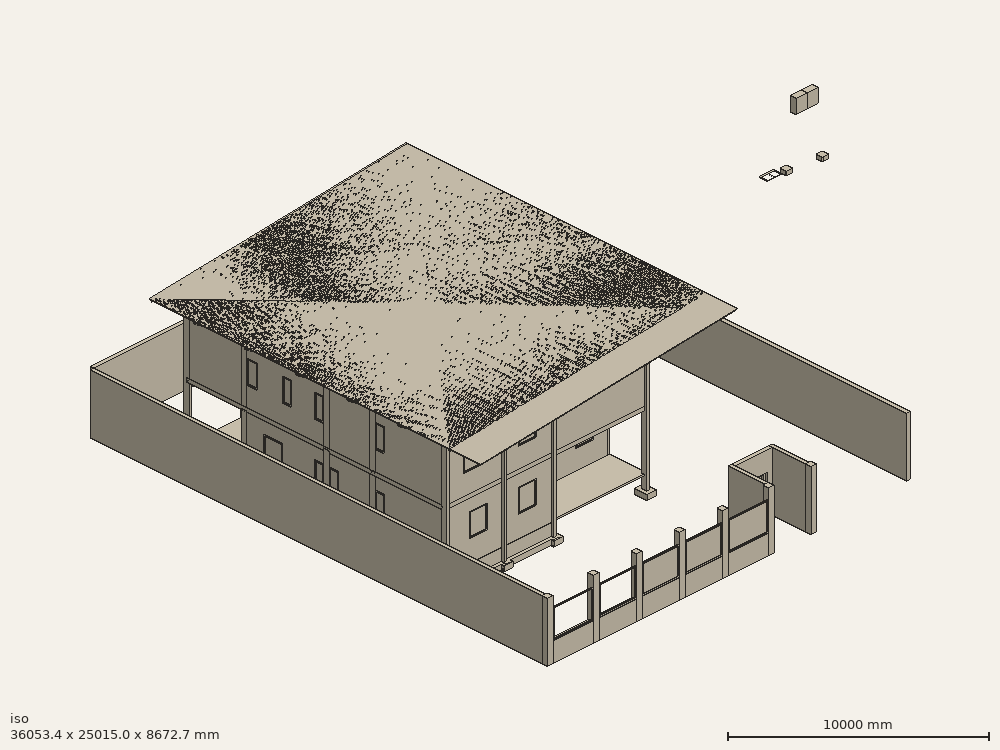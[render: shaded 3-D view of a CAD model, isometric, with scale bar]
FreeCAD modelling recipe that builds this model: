
FCSTD DOCUMENT  (FreeCAD 0.16R5937 (Git))
Label: Dyimba Construction Document test
License: All rights reserved
LicenseURL: http://en.wikipedia.org/wiki/All_rights_reserved
objects: Part::Part2DObjectPython×1218, App::FeaturePython×485, Part::FeaturePython×369, Part::Feature×198, App::DocumentObjectGroup×80, Part::Extrusion×48, Sketcher::SketchObject×44, Drawing::FeatureViewPython×33, App::Annotation×30, Part::Cut×9, Part::MultiFuse×5, Image::ImagePlane×1, App::DocumentObjectGroupPython×1, Drawing::FeaturePage×1
note: 1904 computed .brp shape members not serialized (recipe doc carries the construction recipe); baked Part::Feature solids carry a one-line shape summary decoded from their .brp

FEATURE [App::FeaturePython] Axes  # WARN: FeaturePython — macro-defined, semantics opaque (R4)
  Angles = [0,0,0,0,0]
  Distances = [70,3100,1350,1350,5050]
  Length = 17000
FEATURE [App::FeaturePython] Axes001  # WARN: FeaturePython — macro-defined, semantics opaque (R4)
  Angles = [0,0,0,0,0]
  Distances = [0,3130,4470,2500,3900]
  Length = 15000
  Placement = pos=(-2000,16000,0) rot=(0,0,-1;1.5708rad)
FEATURE [Part::FeaturePython] Structure  # WARN: FeaturePython — macro-defined, semantics opaque (R4)
  Height = 6700
  Length = 150
  MoveWithHost = false
  Nodes = (2) [(0,0,0),(0,0,6700)]
  Normal = (0,0,0)
  Placement = pos=(70,16000,-700) rot=(0,0,1;0rad)
  Role = 1
  Width = 300
FEATURE [Part::FeaturePython] Structure001  # WARN: FeaturePython — macro-defined, semantics opaque (R4)
  Height = 6700
  Length = 150
  MoveWithHost = false
  Nodes = (2) [(0,0,0),(0,0,6700)]
  Normal = (0,0,0)
  Placement = pos=(3170,16000,-700) rot=(0,0,1;0rad)
  Role = 1
  Width = 300
FEATURE [Part::FeaturePython] Structure002  # WARN: FeaturePython — macro-defined, semantics opaque (R4)
  Height = 6700
  Length = 150
  MoveWithHost = false
  Nodes = (2) [(0,0,0),(0,0,6700)]
  Normal = (0,0,0)
  Placement = pos=(5870,16000,-700) rot=(0,0,1;0rad)
  Role = 1
  Width = 300
FEATURE [Part::FeaturePython] Structure003  # WARN: FeaturePython — macro-defined, semantics opaque (R4)
  Height = 6700
  Length = 150
  MoveWithHost = false
  Nodes = (2) [(0,0,0),(0,0,6700)]
  Normal = (0,0,0)
  Placement = pos=(10920,16000,-700) rot=(0,0,1;0rad)
  Role = 1
  Width = 300
FEATURE [Part::FeaturePython] Structure016  # WARN: FeaturePython — macro-defined, semantics opaque (R4)
  Height = 6700
  Length = 150
  MoveWithHost = false
  Nodes = (2) [(0,0,0),(0,0,6700)]
  Normal = (0,0,0)
  Placement = pos=(70,5900,-700) rot=(0,0,1;0rad)
  Role = 1
  Width = 300
FEATURE [Part::FeaturePython] Structure019  # WARN: FeaturePython — macro-defined, semantics opaque (R4)
  Height = 6700
  Length = 150
  MoveWithHost = false
  Nodes = (2) [(0,0,0),(0,0,6700)]
  Normal = (0,0,0)
  Placement = pos=(10920,5900,-700) rot=(0,0,1;0rad)
  Role = 1
  Width = 300
FEATURE [Part::FeaturePython] Structure018  # WARN: FeaturePython — macro-defined, semantics opaque (R4)
  Height = 6700
  Length = 150
  MoveWithHost = false
  Nodes = (2) [(0,0,0),(0,0,6700)]
  Normal = (0,0,0)
  Placement = pos=(5870,5900,-700) rot=(0,0,1;0rad)
  Role = 1
  Width = 300
FEATURE [Part::FeaturePython] Structure020  # WARN: FeaturePython — macro-defined, semantics opaque (R4)
  Height = 6700
  Length = 150
  MoveWithHost = false
  Nodes = (2) [(0,0,0),(0,0,6700)]
  Normal = (0,0,0)
  Placement = pos=(70,2000,-700) rot=(0,0,1;0rad)
  Role = 1
  Width = 300
FEATURE [Part::FeaturePython] Structure021  # WARN: FeaturePython — macro-defined, semantics opaque (R4)
  Height = 6700
  Length = 150
  MoveWithHost = false
  Nodes = (2) [(0,0,0),(0,0,6700)]
  Normal = (0,0,0)
  Placement = pos=(10920,2000,-700) rot=(0,0,1;0rad)
  Role = 1
  Width = 300
FEATURE [Part::FeaturePython] Structure022  # WARN: FeaturePython — macro-defined, semantics opaque (R4)
  Height = 6700
  Length = 150
  MoveWithHost = false
  Nodes = (2) [(0,0,0),(0,0,6700)]
  Normal = (0,0,0)
  Placement = pos=(5870,2000,-700) rot=(0,0,1;0rad)
  Role = 1
  Width = 300
FEATURE [Part::FeaturePython] Structure023  # WARN: FeaturePython — macro-defined, semantics opaque (R4)
  Height = 6700
  Length = 150
  MoveWithHost = false
  Nodes = (2) [(0,0,0),(0,0,6700)]
  Normal = (0,0,0)
  Placement = pos=(3170,2000,-700) rot=(0,0,1;0rad)
  Role = 1
  Width = 300
FEATURE [Part::FeaturePython] Structure024  # WARN: FeaturePython — macro-defined, semantics opaque (R4)
  Height = 6700
  Length = 150
  MoveWithHost = false
  Nodes = (2) [(0,0,0),(0,0,6700)]
  Normal = (0,0,0)
  Placement = pos=(70,8400,-700) rot=(0,0,1;0rad)
  Role = 1
  Width = 300
FEATURE [Part::FeaturePython] Structure025  # WARN: FeaturePython — macro-defined, semantics opaque (R4)
  Height = 6700
  Length = 150
  MoveWithHost = false
  Nodes = (2) [(0,0,0),(0,0,6700)]
  Normal = (0,0,0)
  Placement = pos=(10920,8400,-700) rot=(0,0,1;0rad)
  Role = 1
  Width = 300
FEATURE [Part::FeaturePython] Structure026  # WARN: FeaturePython — macro-defined, semantics opaque (R4)
  Height = 6700
  Length = 150
  MoveWithHost = false
  Nodes = (2) [(0,0,0),(0,0,6700)]
  Normal = (0,0,0)
  Placement = pos=(5870,8400,-700) rot=(0,0,1;0rad)
  Role = 1
  Width = 300
FEATURE [Part::FeaturePython] Structure027  # WARN: FeaturePython — macro-defined, semantics opaque (R4)
  Height = 6700
  Length = 150
  MoveWithHost = false
  Nodes = (2) [(0,0,0),(0,0,6700)]
  Normal = (0,0,0)
  Placement = pos=(4520,8400,-700) rot=(0,0,1;0rad)
  Role = 1
  Width = 300
FEATURE [Part::FeaturePython] Structure028  # WARN: FeaturePython — macro-defined, semantics opaque (R4)
  Height = 6700
  Length = 150
  MoveWithHost = false
  Nodes = (2) [(0,0,0),(0,0,6700)]
  Normal = (0,0,0)
  Placement = pos=(70,12870,-700) rot=(0,0,1;0rad)
  Role = 1
  Width = 300
FEATURE [Part::FeaturePython] Structure029  # WARN: FeaturePython — macro-defined, semantics opaque (R4)
  Height = 6700
  Length = 150
  MoveWithHost = false
  Nodes = (2) [(0,0,0),(0,0,6700)]
  Normal = (0,0,0)
  Placement = pos=(10920,12870,-700) rot=(0,0,1;0rad)
  Role = 1
  Width = 300
FEATURE [Part::FeaturePython] Structure030  # WARN: FeaturePython — macro-defined, semantics opaque (R4)
  Height = 6700
  Length = 150
  MoveWithHost = false
  Nodes = (2) [(0,0,0),(0,0,6700)]
  Normal = (0,0,0)
  Placement = pos=(5870,12870,-700) rot=(0,0,1;0rad)
  Role = 1
  Width = 300
FEATURE [Part::FeaturePython] Structure031  # WARN: FeaturePython — macro-defined, semantics opaque (R4)
  Height = 6700
  Length = 150
  MoveWithHost = false
  Nodes = (2) [(0,0,0),(0,0,6700)]
  Normal = (0,0,0)
  Placement = pos=(4520,12870,-700) rot=(0,0,1;0rad)
  Role = 1
  Width = 300
FEATURE [App::DocumentObjectGroup] Group  label="A-Columns"
  Group = -> [Structure,Structure001,Structure002,Structure003,Structure016,Structure018,Structure019,Structure020,Structure021,Structure022,Structure023,Structure024,Structure025,Structure026,Structure027,Structure028,Structure029,Structure030,Structure031]
FEATURE [Part::Part2DObjectPython] Line  # Draft 2D object (typed FeaturePython)
  ChamferSize = 0
  Closed = false
  End = (10845,16000,0)
  FilletRadius = 0
  Length = 4900
  MakeFace = true
  Points = (2) [(5945,16000,0),(10845,16000,0)]
  Start = (5945,16000,0)
FEATURE [Part::Part2DObjectPython] Line001  # Draft 2D object (typed FeaturePython)
  ChamferSize = 0
  Closed = false
  End = (5795,16000,-100)
  FilletRadius = 0
  Length = 2550
  MakeFace = true
  Placement = pos=(0,0,-100) rot=(0,0,1;0rad)
  Points = (2) [(3245,16000,0),(5795,16000,0)]
  Start = (3245,16000,-100)
FEATURE [Part::Part2DObjectPython] Line002  # Draft 2D object (typed FeaturePython)
  ChamferSize = 0
  Closed = false
  End = (10920,15850,0)
  FilletRadius = 0
  Length = 2830
  MakeFace = true
  Points = (2) [(10920,13020,0),(10920,15850,0)]
  Start = (10920,13020,0)
FEATURE [Part::Part2DObjectPython] Line003  # Draft 2D object (typed FeaturePython)
  ChamferSize = 0
  Closed = false
  End = (10920,12720,0)
  FilletRadius = 0
  Length = 4170
  MakeFace = true
  Points = (2) [(10920,8550,0),(10920,12720,0)]
  Start = (10920,8550,0)
FEATURE [Part::Part2DObjectPython] Line005  # Draft 2D object (typed FeaturePython)
  ChamferSize = 0
  Closed = false
  End = (10920,5750,-100)
  FilletRadius = 0
  Length = 1750.39
  MakeFace = true
  Placement = pos=(0,0,-100) rot=(0,0,1;0rad)
  Points = (2) [(10920,3999.61,0),(10920,5750,0)]
  Start = (10920,3999.61,-100)
FEATURE [Part::Part2DObjectPython] Line007  # Draft 2D object (typed FeaturePython)
  ChamferSize = 0
  Closed = false
  End = (3095,2000,0)
  FilletRadius = 0
  Length = 2950
  MakeFace = true
  Points = (2) [(145,2000,0),(3095,2000,0)]
  Start = (145,2000,0)
FEATURE [Part::Part2DObjectPython] Line008  # Draft 2D object (typed FeaturePython)
  ChamferSize = 0
  Closed = false
  End = (3170,2150,-100)
  FilletRadius = 0
  Length = 3600
  MakeFace = true
  Placement = pos=(0,0,-100) rot=(0,0,1;0rad)
  Points = (2) [(3170,5750,0),(3170,2150,0)]
  Start = (3170,5750,-100)
FEATURE [Part::Part2DObjectPython] Line009  # Draft 2D object (typed FeaturePython)
  ChamferSize = 0
  Closed = false
  End = (5870,2150,3000)
  FilletRadius = 0
  Length = 3600
  MakeFace = true
  Points = (2) [(5870,5750,3000),(5870,2150,3000)]
  Start = (5870,5750,3000)
FEATURE [Part::Part2DObjectPython] Line010  # Draft 2D object (typed FeaturePython)
  ChamferSize = 0
  Closed = false
  End = (3245,2000,3000)
  FilletRadius = 0
  Length = 2550
  MakeFace = true
  Placement = pos=(0,-1000,0) rot=(0,0,1;0rad)
  Points = (2) [(5795,3000,3000),(3245,3000,3000)]
  Start = (5795,2000,3000)
FEATURE [Part::Part2DObjectPython] Line011  # Draft 2D object (typed FeaturePython)
  ChamferSize = 0
  Closed = false
  End = (10845,2000,-100)
  FilletRadius = 0
  Length = 4900
  MakeFace = true
  Placement = pos=(0,0,-100) rot=(0,0,1;0rad)
  Points = (2) [(5945,2000,0),(10845,2000,0)]
  Start = (5945,2000,-100)
FEATURE [Part::Part2DObjectPython] Line013  # Draft 2D object (typed FeaturePython)
  ChamferSize = 0
  Closed = false
  End = (70,5750,0)
  FilletRadius = 0
  Length = 3600
  MakeFace = true
  Placement = pos=(-10850,0,-3172.19) rot=(0,0,1;0rad)
  Points = (2) [(10920,2150,3172.19),(10920,5750,3172.19)]
  Start = (70,2150,0)
FEATURE [Part::Part2DObjectPython] Line014  # Draft 2D object (typed FeaturePython)
  ChamferSize = 0
  Closed = false
  End = (70,6050,0)
  FilletRadius = 0
  Length = 2200
  MakeFace = true
  Placement = pos=(-10850,0,-3172.19) rot=(0,0,1;0rad)
  Points = (2) [(10920,8250,3172.19),(10920,6050,3172.19)]
  Start = (70,8250,0)
FEATURE [Part::Part2DObjectPython] Line015  # Draft 2D object (typed FeaturePython)
  ChamferSize = 0
  Closed = false
  End = (70,12720,0)
  FilletRadius = 0
  Length = 4170
  MakeFace = true
  Placement = pos=(-10850,0,-3172.19) rot=(0,0,1;0rad)
  Points = (2) [(10920,8550,3172.19),(10920,12720,3172.19)]
  Start = (70,8550,0)
FEATURE [Part::Part2DObjectPython] Line016  # Draft 2D object (typed FeaturePython)
  ChamferSize = 0
  Closed = false
  End = (10845,11850,3000)
  FilletRadius = 0
  Length = 3550
  MakeFace = true
  Placement = pos=(0,-1020,3000) rot=(0,0,1;0rad)
  Points = (2) [(7295,12870,0),(10845,12870,0)]
  Start = (7295,11850,3000)
FEATURE [Part::Part2DObjectPython] Line017  # Draft 2D object (typed FeaturePython)
  ChamferSize = 0
  Closed = false
  End = (4595,12870,-100)
  FilletRadius = 0
  Length = 1200
  MakeFace = true
  Placement = pos=(0,0,-100) rot=(0,0,1;0rad)
  Points = (2) [(5795,12870,0),(4595,12870,0)]
  Start = (5795,12870,-100)
FEATURE [Part::Part2DObjectPython] Line018  # Draft 2D object (typed FeaturePython)
  ChamferSize = 0
  Closed = false
  End = (4520,15350,3000)
  FilletRadius = 0
  Length = 500
  MakeFace = true
  Points = (2) [(4520,15850,3000),(4520,15350,3000)]
  Start = (4520,15850,3000)
FEATURE [Part::Part2DObjectPython] Line019  # Draft 2D object (typed FeaturePython)
  ChamferSize = 0
  Closed = false
  End = (145,12000,3000)
  FilletRadius = 0
  Length = 4300
  MakeFace = true
  Placement = pos=(0,-870,3000) rot=(0,0,1;0rad)
  Points = (2) [(4445,12870,0),(145,12870,0)]
  Start = (4445,12000,3000)
FEATURE [Part::Part2DObjectPython] Line022  # Draft 2D object (typed FeaturePython)
  ChamferSize = 0
  Closed = false
  End = (145,9600,0)
  FilletRadius = 0
  Length = 4300
  MakeFace = true
  Placement = pos=(0,50,0) rot=(0,0,1;0rad)
  Points = (2) [(4445,9550,0),(145,9550,0)]
  Start = (4445,9600,0)
FEATURE [Part::FeaturePython] Wall004  # WARN: FeaturePython — macro-defined, semantics opaque (R4)
  Align = 2
  Base = -> Line005
  Face = 0
  Height = 2900
  Length = 0
  MoveWithHost = false
  Normal = (0,0,0)
  Role = 0
  Width = 150
FEATURE [Part::FeaturePython] Wall013  # WARN: FeaturePython — macro-defined, semantics opaque (R4)
  Align = 0
  Base = -> Line017
  Face = 0
  Height = 2800
  Length = 0
  MoveWithHost = false
  Normal = (0,0,0)
  Role = 0
  Width = 150
FEATURE [Part::FeaturePython] Wall015  # WARN: FeaturePython — macro-defined, semantics opaque (R4)
  Align = 0
  Base = -> Line001
  Face = 0
  Height = 2900
  Length = 0
  MoveWithHost = false
  Normal = (0,0,0)
  Role = 0
  Width = 150
FEATURE [Part::Part2DObjectPython] Line025  # Draft 2D object (typed FeaturePython)
  ChamferSize = 0
  Closed = false
  End = (8945,13020,-100)
  FilletRadius = 0
  Length = 2830
  MakeFace = true
  Placement = pos=(0,0,2900) rot=(0,0,1;0rad)
  Points = (2) [(8945,15850,-3000),(8945,13020,-3000)]
  Start = (8945,15850,-100)
FEATURE [Part::FeaturePython] Wall027  # WARN: FeaturePython — macro-defined, semantics opaque (R4)
  Align = 2
  Base = -> Line014
  Face = 0
  Height = 2800
  Length = 0
  MoveWithHost = false
  Normal = (0,0,0)
  Placement = pos=(0,0,3000) rot=(0,0,1;0rad)
  Role = 0
  Width = 150
FEATURE [Part::FeaturePython] Wall028  # WARN: FeaturePython — macro-defined, semantics opaque (R4)
  Align = 2
  Base = -> Line009
  Face = 0
  Height = 2800
  Length = 0
  MoveWithHost = false
  Normal = (0,0,0)
  Role = 0
  Width = 150
FEATURE [Part::FeaturePython] Wall033  # WARN: FeaturePython — macro-defined, semantics opaque (R4)
  Align = 2
  Base = -> Line018
  Face = 0
  Height = 2800
  Length = 0
  MoveWithHost = false
  Normal = (0,0,0)
  Role = 0
  Width = 150
FEATURE [Part::FeaturePython] Wall034  # WARN: FeaturePython — macro-defined, semantics opaque (R4)
  Align = 0
  Base = -> Line022
  Face = 0
  Height = 2800
  Length = 0
  MoveWithHost = false
  Normal = (0,0,0)
  Placement = pos=(0,0,3000) rot=(0,0,1;0rad)
  Role = 0
  Width = 150
FEATURE [Part::FeaturePython] Wall035  # WARN: FeaturePython — macro-defined, semantics opaque (R4)
  Align = 0
  Base = -> Line016
  Face = 0
  Height = 2800
  Length = 0
  MoveWithHost = false
  Normal = (0,0,0)
  Role = 0
  Width = 150
FEATURE [Part::Part2DObjectPython] Line027  # Draft 2D object (typed FeaturePython)
  ChamferSize = 0
  Closed = false
  End = (5795,5900,3000)
  FilletRadius = 0
  Length = 1200
  MakeFace = true
  Points = (2) [(4595,5900,3000),(5795,5900,3000)]
  Start = (4595,5900,3000)
FEATURE [Part::FeaturePython] Wall045  # WARN: FeaturePython — macro-defined, semantics opaque (R4)
  Align = 1
  Base = -> Line027
  Face = 0
  Height = 2800
  Length = 0
  MoveWithHost = false
  Normal = (0,0,0)
  Role = 0
  Width = 150
FEATURE [Part::Part2DObjectPython] Line028  # Draft 2D object (typed FeaturePython)
  ChamferSize = 0
  Closed = false
  End = (10845,5900,3000)
  FilletRadius = 0
  Length = 4900
  MakeFace = true
  Points = (2) [(5945,5900,3000),(10845,5900,3000)]
  Start = (5945,5900,3000)
FEATURE [Part::Part2DObjectPython] Line029  # Draft 2D object (typed FeaturePython)
  ChamferSize = 0
  Closed = false
  End = (70,13020,3000)
  FilletRadius = 0
  Length = 2830
  MakeFace = true
  Points = (2) [(70,15850,3000),(70,13020,3000)]
  Start = (70,15850,3000)
FEATURE [Part::Part2DObjectPython] Line030  # Draft 2D object (typed FeaturePython)
  ChamferSize = 0
  Closed = false
  End = (145,16000,3000)
  FilletRadius = 0
  Length = 2950
  MakeFace = true
  Points = (2) [(3095,16000,3000),(145,16000,3000)]
  Start = (3095,16000,3000)
FEATURE [Part::FeaturePython] Wall048  # WARN: FeaturePython — macro-defined, semantics opaque (R4)
  Align = 2
  Base = -> Line029
  Face = 0
  Height = 2800
  Length = 0
  MoveWithHost = false
  Normal = (0,0,0)
  Role = 0
  Width = 150
FEATURE [Part::Part2DObjectPython] Line031  # Draft 2D object (typed FeaturePython)
  ChamferSize = 0
  Closed = false
  End = (3245,16000,3000)
  FilletRadius = 0
  Length = 2550
  MakeFace = true
  Points = (2) [(5795,16000,3000),(3245,16000,3000)]
  Start = (5795,16000,3000)
FEATURE [Part::Part2DObjectPython] Line039  # Draft 2D object (typed FeaturePython)
  ChamferSize = 0
  Closed = false
  End = (10845,10200,3000)
  FilletRadius = 0
  Length = 3550
  MakeFace = true
  Points = (2) [(7295,10200,3000),(10845,10200,3000)]
  Start = (7295,10200,3000)
FEATURE [Part::FeaturePython] Wall051  # WARN: FeaturePython — macro-defined, semantics opaque (R4)
  Align = 0
  Base = -> Line039
  Face = 0
  Height = 2800
  Length = 0
  MoveWithHost = false
  Normal = (0,0,0)
  Role = 0
  Width = 150
FEATURE [Part::Part2DObjectPython] Line040  # Draft 2D object (typed FeaturePython)
  ChamferSize = 0
  Closed = false
  End = (7145,6050,3000)
  FilletRadius = 0
  Length = 9800
  MakeFace = true
  Points = (2) [(7145,15850,3000),(7145,6050,3000)]
  Start = (7145,15850,3000)
FEATURE [Part::Part2DObjectPython] Line041  # Draft 2D object (typed FeaturePython)
  ChamferSize = 0
  Closed = false
  End = (4593.51,8250,3000)
  FilletRadius = 0
  Length = 1201.49
  MakeFace = true
  Points = (2) [(5795,8250,3000),(4593.51,8250,3000)]
  Start = (5795,8250,3000)
FEATURE [Part::Part2DObjectPython] Line042  # Draft 2D object (typed FeaturePython)
  ChamferSize = 0
  Closed = false
  End = (5945,12720,3000)
  FilletRadius = 0
  Length = 4170
  MakeFace = true
  Points = (2) [(5945,8550,3000),(5945,12720,3000)]
  Start = (5945,8550,3000)
FEATURE [Part::FeaturePython] Wall053  # WARN: FeaturePython — macro-defined, semantics opaque (R4)
  Align = 1
  Base = -> Line042
  Face = 0
  Height = 1000
  Length = 0
  MoveWithHost = false
  Normal = (0,0,0)
  Role = 0
  Width = 150
FEATURE [Part::FeaturePython] Wall054  # WARN: FeaturePython — macro-defined, semantics opaque (R4)
  Align = 0
  Base = -> Line041
  Face = 0
  Height = 1000
  Length = 0
  MoveWithHost = false
  Normal = (0,0,0)
  Role = 0
  Width = 150
FEATURE [Part::Part2DObjectPython] Line043  # Draft 2D object (typed FeaturePython)
  ChamferSize = 0
  Closed = false
  End = (2380,4069.81,3000)
  FilletRadius = 0
  Length = 4506.35
  MakeFace = true
  Placement = pos=(-4915,0.305262,0.0001461) rot=(0,0,1;0rad)
  Points = (2) [(7295,8575.86,3000),(7295,4069.51,3000)]
  Start = (2380,8576.17,3000)
FEATURE [Part::Part2DObjectPython] Line047  # Draft 2D object (typed FeaturePython)
  ChamferSize = 0
  Closed = false
  End = (7295,8250,3000)
  FilletRadius = 0
  Length = 600
  MakeFace = true
  Points = (2) [(7895,8250,3000),(7295,8250,3000)]
  Start = (7895,8250,3000)
FEATURE [Part::FeaturePython] Wall055  # WARN: FeaturePython — macro-defined, semantics opaque (R4)
  Align = 0
  Base = -> Line047
  Face = 0
  Height = 2800
  Length = 0
  MoveWithHost = false
  Normal = (0,0,0)
  Role = 0
  Width = 150
FEATURE [Part::Part2DObjectPython] Line048  # Draft 2D object (typed FeaturePython)
  ChamferSize = 0
  Closed = false
  End = (7447.32,11850.3,3000)
  FilletRadius = 0
  Length = 3155.03
  MakeFace = true
  Placement = pos=(-4915,0.305262,0.0001461) rot=(0,0,1;0rad)
  Points = (2) [(9207.29,11850,3000),(12362.3,11850,3000)]
  Start = (4292.29,11850.3,3000)
FEATURE [Part::Part2DObjectPython] Line049  # Draft 2D object (typed FeaturePython)
  ChamferSize = 0
  Closed = false
  End = (8569.45,15850.3,3000)
  FilletRadius = 0
  Length = 4404.97
  MakeFace = true
  Placement = pos=(-4915,0.305262,0.0001461) rot=(0,0,1;0rad)
  Points = (2) [(9079.47,15850,3000),(13484.4,15850,3000)]
  Start = (4164.47,15850.3,3000)
FEATURE [Part::Part2DObjectPython] Line050  # Draft 2D object (typed FeaturePython)
  ChamferSize = 0
  Closed = false
  End = (8569.45,13650.3,3000)
  FilletRadius = 0
  Length = 4404.97
  MakeFace = true
  Placement = pos=(-4915,0.305262,0.0001461) rot=(0,0,1;0rad)
  Points = (2) [(9079.47,13650,3000),(13484.4,13650,3000)]
  Start = (4164.47,13650.3,3000)
FEATURE [Part::Part2DObjectPython] Line023  # Draft 2D object (typed FeaturePython)
  ChamferSize = 0
  Closed = false
  End = (4520,12720,3000)
  FilletRadius = 0
  Length = 4170
  MakeFace = true
  Points = (2) [(4520,8550,3000),(4520,12720,3000)]
  Start = (4520,8550,3000)
FEATURE [Part::FeaturePython] Wall029  # WARN: FeaturePython — macro-defined, semantics opaque (R4)
  Align = 2
  Base = -> Line023
  Face = 0
  Height = 2800
  Length = 0
  MoveWithHost = false
  Normal = (0,0,0)
  Role = 0
  Width = 150
FEATURE [Part::Part2DObjectPython] Line052  # Draft 2D object (typed FeaturePython)
  ChamferSize = 0
  Closed = false
  End = (4595,8250,3000)
  FilletRadius = 0
  Length = 2350
  MakeFace = true
  Points = (2) [(4595,5900,3000),(4595,8250,3000)]
  Start = (4595,5900,3000)
FEATURE [Part::Part2DObjectPython] Line057  # Draft 2D object (typed FeaturePython)
  ChamferSize = 0
  Closed = false
  End = (-6976.01,12000.3,3000)
  FilletRadius = 0
  Length = 3334.15
  MakeFace = true
  Placement = pos=(-4915,0.305262,0.0001461) rot=(0,0,1;0rad)
  Points = (2) [(1273.13,12000,3000),(-2061.02,12000,3000)]
  Start = (-3641.87,12000.3,3000)
FEATURE [Part::Part2DObjectPython] Line058  # Draft 2D object (typed FeaturePython)
  ChamferSize = 0
  Closed = false
  End = (-6976.01,11400.3,3000)
  FilletRadius = 0
  Length = 7145.96
  MakeFace = true
  Placement = pos=(-4915,0.305262,0.0001461) rot=(0,0,1;0rad)
  Points = (2) [(5084.95,11400,3000),(-2061.02,11400,3000)]
  Start = (169.949,11400.3,3000)
FEATURE [Part::Part2DObjectPython] Line059  # Draft 2D object (typed FeaturePython)
  ChamferSize = 0
  Closed = false
  End = (3170,12000,3000)
  FilletRadius = 0
  Length = 600
  MakeFace = true
  Points = (2) [(3170,11400,3000),(3170,12000,3000)]
  Start = (3170,11400,3000)
FEATURE [Part::FeaturePython] Wall058  # WARN: FeaturePython — macro-defined, semantics opaque (R4)
  Align = 1
  Base = -> Line059
  Face = 0
  Height = 2800
  Length = 0
  MoveWithHost = false
  Normal = (0,0,0)
  Role = 0
  Width = 150
FEATURE [Part::Part2DObjectPython] Line060  # Draft 2D object (typed FeaturePython)
  ChamferSize = 0
  Closed = false
  End = (10845,12870,-100)
  FilletRadius = 0
  Length = 4900
  MakeFace = true
  Placement = pos=(0,0,-100) rot=(0,0,1;0rad)
  Points = (2) [(5945,12870,0),(10845,12870,0)]
  Start = (5945,12870,-100)
FEATURE [Part::Part2DObjectPython] Line061  # Draft 2D object (typed FeaturePython)
  ChamferSize = 0
  Closed = false
  End = (5930,16814.6,0.0001461)
  FilletRadius = 0
  Length = 2358.9
  MakeFace = true
  Placement = pos=(-4915,0.305262,0.0001461) rot=(0,0,1;0rad)
  Points = (2) [(10845,14455.4,0),(10845,16814.3,0)]
  Start = (5930,14455.7,0.0001461)
FEATURE [Part::Part2DObjectPython] Line062  # Draft 2D object (typed FeaturePython)
  ChamferSize = 0
  Closed = false
  End = (4520,15850,-100)
  FilletRadius = 0
  Length = 2830
  MakeFace = true
  Placement = pos=(0,0,-100) rot=(0,0,1;0rad)
  Points = (2) [(4520,13020,0),(4520,15850,0)]
  Start = (4520,13020,-100)
FEATURE [Part::Part2DObjectPython] Line063  # Draft 2D object (typed FeaturePython)
  ChamferSize = 0
  Closed = false
  End = (4520,12720,-100)
  FilletRadius = 0
  Length = 4170
  MakeFace = true
  Placement = pos=(0,0,-100) rot=(0,0,1;0rad)
  Points = (2) [(4520,8550,0),(4520,12720,0)]
  Start = (4520,8550,-100)
FEATURE [Part::FeaturePython] Wall062  # WARN: FeaturePython — macro-defined, semantics opaque (R4)
  Align = 2
  Base = -> Line063
  Face = 0
  Height = 2900
  Length = 0
  MoveWithHost = false
  Normal = (0,0,0)
  Role = 0
  Width = 150
FEATURE [Part::Part2DObjectPython] Line064  # Draft 2D object (typed FeaturePython)
  ChamferSize = 0
  Closed = false
  End = (3170,9600,-100)
  FilletRadius = 0
  Length = 4850
  MakeFace = true
  Placement = pos=(0,0,-100) rot=(0,0,1;0rad)
  Points = (2) [(3170,4750,0),(3170,9600,0)]
  Start = (3170,4750,-100)
FEATURE [Part::Part2DObjectPython] Line065  # Draft 2D object (typed FeaturePython)
  ChamferSize = 0
  Closed = false
  End = (-6252.85,2150.31,0.0001461)
  FilletRadius = 0
  Length = 2264.08
  MakeFace = true
  Placement = pos=(-4915,0.305262,0.0001461) rot=(0,0,1;0rad)
  Points = (2) [(926.23,2150,0),(-1337.85,2150,0)]
  Start = (-3988.77,2150.31,0.0001461)
FEATURE [Part::Part2DObjectPython] Line066  # Draft 2D object (typed FeaturePython)
  ChamferSize = 0
  Closed = false
  End = (-6252.85,6500.31,0.0001461)
  FilletRadius = 0
  Length = 2264.08
  MakeFace = true
  Placement = pos=(-4915,0.305262,0.0001461) rot=(0,0,1;0rad)
  Points = (2) [(926.23,6500,0),(-1337.85,6500,0)]
  Start = (-3988.77,6500.31,0.0001461)
FEATURE [Part::Part2DObjectPython] Line067  # Draft 2D object (typed FeaturePython)
  ChamferSize = 0
  Closed = false
  End = (3095,6500,-100)
  FilletRadius = 0
  Length = 2950
  MakeFace = true
  Placement = pos=(0,0,-100) rot=(0,0,1;0rad)
  Points = (2) [(145,6500,0),(3095,6500,0)]
  Start = (145,6500,-100)
FEATURE [Part::Part2DObjectPython] Line068  # Draft 2D object (typed FeaturePython)
  ChamferSize = 0
  Closed = false
  End = (3095,8250,-100)
  FilletRadius = 0
  Length = 2950
  MakeFace = true
  Placement = pos=(0,0,-100) rot=(0,0,1;0rad)
  Points = (2) [(145,8250,0),(3095,8250,0)]
  Start = (145,8250,-100)
FEATURE [Part::FeaturePython] Wall065  # WARN: FeaturePython — macro-defined, semantics opaque (R4)
  Align = 1
  Base = -> Line068
  Face = 0
  Height = 2900
  Length = 0
  MoveWithHost = false
  Normal = (0,0,0)
  Role = 0
  Width = 150
FEATURE [Part::Part2DObjectPython] Line069  # Draft 2D object (typed FeaturePython)
  ChamferSize = 0
  Closed = false
  End = (-6633.63,8400.31,0.0001461)
  FilletRadius = 0
  Length = 3259.04
  MakeFace = true
  Placement = pos=(-4915,0.305262,0.0001461) rot=(0,0,1;0rad)
  Points = (2) [(1540.41,8400,0),(-1718.63,8400,0)]
  Start = (-3374.59,8400.31,0.0001461)
FEATURE [Part::Part2DObjectPython] Line070  # Draft 2D object (typed FeaturePython)
  ChamferSize = 0
  Closed = false
  End = (-6633.63,9600.31,0.0001461)
  FilletRadius = 0
  Length = 1863.63
  MakeFace = true
  Placement = pos=(-4915,0.305262,0.0001461) rot=(0,0,1;0rad)
  Points = (2) [(145,9600,0),(-1718.63,9600,0)]
  Start = (-4770,9600.31,0.0001461)
FEATURE [Part::Part2DObjectPython] Line071  # Draft 2D object (typed FeaturePython)
  ChamferSize = 0
  Closed = false
  End = (4445,9600,-100)
  FilletRadius = 0
  Length = 4300
  MakeFace = true
  Placement = pos=(0,0,-100) rot=(0,0,1;0rad)
  Points = (2) [(145,9600,0),(4445,9600,0)]
  Start = (145,9600,-100)
FEATURE [Part::Part2DObjectPython] Line072  # Draft 2D object (typed FeaturePython)
  ChamferSize = 0
  Closed = false
  End = (145,13020,-100)
  FilletRadius = 0
  Length = 4300
  MakeFace = true
  Placement = pos=(0,0,-100) rot=(0,0,1;0rad)
  Points = (2) [(4445,13020,0),(145,13020,0)]
  Start = (4445,13020,-100)
FEATURE [Part::Part2DObjectPython] Line073  # Draft 2D object (typed FeaturePython)
  ChamferSize = 0
  Closed = false
  End = (5795,3000,-100)
  FilletRadius = 0
  Length = 2550
  MakeFace = true
  Placement = pos=(0,0,-100) rot=(0,0,1;0rad)
  Points = (2) [(3245,3000,0),(5795,3000,0)]
  Start = (3245,3000,-100)
FEATURE [Part::Feature] Mesh
  Placement = pos=(5488.78,8171.39,0) rot=(0,0,1;0rad)
  shape: bbox 1200 x 4502 x 3000 mm, 40 faces (baked)
FEATURE [Part::Part2DObjectPython] Line074  # Draft 2D object (typed FeaturePython)
  ChamferSize = 0
  Closed = false
  End = (145,2000,-100)
  FilletRadius = 0
  Length = 2950
  MakeFace = true
  Placement = pos=(0,0,-100) rot=(0,0,1;0rad)
  Points = (2) [(3095,2000,0),(145,2000,0)]
  Start = (3095,2000,-100)
FEATURE [Part::FeaturePython] Stairs  # WARN: FeaturePython — macro-defined, semantics opaque (R4)
  Align = 0
  Base = -> Mesh
  BlondelRatio = 0
  Height = 3000
  Landings = 0
  Length = 4500
  MoveWithHost = false
  Nosing = 0
  NumberOfSteps = 0
  Placement = pos=(5488.78,8171.39,0) rot=(0,0,1;0rad)
  RiserHeight = 0
  Role = 0
  StringerWidth = 0
  Structure = 0
  StructureOffset = 0
  StructureThickness = 0
  TreadDepth = 0
  TreadThickness = 0
  Width = 1000
  Winders = 0
FEATURE [Part::Part2DObjectPython] Line076  # Draft 2D object (typed FeaturePython)
  ChamferSize = 0
  Closed = false
  End = (70,12720,-100)
  FilletRadius = 0
  Length = 4170
  MakeFace = true
  Placement = pos=(0,0,-100) rot=(0,0,1;0rad)
  Points = (2) [(70,8550,0.180568),(70,12720,0)]
  Start = (70,8550,-99.8194)
FEATURE [Part::Part2DObjectPython] Line077  # Draft 2D object (typed FeaturePython)
  ChamferSize = 0
  Closed = false
  End = (10920,15850,-100)
  FilletRadius = 0
  Length = 2830
  MakeFace = true
  Placement = pos=(0,0,-100) rot=(0,0,1;0rad)
  Points = (2) [(10920,13020,0),(10920,15850,0)]
  Start = (10920,13020,-100)
FEATURE [Part::Part2DObjectPython] Line078  # Draft 2D object (typed FeaturePython)
  ChamferSize = 0
  Closed = false
  End = (5870,5750,-100)
  FilletRadius = 0
  Length = 3600
  MakeFace = true
  Placement = pos=(0,0,-100) rot=(0,0,1;0rad)
  Points = (2) [(5870,2150,0),(5870,5750,0)]
  Start = (5870,2150,-100)
FEATURE [Part::Part2DObjectPython] Line079  # Draft 2D object (typed FeaturePython)
  ChamferSize = 0
  Closed = false
  End = (5945,16000,-100)
  FilletRadius = 0
  Length = 4900
  MakeFace = true
  Placement = pos=(0,0,-100) rot=(0,0,1;0rad)
  Points = (2) [(10845,16000,0),(5945,16000,0)]
  Start = (10845,16000,-100)
FEATURE [Part::Part2DObjectPython] Line080  # Draft 2D object (typed FeaturePython)
  ChamferSize = 0
  Closed = false
  End = (70,5750,-100)
  FilletRadius = 0
  Length = 3600
  MakeFace = true
  Placement = pos=(0,0,-100) rot=(0,0,1;0rad)
  Points = (2) [(70,2150,0),(70,5750,0)]
  Start = (70,2150,-100)
FEATURE [Part::Part2DObjectPython] Line081  # Draft 2D object (typed FeaturePython)
  ChamferSize = 0
  Closed = false
  End = (10920,12720,-100)
  FilletRadius = 0
  Length = 4170
  MakeFace = true
  Placement = pos=(0,0,-100) rot=(0,0,1;0rad)
  Points = (2) [(10920,8550,0),(10920,12720,0)]
  Start = (10920,8550,-100)
FEATURE [Part::Part2DObjectPython] Line082  # Draft 2D object (typed FeaturePython)
  ChamferSize = 0
  Closed = false
  End = (70,8250,-100)
  FilletRadius = 0
  Length = 2200
  MakeFace = true
  Placement = pos=(0,0,-100) rot=(0,0,1;0rad)
  Points = (2) [(70,6050,0),(70,8250,0)]
  Start = (70,6050,-100)
FEATURE [Part::Part2DObjectPython] Line083  # Draft 2D object (typed FeaturePython)
  ChamferSize = 0
  Closed = false
  End = (10845,11850,3000)
  FilletRadius = 0
  Length = 3550
  MakeFace = true
  Points = (2) [(7295,11850,3000),(10845,11850,3000)]
  Start = (7295,11850,3000)
FEATURE [Part::FeaturePython] Wall078  # WARN: FeaturePython — macro-defined, semantics opaque (R4)
  Align = 0
  Base = -> Line083
  Face = 0
  Height = 2800
  Length = 0
  MoveWithHost = false
  Normal = (0,0,0)
  Role = 0
  Width = 150
FEATURE [Part::Part2DObjectPython] Line084  # Draft 2D object (typed FeaturePython)
  ChamferSize = 0
  Closed = false
  End = (6080,-2593.43,0.0001461)
  FilletRadius = 0
  Length = 21220.1
  MakeFace = true
  Placement = pos=(-4915,0.305262,0.0001461) rot=(0,0,1;0rad)
  Points = (2) [(10995,18626.4,0),(10995,-2593.73,0)]
  Start = (6080,18626.7,0.0001461)
FEATURE [Part::Part2DObjectPython] Line085  # Draft 2D object (typed FeaturePython)
  ChamferSize = 0
  Closed = false
  End = (-4920,499.046,0.0001461)
  FilletRadius = 0
  Length = 18816.3
  MakeFace = true
  Placement = pos=(-4915,0.305262,0.0001461) rot=(0,0,1;0rad)
  Points = (2) [(-5,19315,0),(-5,498.741,0)]
  Start = (-4920,19315.3,0.0001461)
FEATURE [Part::Part2DObjectPython] Line086  # Draft 2D object (typed FeaturePython)
  ChamferSize = 0
  Closed = false
  End = (-5909.06,2000.31,0.0001461)
  FilletRadius = 0
  Length = 13580.1
  MakeFace = true
  Placement = pos=(-4915,0.305262,0.0001461) rot=(0,0,1;0rad)
  Points = (2) [(12586,2000,0),(-994.058,2000,0)]
  Start = (7671.03,2000.31,0.0001461)
FEATURE [Part::Part2DObjectPython] Line087  # Draft 2D object (typed FeaturePython)
  ChamferSize = 0
  Closed = false
  End = (8231.98,16000.3,0.0001461)
  FilletRadius = 0
  Length = 16540.6
  MakeFace = true
  Placement = pos=(-4915,0.305262,0.0001461) rot=(0,0,1;0rad)
  Points = (2) [(-3393.63,16000,0),(13147,16000,0)]
  Start = (-8308.63,16000.3,0.0001461)
FEATURE [Part::Part2DObjectPython] Rectangle  # Draft 2D object (typed FeaturePython)
  ChamferSize = 0
  FilletRadius = 0
  Height = -14000
  Length = -11000
  MakeFace = true
  Placement = pos=(10995,16000,3000) rot=(0,0,1;0rad)
FEATURE [Part::Extrusion] Extrusion001  label="level 2 slab"
  Base = -> Rectangle
  Dir = (0,0,-200)
  Solid = true
FEATURE [Part::Part2DObjectPython] Line088  # Draft 2D object (typed FeaturePython)
  ChamferSize = 0
  Closed = false
  End = (-4920,14435.3,0.0001461)
  FilletRadius = 0
  Length = 1565
  MakeFace = true
  Placement = pos=(-4915,0.305262,0.0001461) rot=(0,0,1;0rad)
  Points = (2) [(-5,16000,0),(-5,14435,0)]
  Start = (-4920,16000.3,0.0001461)
FEATURE [Part::Part2DObjectPython] Line089  # Draft 2D object (typed FeaturePython)
  ChamferSize = 0
  Closed = false
  End = (-6915,16000.3,0.0001461)
  FilletRadius = 0
  Length = 3620
  MakeFace = true
  Placement = pos=(-4915,0.305262,0.0001461) rot=(0,0,1;0rad)
  Points = (2) [(1620,16000,0),(-2000,16000,0)]
  Start = (-3295,16000.3,0.0001461)
FEATURE [Part::Part2DObjectPython] Line090  # Draft 2D object (typed FeaturePython)
  ChamferSize = 0
  Closed = false
  End = (880.002,20292.4,3000)
  FilletRadius = 0
  Length = 21199.3
  MakeFace = true
  Placement = pos=(-4915,0.305262,0.0001461) rot=(0,0,1;0rad)
  Points = (2) [(5795,-907.189,3000),(5795,20292.1,3000)]
  Start = (880.002,-906.884,3000)
FEATURE [Part::Part2DObjectPython] Line091  # Draft 2D object (typed FeaturePython)
  ChamferSize = 0
  Closed = false
  End = (-319.998,19324.2,3000)
  FilletRadius = 0
  Length = 18775.6
  MakeFace = true
  Placement = pos=(-4915,0.305262,0.0001461) rot=(0,0,1;0rad)
  Points = (2) [(4595,548.288,3000),(4595,19323.9,3000)]
  Start = (-319.998,548.593,3000)
FEATURE [Part::Part2DObjectPython] Line092  # Draft 2D object (typed FeaturePython)
  ChamferSize = 0
  Closed = false
  End = (-6405.68,13020.3,3000)
  FilletRadius = 0
  Length = 13409.8
  MakeFace = true
  Placement = pos=(-4915,0.305262,0.0001461) rot=(0,0,1;0rad)
  Points = (2) [(11919.1,13020,3000),(-1490.68,13020,3000)]
  Start = (7004.15,13020.3,3000)
FEATURE [Part::Part2DObjectPython] Line093  # Draft 2D object (typed FeaturePython)
  ChamferSize = 0
  Closed = false
  End = (7233.23,8400.31,3000)
  FilletRadius = 0
  Length = 15139.7
  MakeFace = true
  Placement = pos=(-4915,0.305262,0.0001461) rot=(0,0,1;0rad)
  Points = (2) [(-2991.47,8400,3000),(12148.2,8400,3000)]
  Start = (-7906.46,8400.31,3000)
FEATURE [Part::Part2DObjectPython] Rectangle002  # Draft 2D object (typed FeaturePython)
  ChamferSize = 0
  FilletRadius = 0
  Height = -4620
  Length = 1200
  MakeFace = true
  Placement = pos=(4595,13020,3000) rot=(0,0,1;0rad)
FEATURE [Part::Extrusion] Extrusion003
  Base = -> Rectangle002
  Dir = (0,0,-200)
  Solid = true
FEATURE [Part::Cut] Cut  label="Floor Slab level 2"
  Base = -> Extrusion001
  Tool = -> Extrusion003
FEATURE [Part::Part2DObjectPython] Line094  # Draft 2D object (typed FeaturePython)
  ChamferSize = 0
  Closed = false
  End = (10344.7,16000.3,6000)
  FilletRadius = 0
  Length = 18706.8
  MakeFace = true
  Placement = pos=(-4915,0.305262,0.0001461) rot=(0,0,1;0rad)
  Points = (2) [(-3447.1,16000,6000),(15259.7,16000,6000)]
  Start = (-8362.1,16000.3,6000)
FEATURE [Part::Part2DObjectPython] Line095  # Draft 2D object (typed FeaturePython)
  ChamferSize = 0
  Closed = false
  End = (10085,2000.31,6000)
  FilletRadius = 0
  Length = 18000
  MakeFace = true
  Placement = pos=(-4915,0.305262,0.0001461) rot=(0,0,1;0rad)
  Points = (2) [(-3000,2000,6000),(15000,2000,6000)]
  Start = (-7915,2000.31,6000)
FEATURE [Part::Part2DObjectPython] Line097  # Draft 2D object (typed FeaturePython)
  ChamferSize = 0
  Closed = false
  End = (6080,-1999.69,6000)
  FilletRadius = 0
  Length = 20565.3
  MakeFace = true
  Placement = pos=(-4915,0.305262,0.0001461) rot=(0,0,1;0rad)
  Points = (2) [(10995,18565.3,6000),(10995,-2000,6000)]
  Start = (6080,18565.6,6000)
FEATURE [Part::Part2DObjectPython] Line098  # Draft 2D object (typed FeaturePython)
  ChamferSize = 0
  Closed = false
  End = (11657.2,5900.31,6000)
  FilletRadius = 0
  Length = 17589.6
  MakeFace = true
  Placement = pos=(-4915,0.305262,0.0001461) rot=(0,0,1;0rad)
  Points = (2) [(-1017.37,5900,6000),(16572.2,5900,6000)]
  Start = (-5932.37,5900.31,6000)
FEATURE [Part::Part2DObjectPython] Line099  # Draft 2D object (typed FeaturePython)
  ChamferSize = 0
  Closed = false
  End = (1030,-647.56,6000)
  FilletRadius = 0
  Length = 7788.14
  MakeFace = true
  Placement = pos=(-4915,0.305262,0.0001461) rot=(0,0,1;0rad)
  Points = (2) [(5945,7140.27,6000),(5945,-647.865,6000)]
  Start = (1030,7140.58,6000)
FEATURE [Part::Part2DObjectPython] Line100  # Draft 2D object (typed FeaturePython)
  ChamferSize = 0
  Closed = false
  End = (11192.5,2150.31,6000)
  FilletRadius = 0
  Length = 14487.5
  MakeFace = true
  Placement = pos=(-4915,0.305262,0.0001461) rot=(0,0,1;0rad)
  Points = (2) [(1620,2150,6000),(16107.5,2150,6000)]
  Start = (-3295,2150.31,6000)
FEATURE [Part::Part2DObjectPython] Line101  # Draft 2D object (typed FeaturePython)
  ChamferSize = 0
  Closed = false
  End = (5930,-331.374,6000)
  FilletRadius = 0
  Length = 7481.68
  MakeFace = true
  Placement = pos=(-4915,0.305262,0.0001461) rot=(0,0,1;0rad)
  Points = (2) [(10845,7150,6000),(10845,-331.68,6000)]
  Start = (5930,7150.31,6000)
FEATURE [Part::Part2DObjectPython] Rectangle004  # Draft 2D object (typed FeaturePython)
  ChamferSize = 0
  FilletRadius = 0
  Height = -3750
  Length = 4900
  MakeFace = true
  Placement = pos=(5945,5900,6000) rot=(0,0,1;0rad)
FEATURE [Part::Extrusion] Extrusion005
  Base = -> Rectangle004
  Dir = (0,0,-200)
  Solid = true
FEATURE [Part::Part2DObjectPython] Line102  # Draft 2D object (typed FeaturePython)
  ChamferSize = 0
  Closed = false
  End = (-4920,18537.5,6000)
  FilletRadius = 0
  Length = 19254.8
  MakeFace = true
  Placement = pos=(-4915,0.305262,0.0001461) rot=(0,0,1;0rad)
  Points = (2) [(-5,-717.619,6000),(-5,18537.2,6000)]
  Start = (-4920,-717.314,6000)
FEATURE [Part::Part2DObjectPython] Rectangle005  # Draft 2D object (typed FeaturePython)
  ChamferSize = 0
  FilletRadius = 0
  Height = 14000
  Length = 11000
  MakeFace = true
  Placement = pos=(-5,2000,6000) rot=(0,0,1;0rad)
FEATURE [Part::Extrusion] Extrusion006
  Base = -> Rectangle005
  Dir = (0,0,-200)
  Solid = true
FEATURE [Part::Cut] Cut001  label="Roof Slab level 3"
  Base = -> Extrusion006
  Placement = pos=(0.0019531,0.000212966,-3.634e-05) rot=(0,0,1;0rad)
  Tool = -> Extrusion005
FEATURE [Part::Part2DObjectPython] Line105  # Draft 2D object (typed FeaturePython)
  ChamferSize = 0
  Closed = false
  End = (1030,2000.31,3000)
  FilletRadius = 0
  Length = 6000
  MakeFace = true
  Placement = pos=(-4915,0.305262,0.0001461) rot=(0,0,1;0rad)
  Points = (2) [(5945,2000,9000),(5945,2000,3000)]
  Start = (1030,2000.31,9000)
FEATURE [Part::Part2DObjectPython] Line106  # Draft 2D object (typed FeaturePython)
  ChamferSize = 0
  Closed = false
  End = (1030,2150.31,3000)
  FilletRadius = 0
  Length = 6000
  MakeFace = true
  Placement = pos=(-4915,0.305262,0.0001461) rot=(0,0,1;0rad)
  Points = (2) [(5945,2150,9000),(5945,2150,3000)]
  Start = (1030,2150.31,9000)
FEATURE [Part::Part2DObjectPython] Line107  # Draft 2D object (typed FeaturePython)
  ChamferSize = 0
  Closed = false
  End = (1030,1518.67,3000)
  FilletRadius = 0
  Length = 631.638
  MakeFace = true
  Placement = pos=(-4915,0.305262,0.0001461) rot=(0,0,1;0rad)
  Points = (2) [(5945,2150,3000),(5945,1518.36,3000)]
  Start = (1030,2150.31,3000)
FEATURE [Part::Part2DObjectPython] Line108  # Draft 2D object (typed FeaturePython)
  ChamferSize = 0
  Closed = false
  End = (1030,3000.31,4000)
  FilletRadius = 0
  Length = 1000
  MakeFace = true
  Placement = pos=(-4915,0.305262,0.0001461) rot=(0,0,1;0rad)
  Points = (2) [(5945,2000,4000),(5945,3000,4000)]
  Start = (1030,2000.31,4000)
FEATURE [Part::Part2DObjectPython] Line109  # Draft 2D object (typed FeaturePython)
  ChamferSize = 0
  Closed = false
  End = (1030,2150.31,3632.83)
  FilletRadius = 0
  Length = 150
  MakeFace = true
  Placement = pos=(-4915,0.305262,0.0001461) rot=(0,0,1;0rad)
  Points = (2) [(5945,2000,3632.83),(5945,2150,3632.83)]
  Start = (1030,2000.31,3632.83)
FEATURE [Part::Part2DObjectPython] Line110  # Draft 2D object (typed FeaturePython)
  ChamferSize = 0
  Closed = false
  End = (1030,2075.31,4000)
  FilletRadius = 0
  Length = 900
  MakeFace = true
  Placement = pos=(-4915,0.305262,0.0001461) rot=(0,0,1;0rad)
  Points = (2) [(5945,2075,3100),(5945,2075,4000)]
  Start = (1030,2075.31,3100)
FEATURE [Part::Part2DObjectPython] Line111  # Draft 2D object (typed FeaturePython)
  ChamferSize = 0
  Closed = false
  End = (1030,3000.31,3960)
  FilletRadius = 0
  Length = 1000
  MakeFace = true
  Placement = pos=(-4915,0.305262,0.0001461) rot=(0,0,1;0rad)
  Points = (2) [(5945,2000,3960),(5945,3000,3960)]
  Start = (1030,2000.31,3960)
FEATURE [Part::Part2DObjectPython] Line112  # Draft 2D object (typed FeaturePython)
  ChamferSize = 0
  Closed = false
  End = (1030,2075.33,4000)
  FilletRadius = 0
  Length = 367.171
  MakeFace = true
  Placement = pos=(-4915,0.305262,0.0001461) rot=(0,0,1;0rad)
  Points = (2) [(5945,2075.02,3632.83),(5945,2075.02,4000)]
  Start = (1030,2075.33,3632.83)
FEATURE [Part::Part2DObjectPython] Line113  # Draft 2D object (typed FeaturePython)
  ChamferSize = 0
  Closed = false
  End = (1030,2095.31,4000)
  FilletRadius = 0
  Length = 367.171
  MakeFace = true
  Placement = pos=(-4915,0.305262,0.0001461) rot=(0,0,1;0rad)
  Points = (2) [(5945,2095,3632.83),(5945,2095,4000)]
  Start = (1030,2095.31,3632.83)
FEATURE [Part::Part2DObjectPython] Line114  # Draft 2D object (typed FeaturePython)
  ChamferSize = 0
  Closed = false
  End = (1030,2055.31,4000)
  FilletRadius = 0
  Length = 367.171
  MakeFace = true
  Placement = pos=(-4915,0.305262,0.0001461) rot=(0,0,1;0rad)
  Points = (2) [(5945,2055,3632.83),(5945,2055,4000)]
  Start = (1030,2055.31,3632.83)
FEATURE [Part::Part2DObjectPython] Line115  # Draft 2D object (typed FeaturePython)
  ChamferSize = 0
  Closed = false
  End = (1030,1518.67,3100)
  FilletRadius = 0
  Length = 631.638
  MakeFace = true
  Placement = pos=(-4915,0.305262,0.0001461) rot=(0,0,1;0rad)
  Points = (2) [(5945,2150,3100),(5945,1518.36,3100)]
  Start = (1030,2150.31,3100)
FEATURE [Part::Part2DObjectPython] Line116  # Draft 2D object (typed FeaturePython)
  ChamferSize = 0
  Closed = false
  End = (1030,1518.67,3140)
  FilletRadius = 0
  Length = 631.638
  MakeFace = true
  Placement = pos=(-4915,0.305262,0.0001461) rot=(0,0,1;0rad)
  Points = (2) [(5945,2150,3140),(5945,1518.36,3140)]
  Start = (1030,2150.31,3140)
FEATURE [Part::Part2DObjectPython] Rectangle006  # Draft 2D object (typed FeaturePython)
  ChamferSize = 0
  FilletRadius = 0
  Height = -40
  Length = 40
  MakeFace = true
  Placement = pos=(5945,2055,4000) rot=(0.57735,0.57735,0.57735;2.0944rad)
FEATURE [Part::Part2DObjectPython] Rectangle007  # Draft 2D object (typed FeaturePython)
  ChamferSize = 0
  FilletRadius = 0
  Height = -40
  Length = 40
  MakeFace = true
  Placement = pos=(5945,2055,3140) rot=(0.57735,0.57735,0.57735;2.0944rad)
FEATURE [Part::Extrusion] Extrusion007
  Base = -> Rectangle006
  Dir = (4900,0,0)
  Solid = true
FEATURE [Part::Extrusion] Extrusion008
  Base = -> Rectangle007
  Dir = (4900,0,0)
  Solid = true
FEATURE [Part::Part2DObjectPython] Line117  # Draft 2D object (typed FeaturePython)
  ChamferSize = 0
  Closed = false
  End = (5005,2150.31,3000)
  FilletRadius = 0
  Length = 2000
  MakeFace = true
  Placement = pos=(-4915,0.305262,0.0001461) rot=(0,0,1;0rad)
  Points = (2) [(11920,2150,3000),(9920,2150,3000)]
  Start = (7005,2150.31,3000)
FEATURE [Part::Part2DObjectPython] Line118  # Draft 2D object (typed FeaturePython)
  ChamferSize = 0
  Closed = false
  End = (6393.3,2150.31,3100)
  FilletRadius = 0
  Length = 463.293
  MakeFace = true
  Placement = pos=(-4915,0.305262,0.0001461) rot=(0,0,1;0rad)
  Points = (2) [(10845,2150,3100),(11308.3,2150,3100)]
  Start = (5930,2150.31,3100)
FEATURE [Part::Part2DObjectPython] Line119  # Draft 2D object (typed FeaturePython)
  ChamferSize = 0
  Closed = false
  End = (6393.3,2150.31,3140)
  FilletRadius = 0
  Length = 463.293
  MakeFace = true
  Placement = pos=(-4915,0.305262,0.0001461) rot=(0,0,1;0rad)
  Points = (2) [(10845,2150,3140),(11308.3,2150,3140)]
  Start = (5930,2150.31,3140)
FEATURE [Part::Part2DObjectPython] Line120  # Draft 2D object (typed FeaturePython)
  ChamferSize = 0
  Closed = false
  End = (6393.3,2150.31,3960)
  FilletRadius = 0
  Length = 463.293
  MakeFace = true
  Placement = pos=(-4915,0.305262,0.0001461) rot=(0,0,1;0rad)
  Points = (2) [(10845,2150,3960),(11308.3,2150,3960)]
  Start = (5930,2150.31,3960)
FEATURE [Part::Part2DObjectPython] Line121  # Draft 2D object (typed FeaturePython)
  ChamferSize = 0
  Closed = false
  End = (6393.3,2150.31,4000)
  FilletRadius = 0
  Length = 463.293
  MakeFace = true
  Placement = pos=(-4915,0.305262,0.0001461) rot=(0,0,1;0rad)
  Points = (2) [(10845,2150,4000),(11308.3,2150,4000)]
  Start = (5930,2150.31,4000)
FEATURE [Part::Part2DObjectPython] Line122  # Draft 2D object (typed FeaturePython)
  ChamferSize = 0
  Closed = false
  End = (6080,2150.31,4000)
  FilletRadius = 0
  Length = 900
  MakeFace = true
  Placement = pos=(-4915,0.305262,0.0001461) rot=(0,0,1;0rad)
  Points = (2) [(10995,2150,3100),(10995,2150,4000)]
  Start = (6080,2150.31,3100)
FEATURE [Part::Part2DObjectPython] Line123  # Draft 2D object (typed FeaturePython)
  ChamferSize = 0
  Closed = false
  End = (5930,2150.31,4000)
  FilletRadius = 0
  Length = 900
  MakeFace = true
  Placement = pos=(-4915,0.305262,0.0001461) rot=(0,0,1;0rad)
  Points = (2) [(10845,2150,3100),(10845,2150,4000)]
  Start = (5930,2150.31,3100)
FEATURE [Part::Part2DObjectPython] Line124  # Draft 2D object (typed FeaturePython)
  ChamferSize = 0
  Closed = false
  End = (5930,2150.31,3774.18)
  FilletRadius = 0
  Length = 150
  MakeFace = true
  Placement = pos=(-4915,0.305262,0.0001461) rot=(0,0,1;0rad)
  Points = (2) [(10995,2150,3774.18),(10845,2150,3774.18)]
  Start = (6080,2150.31,3774.18)
FEATURE [Part::Part2DObjectPython] Line125  # Draft 2D object (typed FeaturePython)
  ChamferSize = 0
  Closed = false
  End = (6005,2150.31,4000)
  FilletRadius = 0
  Length = 900
  MakeFace = true
  Placement = pos=(-4915,0.305262,0.0001461) rot=(0,0,1;0rad)
  Points = (2) [(10920,2150,3100),(10920,2150,4000)]
  Start = (6005,2150.31,3100)
FEATURE [Part::Part2DObjectPython] Line126  # Draft 2D object (typed FeaturePython)
  ChamferSize = 0
  Closed = false
  End = (6025,2150.31,4000)
  FilletRadius = 0
  Length = 900
  MakeFace = true
  Placement = pos=(-4915,0.305262,0.0001461) rot=(0,0,1;0rad)
  Points = (2) [(10940,2150,3100),(10940,2150,4000)]
  Start = (6025,2150.31,3100)
FEATURE [Part::Part2DObjectPython] Line127  # Draft 2D object (typed FeaturePython)
  ChamferSize = 0
  Closed = false
  End = (5985,2150.31,4000)
  FilletRadius = 0
  Length = 900
  MakeFace = true
  Placement = pos=(-4915,0.305262,0.0001461) rot=(0,0,1;0rad)
  Points = (2) [(10900,2150,3100),(10900,2150,4000)]
  Start = (5985,2150.31,3100)
FEATURE [Part::Part2DObjectPython] Rectangle008  # Draft 2D object (typed FeaturePython)
  ChamferSize = 0
  FilletRadius = 0
  Height = 40
  Length = -40
  MakeFace = true
  Placement = pos=(10900,2150,3960) rot=(0,0.707107,0.707107;3.14159rad)
FEATURE [Part::Part2DObjectPython] Rectangle009  # Draft 2D object (typed FeaturePython)
  ChamferSize = 0
  FilletRadius = 0
  Height = -40
  Length = -40
  MakeFace = true
  Placement = pos=(10900,2150,3140) rot=(0,0.707107,0.707107;3.14159rad)
FEATURE [Part::Extrusion] Extrusion009
  Base = -> Rectangle009
  Dir = (0,3600,-1e-12)
  Solid = true
FEATURE [Part::Extrusion] Extrusion010
  Base = -> Rectangle008
  Dir = (0,3600,-1e-12)
  Solid = true
FEATURE [Part::Part2DObjectPython] Line129  # Draft 2D object (typed FeaturePython)
  ChamferSize = 0
  Closed = false
  End = (7785.1,2150.31,6000)
  FilletRadius = 0
  Length = 13165
  MakeFace = true
  Placement = pos=(-4915,0.305262,0.0001461) rot=(0,0,1;0rad)
  Points = (2) [(-464.903,2150,6000),(12700.1,2150,6000)]
  Start = (-5379.9,2150.31,6000)
  Support = -> Cut001
FEATURE [Part::Part2DObjectPython] Line130  # Draft 2D object (typed FeaturePython)
  ChamferSize = 0
  Closed = false
  End = (-5379.9,2000.31,6000)
  FilletRadius = 0
  Length = 13165
  MakeFace = true
  Placement = pos=(-4915,0.305262,0.0001461) rot=(0,0,1;0rad)
  Points = (2) [(12700.1,2000,6000),(-464.903,2000,6000)]
  Start = (7785.1,2000.31,6000)
FEATURE [Part::Part2DObjectPython] Line131  # Draft 2D object (typed FeaturePython)
  ChamferSize = 0
  Closed = false
  End = (7785.1,16000.3,6000)
  FilletRadius = 0
  Length = 14700.1
  MakeFace = true
  Placement = pos=(-4915,0.305262,0.0001461) rot=(0,0,1;0rad)
  Points = (2) [(-2000,16000,6000),(12700.1,16000,6000)]
  Start = (-6915,16000.3,6000)
FEATURE [Part::Part2DObjectPython] Line133  # Draft 2D object (typed FeaturePython)
  ChamferSize = 0
  Closed = false
  End = (7785.1,15850.3,6000)
  FilletRadius = 0
  Length = 14700.1
  MakeFace = true
  Placement = pos=(-4915,0.305262,0.0001461) rot=(0,0,1;0rad)
  Points = (2) [(-2000,15850,6000),(12700.1,15850,6000)]
  Start = (-6915,15850.3,6000)
FEATURE [Part::Part2DObjectPython] Line134  # Draft 2D object (typed FeaturePython)
  ChamferSize = 0
  Closed = false
  End = (7785.1,2000.31,6000)
  FilletRadius = 0
  Length = 150
  MakeFace = true
  Placement = pos=(-4915,0.305262,0.0001461) rot=(0,0,1;0rad)
  Points = (2) [(12700.1,2150,6000),(12700.1,2000,6000)]
  Start = (7785.1,2150.31,6000)
  Support = -> Cut001
FEATURE [Part::Part2DObjectPython] Line135  # Draft 2D object (typed FeaturePython)
  ChamferSize = 0
  Closed = false
  End = (-6051.9,2075.31,6000)
  FilletRadius = 0
  Length = 13837
  MakeFace = true
  Placement = pos=(-4915,0.305262,0.0001461) rot=(0,0,1;0rad)
  Points = (2) [(12700.1,2075,6000),(-1136.9,2075,6000)]
  Start = (7785.1,2075.31,6000)
FEATURE [Part::Part2DObjectPython] Line136  # Draft 2D object (typed FeaturePython)
  ChamferSize = 0
  Closed = false
  End = (7785.1,15850.3,6000)
  FilletRadius = 0
  Length = 150
  MakeFace = true
  Placement = pos=(-4915,0.305262,0.0001461) rot=(0,0,1;0rad)
  Points = (2) [(12700.1,16000,6000),(12700.1,15850,6000)]
  Start = (7785.1,16000.3,6000)
FEATURE [Part::Part2DObjectPython] Line137  # Draft 2D object (typed FeaturePython)
  ChamferSize = 0
  Closed = false
  End = (-6911.9,15925.3,6000)
  FilletRadius = 0
  Length = 14697
  MakeFace = true
  Placement = pos=(-4915,0.305262,0.0001461) rot=(0,0,1;0rad)
  Points = (2) [(12700.1,15925,6000),(-1996.9,15925,6000)]
  Start = (7785.1,15925.3,6000)
FEATURE [Part::Part2DObjectPython] Line141  # Draft 2D object (typed FeaturePython)
  ChamferSize = 0
  Closed = true
  End = (6080,2090.31,6000)
  FilletRadius = 0
  Length = 0
  MakeFace = true
  Placement = pos=(-4915,0.305262,0.0001461) rot=(0,0,1;0rad)
  Points = (2) [(10995,2090,6000),(10995,2090,6000)]
  Start = (6080,2090.31,6000)
FEATURE [Part::Part2DObjectPython] Line144  # Draft 2D object (typed FeaturePython)
  ChamferSize = 0
  Closed = false
  End = (6080,2075.31,6000)
  FilletRadius = 0
  Length = 2461
  MakeFace = true
  Placement = pos=(-4915,0.305262,0.0001461) rot=(0,0,1;0rad)
  Points = (2) [(10995,2075,8461),(10995,2075,6000)]
  Start = (6080,2075.31,8461)
FEATURE [Part::Part2DObjectPython] Line148  # Draft 2D object (typed FeaturePython)
  ChamferSize = 0
  Closed = false
  End = (6080,15925.3,6000)
  FilletRadius = 0
  Length = 2461
  MakeFace = true
  Placement = pos=(-4915,10387.8,0.0001461) rot=(0,0,1;0rad)
  Points = (2) [(10995,5537.5,8461),(10995,5537.5,6000)]
  Start = (6080,15925.3,8461)
FEATURE [Part::Part2DObjectPython] Line147  # Draft 2D object (typed FeaturePython)
  ChamferSize = 0
  Closed = false
  End = (6080,12462.8,6000)
  FilletRadius = 0
  Length = 2461
  MakeFace = true
  Placement = pos=(-4915,6925.31,0.0001461) rot=(0,0,1;0rad)
  Points = (2) [(10995,5537.5,8461),(10995,5537.5,6000)]
  Start = (6080,12462.8,8461)
FEATURE [Part::Part2DObjectPython] Line149  # Draft 2D object (typed FeaturePython)
  ChamferSize = 0
  Closed = false
  End = (6080,4845.31,6000)
  FilletRadius = 0
  Length = 2461
  MakeFace = true
  Placement = pos=(-4915,0.305262,0.0001461) rot=(0,0,1;0rad)
  Points = (2) [(10995,4845,8461),(10995,4845,6000)]
  Start = (6080,4845.31,8461)
FEATURE [Part::Part2DObjectPython] Line150  # Draft 2D object (typed FeaturePython)
  ChamferSize = 0
  Closed = false
  End = (6080,7615.31,6000)
  FilletRadius = 0
  Length = 2461
  MakeFace = true
  Placement = pos=(-4915,2770.31,0.0001461) rot=(0,0,1;0rad)
  Points = (2) [(10995,4845,8461),(10995,4845,6000)]
  Start = (6080,7615.31,8461)
FEATURE [Part::Part2DObjectPython] Line151  # Draft 2D object (typed FeaturePython)
  ChamferSize = 0
  Closed = false
  End = (6080,10385.3,6000)
  FilletRadius = 0
  Length = 2461
  MakeFace = true
  Placement = pos=(-4915,5540.31,0.0001461) rot=(0,0,1;0rad)
  Points = (2) [(10995,4845,8461),(10995,4845,6000)]
  Start = (6080,10385.3,8461)
FEATURE [Part::Part2DObjectPython] Line152  # Draft 2D object (typed FeaturePython)
  ChamferSize = 0
  Closed = false
  End = (6080,13155.3,6000)
  FilletRadius = 0
  Length = 2461
  MakeFace = true
  Placement = pos=(-4915,8310.31,0.0001461) rot=(0,0,1;0rad)
  Points = (2) [(10995,4845,8461),(10995,4845,6000)]
  Start = (6080,13155.3,8461)
FEATURE [Part::Part2DObjectPython] Line153  # Draft 2D object (typed FeaturePython)
  ChamferSize = 0
  Closed = false
  End = (6080,15925.3,6000)
  FilletRadius = 0
  Length = 2461
  MakeFace = true
  Placement = pos=(-4915,11080.3,0.0001461) rot=(0,0,1;0rad)
  Points = (2) [(10995,4845,8461),(10995,4845,6000)]
  Start = (6080,15925.3,8461)
FEATURE [Part::Feature] Clone  label="Clone of Extrusion018"
  Placement = pos=(0,2770,0) rot=(0,0,1;0rad)
  shape: bbox 11000 x 40 x 40 mm, 6 faces (baked)
FEATURE [Part::Feature] Clone004  label="Clone of Extrusion019"
  Placement = pos=(0,5540,0) rot=(0,0,1;0rad)
  shape: bbox 11000 x 40 x 40 mm, 6 faces (baked)
FEATURE [Part::Feature] Clone005  label="Clone of Extrusion020"
  Placement = pos=(0,8310,0) rot=(0,0,1;0rad)
  shape: bbox 11000 x 40 x 40 mm, 6 faces (baked)
FEATURE [Part::Feature] Clone006  label="Clone of Extrusion021"
  Placement = pos=(0,11080,0) rot=(0,0,1;0rad)
  shape: bbox 11000 x 40 x 40 mm, 6 faces (baked)
FEATURE [Part::Feature] Clone007  label="Clone of Extrusion022"
  Placement = pos=(0,13850,0) rot=(0,0,1;0rad)
  shape: bbox 11000 x 40 x 40 mm, 6 faces (baked)
FEATURE [Part::Feature] Clone008  label="Clone of Extrusion023"
  shape: bbox 11000 x 40 x 40 mm, 6 faces (baked)
FEATURE [Part::Part2DObjectPython] Rectangle012  # Draft 2D object (typed FeaturePython)
  ChamferSize = 0
  FilletRadius = 0
  Height = -14000
  Length = 18000
  MakeFace = true
  Placement = pos=(12945.5,17000,7633.02) rot=(0.043578,-0.043578,-0.998099;1.5727rad)
FEATURE [Part::Feature] Face009
  Placement = pos=(12949,2055,7593.18) rot=(0,1,0;1.48353rad)
  shape: bbox 3.488 x 40 x 39.85 mm, 1 faces, 0 solids (baked)
FEATURE [Part::Part2DObjectPython] Line155  # Draft 2D object (typed FeaturePython)
  ChamferSize = 0
  Closed = false
  End = (-4920,13155.3,6040)
  FilletRadius = 0
  Length = 1385
  MakeFace = true
  Placement = pos=(-4915,0.305262,0.0001461) rot=(0,0,1;0rad)
  Points = (2) [(-5,14540,6040),(-5,13155,6040)]
  Start = (-4920,14540.3,6040)
FEATURE [Part::Part2DObjectPython] Line156  # Draft 2D object (typed FeaturePython)
  ChamferSize = 0
  Closed = false
  End = (-4920,14540.3,7197)
  FilletRadius = 0
  Length = 1157
  MakeFace = true
  Placement = pos=(-4915,0.305262,0.0001461) rot=(0,0,1;0rad)
  Points = (2) [(-5,14540,6040),(-5,14540,7197)]
  Start = (-4920,14540.3,6040)
FEATURE [Part::Part2DObjectPython] Line157  # Draft 2D object (typed FeaturePython)
  ChamferSize = 0
  Closed = false
  End = (-4920,13155.3,7197)
  FilletRadius = 0
  Length = 1157
  MakeFace = true
  Placement = pos=(-4915,-1384.69,0.0001461) rot=(0,0,1;0rad)
  Points = (2) [(-5,14540,6040),(-5,14540,7197)]
  Start = (-4920,13155.3,6040)
FEATURE [Part::Part2DObjectPython] Line158  # Draft 2D object (typed FeaturePython)
  ChamferSize = 0
  Closed = false
  End = (-4920,11770.3,6040)
  FilletRadius = 0
  Length = 1385
  MakeFace = true
  Placement = pos=(-4915,-1384.69,0.0001461) rot=(0,0,1;0rad)
  Points = (2) [(-5,14540,6040),(-5,13155,6040)]
  Start = (-4920,13155.3,6040)
FEATURE [Part::Part2DObjectPython] Line159  # Draft 2D object (typed FeaturePython)
  ChamferSize = 0
  Closed = false
  End = (-4920,11770.3,7197)
  FilletRadius = 0
  Length = 1157
  MakeFace = true
  Placement = pos=(-4915,-2769.69,0.0001461) rot=(0,0,1;0rad)
  Points = (2) [(-5,14540,6040),(-5,14540,7197)]
  Start = (-4920,11770.3,6040)
FEATURE [Part::Part2DObjectPython] Line160  # Draft 2D object (typed FeaturePython)
  ChamferSize = 0
  Closed = false
  End = (-4920,10385.3,6040)
  FilletRadius = 0
  Length = 1385
  MakeFace = true
  Placement = pos=(-4915,-2769.69,0.0001461) rot=(0,0,1;0rad)
  Points = (2) [(-5,14540,6040),(-5,13155,6040)]
  Start = (-4920,11770.3,6040)
FEATURE [Part::Part2DObjectPython] Line161  # Draft 2D object (typed FeaturePython)
  ChamferSize = 0
  Closed = false
  End = (-4920,9000.31,7197)
  FilletRadius = 0
  Length = 1157
  MakeFace = true
  Placement = pos=(-4915,-5539.69,0.0001461) rot=(0,0,1;0rad)
  Points = (2) [(-5,14540,6040),(-5,14540,7197)]
  Start = (-4920,9000.31,6040)
FEATURE [Part::Part2DObjectPython] Line162  # Draft 2D object (typed FeaturePython)
  ChamferSize = 0
  Closed = false
  End = (-4920,7615.31,6040)
  FilletRadius = 0
  Length = 1385
  MakeFace = true
  Placement = pos=(-4915,-5539.69,0.0001461) rot=(0,0,1;0rad)
  Points = (2) [(-5,14540,6040),(-5,13155,6040)]
  Start = (-4920,9000.31,6040)
FEATURE [Part::Part2DObjectPython] Line163  # Draft 2D object (typed FeaturePython)
  ChamferSize = 0
  Closed = false
  End = (-4920,7615.31,7197)
  FilletRadius = 0
  Length = 1157
  MakeFace = true
  Placement = pos=(-4915,-6924.69,0.0001461) rot=(0,0,1;0rad)
  Points = (2) [(-5,14540,6040),(-5,14540,7197)]
  Start = (-4920,7615.31,6040)
FEATURE [Part::Part2DObjectPython] Line164  # Draft 2D object (typed FeaturePython)
  ChamferSize = 0
  Closed = false
  End = (-4920,6230.31,6040)
  FilletRadius = 0
  Length = 1385
  MakeFace = true
  Placement = pos=(-4915,-6924.69,0.0001461) rot=(0,0,1;0rad)
  Points = (2) [(-5,14540,6040),(-5,13155,6040)]
  Start = (-4920,7615.31,6040)
FEATURE [Part::Part2DObjectPython] Line165  # Draft 2D object (typed FeaturePython)
  ChamferSize = 0
  Closed = false
  End = (-4920,4845.31,6040)
  FilletRadius = 0
  Length = 1385
  MakeFace = true
  Placement = pos=(-4915,-8309.69,0.0001461) rot=(0,0,1;0rad)
  Points = (2) [(-5,14540,6040),(-5,13155,6040)]
  Start = (-4920,6230.31,6040)
FEATURE [Part::Part2DObjectPython] Line166  # Draft 2D object (typed FeaturePython)
  ChamferSize = 0
  Closed = false
  End = (-4920,6230.31,7197)
  FilletRadius = 0
  Length = 1157
  MakeFace = true
  Placement = pos=(-4915,-8309.69,0.0001461) rot=(0,0,1;0rad)
  Points = (2) [(-5,14540,6040),(-5,14540,7197)]
  Start = (-4920,6230.31,6040)
FEATURE [Part::Part2DObjectPython] Line167  # Draft 2D object (typed FeaturePython)
  ChamferSize = 0
  Closed = false
  End = (-4920,4845.31,7197)
  FilletRadius = 0
  Length = 1157
  MakeFace = true
  Placement = pos=(-4915,-9694.69,0.0001461) rot=(0,0,1;0rad)
  Points = (2) [(-5,14540,6040),(-5,14540,7197)]
  Start = (-4920,4845.31,6040)
FEATURE [Part::Part2DObjectPython] Line168  # Draft 2D object (typed FeaturePython)
  ChamferSize = 0
  Closed = false
  End = (-4920,3460.31,6040)
  FilletRadius = 0
  Length = 1385
  MakeFace = true
  Placement = pos=(-4915,-9694.69,0.0001461) rot=(0,0,1;0rad)
  Points = (2) [(-5,14540,6040),(-5,13155,6040)]
  Start = (-4920,4845.31,6040)
FEATURE [Part::Part2DObjectPython] Line169  # Draft 2D object (typed FeaturePython)
  ChamferSize = 0
  Closed = false
  End = (-4920,2075.31,6040)
  FilletRadius = 0
  Length = 1385
  MakeFace = true
  Placement = pos=(-4915,-11079.7,0.0001461) rot=(0,0,1;0rad)
  Points = (2) [(-5,14540,6040),(-5,13155,6040)]
  Start = (-4920,3460.31,6040)
FEATURE [Part::Part2DObjectPython] Line170  # Draft 2D object (typed FeaturePython)
  ChamferSize = 0
  Closed = false
  End = (-4920,3460.31,7197)
  FilletRadius = 0
  Length = 1157
  MakeFace = true
  Placement = pos=(-4915,-11079.7,0.0001461) rot=(0,0,1;0rad)
  Points = (2) [(-5,14540,6040),(-5,14540,7197)]
  Start = (-4920,3460.31,6040)
FEATURE [Part::Part2DObjectPython] Line171  # Draft 2D object (typed FeaturePython)
  ChamferSize = 0
  Closed = false
  End = (-4920,2075.31,7197)
  FilletRadius = 0
  Length = 1157
  MakeFace = true
  Placement = pos=(-4915,-12464.7,0.0001461) rot=(0,0,1;0rad)
  Points = (2) [(-5,14540,6040),(-5,14540,7197)]
  Start = (-4920,2075.31,6040)
FEATURE [Part::Part2DObjectPython] Line172  # Draft 2D object (typed FeaturePython)
  ChamferSize = 0
  Closed = false
  End = (-4920,690.305,6040)
  FilletRadius = 0
  Length = 1385
  MakeFace = true
  Placement = pos=(-4915,-12464.7,0.0001461) rot=(0,0,1;0rad)
  Points = (2) [(-5,14540,6040),(-5,13155,6040)]
  Start = (-4920,2075.31,6040)
FEATURE [Part::Part2DObjectPython] Line173  # Draft 2D object (typed FeaturePython)
  ChamferSize = 0
  Closed = false
  End = (-4920,15925.3,7197)
  FilletRadius = 0
  Length = 1157
  MakeFace = true
  Placement = pos=(-4915,1385.31,0.0001461) rot=(0,0,1;0rad)
  Points = (2) [(-5,14540,6040),(-5,14540,7197)]
  Start = (-4920,15925.3,6040)
FEATURE [Part::Part2DObjectPython] Line174  # Draft 2D object (typed FeaturePython)
  ChamferSize = 0
  Closed = false
  End = (-4920,14540.3,6040)
  FilletRadius = 0
  Length = 1385
  MakeFace = true
  Placement = pos=(-4915,1385.31,0.0001461) rot=(0,0,1;0rad)
  Points = (2) [(-5,14540,6040),(-5,13155,6040)]
  Start = (-4920,15925.3,6040)
FEATURE [Part::Part2DObjectPython] Line175  # Draft 2D object (typed FeaturePython)
  ChamferSize = 0
  Closed = false
  End = (-4920,15925.3,6040)
  FilletRadius = 0
  Length = 1385
  MakeFace = true
  Placement = pos=(-4915,2770.31,0.0001461) rot=(0,0,1;0rad)
  Points = (2) [(-5,14540,6040),(-5,13155,6040)]
  Start = (-4920,17310.3,6040)
FEATURE [Part::Part2DObjectPython] Line176  # Draft 2D object (typed FeaturePython)
  ChamferSize = 0
  Closed = false
  End = (-4920,17310.3,7197)
  FilletRadius = 0
  Length = 1157
  MakeFace = true
  Placement = pos=(-4915,2770.31,0.0001461) rot=(0,0,1;0rad)
  Points = (2) [(-5,14540,6040),(-5,14540,7197)]
  Start = (-4920,17310.3,6040)
FEATURE [Part::Feature] Extrusion016
  Placement = pos=(0,1385,0) rot=(0,0,1;0rad)
  shape: bbox 13950 x 40 x 1260 mm, 6 faces (baked)
FEATURE [Part::Feature] Extrusion017
  Placement = pos=(0,4155,0) rot=(0,0,1;0rad)
  shape: bbox 13950 x 40 x 1260 mm, 6 faces (baked)
FEATURE [Part::Feature] Extrusion018
  Placement = pos=(0,6925,0) rot=(0,0,1;0rad)
  shape: bbox 13950 x 40 x 1260 mm, 6 faces (baked)
FEATURE [Part::Feature] Extrusion019
  Placement = pos=(0,9695,0) rot=(0,0,1;0rad)
  shape: bbox 13950 x 40 x 1260 mm, 6 faces (baked)
FEATURE [Part::Feature] Extrusion020
  Placement = pos=(0,12465,0) rot=(0,0,1;0rad)
  shape: bbox 13950 x 40 x 1260 mm, 6 faces (baked)
FEATURE [Part::Feature] Extrusion021
  Placement = pos=(0,14825,1e-12) rot=(0,0,1;0rad)
  shape: bbox 13950 x 40 x 1260 mm, 6 faces (baked)
FEATURE [Sketcher::SketchObject] Sketch002
  Placement = pos=(10995,10357,3902.22) rot=(0.57735,0.57735,0.57735;2.0944rad)
  sketch-geometry (8):
    g0: LineSegment StartX=0 StartY=0 StartZ=0 EndX=500 EndY=0 EndZ=0
    g1: LineSegment StartX=500 StartY=0 StartZ=0 EndX=500 EndY=1200 EndZ=0
    g2: LineSegment StartX=500 StartY=1200 StartZ=0 EndX=0 EndY=1200 EndZ=0
    g3: LineSegment StartX=0 StartY=1200 StartZ=0 EndX=0 EndY=0 EndZ=0
    g4: LineSegment StartX=50 StartY=50 StartZ=0 EndX=450 EndY=50 EndZ=0
    g5: LineSegment StartX=450 StartY=50 StartZ=0 EndX=450 EndY=1150 EndZ=0
    g6: LineSegment StartX=450 StartY=1150 StartZ=0 EndX=50 EndY=1150 EndZ=0
    g7: LineSegment StartX=50 StartY=1150 StartZ=0 EndX=50 EndY=50 EndZ=0
  constraints (23):
    c: Coincident(g0,g1)
    c: Coincident(g1,g2)
    c: Coincident(g2,g3)
    c: Coincident(g3,g0)
    c: Horizontal(g0)
    c: Horizontal(g2)
    c: Vertical(g1)
    c: Vertical(g3)
    c: Coincident(g4,g5)
    c: Coincident(g5,g6)
    c: Coincident(g6,g7)
    c: Coincident(g7,g4)
    c: Horizontal(g4)
    c: Horizontal(g6)
    c: Vertical(g5)
    c: Vertical(g7)
    c: DistanceY(g1) = 1200
    c: DistanceX(g0) = 500
    c: DistanceY(g6,g2) = 50
    c: DistanceX(g2,g6) = 50
    c: DistanceX(g4,g0) = 50
    c: DistanceY(g0,g4) = 50
    c: Coincident(g0,g-1)
FEATURE [Part::FeaturePython] Window001  # WARN: FeaturePython — macro-defined, semantics opaque (R4)
  Base = -> Sketch002
  Height = 1200
  HoleDepth = 0
  MoveWithHost = true
  Normal = (-1,0,0)
  Placement = pos=(0,843.034,97.7756) rot=(0,0,1;0rad)
  Preset = 1
  Role = 0
  Width = 500
  WindowParts = OuterFrame | Frame | Wire0,Wire1 | 100.0 | 0.0 | Glass | Glass panel | Wire1 | 10.0 | 50.0
FEATURE [Part::FeaturePython] Wall026  # WARN: FeaturePython — macro-defined, semantics opaque (R4)
  Align = 2
  Base = -> Line003
  Face = 0
  Height = 2800
  Length = 0
  MoveWithHost = false
  Normal = (0,0,0)
  Placement = pos=(0,0,3000) rot=(0,0,1;0rad)
  Role = 0
  Subtractions = -> [Window001]
  Width = 150
FEATURE [Sketcher::SketchObject] Sketch005
  Placement = pos=(10995,7773.34,3915.03) rot=(0.707107,0,0.707107;3.14159rad)
  sketch-geometry (8):
    g0: LineSegment StartX=0 StartY=0 StartZ=0 EndX=1200 EndY=0 EndZ=0
    g1: LineSegment StartX=1200 StartY=0 StartZ=0 EndX=1200 EndY=1000 EndZ=0
    g2: LineSegment StartX=1200 StartY=1000 StartZ=0 EndX=0 EndY=1000 EndZ=0
    g3: LineSegment StartX=0 StartY=1000 StartZ=0 EndX=0 EndY=0 EndZ=0
    g4: LineSegment StartX=50 StartY=50 StartZ=0 EndX=1150 EndY=50 EndZ=0
    g5: LineSegment StartX=1150 StartY=50 StartZ=0 EndX=1150 EndY=950 EndZ=0
    g6: LineSegment StartX=1150 StartY=950 StartZ=0 EndX=50 EndY=950 EndZ=0
    g7: LineSegment StartX=50 StartY=950 StartZ=0 EndX=50 EndY=50 EndZ=0
  constraints (23):
    c: Coincident(g0,g1)
    c: Coincident(g1,g2)
    c: Coincident(g2,g3)
    c: Coincident(g3,g0)
    c: Horizontal(g0)
    c: Horizontal(g2)
    c: Vertical(g1)
    c: Vertical(g3)
    c: Coincident(g4,g5)
    c: Coincident(g5,g6)
    c: Coincident(g6,g7)
    c: Coincident(g7,g4)
    c: Horizontal(g4)
    c: Horizontal(g6)
    c: Vertical(g5)
    c: Vertical(g7)
    c: DistanceY(g1) = 1000
    c: DistanceX(g0) = 1200
    c: DistanceY(g6,g2) = 50
    c: DistanceX(g2,g6) = 50
    c: DistanceX(g4,g0) = 50
    c: DistanceY(g0,g4) = 50
    c: Coincident(g0,g-1)
FEATURE [Part::FeaturePython] Window003  # WARN: FeaturePython — macro-defined, semantics opaque (R4)
  Base = -> Sketch005
  Height = 1000
  HoleDepth = 0
  MoveWithHost = true
  Normal = (-1,0,0)
  Placement = pos=(-3.8e-08,476.658,84.9653) rot=(0,0,1;0rad)
  Preset = 1
  Role = 0
  Width = 1200
  WindowParts = OuterFrame | Frame | Wire0,Wire1 | 100.0 | 0.0 | Glass | Glass panel | Wire1 | 10.0 | 50.0
FEATURE [Sketcher::SketchObject] Sketch007
  Placement = pos=(10995,13727.4,3866.65) rot=(0.57735,0.57735,0.57735;2.0944rad)
  sketch-geometry (8):
    g0: LineSegment StartX=0 StartY=0 StartZ=0 EndX=1000 EndY=0 EndZ=0
    g1: LineSegment StartX=1000 StartY=0 StartZ=0 EndX=1000 EndY=1200 EndZ=0
    g2: LineSegment StartX=1000 StartY=1200 StartZ=0 EndX=0 EndY=1200 EndZ=0
    g3: LineSegment StartX=0 StartY=1200 StartZ=0 EndX=0 EndY=0 EndZ=0
    g4: LineSegment StartX=50 StartY=50 StartZ=0 EndX=950 EndY=50 EndZ=0
    g5: LineSegment StartX=950 StartY=50 StartZ=0 EndX=950 EndY=1150 EndZ=0
    g6: LineSegment StartX=950 StartY=1150 StartZ=0 EndX=50 EndY=1150 EndZ=0
    g7: LineSegment StartX=50 StartY=1150 StartZ=0 EndX=50 EndY=50 EndZ=0
  constraints (23):
    c: Coincident(g0,g1)
    c: Coincident(g1,g2)
    c: Coincident(g2,g3)
    c: Coincident(g3,g0)
    c: Horizontal(g0)
    c: Horizontal(g2)
    c: Vertical(g1)
    c: Vertical(g3)
    c: Coincident(g4,g5)
    c: Coincident(g5,g6)
    c: Coincident(g6,g7)
    c: Coincident(g7,g4)
    c: Horizontal(g4)
    c: Horizontal(g6)
    c: Vertical(g5)
    c: Vertical(g7)
    c: DistanceY(g1) = 1200
    c: DistanceX(g0) = 1000
    c: DistanceY(g6,g2) = 50
    c: DistanceX(g2,g6) = 50
    c: DistanceX(g4,g0) = 50
    c: DistanceY(g0,g4) = 50
    c: Coincident(g0,g-1)
FEATURE [Part::FeaturePython] Window  # WARN: FeaturePython — macro-defined, semantics opaque (R4)
  Base = -> Sketch007
  Height = 1200
  HoleDepth = 0
  MoveWithHost = true
  Normal = (-1,0,0)
  Placement = pos=(0,-348.61,133.351) rot=(0,0,1;0rad)
  Preset = 1
  Role = 0
  Width = 1000
  WindowParts = OuterFrame | Frame | Wire0,Wire1 | 100.0 | 0.0 | Glass | Glass panel | Wire1 | 10.0 | 50.0
FEATURE [Part::FeaturePython] Wall038  # WARN: FeaturePython — macro-defined, semantics opaque (R4)
  Align = 2
  Base = -> Line002
  Face = 0
  Height = 2800
  Length = 0
  MoveWithHost = false
  Normal = (0,0,0)
  Placement = pos=(0,0,3000) rot=(0,0,1;0rad)
  Role = 0
  Subtractions = -> [Window]
  Width = 150
FEATURE [Part::Part2DObjectPython] Line179  # Draft 2D object (typed FeaturePython)
  ChamferSize = 0
  Closed = false
  End = (6080,13376.2,-595.874)
  FilletRadius = 0
  Length = 4498.1
  MakeFace = true
  Placement = pos=(-4915,2672.22,0.0001461) rot=(0,0,1;0rad)
  Points = (2) [(10995,10704,3902.22),(10995,10704,-595.874)]
  Start = (6080,13376.2,3902.22)
FEATURE [Sketcher::SketchObject] Sketch009
  Placement = pos=(10995,13569,1202.02) rot=(0.57735,0.57735,0.57735;2.0944rad)
  sketch-geometry (8):
    g0: LineSegment StartX=0 StartY=0 StartZ=0 EndX=500 EndY=0 EndZ=0
    g1: LineSegment StartX=500 StartY=0 StartZ=0 EndX=500 EndY=1200 EndZ=0
    g2: LineSegment StartX=500 StartY=1200 StartZ=0 EndX=0 EndY=1200 EndZ=0
    g3: LineSegment StartX=0 StartY=1200 StartZ=0 EndX=0 EndY=0 EndZ=0
    g4: LineSegment StartX=50 StartY=50 StartZ=0 EndX=450 EndY=50 EndZ=0
    g5: LineSegment StartX=450 StartY=50 StartZ=0 EndX=450 EndY=1150 EndZ=0
    g6: LineSegment StartX=450 StartY=1150 StartZ=0 EndX=50 EndY=1150 EndZ=0
    g7: LineSegment StartX=50 StartY=1150 StartZ=0 EndX=50 EndY=50 EndZ=0
  constraints (23):
    c: Coincident(g0,g1)
    c: Coincident(g1,g2)
    c: Coincident(g2,g3)
    c: Coincident(g3,g0)
    c: Horizontal(g0)
    c: Horizontal(g2)
    c: Vertical(g1)
    c: Vertical(g3)
    c: Coincident(g4,g5)
    c: Coincident(g5,g6)
    c: Coincident(g6,g7)
    c: Coincident(g7,g4)
    c: Horizontal(g4)
    c: Horizontal(g6)
    c: Vertical(g5)
    c: Vertical(g7)
    c: DistanceY(g1) = 1200
    c: DistanceX(g0) = 500
    c: DistanceY(g6,g2) = 50
    c: DistanceX(g2,g6) = 50
    c: DistanceX(g4,g0) = 50
    c: DistanceY(g0,g4) = 50
    c: Coincident(g0,g-1)
FEATURE [Part::FeaturePython] Window005  # WARN: FeaturePython — macro-defined, semantics opaque (R4)
  Base = -> Sketch009
  Height = 1200
  HoleDepth = 0
  MoveWithHost = true
  Normal = (-1,0,0)
  Placement = pos=(0,-190.232,-202.202) rot=(0,0,1;0rad)
  Preset = 1
  Role = 0
  Width = 500
  WindowParts = OuterFrame | Frame | Wire0,Wire1 | 100.0 | 0.0 | Glass | Glass panel | Wire1 | 10.0 | 50.0
FEATURE [Part::FeaturePython] Wall073  # WARN: FeaturePython — macro-defined, semantics opaque (R4)
  Align = 2
  Base = -> Line077
  Face = 0
  Height = 2900
  Length = 0
  MoveWithHost = false
  Normal = (0,0,0)
  Role = 0
  Subtractions = -> [Window005]
  Width = 150
FEATURE [Part::Part2DObjectPython] Line181  # Draft 2D object (typed FeaturePython)
  ChamferSize = 0
  Closed = false
  End = (9168,2000.31,1000)
  FilletRadius = 0
  Length = 8138
  MakeFace = true
  Placement = pos=(-4915,0.305262,0.0001461) rot=(0,0,1;0rad)
  Points = (2) [(5945,2000,1000),(14083,2000,1000)]
  Start = (1030,2000.31,1000)
FEATURE [Part::FeaturePython] Window007  # WARN: FeaturePython — macro-defined, semantics opaque (R4)
  Height = 0
  HoleDepth = 0
  MoveWithHost = true
  Normal = (0,1,0)
  Placement = pos=(0,-850,0) rot=(0,0,1;0rad)
  Preset = 0
  Role = 0
  Width = 0
FEATURE [Sketcher::SketchObject] Sketch
  Placement = pos=(4554,2850,-2) rot=(1,0,0;1.5708rad)
  sketch-geometry (8):
    g0: LineSegment StartX=0 StartY=0 StartZ=0 EndX=900 EndY=0 EndZ=0
    g1: LineSegment StartX=900 StartY=0 StartZ=0 EndX=900 EndY=2000 EndZ=0
    g2: LineSegment StartX=900 StartY=2000 StartZ=0 EndX=0 EndY=2000 EndZ=0
    g3: LineSegment StartX=0 StartY=2000 StartZ=0 EndX=0 EndY=0 EndZ=0
    g4: LineSegment StartX=50 StartY=0 StartZ=0 EndX=850 EndY=0 EndZ=0
    g5: LineSegment StartX=850 StartY=0 StartZ=0 EndX=850 EndY=1950 EndZ=0
    g6: LineSegment StartX=850 StartY=1950 StartZ=0 EndX=50 EndY=1950 EndZ=0
    g7: LineSegment StartX=50 StartY=1950 StartZ=0 EndX=50 EndY=0 EndZ=0
  constraints (23):
    c: Coincident(g0,g1)
    c: Coincident(g1,g2)
    c: Coincident(g2,g3)
    c: Coincident(g3,g0)
    c: Horizontal(g0)
    c: Horizontal(g2)
    c: Vertical(g1)
    c: Vertical(g3)
    c: Coincident(g4,g5)
    c: Coincident(g5,g6)
    c: Coincident(g6,g7)
    c: Coincident(g7,g4)
    c: Horizontal(g4)
    c: Horizontal(g6)
    c: Vertical(g5)
    c: Vertical(g7)
    c: DistanceY(g1) = 2000
    c: DistanceX(g0) = 900
    c: DistanceY(g6,g2) = 50
    c: DistanceX(g2,g6) = 50
    c: DistanceX(g4,g0) = 50
    c: DistanceY(g0,g4) = 0
    c: Coincident(g0,g-1)
FEATURE [Part::Part2DObjectPython] Line182  # Draft 2D object (typed FeaturePython)
  ChamferSize = 0
  Closed = false
  End = (-1670,2150.31,0.0001461)
  FilletRadius = 0
  Length = 2550
  MakeFace = true
  Placement = pos=(-4915,0.305262,0.0001461) rot=(0,0,1;0rad)
  Points = (2) [(5795,2150,0),(3245,2150,0)]
  Start = (880.002,2150.31,0.0001461)
FEATURE [Sketcher::SketchObject] Sketch016
  Placement = pos=(3245,3000,0) rot=(1,0,0;1.5708rad)
  sketch-geometry (8):
    g0: LineSegment StartX=0 StartY=0 StartZ=0 EndX=900 EndY=0 EndZ=0
    g1: LineSegment StartX=900 StartY=0 StartZ=0 EndX=900 EndY=2000 EndZ=0
    g2: LineSegment StartX=900 StartY=2000 StartZ=0 EndX=0 EndY=2000 EndZ=0
    g3: LineSegment StartX=0 StartY=2000 StartZ=0 EndX=0 EndY=0 EndZ=0
    g4: LineSegment StartX=50 StartY=0 StartZ=0 EndX=850 EndY=0 EndZ=0
    g5: LineSegment StartX=850 StartY=0 StartZ=0 EndX=850 EndY=1950 EndZ=0
    g6: LineSegment StartX=850 StartY=1950 StartZ=0 EndX=50 EndY=1950 EndZ=0
    g7: LineSegment StartX=50 StartY=1950 StartZ=0 EndX=50 EndY=0 EndZ=0
  constraints (23):
    c: Coincident(g0,g1)
    c: Coincident(g1,g2)
    c: Coincident(g2,g3)
    c: Coincident(g3,g0)
    c: Horizontal(g0)
    c: Horizontal(g2)
    c: Vertical(g1)
    c: Vertical(g3)
    c: Coincident(g4,g5)
    c: Coincident(g5,g6)
    c: Coincident(g6,g7)
    c: Coincident(g7,g4)
    c: Horizontal(g4)
    c: Horizontal(g6)
    c: Vertical(g5)
    c: Vertical(g7)
    c: DistanceY(g1) = 2000
    c: DistanceX(g0) = 900
    c: DistanceY(g6,g2) = 50
    c: DistanceX(g2,g6) = 50
    c: DistanceX(g4,g0) = 50
    c: DistanceY(g0,g4) = 0
    c: Coincident(g0,g-1)
FEATURE [Sketcher::SketchObject] Sketch017
  Placement = pos=(8925.65,2000,1184.37) rot=(1,0,0;1.5708rad)
  sketch-geometry (8):
    g0: LineSegment StartX=0 StartY=0 StartZ=0 EndX=1000 EndY=0 EndZ=0
    g1: LineSegment StartX=1000 StartY=0 StartZ=0 EndX=1000 EndY=1200 EndZ=0
    g2: LineSegment StartX=1000 StartY=1200 StartZ=0 EndX=0 EndY=1200 EndZ=0
    g3: LineSegment StartX=0 StartY=1200 StartZ=0 EndX=0 EndY=0 EndZ=0
    g4: LineSegment StartX=50 StartY=50 StartZ=0 EndX=950 EndY=50 EndZ=0
    g5: LineSegment StartX=950 StartY=50 StartZ=0 EndX=950 EndY=1150 EndZ=0
    g6: LineSegment StartX=950 StartY=1150 StartZ=0 EndX=50 EndY=1150 EndZ=0
    g7: LineSegment StartX=50 StartY=1150 StartZ=0 EndX=50 EndY=50 EndZ=0
  constraints (23):
    c: Coincident(g0,g1)
    c: Coincident(g1,g2)
    c: Coincident(g2,g3)
    c: Coincident(g3,g0)
    c: Horizontal(g0)
    c: Horizontal(g2)
    c: Vertical(g1)
    c: Vertical(g3)
    c: Coincident(g4,g5)
    c: Coincident(g5,g6)
    c: Coincident(g6,g7)
    c: Coincident(g7,g4)
    c: Horizontal(g4)
    c: Horizontal(g6)
    c: Vertical(g5)
    c: Vertical(g7)
    c: DistanceY(g1) = 1200
    c: DistanceX(g0) = 1000
    c: DistanceY(g6,g2) = 50
    c: DistanceX(g2,g6) = 50
    c: DistanceX(g4,g0) = 50
    c: DistanceY(g0,g4) = 50
    c: Coincident(g0,g-1)
FEATURE [Part::FeaturePython] Window010  label="Window008"  # WARN: FeaturePython — macro-defined, semantics opaque (R4)
  Base = -> Sketch017
  Height = 1200
  HoleDepth = 0
  MoveWithHost = true
  Normal = (0,1,0)
  Placement = pos=(194.348,1999.61,-184.366) rot=(0,0,1;0rad)
  Preset = 1
  Role = 0
  Width = 1000
  WindowParts = OuterFrame | Frame | Wire0,Wire1 | 100.0 | 0.0 | Glass | Glass panel | Wire1 | 10.0 | 50.0
FEATURE [Sketcher::SketchObject] Sketch018
  Placement = pos=(6850.59,2000,1115.38) rot=(1,0,0;1.5708rad)
  sketch-geometry (8):
    g0: LineSegment StartX=0 StartY=0 StartZ=0 EndX=1000 EndY=0 EndZ=0
    g1: LineSegment StartX=1000 StartY=0 StartZ=0 EndX=1000 EndY=1200 EndZ=0
    g2: LineSegment StartX=1000 StartY=1200 StartZ=0 EndX=0 EndY=1200 EndZ=0
    g3: LineSegment StartX=0 StartY=1200 StartZ=0 EndX=0 EndY=0 EndZ=0
    g4: LineSegment StartX=50 StartY=50 StartZ=0 EndX=950 EndY=50 EndZ=0
    g5: LineSegment StartX=950 StartY=50 StartZ=0 EndX=950 EndY=1150 EndZ=0
    g6: LineSegment StartX=950 StartY=1150 StartZ=0 EndX=50 EndY=1150 EndZ=0
    g7: LineSegment StartX=50 StartY=1150 StartZ=0 EndX=50 EndY=50 EndZ=0
  constraints (23):
    c: Coincident(g0,g1)
    c: Coincident(g1,g2)
    c: Coincident(g2,g3)
    c: Coincident(g3,g0)
    c: Horizontal(g0)
    c: Horizontal(g2)
    c: Vertical(g1)
    c: Vertical(g3)
    c: Coincident(g4,g5)
    c: Coincident(g5,g6)
    c: Coincident(g6,g7)
    c: Coincident(g7,g4)
    c: Horizontal(g4)
    c: Horizontal(g6)
    c: Vertical(g5)
    c: Vertical(g7)
    c: DistanceY(g1) = 1200
    c: DistanceX(g0) = 1000
    c: DistanceY(g6,g2) = 50
    c: DistanceX(g2,g6) = 50
    c: DistanceX(g4,g0) = 50
    c: DistanceY(g0,g4) = 50
    c: Coincident(g0,g-1)
FEATURE [Part::FeaturePython] Window011  label="Window009"  # WARN: FeaturePython — macro-defined, semantics opaque (R4)
  Base = -> Sketch018
  Height = 1200
  HoleDepth = 0
  MoveWithHost = true
  Normal = (0,1,0)
  Placement = pos=(-180.587,1999.61,-115.38) rot=(0,0,1;0rad)
  Preset = 1
  Role = 0
  Width = 1000
  WindowParts = OuterFrame | Frame | Wire0,Wire1 | 100.0 | 0.0 | Glass | Glass panel | Wire1 | 10.0 | 50.0
FEATURE [Part::FeaturePython] Wall011  # WARN: FeaturePython — macro-defined, semantics opaque (R4)
  Align = 1
  Base = -> Line011
  Face = 0
  Height = 2900
  Length = 0
  MoveWithHost = false
  Normal = (0,0,0)
  Placement = pos=(0,1999.61,0) rot=(0,0,1;0rad)
  Role = 0
  Subtractions = -> [Window010,Window011]
  Width = 150
FEATURE [Part::Part2DObjectPython] Line180  # Draft 2D object (typed FeaturePython)
  ChamferSize = 0
  Closed = false
  End = (9168,2000.31,0.0001461)
  FilletRadius = 0
  Length = 5688
  MakeFace = true
  Placement = pos=(-4915,0.305262,0.0001461) rot=(0,0,1;0rad)
  Points = (2) [(8395,2000,0),(14083,2000,0)]
  Start = (3480,2000.31,0.0001461)
  Support = -> Wall011
FEATURE [Part::Part2DObjectPython] Line184  # Draft 2D object (typed FeaturePython)
  ChamferSize = 0
  Closed = false
  End = (4205,2000.31,0.0001461)
  FilletRadius = 0
  Length = 1000
  MakeFace = true
  Placement = pos=(-4915,0.305262,0.0001461) rot=(0,0,1;0rad)
  Points = (2) [(9120,2000,1000),(9120,2000,0)]
  Start = (4205,2000.31,1000)
FEATURE [Part::Part2DObjectPython] Line185  # Draft 2D object (typed FeaturePython)
  ChamferSize = 0
  Closed = false
  End = (2755,2000.31,0.0001461)
  FilletRadius = 0
  Length = 1000
  MakeFace = true
  Placement = pos=(-6365,0.305262,0.0001461) rot=(0,0,1;0rad)
  Points = (2) [(9120,2000,1000),(9120,2000,0)]
  Start = (2755,2000.31,1000)
FEATURE [Part::Part2DObjectPython] Line186  # Draft 2D object (typed FeaturePython)
  ChamferSize = 0
  Closed = false
  End = (2030,2000.31,0.0001461)
  FilletRadius = 0
  Length = 1000
  MakeFace = true
  Placement = pos=(-4190,0.305262,0.0001461) rot=(0,0,1;0rad)
  Points = (2) [(6220,2000,1000),(6220,2000,-2.27374e-13)]
  Start = (2030,2000.31,1000)
FEATURE [Part::Part2DObjectPython] Line187  # Draft 2D object (typed FeaturePython)
  ChamferSize = 0
  Closed = false
  End = (-6672,2000.31,0.0001461)
  FilletRadius = 0
  Length = 3377
  MakeFace = true
  Placement = pos=(-4915,0.305262,0.0001461) rot=(0,0,1;0rad)
  Points = (2) [(1620,2000,0),(-1757,2000,0)]
  Start = (-3295,2000.31,0.0001461)
FEATURE [Part::Part2DObjectPython] Line188  # Draft 2D object (typed FeaturePython)
  ChamferSize = 0
  Closed = false
  End = (-6672,2000.31,1000)
  FilletRadius = 0
  Length = 4852
  MakeFace = true
  Placement = pos=(-4915,0.305262,0.0001461) rot=(0,0,1;0rad)
  Points = (2) [(3095,2000,1000),(-1757,2000,1000)]
  Start = (-1820,2000.31,1000)
FEATURE [Sketcher::SketchObject] Sketch019
  Placement = pos=(1545.66,2000,1022.9) rot=(0.57735,-0.57735,0.57735;2.0944rad)
  sketch-geometry (8):
    g0: LineSegment StartX=0 StartY=0 StartZ=0 EndX=1200 EndY=0 EndZ=0
    g1: LineSegment StartX=1200 StartY=0 StartZ=0 EndX=1200 EndY=1000 EndZ=0
    g2: LineSegment StartX=1200 StartY=1000 StartZ=0 EndX=0 EndY=1000 EndZ=0
    g3: LineSegment StartX=0 StartY=1000 StartZ=0 EndX=0 EndY=0 EndZ=0
    g4: LineSegment StartX=50 StartY=50 StartZ=0 EndX=1150 EndY=50 EndZ=0
    g5: LineSegment StartX=1150 StartY=50 StartZ=0 EndX=1150 EndY=950 EndZ=0
    g6: LineSegment StartX=1150 StartY=950 StartZ=0 EndX=50 EndY=950 EndZ=0
    g7: LineSegment StartX=50 StartY=950 StartZ=0 EndX=50 EndY=50 EndZ=0
  constraints (23):
    c: Coincident(g0,g1)
    c: Coincident(g1,g2)
    c: Coincident(g2,g3)
    c: Coincident(g3,g0)
    c: Horizontal(g0)
    c: Horizontal(g2)
    c: Vertical(g1)
    c: Vertical(g3)
    c: Coincident(g4,g5)
    c: Coincident(g5,g6)
    c: Coincident(g6,g7)
    c: Coincident(g7,g4)
    c: Horizontal(g4)
    c: Horizontal(g6)
    c: Vertical(g5)
    c: Vertical(g7)
    c: DistanceY(g1) = 1000
    c: DistanceX(g0) = 1200
    c: DistanceY(g6,g2) = 50
    c: DistanceX(g2,g6) = 50
    c: DistanceX(g4,g0) = 50
    c: DistanceY(g0,g4) = 50
    c: Coincident(g0,g-1)
FEATURE [Part::FeaturePython] Window012  label="Window010"  # WARN: FeaturePython — macro-defined, semantics opaque (R4)
  Base = -> Sketch019
  Height = 1000
  HoleDepth = 0
  MoveWithHost = true
  Normal = (0,1,0)
  Placement = pos=(811.598,0,-22.8969) rot=(0,0,1;0rad)
  Preset = 1
  Role = 0
  Width = 1200
  WindowParts = OuterFrame | Frame | Wire0,Wire1 | 100.0 | 0.0 | Glass | Glass panel | Wire1 | 10.0 | 50.0
FEATURE [Part::FeaturePython] Wall069  # WARN: FeaturePython — macro-defined, semantics opaque (R4)
  Align = 0
  Base = -> Line074
  Face = 0
  Height = 2900
  Length = 0
  MoveWithHost = false
  Normal = (0,0,0)
  Role = 0
  Subtractions = -> [Window012]
  Width = 150
FEATURE [Part::Part2DObjectPython] Line189  # Draft 2D object (typed FeaturePython)
  ChamferSize = 0
  Closed = false
  End = (-3773.13,2000.31,-286)
  FilletRadius = 0
  Length = 1308.9
  MakeFace = true
  Placement = pos=(-4915,0.305262,0.0001461) rot=(0,0,1;0rad)
  Points = (2) [(1141.86,2000,1022.9),(1141.86,2000,-286)]
  Start = (-3773.13,2000.31,1022.9)
  Support = -> Window012
FEATURE [Part::Part2DObjectPython] Line190  # Draft 2D object (typed FeaturePython)
  ChamferSize = 0
  Closed = false
  End = (-2873.13,2000.31,-286)
  FilletRadius = 0
  Length = 1308.9
  MakeFace = true
  Placement = pos=(-4915,0.305262,0.0001461) rot=(0,0,1;0rad)
  Points = (2) [(2041.86,2000,1022.9),(2041.86,2000,-286)]
  Start = (-2873.13,2000.31,1022.9)
FEATURE [Sketcher::SketchObject] Sketch020
  Placement = pos=(983.279,2000,3851.04) rot=(1,0,0;1.5708rad)
  sketch-geometry (8):
    g0: LineSegment StartX=0 StartY=0 StartZ=0 EndX=1000 EndY=0 EndZ=0
    g1: LineSegment StartX=1000 StartY=0 StartZ=0 EndX=1000 EndY=1200 EndZ=0
    g2: LineSegment StartX=1000 StartY=1200 StartZ=0 EndX=0 EndY=1200 EndZ=0
    g3: LineSegment StartX=0 StartY=1200 StartZ=0 EndX=0 EndY=0 EndZ=0
    g4: LineSegment StartX=50 StartY=50 StartZ=0 EndX=950 EndY=50 EndZ=0
    g5: LineSegment StartX=950 StartY=50 StartZ=0 EndX=950 EndY=1150 EndZ=0
    g6: LineSegment StartX=950 StartY=1150 StartZ=0 EndX=50 EndY=1150 EndZ=0
    g7: LineSegment StartX=50 StartY=1150 StartZ=0 EndX=50 EndY=50 EndZ=0
  constraints (23):
    c: Coincident(g0,g1)
    c: Coincident(g1,g2)
    c: Coincident(g2,g3)
    c: Coincident(g3,g0)
    c: Horizontal(g0)
    c: Horizontal(g2)
    c: Vertical(g1)
    c: Vertical(g3)
    c: Coincident(g4,g5)
    c: Coincident(g5,g6)
    c: Coincident(g6,g7)
    c: Coincident(g7,g4)
    c: Horizontal(g4)
    c: Horizontal(g6)
    c: Vertical(g5)
    c: Vertical(g7)
    c: DistanceY(g1) = 1200
    c: DistanceX(g0) = 1000
    c: DistanceY(g6,g2) = 50
    c: DistanceX(g2,g6) = 50
    c: DistanceX(g4,g0) = 50
    c: DistanceY(g0,g4) = 50
    c: Coincident(g0,g-1)
FEATURE [Part::FeaturePython] Window013  label="Window011"  # WARN: FeaturePython — macro-defined, semantics opaque (R4)
  Base = -> Sketch020
  Height = 1200
  HoleDepth = 0
  MoveWithHost = true
  Normal = (0,1,0)
  Placement = pos=(58.7006,0,148.958) rot=(0,0,1;0rad)
  Preset = 1
  Role = 0
  Width = 1000
  WindowParts = OuterFrame | Frame | Wire0,Wire1 | 100.0 | 0.0 | Glass | Glass panel | Wire1 | 10.0 | 50.0
FEATURE [Part::FeaturePython] Wall042  # WARN: FeaturePython — macro-defined, semantics opaque (R4)
  Align = 1
  Base = -> Line007
  Face = 0
  Height = 2800
  Length = 0
  MoveWithHost = false
  Normal = (0,0,0)
  Placement = pos=(0,0,3000) rot=(0,0,1;0rad)
  Role = 0
  Subtractions = -> [Window013]
  Width = 150
FEATURE [Part::Part2DObjectPython] Line191  # Draft 2D object (typed FeaturePython)
  ChamferSize = 0
  Closed = false
  End = (-8347,2000.31,4000)
  FilletRadius = 0
  Length = 7110.34
  MakeFace = true
  Placement = pos=(-4915,0.305262,0.0001461) rot=(0,0,1;0rad)
  Points = (2) [(3678.34,2000,4000),(-3432,2000,4000)]
  Start = (-1236.66,2000.31,4000)
FEATURE [Part::Part2DObjectPython] Line192  # Draft 2D object (typed FeaturePython)
  ChamferSize = 0
  Closed = false
  End = (-3873,2000.31,6263)
  FilletRadius = 0
  Length = 4085.59
  MakeFace = true
  Placement = pos=(-4915,0.305262,0.0001461) rot=(0,0,1;0rad)
  Points = (2) [(1041.86,2000,2177.41),(1042,2000,6263)]
  Start = (-3873.13,2000.31,2177.41)
FEATURE [Sketcher::SketchObject] Sketch023
  Placement = pos=(4360.23,2000,4106.42) rot=(0.57735,-0.57735,0.57735;2.0944rad)
  sketch-geometry (8):
    g0: LineSegment StartX=0 StartY=0 StartZ=0 EndX=1200 EndY=0 EndZ=0
    g1: LineSegment StartX=1200 StartY=0 StartZ=0 EndX=1200 EndY=1000 EndZ=0
    g2: LineSegment StartX=1200 StartY=1000 StartZ=0 EndX=0 EndY=1000 EndZ=0
    g3: LineSegment StartX=0 StartY=1000 StartZ=0 EndX=0 EndY=0 EndZ=0
    g4: LineSegment StartX=50 StartY=50 StartZ=0 EndX=1150 EndY=50 EndZ=0
    g5: LineSegment StartX=1150 StartY=50 StartZ=0 EndX=1150 EndY=950 EndZ=0
    g6: LineSegment StartX=1150 StartY=950 StartZ=0 EndX=50 EndY=950 EndZ=0
    g7: LineSegment StartX=50 StartY=950 StartZ=0 EndX=50 EndY=50 EndZ=0
  constraints (23):
    c: Coincident(g0,g1)
    c: Coincident(g1,g2)
    c: Coincident(g2,g3)
    c: Coincident(g3,g0)
    c: Horizontal(g0)
    c: Horizontal(g2)
    c: Vertical(g1)
    c: Vertical(g3)
    c: Coincident(g4,g5)
    c: Coincident(g5,g6)
    c: Coincident(g6,g7)
    c: Coincident(g7,g4)
    c: Horizontal(g4)
    c: Horizontal(g6)
    c: Vertical(g5)
    c: Vertical(g7)
    c: DistanceY(g1) = 1000
    c: DistanceX(g0) = 1200
    c: DistanceY(g6,g2) = 50
    c: DistanceX(g2,g6) = 50
    c: DistanceX(g4,g0) = 50
    c: DistanceY(g0,g4) = 50
    c: Coincident(g0,g-1)
FEATURE [Part::FeaturePython] Window015  label="Window013"  # WARN: FeaturePython — macro-defined, semantics opaque (R4)
  Base = -> Sketch023
  Height = 1000
  HoleDepth = 0
  MoveWithHost = true
  Normal = (0,1,0)
  Placement = pos=(659.766,0,-107.052) rot=(0,0,1;0rad)
  Preset = 1
  Role = 0
  Width = 1200
  WindowParts = OuterFrame | Frame | Wire0,Wire1 | 100.0 | 0.0 | Glass | Glass panel | Wire1 | 10.0 | 50.0
FEATURE [Part::FeaturePython] Wall023  # WARN: FeaturePython — macro-defined, semantics opaque (R4)
  Align = 0
  Base = -> Line010
  Face = 0
  Height = 2800
  Length = 0
  MoveWithHost = false
  Normal = (0,0,0)
  Role = 0
  Subtractions = -> [Window015]
  Width = 150
FEATURE [Part::Part2DObjectPython] Line193  # Draft 2D object (typed FeaturePython)
  ChamferSize = 0
  Closed = false
  End = (-894.998,2000.31,2270)
  FilletRadius = 0
  Length = 1729.37
  MakeFace = true
  Placement = pos=(-4915,0.305262,0.0001461) rot=(0,0,1;0rad)
  Points = (2) [(4020,2000,3999.37),(4020,2000,2270)]
  Start = (-894.998,2000.31,3999.37)
FEATURE [Sketcher::SketchObject] Sketch024
  Placement = pos=(6684.54,16000,3695.65) rot=(0.57735,0.57735,0.57735;4.18879rad)
  sketch-geometry (8):
    g0: LineSegment StartX=0 StartY=0 StartZ=0 EndX=1200 EndY=0 EndZ=0
    g1: LineSegment StartX=1200 StartY=0 StartZ=0 EndX=1200 EndY=1200 EndZ=0
    g2: LineSegment StartX=1200 StartY=1200 StartZ=0 EndX=0 EndY=1200 EndZ=0
    g3: LineSegment StartX=0 StartY=1200 StartZ=0 EndX=0 EndY=0 EndZ=0
    g4: LineSegment StartX=50 StartY=50 StartZ=0 EndX=1150 EndY=50 EndZ=0
    g5: LineSegment StartX=1150 StartY=50 StartZ=0 EndX=1150 EndY=1150 EndZ=0
    g6: LineSegment StartX=1150 StartY=1150 StartZ=0 EndX=50 EndY=1150 EndZ=0
    g7: LineSegment StartX=50 StartY=1150 StartZ=0 EndX=50 EndY=50 EndZ=0
  constraints (23):
    c: Coincident(g0,g1)
    c: Coincident(g1,g2)
    c: Coincident(g2,g3)
    c: Coincident(g3,g0)
    c: Horizontal(g0)
    c: Horizontal(g2)
    c: Vertical(g1)
    c: Vertical(g3)
    c: Coincident(g4,g5)
    c: Coincident(g5,g6)
    c: Coincident(g6,g7)
    c: Coincident(g7,g4)
    c: Horizontal(g4)
    c: Horizontal(g6)
    c: Vertical(g5)
    c: Vertical(g7)
    c: DistanceY(g1) = 1200
    c: DistanceX(g0) = 1200
    c: DistanceY(g6,g2) = 50
    c: DistanceX(g2,g6) = 50
    c: DistanceX(g4,g0) = 50
    c: DistanceY(g0,g4) = 50
    c: Coincident(g0,g-1)
FEATURE [Part::FeaturePython] Window016  label="Window014"  # WARN: FeaturePython — macro-defined, semantics opaque (R4)
  Base = -> Sketch024
  Height = 1200
  HoleDepth = 0
  MoveWithHost = true
  Normal = (0,-1,0)
  Placement = pos=(-739.539,0,304.351) rot=(0,0,1;0rad)
  Preset = 1
  Role = 0
  Width = 1200
  WindowParts = OuterFrame | Frame | Wire0,Wire1 | 100.0 | 0.0 | Glass | Glass panel | Wire1 | 10.0 | 50.0
FEATURE [Part::FeaturePython] Wall024  # WARN: FeaturePython — macro-defined, semantics opaque (R4)
  Align = 0
  Base = -> Line
  Face = 0
  Height = 2800
  Length = 0
  MoveWithHost = false
  Normal = (0,0,0)
  Placement = pos=(0,0,3000) rot=(0,0,1;0rad)
  Role = 0
  Subtractions = -> [Window016]
  Width = 150
FEATURE [Sketcher::SketchObject] Sketch025
  Placement = pos=(5176.32,16000,3501.5) rot=(0,0.707107,0.707107;3.14159rad)
  sketch-geometry (8):
    g0: LineSegment StartX=0 StartY=0 StartZ=0 EndX=1200 EndY=0 EndZ=0
    g1: LineSegment StartX=1200 StartY=0 StartZ=0 EndX=1200 EndY=1200 EndZ=0
    g2: LineSegment StartX=1200 StartY=1200 StartZ=0 EndX=0 EndY=1200 EndZ=0
    g3: LineSegment StartX=0 StartY=1200 StartZ=0 EndX=0 EndY=0 EndZ=0
    g4: LineSegment StartX=50 StartY=50 StartZ=0 EndX=1150 EndY=50 EndZ=0
    g5: LineSegment StartX=1150 StartY=50 StartZ=0 EndX=1150 EndY=1150 EndZ=0
    g6: LineSegment StartX=1150 StartY=1150 StartZ=0 EndX=50 EndY=1150 EndZ=0
    g7: LineSegment StartX=50 StartY=1150 StartZ=0 EndX=50 EndY=50 EndZ=0
  constraints (23):
    c: Coincident(g0,g1)
    c: Coincident(g1,g2)
    c: Coincident(g2,g3)
    c: Coincident(g3,g0)
    c: Horizontal(g0)
    c: Horizontal(g2)
    c: Vertical(g1)
    c: Vertical(g3)
    c: Coincident(g4,g5)
    c: Coincident(g5,g6)
    c: Coincident(g6,g7)
    c: Coincident(g7,g4)
    c: Horizontal(g4)
    c: Horizontal(g6)
    c: Vertical(g5)
    c: Vertical(g7)
    c: DistanceY(g1) = 1200
    c: DistanceX(g0) = 1200
    c: DistanceY(g6,g2) = 50
    c: DistanceX(g2,g6) = 50
    c: DistanceX(g4,g0) = 50
    c: DistanceY(g0,g4) = 50
    c: Coincident(g0,g-1)
FEATURE [Part::FeaturePython] Window017  label="Window015"  # WARN: FeaturePython — macro-defined, semantics opaque (R4)
  Base = -> Sketch025
  Height = 1200
  HoleDepth = 0
  MoveWithHost = true
  Normal = (0,-1,0)
  Placement = pos=(618.677,0,498.5) rot=(0,0,1;0rad)
  Preset = 1
  Role = 0
  Width = 1200
  WindowParts = OuterFrame | Frame | Wire0,Wire1 | 100.0 | 0.0 | Glass | Glass panel | Wire1 | 10.0 | 50.0
FEATURE [Part::FeaturePython] Wall050  # WARN: FeaturePython — macro-defined, semantics opaque (R4)
  Align = 1
  Base = -> Line031
  Face = 0
  Height = 2800
  Length = 0
  MoveWithHost = false
  Normal = (0,0,0)
  Role = 0
  Subtractions = -> [Window017]
  Width = 150
FEATURE [Sketcher::SketchObject] Sketch026
  Placement = pos=(2156.94,16000,4060.29) rot=(0,0.707107,0.707107;3.14159rad)
  sketch-geometry (8):
    g0: LineSegment StartX=0 StartY=0 StartZ=0 EndX=2950 EndY=0 EndZ=0
    g1: LineSegment StartX=2950 StartY=0 StartZ=0 EndX=2950 EndY=1200 EndZ=0
    g2: LineSegment StartX=2950 StartY=1200 StartZ=0 EndX=0 EndY=1200 EndZ=0
    g3: LineSegment StartX=0 StartY=1200 StartZ=0 EndX=0 EndY=0 EndZ=0
    g4: LineSegment StartX=50 StartY=50 StartZ=0 EndX=2900 EndY=50 EndZ=0
    g5: LineSegment StartX=2900 StartY=50 StartZ=0 EndX=2900 EndY=1150 EndZ=0
    g6: LineSegment StartX=2900 StartY=1150 StartZ=0 EndX=50 EndY=1150 EndZ=0
    g7: LineSegment StartX=50 StartY=1150 StartZ=0 EndX=50 EndY=50 EndZ=0
  constraints (23):
    c: Coincident(g0,g1)
    c: Coincident(g1,g2)
    c: Coincident(g2,g3)
    c: Coincident(g3,g0)
    c: Horizontal(g0)
    c: Horizontal(g2)
    c: Vertical(g1)
    c: Vertical(g3)
    c: Coincident(g4,g5)
    c: Coincident(g5,g6)
    c: Coincident(g6,g7)
    c: Coincident(g7,g4)
    c: Horizontal(g4)
    c: Horizontal(g6)
    c: Vertical(g5)
    c: Vertical(g7)
    c: DistanceY(g1) = 1200
    c: DistanceX(g0) = 2950
    c: DistanceY(g6,g2) = 50
    c: DistanceX(g2,g6) = 50
    c: DistanceX(g4,g0) = 50
    c: DistanceY(g0,g4) = 50
    c: Coincident(g0,g-1)
FEATURE [Part::FeaturePython] Window018  label="Window016"  # WARN: FeaturePython — macro-defined, semantics opaque (R4)
  Base = -> Sketch026
  Height = 1200
  HoleDepth = 0
  MoveWithHost = true
  Normal = (0,-1,0)
  Placement = pos=(938.057,0,-60.292) rot=(0,0,1;0rad)
  Preset = 1
  Role = 0
  Width = 2950
  WindowParts = OuterFrame | Frame | Wire0,Wire1 | 100.0 | 0.0 | Glass | Glass panel | Wire1 | 10.0 | 50.0
FEATURE [Part::FeaturePython] Wall049  # WARN: FeaturePython — macro-defined, semantics opaque (R4)
  Align = 1
  Base = -> Line030
  Face = 0
  Height = 2800
  Length = 0
  MoveWithHost = false
  Normal = (0,0,0)
  Role = 0
  Subtractions = -> [Window018]
  Width = 150
FEATURE [Part::Part2DObjectPython] Line194  # Draft 2D object (typed FeaturePython)
  ChamferSize = 0
  Closed = false
  End = (1030,17748.3,5800)
  FilletRadius = 0
  Length = 1898
  MakeFace = true
  Placement = pos=(-4915,0.305262,0.0001461) rot=(0,0,1;0rad)
  Points = (2) [(5945,15850,5800),(5945,17748,5800)]
  Start = (1030,15850.3,5800)
  Support = -> Wall024
FEATURE [Part::Part2DObjectPython] Line195  # Draft 2D object (typed FeaturePython)
  ChamferSize = 0
  Closed = false
  End = (2230,17748.3,5800)
  FilletRadius = 0
  Length = 1898
  MakeFace = true
  Placement = pos=(-4915,0.305262,0.0001461) rot=(0,0,1;0rad)
  Points = (2) [(7145,15850,5800),(7145,17748,5800)]
  Start = (2230,15850.3,5800)
FEATURE [App::FeaturePython] Dimension005  # Draft dimension (typed FeaturePython)
  Dimline = (1874,17060.3,5800)
  Direction = (0,0,0)
  Distance = 1200
  End = (2230,16799.3,5800)
  Normal = (0,0,1)
  Start = (1030,16799.3,5800)
FEATURE [Part::Part2DObjectPython] Line196  # Draft 2D object (typed FeaturePython)
  ChamferSize = 0
  Closed = false
  End = (-4770,17753.3,5800)
  FilletRadius = 0
  Length = 1753
  MakeFace = true
  Placement = pos=(-4915,0.305262,0.0001461) rot=(0,0,1;0rad)
  Points = (2) [(145,16000,5800),(145,17753,5800)]
  Start = (-4770,16000.3,5800)
  Support = -> Wall049
FEATURE [Part::Part2DObjectPython] Line197  # Draft 2D object (typed FeaturePython)
  ChamferSize = 0
  Closed = false
  End = (-1820,17753.3,5800)
  FilletRadius = 0
  Length = 1753
  MakeFace = true
  Placement = pos=(-4915,0.305262,0.0001461) rot=(0,0,1;0rad)
  Points = (2) [(3095,16000,5800),(3095,17753,5800)]
  Start = (-1820,16000.3,5800)
FEATURE [App::FeaturePython] Dimension006  # Draft dimension (typed FeaturePython)
  Dimline = (-4366,17280.3,5800)
  Direction = (0,0,0)
  Distance = 2950
  End = (-4770,16876.8,5800)
  Normal = (0,0,1)
  Start = (-1820,16876.8,5800)
FEATURE [Part::Part2DObjectPython] Line198  # Draft 2D object (typed FeaturePython)
  ChamferSize = 0
  Closed = false
  End = (-7627.21,16000.3,5045.65)
  FilletRadius = 0
  Length = 8657.21
  MakeFace = true
  Placement = pos=(-4915,0.305262,0.0001461) rot=(0,0,1;0rad)
  Points = (2) [(5945,16000,5045.65),(-2712.21,16000,5045.65)]
  Start = (1030,16000.3,5045.65)
  Support = -> Structure002
FEATURE [Sketcher::SketchObject] Sketch027
  Placement = pos=(7204.4,16000,892.333) rot=(0,0.707107,0.707107;3.14159rad)
  sketch-geometry (8):
    g0: LineSegment StartX=0 StartY=0 StartZ=0 EndX=1200 EndY=0 EndZ=0
    g1: LineSegment StartX=1200 StartY=0 StartZ=0 EndX=1200 EndY=1200 EndZ=0
    g2: LineSegment StartX=1200 StartY=1200 StartZ=0 EndX=0 EndY=1200 EndZ=0
    g3: LineSegment StartX=0 StartY=1200 StartZ=0 EndX=0 EndY=0 EndZ=0
    g4: LineSegment StartX=50 StartY=50 StartZ=0 EndX=1150 EndY=50 EndZ=0
    g5: LineSegment StartX=1150 StartY=50 StartZ=0 EndX=1150 EndY=1150 EndZ=0
    g6: LineSegment StartX=1150 StartY=1150 StartZ=0 EndX=50 EndY=1150 EndZ=0
    g7: LineSegment StartX=50 StartY=1150 StartZ=0 EndX=50 EndY=50 EndZ=0
  constraints (23):
    c: Coincident(g0,g1)
    c: Coincident(g1,g2)
    c: Coincident(g2,g3)
    c: Coincident(g3,g0)
    c: Horizontal(g0)
    c: Horizontal(g2)
    c: Vertical(g1)
    c: Vertical(g3)
    c: Coincident(g4,g5)
    c: Coincident(g5,g6)
    c: Coincident(g6,g7)
    c: Coincident(g7,g4)
    c: Horizontal(g4)
    c: Horizontal(g6)
    c: Vertical(g5)
    c: Vertical(g7)
    c: DistanceY(g1) = 1200
    c: DistanceX(g0) = 1200
    c: DistanceY(g6,g2) = 50
    c: DistanceX(g2,g6) = 50
    c: DistanceX(g4,g0) = 50
    c: DistanceY(g0,g4) = 50
    c: Coincident(g0,g-1)
FEATURE [Part::FeaturePython] Window019  label="Window017"  # WARN: FeaturePython — macro-defined, semantics opaque (R4)
  Base = -> Sketch027
  Height = 1200
  HoleDepth = 0
  MoveWithHost = true
  Normal = (0,-1,0)
  Placement = pos=(-59.4014,0,107.264) rot=(0,0,1;0rad)
  Preset = 1
  Role = 0
  Width = 1200
  WindowParts = OuterFrame | Frame | Wire0,Wire1 | 100.0 | 0.0 | Glass | Glass panel | Wire1 | 10.0 | 50.0
FEATURE [Part::FeaturePython] Wall  # WARN: FeaturePython — macro-defined, semantics opaque (R4)
  Align = 1
  Base = -> Line079
  Face = 0
  Height = 2900
  Length = 0
  MoveWithHost = false
  Normal = (0,0,0)
  Role = 0
  Subtractions = -> [Window019]
  Width = 150
FEATURE [Part::Part2DObjectPython] Line200  # Draft 2D object (typed FeaturePython)
  ChamferSize = 0
  Closed = false
  End = (-4920,-620.272,4000)
  FilletRadius = 0
  Length = 6370.58
  MakeFace = true
  Placement = pos=(-4915,0.305262,0.0001461) rot=(0,0,1;0rad)
  Points = (2) [(-5,5750,4000),(-5,-620.577,4000)]
  Start = (-4920,5750.31,4000)
FEATURE [Part::Part2DObjectPython] Line201  # Draft 2D object (typed FeaturePython)
  ChamferSize = 0
  Closed = false
  End = (-4920,-1734.02,0.0666884)
  FilletRadius = 0
  Length = 7484.33
  MakeFace = true
  Placement = pos=(-4915,0.305262,0.0001461) rot=(0,0,1;0rad)
  Points = (2) [(-5,5750,0),(-5,-1734.33,0.0665423)]
  Start = (-4920,5750.31,0.0001461)
FEATURE [Part::Part2DObjectPython] Line202  # Draft 2D object (typed FeaturePython)
  ChamferSize = 0
  Closed = false
  End = (-4920,-1734.02,1000.07)
  FilletRadius = 0
  Length = 7484.33
  MakeFace = true
  Placement = pos=(-4915,0.305262,0.0001461) rot=(0,0,1;0rad)
  Points = (2) [(-5,5750.01,1000),(-5,-1734.32,1000.07)]
  Start = (-4920,5750.31,1000)
FEATURE [Sketcher::SketchObject] Sketch031
  Placement = pos=(-5,3708.81,1040.01) rot=(0.57735,-0.57735,-0.57735;2.0944rad)
  sketch-geometry (8):
    g0: LineSegment StartX=0 StartY=0 StartZ=0 EndX=500 EndY=0 EndZ=0
    g1: LineSegment StartX=500 StartY=0 StartZ=0 EndX=500 EndY=1200 EndZ=0
    g2: LineSegment StartX=500 StartY=1200 StartZ=0 EndX=0 EndY=1200 EndZ=0
    g3: LineSegment StartX=0 StartY=1200 StartZ=0 EndX=0 EndY=0 EndZ=0
    g4: LineSegment StartX=50 StartY=50 StartZ=0 EndX=450 EndY=50 EndZ=0
    g5: LineSegment StartX=450 StartY=50 StartZ=0 EndX=450 EndY=1150 EndZ=0
    g6: LineSegment StartX=450 StartY=1150 StartZ=0 EndX=50 EndY=1150 EndZ=0
    g7: LineSegment StartX=50 StartY=1150 StartZ=0 EndX=50 EndY=50 EndZ=0
  constraints (23):
    c: Coincident(g0,g1)
    c: Coincident(g1,g2)
    c: Coincident(g2,g3)
    c: Coincident(g3,g0)
    c: Horizontal(g0)
    c: Horizontal(g2)
    c: Vertical(g1)
    c: Vertical(g3)
    c: Coincident(g4,g5)
    c: Coincident(g5,g6)
    c: Coincident(g6,g7)
    c: Coincident(g7,g4)
    c: Horizontal(g4)
    c: Horizontal(g6)
    c: Vertical(g5)
    c: Vertical(g7)
    c: DistanceY(g1) = 1200
    c: DistanceX(g0) = 500
    c: DistanceY(g6,g2) = 50
    c: DistanceX(g2,g6) = 50
    c: DistanceX(g4,g0) = 50
    c: DistanceY(g0,g4) = 50
    c: Coincident(g0,g-1)
FEATURE [Part::FeaturePython] Window024  label="Window022"  # WARN: FeaturePython — macro-defined, semantics opaque (R4)
  Base = -> Sketch031
  Height = 1200
  HoleDepth = 0
  MoveWithHost = true
  Normal = (1,0,0)
  Placement = pos=(0,2041.19,-39.9771) rot=(0,0,1;0rad)
  Preset = 1
  Role = 0
  Width = 500
  WindowParts = OuterFrame | Frame | Wire0,Wire1 | 100.0 | 0.0 | Glass | Glass panel | Wire1 | 10.0 | 50.0
FEATURE [Part::FeaturePython] Wall075  # WARN: FeaturePython — macro-defined, semantics opaque (R4)
  Align = 2
  Base = -> Line080
  Face = 0
  Height = 2900
  Length = 0
  MoveWithHost = false
  Normal = (0,0,0)
  Role = 0
  Subtractions = -> [Window024]
  Width = 150
FEATURE [Sketcher::SketchObject] Sketch032
  Placement = pos=(-5,3336.55,4144.34) rot=(0.57735,-0.57735,-0.57735;2.0944rad)
  sketch-geometry (8):
    g0: LineSegment StartX=0 StartY=0 StartZ=0 EndX=500 EndY=0 EndZ=0
    g1: LineSegment StartX=500 StartY=0 StartZ=0 EndX=500 EndY=1200 EndZ=0
    g2: LineSegment StartX=500 StartY=1200 StartZ=0 EndX=0 EndY=1200 EndZ=0
    g3: LineSegment StartX=0 StartY=1200 StartZ=0 EndX=0 EndY=0 EndZ=0
    g4: LineSegment StartX=50 StartY=50 StartZ=0 EndX=450 EndY=50 EndZ=0
    g5: LineSegment StartX=450 StartY=50 StartZ=0 EndX=450 EndY=1150 EndZ=0
    g6: LineSegment StartX=450 StartY=1150 StartZ=0 EndX=50 EndY=1150 EndZ=0
    g7: LineSegment StartX=50 StartY=1150 StartZ=0 EndX=50 EndY=50 EndZ=0
  constraints (23):
    c: Coincident(g0,g1)
    c: Coincident(g1,g2)
    c: Coincident(g2,g3)
    c: Coincident(g3,g0)
    c: Horizontal(g0)
    c: Horizontal(g2)
    c: Vertical(g1)
    c: Vertical(g3)
    c: Coincident(g4,g5)
    c: Coincident(g5,g6)
    c: Coincident(g6,g7)
    c: Coincident(g7,g4)
    c: Horizontal(g4)
    c: Horizontal(g6)
    c: Vertical(g5)
    c: Vertical(g7)
    c: DistanceY(g1) = 1200
    c: DistanceX(g0) = 500
    c: DistanceY(g6,g2) = 50
    c: DistanceX(g2,g6) = 50
    c: DistanceX(g4,g0) = 50
    c: DistanceY(g0,g4) = 50
    c: Coincident(g0,g-1)
FEATURE [Part::FeaturePython] Window026  label="Window024"  # WARN: FeaturePython — macro-defined, semantics opaque (R4)
  Base = -> Sketch032
  Height = 1200
  HoleDepth = 0
  MoveWithHost = true
  Normal = (1,0,0)
  Placement = pos=(0,2413.45,-144.716) rot=(0,0,1;0rad)
  Preset = 1
  Role = 0
  Width = 500
  WindowParts = OuterFrame | Frame | Wire0,Wire1 | 100.0 | 0.0 | Glass | Glass panel | Wire1 | 10.0 | 50.0
FEATURE [Part::FeaturePython] Wall025  # WARN: FeaturePython — macro-defined, semantics opaque (R4)
  Align = 2
  Base = -> Line013
  Face = 0
  Height = 2800
  Length = 0
  MoveWithHost = false
  Normal = (0,0,0)
  Placement = pos=(0,0,3000) rot=(0,0,1;0rad)
  Role = 0
  Subtractions = -> [Window026]
  Width = 150
FEATURE [Part::Part2DObjectPython] Line199  # Draft 2D object (typed FeaturePython)
  ChamferSize = 0
  Closed = false
  End = (-4920,-620.272,3000)
  FilletRadius = 0
  Length = 6370.58
  MakeFace = true
  Placement = pos=(-4915,0.305262,0.0001461) rot=(0,0,1;0rad)
  Points = (2) [(-5,5750,3000),(-5,-620.577,3000)]
  Start = (-4920,5750.31,3000)
  Support = -> Wall025
FEATURE [Sketcher::SketchObject] Sketch035
  Placement = pos=(-5,8905.43,3845.39) rot=(0,-1,0;1.5708rad)
  sketch-geometry (8):
    g0: LineSegment StartX=0 StartY=0 StartZ=0 EndX=1200 EndY=0 EndZ=0
    g1: LineSegment StartX=1200 StartY=0 StartZ=0 EndX=1200 EndY=500 EndZ=0
    g2: LineSegment StartX=1200 StartY=500 StartZ=0 EndX=0 EndY=500 EndZ=0
    g3: LineSegment StartX=0 StartY=500 StartZ=0 EndX=0 EndY=0 EndZ=0
    g4: LineSegment StartX=50 StartY=50 StartZ=0 EndX=1150 EndY=50 EndZ=0
    g5: LineSegment StartX=1150 StartY=50 StartZ=0 EndX=1150 EndY=450 EndZ=0
    g6: LineSegment StartX=1150 StartY=450 StartZ=0 EndX=50 EndY=450 EndZ=0
    g7: LineSegment StartX=50 StartY=450 StartZ=0 EndX=50 EndY=50 EndZ=0
  constraints (23):
    c: Coincident(g0,g1)
    c: Coincident(g1,g2)
    c: Coincident(g2,g3)
    c: Coincident(g3,g0)
    c: Horizontal(g0)
    c: Horizontal(g2)
    c: Vertical(g1)
    c: Vertical(g3)
    c: Coincident(g4,g5)
    c: Coincident(g5,g6)
    c: Coincident(g6,g7)
    c: Coincident(g7,g4)
    c: Horizontal(g4)
    c: Horizontal(g6)
    c: Vertical(g5)
    c: Vertical(g7)
    c: DistanceY(g1) = 500
    c: DistanceX(g0) = 1200
    c: DistanceY(g6,g2) = 50
    c: DistanceX(g2,g6) = 50
    c: DistanceX(g4,g0) = 50
    c: DistanceY(g0,g4) = 50
    c: Coincident(g0,g-1)
FEATURE [Part::FeaturePython] Window029  label="Window027"  # WARN: FeaturePython — macro-defined, semantics opaque (R4)
  Base = -> Sketch035
  Height = 1000
  HoleDepth = 0
  MoveWithHost = true
  Normal = (1,0,0)
  Placement = pos=(0,-355.431,154.61) rot=(0,0,1;0rad)
  Preset = 1
  Role = 0
  Width = 1000
  WindowParts = OuterFrame | Frame | Wire0,Wire1 | 100.0 | 0.0 | Glass | Glass panel | Wire1 | 10.0 | 50.0
FEATURE [Sketcher::SketchObject] Sketch036
  Placement = pos=(-5,9726.63,950.647) rot=(0.57735,-0.57735,-0.57735;2.0944rad)
  sketch-geometry (8):
    g0: LineSegment StartX=0 StartY=0 StartZ=0 EndX=500 EndY=0 EndZ=0
    g1: LineSegment StartX=500 StartY=0 StartZ=0 EndX=500 EndY=1200 EndZ=0
    g2: LineSegment StartX=500 StartY=1200 StartZ=0 EndX=0 EndY=1200 EndZ=0
    g3: LineSegment StartX=0 StartY=1200 StartZ=0 EndX=0 EndY=0 EndZ=0
    g4: LineSegment StartX=50 StartY=50 StartZ=0 EndX=450 EndY=50 EndZ=0
    g5: LineSegment StartX=450 StartY=50 StartZ=0 EndX=450 EndY=1150 EndZ=0
    g6: LineSegment StartX=450 StartY=1150 StartZ=0 EndX=50 EndY=1150 EndZ=0
    g7: LineSegment StartX=50 StartY=1150 StartZ=0 EndX=50 EndY=50 EndZ=0
  constraints (23):
    c: Coincident(g0,g1)
    c: Coincident(g1,g2)
    c: Coincident(g2,g3)
    c: Coincident(g3,g0)
    c: Horizontal(g0)
    c: Horizontal(g2)
    c: Vertical(g1)
    c: Vertical(g3)
    c: Coincident(g4,g5)
    c: Coincident(g5,g6)
    c: Coincident(g6,g7)
    c: Coincident(g7,g4)
    c: Horizontal(g4)
    c: Horizontal(g6)
    c: Vertical(g5)
    c: Vertical(g7)
    c: DistanceY(g1) = 1200
    c: DistanceX(g0) = 500
    c: DistanceY(g6,g2) = 50
    c: DistanceX(g2,g6) = 50
    c: DistanceX(g4,g0) = 50
    c: DistanceY(g0,g4) = 50
    c: Coincident(g0,g-1)
FEATURE [Part::FeaturePython] Window030  label="Window028"  # WARN: FeaturePython — macro-defined, semantics opaque (R4)
  Base = -> Sketch036
  Height = 1000
  HoleDepth = 0
  MoveWithHost = true
  Normal = (1,0,0)
  Placement = pos=(0,-676.63,49.3897) rot=(0,0,1;0rad)
  Preset = 1
  Role = 0
  Width = 1000
  WindowParts = OuterFrame | Frame | Wire0,Wire1 | 100.0 | 0.0 | Glass | Glass panel | Wire1 | 10.0 | 50.0
FEATURE [Sketcher::SketchObject] Sketch037
  Placement = pos=(-5,11427.7,3858.09) rot=(0.57735,-0.57735,-0.57735;2.0944rad)
  sketch-geometry (8):
    g0: LineSegment StartX=0 StartY=0 StartZ=0 EndX=500 EndY=0 EndZ=0
    g1: LineSegment StartX=500 StartY=0 StartZ=0 EndX=500 EndY=1200 EndZ=0
    g2: LineSegment StartX=500 StartY=1200 StartZ=0 EndX=0 EndY=1200 EndZ=0
    g3: LineSegment StartX=0 StartY=1200 StartZ=0 EndX=0 EndY=0 EndZ=0
    g4: LineSegment StartX=50 StartY=50 StartZ=0 EndX=450 EndY=50 EndZ=0
    g5: LineSegment StartX=450 StartY=50 StartZ=0 EndX=450 EndY=1150 EndZ=0
    g6: LineSegment StartX=450 StartY=1150 StartZ=0 EndX=50 EndY=1150 EndZ=0
    g7: LineSegment StartX=50 StartY=1150 StartZ=0 EndX=50 EndY=50 EndZ=0
  constraints (23):
    c: Coincident(g0,g1)
    c: Coincident(g1,g2)
    c: Coincident(g2,g3)
    c: Coincident(g3,g0)
    c: Horizontal(g0)
    c: Horizontal(g2)
    c: Vertical(g1)
    c: Vertical(g3)
    c: Coincident(g4,g5)
    c: Coincident(g5,g6)
    c: Coincident(g6,g7)
    c: Coincident(g7,g4)
    c: Horizontal(g4)
    c: Horizontal(g6)
    c: Vertical(g5)
    c: Vertical(g7)
    c: DistanceY(g1) = 1200
    c: DistanceX(g0) = 500
    c: DistanceY(g6,g2) = 50
    c: DistanceX(g2,g6) = 50
    c: DistanceX(g4,g0) = 50
    c: DistanceY(g0,g4) = 50
    c: Coincident(g0,g-1)
FEATURE [Part::FeaturePython] Window031  label="Window029"  # WARN: FeaturePython — macro-defined, semantics opaque (R4)
  Base = -> Sketch037
  Height = 1000
  HoleDepth = 0
  MoveWithHost = true
  Normal = (1,0,0)
  Placement = pos=(0,-636.294,141.535) rot=(0,0,1;0rad)
  Preset = 1
  Role = 0
  Width = 1000
  WindowParts = OuterFrame | Frame | Wire0,Wire1 | 100.0 | 0.0 | Glass | Glass panel | Wire1 | 10.0 | 50.0
FEATURE [Sketcher::SketchObject] Sketch038
  Placement = pos=(-5,11630.4,963.774) rot=(0.57735,-0.57735,-0.57735;2.0944rad)
  sketch-geometry (8):
    g0: LineSegment StartX=0 StartY=0 StartZ=0 EndX=1000 EndY=0 EndZ=0
    g1: LineSegment StartX=1000 StartY=0 StartZ=0 EndX=1000 EndY=1200 EndZ=0
    g2: LineSegment StartX=1000 StartY=1200 StartZ=0 EndX=0 EndY=1200 EndZ=0
    g3: LineSegment StartX=0 StartY=1200 StartZ=0 EndX=0 EndY=0 EndZ=0
    g4: LineSegment StartX=50 StartY=50 StartZ=0 EndX=950 EndY=50 EndZ=0
    g5: LineSegment StartX=950 StartY=50 StartZ=0 EndX=950 EndY=1150 EndZ=0
    g6: LineSegment StartX=950 StartY=1150 StartZ=0 EndX=50 EndY=1150 EndZ=0
    g7: LineSegment StartX=50 StartY=1150 StartZ=0 EndX=50 EndY=50 EndZ=0
  constraints (23):
    c: Coincident(g0,g1)
    c: Coincident(g1,g2)
    c: Coincident(g2,g3)
    c: Coincident(g3,g0)
    c: Horizontal(g0)
    c: Horizontal(g2)
    c: Vertical(g1)
    c: Vertical(g3)
    c: Coincident(g4,g5)
    c: Coincident(g5,g6)
    c: Coincident(g6,g7)
    c: Coincident(g7,g4)
    c: Horizontal(g4)
    c: Horizontal(g6)
    c: Vertical(g5)
    c: Vertical(g7)
    c: DistanceY(g1) = 1200
    c: DistanceX(g0) = 1000
    c: DistanceY(g6,g2) = 50
    c: DistanceX(g2,g6) = 50
    c: DistanceX(g4,g0) = 50
    c: DistanceY(g0,g4) = 50
    c: Coincident(g0,g-1)
FEATURE [Part::FeaturePython] Window032  label="Window030"  # WARN: FeaturePython — macro-defined, semantics opaque (R4)
  Base = -> Sketch038
  Height = 1200
  HoleDepth = 0
  MoveWithHost = true
  Normal = (1,0,0)
  Placement = pos=(0,161.051,36.2626) rot=(0,0,1;0rad)
  Preset = 1
  Role = 0
  Width = 1000
  WindowParts = OuterFrame | Frame | Wire0,Wire1 | 100.0 | 0.0 | Glass | Glass panel | Wire1 | 10.0 | 50.0
FEATURE [Part::FeaturePython] Wall072  # WARN: FeaturePython — macro-defined, semantics opaque (R4)
  Align = 2
  Base = -> Line076
  Face = 0
  Height = 2900
  Length = 0
  MoveWithHost = false
  Normal = (0,0,0)
  Role = 0
  Subtractions = -> [Window030,Window032]
  Width = 150
FEATURE [Sketcher::SketchObject] Sketch039
  Placement = pos=(-5,12440.3,3880.54) rot=(0.57735,-0.57735,-0.57735;2.0944rad)
  sketch-geometry (8):
    g0: LineSegment StartX=0 StartY=0 StartZ=0 EndX=570 EndY=0 EndZ=0
    g1: LineSegment StartX=570 StartY=0 StartZ=0 EndX=570 EndY=1200 EndZ=0
    g2: LineSegment StartX=570 StartY=1200 StartZ=0 EndX=0 EndY=1200 EndZ=0
    g3: LineSegment StartX=0 StartY=1200 StartZ=0 EndX=0 EndY=0 EndZ=0
    g4: LineSegment StartX=50 StartY=50 StartZ=0 EndX=520 EndY=50 EndZ=0
    g5: LineSegment StartX=520 StartY=50 StartZ=0 EndX=520 EndY=1150 EndZ=0
    g6: LineSegment StartX=520 StartY=1150 StartZ=0 EndX=50 EndY=1150 EndZ=0
    g7: LineSegment StartX=50 StartY=1150 StartZ=0 EndX=50 EndY=50 EndZ=0
  constraints (23):
    c: Coincident(g0,g1)
    c: Coincident(g1,g2)
    c: Coincident(g2,g3)
    c: Coincident(g3,g0)
    c: Horizontal(g0)
    c: Horizontal(g2)
    c: Vertical(g1)
    c: Vertical(g3)
    c: Coincident(g4,g5)
    c: Coincident(g5,g6)
    c: Coincident(g6,g7)
    c: Coincident(g7,g4)
    c: Horizontal(g4)
    c: Horizontal(g6)
    c: Vertical(g5)
    c: Vertical(g7)
    c: DistanceY(g1) = 1200
    c: DistanceX(g0) = 570
    c: DistanceY(g6,g2) = 50
    c: DistanceX(g2,g6) = 50
    c: DistanceX(g4,g0) = 50
    c: DistanceY(g0,g4) = 50
    c: Coincident(g0,g-1)
FEATURE [Part::FeaturePython] Window033  label="Window031"  # WARN: FeaturePython — macro-defined, semantics opaque (R4)
  Base = -> Sketch039
  Height = 1200
  HoleDepth = 0
  MoveWithHost = true
  Normal = (1,0,0)
  Placement = pos=(0,279.658,119.464) rot=(0,0,1;0rad)
  Preset = 1
  Role = 0
  Width = 570
  WindowParts = OuterFrame | Frame | Wire0,Wire1 | 100.0 | 0.0 | Glass | Glass panel | Wire1 | 10.0 | 50.0
FEATURE [Part::FeaturePython] Wall041  # WARN: FeaturePython — macro-defined, semantics opaque (R4)
  Align = 2
  Base = -> Line015
  Face = 0
  Height = 2800
  Length = 0
  MoveWithHost = false
  Normal = (0,0,0)
  Placement = pos=(0,0,3000) rot=(0,0,1;0rad)
  Role = 0
  Subtractions = -> [Window029,Window031,Window033]
  Width = 150
FEATURE [Sketcher::SketchObject] Sketch041
  Placement = pos=(-5,6454.91,995.958) rot=(0,-1,0;1.5708rad)
  sketch-geometry (8):
    g0: LineSegment StartX=0 StartY=0 StartZ=0 EndX=1200 EndY=0 EndZ=0
    g1: LineSegment StartX=1200 StartY=0 StartZ=0 EndX=1200 EndY=500 EndZ=0
    g2: LineSegment StartX=1200 StartY=500 StartZ=0 EndX=0 EndY=500 EndZ=0
    g3: LineSegment StartX=0 StartY=500 StartZ=0 EndX=0 EndY=0 EndZ=0
    g4: LineSegment StartX=50 StartY=50 StartZ=0 EndX=1150 EndY=50 EndZ=0
    g5: LineSegment StartX=1150 StartY=50 StartZ=0 EndX=1150 EndY=450 EndZ=0
    g6: LineSegment StartX=1150 StartY=450 StartZ=0 EndX=50 EndY=450 EndZ=0
    g7: LineSegment StartX=50 StartY=450 StartZ=0 EndX=50 EndY=50 EndZ=0
  constraints (23):
    c: Coincident(g0,g1)
    c: Coincident(g1,g2)
    c: Coincident(g2,g3)
    c: Coincident(g3,g0)
    c: Horizontal(g0)
    c: Horizontal(g2)
    c: Vertical(g1)
    c: Vertical(g3)
    c: Coincident(g4,g5)
    c: Coincident(g5,g6)
    c: Coincident(g6,g7)
    c: Coincident(g7,g4)
    c: Horizontal(g4)
    c: Horizontal(g6)
    c: Vertical(g5)
    c: Vertical(g7)
    c: DistanceY(g1) = 500
    c: DistanceX(g0) = 1200
    c: DistanceY(g6,g2) = 50
    c: DistanceX(g2,g6) = 50
    c: DistanceX(g4,g0) = 50
    c: DistanceY(g0,g4) = 50
    c: Coincident(g0,g-1)
FEATURE [Part::FeaturePython] Window034  label="Window032"  # WARN: FeaturePython — macro-defined, semantics opaque (R4)
  Base = -> Sketch041
  Height = 500
  HoleDepth = 0
  MoveWithHost = true
  Normal = (1,0,0)
  Placement = pos=(0,1295.09,4.07861) rot=(0,0,1;0rad)
  Preset = 1
  Role = 0
  Width = 1200
  WindowParts = OuterFrame | Frame | Wire0,Wire1 | 100.0 | 0.0 | Glass | Glass panel | Wire1 | 10.0 | 50.0
FEATURE [Part::FeaturePython] Wall077  # WARN: FeaturePython — macro-defined, semantics opaque (R4)
  Align = 2
  Base = -> Line082
  Face = 0
  Height = 2900
  Length = 0
  MoveWithHost = false
  Normal = (0,0,0)
  Role = 0
  Subtractions = -> [Window034]
  Width = 150
FEATURE [Part::Part2DObjectPython] Line203  # Draft 2D object (typed FeaturePython)
  ChamferSize = 0
  Closed = false
  End = (-4920,8250.31,286.666)
  FilletRadius = 0
  Length = 2200
  MakeFace = true
  Placement = pos=(-4915,0.305262,0.0001461) rot=(0,0,1;0rad)
  Points = (2) [(-5,6050,286.666),(-5,8250,286.666)]
  Start = (-4920,6050.31,286.666)
FEATURE [Part::Part2DObjectPython] Line204  # Draft 2D object (typed FeaturePython)
  ChamferSize = 0
  Closed = false
  End = (-4920,8250.73,-967.374)
  FilletRadius = 0
  Length = 1254.04
  MakeFace = true
  Placement = pos=(-4915,0.305262,0.0001461) rot=(0,0,1;0rad)
  Points = (2) [(-5,8250,286.666),(-5,8250.42,-967.374)]
  Start = (-4920,8250.31,286.666)
FEATURE [Part::Part2DObjectPython] Line205  # Draft 2D object (typed FeaturePython)
  ChamferSize = 0
  Closed = false
  End = (-4920,7050.31,-695.847)
  FilletRadius = 0
  Length = 982.513
  MakeFace = true
  Placement = pos=(-4915,0.305262,0.0001461) rot=(0,0,1;0rad)
  Points = (2) [(-5,7050,286.666),(-5,7050,-695.847)]
  Start = (-4920,7050.31,286.666)
FEATURE [App::FeaturePython] Dimension007  # Draft dimension (typed FeaturePython)
  Dimline = (-4565,12213.3,5800)
  Direction = (0,0,0)
  Distance = 570
  End = (-4770,12150.3,5800)
  Normal = (0,0,1)
  Start = (-4770,12720.3,5800)
FEATURE [Sketcher::SketchObject] Sketch042
  Placement = pos=(10995,10155.1,905.079) rot=(0.57735,0.57735,0.57735;2.0944rad)
  sketch-geometry (8):
    g0: LineSegment StartX=0 StartY=0 StartZ=0 EndX=1000 EndY=0 EndZ=0
    g1: LineSegment StartX=1000 StartY=0 StartZ=0 EndX=1000 EndY=1200 EndZ=0
    g2: LineSegment StartX=1000 StartY=1200 StartZ=0 EndX=0 EndY=1200 EndZ=0
    g3: LineSegment StartX=0 StartY=1200 StartZ=0 EndX=0 EndY=0 EndZ=0
    g4: LineSegment StartX=50 StartY=50 StartZ=0 EndX=950 EndY=50 EndZ=0
    g5: LineSegment StartX=950 StartY=50 StartZ=0 EndX=950 EndY=1150 EndZ=0
    g6: LineSegment StartX=950 StartY=1150 StartZ=0 EndX=50 EndY=1150 EndZ=0
    g7: LineSegment StartX=50 StartY=1150 StartZ=0 EndX=50 EndY=50 EndZ=0
  constraints (23):
    c: Coincident(g0,g1)
    c: Coincident(g1,g2)
    c: Coincident(g2,g3)
    c: Coincident(g3,g0)
    c: Horizontal(g0)
    c: Horizontal(g2)
    c: Vertical(g1)
    c: Vertical(g3)
    c: Coincident(g4,g5)
    c: Coincident(g5,g6)
    c: Coincident(g6,g7)
    c: Coincident(g7,g4)
    c: Horizontal(g4)
    c: Horizontal(g6)
    c: Vertical(g5)
    c: Vertical(g7)
    c: DistanceY(g1) = 1200
    c: DistanceX(g0) = 1000
    c: DistanceY(g6,g2) = 50
    c: DistanceX(g2,g6) = 50
    c: DistanceX(g4,g0) = 50
    c: DistanceY(g0,g4) = 50
    c: Coincident(g0,g-1)
FEATURE [Part::FeaturePython] Window035  label="Window033"  # WARN: FeaturePython — macro-defined, semantics opaque (R4)
  Base = -> Sketch042
  Height = 1200
  HoleDepth = 0
  MoveWithHost = true
  Normal = (-1,0,0)
  Placement = pos=(0,1044.94,92.5956) rot=(0,0,1;0rad)
  Preset = 1
  Role = 0
  Width = 1000
  WindowParts = OuterFrame | Frame | Wire0,Wire1 | 100.0 | 0.0 | Glass | Glass panel | Wire1 | 10.0 | 50.0
FEATURE [Part::Part2DObjectPython] Line206  # Draft 2D object (typed FeaturePython)
  ChamferSize = 0
  Closed = false
  End = (6005,8250.31,-99.9999)
  FilletRadius = 0
  Length = 2200
  MakeFace = true
  Placement = pos=(-4915,2500.31,-99.9999) rot=(0,0,1;0rad)
  Points = (2) [(10920,3550,0),(10920,5750,0)]
  Start = (6005,6050.31,-99.9999)
FEATURE [Part::FeaturePython] Wall080  # WARN: FeaturePython — macro-defined, semantics opaque (R4)
  Align = 2
  Base = -> Line206
  Face = 0
  Height = 2900
  Length = 0
  MoveWithHost = false
  Normal = (0,0,0)
  Placement = pos=(4915,-0.305262,0) rot=(0,0,1;0rad)
  Role = 0
  Width = 150
FEATURE [Part::Part2DObjectPython] Line207  # Draft 2D object (typed FeaturePython)
  ChamferSize = 0
  Closed = false
  End = (11371.7,16000.3,-0.403116)
  FilletRadius = 0
  Length = 7891.69
  MakeFace = true
  Placement = pos=(-4915,0.305262,0.0001461) rot=(0,0,1;0rad)
  Points = (2) [(8395,16000,0),(16286.7,16000,-0.403262)]
  Start = (3480,16000.3,0.0001461)
FEATURE [Part::Part2DObjectPython] Line208  # Draft 2D object (typed FeaturePython)
  ChamferSize = 0
  Closed = false
  End = (11371.7,16000.3,999.597)
  FilletRadius = 0
  Length = 10341.7
  MakeFace = true
  Placement = pos=(-4915,0.305262,0.0001461) rot=(0,0,1;0rad)
  Points = (2) [(5945,16000,1000.13),(16286.7,16000,999.597)]
  Start = (1030,16000.3,1000.13)
FEATURE [Part::Part2DObjectPython] Line209  # Draft 2D object (typed FeaturePython)
  ChamferSize = 0
  Closed = false
  End = (-9097.1,16000.3,3000)
  FilletRadius = 0
  Length = 9977.1
  MakeFace = true
  Placement = pos=(-4915,0.305262,0.0001461) rot=(0,0,1;0rad)
  Points = (2) [(5795,16000,3000),(-4182.1,16000,3000)]
  Start = (880.002,16000.3,3000)
  Support = -> Wall050
FEATURE [Part::Part2DObjectPython] Line210  # Draft 2D object (typed FeaturePython)
  ChamferSize = 0
  Closed = false
  End = (-9097.1,16000.3,4000)
  FilletRadius = 0
  Length = 9977.1
  MakeFace = true
  Placement = pos=(-4915,0.305262,0.0001461) rot=(0,0,1;0rad)
  Points = (2) [(5795,16000,4000),(-4182.1,16000,4000)]
  Start = (880.002,16000.3,4000)
FEATURE [Sketcher::SketchObject] Sketch046
  Placement = pos=(4595,13103.3,0.909169) rot=(0.57735,0.57735,0.57735;2.0944rad)
  sketch-geometry (8):
    g0: LineSegment StartX=0 StartY=0 StartZ=0 EndX=1000 EndY=0 EndZ=0
    g1: LineSegment StartX=1000 StartY=0 StartZ=0 EndX=1000 EndY=2200 EndZ=0
    g2: LineSegment StartX=1000 StartY=2200 StartZ=0 EndX=0 EndY=2200 EndZ=0
    g3: LineSegment StartX=0 StartY=2200 StartZ=0 EndX=0 EndY=0 EndZ=0
    g4: LineSegment StartX=50 StartY=0 StartZ=0 EndX=950 EndY=0 EndZ=0
    g5: LineSegment StartX=950 StartY=0 StartZ=0 EndX=950 EndY=2150 EndZ=0
    g6: LineSegment StartX=950 StartY=2150 StartZ=0 EndX=50 EndY=2150 EndZ=0
    g7: LineSegment StartX=50 StartY=2150 StartZ=0 EndX=50 EndY=0 EndZ=0
  constraints (23):
    c: Coincident(g0,g1)
    c: Coincident(g1,g2)
    c: Coincident(g2,g3)
    c: Coincident(g3,g0)
    c: Horizontal(g0)
    c: Horizontal(g2)
    c: Vertical(g1)
    c: Vertical(g3)
    c: Coincident(g4,g5)
    c: Coincident(g5,g6)
    c: Coincident(g6,g7)
    c: Coincident(g7,g4)
    c: Horizontal(g4)
    c: Horizontal(g6)
    c: Vertical(g5)
    c: Vertical(g7)
    c: DistanceY(g1) = 2200
    c: DistanceX(g0) = 1000
    c: DistanceY(g6,g2) = 50
    c: DistanceX(g2,g6) = 50
    c: DistanceX(g4,g0) = 50
    c: DistanceY(g0,g4) = 0
    c: Coincident(g0,g-1)
FEATURE [Part::FeaturePython] Window038  label="Window036"  # WARN: FeaturePython — macro-defined, semantics opaque (R4)
  Base = -> Sketch046
  Height = 2200
  HoleDepth = 0
  MoveWithHost = true
  Normal = (-1,0,0)
  Placement = pos=(-1350.34,16.7129,-0.909169) rot=(0,0,1;0rad)
  Preset = 6
  Role = 1
  Width = 1000
  WindowParts = OuterFrame | Frame | Wire0,Wire1 | 150.0 | 0.0 | Door | Solid panel | Wire1 | 50.0 | 50.0
FEATURE [Part::FeaturePython] Wall061  # WARN: FeaturePython — macro-defined, semantics opaque (R4)
  Align = 2
  Base = -> Line062
  Face = 0
  Height = 2900
  Length = 0
  MoveWithHost = false
  Normal = (0,0,0)
  Placement = pos=(-1350.34,0,0) rot=(0,0,1;0rad)
  Role = 0
  Subtractions = -> [Window038]
  Width = 150
FEATURE [Sketcher::SketchObject] Sketch048
  Placement = pos=(7145,9592.53,3262.68) rot=(0.57735,-0.57735,-0.57735;2.0944rad)
  sketch-geometry (8):
    g0: LineSegment StartX=0 StartY=0 StartZ=0 EndX=1000 EndY=0 EndZ=0
    g1: LineSegment StartX=1000 StartY=0 StartZ=0 EndX=1000 EndY=2200 EndZ=0
    g2: LineSegment StartX=1000 StartY=2200 StartZ=0 EndX=0 EndY=2200 EndZ=0
    g3: LineSegment StartX=0 StartY=2200 StartZ=0 EndX=0 EndY=0 EndZ=0
    g4: LineSegment StartX=50 StartY=0 StartZ=0 EndX=950 EndY=0 EndZ=0
    g5: LineSegment StartX=950 StartY=0 StartZ=0 EndX=950 EndY=2150 EndZ=0
    g6: LineSegment StartX=950 StartY=2150 StartZ=0 EndX=50 EndY=2150 EndZ=0
    g7: LineSegment StartX=50 StartY=2150 StartZ=0 EndX=50 EndY=0 EndZ=0
  constraints (23):
    c: Coincident(g0,g1)
    c: Coincident(g1,g2)
    c: Coincident(g2,g3)
    c: Coincident(g3,g0)
    c: Horizontal(g0)
    c: Horizontal(g2)
    c: Vertical(g1)
    c: Vertical(g3)
    c: Coincident(g4,g5)
    c: Coincident(g5,g6)
    c: Coincident(g6,g7)
    c: Coincident(g7,g4)
    c: Horizontal(g4)
    c: Horizontal(g6)
    c: Vertical(g5)
    c: Vertical(g7)
    c: DistanceY(g1) = 2200
    c: DistanceX(g0) = 1000
    c: DistanceY(g6,g2) = 50
    c: DistanceX(g2,g6) = 50
    c: DistanceX(g4,g0) = 50
    c: DistanceY(g0,g4) = 0
    c: Coincident(g0,g-1)
FEATURE [Part::FeaturePython] Window040  label="Window038"  # WARN: FeaturePython — macro-defined, semantics opaque (R4)
  Base = -> Sketch048
  Height = 2200
  HoleDepth = 0
  MoveWithHost = true
  Normal = (1,0,0)
  Placement = pos=(0,357.471,-262.678) rot=(0,0,1;0rad)
  Preset = 6
  Role = 1
  Width = 1000
  WindowParts = OuterFrame | Frame | Wire0,Wire1 | 150.0 | 0.0 | Door | Solid panel | Wire1 | 50.0 | 50.0
FEATURE [Sketcher::SketchObject] Sketch051
  Placement = pos=(7145,11348.3,3088.52) rot=(0.57735,-0.57735,-0.57735;2.0944rad)
  sketch-geometry (8):
    g0: LineSegment StartX=0 StartY=0 StartZ=0 EndX=1000 EndY=0 EndZ=0
    g1: LineSegment StartX=1000 StartY=0 StartZ=0 EndX=1000 EndY=2200 EndZ=0
    g2: LineSegment StartX=1000 StartY=2200 StartZ=0 EndX=0 EndY=2200 EndZ=0
    g3: LineSegment StartX=0 StartY=2200 StartZ=0 EndX=0 EndY=0 EndZ=0
    g4: LineSegment StartX=50 StartY=0 StartZ=0 EndX=950 EndY=0 EndZ=0
    g5: LineSegment StartX=950 StartY=0 StartZ=0 EndX=950 EndY=2150 EndZ=0
    g6: LineSegment StartX=950 StartY=2150 StartZ=0 EndX=50 EndY=2150 EndZ=0
    g7: LineSegment StartX=50 StartY=2150 StartZ=0 EndX=50 EndY=0 EndZ=0
  constraints (23):
    c: Coincident(g0,g1)
    c: Coincident(g1,g2)
    c: Coincident(g2,g3)
    c: Coincident(g3,g0)
    c: Horizontal(g0)
    c: Horizontal(g2)
    c: Vertical(g1)
    c: Vertical(g3)
    c: Coincident(g4,g5)
    c: Coincident(g5,g6)
    c: Coincident(g6,g7)
    c: Coincident(g7,g4)
    c: Horizontal(g4)
    c: Horizontal(g6)
    c: Vertical(g5)
    c: Vertical(g7)
    c: DistanceY(g1) = 2200
    c: DistanceX(g0) = 1000
    c: DistanceY(g6,g2) = 50
    c: DistanceX(g2,g6) = 50
    c: DistanceX(g4,g0) = 50
    c: DistanceY(g0,g4) = 0
    c: Coincident(g0,g-1)
FEATURE [Part::FeaturePython] Window041  label="Window039"  # WARN: FeaturePython — macro-defined, semantics opaque (R4)
  Base = -> Sketch051
  Height = 2200
  HoleDepth = 0
  MoveWithHost = true
  Normal = (1,0,0)
  Placement = pos=(0,-51.0527,-88.5159) rot=(0,0,1;0rad)
  Preset = 6
  Role = 1
  Width = 1000
  WindowParts = OuterFrame | Frame | Wire0,Wire1 | 150.0 | 0.0 | Door | Solid panel | Wire1 | 50.0 | 50.0
FEATURE [Sketcher::SketchObject] Sketch052
  Placement = pos=(7145,13328.9,3078.96) rot=(0.57735,-0.57735,-0.57735;2.0944rad)
  sketch-geometry (8):
    g0: LineSegment StartX=0 StartY=0 StartZ=0 EndX=1000 EndY=0 EndZ=0
    g1: LineSegment StartX=1000 StartY=0 StartZ=0 EndX=1000 EndY=2200 EndZ=0
    g2: LineSegment StartX=1000 StartY=2200 StartZ=0 EndX=0 EndY=2200 EndZ=0
    g3: LineSegment StartX=0 StartY=2200 StartZ=0 EndX=0 EndY=0 EndZ=0
    g4: LineSegment StartX=50 StartY=0 StartZ=0 EndX=950 EndY=0 EndZ=0
    g5: LineSegment StartX=950 StartY=0 StartZ=0 EndX=950 EndY=2150 EndZ=0
    g6: LineSegment StartX=950 StartY=2150 StartZ=0 EndX=50 EndY=2150 EndZ=0
    g7: LineSegment StartX=50 StartY=2150 StartZ=0 EndX=50 EndY=0 EndZ=0
  constraints (23):
    c: Coincident(g0,g1)
    c: Coincident(g1,g2)
    c: Coincident(g2,g3)
    c: Coincident(g3,g0)
    c: Horizontal(g0)
    c: Horizontal(g2)
    c: Vertical(g1)
    c: Vertical(g3)
    c: Coincident(g4,g5)
    c: Coincident(g5,g6)
    c: Coincident(g6,g7)
    c: Coincident(g7,g4)
    c: Horizontal(g4)
    c: Horizontal(g6)
    c: Vertical(g5)
    c: Vertical(g7)
    c: DistanceY(g1) = 2200
    c: DistanceX(g0) = 1000
    c: DistanceY(g6,g2) = 50
    c: DistanceX(g2,g6) = 50
    c: DistanceX(g4,g0) = 50
    c: DistanceY(g0,g4) = 0
    c: Coincident(g0,g-1)
FEATURE [Part::FeaturePython] Window042  label="Window040"  # WARN: FeaturePython — macro-defined, semantics opaque (R4)
  Base = -> Sketch052
  Height = 2200
  HoleDepth = 0
  MoveWithHost = true
  Normal = (1,0,0)
  Placement = pos=(0,-383.989,-78.9607) rot=(0,0,1;0rad)
  Preset = 6
  Role = 1
  Width = 1000
  WindowParts = OuterFrame | Frame | Wire0,Wire1 | 150.0 | 0.0 | Door | Solid panel | Wire1 | 50.0 | 50.0
FEATURE [Part::FeaturePython] Wall052  # WARN: FeaturePython — macro-defined, semantics opaque (R4)
  Align = 1
  Base = -> Line040
  Face = 0
  Height = 2800
  Length = 0
  MoveWithHost = false
  Normal = (0,0,0)
  Role = 0
  Subtractions = -> [Window040,Window041,Window042]
  Width = 150
FEATURE [Sketcher::SketchObject] Sketch053
  Placement = pos=(4043.83,12150,3125.58) rot=(0,0.707107,0.707107;3.14159rad)
  sketch-geometry (8):
    g0: LineSegment StartX=0 StartY=0 StartZ=0 EndX=1000 EndY=0 EndZ=0
    g1: LineSegment StartX=1000 StartY=0 StartZ=0 EndX=1000 EndY=2200 EndZ=0
    g2: LineSegment StartX=1000 StartY=2200 StartZ=0 EndX=0 EndY=2200 EndZ=0
    g3: LineSegment StartX=0 StartY=2200 StartZ=0 EndX=0 EndY=0 EndZ=0
    g4: LineSegment StartX=50 StartY=0 StartZ=0 EndX=950 EndY=0 EndZ=0
    g5: LineSegment StartX=950 StartY=0 StartZ=0 EndX=950 EndY=2150 EndZ=0
    g6: LineSegment StartX=950 StartY=2150 StartZ=0 EndX=50 EndY=2150 EndZ=0
    g7: LineSegment StartX=50 StartY=2150 StartZ=0 EndX=50 EndY=0 EndZ=0
  constraints (23):
    c: Coincident(g0,g1)
    c: Coincident(g1,g2)
    c: Coincident(g2,g3)
    c: Coincident(g3,g0)
    c: Horizontal(g0)
    c: Horizontal(g2)
    c: Vertical(g1)
    c: Vertical(g3)
    c: Coincident(g4,g5)
    c: Coincident(g5,g6)
    c: Coincident(g6,g7)
    c: Coincident(g7,g4)
    c: Horizontal(g4)
    c: Horizontal(g6)
    c: Vertical(g5)
    c: Vertical(g7)
    c: DistanceY(g1) = 2200
    c: DistanceX(g0) = 1000
    c: DistanceY(g6,g2) = 50
    c: DistanceX(g2,g6) = 50
    c: DistanceX(g4,g0) = 50
    c: DistanceY(g0,g4) = 0
    c: Coincident(g0,g-1)
FEATURE [Part::FeaturePython] Window043  label="Window041"  # WARN: FeaturePython — macro-defined, semantics opaque (R4)
  Base = -> Sketch053
  Height = 2200
  HoleDepth = 0
  MoveWithHost = true
  Normal = (0,-1,0)
  Placement = pos=(301.167,0,-125.582) rot=(0,0,1;0rad)
  Preset = 6
  Role = 1
  Width = 1000
  WindowParts = OuterFrame | Frame | Wire0,Wire1 | 150.0 | 0.0 | Door | Solid panel | Wire1 | 50.0 | 50.0
FEATURE [Part::FeaturePython] Wall037  # WARN: FeaturePython — macro-defined, semantics opaque (R4)
  Align = 0
  Base = -> Line019
  Face = 0
  Height = 2800
  Length = 0
  MoveWithHost = false
  Normal = (0,0,0)
  Role = 0
  Subtractions = -> [Window043]
  Width = 150
FEATURE [Sketcher::SketchObject] Sketch054
  Placement = pos=(6098.78,5900,3053.06) rot=(1,0,0;1.5708rad)
  sketch-geometry (16):
    g0: LineSegment StartX=0 StartY=0 StartZ=0 EndX=1000 EndY=0 EndZ=0
    g1: LineSegment StartX=1000 StartY=0 StartZ=0 EndX=1000 EndY=2200 EndZ=0
    g2: LineSegment StartX=1000 StartY=2200 StartZ=0 EndX=0 EndY=2200 EndZ=0
    g3: LineSegment StartX=0 StartY=2200 StartZ=0 EndX=0 EndY=0 EndZ=0
    g4: LineSegment StartX=50 StartY=0 StartZ=0 EndX=950 EndY=0 EndZ=0
    g5: LineSegment StartX=950 StartY=0 StartZ=0 EndX=950 EndY=2150 EndZ=0
    g6: LineSegment StartX=950 StartY=2150 StartZ=0 EndX=50 EndY=2150 EndZ=0
    g7: LineSegment StartX=50 StartY=2150 StartZ=0 EndX=50 EndY=0 EndZ=0
    g8: LineSegment StartX=55 StartY=5 StartZ=0 EndX=945 EndY=5 EndZ=0
    g9: LineSegment StartX=945 StartY=5 StartZ=0 EndX=945 EndY=2145 EndZ=0
    g10: LineSegment StartX=945 StartY=2145 StartZ=0 EndX=55 EndY=2145 EndZ=0
    g11: LineSegment StartX=55 StartY=2145 StartZ=0 EndX=55 EndY=5 EndZ=0
    g12: LineSegment StartX=105 StartY=55 StartZ=0 EndX=895 EndY=55 EndZ=0
    g13: LineSegment StartX=895 StartY=55 StartZ=0 EndX=895 EndY=2095 EndZ=0
    g14: LineSegment StartX=895 StartY=2095 StartZ=0 EndX=105 EndY=2095 EndZ=0
    g15: LineSegment StartX=105 StartY=2095 StartZ=0 EndX=105 EndY=55 EndZ=0
  constraints (47):
    c: Coincident(g0,g1)
    c: Coincident(g1,g2)
    c: Coincident(g2,g3)
    c: Coincident(g3,g0)
    c: Horizontal(g0)
    c: Horizontal(g2)
    c: Vertical(g1)
    c: Vertical(g3)
    c: Coincident(g4,g5)
    c: Coincident(g5,g6)
    c: Coincident(g6,g7)
    c: Coincident(g7,g4)
    c: Horizontal(g4)
    c: Horizontal(g6)
    c: Vertical(g5)
    c: Vertical(g7)
    c: DistanceY(g1) = 2200
    c: DistanceX(g0) = 1000
    c: DistanceY(g6,g2) = 50
    c: DistanceX(g2,g6) = 50
    c: DistanceX(g4,g0) = 50
    c: DistanceY(g0,g4) = 0
    c: Coincident(g0,g-1)
    c: Coincident(g8,g9)
    c: Coincident(g9,g10)
    c: Coincident(g10,g11)
    c: Coincident(g11,g8)
    c: Horizontal(g8)
    c: Horizontal(g10)
    c: Vertical(g9)
    c: Vertical(g11)
    c: Coincident(g12,g13)
    c: Coincident(g13,g14)
    c: Coincident(g14,g15)
    c: Coincident(g15,g12)
    c: Horizontal(g12)
    c: Horizontal(g14)
    c: Vertical(g13)
    c: Vertical(g15)
    c: DistanceX(g8,g12) = 50
    c: DistanceY(g8,g12) = 50
    c: DistanceX(g14,g10) = 50
    c: DistanceY(g14,g10) = 50
    c: DistanceX(g4,g8) = 5
    c: DistanceY(g4,g8) = 5
    c: DistanceX(g10,g6) = 5
    c: DistanceY(g10,g6) = 5
FEATURE [Part::FeaturePython] Window044  label="Window042"  # WARN: FeaturePython — macro-defined, semantics opaque (R4)
  Base = -> Sketch054
  Height = 2200
  HoleDepth = 0
  MoveWithHost = true
  Normal = (0,1,0)
  Placement = pos=(-53.7827,0,-53.0642) rot=(0,0,1;0rad)
  Preset = 7
  Role = 1
  Width = 1000
  WindowParts = OuterFrame | Frame | Wire0,Wire1 | 150.0 | 0.0 | InnerFrame | Frame | Wire2,Wire3 | 50.0 | 50.0 | InnerGlass | Glass panel | Wire3 | 10.0 | 70.0
FEATURE [Part::FeaturePython] Wall047  # WARN: FeaturePython — macro-defined, semantics opaque (R4)
  Align = 1
  Base = -> Line028
  Face = 0
  Height = 2800
  Length = 0
  MoveWithHost = false
  Normal = (0,0,0)
  Role = 0
  Subtractions = -> [Window044]
  Width = 150
FEATURE [Sketcher::SketchObject] Sketch055
  Placement = pos=(3397.14,9600,136.121) rot=(1,0,0;1.5708rad)
  sketch-geometry (8):
    g0: LineSegment StartX=0 StartY=0 StartZ=0 EndX=1000 EndY=0 EndZ=0
    g1: LineSegment StartX=1000 StartY=0 StartZ=0 EndX=1000 EndY=2000 EndZ=0
    g2: LineSegment StartX=1000 StartY=2000 StartZ=0 EndX=0 EndY=2000 EndZ=0
    g3: LineSegment StartX=0 StartY=2000 StartZ=0 EndX=0 EndY=0 EndZ=0
    g4: LineSegment StartX=50 StartY=0 StartZ=0 EndX=950 EndY=0 EndZ=0
    g5: LineSegment StartX=950 StartY=0 StartZ=0 EndX=950 EndY=1950 EndZ=0
    g6: LineSegment StartX=950 StartY=1950 StartZ=0 EndX=50 EndY=1950 EndZ=0
    g7: LineSegment StartX=50 StartY=1950 StartZ=0 EndX=50 EndY=0 EndZ=0
  constraints (23):
    c: Coincident(g0,g1)
    c: Coincident(g1,g2)
    c: Coincident(g2,g3)
    c: Coincident(g3,g0)
    c: Horizontal(g0)
    c: Horizontal(g2)
    c: Vertical(g1)
    c: Vertical(g3)
    c: Coincident(g4,g5)
    c: Coincident(g5,g6)
    c: Coincident(g6,g7)
    c: Coincident(g7,g4)
    c: Horizontal(g4)
    c: Horizontal(g6)
    c: Vertical(g5)
    c: Vertical(g7)
    c: DistanceY(g1) = 2000
    c: DistanceX(g0) = 1000
    c: DistanceY(g6,g2) = 50
    c: DistanceX(g2,g6) = 50
    c: DistanceX(g4,g0) = 50
    c: DistanceY(g0,g4) = 0
    c: Coincident(g0,g-1)
FEATURE [Part::FeaturePython] Window045  label="Window043"  # WARN: FeaturePython — macro-defined, semantics opaque (R4)
  Base = -> Sketch055
  Height = 2000
  HoleDepth = 0
  MoveWithHost = true
  Normal = (0,1,0)
  Placement = pos=(-52.1445,0,-136.121) rot=(0,0,1;0rad)
  Preset = 6
  Role = 1
  Width = 1000
  WindowParts = OuterFrame | Frame | Wire0,Wire1 | 150.0 | 0.0 | Door | Solid panel | Wire1 | 50.0 | 50.0
FEATURE [Part::FeaturePython] Wall066  # WARN: FeaturePython — macro-defined, semantics opaque (R4)
  Align = 1
  Base = -> Line071
  Face = 0
  Height = 2900
  Length = 0
  MoveWithHost = false
  Normal = (0,0,0)
  Role = 0
  Subtractions = -> [Window045]
  Width = 150
FEATURE [Sketcher::SketchObject] Sketch056
  Placement = pos=(3095,9472.37,101.752) rot=(0.57735,-0.57735,-0.57735;2.0944rad)
  sketch-geometry (8):
    g0: LineSegment StartX=0 StartY=0 StartZ=0 EndX=900 EndY=0 EndZ=0
    g1: LineSegment StartX=900 StartY=0 StartZ=0 EndX=900 EndY=2000 EndZ=0
    g2: LineSegment StartX=900 StartY=2000 StartZ=0 EndX=0 EndY=2000 EndZ=0
    g3: LineSegment StartX=0 StartY=2000 StartZ=0 EndX=0 EndY=0 EndZ=0
    g4: LineSegment StartX=50 StartY=0 StartZ=0 EndX=850 EndY=0 EndZ=0
    g5: LineSegment StartX=850 StartY=0 StartZ=0 EndX=850 EndY=1950 EndZ=0
    g6: LineSegment StartX=850 StartY=1950 StartZ=0 EndX=50 EndY=1950 EndZ=0
    g7: LineSegment StartX=50 StartY=1950 StartZ=0 EndX=50 EndY=0 EndZ=0
  constraints (23):
    c: Coincident(g0,g1)
    c: Coincident(g1,g2)
    c: Coincident(g2,g3)
    c: Coincident(g3,g0)
    c: Horizontal(g0)
    c: Horizontal(g2)
    c: Vertical(g1)
    c: Vertical(g3)
    c: Coincident(g4,g5)
    c: Coincident(g5,g6)
    c: Coincident(g6,g7)
    c: Coincident(g7,g4)
    c: Horizontal(g4)
    c: Horizontal(g6)
    c: Vertical(g5)
    c: Vertical(g7)
    c: DistanceY(g1) = 2000
    c: DistanceX(g0) = 900
    c: DistanceY(g6,g2) = 50
    c: DistanceX(g2,g6) = 50
    c: DistanceX(g4,g0) = 50
    c: DistanceY(g0,g4) = 0
    c: Coincident(g0,g-1)
FEATURE [Part::FeaturePython] Window046  label="Window044"  # WARN: FeaturePython — macro-defined, semantics opaque (R4)
  Base = -> Sketch056
  Height = 2000
  HoleDepth = 0
  MoveWithHost = true
  Normal = (1,0,0)
  Placement = pos=(0,27.626,-101.752) rot=(0,0,1;0rad)
  Preset = 6
  Role = 1
  Width = 900
  WindowParts = OuterFrame | Frame | Wire0,Wire1 | 150.0 | 0.0 | Door | Solid panel | Wire1 | 50.0 | 50.0
FEATURE [Part::FeaturePython] Wall063  # WARN: FeaturePython — macro-defined, semantics opaque (R4)
  Align = 2
  Base = -> Line064
  Face = 0
  Height = 2900
  Length = 0
  MoveWithHost = false
  Normal = (0,0,0)
  Role = 0
  Subtractions = -> [Window046]
  Width = 150
FEATURE [Sketcher::SketchObject] Sketch057
  Placement = pos=(1889.83,6500,142.361) rot=(1,0,0;1.5708rad)
  sketch-geometry (8):
    g0: LineSegment StartX=0 StartY=0 StartZ=0 EndX=900 EndY=0 EndZ=0
    g1: LineSegment StartX=900 StartY=0 StartZ=0 EndX=900 EndY=2000 EndZ=0
    g2: LineSegment StartX=900 StartY=2000 StartZ=0 EndX=0 EndY=2000 EndZ=0
    g3: LineSegment StartX=0 StartY=2000 StartZ=0 EndX=0 EndY=0 EndZ=0
    g4: LineSegment StartX=50 StartY=0 StartZ=0 EndX=850 EndY=0 EndZ=0
    g5: LineSegment StartX=850 StartY=0 StartZ=0 EndX=850 EndY=1950 EndZ=0
    g6: LineSegment StartX=850 StartY=1950 StartZ=0 EndX=50 EndY=1950 EndZ=0
    g7: LineSegment StartX=50 StartY=1950 StartZ=0 EndX=50 EndY=0 EndZ=0
  constraints (23):
    c: Coincident(g0,g1)
    c: Coincident(g1,g2)
    c: Coincident(g2,g3)
    c: Coincident(g3,g0)
    c: Horizontal(g0)
    c: Horizontal(g2)
    c: Vertical(g1)
    c: Vertical(g3)
    c: Coincident(g4,g5)
    c: Coincident(g5,g6)
    c: Coincident(g6,g7)
    c: Coincident(g7,g4)
    c: Horizontal(g4)
    c: Horizontal(g6)
    c: Vertical(g5)
    c: Vertical(g7)
    c: DistanceY(g1) = 2000
    c: DistanceX(g0) = 900
    c: DistanceY(g6,g2) = 50
    c: DistanceX(g2,g6) = 50
    c: DistanceX(g4,g0) = 50
    c: DistanceY(g0,g4) = 0
    c: Coincident(g0,g-1)
FEATURE [Part::FeaturePython] Window047  label="Window045"  # WARN: FeaturePython — macro-defined, semantics opaque (R4)
  Base = -> Sketch057
  Height = 2000
  HoleDepth = 0
  MoveWithHost = true
  Normal = (0,1,0)
  Placement = pos=(205.169,0,-142.361) rot=(0,0,1;0rad)
  Preset = 6
  Role = 1
  Width = 900
  WindowParts = OuterFrame | Frame | Wire0,Wire1 | 150.0 | 0.0 | Door | Solid panel | Wire1 | 50.0 | 50.0
FEATURE [Part::FeaturePython] Wall064  # WARN: FeaturePython — macro-defined, semantics opaque (R4)
  Align = 1
  Base = -> Line067
  Face = 0
  Height = 2900
  Length = 0
  MoveWithHost = false
  Normal = (0,0,0)
  Role = 0
  Subtractions = -> [Window047]
  Width = 150
FEATURE [Sketcher::SketchObject] Sketch058
  Placement = pos=(3095,5375.63,103.777) rot=(0.57735,-0.57735,-0.57735;2.0944rad)
  sketch-geometry (8):
    g0: LineSegment StartX=0 StartY=0 StartZ=0 EndX=1000 EndY=0 EndZ=0
    g1: LineSegment StartX=1000 StartY=0 StartZ=0 EndX=1000 EndY=2000 EndZ=0
    g2: LineSegment StartX=1000 StartY=2000 StartZ=0 EndX=0 EndY=2000 EndZ=0
    g3: LineSegment StartX=0 StartY=2000 StartZ=0 EndX=0 EndY=0 EndZ=0
    g4: LineSegment StartX=50 StartY=0 StartZ=0 EndX=950 EndY=0 EndZ=0
    g5: LineSegment StartX=950 StartY=0 StartZ=0 EndX=950 EndY=1950 EndZ=0
    g6: LineSegment StartX=950 StartY=1950 StartZ=0 EndX=50 EndY=1950 EndZ=0
    g7: LineSegment StartX=50 StartY=1950 StartZ=0 EndX=50 EndY=0 EndZ=0
  constraints (23):
    c: Coincident(g0,g1)
    c: Coincident(g1,g2)
    c: Coincident(g2,g3)
    c: Coincident(g3,g0)
    c: Horizontal(g0)
    c: Horizontal(g2)
    c: Vertical(g1)
    c: Vertical(g3)
    c: Coincident(g4,g5)
    c: Coincident(g5,g6)
    c: Coincident(g6,g7)
    c: Coincident(g7,g4)
    c: Horizontal(g4)
    c: Horizontal(g6)
    c: Vertical(g5)
    c: Vertical(g7)
    c: DistanceY(g1) = 2000
    c: DistanceX(g0) = 1000
    c: DistanceY(g6,g2) = 50
    c: DistanceX(g2,g6) = 50
    c: DistanceX(g4,g0) = 50
    c: DistanceY(g0,g4) = 0
    c: Coincident(g0,g-1)
FEATURE [Part::FeaturePython] Window048  label="Window046"  # WARN: FeaturePython — macro-defined, semantics opaque (R4)
  Base = -> Sketch058
  Height = 2000
  HoleDepth = 0
  MoveWithHost = true
  Normal = (1,0,0)
  Placement = pos=(0,374.375,-103.777) rot=(0,0,1;0rad)
  Preset = 6
  Role = 1
  Width = 1000
  WindowParts = OuterFrame | Frame | Wire0,Wire1 | 150.0 | 0.0 | Door | Solid panel | Wire1 | 50.0 | 50.0
FEATURE [Part::FeaturePython] Wall009  # WARN: FeaturePython — macro-defined, semantics opaque (R4)
  Align = 2
  Base = -> Line008
  Face = 0
  Height = 2900
  Length = 0
  MoveWithHost = false
  Normal = (0,0,0)
  Role = 0
  Subtractions = -> [Window048]
  Width = 150
FEATURE [Part::Part2DObjectPython] Line183  # Draft 2D object (typed FeaturePython)
  ChamferSize = 0
  Closed = false
  End = (-394.998,0.305262,0.0001461)
  FilletRadius = 0
  Length = 3050
  MakeFace = true
  Placement = pos=(-4915,0.305262,0.0001461) rot=(0,0,1;0rad)
  Points = (2) [(4520,3050,0),(4520,4.54747e-13,0)]
  Start = (-394.998,3050.31,0.0001461)
  Support = -> Wall009
FEATURE [Sketcher::SketchObject] Sketch059
  Placement = pos=(1369.67,13020,243.219) rot=(0,0.707107,0.707107;3.14159rad)
  sketch-geometry (8):
    g0: LineSegment StartX=0 StartY=0 StartZ=0 EndX=1000 EndY=0 EndZ=0
    g1: LineSegment StartX=1000 StartY=0 StartZ=0 EndX=1000 EndY=2200 EndZ=0
    g2: LineSegment StartX=1000 StartY=2200 StartZ=0 EndX=0 EndY=2200 EndZ=0
    g3: LineSegment StartX=0 StartY=2200 StartZ=0 EndX=0 EndY=0 EndZ=0
    g4: LineSegment StartX=50 StartY=0 StartZ=0 EndX=950 EndY=0 EndZ=0
    g5: LineSegment StartX=950 StartY=0 StartZ=0 EndX=950 EndY=2150 EndZ=0
    g6: LineSegment StartX=950 StartY=2150 StartZ=0 EndX=50 EndY=2150 EndZ=0
    g7: LineSegment StartX=50 StartY=2150 StartZ=0 EndX=50 EndY=0 EndZ=0
  constraints (23):
    c: Coincident(g0,g1)
    c: Coincident(g1,g2)
    c: Coincident(g2,g3)
    c: Coincident(g3,g0)
    c: Horizontal(g0)
    c: Horizontal(g2)
    c: Vertical(g1)
    c: Vertical(g3)
    c: Coincident(g4,g5)
    c: Coincident(g5,g6)
    c: Coincident(g6,g7)
    c: Coincident(g7,g4)
    c: Horizontal(g4)
    c: Horizontal(g6)
    c: Vertical(g5)
    c: Vertical(g7)
    c: DistanceY(g1) = 2200
    c: DistanceX(g0) = 1000
    c: DistanceY(g6,g2) = 50
    c: DistanceX(g2,g6) = 50
    c: DistanceX(g4,g0) = 50
    c: DistanceY(g0,g4) = 0
    c: Coincident(g0,g-1)
FEATURE [Part::FeaturePython] Window049  label="Window047"  # WARN: FeaturePython — macro-defined, semantics opaque (R4)
  Base = -> Sketch059
  Height = 2200
  HoleDepth = 0
  MoveWithHost = true
  Normal = (0,-1,0)
  Placement = pos=(-124.668,0,-243.219) rot=(0,0,1;0rad)
  Preset = 6
  Role = 1
  Width = 1000
  WindowParts = OuterFrame | Frame | Wire0,Wire1 | 150.0 | 0.0 | Door | Solid panel | Wire1 | 50.0 | 50.0
FEATURE [Part::FeaturePython] Wall067  # WARN: FeaturePython — macro-defined, semantics opaque (R4)
  Align = 1
  Base = -> Line072
  Face = 0
  Height = 2900
  Length = 0
  MoveWithHost = false
  Normal = (0,0,0)
  Role = 0
  Subtractions = -> [Window049]
  Width = 150
FEATURE [Sketcher::SketchObject] Sketch060
  Placement = pos=(8795,13474.6,138.247) rot=(0.57735,-0.57735,-0.57735;2.0944rad)
  sketch-geometry (8):
    g0: LineSegment StartX=0 StartY=0 StartZ=0 EndX=900 EndY=0 EndZ=0
    g1: LineSegment StartX=900 StartY=0 StartZ=0 EndX=900 EndY=2200 EndZ=0
    g2: LineSegment StartX=900 StartY=2200 StartZ=0 EndX=0 EndY=2200 EndZ=0
    g3: LineSegment StartX=0 StartY=2200 StartZ=0 EndX=0 EndY=0 EndZ=0
    g4: LineSegment StartX=50 StartY=0 StartZ=0 EndX=850 EndY=0 EndZ=0
    g5: LineSegment StartX=850 StartY=0 StartZ=0 EndX=850 EndY=2150 EndZ=0
    g6: LineSegment StartX=850 StartY=2150 StartZ=0 EndX=50 EndY=2150 EndZ=0
    g7: LineSegment StartX=50 StartY=2150 StartZ=0 EndX=50 EndY=0 EndZ=0
  constraints (23):
    c: Coincident(g0,g1)
    c: Coincident(g1,g2)
    c: Coincident(g2,g3)
    c: Coincident(g3,g0)
    c: Horizontal(g0)
    c: Horizontal(g2)
    c: Vertical(g1)
    c: Vertical(g3)
    c: Coincident(g4,g5)
    c: Coincident(g5,g6)
    c: Coincident(g6,g7)
    c: Coincident(g7,g4)
    c: Horizontal(g4)
    c: Horizontal(g6)
    c: Vertical(g5)
    c: Vertical(g7)
    c: DistanceY(g1) = 2200
    c: DistanceX(g0) = 900
    c: DistanceY(g6,g2) = 50
    c: DistanceX(g2,g6) = 50
    c: DistanceX(g4,g0) = 50
    c: DistanceY(g0,g4) = 0
    c: Coincident(g0,g-1)
FEATURE [Part::FeaturePython] Window050  label="Window048"  # WARN: FeaturePython — macro-defined, semantics opaque (R4)
  Base = -> Sketch060
  Height = 2200
  HoleDepth = 0
  MoveWithHost = true
  Normal = (1,0,0)
  Placement = pos=(0,545.38,-138.247) rot=(0,0,1;0rad)
  Preset = 6
  Role = 1
  Width = 900
  WindowParts = OuterFrame | Frame | Wire0,Wire1 | 150.0 | 0.0 | Door | Solid panel | Wire1 | 50.0 | 50.0
FEATURE [Part::FeaturePython] Wall060  # WARN: FeaturePython — macro-defined, semantics opaque (R4)
  Align = 0
  Base = -> Line025
  Face = 0
  Height = 2900
  Length = 0
  MoveWithHost = false
  Normal = (0,0,0)
  Role = 0
  Subtractions = -> [Window050]
  Width = 150
FEATURE [App::DocumentObjectGroup] Group005  label="external railings"
  Group = -> [Extrusion007,Extrusion008,Extrusion009,Extrusion010]
FEATURE [Sketcher::SketchObject] Sketch061
  Placement = pos=(6504.33,12870,252.819) rot=(1,0,0;1.5708rad)
  sketch-geometry (8):
    g0: LineSegment StartX=0 StartY=0 StartZ=0 EndX=1000 EndY=0 EndZ=0
    g1: LineSegment StartX=1000 StartY=0 StartZ=0 EndX=1000 EndY=2200 EndZ=0
    g2: LineSegment StartX=1000 StartY=2200 StartZ=0 EndX=0 EndY=2200 EndZ=0
    g3: LineSegment StartX=0 StartY=2200 StartZ=0 EndX=0 EndY=0 EndZ=0
    g4: LineSegment StartX=50 StartY=0 StartZ=0 EndX=950 EndY=0 EndZ=0
    g5: LineSegment StartX=950 StartY=0 StartZ=0 EndX=950 EndY=2150 EndZ=0
    g6: LineSegment StartX=950 StartY=2150 StartZ=0 EndX=50 EndY=2150 EndZ=0
    g7: LineSegment StartX=50 StartY=2150 StartZ=0 EndX=50 EndY=0 EndZ=0
  constraints (23):
    c: Coincident(g0,g1)
    c: Coincident(g1,g2)
    c: Coincident(g2,g3)
    c: Coincident(g3,g0)
    c: Horizontal(g0)
    c: Horizontal(g2)
    c: Vertical(g1)
    c: Vertical(g3)
    c: Coincident(g4,g5)
    c: Coincident(g5,g6)
    c: Coincident(g6,g7)
    c: Coincident(g7,g4)
    c: Horizontal(g4)
    c: Horizontal(g6)
    c: Vertical(g5)
    c: Vertical(g7)
    c: DistanceY(g1) = 2200
    c: DistanceX(g0) = 1000
    c: DistanceY(g6,g2) = 50
    c: DistanceX(g2,g6) = 50
    c: DistanceX(g4,g0) = 50
    c: DistanceY(g0,g4) = 0
    c: Coincident(g0,g-1)
FEATURE [Part::FeaturePython] Window051  label="Window049"  # WARN: FeaturePython — macro-defined, semantics opaque (R4)
  Base = -> Sketch061
  Height = 2200
  HoleDepth = 0
  MoveWithHost = true
  Normal = (0,1,0)
  Placement = pos=(-559.328,0,-252.819) rot=(0,0,1;0rad)
  Preset = 6
  Role = 1
  Width = 1000
  WindowParts = OuterFrame | Frame | Wire0,Wire1 | 150.0 | 0.0 | Door | Solid panel | Wire1 | 50.0 | 50.0
FEATURE [Part::FeaturePython] Wall059  # WARN: FeaturePython — macro-defined, semantics opaque (R4)
  Align = 1
  Base = -> Line060
  Face = 0
  Height = 2900
  Length = 0
  MoveWithHost = false
  Normal = (0,0,0)
  Role = 0
  Subtractions = -> [Window051]
  Width = 150
FEATURE [Part::Part2DObjectPython] Line211  # Draft 2D object (typed FeaturePython)
  ChamferSize = 0
  Closed = false
  End = (6080,15417.5,0.0001461)
  FilletRadius = 0
  Length = 6391.78
  MakeFace = true
  Placement = pos=(-4915,0.305262,0.0001461) rot=(0,0,1;0rad)
  Points = (2) [(10995,21809,0),(10995,15417.2,0)]
  Start = (6080,21809.3,0.0001461)
FEATURE [Part::Part2DObjectPython] Line212  # Draft 2D object (typed FeaturePython)
  ChamferSize = 0
  Closed = false
  End = (12680,20689.3,0.0001461)
  FilletRadius = 0
  Length = 28788
  MakeFace = true
  Placement = pos=(-4915,0.305262,0.0001461) rot=(0,0,1;0rad)
  Points = (2) [(17595,-8099,0),(17595,20689,0)]
  Start = (12680,-8098.69,0.0001461)
FEATURE [Part::Part2DObjectPython] Line215  # Draft 2D object (typed FeaturePython)
  ChamferSize = 0
  Closed = false
  End = (-4920,22480.3,0.0001461)
  FilletRadius = 0
  Length = 6480
  MakeFace = true
  Placement = pos=(-4915,0.305262,0.0001461) rot=(0,0,1;0rad)
  Points = (2) [(-5,16000,0),(-5,22480,0)]
  Start = (-4920,16000.3,0.0001461)
FEATURE [Part::Part2DObjectPython] Line216  # Draft 2D object (typed FeaturePython)
  ChamferSize = 0
  Closed = false
  End = (-6920,-10739.7,0.0001461)
  FilletRadius = 0
  Length = 32773
  MakeFace = true
  Placement = pos=(-4915,0.305262,0.0001461) rot=(0,0,1;0rad)
  Points = (2) [(-2005,22033,0),(-2005,-10740,0)]
  Start = (-6920,22033.3,0.0001461)
FEATURE [Part::Part2DObjectPython] Line217  # Draft 2D object (typed FeaturePython)
  ChamferSize = 0
  Closed = false
  End = (16323,2000.31,0.0001461)
  FilletRadius = 0
  Length = 9472.71
  MakeFace = true
  Placement = pos=(-4915,0.305262,0.0001461) rot=(0,0,1;0rad)
  Points = (2) [(11765.3,2000,0),(21238,2000,0)]
  Start = (6850.3,2000.31,0.0001461)
FEATURE [Part::Part2DObjectPython] Line218  # Draft 2D object (typed FeaturePython)
  ChamferSize = 0
  Closed = false
  End = (17756,-5799.69,0.0001461)
  FilletRadius = 0
  Length = 28609
  MakeFace = true
  Placement = pos=(-4915,0.305262,0.0001461) rot=(0,0,1;0rad)
  Points = (2) [(-5938,-5800,0),(22671,-5800,0)]
  Start = (-10853,-5799.69,0.0001461)
FEATURE [Part::Part2DObjectPython] Line219  # Draft 2D object (typed FeaturePython)
  ChamferSize = 0
  Closed = false
  End = (17595,19000,0)
  FilletRadius = 0
  Length = 24515
  MakeFace = true
  Points = (2) [(17595,-5515,0),(17595,19000,0)]
  Start = (17595,-5515,0)
FEATURE [Part::Part2DObjectPython] Line220  # Draft 2D object (typed FeaturePython)
  ChamferSize = 0
  Closed = false
  End = (-2005,19000,0)
  FilletRadius = 0
  Length = 19600
  MakeFace = true
  Points = (2) [(17595,19000,0),(-2005,19000,0)]
  Start = (17595,19000,0)
FEATURE [Part::Part2DObjectPython] Line221  # Draft 2D object (typed FeaturePython)
  ChamferSize = 0
  Closed = false
  End = (-2005,19000,0)
  FilletRadius = 0
  Length = 24515
  MakeFace = true
  Points = (2) [(-2005,-5515,0),(-2005,19000,0)]
  Start = (-2005,-5515,0)
FEATURE [Part::FeaturePython] Wall081  # WARN: FeaturePython — macro-defined, semantics opaque (R4)
  Align = 0
  Base = -> Line219
  Face = 0
  Height = 3000
  Length = 0
  MoveWithHost = false
  Normal = (0,0,0)
  Role = 0
  Width = 200
FEATURE [Part::FeaturePython] Wall082  # WARN: FeaturePython — macro-defined, semantics opaque (R4)
  Align = 1
  Base = -> Line221
  Face = 0
  Height = 3000
  Length = 0
  MoveWithHost = false
  Normal = (0,0,0)
  Role = 0
  Width = 200
FEATURE [Part::FeaturePython] Wall083  # WARN: FeaturePython — macro-defined, semantics opaque (R4)
  Align = 0
  Base = -> Line220
  Face = 0
  Height = 3000
  Length = 0
  MoveWithHost = false
  Normal = (0,0,0)
  Role = 0
  Width = 200
FEATURE [Part::Feature] Block_Car_05_18
  Placement = pos=(13753.6,-1979.05,0) rot=(0,0,1;1.5702rad)
  shape: bbox 1966 x 4375 x 2e-07 mm, 0 faces, 0 solids (baked)
FEATURE [Part::Feature] Block_Subcompact_Car_18
  Placement = pos=(16130.3,163.492,0) rot=(0,0,-1;1.5708rad)
  shape: bbox 1899 x 3606 x 2e-07 mm, 0 faces, 0 solids (baked)
FEATURE [App::DocumentObjectGroup] Interior___Furniture  label="Interior - Furniture"
  Group = -> [Block_Car_05_18,Block_Subcompact_Car_18]
FEATURE [App::DocumentObjectGroup] _d_vehicles  label="2d vehicles"
  Group = -> [Interior___Furniture]
FEATURE [Part::Part2DObjectPython] DWire002  # Draft 2D object (typed FeaturePython)
  ChamferSize = 0
  Closed = true
  End = (-5,2000,0)
  FilletRadius = 0
  Length = 50000
  MakeFace = true
  Points = (6) [(-5,16000,0),(10995,16000,0),(10995,2000,0),(5795,2000,0),(3245,2000,0),(-5,2000,0)]
  Start = (-5,16000,0)
FEATURE [Part::Feature] Face010
  shape: bbox 13900 x 17000 x 2e-07 mm, 1 faces, 0 solids (baked)
FEATURE [Part::Cut] Cut002
  Base = -> Face010
  Tool = -> DWire002
FEATURE [Part::Extrusion] Extrusion022  label="Around House side walk"
  Base = -> Cut002
  Dir = (0,0,-100)
  Solid = true
FEATURE [Part::Part2DObjectPython] Line228  # Draft 2D object (typed FeaturePython)
  ChamferSize = 0
  Closed = false
  End = (-1820.14,5159.82,0.0001461)
  FilletRadius = 0
  Length = 409.518
  MakeFace = true
  Placement = pos=(-4915,0.305262,0.0001461) rot=(0,0,1;0rad)
  Points = (2) [(3095,4750,0),(3094.86,5159.52,0)]
  Start = (-1820,4750.31,0.0001461)
FEATURE [Part::Part2DObjectPython] Line229  # Draft 2D object (typed FeaturePython)
  ChamferSize = 0
  Closed = false
  End = (-2420.14,5159.61,0.0001461)
  FilletRadius = 0
  Length = 921.768
  MakeFace = true
  Placement = pos=(-4915,0.305262,0.0001461) rot=(0,0,1;0rad)
  Points = (2) [(2495.18,4237.54,0),(2494.86,5159.31,0)]
  Start = (-2419.82,4237.85,0.0001461)
FEATURE [Part::Part2DObjectPython] Line230  # Draft 2D object (typed FeaturePython)
  ChamferSize = 0
  Closed = false
  End = (2495.03,4650,-100)
  FilletRadius = 0
  Length = 599.965
  MakeFace = true
  Placement = pos=(0,0,-100) rot=(0,0,1;0rad)
  Points = (2) [(3095,4650,0),(2495.03,4650,0)]
  Start = (3095,4650,-100)
FEATURE [Part::FeaturePython] Wall084  # WARN: FeaturePython — macro-defined, semantics opaque (R4)
  Align = 1
  Base = -> Line230
  Face = 0
  Height = 2900
  Length = 0
  MoveWithHost = false
  Normal = (0,0,0)
  Role = 0
  Width = 150
FEATURE [Part::Part2DObjectPython] Line231  # Draft 2D object (typed FeaturePython)
  ChamferSize = 0
  Closed = false
  End = (6080,19207.5,3000)
  FilletRadius = 0
  Length = 3357.22
  MakeFace = true
  Placement = pos=(-4915,0.305262,0.0001461) rot=(0,0,1;0rad)
  Points = (2) [(10995,15850,3000),(10995,19207.2,3000)]
  Start = (6080,15850.3,3000)
FEATURE [Part::Part2DObjectPython] Line232  # Draft 2D object (typed FeaturePython)
  ChamferSize = 0
  Closed = false
  End = (6080,19207.5,4000)
  FilletRadius = 0
  Length = 13157.2
  MakeFace = true
  Placement = pos=(-4915,0.305262,0.0001461) rot=(0,0,1;0rad)
  Points = (2) [(10995,6050,4000),(10995,19207.2,4000)]
  Start = (6080,6050.31,4000)
FEATURE [Part::Part2DObjectPython] Line233  # Draft 2D object (typed FeaturePython)
  ChamferSize = 0
  Closed = false
  End = (-5912.71,670.305,6373)
  FilletRadius = 0
  Length = 1276
  MakeFace = true
  Placement = pos=(-4915,0.305262,0.0001461) rot=(0,0,1;0rad)
  Points = (2) [(-1108.92,670,7644.14),(-997.708,670,6373)]
  Start = (-6023.92,670.305,7644.14)
FEATURE [Part::Part2DObjectPython] Line234  # Draft 2D object (typed FeaturePython)
  ChamferSize = 0
  Closed = false
  End = (-4518.03,670.305,6495.01)
  FilletRadius = 0
  Length = 1276
  MakeFace = true
  Placement = pos=(-4915,0.305262,0.0001461) rot=(0,0,1;0rad)
  Points = (2) [(285.753,670,7766.16),(396.964,670,6495.01)]
  Start = (-4629.24,670.305,7766.16)
FEATURE [Part::Part2DObjectPython] Line236  # Draft 2D object (typed FeaturePython)
  ChamferSize = 0
  Closed = false
  End = (-5872.86,670.305,6376.48)
  FilletRadius = 0
  Length = 79.9999
  MakeFace = true
  Placement = pos=(-4915,0.305262,0.0001461) rot=(0,0,1;0rad)
  Points = (2) [(-964.833,670,6456.18),(-957.861,670,6376.48)]
  Start = (-5879.83,670.305,6456.18)
FEATURE [Part::Part2DObjectPython] Line237  # Draft 2D object (typed FeaturePython)
  ChamferSize = 0
  Closed = false
  End = (-6232.98,670.305,6385.13)
  FilletRadius = 0
  Length = 398
  MakeFace = true
  Placement = pos=(-4915,0.305262,0.0001461) rot=(0,0,1;0rad)
  Points = (2) [(-921.499,670,6419.82),(-1317.98,670,6385.13)]
  Start = (-5836.5,670.305,6419.82)
FEATURE [Part::Part2DObjectPython] Line238  # Draft 2D object (typed FeaturePython)
  ChamferSize = 0
  Closed = false
  End = (-6236.47,670.305,6424.98)
  FilletRadius = 0
  Length = 398
  MakeFace = true
  Placement = pos=(-4915,0.305262,0.0001461) rot=(0,0,1;0rad)
  Points = (2) [(-924.985,670,6459.66),(-1321.47,670,6424.98)]
  Start = (-5839.98,670.305,6459.66)
FEATURE [Part::Part2DObjectPython] Line239  # Draft 2D object (typed FeaturePython)
  ChamferSize = 0
  Closed = false
  End = (-5944.22,670.305,7651.11)
  FilletRadius = 0
  Length = 1236
  MakeFace = true
  Placement = pos=(-4875.15,0.305262,3.48637) rot=(0,0,1;0rad)
  Points = (2) [(-961.347,670,6416.33),(-1069.07,670,7647.63)]
  Start = (-5836.5,670.305,6419.82)
FEATURE [Part::Part2DObjectPython] Rectangle013  # Draft 2D object (typed FeaturePython)
  ChamferSize = 0
  FilletRadius = 0
  Height = 40
  Length = 39.9998
  MakeFace = true
  Placement = pos=(-921.499,670,6419.82) rot=(0.543775,-0.593426,0.593426;2.14549rad)
FEATURE [Part::Part2DObjectPython] Rectangle014  # Draft 2D object (typed FeaturePython)
  ChamferSize = 0
  FilletRadius = 0
  Height = 40
  Length = 39.9998
  MakeFace = true
  Placement = pos=(433.326,670,6538.35) rot=(0.543775,-0.593426,0.593426;2.14549rad)
FEATURE [Part::Part2DObjectPython] Rectangle015  # Draft 2D object (typed FeaturePython)
  ChamferSize = 0
  FilletRadius = 0
  Height = 40
  Length = 39.9998
  MakeFace = true
  Placement = pos=(1788.15,670,6656.88) rot=(0.543775,-0.593426,0.593426;2.14549rad)
FEATURE [Part::Part2DObjectPython] Rectangle016  # Draft 2D object (typed FeaturePython)
  ChamferSize = 0
  FilletRadius = 0
  Height = 40
  Length = 39.9998
  MakeFace = true
  Placement = pos=(3142.98,670,6775.41) rot=(0.543775,-0.593426,0.593426;2.14549rad)
FEATURE [Part::Part2DObjectPython] Rectangle017  # Draft 2D object (typed FeaturePython)
  ChamferSize = 0
  FilletRadius = 0
  Height = 40
  Length = 39.9998
  MakeFace = true
  Placement = pos=(5852.62,670,7012.48) rot=(0.543775,-0.593426,0.593426;2.14549rad)
FEATURE [Part::Part2DObjectPython] Rectangle018  # Draft 2D object (typed FeaturePython)
  ChamferSize = 0
  FilletRadius = 0
  Height = 40
  Length = 39.9998
  MakeFace = true
  Placement = pos=(4497.8,670,6893.94) rot=(0.543775,-0.593426,0.593426;2.14549rad)
FEATURE [Part::Part2DObjectPython] Rectangle019  # Draft 2D object (typed FeaturePython)
  ChamferSize = 0
  FilletRadius = 0
  Height = 40
  Length = 39.9998
  MakeFace = true
  Placement = pos=(7207.45,670,7131.01) rot=(0.543775,-0.593426,0.593426;2.14549rad)
FEATURE [Part::Part2DObjectPython] Rectangle020  # Draft 2D object (typed FeaturePython)
  ChamferSize = 0
  FilletRadius = 0
  Height = 40
  Length = 39.9998
  MakeFace = true
  Placement = pos=(8562.27,670,7249.54) rot=(0.543775,-0.593426,0.593426;2.14549rad)
FEATURE [Part::Part2DObjectPython] Rectangle021  # Draft 2D object (typed FeaturePython)
  ChamferSize = 0
  FilletRadius = 0
  Height = 40
  Length = 39.9998
  MakeFace = true
  Placement = pos=(9917.1,670,7368.07) rot=(0.543775,-0.593426,0.593426;2.14549rad)
FEATURE [Part::Part2DObjectPython] Rectangle022  # Draft 2D object (typed FeaturePython)
  ChamferSize = 0
  FilletRadius = 0
  Height = 40
  Length = 39.9998
  MakeFace = true
  Placement = pos=(11271.9,670,7486.6) rot=(0.543775,-0.593426,0.593426;2.14549rad)
FEATURE [Part::Part2DObjectPython] Rectangle023  # Draft 2D object (typed FeaturePython)
  ChamferSize = 0
  FilletRadius = 0
  Height = 40
  Length = 39.9998
  MakeFace = true
  Placement = pos=(12626.7,670,7605.13) rot=(0.543775,-0.593426,0.593426;2.14549rad)
FEATURE [Part::Extrusion] Extrusion023
  Base = -> Rectangle013
  Dir = (0,16250,0)
  Solid = true
FEATURE [Part::Extrusion] Extrusion024
  Base = -> Rectangle014
  Dir = (-4e-12,16225,0)
  Solid = true
FEATURE [Part::Extrusion] Extrusion025
  Base = -> Rectangle015
  Dir = (0,16225,0)
  Solid = true
FEATURE [Part::Extrusion] Extrusion026
  Base = -> Rectangle016
  Dir = (0,16225,0)
  Solid = true
FEATURE [Part::Extrusion] Extrusion027
  Base = -> Rectangle018
  Dir = (0,16225,0)
  Solid = true
FEATURE [Part::Extrusion] Extrusion028
  Base = -> Rectangle017
  Dir = (0,16225,0)
  Solid = true
FEATURE [Part::Extrusion] Extrusion029
  Base = -> Rectangle019
  Dir = (0,16225,0)
  Solid = true
FEATURE [Part::Extrusion] Extrusion030
  Base = -> Rectangle020
  Dir = (0,16225,0)
  Solid = true
FEATURE [Part::Extrusion] Extrusion031
  Base = -> Rectangle021
  Dir = (0,16225,0)
  Solid = true
FEATURE [Part::Extrusion] Extrusion032
  Base = -> Rectangle022
  Dir = (0,16225,0)
  Solid = true
FEATURE [Part::Extrusion] Extrusion033
  Base = -> Rectangle023
  Dir = (0,16225,0)
  Solid = true
FEATURE [Part::Feature] Face011
  Placement = pos=(12942,17000,7672.87) rot=(0.043578,-0.043578,-0.998099;1.5727rad)
  shape: bbox 13950 x 18000 x 1220 mm, 1 faces, 0 solids (baked)
FEATURE [Part::Extrusion] Extrusion035
  Base = -> Face011
  Dir = (-3.48623,0,39.8478)
  Solid = true
FEATURE [Part::Feature] Face015
  Placement = pos=(0,1670,0) rot=(0,0,1;0rad)
  shape: bbox 13950 x 2e-07 x 1260 mm, 1 faces, 0 solids (baked)
FEATURE [Part::Extrusion] Extrusion038  label="Roof Sheet Metal"
  Base = -> Face015
  Dir = (0,16250,0)
  Solid = true
FEATURE [Sketcher::SketchObject] Sketch062
  Placement = pos=(10995,6109.53,185.542) rot=(0.57735,0.57735,0.57735;2.0944rad)
  sketch-geometry (8):
    g0: LineSegment StartX=0 StartY=0 StartZ=0 EndX=1000 EndY=0 EndZ=0
    g1: LineSegment StartX=1000 StartY=0 StartZ=0 EndX=1000 EndY=2200 EndZ=0
    g2: LineSegment StartX=1000 StartY=2200 StartZ=0 EndX=0 EndY=2200 EndZ=0
    g3: LineSegment StartX=0 StartY=2200 StartZ=0 EndX=0 EndY=0 EndZ=0
    g4: LineSegment StartX=50 StartY=0 StartZ=0 EndX=950 EndY=0 EndZ=0
    g5: LineSegment StartX=950 StartY=0 StartZ=0 EndX=950 EndY=2150 EndZ=0
    g6: LineSegment StartX=950 StartY=2150 StartZ=0 EndX=50 EndY=2150 EndZ=0
    g7: LineSegment StartX=50 StartY=2150 StartZ=0 EndX=50 EndY=0 EndZ=0
  constraints (23):
    c: Coincident(g0,g1)
    c: Coincident(g1,g2)
    c: Coincident(g2,g3)
    c: Coincident(g3,g0)
    c: Horizontal(g0)
    c: Horizontal(g2)
    c: Vertical(g1)
    c: Vertical(g3)
    c: Coincident(g4,g5)
    c: Coincident(g5,g6)
    c: Coincident(g6,g7)
    c: Coincident(g7,g4)
    c: Horizontal(g4)
    c: Horizontal(g6)
    c: Vertical(g5)
    c: Vertical(g7)
    c: DistanceY(g1) = 2200
    c: DistanceX(g0) = 1000
    c: DistanceY(g6,g2) = 50
    c: DistanceX(g2,g6) = 50
    c: DistanceX(g4,g0) = 50
    c: DistanceY(g0,g4) = 0
    c: Coincident(g0,g-1)
FEATURE [Part::Part2DObjectPython] Line241  # Draft 2D object (typed FeaturePython)
  ChamferSize = 0
  Closed = false
  End = (-320.057,5900.31,6172.24)
  FilletRadius = 0
  Length = 463.499
  MakeFace = true
  Placement = pos=(-4915,0.305262,0.0001461) rot=(0,0,1;0rad)
  Points = (2) [(4595,5900,5708.74),(4594.94,5900,6172.24)]
  Start = (-319.998,5900.31,5708.74)
FEATURE [App::FeaturePython] Dimension021  # Draft dimension (typed FeaturePython)
  Dimline = (505.943,5900.31,6284.24)
  Direction = (0,0,0)
  Distance = 1200
  End = (879.943,5900.31,6172.24)
  Normal = (0,-1,0)
  Start = (-320.057,5900.31,6172.24)
FEATURE [Part::Part2DObjectPython] Line242  # Draft 2D object (typed FeaturePython)
  ChamferSize = 0
  Closed = false
  End = (879.96,1850.31,6172.39)
  FilletRadius = 0
  Length = 463.499
  MakeFace = true
  Placement = pos=(-4915,0.305262,0.0001461) rot=(0,0,1;0rad)
  Points = (2) [(5795.02,1850,5708.89),(5794.96,1850,6172.39)]
  Start = (880.019,1850.31,5708.89)
FEATURE [Part::Part2DObjectPython] Line243  # Draft 2D object (typed FeaturePython)
  ChamferSize = 0
  Closed = false
  End = (-220.057,5900.31,6172.25)
  FilletRadius = 0
  Length = 463.499
  MakeFace = true
  Placement = pos=(-4915,0.305262,0.0001461) rot=(0,0,1;0rad)
  Points = (2) [(4695,5900,5708.75),(4694.94,5900,6172.25)]
  Start = (-219.998,5900.31,5708.75)
FEATURE [Part::Part2DObjectPython] Line244  # Draft 2D object (typed FeaturePython)
  ChamferSize = 0
  Closed = false
  End = (779.943,5900.31,6172.38)
  FilletRadius = 0
  Length = 463.499
  MakeFace = true
  Placement = pos=(-4915,0.305262,0.0001461) rot=(0,0,1;0rad)
  Points = (2) [(5695,5900,5708.88),(5694.94,5900,6172.37)]
  Start = (780.002,5900.31,5708.88)
FEATURE [Part::Part2DObjectPython] Line245  # Draft 2D object (typed FeaturePython)
  ChamferSize = 0
  Closed = false
  End = (879.96,5900.31,6172.39)
  FilletRadius = 0
  Length = 463.499
  MakeFace = true
  Placement = pos=(-4915,0.305262,0.0001461) rot=(0,0,1;0rad)
  Points = (2) [(5795.02,5900,5708.89),(5794.96,5900,6172.39)]
  Start = (880.019,5900.31,5708.89)
FEATURE [Part::Part2DObjectPython] Line248  # Draft 2D object (typed FeaturePython)
  ChamferSize = 0
  Closed = false
  End = (2230,10050.3,5427.94)
  FilletRadius = 0
  Length = 427.94
  MakeFace = true
  Placement = pos=(-4915,0.305262,0.0001461) rot=(0,0,1;0rad)
  Points = (2) [(7145,10050,5000),(7145,10050,5427.94)]
  Start = (2230,10050.3,5000)
FEATURE [Part::Part2DObjectPython] Line249  # Draft 2D object (typed FeaturePython)
  ChamferSize = 0
  Closed = false
  End = (2230,9950.31,5427.94)
  FilletRadius = 0
  Length = 427.94
  MakeFace = true
  Placement = pos=(-4915,0.305262,0.0001461) rot=(0,0,1;0rad)
  Points = (2) [(7145,9950,5000),(7145,9950,5427.94)]
  Start = (2230,9950.31,5000)
FEATURE [Part::Part2DObjectPython] Line250  # Draft 2D object (typed FeaturePython)
  ChamferSize = 0
  Closed = false
  End = (2230,10197.4,5411.26)
  FilletRadius = 0
  Length = 411.266
  MakeFace = true
  Placement = pos=(-4915,0.305262,0.0001461) rot=(0,0,1;0rad)
  Points = (2) [(7145,10200,5000),(7145,10197.1,5411.26)]
  Start = (2230,10200.3,5000)
FEATURE [Part::Part2DObjectPython] Line251  # Draft 2D object (typed FeaturePython)
  ChamferSize = 0
  Closed = false
  End = (2230,10297.4,5411.96)
  FilletRadius = 0
  Length = 411.266
  MakeFace = true
  Placement = pos=(-4915,0.305262,0.0001461) rot=(0,0,1;0rad)
  Points = (2) [(7145,10300,5000.7),(7145,10297.1,5411.96)]
  Start = (2230,10300.3,5000.7)
FEATURE [Part::Part2DObjectPython] Line252  # Draft 2D object (typed FeaturePython)
  ChamferSize = 0
  Closed = false
  End = (2230,11845.3,5401.78)
  FilletRadius = 0
  Length = 401.777
  MakeFace = true
  Placement = pos=(-4915,0.305262,0.0001461) rot=(0,0,1;0rad)
  Points = (2) [(7145,11844.9,5000),(7145,11844.9,5401.78)]
  Start = (2230,11845.3,5000)
FEATURE [Part::Part2DObjectPython] Line253  # Draft 2D object (typed FeaturePython)
  ChamferSize = 0
  Closed = false
  End = (2230,11945.3,5401.78)
  FilletRadius = 0
  Length = 401.777
  MakeFace = true
  Placement = pos=(-4915,0.305262,0.0001461) rot=(0,0,1;0rad)
  Points = (2) [(7145,11944.9,5000),(7145,11944.9,5401.78)]
  Start = (2230,11945.3,5000)
FEATURE [Part::Part2DObjectPython] Line254  # Draft 2D object (typed FeaturePython)
  ChamferSize = 0
  Closed = false
  End = (-1470,12000.3,5533.68)
  FilletRadius = 0
  Length = 533.681
  MakeFace = true
  Placement = pos=(-4915,0.305262,0.0001461) rot=(0,0,1;0rad)
  Points = (2) [(3445,12000,5000),(3445,12000,5533.68)]
  Start = (-1470,12000.3,5000)
  Support = -> Wall037
FEATURE [Part::Part2DObjectPython] Line255  # Draft 2D object (typed FeaturePython)
  ChamferSize = 0
  Closed = false
  End = (-1570,12000.3,5533.68)
  FilletRadius = 0
  Length = 533.681
  MakeFace = true
  Placement = pos=(-4915,0.305262,0.0001461) rot=(0,0,1;0rad)
  Points = (2) [(3345,12000,5000),(3345,12000,5533.68)]
  Start = (-1570,12000.3,5000)
FEATURE [Part::Part2DObjectPython] Line256  # Draft 2D object (typed FeaturePython)
  ChamferSize = 0
  Closed = false
  End = (2030,5900.31,5556.76)
  FilletRadius = 0
  Length = 556.761
  MakeFace = true
  Placement = pos=(-4915,0.305262,0.0001461) rot=(0,0,1;0rad)
  Points = (2) [(6945,5900,5000),(6945,5900,5556.76)]
  Start = (2030,5900.31,5000)
FEATURE [Part::Part2DObjectPython] Line257  # Draft 2D object (typed FeaturePython)
  ChamferSize = 0
  Closed = false
  End = (2130,5900.31,5556.76)
  FilletRadius = 0
  Length = 556.761
  MakeFace = true
  Placement = pos=(-4915,0.305262,0.0001461) rot=(0,0,1;0rad)
  Points = (2) [(7045,5900,5000),(7045,5900,5556.76)]
  Start = (2130,5900.31,5000)
FEATURE [Part::Part2DObjectPython] Line258  # Draft 2D object (typed FeaturePython)
  ChamferSize = 0
  Closed = false
  End = (3880,13918.5,2504.57)
  FilletRadius = 0
  Length = 282.216
  MakeFace = true
  Placement = pos=(-4915,0.305262,0.0001461) rot=(0,0,1;0rad)
  Points = (2) [(8795,13918.2,2222.35),(8795,13918.2,2504.57)]
  Start = (3880,13918.5,2222.35)
  Support = -> Wall060
FEATURE [Part::Part2DObjectPython] Line259  # Draft 2D object (typed FeaturePython)
  ChamferSize = 0
  Closed = false
  End = (3880,14018.5,2504.57)
  FilletRadius = 0
  Length = 282.216
  MakeFace = true
  Placement = pos=(-4915,0.305262,0.0001461) rot=(0,0,1;0rad)
  Points = (2) [(8795,14018.2,2222.35),(8795,14018.2,2504.57)]
  Start = (3880,14018.5,2222.35)
FEATURE [Part::Part2DObjectPython] Line260  # Draft 2D object (typed FeaturePython)
  ChamferSize = 0
  Closed = false
  End = (-469.998,14016.3,2582.04)
  FilletRadius = 0
  Length = 465.392
  MakeFace = true
  Placement = pos=(-4915,0.305262,0.0001461) rot=(0,0,1;0rad)
  Points = (2) [(4445,14016,2116.65),(4445,14016,2582.04)]
  Start = (-469.998,14016.3,2116.65)
  Support = -> Wall061
FEATURE [Part::Part2DObjectPython] Line261  # Draft 2D object (typed FeaturePython)
  ChamferSize = 0
  Closed = false
  End = (-469.998,14116.3,2582.04)
  FilletRadius = 0
  Length = 465.392
  MakeFace = true
  Placement = pos=(-4915,0.305262,0.0001461) rot=(0,0,1;0rad)
  Points = (2) [(4445,14116,2116.65),(4445,14116,2582.04)]
  Start = (-469.998,14116.3,2116.65)
FEATURE [Part::Part2DObjectPython] Line262  # Draft 2D object (typed FeaturePython)
  ChamferSize = 0
  Closed = false
  End = (-3778.84,13020.3,2623.16)
  FilletRadius = 0
  Length = 416.828
  MakeFace = true
  Placement = pos=(-4915,0.305262,0.0001461) rot=(0,0,1;0rad)
  Points = (2) [(1136.16,13020,2206.33),(1136.16,13020,2623.16)]
  Start = (-3778.84,13020.3,2206.33)
FEATURE [Part::Part2DObjectPython] Line263  # Draft 2D object (typed FeaturePython)
  ChamferSize = 0
  Closed = false
  End = (-3678.84,13020.3,2623.16)
  FilletRadius = 0
  Length = 416.828
  MakeFace = true
  Placement = pos=(-4915,0.305262,0.0001461) rot=(0,0,1;0rad)
  Points = (2) [(1236.16,13020,2206.33),(1236.16,13020,2623.16)]
  Start = (-3678.84,13020.3,2206.33)
FEATURE [Part::Part2DObjectPython] Line264  # Draft 2D object (typed FeaturePython)
  ChamferSize = 0
  Closed = false
  End = (-1465.08,9750.31,2618.56)
  FilletRadius = 0
  Length = 468.739
  MakeFace = true
  Placement = pos=(-4915,0.305262,0.0001461) rot=(0,0,1;0rad)
  Points = (2) [(3449.92,9750,2149.83),(3449.92,9750,2618.56)]
  Start = (-1465.08,9750.31,2149.83)
FEATURE [Part::Part2DObjectPython] Line265  # Draft 2D object (typed FeaturePython)
  ChamferSize = 0
  Closed = false
  End = (-1565.08,9750.31,2618.56)
  FilletRadius = 0
  Length = 468.739
  MakeFace = true
  Placement = pos=(-4915,0.305262,0.0001461) rot=(0,0,1;0rad)
  Points = (2) [(3349.92,9750,2149.83),(3349.92,9750,2618.56)]
  Start = (-1565.08,9750.31,2149.83)
FEATURE [Part::Part2DObjectPython] Line266  # Draft 2D object (typed FeaturePython)
  ChamferSize = 0
  Closed = false
  End = (-1820,8704.21,2486.69)
  FilletRadius = 0
  Length = 353.329
  MakeFace = true
  Placement = pos=(-4915,0.305262,0.0001461) rot=(0,0,1;0rad)
  Points = (2) [(3095,8703.9,2133.36),(3095,8703.9,2486.69)]
  Start = (-1820,8704.21,2133.36)
  Support = -> Wall063
FEATURE [Part::Part2DObjectPython] Line267  # Draft 2D object (typed FeaturePython)
  ChamferSize = 0
  Closed = false
  End = (-1820,8604.21,2486.69)
  FilletRadius = 0
  Length = 353.329
  MakeFace = true
  Placement = pos=(-4915,0.305262,0.0001461) rot=(0,0,1;0rad)
  Points = (2) [(3095,8603.9,2133.36),(3095,8603.9,2486.69)]
  Start = (-1820,8604.21,2133.36)
FEATURE [Part::Part2DObjectPython] Line268  # Draft 2D object (typed FeaturePython)
  ChamferSize = 0
  Closed = false
  End = (-2720.34,6650.31,2344.47)
  FilletRadius = 0
  Length = 276.666
  MakeFace = true
  Placement = pos=(-4915,0.305262,0.0001461) rot=(0,0,1;0rad)
  Points = (2) [(2194.66,6650,2067.8),(2194.66,6650,2344.47)]
  Start = (-2720.34,6650.31,2067.81)
  Support = -> Wall064
FEATURE [Part::Part2DObjectPython] Line269  # Draft 2D object (typed FeaturePython)
  ChamferSize = 0
  Closed = false
  End = (-2820.34,6650.31,2344.47)
  FilletRadius = 0
  Length = 276.666
  MakeFace = true
  Placement = pos=(-4915,0.305262,0.0001461) rot=(0,0,1;0rad)
  Points = (2) [(2094.66,6650,2067.8),(2094.66,6650,2344.47)]
  Start = (-2820.34,6650.31,2067.81)
FEATURE [Part::Part2DObjectPython] Arc003  # Draft 2D object (typed FeaturePython)
  FirstAngle = -90
  LastAngle = 0
  MakeFace = true
  Placement = pos=(48237,5949.61,0) rot=(0,0,1;0rad)
  Radius = 900
FEATURE [Part::Part2DObjectPython] Line277  # Draft 2D object (typed FeaturePython)
  ChamferSize = 0
  Closed = false
  End = (48237,5049.61,0)
  FilletRadius = 0
  Length = 900
  MakeFace = true
  Placement = pos=(-366,-8.94205e-05,0) rot=(0,0,1;0rad)
  Points = (2) [(48603,5949.61,0),(48603,5049.61,0)]
  Start = (48237,5949.61,0)
FEATURE [Part::Part2DObjectPython] Arc004  # Draft 2D object (typed FeaturePython)
  FirstAngle = -90
  LastAngle = 0.0245798
  MakeFace = true
  Placement = pos=(36471.3,8199.61,0) rot=(0,0,1;0rad)
  Radius = 900
FEATURE [Part::Part2DObjectPython] Line278  # Draft 2D object (typed FeaturePython)
  ChamferSize = 0
  Closed = false
  End = (37371.3,8199.61,0)
  FilletRadius = 0
  Length = 900
  MakeFace = true
  Placement = pos=(-13281.7,-1700,0) rot=(0,0,1;0rad)
  Points = (2) [(49753,9899.61,0),(50653,9899.61,0)]
  Start = (36471.3,8199.61,0)
FEATURE [Part::Part2DObjectPython] Arc005  # Draft 2D object (typed FeaturePython)
  FirstAngle = 0.00625634
  LastAngle = 90
  MakeFace = true
  Placement = pos=(49412,10346.9,0) rot=(0,0,1;0rad)
  Radius = 900
FEATURE [Part::Part2DObjectPython] Line279  # Draft 2D object (typed FeaturePython)
  ChamferSize = 0
  Closed = false
  End = (50312,10347,0)
  FilletRadius = 0
  Length = 900
  MakeFace = true
  Placement = pos=(-341,-8.94205e-05,0) rot=(0,0,1;0rad)
  Points = (2) [(49753,10346.9,0),(50653,10347,0)]
  Start = (49412,10346.9,0)
FEATURE [Part::Part2DObjectPython] Arc006  # Draft 2D object (typed FeaturePython)
  FirstAngle = 0.0275498
  LastAngle = 90
  MakeFace = true
  Placement = pos=(49412,11994.6,0) rot=(0,0,1;0rad)
  Radius = 900
FEATURE [Part::Part2DObjectPython] Line280  # Draft 2D object (typed FeaturePython)
  ChamferSize = 0
  Closed = false
  End = (50312,11995,0)
  FilletRadius = 0
  Length = 925
  MakeFace = true
  Placement = pos=(-341,-8.94205e-05,0) rot=(0,0,1;0rad)
  Points = (2) [(49728,11994.6,0),(50653,11995,0)]
  Start = (49387,11994.6,0)
FEATURE [Part::Part2DObjectPython] Arc007  # Draft 2D object (typed FeaturePython)
  FirstAngle = -180
  LastAngle = -90
  MakeFace = true
  Placement = pos=(46437,12049.6,0) rot=(0,0,1;0rad)
  Radius = 900
FEATURE [Part::Part2DObjectPython] Line281  # Draft 2D object (typed FeaturePython)
  ChamferSize = 0
  Closed = false
  End = (46437,11149.6,0)
  FilletRadius = 0
  Length = 900
  MakeFace = true
  Placement = pos=(-366,-8.94205e-05,0) rot=(0,0,1;0rad)
  Points = (2) [(46803,12049.6,0),(46803,11149.6,0)]
  Start = (46437,12049.6,0)
FEATURE [Part::Part2DObjectPython] Arc008  # Draft 2D object (typed FeaturePython)
  FirstAngle = -179.973
  LastAngle = -90
  MakeFace = true
  Placement = pos=(46637,7099.61,0) rot=(0,0,1;0rad)
  Radius = 900
FEATURE [Part::Part2DObjectPython] Line282  # Draft 2D object (typed FeaturePython)
  ChamferSize = 0
  Closed = false
  End = (45737,7099.19,0)
  FilletRadius = 0
  Length = 900
  MakeFace = true
  Placement = pos=(984,-999.83,0) rot=(0,0,1;0rad)
  Points = (2) [(45653,8099.44,0),(44753,8099.02,0)]
  Start = (46637,7099.61,0)
FEATURE [Part::Part2DObjectPython] Arc  # Draft 2D object (typed FeaturePython)
  FirstAngle = 90
  LastAngle = 179.976
  MakeFace = true
  Placement = pos=(28648,13169.6,0) rot=(0,0,1;0rad)
  Radius = 900
FEATURE [Part::Part2DObjectPython] Line283  # Draft 2D object (typed FeaturePython)
  ChamferSize = 0
  Closed = false
  End = (27748,13170,0)
  FilletRadius = 0
  Length = 900
  MakeFace = true
  Placement = pos=(-1350.34,-0.000394594,0) rot=(0,0,1;0rad)
  Points = (2) [(29998.4,13169.6,0),(29098.4,13170,0)]
  Start = (28648,13169.6,0)
FEATURE [Part::Part2DObjectPython] Arc009  # Draft 2D object (typed FeaturePython)
  FirstAngle = 0.0269843
  LastAngle = 90
  MakeFace = true
  Placement = pos=(34398.4,13169.6,0) rot=(0,0,1;0rad)
  Radius = 800
FEATURE [Part::Part2DObjectPython] Line284  # Draft 2D object (typed FeaturePython)
  ChamferSize = 0
  Closed = false
  End = (34398.4,13169.6,0)
  FilletRadius = 0
  Length = 800
  MakeFace = true
  Points = (2) [(35198.4,13170,0),(34398.4,13169.6,0)]
  Start = (35198.4,13170,0)
FEATURE [Part::Part2DObjectPython] Arc010  # Draft 2D object (typed FeaturePython)
  FirstAngle = 90.0242
  LastAngle = 180
  MakeFace = true
  Placement = pos=(32398.4,12969.6,0) rot=(0,0,1;0rad)
  Radius = 900
FEATURE [Part::Part2DObjectPython] Line285  # Draft 2D object (typed FeaturePython)
  ChamferSize = 0
  Closed = false
  End = (32398.4,12969.6,0)
  FilletRadius = 0
  Length = 900
  MakeFace = true
  Points = (2) [(32398,13869.6,0),(32398.4,12969.6,0)]
  Start = (32398,13869.6,0)
FEATURE [Part::Part2DObjectPython] Arc011  # Draft 2D object (typed FeaturePython)
  FirstAngle = 90.0238
  LastAngle = 180
  MakeFace = true
  Placement = pos=(29798.4,9699.61,0) rot=(0,0,1;0rad)
  Radius = 900
FEATURE [Part::Part2DObjectPython] Line286  # Draft 2D object (typed FeaturePython)
  ChamferSize = 0
  Closed = false
  End = (29798,10599.6,0)
  FilletRadius = 0
  Length = 900
  MakeFace = true
  Points = (2) [(29798.4,9699.61,0),(29798,10599.6,0)]
  Start = (29798.4,9699.61,0)
FEATURE [Part::Part2DObjectPython] Arc012  # Draft 2D object (typed FeaturePython)
  FirstAngle = 179.973
  LastAngle = 270
  MakeFace = true
  Placement = pos=(28648.4,9449.61,0) rot=(0,0,1;0rad)
  Radius = 800
FEATURE [Part::Part2DObjectPython] Line287  # Draft 2D object (typed FeaturePython)
  ChamferSize = 0
  Closed = false
  End = (27848.4,9449.99,0)
  FilletRadius = 0
  Length = 800
  MakeFace = true
  Points = (2) [(28648.4,9449.61,0),(27848.4,9449.99,0)]
  Start = (28648.4,9449.61,0)
FEATURE [Part::Part2DObjectPython] Arc013  # Draft 2D object (typed FeaturePython)
  FirstAngle = 90.0275
  LastAngle = 180
  MakeFace = true
  Placement = pos=(28448.4,6599.61,0) rot=(0,0,1;0rad)
  Radius = 800
FEATURE [Part::Part2DObjectPython] Line288  # Draft 2D object (typed FeaturePython)
  ChamferSize = 0
  Closed = false
  End = (28448.4,6599.61,0)
  FilletRadius = 0
  Length = 800
  MakeFace = true
  Points = (2) [(28448,7399.61,0),(28448.4,6599.61,0)]
  Start = (28448,7399.61,0)
FEATURE [Part::Part2DObjectPython] Arc014  # Draft 2D object (typed FeaturePython)
  FirstAngle = 90
  LastAngle = 179.976
  MakeFace = true
  Placement = pos=(28648.4,4799.61,0) rot=(0,0,1;0rad)
  Radius = 900
FEATURE [Part::Part2DObjectPython] Line289  # Draft 2D object (typed FeaturePython)
  ChamferSize = 0
  Closed = false
  End = (27748.4,4799.99,0)
  FilletRadius = 0
  Length = 900
  MakeFace = true
  Points = (2) [(28648.4,4799.61,0),(27748.4,4799.99,0)]
  Start = (28648.4,4799.61,0)
FEATURE [Part::Part2DObjectPython] Line290  # Draft 2D object (typed FeaturePython)
  ChamferSize = 0
  Closed = false
  End = (27998.4,2149.61,0)
  FilletRadius = 0
  Length = 2350
  MakeFace = true
  Placement = pos=(0,-8.9407e-05,-1500) rot=(0,0,1;0rad)
  Points = (2) [(27998.4,4499.61,1500),(27998.4,2149.61,1500)]
  Start = (27998.4,4499.61,0)
FEATURE [Part::Part2DObjectPython] Line291  # Draft 2D object (typed FeaturePython)
  ChamferSize = 0
  Closed = false
  End = (42312,11399.6,0)
  FilletRadius = 0
  Length = 2875
  MakeFace = true
  Placement = pos=(-11809,-8.94205e-05,0) rot=(0,0,1;0rad)
  Points = (2) [(56996,11399.6,0),(54121,11399.6,0)]
  Start = (45187,11399.6,0)
FEATURE [App::DocumentObjectGroup] Group011
FEATURE [App::DocumentObjectGroup] Group009  label="Plan Annotation draw"
  Group = -> [Arc003,Line277,Arc004,Line278,Arc005,Line279,Arc006,Line280,Arc007,Line281,Arc008,Line282,Arc,Line283,Arc009,Line284,Arc010,Line285,Arc011,Line286,Arc012,Line287,Arc013,Line288,Arc014,Line289,Line290,Line291,Group011]
FEATURE [Part::Part2DObjectPython] Rectangle025  # Draft 2D object (typed FeaturePython)
  ChamferSize = 0
  FilletRadius = 0
  Height = -2200
  Length = -605.65
  MakeFace = true
  Placement = pos=(68947.7,11114.6,0) rot=(0,0,1;0rad)
FEATURE [Part::FeaturePython] Panel  # WARN: FeaturePython — macro-defined, semantics opaque (R4)
  Base = -> Rectangle025
  Length = 0
  MoveWithHost = false
  Placement = pos=(-61047,-2864.61,3000) rot=(0,0,1;0rad)
  Role = 0
  Sheets = 1
  Thickness = 50
  Width = 0
FEATURE [Part::FeaturePython] Panel001  # WARN: FeaturePython — macro-defined, semantics opaque (R4)
  Base = -> Rectangle025
  Length = 0
  MoveWithHost = false
  Placement = pos=(-61047,-2864.61,5750) rot=(0,0,1;0rad)
  Role = 0
  Sheets = 1
  Thickness = 50
  Width = 0
FEATURE [Part::Part2DObjectPython] Rectangle026  # Draft 2D object (typed FeaturePython)
  ChamferSize = 0
  FilletRadius = 0
  Height = -2700
  Length = 605.65
  MakeFace = true
  Placement = pos=(68947.7,11114.6,2750) rot=(0,0.707107,0.707107;3.14159rad)
FEATURE [Part::FeaturePython] Panel002  # WARN: FeaturePython — macro-defined, semantics opaque (R4)
  Base = -> Rectangle026
  Length = 0
  MoveWithHost = false
  Placement = pos=(-61047,-2894.61,3000) rot=(0,0,1;0rad)
  Role = 0
  Sheets = 1
  Thickness = 30
  Width = 0
FEATURE [Part::FeaturePython] Panel003  # WARN: FeaturePython — macro-defined, semantics opaque (R4)
  Base = -> Rectangle026
  Length = 0
  MoveWithHost = false
  Placement = pos=(-61047,-5064.61,3000) rot=(0,0,1;0rad)
  Role = 0
  Sheets = 1
  Thickness = 30
  Width = 0
FEATURE [Part::Part2DObjectPython] Rectangle027  # Draft 2D object (typed FeaturePython)
  ChamferSize = 0
  FilletRadius = 0
  Height = 2140
  Length = 605.652
  MakeFace = true
  Placement = pos=(68947.7,11084.6,1050) rot=(0,0,1;3.14159rad)
FEATURE [Part::FeaturePython] Panel008  # WARN: FeaturePython — macro-defined, semantics opaque (R4)
  Base = -> Rectangle027
  Length = 0
  MoveWithHost = false
  Placement = pos=(-61047,-2864.61,3000) rot=(0,0,1;0rad)
  Role = 0
  Sheets = 1
  Thickness = 30
  Width = 0
FEATURE [Part::FeaturePython] Panel009  # WARN: FeaturePython — macro-defined, semantics opaque (R4)
  Base = -> Rectangle027
  Length = 0
  MoveWithHost = false
  Placement = pos=(-61047,-2864.61,3030) rot=(0,0,1;0rad)
  Role = 0
  Sheets = 1
  Thickness = 30
  Width = 0
FEATURE [Part::FeaturePython] Panel010  # WARN: FeaturePython — macro-defined, semantics opaque (R4)
  Base = -> Rectangle027
  Length = 0
  MoveWithHost = false
  Placement = pos=(-61047,-2864.61,4170) rot=(0,0,1;0rad)
  Role = 0
  Sheets = 1
  Thickness = 30
  Width = 0
FEATURE [Part::Part2DObjectPython] Rectangle028  # Draft 2D object (typed FeaturePython)
  ChamferSize = 0
  FilletRadius = 0
  Height = -605.65
  Length = -1000
  MakeFace = true
  Placement = pos=(66791.9,8910.25,-1501) rot=(0.57735,-0.57735,-0.57735;4.18879rad)
FEATURE [Part::FeaturePython] Panel011  # WARN: FeaturePython — macro-defined, semantics opaque (R4)
  Base = -> Rectangle028
  Length = 0
  MoveWithHost = false
  Placement = pos=(-59496.9,-1420.24,4551) rot=(0,0,1;0rad)
  Role = 0
  Sheets = 1
  Thickness = 30
  Width = 0
FEATURE [Part::FeaturePython] Panel012  # WARN: FeaturePython — macro-defined, semantics opaque (R4)
  Base = -> Rectangle028
  Length = 0
  MoveWithHost = false
  Placement = pos=(-59496.9,-1450.24,4551) rot=(0,0,1;0rad)
  Role = 0
  Sheets = 1
  Thickness = 30
  Width = 0
FEATURE [Part::Part2DObjectPython] Rectangle029  # Draft 2D object (typed FeaturePython)
  ChamferSize = 0
  FilletRadius = 0
  Height = -605.652
  Length = -1110
  MakeFace = true
  Placement = pos=(68342,9704.61,1110) rot=(0.57735,-0.57735,-0.57735;4.18879rad)
FEATURE [Part::FeaturePython] Panel013  # WARN: FeaturePython — macro-defined, semantics opaque (R4)
  Base = -> Rectangle029
  Length = 0
  MoveWithHost = false
  Placement = pos=(-61047,-2894.61,3000) rot=(0,0,1;0rad)
  Role = 0
  Sheets = 1
  Thickness = 30
  Width = 0
FEATURE [Part::FeaturePython] Panel014  # WARN: FeaturePython — macro-defined, semantics opaque (R4)
  Base = -> Rectangle029
  Length = 0
  MoveWithHost = false
  Placement = pos=(-61047,-2924.61,3000) rot=(0,0,1;0rad)
  Role = 0
  Sheets = 1
  Thickness = 30
  Width = 0
FEATURE [Part::FeaturePython] Panel015  # WARN: FeaturePython — macro-defined, semantics opaque (R4)
  Base = -> Rectangle029
  Length = 0
  MoveWithHost = false
  Placement = pos=(-61047,-2214.61,3000) rot=(0,0,1;0rad)
  Role = 0
  Sheets = 1
  Thickness = 30
  Width = 0
FEATURE [Part::FeaturePython] Panel016  # WARN: FeaturePython — macro-defined, semantics opaque (R4)
  Base = -> Rectangle029
  Length = 0
  MoveWithHost = false
  Placement = pos=(-61047,-2244.61,3000) rot=(0,0,1;0rad)
  Role = 0
  Sheets = 1
  Thickness = 30
  Width = 0
FEATURE [Part::FeaturePython] Panel017  # WARN: FeaturePython — macro-defined, semantics opaque (R4)
  Base = -> Rectangle028
  Length = 0
  MoveWithHost = false
  Placement = pos=(-59496.9,-2100.24,4551) rot=(0,0,1;0rad)
  Role = 0
  Sheets = 1
  Thickness = 30
  Width = 0
FEATURE [Part::FeaturePython] Panel018  # WARN: FeaturePython — macro-defined, semantics opaque (R4)
  Base = -> Rectangle028
  Length = 0
  MoveWithHost = false
  Placement = pos=(-59496.9,-2130.24,4551) rot=(0,0,1;0rad)
  Role = 0
  Sheets = 1
  Thickness = 30
  Width = 0
FEATURE [Part::FeaturePython] Panel020  # WARN: FeaturePython — macro-defined, semantics opaque (R4)
  Base = -> Rectangle026
  Length = 0
  MoveWithHost = false
  Placement = pos=(-61047,4705.39,3000) rot=(0,0,1;0rad)
  Role = 0
  Sheets = 1
  Thickness = 30
  Width = 0
FEATURE [Part::FeaturePython] Panel021  # WARN: FeaturePython — macro-defined, semantics opaque (R4)
  Base = -> Rectangle025
  Length = 0
  MoveWithHost = false
  Placement = pos=(-61047,4735.39,3000) rot=(0,0,1;0rad)
  Role = 0
  Sheets = 1
  Thickness = 50
  Width = 0
FEATURE [Part::FeaturePython] Panel022  # WARN: FeaturePython — macro-defined, semantics opaque (R4)
  Base = -> Rectangle025
  Length = 0
  MoveWithHost = false
  Placement = pos=(-61047,4735.39,5750) rot=(0,0,1;0rad)
  Role = 0
  Sheets = 1
  Thickness = 50
  Width = 0
FEATURE [Part::FeaturePython] Panel023  # WARN: FeaturePython — macro-defined, semantics opaque (R4)
  Base = -> Rectangle026
  Length = 0
  MoveWithHost = false
  Placement = pos=(-61047,2535.39,3000) rot=(0,0,1;0rad)
  Role = 0
  Sheets = 1
  Thickness = 30
  Width = 0
FEATURE [Part::FeaturePython] Panel024  # WARN: FeaturePython — macro-defined, semantics opaque (R4)
  Base = -> Rectangle027
  Length = 0
  MoveWithHost = false
  Placement = pos=(-61047,4735.39,3000) rot=(0,0,1;0rad)
  Role = 0
  Sheets = 1
  Thickness = 30
  Width = 0
FEATURE [Part::FeaturePython] Panel025  # WARN: FeaturePython — macro-defined, semantics opaque (R4)
  Base = -> Rectangle027
  Length = 0
  MoveWithHost = false
  Placement = pos=(-61047,4735.39,3030) rot=(0,0,1;0rad)
  Role = 0
  Sheets = 1
  Thickness = 30
  Width = 0
FEATURE [Part::FeaturePython] Panel027  # WARN: FeaturePython — macro-defined, semantics opaque (R4)
  Base = -> Rectangle027
  Length = 0
  MoveWithHost = false
  Placement = pos=(-61047,4735.39,4170) rot=(0,0,1;0rad)
  Role = 0
  Sheets = 1
  Thickness = 30
  Width = 0
FEATURE [Part::FeaturePython] Panel029  # WARN: FeaturePython — macro-defined, semantics opaque (R4)
  Base = -> Rectangle029
  Length = 0
  MoveWithHost = false
  Placement = pos=(-61047,4705.39,3000) rot=(0,0,1;0rad)
  Role = 0
  Sheets = 1
  Thickness = 30
  Width = 0
FEATURE [Part::FeaturePython] Panel030  # WARN: FeaturePython — macro-defined, semantics opaque (R4)
  Base = -> Rectangle029
  Length = 0
  MoveWithHost = false
  Placement = pos=(-61047,4675.39,3000) rot=(0,0,1;0rad)
  Role = 0
  Sheets = 1
  Thickness = 30
  Width = 0
FEATURE [Part::FeaturePython] Panel031  # WARN: FeaturePython — macro-defined, semantics opaque (R4)
  Base = -> Rectangle029
  Length = 0
  MoveWithHost = false
  Placement = pos=(-61047,5355.39,3000) rot=(0,0,1;0rad)
  Role = 0
  Sheets = 1
  Thickness = 30
  Width = 0
FEATURE [Part::FeaturePython] Panel033  # WARN: FeaturePython — macro-defined, semantics opaque (R4)
  Base = -> Rectangle029
  Length = 0
  MoveWithHost = false
  Placement = pos=(-61047,5385.39,3000) rot=(0,0,1;0rad)
  Role = 0
  Sheets = 1
  Thickness = 30
  Width = 0
FEATURE [Part::Part2DObjectPython] Line294  # Draft 2D object (typed FeaturePython)
  ChamferSize = 0
  Closed = false
  End = (7295,13650,3000)
  FilletRadius = 0
  Length = 599.997
  MakeFace = true
  Points = (2) [(7895,13650,3000),(7295,13650,3000)]
  Start = (7895,13650,3000)
  Support = -> Wall052
FEATURE [Part::FeaturePython] Wall085  # WARN: FeaturePython — macro-defined, semantics opaque (R4)
  Align = 1
  Base = -> Line294
  Face = 0
  Height = 2800
  Length = 0
  MoveWithHost = false
  Normal = (0,0,0)
  Role = 0
  Width = 150
FEATURE [Part::FeaturePython] Panel034  # WARN: FeaturePython — macro-defined, semantics opaque (R4)
  Base = -> Rectangle028
  Length = 0
  MoveWithHost = false
  Placement = pos=(-59496.9,6149.75,4551) rot=(0,0,1;0rad)
  Role = 0
  Sheets = 1
  Thickness = 30
  Width = 0
FEATURE [Part::FeaturePython] Panel035  # WARN: FeaturePython — macro-defined, semantics opaque (R4)
  Base = -> Rectangle028
  Length = 0
  MoveWithHost = false
  Placement = pos=(-59496.9,5469.75,4551) rot=(0,0,1;0rad)
  Role = 0
  Sheets = 1
  Thickness = 30
  Width = 0
FEATURE [Part::FeaturePython] Panel036  # WARN: FeaturePython — macro-defined, semantics opaque (R4)
  Base = -> Rectangle028
  Length = 0
  MoveWithHost = false
  Placement = pos=(-59496.9,5499.75,4551) rot=(0,0,1;0rad)
  Role = 0
  Sheets = 1
  Thickness = 30
  Width = 0
FEATURE [Part::FeaturePython] Panel037  # WARN: FeaturePython — macro-defined, semantics opaque (R4)
  Base = -> Rectangle028
  Length = 0
  MoveWithHost = false
  Placement = pos=(-59496.9,6179.75,4551) rot=(0,0,1;0rad)
  Role = 0
  Sheets = 1
  Thickness = 30
  Width = 0
FEATURE [Part::Part2DObjectPython] Line296  # Draft 2D object (typed FeaturePython)
  ChamferSize = 0
  Closed = false
  End = (-4922,2055.31,11295)
  FilletRadius = 0
  Length = 2637.83
  MakeFace = true
  Placement = pos=(-4915,0.305262,0.0001461) rot=(0,0,1;0rad)
  Points = (2) [(-7,2055,8657.17),(-7,2055,11295)]
  Start = (-4922,2055.31,8657.17)
FEATURE [Part::Part2DObjectPython] Line297  # Draft 2D object (typed FeaturePython)
  ChamferSize = 0
  Closed = false
  End = (-3547,2055.31,11295)
  FilletRadius = 0
  Length = 2637.83
  MakeFace = true
  Placement = pos=(-4915,0.305262,0.0001461) rot=(0,0,1;0rad)
  Points = (2) [(1368,2055,8657.17),(1368,2055,11295)]
  Start = (-3547,2055.31,8657.17)
FEATURE [Part::Part2DObjectPython] Line298  # Draft 2D object (typed FeaturePython)
  ChamferSize = 0
  Closed = false
  End = (-2172,2055.31,11295)
  FilletRadius = 0
  Length = 2637.83
  MakeFace = true
  Placement = pos=(-4915,0.305262,0.0001461) rot=(0,0,1;0rad)
  Points = (2) [(2743,2055,8657.17),(2743,2055,11295)]
  Start = (-2172,2055.31,8657.17)
FEATURE [Part::Part2DObjectPython] Line299  # Draft 2D object (typed FeaturePython)
  ChamferSize = 0
  Closed = false
  End = (578.002,2055.31,11295)
  FilletRadius = 0
  Length = 2637.83
  MakeFace = true
  Placement = pos=(-2165,0.305262,0.0001461) rot=(0,0,1;0rad)
  Points = (2) [(2743,2055,8657.17),(2743,2055,11295)]
  Start = (578.002,2055.31,8657.17)
FEATURE [Part::Part2DObjectPython] Line300  # Draft 2D object (typed FeaturePython)
  ChamferSize = 0
  Closed = false
  End = (-796.998,2055.31,11295)
  FilletRadius = 0
  Length = 2637.83
  MakeFace = true
  Placement = pos=(-2165,0.305262,0.0001461) rot=(0,0,1;0rad)
  Points = (2) [(1368,2055,8657.17),(1368,2055,11295)]
  Start = (-796.998,2055.31,8657.17)
FEATURE [Part::Part2DObjectPython] Line301  # Draft 2D object (typed FeaturePython)
  ChamferSize = 0
  Closed = false
  End = (6078,2055.31,11295)
  FilletRadius = 0
  Length = 2637.83
  MakeFace = true
  Placement = pos=(3335,0.305262,0.0001461) rot=(0,0,1;0rad)
  Points = (2) [(2743,2055,8657.17),(2743,2055,11295)]
  Start = (6078,2055.31,8657.17)
FEATURE [Part::Part2DObjectPython] Line302  # Draft 2D object (typed FeaturePython)
  ChamferSize = 0
  Closed = false
  End = (4703,2055.31,11295)
  FilletRadius = 0
  Length = 2637.83
  MakeFace = true
  Placement = pos=(3335,0.305262,0.0001461) rot=(0,0,1;0rad)
  Points = (2) [(1368,2055,8657.17),(1368,2055,11295)]
  Start = (4703,2055.31,8657.17)
FEATURE [Part::Part2DObjectPython] Line303  # Draft 2D object (typed FeaturePython)
  ChamferSize = 0
  Closed = false
  End = (3328,2055.31,11295)
  FilletRadius = 0
  Length = 2637.83
  MakeFace = true
  Placement = pos=(585.002,0.305262,0.0001461) rot=(0,0,1;0rad)
  Points = (2) [(2743,2055,8657.17),(2743,2055,11295)]
  Start = (3328,2055.31,8657.17)
FEATURE [Part::Part2DObjectPython] Line304  # Draft 2D object (typed FeaturePython)
  ChamferSize = 0
  Closed = false
  End = (1953,2055.31,11295)
  FilletRadius = 0
  Length = 2637.83
  MakeFace = true
  Placement = pos=(585.002,0.305262,0.0001461) rot=(0,0,1;0rad)
  Points = (2) [(1368,2055,8657.17),(1368,2055,11295)]
  Start = (1953,2055.31,8657.17)
FEATURE [Part::Part2DObjectPython] Line306  # Draft 2D object (typed FeaturePython)
  ChamferSize = 0
  Closed = false
  End = (7963,2055.31,7588.33)
  FilletRadius = 0
  Length = 13928.8
  MakeFace = true
  Placement = pos=(-4915,2055.3,0.0001461) rot=(0,0,1;0rad)
  Points = (2) [(-997.708,0.00037986,6373),(12878,0.0004523,7588.33)]
  Start = (-5912.71,2055.31,6373)
FEATURE [Part::Part2DObjectPython] Line307  # Draft 2D object (typed FeaturePython)
  ChamferSize = 0
  Closed = false
  End = (7963,710.305,7588.33)
  FilletRadius = 0
  Length = 13928.8
  MakeFace = true
  Placement = pos=(-4915,710.305,0.0001461) rot=(0,0,1;0rad)
  Points = (2) [(-997.708,0.00037986,6373),(12878,0.0004523,7588.33)]
  Start = (-5912.71,710.305,6373)
FEATURE [Part::Part2DObjectPython] Line308  # Draft 2D object (typed FeaturePython)
  ChamferSize = 0
  Closed = false
  End = (-7467.8,2265.4,4817.9)
  FilletRadius = 0
  Length = 1656.49
  MakeFace = true
  Placement = pos=(-4915,0.305262,0.0001461) rot=(0,0,1;0rad)
  Points = (2) [(-1333,3381,4714),(-2552.8,2265.1,4817.9)]
  Start = (-6248,3381.3,4714)
FEATURE [Part::Part2DObjectPython] Line309  # Draft 2D object (typed FeaturePython)
  ChamferSize = 0
  Closed = false
  End = (-7,2055,6040)
  FilletRadius = 0
  Length = 1703.35
  MakeFace = true
  Points = (2) [(-997.708,710,6373),(-7,2055,6040)]
  Start = (-997.708,710,6373)
FEATURE [Part::Part2DObjectPython] Line310  # Draft 2D object (typed FeaturePython)
  ChamferSize = 0
  Closed = false
  End = (1368.2,710,6580.22)
  FilletRadius = 0
  Length = 1998.01
  MakeFace = true
  Points = (2) [(-7,2055,6040),(1368.2,710,6580.22)]
  Start = (-7,2055,6040)
FEATURE [Part::Part2DObjectPython] Line311  # Draft 2D object (typed FeaturePython)
  ChamferSize = 0
  Closed = false
  End = (2743,2055,6040)
  FilletRadius = 0
  Length = 1997.89
  MakeFace = true
  Points = (2) [(1368,710,6580.3),(2743,2055,6040)]
  Start = (1368,710,6580.3)
FEATURE [Part::Part2DObjectPython] Line312  # Draft 2D object (typed FeaturePython)
  ChamferSize = 0
  Closed = false
  End = (4118,710,6820.74)
  FilletRadius = 0
  Length = 2075.86
  MakeFace = true
  Points = (2) [(2743,2055,6040),(4118,710,6820.74)]
  Start = (2743,2055,6040)
FEATURE [Part::Part2DObjectPython] Line313  # Draft 2D object (typed FeaturePython)
  ChamferSize = 0
  Closed = false
  End = (5493,2055,6040)
  FilletRadius = 0
  Length = 2075.86
  MakeFace = true
  Points = (2) [(4118,710,6820.74),(5493,2055,6040)]
  Start = (4118,710,6820.74)
FEATURE [Part::Part2DObjectPython] Line314  # Draft 2D object (typed FeaturePython)
  ChamferSize = 0
  Closed = false
  End = (6868,710,7061.16)
  FilletRadius = 0
  Length = 2177.71
  MakeFace = true
  Points = (2) [(5493,2055,6040),(6868,710,7061.16)]
  Start = (5493,2055,6040)
FEATURE [Part::Part2DObjectPython] Line315  # Draft 2D object (typed FeaturePython)
  ChamferSize = 0
  Closed = false
  End = (8243,2055,6040)
  FilletRadius = 0
  Length = 2177.71
  MakeFace = true
  Points = (2) [(6868,710,7061.16),(8243,2055,6040)]
  Start = (6868,710,7061.16)
FEATURE [Part::Part2DObjectPython] Line316  # Draft 2D object (typed FeaturePython)
  ChamferSize = 0
  Closed = false
  End = (9618,710,7301.44)
  FilletRadius = 0
  Length = 2300.19
  MakeFace = true
  Points = (2) [(8243,2055,6040),(9618,710,7301.44)]
  Start = (8243,2055,6040)
FEATURE [Part::Part2DObjectPython] Line317  # Draft 2D object (typed FeaturePython)
  ChamferSize = 0
  Closed = false
  End = (10993,2055,6040)
  FilletRadius = 0
  Length = 2300.19
  MakeFace = true
  Points = (2) [(9618,710,7301.44),(10993,2055,6040)]
  Start = (9618,710,7301.44)
FEATURE [Part::Part2DObjectPython] Line318  # Draft 2D object (typed FeaturePython)
  ChamferSize = 0
  Closed = false
  End = (12878,710,7588.33)
  FilletRadius = 0
  Length = 2785.6
  MakeFace = true
  Points = (2) [(10993,2055,6040),(12878,710,7588.33)]
  Start = (10993,2055,6040)
FEATURE [Part::Part2DObjectPython] Line004  # Draft 2D object (typed FeaturePython)
  ChamferSize = 0
  Closed = false
  End = (10920,6050,3000)
  FilletRadius = 0
  Length = 2200
  MakeFace = true
  Placement = pos=(0,0,3000) rot=(0,0,1;0rad)
  Points = (2) [(10920,8250,0),(10920,6050,0)]
  Start = (10920,8250,3000)
FEATURE [Part::FeaturePython] Wall030  # WARN: FeaturePython — macro-defined, semantics opaque (R4)
  Align = 2
  Base = -> Line004
  Face = 0
  Height = 2800
  Length = 0
  MoveWithHost = false
  Normal = (0,0,0)
  Placement = pos=(-3.8e-08,0,0) rot=(0,0,1;0rad)
  Role = 0
  Subtractions = -> [Window003]
  Width = 150
FEATURE [Part::Part2DObjectPython] Line319  # Draft 2D object (typed FeaturePython)
  ChamferSize = 0
  Closed = false
  End = (-997.913,3440,6373.08)
  FilletRadius = 0
  Length = 1703.49
  MakeFace = true
  Placement = pos=(0,40,0) rot=(0,0,1;0rad)
  Points = (2) [(-7,2055,6040),(-997.913,3400,6373.08)]
  Start = (-7,2095,6040)
FEATURE [Part::Part2DObjectPython] Line320  # Draft 2D object (typed FeaturePython)
  ChamferSize = 0
  Closed = false
  End = (1367.8,3440,6580.38)
  FilletRadius = 0
  Length = 1997.77
  MakeFace = true
  Placement = pos=(0,40,0) rot=(0,0,1;0rad)
  Points = (2) [(-7,2055,6040),(1367.8,3400,6580.38)]
  Start = (-7,2095,6040)
FEATURE [Part::Part2DObjectPython] Line321  # Draft 2D object (typed FeaturePython)
  ChamferSize = 0
  Closed = false
  End = (2743,2095,6040)
  FilletRadius = 0
  Length = 1998.05
  MakeFace = true
  Placement = pos=(0,40,0) rot=(0,0,1;0rad)
  Points = (2) [(1367.8,3400,6580.38),(2743,2055,6040)]
  Start = (1367.8,3440,6580.38)
FEATURE [Part::Part2DObjectPython] Line322  # Draft 2D object (typed FeaturePython)
  ChamferSize = 0
  Closed = false
  End = (4117.8,3440,6820.82)
  FilletRadius = 0
  Length = 2075.76
  MakeFace = true
  Placement = pos=(0,40,0) rot=(0,0,1;0rad)
  Points = (2) [(2743,2055,6040),(4117.8,3400,6820.82)]
  Start = (2743,2095,6040)
FEATURE [Part::Part2DObjectPython] Line323  # Draft 2D object (typed FeaturePython)
  ChamferSize = 0
  Closed = false
  End = (5493,2095,6040)
  FilletRadius = 0
  Length = 2076.03
  MakeFace = true
  Placement = pos=(0,40,0) rot=(0,0,1;0rad)
  Points = (2) [(4117.8,3400,6820.82),(5493,2055,6040)]
  Start = (4117.8,3440,6820.82)
FEATURE [Part::Part2DObjectPython] Line324  # Draft 2D object (typed FeaturePython)
  ChamferSize = 0
  Closed = false
  End = (6867.8,3440,7061.24)
  FilletRadius = 0
  Length = 2177.62
  MakeFace = true
  Placement = pos=(0,40,0) rot=(0,0,1;0rad)
  Points = (2) [(5493,2055,6040),(6867.8,3400,7061.24)]
  Start = (5493,2095,6040)
FEATURE [Part::Part2DObjectPython] Line325  # Draft 2D object (typed FeaturePython)
  ChamferSize = 0
  Closed = false
  End = (8243,2095,6040)
  FilletRadius = 0
  Length = 2177.88
  MakeFace = true
  Placement = pos=(0,40,0) rot=(0,0,1;0rad)
  Points = (2) [(6867.8,3400,7061.24),(8243,2055,6040)]
  Start = (6867.8,3440,7061.24)
FEATURE [Part::Part2DObjectPython] Line326  # Draft 2D object (typed FeaturePython)
  ChamferSize = 0
  Closed = false
  End = (9617.8,3440,7301.52)
  FilletRadius = 0
  Length = 2300.11
  MakeFace = true
  Placement = pos=(0,40,0) rot=(0,0,1;0rad)
  Points = (2) [(8243,2055,6040),(9617.8,3400,7301.52)]
  Start = (8243,2095,6040)
FEATURE [Part::Part2DObjectPython] Line327  # Draft 2D object (typed FeaturePython)
  ChamferSize = 0
  Closed = false
  End = (10993,2095,6040)
  FilletRadius = 0
  Length = 2300.36
  MakeFace = true
  Placement = pos=(0,40,0) rot=(0,0,1;0rad)
  Points = (2) [(9617.8,3400,7301.52),(10993,2055,6040)]
  Start = (9617.8,3440,7301.52)
FEATURE [Part::Part2DObjectPython] Line328  # Draft 2D object (typed FeaturePython)
  ChamferSize = 0
  Closed = false
  End = (12877.8,3440,7588.41)
  FilletRadius = 0
  Length = 2785.51
  MakeFace = true
  Placement = pos=(0,40,0) rot=(0,0,1;0rad)
  Points = (2) [(10993,2055,6040),(12877.8,3400,7588.41)]
  Start = (10993,2095,6040)
FEATURE [Part::Part2DObjectPython] Line329  # Draft 2D object (typed FeaturePython)
  ChamferSize = 0
  Closed = false
  End = (10993,4865,6040)
  FilletRadius = 0
  Length = 2300.36
  MakeFace = true
  Placement = pos=(0,2810,0) rot=(0,0,1;0rad)
  Points = (2) [(9617.8,3400,7301.52),(10993,2055,6040)]
  Start = (9617.8,6210,7301.52)
FEATURE [Part::Part2DObjectPython] Line330  # Draft 2D object (typed FeaturePython)
  ChamferSize = 0
  Closed = false
  End = (12877.8,6210,7588.41)
  FilletRadius = 0
  Length = 2785.51
  MakeFace = true
  Placement = pos=(0,2810,0) rot=(0,0,1;0rad)
  Points = (2) [(10993,2055,6040),(12877.8,3400,7588.41)]
  Start = (10993,4865,6040)
FEATURE [Part::Part2DObjectPython] Line331  # Draft 2D object (typed FeaturePython)
  ChamferSize = 0
  Closed = false
  End = (9617.8,6210,7301.52)
  FilletRadius = 0
  Length = 2300.11
  MakeFace = true
  Placement = pos=(0,2810,0) rot=(0,0,1;0rad)
  Points = (2) [(8243,2055,6040),(9617.8,3400,7301.52)]
  Start = (8243,4865,6040)
FEATURE [Part::Part2DObjectPython] Line332  # Draft 2D object (typed FeaturePython)
  ChamferSize = 0
  Closed = false
  End = (8243,4865,6040)
  FilletRadius = 0
  Length = 2177.88
  MakeFace = true
  Placement = pos=(0,2810,0) rot=(0,0,1;0rad)
  Points = (2) [(6867.8,3400,7061.24),(8243,2055,6040)]
  Start = (6867.8,6210,7061.24)
FEATURE [Part::Part2DObjectPython] Line333  # Draft 2D object (typed FeaturePython)
  ChamferSize = 0
  Closed = false
  End = (6867.8,6210,7061.24)
  FilletRadius = 0
  Length = 2177.62
  MakeFace = true
  Placement = pos=(0,2810,0) rot=(0,0,1;0rad)
  Points = (2) [(5493,2055,6040),(6867.8,3400,7061.24)]
  Start = (5493,4865,6040)
FEATURE [Part::Part2DObjectPython] Line334  # Draft 2D object (typed FeaturePython)
  ChamferSize = 0
  Closed = false
  End = (5493,4865,6040)
  FilletRadius = 0
  Length = 2076.03
  MakeFace = true
  Placement = pos=(0,2810,0) rot=(0,0,1;0rad)
  Points = (2) [(4117.8,3400,6820.82),(5493,2055,6040)]
  Start = (4117.8,6210,6820.82)
FEATURE [Part::Part2DObjectPython] Line335  # Draft 2D object (typed FeaturePython)
  ChamferSize = 0
  Closed = false
  End = (4117.8,6210,6820.82)
  FilletRadius = 0
  Length = 2075.76
  MakeFace = true
  Placement = pos=(0,2810,0) rot=(0,0,1;0rad)
  Points = (2) [(2743,2055,6040),(4117.8,3400,6820.82)]
  Start = (2743,4865,6040)
FEATURE [Part::Part2DObjectPython] Line336  # Draft 2D object (typed FeaturePython)
  ChamferSize = 0
  Closed = false
  End = (2743,4865,6040)
  FilletRadius = 0
  Length = 1998.05
  MakeFace = true
  Placement = pos=(0,2810,0) rot=(0,0,1;0rad)
  Points = (2) [(1367.8,3400,6580.38),(2743,2055,6040)]
  Start = (1367.8,6210,6580.38)
FEATURE [Part::Part2DObjectPython] Line337  # Draft 2D object (typed FeaturePython)
  ChamferSize = 0
  Closed = false
  End = (1367.8,6210,6580.38)
  FilletRadius = 0
  Length = 1997.77
  MakeFace = true
  Placement = pos=(0,2810,0) rot=(0,0,1;0rad)
  Points = (2) [(-7,2055,6040),(1367.8,3400,6580.38)]
  Start = (-7,4865,6040)
FEATURE [Part::Part2DObjectPython] Line338  # Draft 2D object (typed FeaturePython)
  ChamferSize = 0
  Closed = false
  End = (-997.913,6210,6373.08)
  FilletRadius = 0
  Length = 1703.49
  MakeFace = true
  Placement = pos=(0,2810,0) rot=(0,0,1;0rad)
  Points = (2) [(-7,2055,6040),(-997.913,3400,6373.08)]
  Start = (-7,4865,6040)
FEATURE [Part::Part2DObjectPython] Line339  # Draft 2D object (typed FeaturePython)
  ChamferSize = 0
  Closed = false
  End = (1368.2,3480,6580.22)
  FilletRadius = 0
  Length = 1998.01
  MakeFace = true
  Placement = pos=(0,2770,0) rot=(0,0,1;0rad)
  Points = (2) [(-7,2055,6040),(1368.2,710,6580.22)]
  Start = (-7,4825,6040)
FEATURE [Part::Part2DObjectPython] Line340  # Draft 2D object (typed FeaturePython)
  ChamferSize = 0
  Closed = false
  End = (-7,4825,6040)
  FilletRadius = 0
  Length = 1703.35
  MakeFace = true
  Placement = pos=(0,2770,0) rot=(0,0,1;0rad)
  Points = (2) [(-997.708,710,6373),(-7,2055,6040)]
  Start = (-997.708,3480,6373)
FEATURE [Part::Part2DObjectPython] Line341  # Draft 2D object (typed FeaturePython)
  ChamferSize = 0
  Closed = false
  End = (2743,4825,6040)
  FilletRadius = 0
  Length = 1997.89
  MakeFace = true
  Placement = pos=(0,2770,0) rot=(0,0,1;0rad)
  Points = (2) [(1368,710,6580.3),(2743,2055,6040)]
  Start = (1368,3480,6580.3)
FEATURE [Part::Part2DObjectPython] Line342  # Draft 2D object (typed FeaturePython)
  ChamferSize = 0
  Closed = false
  End = (4118,3480,6820.74)
  FilletRadius = 0
  Length = 2075.86
  MakeFace = true
  Placement = pos=(0,2770,0) rot=(0,0,1;0rad)
  Points = (2) [(2743,2055,6040),(4118,710,6820.74)]
  Start = (2743,4825,6040)
FEATURE [Part::Part2DObjectPython] Line343  # Draft 2D object (typed FeaturePython)
  ChamferSize = 0
  Closed = false
  End = (5493,4825,6040)
  FilletRadius = 0
  Length = 2075.86
  MakeFace = true
  Placement = pos=(0,2770,0) rot=(0,0,1;0rad)
  Points = (2) [(4118,710,6820.74),(5493,2055,6040)]
  Start = (4118,3480,6820.74)
FEATURE [Part::Part2DObjectPython] Line344  # Draft 2D object (typed FeaturePython)
  ChamferSize = 0
  Closed = false
  End = (6868,3480,7061.16)
  FilletRadius = 0
  Length = 2177.71
  MakeFace = true
  Placement = pos=(0,2770,0) rot=(0,0,1;0rad)
  Points = (2) [(5493,2055,6040),(6868,710,7061.16)]
  Start = (5493,4825,6040)
FEATURE [Part::Part2DObjectPython] Line345  # Draft 2D object (typed FeaturePython)
  ChamferSize = 0
  Closed = false
  End = (8243,4825,6040)
  FilletRadius = 0
  Length = 2177.71
  MakeFace = true
  Placement = pos=(0,2770,0) rot=(0,0,1;0rad)
  Points = (2) [(6868,710,7061.16),(8243,2055,6040)]
  Start = (6868,3480,7061.16)
FEATURE [Part::Part2DObjectPython] Line346  # Draft 2D object (typed FeaturePython)
  ChamferSize = 0
  Closed = false
  End = (9618,3480,7301.44)
  FilletRadius = 0
  Length = 2300.19
  MakeFace = true
  Placement = pos=(0,2770,0) rot=(0,0,1;0rad)
  Points = (2) [(8243,2055,6040),(9618,710,7301.44)]
  Start = (8243,4825,6040)
FEATURE [Part::Part2DObjectPython] Line347  # Draft 2D object (typed FeaturePython)
  ChamferSize = 0
  Closed = false
  End = (10993,4825,6040)
  FilletRadius = 0
  Length = 2300.19
  MakeFace = true
  Placement = pos=(0,2770,0) rot=(0,0,1;0rad)
  Points = (2) [(9618,710,7301.44),(10993,2055,6040)]
  Start = (9618,3480,7301.44)
FEATURE [Part::Part2DObjectPython] Line348  # Draft 2D object (typed FeaturePython)
  ChamferSize = 0
  Closed = false
  End = (12878,3480,7588.33)
  FilletRadius = 0
  Length = 2785.6
  MakeFace = true
  Placement = pos=(0,2770,0) rot=(0,0,1;0rad)
  Points = (2) [(10993,2055,6040),(12878,710,7588.33)]
  Start = (10993,4825,6040)
FEATURE [Part::Part2DObjectPython] Line349  # Draft 2D object (typed FeaturePython)
  ChamferSize = 0
  Closed = false
  End = (12877.8,8980,7588.41)
  FilletRadius = 0
  Length = 2785.51
  MakeFace = true
  Placement = pos=(0,5580,0) rot=(0,0,1;0rad)
  Points = (2) [(10993,2055,6040),(12877.8,3400,7588.41)]
  Start = (10993,7635,6040)
FEATURE [Part::Part2DObjectPython] Line350  # Draft 2D object (typed FeaturePython)
  ChamferSize = 0
  Closed = false
  End = (10993,7635,6040)
  FilletRadius = 0
  Length = 2300.36
  MakeFace = true
  Placement = pos=(0,5580,0) rot=(0,0,1;0rad)
  Points = (2) [(9617.8,3400,7301.52),(10993,2055,6040)]
  Start = (9617.8,8980,7301.52)
FEATURE [Part::Part2DObjectPython] Line351  # Draft 2D object (typed FeaturePython)
  ChamferSize = 0
  Closed = false
  End = (9617.8,8980,7301.52)
  FilletRadius = 0
  Length = 2300.11
  MakeFace = true
  Placement = pos=(0,5580,0) rot=(0,0,1;0rad)
  Points = (2) [(8243,2055,6040),(9617.8,3400,7301.52)]
  Start = (8243,7635,6040)
FEATURE [Part::Part2DObjectPython] Line352  # Draft 2D object (typed FeaturePython)
  ChamferSize = 0
  Closed = false
  End = (8243,7635,6040)
  FilletRadius = 0
  Length = 2177.88
  MakeFace = true
  Placement = pos=(0,5580,0) rot=(0,0,1;0rad)
  Points = (2) [(6867.8,3400,7061.24),(8243,2055,6040)]
  Start = (6867.8,8980,7061.24)
FEATURE [Part::Part2DObjectPython] Line353  # Draft 2D object (typed FeaturePython)
  ChamferSize = 0
  Closed = false
  End = (6867.8,8980,7061.24)
  FilletRadius = 0
  Length = 2177.62
  MakeFace = true
  Placement = pos=(0,5580,0) rot=(0,0,1;0rad)
  Points = (2) [(5493,2055,6040),(6867.8,3400,7061.24)]
  Start = (5493,7635,6040)
FEATURE [Part::Part2DObjectPython] Line354  # Draft 2D object (typed FeaturePython)
  ChamferSize = 0
  Closed = false
  End = (5493,7635,6040)
  FilletRadius = 0
  Length = 2076.03
  MakeFace = true
  Placement = pos=(0,5580,0) rot=(0,0,1;0rad)
  Points = (2) [(4117.8,3400,6820.82),(5493,2055,6040)]
  Start = (4117.8,8980,6820.82)
FEATURE [Part::Part2DObjectPython] Line355  # Draft 2D object (typed FeaturePython)
  ChamferSize = 0
  Closed = false
  End = (4117.8,8980,6820.82)
  FilletRadius = 0
  Length = 2075.76
  MakeFace = true
  Placement = pos=(0,5580,0) rot=(0,0,1;0rad)
  Points = (2) [(2743,2055,6040),(4117.8,3400,6820.82)]
  Start = (2743,7635,6040)
FEATURE [Part::Part2DObjectPython] Line356  # Draft 2D object (typed FeaturePython)
  ChamferSize = 0
  Closed = false
  End = (2743,7635,6040)
  FilletRadius = 0
  Length = 1998.05
  MakeFace = true
  Placement = pos=(0,5580,0) rot=(0,0,1;0rad)
  Points = (2) [(1367.8,3400,6580.38),(2743,2055,6040)]
  Start = (1367.8,8980,6580.38)
FEATURE [Part::Part2DObjectPython] Line357  # Draft 2D object (typed FeaturePython)
  ChamferSize = 0
  Closed = false
  End = (1367.8,8980,6580.38)
  FilletRadius = 0
  Length = 1997.77
  MakeFace = true
  Placement = pos=(0,5580,0) rot=(0,0,1;0rad)
  Points = (2) [(-7,2055,6040),(1367.8,3400,6580.38)]
  Start = (-7,7635,6040)
FEATURE [Part::Part2DObjectPython] Line358  # Draft 2D object (typed FeaturePython)
  ChamferSize = 0
  Closed = false
  End = (-997.913,8980,6373.08)
  FilletRadius = 0
  Length = 1703.49
  MakeFace = true
  Placement = pos=(0,5580,0) rot=(0,0,1;0rad)
  Points = (2) [(-7,2055,6040),(-997.913,3400,6373.08)]
  Start = (-7,7635,6040)
FEATURE [Part::Part2DObjectPython] Line359  # Draft 2D object (typed FeaturePython)
  ChamferSize = 0
  Closed = false
  End = (-7,7595,6040)
  FilletRadius = 0
  Length = 1703.35
  MakeFace = true
  Placement = pos=(0,5540,0) rot=(0,0,1;0rad)
  Points = (2) [(-997.708,710,6373),(-7,2055,6040)]
  Start = (-997.708,6250,6373)
FEATURE [Part::Part2DObjectPython] Line360  # Draft 2D object (typed FeaturePython)
  ChamferSize = 0
  Closed = false
  End = (1368.2,6250,6580.22)
  FilletRadius = 0
  Length = 1998.01
  MakeFace = true
  Placement = pos=(0,5540,0) rot=(0,0,1;0rad)
  Points = (2) [(-7,2055,6040),(1368.2,710,6580.22)]
  Start = (-7,7595,6040)
FEATURE [Part::Part2DObjectPython] Line361  # Draft 2D object (typed FeaturePython)
  ChamferSize = 0
  Closed = false
  End = (2743,7595,6040)
  FilletRadius = 0
  Length = 1997.89
  MakeFace = true
  Placement = pos=(0,5540,0) rot=(0,0,1;0rad)
  Points = (2) [(1368,710,6580.3),(2743,2055,6040)]
  Start = (1368,6250,6580.3)
FEATURE [Part::Part2DObjectPython] Line362  # Draft 2D object (typed FeaturePython)
  ChamferSize = 0
  Closed = false
  End = (4118,6250,6820.74)
  FilletRadius = 0
  Length = 2075.86
  MakeFace = true
  Placement = pos=(0,5540,0) rot=(0,0,1;0rad)
  Points = (2) [(2743,2055,6040),(4118,710,6820.74)]
  Start = (2743,7595,6040)
FEATURE [Part::Part2DObjectPython] Line363  # Draft 2D object (typed FeaturePython)
  ChamferSize = 0
  Closed = false
  End = (5493,7595,6040)
  FilletRadius = 0
  Length = 2075.86
  MakeFace = true
  Placement = pos=(0,5540,0) rot=(0,0,1;0rad)
  Points = (2) [(4118,710,6820.74),(5493,2055,6040)]
  Start = (4118,6250,6820.74)
FEATURE [Part::Part2DObjectPython] Line364  # Draft 2D object (typed FeaturePython)
  ChamferSize = 0
  Closed = false
  End = (6868,6250,7061.16)
  FilletRadius = 0
  Length = 2177.71
  MakeFace = true
  Placement = pos=(0,5540,0) rot=(0,0,1;0rad)
  Points = (2) [(5493,2055,6040),(6868,710,7061.16)]
  Start = (5493,7595,6040)
FEATURE [Part::Part2DObjectPython] Line365  # Draft 2D object (typed FeaturePython)
  ChamferSize = 0
  Closed = false
  End = (8243,7595,6040)
  FilletRadius = 0
  Length = 2177.71
  MakeFace = true
  Placement = pos=(0,5540,0) rot=(0,0,1;0rad)
  Points = (2) [(6868,710,7061.16),(8243,2055,6040)]
  Start = (6868,6250,7061.16)
FEATURE [Part::Part2DObjectPython] Line366  # Draft 2D object (typed FeaturePython)
  ChamferSize = 0
  Closed = false
  End = (9618,6250,7301.44)
  FilletRadius = 0
  Length = 2300.19
  MakeFace = true
  Placement = pos=(0,5540,0) rot=(0,0,1;0rad)
  Points = (2) [(8243,2055,6040),(9618,710,7301.44)]
  Start = (8243,7595,6040)
FEATURE [Part::Part2DObjectPython] Line367  # Draft 2D object (typed FeaturePython)
  ChamferSize = 0
  Closed = false
  End = (10993,7595,6040)
  FilletRadius = 0
  Length = 2300.19
  MakeFace = true
  Placement = pos=(0,5540,0) rot=(0,0,1;0rad)
  Points = (2) [(9618,710,7301.44),(10993,2055,6040)]
  Start = (9618,6250,7301.44)
FEATURE [Part::Part2DObjectPython] Line368  # Draft 2D object (typed FeaturePython)
  ChamferSize = 0
  Closed = false
  End = (12878,6250,7588.33)
  FilletRadius = 0
  Length = 2785.6
  MakeFace = true
  Placement = pos=(0,5540,0) rot=(0,0,1;0rad)
  Points = (2) [(10993,2055,6040),(12878,710,7588.33)]
  Start = (10993,7595,6040)
FEATURE [Part::Part2DObjectPython] Line369  # Draft 2D object (typed FeaturePython)
  ChamferSize = 0
  Closed = false
  End = (12878,9020,7588.33)
  FilletRadius = 0
  Length = 2785.6
  MakeFace = true
  Placement = pos=(0,8310,0) rot=(0,0,1;0rad)
  Points = (2) [(10993,2055,6040),(12878,710,7588.33)]
  Start = (10993,10365,6040)
FEATURE [Part::Part2DObjectPython] Line370  # Draft 2D object (typed FeaturePython)
  ChamferSize = 0
  Closed = false
  End = (12877.8,11750,7588.41)
  FilletRadius = 0
  Length = 2785.51
  MakeFace = true
  Placement = pos=(0,8350,0) rot=(0,0,1;0rad)
  Points = (2) [(10993,2055,6040),(12877.8,3400,7588.41)]
  Start = (10993,10405,6040)
FEATURE [Part::Part2DObjectPython] Line371  # Draft 2D object (typed FeaturePython)
  ChamferSize = 0
  Closed = false
  End = (10993,10405,6040)
  FilletRadius = 0
  Length = 2300.36
  MakeFace = true
  Placement = pos=(0,8350,0) rot=(0,0,1;0rad)
  Points = (2) [(9617.8,3400,7301.52),(10993,2055,6040)]
  Start = (9617.8,11750,7301.52)
FEATURE [Part::Part2DObjectPython] Line372  # Draft 2D object (typed FeaturePython)
  ChamferSize = 0
  Closed = false
  End = (10993,10365,6040)
  FilletRadius = 0
  Length = 2300.19
  MakeFace = true
  Placement = pos=(0,8310,0) rot=(0,0,1;0rad)
  Points = (2) [(9618,710,7301.44),(10993,2055,6040)]
  Start = (9618,9020,7301.44)
FEATURE [Part::Part2DObjectPython] Line373  # Draft 2D object (typed FeaturePython)
  ChamferSize = 0
  Closed = false
  End = (9618,9020,7301.44)
  FilletRadius = 0
  Length = 2300.19
  MakeFace = true
  Placement = pos=(0,8310,0) rot=(0,0,1;0rad)
  Points = (2) [(8243,2055,6040),(9618,710,7301.44)]
  Start = (8243,10365,6040)
FEATURE [Part::Part2DObjectPython] Line374  # Draft 2D object (typed FeaturePython)
  ChamferSize = 0
  Closed = false
  End = (9617.8,11750,7301.52)
  FilletRadius = 0
  Length = 2300.11
  MakeFace = true
  Placement = pos=(0,8350,0) rot=(0,0,1;0rad)
  Points = (2) [(8243,2055,6040),(9617.8,3400,7301.52)]
  Start = (8243,10405,6040)
FEATURE [Part::Part2DObjectPython] Line375  # Draft 2D object (typed FeaturePython)
  ChamferSize = 0
  Closed = false
  End = (8243,10405,6040)
  FilletRadius = 0
  Length = 2177.88
  MakeFace = true
  Placement = pos=(0,8350,0) rot=(0,0,1;0rad)
  Points = (2) [(6867.8,3400,7061.24),(8243,2055,6040)]
  Start = (6867.8,11750,7061.24)
FEATURE [Part::Part2DObjectPython] Line376  # Draft 2D object (typed FeaturePython)
  ChamferSize = 0
  Closed = false
  End = (8243,10365,6040)
  FilletRadius = 0
  Length = 2177.71
  MakeFace = true
  Placement = pos=(0,8310,0) rot=(0,0,1;0rad)
  Points = (2) [(6868,710,7061.16),(8243,2055,6040)]
  Start = (6868,9020,7061.16)
FEATURE [Part::Part2DObjectPython] Line377  # Draft 2D object (typed FeaturePython)
  ChamferSize = 0
  Closed = false
  End = (6868,9020,7061.16)
  FilletRadius = 0
  Length = 2177.71
  MakeFace = true
  Placement = pos=(0,8310,0) rot=(0,0,1;0rad)
  Points = (2) [(5493,2055,6040),(6868,710,7061.16)]
  Start = (5493,10365,6040)
FEATURE [Part::Part2DObjectPython] Line378  # Draft 2D object (typed FeaturePython)
  ChamferSize = 0
  Closed = false
  End = (6867.8,11750,7061.24)
  FilletRadius = 0
  Length = 2177.62
  MakeFace = true
  Placement = pos=(0,8350,0) rot=(0,0,1;0rad)
  Points = (2) [(5493,2055,6040),(6867.8,3400,7061.24)]
  Start = (5493,10405,6040)
FEATURE [Part::Part2DObjectPython] Line379  # Draft 2D object (typed FeaturePython)
  ChamferSize = 0
  Closed = false
  End = (5493,10405,6040)
  FilletRadius = 0
  Length = 2076.03
  MakeFace = true
  Placement = pos=(0,8350,0) rot=(0,0,1;0rad)
  Points = (2) [(4117.8,3400,6820.82),(5493,2055,6040)]
  Start = (4117.8,11750,6820.82)
FEATURE [Part::Part2DObjectPython] Line380  # Draft 2D object (typed FeaturePython)
  ChamferSize = 0
  Closed = false
  End = (5493,10365,6040)
  FilletRadius = 0
  Length = 2075.86
  MakeFace = true
  Placement = pos=(0,8310,0) rot=(0,0,1;0rad)
  Points = (2) [(4118,710,6820.74),(5493,2055,6040)]
  Start = (4118,9020,6820.74)
FEATURE [Part::Part2DObjectPython] Line381  # Draft 2D object (typed FeaturePython)
  ChamferSize = 0
  Closed = false
  End = (4118,9020,6820.74)
  FilletRadius = 0
  Length = 2075.86
  MakeFace = true
  Placement = pos=(0,8310,0) rot=(0,0,1;0rad)
  Points = (2) [(2743,2055,6040),(4118,710,6820.74)]
  Start = (2743,10365,6040)
FEATURE [Part::Part2DObjectPython] Line382  # Draft 2D object (typed FeaturePython)
  ChamferSize = 0
  Closed = false
  End = (4117.8,11750,6820.82)
  FilletRadius = 0
  Length = 2075.76
  MakeFace = true
  Placement = pos=(0,8350,0) rot=(0,0,1;0rad)
  Points = (2) [(2743,2055,6040),(4117.8,3400,6820.82)]
  Start = (2743,10405,6040)
FEATURE [Part::Part2DObjectPython] Line383  # Draft 2D object (typed FeaturePython)
  ChamferSize = 0
  Closed = false
  End = (2743,10405,6040)
  FilletRadius = 0
  Length = 1998.05
  MakeFace = true
  Placement = pos=(0,8350,0) rot=(0,0,1;0rad)
  Points = (2) [(1367.8,3400,6580.38),(2743,2055,6040)]
  Start = (1367.8,11750,6580.38)
FEATURE [Part::Part2DObjectPython] Line384  # Draft 2D object (typed FeaturePython)
  ChamferSize = 0
  Closed = false
  End = (2743,10365,6040)
  FilletRadius = 0
  Length = 1997.89
  MakeFace = true
  Placement = pos=(0,8310,0) rot=(0,0,1;0rad)
  Points = (2) [(1368,710,6580.3),(2743,2055,6040)]
  Start = (1368,9020,6580.3)
FEATURE [Part::Part2DObjectPython] Line385  # Draft 2D object (typed FeaturePython)
  ChamferSize = 0
  Closed = false
  End = (1368.2,9020,6580.22)
  FilletRadius = 0
  Length = 1998.01
  MakeFace = true
  Placement = pos=(0,8310,0) rot=(0,0,1;0rad)
  Points = (2) [(-7,2055,6040),(1368.2,710,6580.22)]
  Start = (-7,10365,6040)
FEATURE [Part::Part2DObjectPython] Line386  # Draft 2D object (typed FeaturePython)
  ChamferSize = 0
  Closed = false
  End = (1367.8,11750,6580.38)
  FilletRadius = 0
  Length = 1997.77
  MakeFace = true
  Placement = pos=(0,8350,0) rot=(0,0,1;0rad)
  Points = (2) [(-7,2055,6040),(1367.8,3400,6580.38)]
  Start = (-7,10405,6040)
FEATURE [Part::Part2DObjectPython] Line387  # Draft 2D object (typed FeaturePython)
  ChamferSize = 0
  Closed = false
  End = (-997.913,11750,6373.08)
  FilletRadius = 0
  Length = 1703.49
  MakeFace = true
  Placement = pos=(0,8350,0) rot=(0,0,1;0rad)
  Points = (2) [(-7,2055,6040),(-997.913,3400,6373.08)]
  Start = (-7,10405,6040)
FEATURE [Part::Part2DObjectPython] Line388  # Draft 2D object (typed FeaturePython)
  ChamferSize = 0
  Closed = false
  End = (-7,10365,6040)
  FilletRadius = 0
  Length = 1703.35
  MakeFace = true
  Placement = pos=(0,8310,0) rot=(0,0,1;0rad)
  Points = (2) [(-997.708,710,6373),(-7,2055,6040)]
  Start = (-997.708,9020,6373)
FEATURE [Part::Part2DObjectPython] Line399  # Draft 2D object (typed FeaturePython)
  ChamferSize = 0
  Closed = false
  End = (-7,15905,6040)
  FilletRadius = 0
  Length = 1703.35
  MakeFace = true
  Placement = pos=(0,13850,0) rot=(0,0,1;0rad)
  Points = (2) [(-997.708,710,6373),(-7,2055,6040)]
  Start = (-997.708,14560,6373)
FEATURE [Part::Part2DObjectPython] Line400  # Draft 2D object (typed FeaturePython)
  ChamferSize = 0
  Closed = false
  End = (1368.2,14560,6580.22)
  FilletRadius = 0
  Length = 1998.01
  MakeFace = true
  Placement = pos=(0,13850,0) rot=(0,0,1;0rad)
  Points = (2) [(-7,2055,6040),(1368.2,710,6580.22)]
  Start = (-7,15905,6040)
FEATURE [Part::Part2DObjectPython] Line401  # Draft 2D object (typed FeaturePython)
  ChamferSize = 0
  Closed = false
  End = (2743,15905,6040)
  FilletRadius = 0
  Length = 1997.89
  MakeFace = true
  Placement = pos=(0,13850,0) rot=(0,0,1;0rad)
  Points = (2) [(1368,710,6580.3),(2743,2055,6040)]
  Start = (1368,14560,6580.3)
FEATURE [Part::Part2DObjectPython] Line402  # Draft 2D object (typed FeaturePython)
  ChamferSize = 0
  Closed = false
  End = (4118,14560,6820.74)
  FilletRadius = 0
  Length = 2075.86
  MakeFace = true
  Placement = pos=(0,13850,0) rot=(0,0,1;0rad)
  Points = (2) [(2743,2055,6040),(4118,710,6820.74)]
  Start = (2743,15905,6040)
FEATURE [Part::Part2DObjectPython] Line403  # Draft 2D object (typed FeaturePython)
  ChamferSize = 0
  Closed = false
  End = (5493,15905,6040)
  FilletRadius = 0
  Length = 2075.86
  MakeFace = true
  Placement = pos=(0,13850,0) rot=(0,0,1;0rad)
  Points = (2) [(4118,710,6820.74),(5493,2055,6040)]
  Start = (4118,14560,6820.74)
FEATURE [Part::Part2DObjectPython] Line404  # Draft 2D object (typed FeaturePython)
  ChamferSize = 0
  Closed = false
  End = (6868,14560,7061.16)
  FilletRadius = 0
  Length = 2177.71
  MakeFace = true
  Placement = pos=(0,13850,0) rot=(0,0,1;0rad)
  Points = (2) [(5493,2055,6040),(6868,710,7061.16)]
  Start = (5493,15905,6040)
FEATURE [Part::Part2DObjectPython] Line405  # Draft 2D object (typed FeaturePython)
  ChamferSize = 0
  Closed = false
  End = (8243,15905,6040)
  FilletRadius = 0
  Length = 2177.71
  MakeFace = true
  Placement = pos=(0,13850,0) rot=(0,0,1;0rad)
  Points = (2) [(6868,710,7061.16),(8243,2055,6040)]
  Start = (6868,14560,7061.16)
FEATURE [Part::Part2DObjectPython] Line406  # Draft 2D object (typed FeaturePython)
  ChamferSize = 0
  Closed = false
  End = (9618,14560,7301.44)
  FilletRadius = 0
  Length = 2300.19
  MakeFace = true
  Placement = pos=(0,13850,0) rot=(0,0,1;0rad)
  Points = (2) [(8243,2055,6040),(9618,710,7301.44)]
  Start = (8243,15905,6040)
FEATURE [Part::Part2DObjectPython] Line407  # Draft 2D object (typed FeaturePython)
  ChamferSize = 0
  Closed = false
  End = (10993,15905,6040)
  FilletRadius = 0
  Length = 2300.19
  MakeFace = true
  Placement = pos=(0,13850,0) rot=(0,0,1;0rad)
  Points = (2) [(9618,710,7301.44),(10993,2055,6040)]
  Start = (9618,14560,7301.44)
FEATURE [Part::Part2DObjectPython] Line408  # Draft 2D object (typed FeaturePython)
  ChamferSize = 0
  Closed = false
  End = (12878,14560,7588.33)
  FilletRadius = 0
  Length = 2785.6
  MakeFace = true
  Placement = pos=(0,13850,0) rot=(0,0,1;0rad)
  Points = (2) [(10993,2055,6040),(12878,710,7588.33)]
  Start = (10993,15905,6040)
FEATURE [Part::Part2DObjectPython] Line409  # Draft 2D object (typed FeaturePython)
  ChamferSize = 0
  Closed = false
  End = (-997.913,14520,6373.08)
  FilletRadius = 0
  Length = 1703.49
  MakeFace = true
  Placement = pos=(0,11120,0) rot=(0,0,1;0rad)
  Points = (2) [(-7,2055,6040),(-997.913,3400,6373.08)]
  Start = (-7,13175,6040)
FEATURE [Part::Part2DObjectPython] Line410  # Draft 2D object (typed FeaturePython)
  ChamferSize = 0
  Closed = false
  End = (1367.8,14520,6580.38)
  FilletRadius = 0
  Length = 1997.77
  MakeFace = true
  Placement = pos=(0,11120,0) rot=(0,0,1;0rad)
  Points = (2) [(-7,2055,6040),(1367.8,3400,6580.38)]
  Start = (-7,13175,6040)
FEATURE [Part::Part2DObjectPython] Line411  # Draft 2D object (typed FeaturePython)
  ChamferSize = 0
  Closed = false
  End = (2743,13175,6040)
  FilletRadius = 0
  Length = 1998.05
  MakeFace = true
  Placement = pos=(0,11120,0) rot=(0,0,1;0rad)
  Points = (2) [(1367.8,3400,6580.38),(2743,2055,6040)]
  Start = (1367.8,14520,6580.38)
FEATURE [Part::Part2DObjectPython] Line412  # Draft 2D object (typed FeaturePython)
  ChamferSize = 0
  Closed = false
  End = (4117.8,14520,6820.82)
  FilletRadius = 0
  Length = 2075.76
  MakeFace = true
  Placement = pos=(0,11120,0) rot=(0,0,1;0rad)
  Points = (2) [(2743,2055,6040),(4117.8,3400,6820.82)]
  Start = (2743,13175,6040)
FEATURE [Part::Part2DObjectPython] Line413  # Draft 2D object (typed FeaturePython)
  ChamferSize = 0
  Closed = false
  End = (5493,13175,6040)
  FilletRadius = 0
  Length = 2076.03
  MakeFace = true
  Placement = pos=(0,11120,0) rot=(0,0,1;0rad)
  Points = (2) [(4117.8,3400,6820.82),(5493,2055,6040)]
  Start = (4117.8,14520,6820.82)
FEATURE [Part::Part2DObjectPython] Line414  # Draft 2D object (typed FeaturePython)
  ChamferSize = 0
  Closed = false
  End = (6867.8,14520,7061.24)
  FilletRadius = 0
  Length = 2177.62
  MakeFace = true
  Placement = pos=(0,11120,0) rot=(0,0,1;0rad)
  Points = (2) [(5493,2055,6040),(6867.8,3400,7061.24)]
  Start = (5493,13175,6040)
FEATURE [Part::Part2DObjectPython] Line415  # Draft 2D object (typed FeaturePython)
  ChamferSize = 0
  Closed = false
  End = (8243,13175,6040)
  FilletRadius = 0
  Length = 2177.88
  MakeFace = true
  Placement = pos=(0,11120,0) rot=(0,0,1;0rad)
  Points = (2) [(6867.8,3400,7061.24),(8243,2055,6040)]
  Start = (6867.8,14520,7061.24)
FEATURE [Part::Part2DObjectPython] Line416  # Draft 2D object (typed FeaturePython)
  ChamferSize = 0
  Closed = false
  End = (9617.8,14520,7301.52)
  FilletRadius = 0
  Length = 2300.11
  MakeFace = true
  Placement = pos=(0,11120,0) rot=(0,0,1;0rad)
  Points = (2) [(8243,2055,6040),(9617.8,3400,7301.52)]
  Start = (8243,13175,6040)
FEATURE [Part::Part2DObjectPython] Line417  # Draft 2D object (typed FeaturePython)
  ChamferSize = 0
  Closed = false
  End = (10993,13175,6040)
  FilletRadius = 0
  Length = 2300.36
  MakeFace = true
  Placement = pos=(0,11120,0) rot=(0,0,1;0rad)
  Points = (2) [(9617.8,3400,7301.52),(10993,2055,6040)]
  Start = (9617.8,14520,7301.52)
FEATURE [Part::Part2DObjectPython] Line418  # Draft 2D object (typed FeaturePython)
  ChamferSize = 0
  Closed = false
  End = (12877.8,14520,7588.41)
  FilletRadius = 0
  Length = 2785.51
  MakeFace = true
  Placement = pos=(0,11120,0) rot=(0,0,1;0rad)
  Points = (2) [(10993,2055,6040),(12877.8,3400,7588.41)]
  Start = (10993,13175,6040)
FEATURE [Part::Part2DObjectPython] Line419  # Draft 2D object (typed FeaturePython)
  ChamferSize = 0
  Closed = false
  End = (12878,11790,7588.33)
  FilletRadius = 0
  Length = 2785.6
  MakeFace = true
  Placement = pos=(0,11080,0) rot=(0,0,1;0rad)
  Points = (2) [(10993,2055,6040),(12878,710,7588.33)]
  Start = (10993,13135,6040)
FEATURE [Part::Part2DObjectPython] Line420  # Draft 2D object (typed FeaturePython)
  ChamferSize = 0
  Closed = false
  End = (10993,13135,6040)
  FilletRadius = 0
  Length = 2300.19
  MakeFace = true
  Placement = pos=(0,11080,0) rot=(0,0,1;0rad)
  Points = (2) [(9618,710,7301.44),(10993,2055,6040)]
  Start = (9618,11790,7301.44)
FEATURE [Part::Part2DObjectPython] Line421  # Draft 2D object (typed FeaturePython)
  ChamferSize = 0
  Closed = false
  End = (9618,11790,7301.44)
  FilletRadius = 0
  Length = 2300.19
  MakeFace = true
  Placement = pos=(0,11080,0) rot=(0,0,1;0rad)
  Points = (2) [(8243,2055,6040),(9618,710,7301.44)]
  Start = (8243,13135,6040)
FEATURE [Part::Part2DObjectPython] Line422  # Draft 2D object (typed FeaturePython)
  ChamferSize = 0
  Closed = false
  End = (8243,13135,6040)
  FilletRadius = 0
  Length = 2177.71
  MakeFace = true
  Placement = pos=(0,11080,0) rot=(0,0,1;0rad)
  Points = (2) [(6868,710,7061.16),(8243,2055,6040)]
  Start = (6868,11790,7061.16)
FEATURE [Part::Part2DObjectPython] Line423  # Draft 2D object (typed FeaturePython)
  ChamferSize = 0
  Closed = false
  End = (6868,11790,7061.16)
  FilletRadius = 0
  Length = 2177.71
  MakeFace = true
  Placement = pos=(0,11080,0) rot=(0,0,1;0rad)
  Points = (2) [(5493,2055,6040),(6868,710,7061.16)]
  Start = (5493,13135,6040)
FEATURE [Part::Part2DObjectPython] Line424  # Draft 2D object (typed FeaturePython)
  ChamferSize = 0
  Closed = false
  End = (5493,13135,6040)
  FilletRadius = 0
  Length = 2075.86
  MakeFace = true
  Placement = pos=(0,11080,0) rot=(0,0,1;0rad)
  Points = (2) [(4118,710,6820.74),(5493,2055,6040)]
  Start = (4118,11790,6820.74)
FEATURE [Part::Part2DObjectPython] Line425  # Draft 2D object (typed FeaturePython)
  ChamferSize = 0
  Closed = false
  End = (4118,11790,6820.74)
  FilletRadius = 0
  Length = 2075.86
  MakeFace = true
  Placement = pos=(0,11080,0) rot=(0,0,1;0rad)
  Points = (2) [(2743,2055,6040),(4118,710,6820.74)]
  Start = (2743,13135,6040)
FEATURE [Part::Part2DObjectPython] Line426  # Draft 2D object (typed FeaturePython)
  ChamferSize = 0
  Closed = false
  End = (2743,13135,6040)
  FilletRadius = 0
  Length = 1997.89
  MakeFace = true
  Placement = pos=(0,11080,0) rot=(0,0,1;0rad)
  Points = (2) [(1368,710,6580.3),(2743,2055,6040)]
  Start = (1368,11790,6580.3)
FEATURE [Part::Part2DObjectPython] Line427  # Draft 2D object (typed FeaturePython)
  ChamferSize = 0
  Closed = false
  End = (1368.2,11790,6580.22)
  FilletRadius = 0
  Length = 1998.01
  MakeFace = true
  Placement = pos=(0,11080,0) rot=(0,0,1;0rad)
  Points = (2) [(-7,2055,6040),(1368.2,710,6580.22)]
  Start = (-7,13135,6040)
FEATURE [Part::Part2DObjectPython] Line428  # Draft 2D object (typed FeaturePython)
  ChamferSize = 0
  Closed = false
  End = (-7,13135,6040)
  FilletRadius = 0
  Length = 1703.35
  MakeFace = true
  Placement = pos=(0,11080,0) rot=(0,0,1;0rad)
  Points = (2) [(-997.708,710,6373),(-7,2055,6040)]
  Start = (-997.708,11790,6373)
FEATURE [Part::Part2DObjectPython] Line429  # Draft 2D object (typed FeaturePython)
  ChamferSize = 0
  Closed = false
  End = (-7,15945,6040)
  FilletRadius = 0
  Length = 1402.36
  MakeFace = true
  Points = (2) [(-997.708,16880,6373),(-7,15945,6040)]
  Start = (-997.708,16880,6373)
FEATURE [Part::Part2DObjectPython] Line430  # Draft 2D object (typed FeaturePython)
  ChamferSize = 0
  Closed = false
  End = (1368,16880,6580.3)
  FilletRadius = 0
  Length = 1748.36
  MakeFace = true
  Points = (2) [(-7,15945,6040),(1368,16880,6580.3)]
  Start = (-7,15945,6040)
FEATURE [Part::Part2DObjectPython] Line431  # Draft 2D object (typed FeaturePython)
  ChamferSize = 0
  Closed = false
  End = (2743,15945,6040)
  FilletRadius = 0
  Length = 1748.36
  MakeFace = true
  Points = (2) [(1368,16880,6580.3),(2743,15945,6040)]
  Start = (1368,16880,6580.3)
FEATURE [Part::Part2DObjectPython] Line432  # Draft 2D object (typed FeaturePython)
  ChamferSize = 0
  Closed = false
  End = (4118,16880,6820.74)
  FilletRadius = 0
  Length = 1836.95
  MakeFace = true
  Points = (2) [(2743,15945,6040),(4118,16880,6820.74)]
  Start = (2743,15945,6040)
FEATURE [Part::Part2DObjectPython] Line433  # Draft 2D object (typed FeaturePython)
  ChamferSize = 0
  Closed = false
  End = (5493,15945,6040)
  FilletRadius = 0
  Length = 1836.95
  MakeFace = true
  Points = (2) [(4118,16880,6820.74),(5493,15945,6040)]
  Start = (4118,16880,6820.74)
FEATURE [Part::Part2DObjectPython] Line434  # Draft 2D object (typed FeaturePython)
  ChamferSize = 0
  Closed = false
  End = (6868,16880,7061.16)
  FilletRadius = 0
  Length = 1951.31
  MakeFace = true
  Points = (2) [(5493,15945,6040),(6868,16880,7061.16)]
  Start = (5493,15945,6040)
FEATURE [Part::Part2DObjectPython] Line435  # Draft 2D object (typed FeaturePython)
  ChamferSize = 0
  Closed = false
  End = (8243,15945,6040)
  FilletRadius = 0
  Length = 1951.31
  MakeFace = true
  Points = (2) [(6868,16880,7061.16),(8243,15945,6040)]
  Start = (6868,16880,7061.16)
FEATURE [Part::Part2DObjectPython] Line436  # Draft 2D object (typed FeaturePython)
  ChamferSize = 0
  Closed = false
  End = (9618,16880,7301.44)
  FilletRadius = 0
  Length = 2087.12
  MakeFace = true
  Points = (2) [(8243,15945,6040),(9618,16880,7301.44)]
  Start = (8243,15945,6040)
FEATURE [Part::Part2DObjectPython] Line437  # Draft 2D object (typed FeaturePython)
  ChamferSize = 0
  Closed = false
  End = (10993,15945,6040)
  FilletRadius = 0
  Length = 2087.12
  MakeFace = true
  Points = (2) [(9618,16880,7301.44),(10993,15945,6040)]
  Start = (9618,16880,7301.44)
FEATURE [Part::Part2DObjectPython] Line438  # Draft 2D object (typed FeaturePython)
  ChamferSize = 0
  Closed = false
  End = (12878,16880,7588.33)
  FilletRadius = 0
  Length = 2612.43
  MakeFace = true
  Points = (2) [(10993,15945,6040),(12878,16880,7588.33)]
  Start = (10993,15945,6040)
FEATURE [Part::Part2DObjectPython] DWire004  # Draft 2D object (typed FeaturePython)
  ChamferSize = 0
  Closed = false
  End = (12878,16880,7588.33)
  FilletRadius = 0
  Length = 16759
  MakeFace = true
  Placement = pos=(0,14825,-2617.17) rot=(0,0,1;0rad)
  Points = (11) [(-997.708,2055,8990.16),(-7,2055,8657.17),(1368,2055,9197.47),(2743,2055,8657.17),(4118,2055,9437.91),(5493,2055,8657.17),(6868,2055,9678.33),+4 more]
  Start = (-997.708,16880,6373)
FEATURE [Part::Part2DObjectPython] DWire003  # Draft 2D object (typed FeaturePython)
  ChamferSize = 0
  Closed = false
  End = (12878,2055,7588.33)
  FilletRadius = 0
  Length = 16759
  MakeFace = true
  Placement = pos=(0,-0.000155996,-2617.17) rot=(0,0,1;0rad)
  Points = (11) [(-997.708,2055,8990.16),(-7,2055,8657.17),(1368,2055,9197.47),(2743,2055,8657.17),(4118,2055,9437.91),(5493,2055,8657.17),(6868,2055,9678.33),+4 more]
  Start = (-997.708,2055,6373)
FEATURE [Part::Part2DObjectPython] Circle  # Draft 2D object (typed FeaturePython)
  FirstAngle = 0
  LastAngle = 0
  MakeFace = true
  Placement = pos=(12949,710,7588.33) rot=(0,1,0;1.5708rad)
  Radius = 15
FEATURE [Part::Part2DObjectPython] DWire017  # Draft 2D object (typed FeaturePython)
  ChamferSize = 0
  Closed = false
  End = (-997.708,710,6373)
  FilletRadius = 40
  Length = 21431.7
  MakeFace = true
  Points = (12) [(12949,710,7588.33),(12878,710,7588.33),(10993,2055,6040),(9618,710,7301.44),(8243,2055,6040),(6868,710,7061.16),(5493,2055,6040),(4118,710,6820.74),+4 more]
  Start = (12949,710,7588.33)
FEATURE [Part::Part2DObjectPython] DWire018  # Draft 2D object (typed FeaturePython)
  ChamferSize = 0
  Closed = false
  End = (12949,3440,7588.33)
  FilletRadius = 40
  Length = 21432.2
  MakeFace = true
  Points = (12) [(-997.913,3440,6373.08),(-7,2095,6040),(1367.8,3440,6580.38),(2743,2095,6040),(4117.8,3440,6820.82),(5493,2095,6040),(6867.8,3440,7061.24),+5 more]
  Start = (-997.913,3440,6373.08)
FEATURE [Part::Part2DObjectPython] DWire019  # Draft 2D object (typed FeaturePython)
  ChamferSize = 0
  Closed = false
  End = (12949,3480,7588.33)
  FilletRadius = 40
  Length = 21431.6
  MakeFace = true
  Points = (12) [(-997.708,3480,6373),(-7,4825,6040),(1368.2,3480,6580.22),(2743,4825,6040),(4118,3480,6820.74),(5493,4825,6040),(6868,3480,7061.16),(8243,4825,6040),+4 more]
  Start = (-997.708,3480,6373)
FEATURE [Part::Part2DObjectPython] DWire020  # Draft 2D object (typed FeaturePython)
  ChamferSize = 0
  Closed = false
  End = (12949,6210,7588.33)
  FilletRadius = 40
  Length = 21432.2
  MakeFace = true
  Points = (12) [(-997.913,6210,6373.08),(-7,4865,6040),(1367.8,6210,6580.38),(2743,4865,6040),(4117.8,6210,6820.82),(5493,4865,6040),(6867.8,6210,7061.24),+5 more]
  Start = (-997.913,6210,6373.08)
FEATURE [Part::Part2DObjectPython] DWire021  # Draft 2D object (typed FeaturePython)
  ChamferSize = 0
  Closed = false
  End = (12949,6250,7588.33)
  FilletRadius = 40
  Length = 21431.7
  MakeFace = true
  Points = (12) [(-997.708,6250,6373),(-7,7595,6040),(1368,6250,6580.3),(2743,7595,6040),(4118,6250,6820.74),(5493,7595,6040),(6868,6250,7061.16),(8243,7595,6040),+4 more]
  Start = (-997.708,6250,6373)
FEATURE [Part::Part2DObjectPython] DWire022  # Draft 2D object (typed FeaturePython)
  ChamferSize = 0
  Closed = false
  End = (12949,8980,7588.33)
  FilletRadius = 40
  Length = 21432.2
  MakeFace = true
  Points = (13) [(-997.913,8980,6373.08),(-7,7635,6040),(1367.8,8980,6580.38),(2743,7635,6040),(4117.8,8980,6820.82),(5493,7635,6040),(6867.8,8980,7061.24),+6 more]
  Start = (-997.913,8980,6373.08)
FEATURE [Part::Part2DObjectPython] DWire023  # Draft 2D object (typed FeaturePython)
  ChamferSize = 0
  Closed = false
  End = (12949,9020,7588.33)
  FilletRadius = 40
  Length = 21431.7
  MakeFace = true
  Points = (12) [(-997.708,9020,6373),(-7,10365,6040),(1368,9020,6580.3),(2743,10365,6040),(4118,9020,6820.74),(5493,10365,6040),(6868,9020,7061.16),(8243,10365,6040),+4 more]
  Start = (-997.708,9020,6373)
FEATURE [Part::Part2DObjectPython] DWire024  # Draft 2D object (typed FeaturePython)
  ChamferSize = 0
  Closed = false
  End = (12949,11750,7588.33)
  FilletRadius = 40
  Length = 21432.2
  MakeFace = true
  Points = (12) [(-997.913,11750,6373.08),(-7,10405,6040),(1367.8,11750,6580.38),(2743,10405,6040),(4117.8,11750,6820.82),(5493,10405,6040),(6867.8,11750,7061.24),+5 more]
  Start = (-997.913,11750,6373.08)
FEATURE [Part::Part2DObjectPython] DWire025  # Draft 2D object (typed FeaturePython)
  ChamferSize = 0
  Closed = false
  End = (12949,11790,7588.33)
  FilletRadius = 40
  Length = 21431.6
  MakeFace = true
  Points = (12) [(-997.708,11790,6373),(-7,13135,6040),(1368.2,11790,6580.22),(2743,13135,6040),(4118,11790,6820.74),(5493,13135,6040),(6868,11790,7061.16),+5 more]
  Start = (-997.708,11790,6373)
FEATURE [Part::Part2DObjectPython] DWire026  # Draft 2D object (typed FeaturePython)
  ChamferSize = 0
  Closed = false
  End = (12949,14520,7588.33)
  FilletRadius = 40
  Length = 21432.2
  MakeFace = true
  Points = (12) [(-997.913,14520,6373.08),(-7,13175,6040),(1367.8,14520,6580.38),(2743,13175,6040),(4117.8,14520,6820.82),(5493,13175,6040),(6867.8,14520,7061.24),+5 more]
  Start = (-997.913,14520,6373.08)
FEATURE [Part::Part2DObjectPython] DWire027  # Draft 2D object (typed FeaturePython)
  ChamferSize = 0
  Closed = false
  End = (12949,14560,7588.33)
  FilletRadius = 40
  Length = 21431.6
  MakeFace = true
  Points = (12) [(-997.708,14560,6373),(-7,15905,6040),(1368.2,14560,6580.22),(2743,15905,6040),(4118,14560,6820.74),(5493,15905,6040),(6868,14560,7061.16),+5 more]
  Start = (-997.708,14560,6373)
FEATURE [Part::Part2DObjectPython] DWire028  # Draft 2D object (typed FeaturePython)
  ChamferSize = 0
  Closed = false
  End = (12949,16880,7588.33)
  FilletRadius = 40
  Length = 19191.1
  MakeFace = true
  Points = (12) [(-997.708,16880,6373),(-7,15945,6040),(1368,16880,6580.3),(2743,15945,6040),(4118,16880,6820.74),(5493,15945,6040),(6868,16880,7061.16),+5 more]
  Start = (-997.708,16880,6373)
FEATURE [App::DocumentObjectGroup] Group006  label="sketches"
  Group = -> [DWire003,DWire004,Line309,Line310,Line311,Line312,Line313,Line314,Line315,Line316,Line317,Line318,Line319,Line320,Line321,Line322,Line323,Line324,Line325,Line326,Line327,Line328,Line329,Line330,Line331,Line332,Line333,Line334,Line335,Line336,Line337,Line338,Line339,Line340,Line341,Line342,Line343,Line344,Line345,Line346,Line347,Line348,Line349,Line350,Line351,Line352,Line353,Line354,Line355,+86 more]
FEATURE [Part::FeaturePython] Clone009  label="Clone of Sweep"  # WARN: FeaturePython — macro-defined, semantics opaque (R4)
  Placement = pos=(0,2770,0) rot=(0,0,1;0rad)
  Scale = (1,1,1)
FEATURE [Part::FeaturePython] Clone010  label="Clone of Sweep001"  # WARN: FeaturePython — macro-defined, semantics opaque (R4)
  Placement = pos=(0,5540,0) rot=(0,0,1;0rad)
  Scale = (1,1,1)
FEATURE [Part::FeaturePython] Clone011  label="Clone of Sweep002"  # WARN: FeaturePython — macro-defined, semantics opaque (R4)
  Placement = pos=(0,8310,0) rot=(0,0,1;0rad)
  Scale = (1,1,1)
FEATURE [Part::FeaturePython] Clone012  label="Clone of Sweep003"  # WARN: FeaturePython — macro-defined, semantics opaque (R4)
  Placement = pos=(0.0002732,11080,-1.114e-05) rot=(0,0,1;0rad)
  Scale = (1,1,1)
FEATURE [Part::FeaturePython] Clone013  label="Clone of Sweep004"  # WARN: FeaturePython — macro-defined, semantics opaque (R4)
  Placement = pos=(0.000273225,13850,-1.11425e-05) rot=(0,0,1;0rad)
  Scale = (1,1,1)
FEATURE [Part::FeaturePython] Clone014  label="Clone of Sweep005"  # WARN: FeaturePython — macro-defined, semantics opaque (R4)
  Scale = (1,1,1)
FEATURE [Part::FeaturePython] Clone015  label="Clone of Clone of Sweep005 (Mirror #1)"  # WARN: FeaturePython — macro-defined, semantics opaque (R4)
  Placement = pos=(-0.0002732,6920,1.114e-05) rot=(0,0,1;0rad)
  Scale = (1,1,1)
FEATURE [Part::FeaturePython] Clone016  label="Clone of Clone of Sweep005 (Mirror #1)001"  # WARN: FeaturePython — macro-defined, semantics opaque (R4)
  Placement = pos=(-0.0002732,9690,1.114e-05) rot=(0,0,1;0rad)
  Scale = (1,1,1)
FEATURE [Part::FeaturePython] Clone017  label="Clone of Clone of Sweep005 (Mirror #1)002"  # WARN: FeaturePython — macro-defined, semantics opaque (R4)
  Placement = pos=(0,12460,-3e-12) rot=(0,0,1;0rad)
  Scale = (1,1,1)
FEATURE [Part::FeaturePython] Clone018  label="Clone of Clone of Sweep005 (Mirror #1)003"  # WARN: FeaturePython — macro-defined, semantics opaque (R4)
  Placement = pos=(2.5e-08,15230,-2.503e-09) rot=(0,0,1;0rad)
  Scale = (1,1,1)
FEATURE [Part::Part2DObjectPython] Clone2D  label="Clone of Circle (2D)"  # Draft 2D object (typed FeaturePython)
  Objects = -> [Circle]
  Placement = pos=(12949,16880,7588.33) rot=(0,1,0;1.5708rad)
  Scale = (1,1,1)
FEATURE [App::DocumentObjectGroup] Group012  label="Closet panels"
  Group = -> [Panel,Panel001,Panel002,Panel003,Panel008,Panel009,Panel010,Panel011,Panel012,Panel013,Panel014,Panel015,Panel016,Panel017,Panel018,Panel020,Panel021,Panel022,Panel023,Panel024,Panel025,Panel027,Panel029,Panel030,Panel031,Panel033,Panel034,Panel035,Panel036,Panel037]
FEATURE [Part::Part2DObjectPython] Rectangle032  # Draft 2D object (typed FeaturePython)
  ChamferSize = 0
  FilletRadius = 0
  Height = 490
  Length = 150
  MakeFace = true
  Placement = pos=(4595,8250,2310) rot=(0.57735,0.57735,0.57735;2.0944rad)
FEATURE [Part::Part2DObjectPython] Rectangle033  # Draft 2D object (typed FeaturePython)
  ChamferSize = 0
  FilletRadius = 0
  Height = 490
  Length = 150
  MakeFace = true
  Placement = pos=(5945,8250,2310) rot=(0.57735,0.57735,0.57735;2.0944rad)
FEATURE [Part::Part2DObjectPython] Rectangle034  # Draft 2D object (typed FeaturePython)
  ChamferSize = 0
  FilletRadius = 0
  Height = 490
  Length = 150
  MakeFace = true
  Placement = pos=(5945,5900,2310) rot=(0.57735,0.57735,0.57735;2.0944rad)
FEATURE [Part::FeaturePython] Structure034  # WARN: FeaturePython — macro-defined, semantics opaque (R4)
  Base = -> Rectangle034
  Height = 4900
  Length = 0
  MoveWithHost = false
  Nodes = (2) [(5945,5975,2555),(5945,5975,7455)]
  Normal = (0,0,0)
  Role = 0
  Width = 100
FEATURE [Part::FeaturePython] Structure035  # WARN: FeaturePython — macro-defined, semantics opaque (R4)
  Base = -> Rectangle033
  Height = 4900
  Length = 0
  MoveWithHost = false
  Nodes = (2) [(5945,8325,2555),(5945,8325,7455)]
  Normal = (0,0,0)
  Role = 0
  Width = 100
FEATURE [Part::FeaturePython] Structure036  # WARN: FeaturePython — macro-defined, semantics opaque (R4)
  Base = -> Rectangle032
  Height = 1200
  Length = 0
  MoveWithHost = false
  Nodes = (2) [(4595,8325,2555),(4595,8325,3755)]
  Normal = (0,0,0)
  Role = 0
  Width = 100
FEATURE [Part::Part2DObjectPython] Rectangle036  # Draft 2D object (typed FeaturePython)
  ChamferSize = 0
  FilletRadius = 0
  Height = 490
  Length = 150
  MakeFace = true
  Placement = pos=(5945,2000,5310) rot=(0.57735,0.57735,0.57735;2.0944rad)
FEATURE [Part::FeaturePython] Structure037  # WARN: FeaturePython — macro-defined, semantics opaque (R4)
  Base = -> Rectangle036
  Height = 4900
  Length = 0
  MoveWithHost = false
  Nodes = (2) [(5945,2075,5555),(5945,2075,10455)]
  Normal = (0,0,0)
  Role = 0
  Width = 100
FEATURE [Part::Part2DObjectPython] Rectangle037  # Draft 2D object (typed FeaturePython)
  ChamferSize = 0
  FilletRadius = 0
  Height = 450
  Length = 150
  MakeFace = true
  Placement = pos=(10845,5750,5350) rot=(1,0,0;1.5708rad)
  Support = -> Structure019
FEATURE [Part::FeaturePython] Structure038  # WARN: FeaturePython — macro-defined, semantics opaque (R4)
  Base = -> Rectangle037
  Height = 3600
  Length = 0
  MoveWithHost = false
  Nodes = (2) [(10920,5750,5575),(10920,5750,9175)]
  Normal = (0,0,0)
  Role = 0
  Width = 100
FEATURE [App::DocumentObjectGroup] Group014  label="A-Beams"
  Group = -> [Structure034,Structure035,Structure036,Structure037,Structure038]
FEATURE [Part::Part2DObjectPython] Line440  # Draft 2D object (typed FeaturePython)
  ChamferSize = 0
  Closed = false
  End = (7480,-10063.7,0.0001461)
  FilletRadius = 0
  Length = 4249
  MakeFace = true
  Placement = pos=(-5015,0.305262,0.0001461) rot=(0,0,1;0rad)
  Points = (2) [(12495,-5815,0),(12495,-10064,0)]
  Start = (7480,-5814.69,0.0001461)
FEATURE [Part::Part2DObjectPython] Line441  # Draft 2D object (typed FeaturePython)
  ChamferSize = 0
  Closed = false
  End = (7180,-10063.7,0.0001461)
  FilletRadius = 0
  Length = 4249
  MakeFace = true
  Placement = pos=(-5015,0.305262,0.0001461) rot=(0,0,1;0rad)
  Points = (2) [(12195,-5815,0),(12195,-10064,0)]
  Start = (7180,-5814.69,0.0001461)
FEATURE [Part::Part2DObjectPython] Line442  # Draft 2D object (typed FeaturePython)
  ChamferSize = 0
  Closed = false
  End = (5180,-10063.7,0.0001461)
  FilletRadius = 0
  Length = 4249
  MakeFace = true
  Placement = pos=(-5015,0.305262,0.0001461) rot=(0,0,1;0rad)
  Points = (2) [(10195,-5815,0),(10195,-10064,0)]
  Start = (5180,-5814.69,0.0001461)
FEATURE [Part::Part2DObjectPython] Line443  # Draft 2D object (typed FeaturePython)
  ChamferSize = 0
  Closed = false
  End = (4880,-10063.7,0.0001461)
  FilletRadius = 0
  Length = 4249
  MakeFace = true
  Placement = pos=(-7315,0.305262,0.0001461) rot=(0,0,1;0rad)
  Points = (2) [(12195,-5815,0),(12195,-10064,0)]
  Start = (4880,-5814.69,0.0001461)
FEATURE [Part::Part2DObjectPython] Line444  # Draft 2D object (typed FeaturePython)
  ChamferSize = 0
  Closed = false
  End = (12880,-10063.7,0.0001461)
  FilletRadius = 0
  Length = 4249
  MakeFace = true
  Placement = pos=(-4915,0.305262,0.0001461) rot=(0,0,1;0rad)
  Points = (2) [(17795,-5815,0),(17795,-10064,0)]
  Start = (12880,-5814.69,0.0001461)
FEATURE [Part::Part2DObjectPython] Line445  # Draft 2D object (typed FeaturePython)
  ChamferSize = 0
  Closed = false
  End = (12580,-10063.7,0.0001461)
  FilletRadius = 0
  Length = 4249
  MakeFace = true
  Placement = pos=(385.002,0.305262,0.0001461) rot=(0,0,1;0rad)
  Points = (2) [(12195,-5815,0),(12195,-10064,0)]
  Start = (12580,-5814.69,0.0001461)
FEATURE [App::FeaturePython] Dimension023  # Draft dimension (typed FeaturePython)
  Dimline = (3060,-11168.7,0.0001461)
  Direction = (0,0,0)
  Distance = 11700
  End = (4880,-10063.7,0.0001461)
  Normal = (0,0,1)
  Start = (-6820,-10063.7,0.0001461)
FEATURE [Part::Part2DObjectPython] Line448  # Draft 2D object (typed FeaturePython)
  ChamferSize = 0
  Closed = false
  End = (4880,-7939.19,0.0001461)
  FilletRadius = 0
  Length = 11700
  MakeFace = true
  Placement = pos=(-4915,0.305262,0.0001461) rot=(0,0,1;0rad)
  Points = (2) [(-1905,-7939.5,0),(9795,-7939.5,0)]
  Start = (-6820,-7939.19,0.0001461)
FEATURE [Part::Part2DObjectPython] Line449  # Draft 2D object (typed FeaturePython)
  ChamferSize = 0
  Closed = false
  End = (-4480,-10063.7,0.0001461)
  FilletRadius = 0
  Length = 4249
  MakeFace = true
  Placement = pos=(-4915,0.305262,0.0001461) rot=(0,0,1;0rad)
  Points = (2) [(435,-5815,0),(435,-10064,0)]
  Start = (-4480,-5814.69,0.0001461)
FEATURE [Part::Part2DObjectPython] Line450  # Draft 2D object (typed FeaturePython)
  ChamferSize = 0
  Closed = false
  End = (-2140,-10063.7,0.0001461)
  FilletRadius = 0
  Length = 4249
  MakeFace = true
  Placement = pos=(-2575,0.305262,0.0001461) rot=(0,0,1;0rad)
  Points = (2) [(435,-5815,0),(435,-10064,0)]
  Start = (-2140,-5814.69,0.0001461)
FEATURE [Part::Part2DObjectPython] Line451  # Draft 2D object (typed FeaturePython)
  ChamferSize = 0
  Closed = false
  End = (200.002,-10063.7,0.0001461)
  FilletRadius = 0
  Length = 4249
  MakeFace = true
  Placement = pos=(-234.998,0.305262,0.0001461) rot=(0,0,1;0rad)
  Points = (2) [(435,-5815,0),(435,-10064,0)]
  Start = (200.002,-5814.69,0.0001461)
FEATURE [Part::Part2DObjectPython] Line452  # Draft 2D object (typed FeaturePython)
  ChamferSize = 0
  Closed = false
  End = (2540,-10063.7,0.0001461)
  FilletRadius = 0
  Length = 4249
  MakeFace = true
  Placement = pos=(2105,0.305262,0.0001461) rot=(0,0,1;0rad)
  Points = (2) [(435,-5815,0),(435,-10064,0)]
  Start = (2540,-5814.69,0.0001461)
FEATURE [Part::Part2DObjectPython] Line453  # Draft 2D object (typed FeaturePython)
  ChamferSize = 0
  Closed = false
  End = (-7120,-10063.7,0.0001461)
  FilletRadius = 0
  Length = 300
  MakeFace = true
  Placement = pos=(-4915,0.305262,0.0001461) rot=(0,0,1;0rad)
  Points = (2) [(-1905,-10064,0),(-2205,-10064,0)]
  Start = (-6820,-10063.7,0.0001461)
FEATURE [Part::Part2DObjectPython] Line454  # Draft 2D object (typed FeaturePython)
  ChamferSize = 0
  Closed = false
  End = (-7120,-10063.7,0.0001461)
  FilletRadius = 0
  Length = 4249
  MakeFace = true
  Placement = pos=(-16825,0.305262,500) rot=(0,0,1;0rad)
  Points = (2) [(9705,-5815,-500),(9705,-10064,-500)]
  Start = (-7120,-5814.69,0.0001461)
FEATURE [Part::Part2DObjectPython] Line455  # Draft 2D object (typed FeaturePython)
  ChamferSize = 0
  Closed = false
  End = (-6820,-10063.7,0.0001461)
  FilletRadius = 0
  Length = 4249
  MakeFace = true
  Placement = pos=(-22125,0.305262,-500) rot=(0,0,1;0rad)
  Points = (2) [(15305,-5815,500),(15305,-10064,500)]
  Start = (-6820,-5814.69,0.0001461)
FEATURE [Part::Part2DObjectPython] Line456  # Draft 2D object (typed FeaturePython)
  ChamferSize = 0
  Closed = false
  End = (-4330,-10063.7,0.0001461)
  FilletRadius = 0
  Length = 4249
  MakeFace = true
  Placement = pos=(-19635,0.305262,-500) rot=(0,0,1;0rad)
  Points = (2) [(15305,-5815,500),(15305,-10064,500)]
  Start = (-4330,-5814.69,0.0001461)
FEATURE [Part::Part2DObjectPython] Line457  # Draft 2D object (typed FeaturePython)
  ChamferSize = 0
  Closed = false
  End = (-4630,-10063.7,0.0001461)
  FilletRadius = 0
  Length = 4249
  MakeFace = true
  Placement = pos=(-14335,0.305262,500) rot=(0,0,1;0rad)
  Points = (2) [(9705,-5815,-500),(9705,-10064,-500)]
  Start = (-4630,-5814.69,0.0001461)
FEATURE [Part::Part2DObjectPython] Line458  # Draft 2D object (typed FeaturePython)
  ChamferSize = 0
  Closed = false
  End = (-2290,-10063.7,0.0001461)
  FilletRadius = 0
  Length = 4249
  MakeFace = true
  Placement = pos=(-11995,0.305262,500) rot=(0,0,1;0rad)
  Points = (2) [(9705,-5815,-500),(9705,-10064,-500)]
  Start = (-2290,-5814.69,0.0001461)
FEATURE [Part::Part2DObjectPython] Line459  # Draft 2D object (typed FeaturePython)
  ChamferSize = 0
  Closed = false
  End = (-1990,-10063.7,0.0001461)
  FilletRadius = 0
  Length = 4249
  MakeFace = true
  Placement = pos=(-17295,0.305262,-500) rot=(0,0,1;0rad)
  Points = (2) [(15305,-5815,500),(15305,-10064,500)]
  Start = (-1990,-5814.69,0.0001461)
FEATURE [Part::Part2DObjectPython] Line460  # Draft 2D object (typed FeaturePython)
  ChamferSize = 0
  Closed = false
  End = (50.0022,-10063.7,0.0001461)
  FilletRadius = 0
  Length = 4249
  MakeFace = true
  Placement = pos=(-9655,0.305262,500) rot=(0,0,1;0rad)
  Points = (2) [(9705,-5815,-500),(9705,-10064,-500)]
  Start = (50.0022,-5814.69,0.0001461)
FEATURE [Part::Part2DObjectPython] Line461  # Draft 2D object (typed FeaturePython)
  ChamferSize = 0
  Closed = false
  End = (350.002,-10063.7,0.0001461)
  FilletRadius = 0
  Length = 4249
  MakeFace = true
  Placement = pos=(-14955,0.305262,-500) rot=(0,0,1;0rad)
  Points = (2) [(15305,-5815,500),(15305,-10064,500)]
  Start = (350.002,-5814.69,0.0001461)
FEATURE [Part::Part2DObjectPython] Line462  # Draft 2D object (typed FeaturePython)
  ChamferSize = 0
  Closed = false
  End = (2390,-10063.7,0.0001461)
  FilletRadius = 0
  Length = 4249
  MakeFace = true
  Placement = pos=(-7315,0.305262,500) rot=(0,0,1;0rad)
  Points = (2) [(9705,-5815,-500),(9705,-10064,-500)]
  Start = (2390,-5814.69,0.0001461)
FEATURE [Part::Part2DObjectPython] Line463  # Draft 2D object (typed FeaturePython)
  ChamferSize = 0
  Closed = false
  End = (2690,-10063.7,0.0001461)
  FilletRadius = 0
  Length = 4249
  MakeFace = true
  Placement = pos=(-12615,0.305262,-500) rot=(0,0,1;0rad)
  Points = (2) [(15305,-5815,500),(15305,-10064,500)]
  Start = (2690,-5814.69,0.0001461)
FEATURE [Part::Part2DObjectPython] Rectangle038  # Draft 2D object (typed FeaturePython)
  ChamferSize = 0
  FilletRadius = 0
  Height = 300
  Length = 300
  MakeFace = true
  Placement = pos=(17495,-5815,0) rot=(0,0,1;0rad)
FEATURE [Part::FeaturePython] Structure039  # WARN: FeaturePython — macro-defined, semantics opaque (R4)
  Base = -> Rectangle038
  Height = 3000
  Length = 0
  MoveWithHost = false
  Nodes = (2) [(17645,-5665,0),(17645,-5665,3000)]
  Normal = (0,0,0)
  Role = 0
  Width = 100
FEATURE [Part::FeaturePython] Clone019  label="Clone of Structure039"  # Draft clone (typed FeaturePython)
  Objects = -> [Structure039]
  Placement = pos=(-5400,0,0) rot=(0,0,1;0rad)
  Scale = (1,1,1)
FEATURE [Part::FeaturePython] Clone020  label="Clone of Structure040"  # Draft clone (typed FeaturePython)
  Objects = -> [Structure039]
  Placement = pos=(-7700,0,0) rot=(0,0,1;0rad)
  Scale = (1,1,1)
FEATURE [Part::FeaturePython] Clone021  label="Clone of Structure041"  # Draft clone (typed FeaturePython)
  Objects = -> [Structure039]
  Placement = pos=(-10190,0,0) rot=(0,0,1;0rad)
  Scale = (1,1,1)
FEATURE [Part::FeaturePython] Clone022  label="Clone of Structure042"  # Draft clone (typed FeaturePython)
  Objects = -> [Structure039]
  Placement = pos=(-12530,0,0) rot=(0,0,1;0rad)
  Scale = (1,1,1)
FEATURE [Part::FeaturePython] Clone023  label="Clone of Structure043"  # Draft clone (typed FeaturePython)
  Objects = -> [Structure039]
  Placement = pos=(-14870,0,0) rot=(0,0,1;0rad)
  Scale = (1,1,1)
FEATURE [Part::FeaturePython] Clone024  label="Clone of Structure044"  # Draft clone (typed FeaturePython)
  Objects = -> [Structure039]
  Placement = pos=(-17210,0,0) rot=(0,0,1;0rad)
  Scale = (1,1,1)
FEATURE [Part::FeaturePython] Clone025  label="Clone of Structure045"  # Draft clone (typed FeaturePython)
  Objects = -> [Structure039]
  Placement = pos=(-19700,0,0) rot=(0,0,1;0rad)
  Scale = (1,1,1)
FEATURE [Part::Part2DObjectPython] Line464  # Draft 2D object (typed FeaturePython)
  ChamferSize = 0
  Closed = false
  End = (285,-5815,0)
  FilletRadius = 0
  Length = 2190
  MakeFace = true
  Points = (2) [(-1905,-5815,0),(285,-5815,0)]
  Start = (-1905,-5815,0)
FEATURE [Part::Part2DObjectPython] Line465  # Draft 2D object (typed FeaturePython)
  ChamferSize = 0
  Closed = false
  End = (2625,-5815,0)
  FilletRadius = 0
  Length = 2040
  MakeFace = true
  Points = (2) [(585,-5815,0),(2625,-5815,0)]
  Start = (585,-5815,0)
FEATURE [Part::Part2DObjectPython] Line466  # Draft 2D object (typed FeaturePython)
  ChamferSize = 0
  Closed = false
  End = (4965,-5815,0)
  FilletRadius = 0
  Length = 2040
  MakeFace = true
  Points = (2) [(2925,-5815,0),(4965,-5815,0)]
  Start = (2925,-5815,0)
FEATURE [Part::Part2DObjectPython] Line467  # Draft 2D object (typed FeaturePython)
  ChamferSize = 0
  Closed = false
  End = (7305,-5815,0)
  FilletRadius = 0
  Length = 2040
  MakeFace = true
  Points = (2) [(5265,-5815,0),(7305,-5815,0)]
  Start = (5265,-5815,0)
FEATURE [Part::Part2DObjectPython] Line468  # Draft 2D object (typed FeaturePython)
  ChamferSize = 0
  Closed = false
  End = (9795,-5815,0)
  FilletRadius = 0
  Length = 2190
  MakeFace = true
  Points = (2) [(7605,-5815,0),(9795,-5815,0)]
  Start = (7605,-5815,0)
FEATURE [Part::FeaturePython] Wall086  # WARN: FeaturePython — macro-defined, semantics opaque (R4)
  Align = 1
  Base = -> Line464
  Face = 0
  Height = 1000
  Length = 0
  MoveWithHost = false
  Normal = (0,0,0)
  Role = 0
  Width = 200
FEATURE [Part::FeaturePython] Wall087  # WARN: FeaturePython — macro-defined, semantics opaque (R4)
  Align = 1
  Base = -> Line465
  Face = 0
  Height = 1000
  Length = 0
  MoveWithHost = false
  Normal = (0,0,0)
  Role = 0
  Width = 200
FEATURE [Part::FeaturePython] Wall088  # WARN: FeaturePython — macro-defined, semantics opaque (R4)
  Align = 1
  Base = -> Line466
  Face = 0
  Height = 1000
  Length = 0
  MoveWithHost = false
  Normal = (0,0,0)
  Role = 0
  Width = 200
FEATURE [Part::FeaturePython] Wall089  # WARN: FeaturePython — macro-defined, semantics opaque (R4)
  Align = 1
  Base = -> Line467
  Face = 0
  Height = 1000
  Length = 0
  MoveWithHost = false
  Normal = (0,0,0)
  Role = 0
  Width = 200
FEATURE [Part::FeaturePython] Wall090  # WARN: FeaturePython — macro-defined, semantics opaque (R4)
  Align = 1
  Base = -> Line468
  Face = 0
  Height = 1000
  Length = 0
  MoveWithHost = false
  Normal = (0,0,0)
  Role = 0
  Width = 200
FEATURE [Part::Part2DObjectPython] Arc015  # Draft 2D object (typed FeaturePython)
  FirstAngle = 0
  LastAngle = 90
  MakeFace = true
  Placement = pos=(12395,-5515,0) rot=(0,0,1;0rad)
  Radius = 2550
FEATURE [Part::Part2DObjectPython] Arc016  # Draft 2D object (typed FeaturePython)
  FirstAngle = 90
  LastAngle = 180
  MakeFace = true
  Placement = pos=(17495,-5515,0) rot=(0,0,1;0rad)
  Radius = 2550
FEATURE [Part::Part2DObjectPython] Line470  # Draft 2D object (typed FeaturePython)
  ChamferSize = 0
  Closed = false
  End = (12395,-5515,0)
  FilletRadius = 0
  Length = 2550
  MakeFace = true
  Points = (2) [(12395,-2965,0),(12395,-5515,0)]
  Start = (12395,-2965,0)
FEATURE [Part::Part2DObjectPython] Line471  # Draft 2D object (typed FeaturePython)
  ChamferSize = 0
  Closed = false
  End = (17495,-5515,0)
  FilletRadius = 0
  Length = 2550
  MakeFace = true
  Points = (2) [(17495,-2965,0),(17495,-5515,0)]
  Start = (17495,-2965,0)
FEATURE [Part::Part2DObjectPython] Line474  # Draft 2D object (typed FeaturePython)
  ChamferSize = 0
  Closed = false
  End = (12095,-5515,0)
  FilletRadius = 0
  Length = 2000
  MakeFace = true
  Points = (2) [(12095,-3515,0),(12095,-5515,0)]
  Start = (12095,-3515,0)
FEATURE [Part::Part2DObjectPython] Line475  # Draft 2D object (typed FeaturePython)
  ChamferSize = 0
  Closed = false
  End = (10095,-5515,0)
  FilletRadius = 0
  Length = 2000
  MakeFace = true
  Placement = pos=(-2000,0,0) rot=(0,0,1;0rad)
  Points = (2) [(12095,-3515,0),(12095,-5515,0)]
  Start = (10095,-3515,0)
FEATURE [Part::Part2DObjectPython] Line476  # Draft 2D object (typed FeaturePython)
  ChamferSize = 0
  Closed = false
  End = (10095,-3515,0)
  FilletRadius = 0
  Length = 2000
  MakeFace = true
  Points = (2) [(12095,-3515,0),(10095,-3515,0)]
  Start = (12095,-3515,0)
FEATURE [Part::FeaturePython] Wall091  # WARN: FeaturePython — macro-defined, semantics opaque (R4)
  Align = 0
  Base = -> Line475
  Face = 0
  Height = 3000
  Length = 0
  MoveWithHost = false
  Normal = (0,0,0)
  Role = 0
  Width = 200
FEATURE [Part::FeaturePython] Wall092  # WARN: FeaturePython — macro-defined, semantics opaque (R4)
  Align = 1
  Base = -> Line474
  Face = 0
  Height = 3000
  Length = 0
  MoveWithHost = false
  Normal = (0,0,0)
  Role = 0
  Width = 200
FEATURE [Sketcher::SketchObject] Sketch065
  Placement = pos=(10817.2,-3715,0) rot=(1,0,0;1.5708rad)
  sketch-geometry (8):
    g0: LineSegment StartX=0 StartY=0 StartZ=0 EndX=1000 EndY=0 EndZ=0
    g1: LineSegment StartX=1000 StartY=0 StartZ=0 EndX=1000 EndY=2000 EndZ=0
    g2: LineSegment StartX=1000 StartY=2000 StartZ=0 EndX=0 EndY=2000 EndZ=0
    g3: LineSegment StartX=0 StartY=2000 StartZ=0 EndX=0 EndY=0 EndZ=0
    g4: LineSegment StartX=100 StartY=0 StartZ=0 EndX=900 EndY=0 EndZ=0
    g5: LineSegment StartX=900 StartY=0 StartZ=0 EndX=900 EndY=1900 EndZ=0
    g6: LineSegment StartX=900 StartY=1900 StartZ=0 EndX=100 EndY=1900 EndZ=0
    g7: LineSegment StartX=100 StartY=1900 StartZ=0 EndX=100 EndY=0 EndZ=0
  constraints (23):
    c: Coincident(g0,g1)
    c: Coincident(g1,g2)
    c: Coincident(g2,g3)
    c: Coincident(g3,g0)
    c: Horizontal(g0)
    c: Horizontal(g2)
    c: Vertical(g1)
    c: Vertical(g3)
    c: Coincident(g4,g5)
    c: Coincident(g5,g6)
    c: Coincident(g6,g7)
    c: Coincident(g7,g4)
    c: Horizontal(g4)
    c: Horizontal(g6)
    c: Vertical(g5)
    c: Vertical(g7)
    c: DistanceY(g1) = 2000
    c: DistanceX(g0) = 1000
    c: DistanceY(g6,g2) = 100
    c: DistanceX(g2,g6) = 100
    c: DistanceX(g4,g0) = 100
    c: DistanceY(g0,g4) = 0
    c: Coincident(g0,g-1)
FEATURE [Part::FeaturePython] Window054  label="Window052"  # WARN: FeaturePython — macro-defined, semantics opaque (R4)
  Base = -> Sketch065
  Height = 2000
  HoleDepth = 0
  MoveWithHost = true
  Normal = (0,1,0)
  Preset = 6
  Role = 1
  Width = 1000
  WindowParts = OuterFrame | Frame | Wire0,Wire1 | 100.0 | 100.0 | Door | Solid panel | Wire1 | 100.0 | 200.0
FEATURE [Part::FeaturePython] Wall093  # WARN: FeaturePython — macro-defined, semantics opaque (R4)
  Align = 1
  Base = -> Line476
  Face = 0
  Height = 3000
  Length = 0
  MoveWithHost = false
  Normal = (0,0,0)
  Role = 0
  Subtractions = -> [Window054]
  Width = 200
FEATURE [Part::Part2DObjectPython] Rectangle042  # Draft 2D object (typed FeaturePython)
  ChamferSize = 0
  FilletRadius = 0
  Height = 1320
  Length = -2010
  MakeFace = true
  Placement = pos=(195,-5815,1090) rot=(1,0,0;1.5708rad)
FEATURE [Part::FeaturePython] Panel038  # WARN: FeaturePython — macro-defined, semantics opaque (R4)
  Base = -> Rectangle042
  Length = 0
  MoveWithHost = false
  Placement = pos=(0,25,0) rot=(0,0,1;0rad)
  Role = 0
  Sheets = 1
  Thickness = 10
  Width = 0
FEATURE [Part::Part2DObjectPython] Rectangle045  # Draft 2D object (typed FeaturePython)
  ChamferSize = 0
  FilletRadius = 0
  Height = 1300
  Length = -1840
  MakeFace = true
  Placement = pos=(2525,-5815,1100) rot=(1,0,0;1.5708rad)
FEATURE [Part::FeaturePython] Panel039  # WARN: FeaturePython — macro-defined, semantics opaque (R4)
  Base = -> Rectangle045
  Length = 0
  MoveWithHost = false
  Placement = pos=(0,25,0) rot=(0,0,1;0rad)
  Role = 0
  Sheets = 1
  Thickness = 10
  Width = 0
FEATURE [Part::FeaturePython] Clone026  label="Clone of Panel039"  # Draft clone (typed FeaturePython)
  Objects = -> [Panel039]
  Placement = pos=(2340,25,0) rot=(0,0,1;0rad)
  Scale = (1,1,1)
FEATURE [Part::FeaturePython] Clone028  label="Clone of Panel040"  # Draft clone (typed FeaturePython)
  Objects = -> [Panel039]
  Placement = pos=(4680,25,0) rot=(0,0,1;0rad)
  Scale = (1,1,1)
FEATURE [Part::FeaturePython] Clone031  label="Clone of Panel038"  # Draft clone (typed FeaturePython)
  Objects = -> [Panel038]
  Placement = pos=(9510,25,0) rot=(0,0,1;0rad)
  Scale = (1,1,1)
FEATURE [Part::Part2DObjectPython] Rectangle048  # Draft 2D object (typed FeaturePython)
  ChamferSize = 0
  FilletRadius = 0
  Height = -1370
  Length = -2060
  MakeFace = true
  Placement = pos=(220,-5815,2435) rot=(1,0,0;1.5708rad)
FEATURE [Part::Feature] Face
  shape: bbox 2160 x 2e-07 x 1470 mm, 1 faces, 0 solids (baked)
FEATURE [Part::Cut] Cut003
  Base = -> Face
  Tool = -> Rectangle048
FEATURE [Part::Extrusion] Extrusion039
  Base = -> Cut003
  Dir = (0,50,0)
  Solid = true
FEATURE [Part::Part2DObjectPython] Rectangle049  # Draft 2D object (typed FeaturePython)
  ChamferSize = 0
  FilletRadius = 0
  Height = -1450
  Length = -1990
  MakeFace = true
  Placement = pos=(2600,-5815,2475) rot=(1,0,0;1.5708rad)
  Support = -> Wall087
FEATURE [Part::Part2DObjectPython] Rectangle050  # Draft 2D object (typed FeaturePython)
  ChamferSize = 0
  FilletRadius = 0
  Height = -1350
  Length = -1890
  MakeFace = true
  Placement = pos=(2550,-5815,2425) rot=(1,0,0;1.5708rad)
FEATURE [Part::Cut] Cut004
  Base = -> Rectangle049
  Tool = -> Rectangle050
FEATURE [Part::Extrusion] Extrusion040
  Base = -> Cut004
  Dir = (0,50,0)
  Solid = true
FEATURE [Part::Feature] Extrusion041
  Placement = pos=(9510,0,0) rot=(0,0,1;0rad)
  shape: bbox 2160 x 50 x 1470 mm, 10 faces (baked)
FEATURE [Part::Feature] Extrusion042
  Placement = pos=(2340,0,0) rot=(0,0,1;0rad)
  shape: bbox 1990 x 50 x 1450 mm, 10 faces (baked)
FEATURE [Part::Feature] Extrusion043
  Placement = pos=(4680,0,0) rot=(0,0,1;0rad)
  shape: bbox 1990 x 50 x 1450 mm, 10 faces (baked)
FEATURE [App::DocumentObjectGroup] Group015  label="Cloture"
  Group = -> [Wall081,Wall082,Wall083,Structure039,Clone019,Clone020,Clone021,Clone022,Clone023,Clone024,Clone025,Wall086,Wall087,Wall088,Wall089,Wall090,Wall091,Wall092,Wall093,Panel038,Panel039,Clone026,Clone028,Clone031,Extrusion039,Extrusion040,Extrusion041,Extrusion042,Extrusion043]
FEATURE [Part::FeaturePython] Clone032  label="Clone of Main Sweep clone controller"  # WARN: FeaturePython — macro-defined, semantics opaque (R4)
  Scale = (1,1,1)
FEATURE [Part::FeaturePython] Clone033  label="Clone of Sweep006"  # WARN: FeaturePython — macro-defined, semantics opaque (R4)
  Scale = (1,1,1)
FEATURE [Part::FeaturePython] Clone034  label="Clone of Clone of Sweep005 (Mirror #1)004"  # WARN: FeaturePython — macro-defined, semantics opaque (R4)
  Placement = pos=(0,4150,-3e-12) rot=(0,0,1;0rad)
  Scale = (1,1,1)
FEATURE [App::DocumentObjectGroup] Group013  label="Roof rebar structure"
  Group = -> [Clone009,Clone010,Clone011,Clone012,Clone013,Clone015,Clone016,Clone017,Clone018,Clone032,Clone033,Clone034,Clone014]
FEATURE [Part::FeaturePython] Clone035  label="Clone of Extrusion015"  # WARN: FeaturePython — macro-defined, semantics opaque (R4)
  Placement = pos=(0,-1385,0) rot=(0,0,1;0rad)
  Scale = (1,1,1)
FEATURE [App::DocumentObjectGroup] Group004  label="roof"
  Group = -> [Clone,Clone004,Clone005,Clone006,Clone007,Clone008,Extrusion016,Extrusion017,Extrusion018,Extrusion019,Extrusion020,Extrusion021,Extrusion023,Extrusion024,Extrusion025,Extrusion026,Extrusion027,Extrusion028,Extrusion029,Extrusion030,Extrusion031,Extrusion032,Extrusion033,Group013,Clone035]
FEATURE [Part::Part2DObjectPython] DWire053  # Draft 2D object (typed FeaturePython)
  ChamferSize = 0
  Closed = true
  End = (52987,15849.6,0)
  FilletRadius = 0
  Length = 14710.1
  MakeFace = true
  Placement = pos=(0,-0.388761,0) rot=(0,0,1;0rad)
  Points = (10) [(52987,16000,0),(49287,16000,0),(49287,12944.9,0),(49437,12944.9,0),(49437,13500,0),(50037,13500,0),(50037,13650,0),(49437,13650,0),(49437,15850,0),+1 more]
  Start = (52987,15999.6,0)
FEATURE [Part::Part2DObjectPython] DWire054  # Draft 2D object (typed FeaturePython)
  ChamferSize = 0
  Closed = true
  End = (52987,14378.4,0)
  FilletRadius = 0
  Length = 3242.39
  MakeFace = true
  Placement = pos=(0,-0.388761,0) rot=(0,0,1;0rad)
  Points = (4) [(52987,15850,0),(53137,15850,0),(53137,14378.8,0),(52987,14378.8,0)]
  Start = (52987,15849.6,0)
FEATURE [Part::Part2DObjectPython] DWire055  # Draft 2D object (typed FeaturePython)
  ChamferSize = 0
  Closed = true
  End = (52987,13019.6,0)
  FilletRadius = 0
  Length = 1017.61
  MakeFace = true
  Placement = pos=(0,-0.388761,0) rot=(0,0,1;0rad)
  Points = (4) [(52987,13378.8,0),(53137,13378.8,0),(53137,13020,0),(52987,13020,0)]
  Start = (52987,13378.4,0)
FEATURE [Part::Part2DObjectPython] DWire056  # Draft 2D object (typed FeaturePython)
  ChamferSize = 0
  Closed = true
  End = (53137,12719.6,0)
  FilletRadius = 0
  Length = 11727.3
  MakeFace = true
  Placement = pos=(0,-0.388761,0) rot=(0,0,1;0rad)
  Points = (12) [(52987,12720,0),(52987,11850,0),(49437,11850,0),(49437,11944.9,0),(49287,11944.9,0),(49287,11297.3,0),(49437,11297.3,0),(49437,11700,0),+4 more]
  Start = (52987,12719.6,0)
FEATURE [Part::Part2DObjectPython] DWire057  # Draft 2D object (typed FeaturePython)
  ChamferSize = 0
  Closed = true
  End = (49437,10296.9,0)
  FilletRadius = 0
  Length = 12402.6
  MakeFace = true
  Placement = pos=(0,-0.388761,0) rot=(0,0,1;0rad)
  Points = (12) [(49287,10297.3,0),(49287,9950,0),(49437,9950,0),(49437,10050,0),(52987,10050,0),(52987,8550,0),(53137,8550,0),(53137,10704,0),(52987,10704,0),+3 more]
  Start = (49287,10296.9,0)
FEATURE [Part::Part2DObjectPython] DWire058  # Draft 2D object (typed FeaturePython)
  ChamferSize = 0
  Closed = true
  End = (49287,6049.61,0)
  FilletRadius = 0
  Length = 14900
  MakeFace = true
  Placement = pos=(0,-0.388761,0) rot=(0,0,1;0rad)
  Points = (12) [(49287,8950,0),(49437,8950,0),(49437,8400,0),(50037,8400,0),(50037,8250,0),(49437,8250,0),(49437,6050,0),(52987,6050,0),(52987,5900,0),(49187,5900,0),+2 more]
  Start = (49287,8949.61,0)
FEATURE [Part::Part2DObjectPython] DWire059  # Draft 2D object (typed FeaturePython)
  ChamferSize = 0
  Closed = true
  End = (52987,6049.61,0)
  FilletRadius = 0
  Length = 2700
  MakeFace = true
  Placement = pos=(0,-0.388761,0) rot=(0,0,1;0rad)
  Points = (4) [(52987,7250,0),(53137,7250,0),(53137,6050,0),(52987,6050,0)]
  Start = (52987,7249.61,0)
FEATURE [Part::Part2DObjectPython] DWire060  # Draft 2D object (typed FeaturePython)
  ChamferSize = 0
  Closed = true
  End = (42137,13019.6,0)
  FilletRadius = 0
  Length = 5960
  MakeFace = true
  Placement = pos=(0,-0.388761,0) rot=(0,0,1;0rad)
  Points = (4) [(42137,15850,0),(42287,15850,0),(42287,13020,0),(42137,13020,0)]
  Start = (42137,15849.6,0)
FEATURE [Part::Part2DObjectPython] DWire061  # Draft 2D object (typed FeaturePython)
  ChamferSize = 0
  Closed = true
  End = (45487,11999.6,0)
  FilletRadius = 0
  Length = 10617.2
  MakeFace = true
  Placement = pos=(0,-0.388761,0) rot=(0,0,1;0rad)
  Points = (10) [(45487,12150,0),(42137,12150,0),(42137,10791.4,0),(42287,10791.4,0),(42287,12000,0),(45162,12000,0),(45162,11400,0),(45312,11400,0),(45312,12000,0),+1 more]
  Start = (45487,12149.6,0)
FEATURE [Part::Part2DObjectPython] DWire062  # Draft 2D object (typed FeaturePython)
  ChamferSize = 0
  Closed = true
  End = (46737,12719.6,0)
  FilletRadius = 0
  Length = 19922.8
  MakeFace = true
  Placement = pos=(0,-0.388761,0) rot=(0,0,1;0rad)
  Points = (16) [(46587,12720,0),(46587,12150,0),(46487,12150,0),(46487,12000,0),(46587,12000,0),(46587,9750,0),(42287,9750,0),(42287,10291.4,0),(42137,10291.4,0),+7 more]
  Start = (46587,12719.6,0)
FEATURE [Part::Part2DObjectPython] DWire064  # Draft 2D object (typed FeaturePython)
  ChamferSize = 0
  Closed = true
  End = (42137,6049.61,0)
  FilletRadius = 0
  Length = 3700
  MakeFace = true
  Placement = pos=(0,-0.388761,0) rot=(0,0,1;0rad)
  Points = (4) [(42137,7750,0),(42287,7750,0),(42287,6050,0),(42137,6050,0)]
  Start = (42137,7749.61,0)
FEATURE [Part::Part2DObjectPython] DWire065  # Draft 2D object (typed FeaturePython)
  ChamferSize = 0
  Closed = true
  End = (45237,6049.61,0)
  FilletRadius = 0
  Length = 6200
  MakeFace = true
  Placement = pos=(0,-0.388761,0) rot=(0,0,1;0rad)
  Points = (4) [(42287,6050,0),(42287,5900,0),(45237,5900,0),(45237,6050,0)]
  Start = (42287,6049.61,0)
FEATURE [Part::Part2DObjectPython] DWire066  # Draft 2D object (typed FeaturePython)
  ChamferSize = 0
  Closed = true
  End = (45237,6049.61,0)
  FilletRadius = 0
  Length = 2499.66
  MakeFace = true
  Placement = pos=(0,-0.388761,0) rot=(0,0,1;0rad)
  Points = (4) [(45237,7149.83,0),(45387,7149.83,0),(45387,6050,0),(45237,6050,0)]
  Start = (45237,7149.44,0)
FEATURE [Part::Part2DObjectPython] DWire067  # Draft 2D object (typed FeaturePython)
  ChamferSize = 0
  Closed = true
  End = (42137,2149.61,0)
  FilletRadius = 0
  Length = 6500
  MakeFace = true
  Placement = pos=(0,-0.388761,0) rot=(0,0,1;0rad)
  Points = (4) [(42137,5250,0),(42287,5250,0),(42287,2150,0),(42137,2150,0)]
  Start = (42137,5249.61,0)
FEATURE [Part::Part2DObjectPython] DWire068  # Draft 2D object (typed FeaturePython)
  ChamferSize = 0
  Closed = true
  End = (43184,2149.61,0)
  FilletRadius = 0
  Length = 2093.96
  MakeFace = true
  Placement = pos=(0,-0.388761,0) rot=(0,0,1;0rad)
  Points = (4) [(42287,2150,0),(42287,2000,0),(43184,2000,0),(43184,2150,0)]
  Start = (42287,2149.61,0)
FEATURE [Part::Part2DObjectPython] DWire069  # Draft 2D object (typed FeaturePython)
  ChamferSize = 0
  Closed = true
  End = (45237,2149.61,0)
  FilletRadius = 0
  Length = 2406.04
  MakeFace = true
  Placement = pos=(0,-0.388761,0) rot=(0,0,1;0rad)
  Points = (4) [(44184,2150,0),(44184,2000,0),(45237,2000,0),(45237,2150,0)]
  Start = (44184,2149.61,0)
FEATURE [Part::Part2DObjectPython] DWire070  # Draft 2D object (typed FeaturePython)
  ChamferSize = 0
  Closed = true
  End = (46162,2149.61,0)
  FilletRadius = 0
  Length = 1850
  MakeFace = true
  Placement = pos=(0,-0.388761,0) rot=(0,0,1;0rad)
  Points = (4) [(45387,2150,0),(45387,2000,0),(46162,2000,0),(46162,2150,0)]
  Start = (45387,2149.61,0)
FEATURE [Part::Part2DObjectPython] DWire071  # Draft 2D object (typed FeaturePython)
  ChamferSize = 0
  Closed = true
  End = (47937,2149.61,0)
  FilletRadius = 0
  Length = 1850
  MakeFace = true
  Placement = pos=(0,-0.388761,0) rot=(0,0,1;0rad)
  Points = (4) [(47162,2150,0),(47162,2000,0),(47937,2000,0),(47937,2150,0)]
  Start = (47162,2149.61,0)
FEATURE [Part::Part2DObjectPython] DWire072  # Draft 2D object (typed FeaturePython)
  ChamferSize = 0
  Closed = true
  End = (47937,5749.61,0)
  FilletRadius = 0
  Length = 7500
  MakeFace = true
  Placement = pos=(0,-0.388761,0) rot=(0,0,1;0rad)
  Points = (4) [(47937,2150,0),(48087,2150,0),(48087,5750,0),(47937,5750,0)]
  Start = (47937,2149.61,0)
FEATURE [Part::Part2DObjectPython] DWire073  # Draft 2D object (typed FeaturePython)
  ChamferSize = 0
  Closed = true
  End = (46737,8249.61,0)
  FilletRadius = 0
  Length = 5199.89
  MakeFace = true
  Placement = pos=(0,-0.388761,0) rot=(0,0,1;0rad)
  Points = (6) [(46587,8250,0),(46587,5900,0),(46836.9,5900,0),(46836.9,6050,0),(46737,6050,0),(46737,8250,0)]
  Start = (46587,8249.61,0)
FEATURE [Part::Part2DObjectPython] DWire074  # Draft 2D object (typed FeaturePython)
  ChamferSize = 0
  Closed = true
  End = (47937,6049.61,0)
  FilletRadius = 0
  Length = 500.107
  MakeFace = true
  Placement = pos=(0,-0.388761,0) rot=(0,0,1;0rad)
  Points = (4) [(47836.9,6050,0),(47836.9,5900,0),(47937,5900,0),(47937,6050,0)]
  Start = (47836.9,6049.61,0)
FEATURE [Part::Part2DObjectPython] DWire075  # Draft 2D object (typed FeaturePython)
  ChamferSize = 0
  Closed = true
  End = (48187,6049.61,0)
  FilletRadius = 0
  Length = 500
  MakeFace = true
  Placement = pos=(0,-0.388761,0) rot=(0,0,1;0rad)
  Points = (4) [(48087,6050,0),(48087,5900,0),(48187,5900,0),(48187,6050,0)]
  Start = (48087,6049.61,0)
FEATURE [App::Annotation] Text  label="FAMILY ROOM"
  LabelText = FAMILY ROOM
  Position = (44087,14066.3,0)
FEATURE [App::Annotation] Text001  label="BED ROOM3"
  LabelText = BED ROOM 3
  Position = (50950.7,14171.2,0)
FEATURE [App::Annotation] Text002  label="BED ROOM 2"
  LabelText = BED ROOM 2
  Position = (51003.7,8054.16,0)
FEATURE [App::Annotation] Text003  label="MASTER BEDROOM"
  LabelText = MASTER BEDROOM
  Position = (44494.7,3845.16,0)
FEATURE [App::Annotation] Text004  label="VERANDA / BALCONY"
  LabelText = VERANDA / BALCONY
  Position = (50347.7,3942.16,0)
FEATURE [App::Annotation] Text005  label="MASTER BATHROOM"
  LabelText = MASTER BATHROOM
  Position = (42671.5,7053.46,0)
FEATURE [App::Annotation] Text006  label="CORRIDOOR"
  LabelText = CORRIDOR
  Position = (47405.7,7043.16,0)
FEATURE [Part::Part2DObjectPython] DWire077  # Draft 2D object (typed FeaturePython)
  ChamferSize = 0
  Closed = true
  End = (36348.4,15999.6,0)
  FilletRadius = 0
  Length = 11360
  MakeFace = true
  Points = (8) [(32648.4,15999.6,0),(32648.4,15849.6,0),(34298.4,15849.6,0),(34298.4,14019.6,0),(34448.4,14019.6,0),(34448.4,15849.6,0),(36348.4,15849.6,0),+1 more]
  Start = (32648.4,15999.6,0)
FEATURE [Part::Part2DObjectPython] DWire078  # Draft 2D object (typed FeaturePython)
  ChamferSize = 0
  Closed = true
  End = (36348.4,13878.4,0)
  FilletRadius = 0
  Length = 4242.39
  MakeFace = true
  Points = (4) [(36348.4,15849.6,0),(36498.4,15849.6,0),(36498.4,13878.4,0),(36348.4,13878.4,0)]
  Start = (36348.4,15849.6,0)
FEATURE [Part::Part2DObjectPython] DWire079  # Draft 2D object (typed FeaturePython)
  ChamferSize = 0
  Closed = true
  End = (36348.4,13019.6,0)
  FilletRadius = 0
  Length = 1017.61
  MakeFace = true
  Points = (4) [(36348.4,13378.4,0),(36498.4,13378.4,0),(36498.4,13019.6,0),(36348.4,13019.6,0)]
  Start = (36348.4,13378.4,0)
FEATURE [Part::Part2DObjectPython] DWire080  # Draft 2D object (typed FeaturePython)
  ChamferSize = 0
  Closed = true
  End = (36348.4,12869.6,0)
  FilletRadius = 0
  Length = 8300
  MakeFace = true
  Points = (8) [(36348.4,13019.6,0),(34448.4,13019.6,0),(34448.4,13119.6,0),(34298.4,13119.6,0),(34298.4,13019.6,0),(32448.4,13019.6,0),(32448.4,12869.6,0),+1 more]
  Start = (36348.4,13019.6,0)
FEATURE [Part::Part2DObjectPython] DWire081  # Draft 2D object (typed FeaturePython)
  ChamferSize = 0
  Closed = true
  End = (36348.4,11203.6,0)
  FilletRadius = 0
  Length = 3332
  MakeFace = true
  Points = (4) [(36348.4,12719.6,0),(36498.4,12719.6,0),(36498.4,11203.6,0),(36348.4,11203.6,0)]
  Start = (36348.4,12719.6,0)
FEATURE [Part::Part2DObjectPython] DWire082  # Draft 2D object (typed FeaturePython)
  ChamferSize = 0
  Closed = true
  End = (36348.4,8549.61,0)
  FilletRadius = 0
  Length = 4608
  MakeFace = true
  Points = (4) [(36348.4,10703.6,0),(36498.4,10703.6,0),(36498.4,8549.61,0),(36348.4,8549.61,0)]
  Start = (36348.4,10703.6,0)
FEATURE [Part::Part2DObjectPython] DWire083  # Draft 2D object (typed FeaturePython)
  ChamferSize = 0
  Closed = true
  End = (36348.4,6049.61,0)
  FilletRadius = 0
  Length = 2700
  MakeFace = true
  Points = (4) [(36348.4,7249.61,0),(36498.4,7249.61,0),(36498.4,6049.61,0),(36348.4,6049.61,0)]
  Start = (36348.4,7249.61,0)
FEATURE [Part::Part2DObjectPython] DWire090  # Draft 2D object (typed FeaturePython)
  ChamferSize = 0
  Closed = true
  End = (28598.4,1999.61,0)
  FilletRadius = 0
  Length = 2406.04
  MakeFace = true
  Points = (4) [(28598.4,2149.61,0),(27545.4,2149.61,0),(27545.4,1999.61,0),(28598.4,1999.61,0)]
  Start = (28598.4,2149.61,0)
FEATURE [Part::Part2DObjectPython] DWire091  # Draft 2D object (typed FeaturePython)
  ChamferSize = 0
  Closed = true
  End = (25648.4,2149.61,0)
  FilletRadius = 0
  Length = 2093.96
  MakeFace = true
  Points = (4) [(26545.4,2149.61,0),(26545.4,1999.61,0),(25648.4,1999.61,0),(25648.4,2149.61,0)]
  Start = (26545.4,2149.61,0)
FEATURE [Part::Part2DObjectPython] DWire092  # Draft 2D object (typed FeaturePython)
  ChamferSize = 0
  Closed = true
  End = (25648.4,5249.61,0)
  FilletRadius = 0
  Length = 6500
  MakeFace = true
  Points = (4) [(25648.4,2149.61,0),(25498.4,2149.61,0),(25498.4,5249.61,0),(25648.4,5249.61,0)]
  Start = (25648.4,2149.61,0)
FEATURE [Part::Part2DObjectPython] DWire093  # Draft 2D object (typed FeaturePython)
  ChamferSize = 0
  Closed = true
  End = (25648.4,6049.61,0)
  FilletRadius = 0
  Length = 7600
  MakeFace = true
  Points = (8) [(25498.4,6049.61,0),(25498.4,7749.61,0),(25648.4,7749.61,0),(25648.4,6649.61,0),(27598.4,6649.61,0),(27598.4,6499.61,0),(25648.4,6499.61,0),+1 more]
  Start = (25498.4,6049.61,0)
FEATURE [Part::Part2DObjectPython] DWire094  # Draft 2D object (typed FeaturePython)
  ChamferSize = 0
  Closed = true
  End = (28498.4,6649.61,0)
  FilletRadius = 0
  Length = 11500
  MakeFace = true
  Points = (12) [(28498.4,6499.61,0),(28598.4,6499.61,0),(28598.4,6049.61,0),(28748.4,6049.61,0),(28748.4,8599.61,0),(28598.4,8599.61,0),(28598.4,8399.61,0),+5 more]
  Start = (28498.4,6499.61,0)
FEATURE [Part::Part2DObjectPython] DWire095  # Draft 2D object (typed FeaturePython)
  ChamferSize = 0
  Closed = true
  End = (25498.4,9049.61,0)
  FilletRadius = 0
  Length = 10382.8
  MakeFace = true
  Points = (12) [(25498.4,10791,0),(25648.4,10791,0),(25648.4,9749.61,0),(28848.4,9749.61,0),(28848.4,9599.61,0),(28748.4,9599.61,0),(28748.4,9499.61,0),+5 more]
  Start = (25498.4,10791,0)
FEATURE [Part::Part2DObjectPython] DWire096  # Draft 2D object (typed FeaturePython)
  ChamferSize = 0
  Closed = true
  End = (29848.4,9749.61,0)
  FilletRadius = 0
  Length = 8840
  MakeFace = true
  Points = (8) [(29848.4,9599.61,0),(29948.4,9599.61,0),(29948.4,8549.61,0),(30098.4,8549.61,0),(30098.4,12719.6,0),(29948.4,12719.6,0),(29948.4,9749.61,0),+1 more]
  Start = (29848.4,9599.61,0)
FEATURE [Part::Part2DObjectPython] DWire097  # Draft 2D object (typed FeaturePython)
  ChamferSize = 0
  Closed = true
  End = (25498.4,11791,0)
  FilletRadius = 0
  Length = 2157.15
  MakeFace = true
  Points = (4) [(25498.4,12719.6,0),(25648.4,12719.6,0),(25648.4,11791,0),(25498.4,11791,0)]
  Start = (25498.4,12719.6,0)
FEATURE [Part::Part2DObjectPython] DWire098  # Draft 2D object (typed FeaturePython)
  ChamferSize = 0
  Closed = true
  End = (25648.4,12869.6,0)
  FilletRadius = 0
  Length = 500
  MakeFace = true
  Points = (4) [(25648.4,13019.6,0),(25748.4,13019.6,0),(25748.4,12869.6,0),(25648.4,12869.6,0)]
  Start = (25648.4,13019.6,0)
FEATURE [Part::Part2DObjectPython] DWire099  # Draft 2D object (typed FeaturePython)
  ChamferSize = 0
  Closed = true
  End = (28598,13019.6,0)
  FilletRadius = 0
  Length = 6900
  MakeFace = true
  Points = (8) [(26748.4,13019.6,0),(26748.4,12869.6,0),(29948.4,12869.6,0),(29948.4,13019.6,0),(28748,13019.6,0),(28748,13119.6,0),(28598,13119.6,0),+1 more]
  Start = (26748.4,13019.6,0)
FEATURE [Part::Part2DObjectPython] DWire100  # Draft 2D object (typed FeaturePython)
  ChamferSize = 0
  Closed = true
  End = (31298.4,13019.6,0)
  FilletRadius = 0
  Length = 2700
  MakeFace = true
  Points = (4) [(30098.4,13019.6,0),(30098.4,12869.6,0),(31298.4,12869.6,0),(31298.4,13019.6,0)]
  Start = (30098.4,13019.6,0)
FEATURE [Part::Part2DObjectPython] DWire101  # Draft 2D object (typed FeaturePython)
  ChamferSize = 0
  Closed = true
  End = (28598,14119.6,0)
  FilletRadius = 0
  Length = 3759.66
  MakeFace = true
  Points = (4) [(28598.4,15849.6,0),(28748,15849.6,0),(28748,14119.6,0),(28598,14119.6,0)]
  Start = (28598.4,15849.6,0)
FEATURE [Part::Part2DObjectPython] DWire102  # Draft 2D object (typed FeaturePython)
  ChamferSize = 0
  Closed = true
  End = (28748.4,15849.6,0)
  FilletRadius = 0
  Length = 5400
  MakeFace = true
  Points = (4) [(31298.4,15849.6,0),(31298.4,15999.6,0),(28748.4,15999.6,0),(28748.4,15849.6,0)]
  Start = (31298.4,15849.6,0)
FEATURE [Part::Part2DObjectPython] DWire103  # Draft 2D object (typed FeaturePython)
  ChamferSize = 0
  Closed = true
  End = (25498.4,16149.6,0)
  FilletRadius = 0
  Length = 900
  MakeFace = true
  Points = (4) [(25498.4,15849.6,0),(25648.4,15849.6,0),(25648.4,16149.6,0),(25498.4,16149.6,0)]
  Start = (25498.4,15849.6,0)
FEATURE [Part::Part2DObjectPython] DWire104  # Draft 2D object (typed FeaturePython)
  ChamferSize = 0
  Closed = true
  End = (28598.4,16149.6,0)
  FilletRadius = 0
  Length = 900
  MakeFace = true
  Placement = pos=(3100,0,0) rot=(0,0,1;0rad)
  Points = (4) [(25498.4,15849.6,0),(25648.4,15849.6,0),(25648.4,16149.6,0),(25498.4,16149.6,0)]
  Start = (28598.4,15849.6,0)
FEATURE [Part::Part2DObjectPython] DWire105  # Draft 2D object (typed FeaturePython)
  ChamferSize = 0
  Closed = true
  End = (31298.4,16149.6,0)
  FilletRadius = 0
  Length = 900
  MakeFace = true
  Placement = pos=(5800,0,0) rot=(0,0,1;0rad)
  Points = (4) [(25498.4,15849.6,0),(25648.4,15849.6,0),(25648.4,16149.6,0),(25498.4,16149.6,0)]
  Start = (31298.4,15849.6,0)
FEATURE [Part::Part2DObjectPython] DWire106  # Draft 2D object (typed FeaturePython)
  ChamferSize = 0
  Closed = true
  End = (36348.4,16149.6,0)
  FilletRadius = 0
  Length = 900
  MakeFace = true
  Placement = pos=(10850,-0.000305176,0) rot=(0,0,1;0rad)
  Points = (4) [(25498.4,15849.6,0),(25648.4,15849.6,0),(25648.4,16149.6,0),(25498.4,16149.6,0)]
  Start = (36348.4,15849.6,0)
FEATURE [Part::Part2DObjectPython] DWire107  # Draft 2D object (typed FeaturePython)
  ChamferSize = 0
  Closed = true
  End = (25498.4,13019.6,0)
  FilletRadius = 0
  Length = 900
  MakeFace = true
  Placement = pos=(-0.0009766,-3130,0) rot=(0,0,1;0rad)
  Points = (4) [(25498.4,15849.6,0),(25648.4,15849.6,0),(25648.4,16149.6,0),(25498.4,16149.6,0)]
  Start = (25498.4,12719.6,0)
FEATURE [Part::Part2DObjectPython] DWire108  # Draft 2D object (typed FeaturePython)
  ChamferSize = 0
  Closed = true
  End = (29948.4,13019.6,0)
  FilletRadius = 0
  Length = 900
  MakeFace = true
  Placement = pos=(4450,-3130,0) rot=(0,0,1;0rad)
  Points = (4) [(25498.4,15849.6,0),(25648.4,15849.6,0),(25648.4,16149.6,0),(25498.4,16149.6,0)]
  Start = (29948.4,12719.6,0)
FEATURE [Part::Part2DObjectPython] DWire109  # Draft 2D object (typed FeaturePython)
  ChamferSize = 0
  Closed = true
  End = (31298.4,13019.6,0)
  FilletRadius = 0
  Length = 900
  MakeFace = true
  Placement = pos=(5800,-3130,0) rot=(0,0,1;0rad)
  Points = (4) [(25498.4,15849.6,0),(25648.4,15849.6,0),(25648.4,16149.6,0),(25498.4,16149.6,0)]
  Start = (31298.4,12719.6,0)
FEATURE [Part::Part2DObjectPython] DWire110  # Draft 2D object (typed FeaturePython)
  ChamferSize = 0
  Closed = true
  End = (36348.4,13019.6,0)
  FilletRadius = 0
  Length = 900
  MakeFace = true
  Placement = pos=(10850,-3130,0) rot=(0,0,1;0rad)
  Points = (4) [(25498.4,15849.6,0),(25648.4,15849.6,0),(25648.4,16149.6,0),(25498.4,16149.6,0)]
  Start = (36348.4,12719.6,0)
FEATURE [Part::Part2DObjectPython] DWire111  # Draft 2D object (typed FeaturePython)
  ChamferSize = 0
  Closed = true
  End = (36348.4,8549.61,0)
  FilletRadius = 0
  Length = 900
  MakeFace = true
  Placement = pos=(10850,-7600,0) rot=(0,0,1;0rad)
  Points = (4) [(25498.4,15849.6,0),(25648.4,15849.6,0),(25648.4,16149.6,0),(25498.4,16149.6,0)]
  Start = (36348.4,8249.61,0)
FEATURE [Part::Part2DObjectPython] DWire112  # Draft 2D object (typed FeaturePython)
  ChamferSize = 0
  Closed = true
  End = (31298.4,8549.61,0)
  FilletRadius = 0
  Length = 900
  MakeFace = true
  Placement = pos=(5800,-7600,0) rot=(0,0,1;0rad)
  Points = (4) [(25498.4,15849.6,0),(25648.4,15849.6,0),(25648.4,16149.6,0),(25498.4,16149.6,0)]
  Start = (31298.4,8249.61,0)
FEATURE [Part::Part2DObjectPython] DWire113  # Draft 2D object (typed FeaturePython)
  ChamferSize = 0
  Closed = true
  End = (29948.4,8549.61,0)
  FilletRadius = 0
  Length = 900
  MakeFace = true
  Placement = pos=(4450,-7600,0) rot=(0,0,1;0rad)
  Points = (4) [(25498.4,15849.6,0),(25648.4,15849.6,0),(25648.4,16149.6,0),(25498.4,16149.6,0)]
  Start = (29948.4,8249.61,0)
FEATURE [Part::Part2DObjectPython] DWire114  # Draft 2D object (typed FeaturePython)
  ChamferSize = 0
  Closed = true
  End = (25498.4,8549.61,0)
  FilletRadius = 0
  Length = 900
  MakeFace = true
  Placement = pos=(-0.0009766,-7600,0) rot=(0,0,1;0rad)
  Points = (4) [(25498.4,15849.6,0),(25648.4,15849.6,0),(25648.4,16149.6,0),(25498.4,16149.6,0)]
  Start = (25498.4,8249.61,0)
FEATURE [Part::Part2DObjectPython] DWire115  # Draft 2D object (typed FeaturePython)
  ChamferSize = 0
  Closed = true
  End = (36348.4,6049.61,0)
  FilletRadius = 0
  Length = 900
  MakeFace = true
  Placement = pos=(10850,-10100,0) rot=(0,0,1;0rad)
  Points = (4) [(25498.4,15849.6,0),(25648.4,15849.6,0),(25648.4,16149.6,0),(25498.4,16149.6,0)]
  Start = (36348.4,5749.61,0)
FEATURE [Part::Part2DObjectPython] DWire116  # Draft 2D object (typed FeaturePython)
  ChamferSize = 0
  Closed = true
  End = (25498.4,6049.61,0)
  FilletRadius = 0
  Length = 900
  MakeFace = true
  Placement = pos=(-0.0009766,-10100,0) rot=(0,0,1;0rad)
  Points = (4) [(25498.4,15849.6,0),(25648.4,15849.6,0),(25648.4,16149.6,0),(25498.4,16149.6,0)]
  Start = (25498.4,5749.61,0)
FEATURE [Part::Part2DObjectPython] DWire117  # Draft 2D object (typed FeaturePython)
  ChamferSize = 0
  Closed = true
  End = (28598.4,6049.61,0)
  FilletRadius = 0
  Length = 900
  MakeFace = true
  Placement = pos=(3100,-10100,0) rot=(0,0,1;0rad)
  Points = (4) [(25498.4,15849.6,0),(25648.4,15849.6,0),(25648.4,16149.6,0),(25498.4,16149.6,0)]
  Start = (28598.4,5749.61,0)
FEATURE [Part::Part2DObjectPython] DWire118  # Draft 2D object (typed FeaturePython)
  ChamferSize = 0
  Closed = true
  End = (31298.4,6049.61,0)
  FilletRadius = 0
  Length = 900
  MakeFace = true
  Placement = pos=(5800,-10100,0) rot=(0,0,1;0rad)
  Points = (4) [(25498.4,15849.6,0),(25648.4,15849.6,0),(25648.4,16149.6,0),(25498.4,16149.6,0)]
  Start = (31298.4,5749.61,0)
FEATURE [Part::Part2DObjectPython] DWire119  # Draft 2D object (typed FeaturePython)
  ChamferSize = 0
  Closed = true
  End = (31298.4,2149.61,0)
  FilletRadius = 0
  Length = 900
  MakeFace = true
  Placement = pos=(5800,-14000,0) rot=(0,0,1;0rad)
  Points = (4) [(25498.4,15849.6,0),(25648.4,15849.6,0),(25648.4,16149.6,0),(25498.4,16149.6,0)]
  Start = (31298.4,1849.61,0)
FEATURE [Part::Part2DObjectPython] DWire120  # Draft 2D object (typed FeaturePython)
  ChamferSize = 0
  Closed = true
  End = (28598.4,2149.61,0)
  FilletRadius = 0
  Length = 900
  MakeFace = true
  Placement = pos=(3100,-14000,0) rot=(0,0,1;0rad)
  Points = (4) [(25498.4,15849.6,0),(25648.4,15849.6,0),(25648.4,16149.6,0),(25498.4,16149.6,0)]
  Start = (28598.4,1849.61,0)
FEATURE [Part::Part2DObjectPython] DWire121  # Draft 2D object (typed FeaturePython)
  ChamferSize = 0
  Closed = true
  End = (25498.4,2149.61,0)
  FilletRadius = 0
  Length = 900
  MakeFace = true
  Placement = pos=(-0.0009766,-14000,0) rot=(0,0,1;0rad)
  Points = (4) [(25498.4,15849.6,0),(25648.4,15849.6,0),(25648.4,16149.6,0),(25498.4,16149.6,0)]
  Start = (25498.4,1849.61,0)
FEATURE [Part::Part2DObjectPython] DWire122  # Draft 2D object (typed FeaturePython)
  ChamferSize = 0
  Closed = true
  End = (36348.4,2149.61,0)
  FilletRadius = 0
  Length = 900
  MakeFace = true
  Placement = pos=(10850,-14000,0) rot=(0,0,1;0rad)
  Points = (4) [(25498.4,15849.6,0),(25648.4,15849.6,0),(25648.4,16149.6,0),(25498.4,16149.6,0)]
  Start = (36348.4,1849.61,0)
FEATURE [App::DocumentObjectGroup] Group021  label="A-Columns level 1"
  Group = -> [DWire103,DWire104,DWire105,DWire106,DWire107,DWire108,DWire109,DWire110,DWire111,DWire112,DWire113,DWire114,DWire115,DWire116,DWire117,DWire118,DWire119,DWire120,DWire121,DWire122]
FEATURE [Part::Part2DObjectPython] DWire123  # Draft 2D object (typed FeaturePython)
  ChamferSize = 0
  Closed = true
  End = (52987,2149.61,0)
  FilletRadius = 0
  Length = 900
  MakeFace = true
  Placement = pos=(27488.6,-14000,0) rot=(0,0,1;0rad)
  Points = (4) [(25498.4,15849.6,0),(25648.4,15849.6,0),(25648.4,16149.6,0),(25498.4,16149.6,0)]
  Start = (52987,1849.61,0)
FEATURE [Part::Part2DObjectPython] DWire124  # Draft 2D object (typed FeaturePython)
  ChamferSize = 0
  Closed = true
  End = (42137,16149.6,0)
  FilletRadius = 0
  Length = 900
  MakeFace = true
  Placement = pos=(16638.6,-0.0003052,0) rot=(0,0,1;0rad)
  Points = (4) [(25498.4,15849.6,0),(25648.4,15849.6,0),(25648.4,16149.6,0),(25498.4,16149.6,0)]
  Start = (42137,15849.6,0)
FEATURE [Part::Part2DObjectPython] DWire125  # Draft 2D object (typed FeaturePython)
  ChamferSize = 0
  Closed = true
  End = (45237,16149.6,0)
  FilletRadius = 0
  Length = 900
  MakeFace = true
  Placement = pos=(19738.6,-0.0003052,0) rot=(0,0,1;0rad)
  Points = (4) [(25498.4,15849.6,0),(25648.4,15849.6,0),(25648.4,16149.6,0),(25498.4,16149.6,0)]
  Start = (45237,15849.6,0)
FEATURE [Part::Part2DObjectPython] DWire126  # Draft 2D object (typed FeaturePython)
  ChamferSize = 0
  Closed = true
  End = (47937,16149.6,0)
  FilletRadius = 0
  Length = 900
  MakeFace = true
  Placement = pos=(22438.6,-0.0003052,0) rot=(0,0,1;0rad)
  Points = (4) [(25498.4,15849.6,0),(25648.4,15849.6,0),(25648.4,16149.6,0),(25498.4,16149.6,0)]
  Start = (47937,15849.6,0)
FEATURE [Part::Part2DObjectPython] DWire127  # Draft 2D object (typed FeaturePython)
  ChamferSize = 0
  Closed = true
  End = (47937,13019.6,0)
  FilletRadius = 0
  Length = 900
  MakeFace = true
  Placement = pos=(22438.6,-3130,0) rot=(0,0,1;0rad)
  Points = (4) [(25498.4,15849.6,0),(25648.4,15849.6,0),(25648.4,16149.6,0),(25498.4,16149.6,0)]
  Start = (47937,12719.6,0)
FEATURE [Part::Part2DObjectPython] DWire128  # Draft 2D object (typed FeaturePython)
  ChamferSize = 0
  Closed = true
  End = (46587,13019.6,0)
  FilletRadius = 0
  Length = 900
  MakeFace = true
  Placement = pos=(21088.6,-3130,0) rot=(0,0,1;0rad)
  Points = (4) [(25498.4,15849.6,0),(25648.4,15849.6,0),(25648.4,16149.6,0),(25498.4,16149.6,0)]
  Start = (46587,12719.6,0)
FEATURE [Part::Part2DObjectPython] DWire129  # Draft 2D object (typed FeaturePython)
  ChamferSize = 0
  Closed = true
  End = (52987,16149.6,0)
  FilletRadius = 0
  Length = 900
  MakeFace = true
  Placement = pos=(27488.6,-0.000610376,0) rot=(0,0,1;0rad)
  Points = (4) [(25498.4,15849.6,0),(25648.4,15849.6,0),(25648.4,16149.6,0),(25498.4,16149.6,0)]
  Start = (52987,15849.6,0)
FEATURE [Part::Part2DObjectPython] DWire130  # Draft 2D object (typed FeaturePython)
  ChamferSize = 0
  Closed = true
  End = (42137,13019.6,0)
  FilletRadius = 0
  Length = 900
  MakeFace = true
  Placement = pos=(16638.6,-3130,0) rot=(0,0,1;0rad)
  Points = (4) [(25498.4,15849.6,0),(25648.4,15849.6,0),(25648.4,16149.6,0),(25498.4,16149.6,0)]
  Start = (42137,12719.6,0)
FEATURE [Part::Part2DObjectPython] DWire131  # Draft 2D object (typed FeaturePython)
  ChamferSize = 0
  Closed = true
  End = (52987,8549.61,0)
  FilletRadius = 0
  Length = 900
  MakeFace = true
  Placement = pos=(27488.6,-7600,0) rot=(0,0,1;0rad)
  Points = (4) [(25498.4,15849.6,0),(25648.4,15849.6,0),(25648.4,16149.6,0),(25498.4,16149.6,0)]
  Start = (52987,8249.61,0)
FEATURE [Part::Part2DObjectPython] DWire132  # Draft 2D object (typed FeaturePython)
  ChamferSize = 0
  Closed = true
  End = (47937,8549.61,0)
  FilletRadius = 0
  Length = 900
  MakeFace = true
  Placement = pos=(22438.6,-7600,0) rot=(0,0,1;0rad)
  Points = (4) [(25498.4,15849.6,0),(25648.4,15849.6,0),(25648.4,16149.6,0),(25498.4,16149.6,0)]
  Start = (47937,8249.61,0)
FEATURE [Part::Part2DObjectPython] DWire133  # Draft 2D object (typed FeaturePython)
  ChamferSize = 0
  Closed = true
  End = (46587,8549.61,0)
  FilletRadius = 0
  Length = 900
  MakeFace = true
  Placement = pos=(21088.6,-7600,0) rot=(0,0,1;0rad)
  Points = (4) [(25498.4,15849.6,0),(25648.4,15849.6,0),(25648.4,16149.6,0),(25498.4,16149.6,0)]
  Start = (46587,8249.61,0)
FEATURE [Part::Part2DObjectPython] DWire134  # Draft 2D object (typed FeaturePython)
  ChamferSize = 0
  Closed = true
  End = (52987,13019.6,0)
  FilletRadius = 0
  Length = 900
  MakeFace = true
  Placement = pos=(27488.6,-3130,0) rot=(0,0,1;0rad)
  Points = (4) [(25498.4,15849.6,0),(25648.4,15849.6,0),(25648.4,16149.6,0),(25498.4,16149.6,0)]
  Start = (52987,12719.6,0)
FEATURE [Part::Part2DObjectPython] DWire135  # Draft 2D object (typed FeaturePython)
  ChamferSize = 0
  Closed = true
  End = (45237,6049.61,0)
  FilletRadius = 0
  Length = 900
  MakeFace = true
  Placement = pos=(19738.6,-10100,0) rot=(0,0,1;0rad)
  Points = (4) [(25498.4,15849.6,0),(25648.4,15849.6,0),(25648.4,16149.6,0),(25498.4,16149.6,0)]
  Start = (45237,5749.61,0)
FEATURE [Part::Part2DObjectPython] DWire136  # Draft 2D object (typed FeaturePython)
  ChamferSize = 0
  Closed = true
  End = (42137,6049.61,0)
  FilletRadius = 0
  Length = 900
  MakeFace = true
  Placement = pos=(16638.6,-10100,0) rot=(0,0,1;0rad)
  Points = (4) [(25498.4,15849.6,0),(25648.4,15849.6,0),(25648.4,16149.6,0),(25498.4,16149.6,0)]
  Start = (42137,5749.61,0)
FEATURE [Part::Part2DObjectPython] DWire137  # Draft 2D object (typed FeaturePython)
  ChamferSize = 0
  Closed = true
  End = (47937,6049.61,0)
  FilletRadius = 0
  Length = 900
  MakeFace = true
  Placement = pos=(22438.6,-10100,0) rot=(0,0,1;0rad)
  Points = (4) [(25498.4,15849.6,0),(25648.4,15849.6,0),(25648.4,16149.6,0),(25498.4,16149.6,0)]
  Start = (47937,5749.61,0)
FEATURE [Part::Part2DObjectPython] DWire138  # Draft 2D object (typed FeaturePython)
  ChamferSize = 0
  Closed = true
  End = (42137,8549.61,0)
  FilletRadius = 0
  Length = 900
  MakeFace = true
  Placement = pos=(16638.6,-7600,0) rot=(0,0,1;0rad)
  Points = (4) [(25498.4,15849.6,0),(25648.4,15849.6,0),(25648.4,16149.6,0),(25498.4,16149.6,0)]
  Start = (42137,8249.61,0)
FEATURE [Part::Part2DObjectPython] DWire139  # Draft 2D object (typed FeaturePython)
  ChamferSize = 0
  Closed = true
  End = (45237,2149.61,0)
  FilletRadius = 0
  Length = 900
  MakeFace = true
  Placement = pos=(19738.6,-14000,0) rot=(0,0,1;0rad)
  Points = (4) [(25498.4,15849.6,0),(25648.4,15849.6,0),(25648.4,16149.6,0),(25498.4,16149.6,0)]
  Start = (45237,1849.61,0)
FEATURE [Part::Part2DObjectPython] DWire140  # Draft 2D object (typed FeaturePython)
  ChamferSize = 0
  Closed = true
  End = (52987,6049.61,0)
  FilletRadius = 0
  Length = 900
  MakeFace = true
  Placement = pos=(27488.6,-10100,0) rot=(0,0,1;0rad)
  Points = (4) [(25498.4,15849.6,0),(25648.4,15849.6,0),(25648.4,16149.6,0),(25498.4,16149.6,0)]
  Start = (52987,5749.61,0)
FEATURE [Part::Part2DObjectPython] DWire141  # Draft 2D object (typed FeaturePython)
  ChamferSize = 0
  Closed = true
  End = (42137,2149.61,0)
  FilletRadius = 0
  Length = 900
  MakeFace = true
  Placement = pos=(16638.6,-14000,0) rot=(0,0,1;0rad)
  Points = (4) [(25498.4,15849.6,0),(25648.4,15849.6,0),(25648.4,16149.6,0),(25498.4,16149.6,0)]
  Start = (42137,1849.61,0)
FEATURE [Part::Part2DObjectPython] DWire142  # Draft 2D object (typed FeaturePython)
  ChamferSize = 0
  Closed = true
  End = (47937,2149.61,0)
  FilletRadius = 0
  Length = 900
  MakeFace = true
  Placement = pos=(22438.6,-14000,0) rot=(0,0,1;0rad)
  Points = (4) [(25498.4,15849.6,0),(25648.4,15849.6,0),(25648.4,16149.6,0),(25498.4,16149.6,0)]
  Start = (47937,1849.61,0)
FEATURE [App::DocumentObjectGroup] Group022  label="A-Columns level 2"
  Group = -> [DWire123,DWire124,DWire125,DWire126,DWire127,DWire128,DWire129,DWire130,DWire131,DWire132,DWire133,DWire134,DWire135,DWire136,DWire137,DWire138,DWire139,DWire140,DWire141,DWire142]
FEATURE [Part::Part2DObjectPython] DWire143  # Draft 2D object (typed FeaturePython)
  ChamferSize = 0
  Closed = true
  End = (46737,15999.6,0)
  FilletRadius = 0
  Length = 4000
  MakeFace = true
  Placement = pos=(0,-0.388761,0) rot=(0,0,1;0rad)
  Points = (6) [(45387,16000,0),(45387,15850,0),(46587,15850,0),(46587,15350,0),(46737,15350,0),(46737,16000,0)]
  Start = (45387,15999.6,0)
FEATURE [Part::Part2DObjectPython] DWire144  # Draft 2D object (typed FeaturePython)
  ChamferSize = 0
  Closed = true
  End = (42287,8399.61,0)
  FilletRadius = 0
  Length = 6700.34
  MakeFace = true
  Placement = pos=(0,-0.388761,0) rot=(0,0,1;0rad)
  Points = (6) [(45387,8400,0),(45387,8149.83,0),(45237,8149.83,0),(45237,8250,0),(42287,8250,0),(42287,8400,0)]
  Start = (45387,8399.61,0)
FEATURE [Part::Part2DObjectPython] Rectangle051  # Draft 2D object (typed FeaturePython)
  ChamferSize = 0
  FilletRadius = 0
  Height = -2200
  Length = 2950
  MakeFace = true
  Placement = pos=(42287,8249.61,0) rot=(0,0,1;0rad)
FEATURE [Part::Part2DObjectPython] DWire145  # Draft 2D object (typed FeaturePython)
  ChamferSize = 0
  Closed = true
  End = (65360.2,9965.75,-0.0145023)
  FilletRadius = 0
  Length = 13133.9
  MakeFace = true
  Points = (38) [(65095.4,9965.75,-0.0145023),(65095.4,10145.8,-0.0145023),(65360.2,10145.8,-0.0145023),(65360.2,10325.8,-0.0145023),(65625,10325.8,-0.0145023),+33 more]
  Start = (65095.4,9965.75,-0.0145023)
FEATURE [Part::Part2DObjectPython] DWire146  # Draft 2D object (typed FeaturePython)
  ChamferSize = 0
  Closed = true
  End = (69447,12665.8,-0.0145023)
  FilletRadius = 0
  Length = 5700
  MakeFace = true
  Points = (4) [(69597,12665.8,-0.0145023),(69597,9965.75,-0.0145023),(69447,9965.75,-0.0145023),(69447,12665.8,-0.0145023)]
  Start = (69597,12665.8,-0.0145023)
FEATURE [Part::Part2DObjectPython] DWire147  # Draft 2D object (typed FeaturePython)
  ChamferSize = 0
  Closed = true
  End = (69597,12765.8,-0.0145023)
  FilletRadius = 0
  Length = 6360
  MakeFace = true
  Points = (4) [(69597,12965.8,-0.0145023),(72577,12965.8,-0.0145023),(72577,12765.8,-0.0145023),(69597,12765.8,-0.0145023)]
  Start = (69597,12965.8,-0.0145023)
FEATURE [Part::Part2DObjectPython] DWire148  # Draft 2D object (typed FeaturePython)
  ChamferSize = 0
  Closed = true
  End = (58577,12765.8,-0.0147835)
  FilletRadius = 0
  Length = 13200
  MakeFace = true
  Points = (4) [(58577,12965.8,-0.0147835),(64977,12965.8,-0.0147835),(64977,12765.8,-0.0147835),(58577,12765.8,-0.0147835)]
  Start = (58577,12965.8,-0.0147835)
FEATURE [Part::Part2DObjectPython] DWire149  # Draft 2D object (typed FeaturePython)
  ChamferSize = 0
  Closed = true
  End = (58577,15765.8,-0.0147835)
  FilletRadius = 0
  Length = 28400
  MakeFace = true
  Points = (4) [(58577,15965.8,-0.0147835),(72577,15965.8,-0.0147835),(72577,15765.8,-0.0147835),(58577,15765.8,-0.0147835)]
  Start = (58577,15965.8,-0.0147835)
FEATURE [Part::Part2DObjectPython] DWire150  # Draft 2D object (typed FeaturePython)
  ChamferSize = 0
  Closed = true
  End = (64827,12965.8,-0.0147835)
  FilletRadius = 0
  Length = 2300
  MakeFace = true
  Points = (4) [(64827,13965.8,-0.0147835),(64977,13965.8,-0.0147835),(64977,12965.8,-0.0147835),(64827,12965.8,-0.0147835)]
  Start = (64827,13965.8,-0.0147835)
FEATURE [Part::Part2DObjectPython] DWire151  # Draft 2D object (typed FeaturePython)
  ChamferSize = 0
  Closed = true
  End = (64977,12765.8,-0.0147835)
  FilletRadius = 0
  Length = 1280
  MakeFace = true
  Points = (4) [(64827,12765.8,-0.0147835),(64827,12275.8,-0.0147835),(64977,12275.8,-0.0147835),(64977,12765.8,-0.0147835)]
  Start = (64827,12765.8,-0.0147835)
FEATURE [Part::Part2DObjectPython] DWire152  # Draft 2D object (typed FeaturePython)
  ChamferSize = 0
  Closed = true
  End = (62627,12765.8,-0.0147835)
  FilletRadius = 0
  Length = 1280
  MakeFace = true
  Points = (4) [(62477,12765.8,-0.0147835),(62477,12275.8,-0.0147835),(62627,12275.8,-0.0147835),(62627,12765.8,-0.0147835)]
  Start = (62477,12765.8,-0.0147835)
FEATURE [Part::Part2DObjectPython] DWire153  # Draft 2D object (typed FeaturePython)
  ChamferSize = 0
  Closed = true
  End = (58727,12765.8,-0.0147835)
  FilletRadius = 0
  Length = 1280
  MakeFace = true
  Points = (4) [(58577,12765.8,-0.0147835),(58577,12275.8,-0.0147835),(58727,12275.8,-0.0147835),(58727,12765.8,-0.0147835)]
  Start = (58577,12765.8,-0.0147835)
FEATURE [Part::Part2DObjectPython] DWire154  # Draft 2D object (typed FeaturePython)
  ChamferSize = 0
  Closed = true
  End = (59577,12765.8,-0.0147835)
  FilletRadius = 0
  Length = 1900
  MakeFace = true
  Points = (4) [(59427,12765.8,-0.0147835),(59427,11965.8,-0.0147835),(59577,11965.8,-0.0147835),(59577,12765.8,-0.0147835)]
  Start = (59427,12765.8,-0.0147835)
FEATURE [Part::Part2DObjectPython] DWire155  # Draft 2D object (typed FeaturePython)
  ChamferSize = 0
  Closed = true
  End = (58727,15765.8,-0.0147835)
  FilletRadius = 0
  Length = 5900
  MakeFace = true
  Points = (4) [(58577,15765.8,-0.0147835),(58577,12965.8,-0.0147835),(58727,12965.8,-0.0147835),(58727,15765.8,-0.0147835)]
  Start = (58577,15765.8,-0.0147835)
FEATURE [Part::Part2DObjectPython] DWire156  # Draft 2D object (typed FeaturePython)
  ChamferSize = 0
  Closed = true
  End = (62627,15765.8,-0.0147835)
  FilletRadius = 0
  Length = 1900
  MakeFace = true
  Points = (4) [(62477,15765.8,-0.0147835),(62477,14965.8,-0.0147835),(62627,14965.8,-0.0147835),(62627,15765.8,-0.0147835)]
  Start = (62477,15765.8,-0.0147835)
FEATURE [Part::Part2DObjectPython] DWire158  # Draft 2D object (typed FeaturePython)
  ChamferSize = 0
  Closed = true
  End = (72427,12965.8,-0.0147835)
  FilletRadius = 0
  Length = 2300
  MakeFace = true
  Points = (4) [(72427,13965.8,-0.0147835),(72577,13965.8,-0.0147835),(72577,12965.8,-0.0147835),(72427,12965.8,-0.0147835)]
  Start = (72427,13965.8,-0.0147835)
FEATURE [Part::Part2DObjectPython] DWire159  # Draft 2D object (typed FeaturePython)
  ChamferSize = 0
  Closed = true
  End = (72427,9965.85,-0.0147835)
  FilletRadius = 0
  Length = 5900
  MakeFace = true
  Points = (4) [(72427,12765.8,-0.0147835),(72577,12765.8,-0.0147835),(72577,9965.85,-0.0147835),(72427,9965.85,-0.0147835)]
  Start = (72427,12765.8,-0.0147835)
FEATURE [Part::Part2DObjectPython] DWire160  # Draft 2D object (typed FeaturePython)
  ChamferSize = 0
  Closed = true
  End = (52987,11699.6,0)
  FilletRadius = 0
  Length = 10100
  MakeFace = true
  Placement = pos=(0,-0.388761,0) rot=(0,0,1;0rad)
  Points = (4) [(49437,11700,0),(49437,10200,0),(52987,10200,0),(52987,11700,0)]
  Start = (49437,11699.6,0)
FEATURE [Part::Part2DObjectPython] DWire161  # Draft 2D object (typed FeaturePython)
  ChamferSize = 0
  Closed = true
  End = (49437,8399.61,0)
  FilletRadius = 0
  Length = 15100
  MakeFace = true
  Placement = pos=(0,-0.388761,0) rot=(0,0,1;0rad)
  Points = (6) [(49437,10050,0),(52987,10050,0),(52987,6050,0),(50037,6050,0),(50037,8400,0),(49437,8400,0)]
  Start = (49437,10049.6,0)
FEATURE [Part::Part2DObjectPython] DWire162  # Draft 2D object (typed FeaturePython)
  ChamferSize = 0
  Closed = true
  End = (46587,11999.6,0)
  FilletRadius = 0
  Length = 13100
  MakeFace = true
  Placement = pos=(0,-0.388761,0) rot=(0,0,1;0rad)
  Points = (6) [(45312,12000,0),(45312,11400,0),(42287,11400,0),(42287,9750,0),(46587,9750,0),(46587,12000,0)]
  Start = (45312,11999.6,0)
FEATURE [Part::Part2DObjectPython] DWire163  # Draft 2D object (typed FeaturePython)
  ChamferSize = 0
  Closed = true
  End = (46587,12149.6,0)
  FilletRadius = 0
  Length = 16000
  MakeFace = true
  Placement = pos=(0,-0.388761,0) rot=(0,0,1;0rad)
  Points = (4) [(46587,15850,0),(42287,15850,0),(42287,12150,0),(46587,12150,0)]
  Start = (46587,15849.6,0)
FEATURE [Part::Part2DObjectPython] DWire164  # Draft 2D object (typed FeaturePython)
  ChamferSize = 0
  Closed = true
  End = (46737,15349.6,0)
  FilletRadius = 0
  Length = 27700
  MakeFace = true
  Placement = pos=(0,-0.388761,0) rot=(0,0,1;0rad)
  Points = (10) [(46587,15350,0),(46587,13020,0),(48087,13020,0),(48087,8250,0),(46737,8250,0),(46737,6050,0),(49287,6050,0),(49287,15850,0),(46737,15850,0),+1 more]
  Start = (46587,15349.6,0)
FEATURE [Part::Part2DObjectPython] Line484  # Draft 2D object (typed FeaturePython)
  ChamferSize = 0
  Closed = false
  End = (50037,15849.6,0)
  FilletRadius = 0
  Length = 2200
  MakeFace = true
  Points = (2) [(50037,13649.6,0),(50037,15849.6,0)]
  Start = (50037,13649.6,0)
FEATURE [Part::Part2DObjectPython] Line485  # Draft 2D object (typed FeaturePython)
  ChamferSize = 0
  Closed = false
  End = (50037,6049.61,0)
  FilletRadius = 0
  Length = 2200
  MakeFace = true
  Points = (2) [(50037,8249.61,0),(50037,6049.61,0)]
  Start = (50037,8249.61,0)
FEATURE [Part::Part2DObjectPython] DWire165  # Draft 2D object (typed FeaturePython)
  ChamferSize = 0
  Closed = true
  End = (52987,15849.6,0)
  FilletRadius = 0
  Length = 15100
  MakeFace = true
  Points = (6) [(50037,15849.6,0),(50037,13499.6,0),(49437,13499.6,0),(49437,11849.6,0),(52987,11849.6,0),(52987,15849.6,0)]
  Start = (50037,15849.6,0)
FEATURE [Part::Part2DObjectPython] Line486  # Draft 2D object (typed FeaturePython)
  ChamferSize = 0
  Closed = false
  End = (46587,9049.61,0)
  FilletRadius = 0
  Length = 4300
  MakeFace = true
  Points = (2) [(42287,9049.61,0),(46587,9049.61,0)]
  Start = (42287,9049.61,0)
FEATURE [Part::Part2DObjectPython] DWire166  # Draft 2D object (typed FeaturePython)
  ChamferSize = 0
  Closed = true
  End = (45387,5749.61,0)
  FilletRadius = 0
  Length = 19100
  MakeFace = true
  Points = (8) [(45387,5899.61,0),(47937,5899.61,0),(47937,2149.61,0),(42287,2149.61,0),(42287,5899.61,0),(45237,5899.61,0),(45237,5749.61,0),(45387,5749.61,0)]
  Start = (45387,5899.61,0)
FEATURE [Part::Part2DObjectPython] DWire167  # Draft 2D object (typed FeaturePython)
  ChamferSize = 0
  Closed = true
  End = (46587,9049.61,0)
  FilletRadius = 0
  Length = 14900
  MakeFace = true
  Points = (6) [(42287,9049.61,0),(42287,8399.61,0),(45387,8399.61,0),(45387,5899.61,0),(46587,5899.61,0),(46587,9049.61,0)]
  Start = (42287,9049.61,0)
FEATURE [Part::Part2DObjectPython] DWire168  # Draft 2D object (typed FeaturePython)
  ChamferSize = 0
  Closed = true
  End = (48087,1999.61,0)
  FilletRadius = 0
  Length = 17900
  MakeFace = true
  Points = (8) [(48087,5899.61,0),(52987,5899.61,0),(52987,5749.61,0),(53137,5749.61,0),(53137,2149.61,0),(52987,2149.61,0),(52987,1999.61,0),(48087,1999.61,0)]
  Start = (48087,5899.61,0)
FEATURE [Part::Part2DObjectPython] DWire169  # Draft 2D object (typed FeaturePython)
  ChamferSize = 0
  Closed = true
  End = (28598.4,15999.6,0)
  FilletRadius = 0
  Length = 12159.7
  MakeFace = true
  Points = (6) [(25648.4,15999.6,0),(25648.4,15849.6,0),(25498.4,15849.6,0),(25498.4,13019.6,0),(28598,13019.6,0),(28598.4,15999.6,0)]
  Start = (25648.4,15999.6,0)
FEATURE [Part::Part2DObjectPython] DWire170  # Draft 2D object (typed FeaturePython)
  ChamferSize = 0
  Closed = true
  End = (34298.4,15849.6,0)
  FilletRadius = 0
  Length = 16760.3
  MakeFace = true
  Points = (4) [(28748.4,15849.6,0),(28748,13019.6,0),(34298.4,13019.6,0),(34298.4,15849.6,0)]
  Start = (28748.4,15849.6,0)
FEATURE [Part::Part2DObjectPython] DWire171  # Draft 2D object (typed FeaturePython)
  ChamferSize = 0
  Closed = true
  End = (36348.4,15849.6,0)
  FilletRadius = 0
  Length = 9460
  MakeFace = true
  Points = (4) [(34448.4,15849.6,0),(34448.4,13019.6,0),(36348.4,13019.6,0),(36348.4,15849.6,0)]
  Start = (34448.4,15849.6,0)
FEATURE [Part::Part2DObjectPython] DWire172  # Draft 2D object (typed FeaturePython)
  ChamferSize = 0
  Closed = true
  End = (25648.4,9749.61,0)
  FilletRadius = 0
  Length = 14840
  MakeFace = true
  Points = (4) [(25648.4,12869.6,0),(29948.4,12869.6,0),(29948.4,9749.61,0),(25648.4,9749.61,0)]
  Start = (25648.4,12869.6,0)
FEATURE [Part::Part2DObjectPython] DWire173  # Draft 2D object (typed FeaturePython)
  ChamferSize = 0
  Closed = true
  End = (28598.4,9599.61,0)
  FilletRadius = 0
  Length = 8300
  MakeFace = true
  Points = (4) [(25648.4,9599.61,0),(25648.4,8399.61,0),(28598.4,8399.61,0),(28598.4,9599.61,0)]
  Start = (25648.4,9599.61,0)
FEATURE [Part::Part2DObjectPython] DWire174  # Draft 2D object (typed FeaturePython)
  ChamferSize = 0
  Closed = true
  End = (28598.4,8249.61,0)
  FilletRadius = 0
  Length = 9100
  MakeFace = true
  Points = (4) [(25648.4,8249.61,0),(25648.4,6649.61,0),(28598.4,6649.61,0),(28598.4,8249.61,0)]
  Start = (25648.4,8249.61,0)
FEATURE [Part::Part2DObjectPython] DWire175  # Draft 2D object (typed FeaturePython)
  ChamferSize = 0
  Closed = true
  End = (28598.4,4649.61,0)
  FilletRadius = 0
  Length = 14600
  MakeFace = true
  Points = (6) [(28598.4,6499.61,0),(25648.4,6499.61,0),(25648.4,2149.61,0),(27998.4,2149.61,0),(27998.4,4649.61,0),(28598.4,4649.61,0)]
  Start = (28598.4,6499.61,0)
FEATURE [Part::Part2DObjectPython] DWire176  # Draft 2D object (typed FeaturePython)
  ChamferSize = 0
  Closed = true
  End = (31448.4,12869.6,0)
  FilletRadius = 0
  Length = 31240
  MakeFace = true
  Points = (4) [(31448.4,2149.61,0),(36348.4,2149.61,0),(36348.4,12869.6,0),(31448.4,12869.6,0)]
  Start = (31448.4,2149.61,0)
FEATURE [Part::Part2DObjectPython] DWire177  # Draft 2D object (typed FeaturePython)
  ChamferSize = 0
  Closed = true
  End = (28748.4,9599.61,0)
  FilletRadius = 0
  Length = 18300
  MakeFace = true
  Points = (6) [(28748.4,2999.61,0),(31298.4,2999.61,0),(31298.4,8249.61,0),(29948.4,8249.61,0),(29948.4,9599.61,0),(28748.4,9599.61,0)]
  Start = (28748.4,2999.61,0)
FEATURE [Part::Part2DObjectPython] DWire178  # Draft 2D object (typed FeaturePython)
  ChamferSize = 0
  Closed = true
  End = (31298.4,12869.6,0)
  FilletRadius = 0
  Length = 11640
  MakeFace = true
  Points = (4) [(31298.4,8249.61,0),(30098.4,8249.61,0),(30098.4,12869.6,0),(31298.4,12869.6,0)]
  Start = (31298.4,8249.61,0)
FEATURE [Part::Part2DObjectPython] DWire179  # Draft 2D object (typed FeaturePython)
  ChamferSize = 0
  Closed = true
  End = (47937,13019.6,0)
  FilletRadius = 0
  Length = 11640
  MakeFace = true
  Placement = pos=(16638.6,150,0) rot=(0,0,1;0rad)
  Points = (4) [(31298.4,8249.61,0),(30098.4,8249.61,0),(30098.4,12869.6,0),(31298.4,12869.6,0)]
  Start = (47937,8399.61,0)
FEATURE [App::DocumentObjectGroup] Group023  label="Color Plan"
  Group = -> [Rectangle051,DWire160,DWire161,DWire162,DWire163,DWire164,Line484,Line485,DWire165,Line486,DWire166,DWire167,DWire168,DWire169,DWire170,DWire171,DWire172,DWire173,DWire174,DWire175,DWire176,DWire177,DWire178,DWire179]
FEATURE [App::DocumentObjectGroup] Group024  label="text LEVEL 2"
  Group = -> [Text,Text001,Text002,Text003,Text004,Text005,Text006]
FEATURE [App::DocumentObjectGroup] Group025  label="wall fill"
  Group = -> [DWire053,DWire054,DWire055,DWire056,DWire057,DWire058,DWire059,DWire060,DWire061,DWire062,DWire064,DWire065,DWire066,DWire067,DWire068,DWire069,DWire070,DWire071,DWire072,DWire073,DWire074,DWire075,DWire143,DWire144]
FEATURE [App::DocumentObjectGroup] Group017  label="Level 2 Floor"
  Group = -> [Group024,Group025,Group022]
FEATURE [App::DocumentObjectGroup] Group026  label="wall fill level 1"
  Group = -> [DWire077,DWire078,DWire079,DWire080,DWire081,DWire082,DWire083,DWire090,DWire091,DWire092,DWire093,DWire094,DWire095,DWire096,DWire097,DWire098,DWire099,DWire100,DWire101,DWire102]
FEATURE [App::Annotation] Text007
  LabelText = LIVING ROOM
  Position = (33329,5774.86,0)
FEATURE [App::Annotation] Text008
  LabelText = DINNING AREA
  Position = (32970.3,11297.2,0)
FEATURE [App::Annotation] Text009
  LabelText = FOYER / ENTRY
  Position = (29356.5,3189.98,0)
FEATURE [App::Annotation] Text010
  LabelText = GUEST BED ROOM 4
  Position = (26026.6,5685.67,0)
FEATURE [App::Annotation] Text011
  LabelText = GUEST BATHROOM
  Position = (26015.3,7496.14,0)
FEATURE [App::Annotation] Text012
  LabelText = TOILET
  Position = (26545.4,9001.71,0)
FEATURE [App::Annotation] Text013
  LabelText = UTILITY ROOM / WASHROOM
  Position = (26084.7,11328.5,0)
FEATURE [App::Annotation] Text014
  LabelText = KITCHEN
  Position = (30794.7,14413,0)
FEATURE [App::Annotation] Text015
  LabelText = STORAGE
  Position = (34894.5,14442.4,0)
FEATURE [Part::Part2DObjectPython] Line487  # Draft 2D object (typed FeaturePython)
  ChamferSize = 0
  Closed = false
  End = (38503.4,15999.6,0)
  FilletRadius = 0
  Length = 15000
  MakeFace = true
  Placement = pos=(25503.4,-0.388761,0) rot=(0,0,1;0rad)
  Points = (2) [(-2000,16000,0),(13000,16000,0)]
  Start = (23503.4,15999.6,0)
FEATURE [Part::Part2DObjectPython] Line488  # Draft 2D object (typed FeaturePython)
  ChamferSize = 0
  Closed = false
  End = (23503.4,12869.6,0)
  FilletRadius = 0
  Length = 15000
  MakeFace = true
  Placement = pos=(25503.4,-0.388761,0) rot=(0,0,1;0rad)
  Points = (2) [(13000,12870,0),(-2000,12870,0)]
  Start = (38503.4,12869.6,0)
FEATURE [Part::Part2DObjectPython] Line489  # Draft 2D object (typed FeaturePython)
  ChamferSize = 0
  Closed = false
  End = (23503.4,8399.61,0)
  FilletRadius = 0
  Length = 15000
  MakeFace = true
  Placement = pos=(25503.4,-0.388761,0) rot=(0,0,1;0rad)
  Points = (2) [(13000,8400,0),(-2000,8400,0)]
  Start = (38503.4,8399.61,0)
FEATURE [Part::Part2DObjectPython] Line490  # Draft 2D object (typed FeaturePython)
  ChamferSize = 0
  Closed = false
  End = (23503.4,5899.61,0)
  FilletRadius = 0
  Length = 15000
  MakeFace = true
  Placement = pos=(25503.4,-0.388761,0) rot=(0,0,1;0rad)
  Points = (2) [(13000,5900,0),(-2000,5900,0)]
  Start = (38503.4,5899.61,0)
FEATURE [Part::Part2DObjectPython] Line491  # Draft 2D object (typed FeaturePython)
  ChamferSize = 0
  Closed = false
  End = (23503.4,1999.61,0)
  FilletRadius = 0
  Length = 15000
  MakeFace = true
  Placement = pos=(25503.4,-0.388761,0) rot=(0,0,1;0rad)
  Points = (2) [(13000,2000,0),(-2000,2000,0)]
  Start = (38503.4,1999.61,0)
FEATURE [Part::Part2DObjectPython] Line492  # Draft 2D object (typed FeaturePython)
  ChamferSize = 0
  Closed = false
  End = (25573.4,16999.6,0)
  FilletRadius = 0
  Length = 17000
  MakeFace = true
  Placement = pos=(25503.4,-0.388761,0) rot=(0,0,1;0rad)
  Points = (2) [(70,0,0),(70,17000,0)]
  Start = (25573.4,-0.388761,0)
FEATURE [Part::Part2DObjectPython] Line493  # Draft 2D object (typed FeaturePython)
  ChamferSize = 0
  Closed = false
  End = (28673.4,-0.388761,0)
  FilletRadius = 0
  Length = 17000
  MakeFace = true
  Placement = pos=(25503.4,-0.388761,0) rot=(0,0,1;0rad)
  Points = (2) [(3170,17000,0),(3170,0,0)]
  Start = (28673.4,16999.6,0)
FEATURE [Part::Part2DObjectPython] Line494  # Draft 2D object (typed FeaturePython)
  ChamferSize = 0
  Closed = false
  End = (30023.4,-0.388761,0)
  FilletRadius = 0
  Length = 17000
  MakeFace = true
  Placement = pos=(25503.4,-0.388761,0) rot=(0,0,1;0rad)
  Points = (2) [(4520,17000,0),(4520,0,0)]
  Start = (30023.4,16999.6,0)
FEATURE [Part::Part2DObjectPython] Line495  # Draft 2D object (typed FeaturePython)
  ChamferSize = 0
  Closed = false
  End = (31373.4,-0.388761,0)
  FilletRadius = 0
  Length = 17000
  MakeFace = true
  Placement = pos=(25503.4,-0.388761,0) rot=(0,0,1;0rad)
  Points = (2) [(5870,17000,0),(5870,0,0)]
  Start = (31373.4,16999.6,0)
FEATURE [Part::Part2DObjectPython] Line496  # Draft 2D object (typed FeaturePython)
  ChamferSize = 0
  Closed = false
  End = (36423.4,-0.388761,0)
  FilletRadius = 0
  Length = 17000
  MakeFace = true
  Placement = pos=(25503.4,-0.388761,0) rot=(0,0,1;0rad)
  Points = (2) [(10920,17000,0),(10920,0,0)]
  Start = (36423.4,16999.6,0)
FEATURE [Part::Part2DObjectPython] Line497  # Draft 2D object (typed FeaturePython)
  ChamferSize = 0
  Closed = false
  End = (55142,15999.6,0)
  FilletRadius = 0
  Length = 15000
  MakeFace = true
  Placement = pos=(42142,-0.388761,0) rot=(0,0,1;0rad)
  Points = (2) [(-2000,16000,0),(13000,16000,0)]
  Start = (40142,15999.6,0)
FEATURE [Part::Part2DObjectPython] Line498  # Draft 2D object (typed FeaturePython)
  ChamferSize = 0
  Closed = false
  End = (40142,12869.6,0)
  FilletRadius = 0
  Length = 15000
  MakeFace = true
  Placement = pos=(42142,-0.388761,0) rot=(0,0,1;0rad)
  Points = (2) [(13000,12870,0),(-2000,12870,0)]
  Start = (55142,12869.6,0)
FEATURE [Part::Part2DObjectPython] Line499  # Draft 2D object (typed FeaturePython)
  ChamferSize = 0
  Closed = false
  End = (40142,1999.61,0)
  FilletRadius = 0
  Length = 15000
  MakeFace = true
  Placement = pos=(42142,-0.388761,0) rot=(0,0,1;0rad)
  Points = (2) [(13000,2000,0),(-2000,2000,0)]
  Start = (55142,1999.61,0)
FEATURE [Part::Part2DObjectPython] Line500  # Draft 2D object (typed FeaturePython)
  ChamferSize = 0
  Closed = false
  End = (40142,8399.61,0)
  FilletRadius = 0
  Length = 15000
  MakeFace = true
  Placement = pos=(42142,-0.388761,0) rot=(0,0,1;0rad)
  Points = (2) [(13000,8400,0),(-2000,8400,0)]
  Start = (55142,8399.61,0)
FEATURE [Part::Part2DObjectPython] Line501  # Draft 2D object (typed FeaturePython)
  ChamferSize = 0
  Closed = false
  End = (40142,5899.61,0)
  FilletRadius = 0
  Length = 15000
  MakeFace = true
  Placement = pos=(42142,-0.388761,0) rot=(0,0,1;0rad)
  Points = (2) [(13000,5900,0),(-2000,5900,0)]
  Start = (55142,5899.61,0)
FEATURE [Part::Part2DObjectPython] Line502  # Draft 2D object (typed FeaturePython)
  ChamferSize = 0
  Closed = false
  End = (46662,-0.388761,0)
  FilletRadius = 0
  Length = 17000
  MakeFace = true
  Placement = pos=(42142,-0.388761,0) rot=(0,0,1;0rad)
  Points = (2) [(4520,17000,0),(4520,0,0)]
  Start = (46662,16999.6,0)
FEATURE [Part::Part2DObjectPython] Line503  # Draft 2D object (typed FeaturePython)
  ChamferSize = 0
  Closed = false
  End = (45312,-0.388761,0)
  FilletRadius = 0
  Length = 17000
  MakeFace = true
  Placement = pos=(42142,-0.388761,0) rot=(0,0,1;0rad)
  Points = (2) [(3170,17000,0),(3170,0,0)]
  Start = (45312,16999.6,0)
FEATURE [Part::Part2DObjectPython] Line504  # Draft 2D object (typed FeaturePython)
  ChamferSize = 0
  Closed = false
  End = (42212,16999.6,0)
  FilletRadius = 0
  Length = 17000
  MakeFace = true
  Placement = pos=(42142,-0.388761,0) rot=(0,0,1;0rad)
  Points = (2) [(70,0,0),(70,17000,0)]
  Start = (42212,-0.388761,0)
FEATURE [Part::Part2DObjectPython] Line505  # Draft 2D object (typed FeaturePython)
  ChamferSize = 0
  Closed = false
  End = (48012,-0.388761,0)
  FilletRadius = 0
  Length = 17000
  MakeFace = true
  Placement = pos=(42142,-0.388761,0) rot=(0,0,1;0rad)
  Points = (2) [(5870,17000,0),(5870,0,0)]
  Start = (48012,16999.6,0)
FEATURE [Part::Part2DObjectPython] Line506  # Draft 2D object (typed FeaturePython)
  ChamferSize = 0
  Closed = false
  End = (53062,-0.388761,0)
  FilletRadius = 0
  Length = 17000
  MakeFace = true
  Placement = pos=(42142,-0.388761,0) rot=(0,0,1;0rad)
  Points = (2) [(10920,17000,0),(10920,0,0)]
  Start = (53062,16999.6,0)
FEATURE [Part::Part2DObjectPython] Circle001  # Draft 2D object (typed FeaturePython)
  FirstAngle = 0
  LastAngle = 0
  MakeFace = false
  Placement = pos=(36423.4,17249.6,0) rot=(0,0,-1;1.5708rad)
  Radius = 250
FEATURE [Part::Part2DObjectPython] Clone2D001  label="Clone of Circle001 (2D)"  # Draft 2D object (typed FeaturePython)
  Objects = -> [Circle001]
  Placement = pos=(38749.9,15999.6,0) rot=(0,0,-1;1.5708rad)
  Scale = (1,1,1)
FEATURE [Part::Part2DObjectPython] Clone2D002  label="Clone of Circle001 (2D)001"  # Draft 2D object (typed FeaturePython)
  Objects = -> [Circle001]
  Placement = pos=(38749.9,8399.61,0) rot=(0,0,-1;1.5708rad)
  Scale = (1,1,1)
FEATURE [Part::Part2DObjectPython] Clone2D003  label="Clone of Circle001 (2D)002"  # Draft 2D object (typed FeaturePython)
  Objects = -> [Circle001]
  Placement = pos=(38749.9,5899.61,0) rot=(0,0,-1;1.5708rad)
  Scale = (1,1,1)
FEATURE [Part::Part2DObjectPython] Clone2D004  label="Clone of Circle001 (2D)003"  # Draft 2D object (typed FeaturePython)
  Objects = -> [Circle001]
  Placement = pos=(38749.9,12869.6,0) rot=(0,0,-1;1.5708rad)
  Scale = (1,1,1)
FEATURE [Part::Part2DObjectPython] Clone2D006  label="Clone of Circle001 (2D)005"  # Draft 2D object (typed FeaturePython)
  Objects = -> [Circle001]
  Placement = pos=(38749.9,1999.61,0) rot=(0,0,-1;1.5708rad)
  Scale = (1,1,1)
FEATURE [Part::Part2DObjectPython] Clone2D007  label="Clone of Circle001 (2D)006"  # Draft 2D object (typed FeaturePython)
  Objects = -> [Circle001]
  Placement = pos=(25573.4,17249.6,0) rot=(0,0,-1;1.5708rad)
  Scale = (1,1,1)
FEATURE [Part::Part2DObjectPython] Clone2D008  label="Clone of Circle001 (2D)007"  # Draft 2D object (typed FeaturePython)
  Objects = -> [Circle001]
  Placement = pos=(28673.4,17249.6,0) rot=(0,0,-1;1.5708rad)
  Scale = (1,1,1)
FEATURE [Part::Part2DObjectPython] Clone2D009  label="Clone of Circle001 (2D)008"  # Draft 2D object (typed FeaturePython)
  Objects = -> [Circle001]
  Placement = pos=(30023.4,17249.6,0) rot=(0,0,-1;1.5708rad)
  Scale = (1,1,1)
FEATURE [Part::Part2DObjectPython] Clone2D010  label="Clone of Circle001 (2D)009"  # Draft 2D object (typed FeaturePython)
  Objects = -> [Circle001]
  Placement = pos=(31373.4,17249.6,0) rot=(0,0,-1;1.5708rad)
  Scale = (1,1,1)
FEATURE [Part::Part2DObjectPython] Clone2D011  label="Clone of Circle001 (2D)010"  # Draft 2D object (typed FeaturePython)
  Objects = -> [Circle001]
  Placement = pos=(53065.5,17249.6,0) rot=(0,0,-1;1.5708rad)
  Scale = (1,1,1)
FEATURE [Part::Part2DObjectPython] Clone2D012  label="Clone of Clone of Circle001 (2D)009 (2D)"  # Draft 2D object (typed FeaturePython)
  Objects = -> [Clone2D010]
  Placement = pos=(48015.5,17249.6,0) rot=(0,0,-1;1.5708rad)
  Scale = (1,1,1)
FEATURE [Part::Part2DObjectPython] Clone2D013  label="Clone of Clone of Circle001 (2D) (2D)"  # Draft 2D object (typed FeaturePython)
  Objects = -> [Clone2D001]
  Placement = pos=(55392,15999.6,0) rot=(0,0,-1;1.5708rad)
  Scale = (1,1,1)
FEATURE [Part::Part2DObjectPython] Clone2D014  label="Clone of Clone of Circle001 (2D)001 (2D)"  # Draft 2D object (typed FeaturePython)
  Objects = -> [Clone2D002]
  Placement = pos=(55392,8399.61,0) rot=(0,0,-1;1.5708rad)
  Scale = (1,1,1)
FEATURE [Part::Part2DObjectPython] Clone2D015  label="Clone of Clone of Circle001 (2D)002 (2D)"  # Draft 2D object (typed FeaturePython)
  Objects = -> [Clone2D003]
  Placement = pos=(55392,5899.61,0) rot=(0,0,-1;1.5708rad)
  Scale = (1,1,1)
FEATURE [Part::Part2DObjectPython] Clone2D016  label="Clone of Clone of Circle001 (2D)003 (2D)"  # Draft 2D object (typed FeaturePython)
  Objects = -> [Clone2D004]
  Placement = pos=(55392,12869.6,0) rot=(0,0,-1;1.5708rad)
  Scale = (1,1,1)
FEATURE [Part::Part2DObjectPython] Clone2D017  label="Clone of Clone of Circle001 (2D)005 (2D)"  # Draft 2D object (typed FeaturePython)
  Objects = -> [Clone2D006]
  Placement = pos=(55392,1999.61,0) rot=(0,0,-1;1.5708rad)
  Scale = (1,1,1)
FEATURE [Part::Part2DObjectPython] Clone2D018  label="Clone of Clone of Circle001 (2D)006 (2D)"  # Draft 2D object (typed FeaturePython)
  Objects = -> [Clone2D007]
  Placement = pos=(42215.5,17249.6,0) rot=(0,0,-1;1.5708rad)
  Scale = (1,1,1)
FEATURE [Part::Part2DObjectPython] Clone2D019  label="Clone of Clone of Circle001 (2D)007 (2D)"  # Draft 2D object (typed FeaturePython)
  Objects = -> [Clone2D008]
  Placement = pos=(45315.5,17249.6,0) rot=(0,0,-1;1.5708rad)
  Scale = (1,1,1)
FEATURE [Part::Part2DObjectPython] Clone2D020  label="Clone of Clone of Circle001 (2D)008 (2D)"  # Draft 2D object (typed FeaturePython)
  Objects = -> [Clone2D009]
  Placement = pos=(46665.5,17249.6,0) rot=(0,0,-1;1.5708rad)
  Scale = (1,1,1)
FEATURE [App::Annotation] Text016
  LabelText = A
  Position = (25492,17154.7,0)
FEATURE [App::Annotation] Text017
  LabelText = B
  Position = (28606.4,17156.4,0)
FEATURE [App::Annotation] Text018
  LabelText = C
  Position = (29978.4,17159.6,0)
FEATURE [App::Annotation] Text019
  LabelText = D
  Position = (31308.3,17154.9,0)
FEATURE [App::Annotation] Text020
  LabelText = E
  Position = (36360.9,17154.8,0)
FEATURE [App::Annotation] Text021
  LabelText = 1
  Position = (38728.7,15998.1,0)
FEATURE [App::Annotation] Text022
  LabelText = 2
  Position = (38728.9,12846.2,0)
FEATURE [App::Annotation] Text023
  LabelText = 3
  Position = (38644.2,8371.35,0)
FEATURE [App::Annotation] Text024
  LabelText = 4
  Position = (38651.2,5871.35,0)
FEATURE [App::Annotation] Text025
  LabelText = 5
  Position = (38663.8,1949.27,0)
FEATURE [App::DocumentObjectGroup] Group029  label="GRID TEXT"
  Group = -> [Text016,Text017,Text018,Text019,Text020,Text021,Text022,Text023,Text024,Text025]
FEATURE [App::DocumentObjectGroup] Group030  label="GRID CIRCLES"
  Group = -> [Circle001,Clone2D001,Clone2D002,Clone2D003,Clone2D004,Clone2D006,Clone2D007,Clone2D008,Clone2D009,Clone2D010,Clone2D011,Clone2D012,Clone2D013,Clone2D014,Clone2D015,Clone2D016,Clone2D017,Clone2D018,Clone2D019,Clone2D020]
FEATURE [App::DocumentObjectGroup] Group028  label="Axes grid lines"
  Group = -> [Line487,Line488,Line489,Line490,Line491,Line492,Line493,Line494,Line495,Line496,Line497,Line498,Line499,Line500,Line501,Line502,Line503,Line504,Line505,Line506,Group029,Group030]
FEATURE [App::Annotation] Text026
  LabelText = KITCHEN
  Position = (71122.4,11372.2,0)
FEATURE [App::Annotation] Text027
  LabelText = FOYER
  Position = (60037.7,11411.6,0)
FEATURE [App::Annotation] Text028
  LabelText = MASTER BEDROOM
  Position = (59329.8,14194.8,0)
FEATURE [Part::Feature] Clone2D021  label="Clone of Circle001 (2D)011"
  Placement = pos=(30409.3,17975.6,0) rot=(0,0,-1;1.5708rad)
  shape: bbox 500 x 500 x 2e-07 mm, 0 faces, 0 solids (baked)
FEATURE [Part::Part2DObjectPython] DWire180  # Draft 2D object (typed FeaturePython)
  ChamferSize = 0
  Closed = true
  End = (30159.3,17975.6,0)
  FilletRadius = 0
  Length = 1414.21
  MakeFace = true
  Placement = pos=(37.9277,0,0) rot=(0,0,1;0rad)
  Points = (6) [(30371.4,18225.6,0),(30420.9,18176.1,0),(30220.4,17975.6,0),(30420.9,17775.1,0),(30371.4,17725.6,0),(30121.4,17975.6,0)]
  Start = (30409.3,18225.6,0)
FEATURE [Part::Part2DObjectPython] Clone2D022  label="Clone of DWire180 (2D)"  # Draft 2D object (typed FeaturePython)
  Objects = -> [DWire180]
  Placement = pos=(37.9258,-18476,0) rot=(0,0,1;0rad)
  Scale = (1,1,1)
FEATURE [Part::FeaturePython] Clone036  label="Clone of Clone of Circle001 (2D)011"  # Draft clone (typed FeaturePython)
  Objects = -> [Clone2D021]
  Placement = pos=(30409.3,-500.383,0) rot=(0,0,-1;1.5708rad)
  Scale = (1,1,1)
FEATURE [Part::Feature] Clone037  label="Clone of Clone of Circle001 (2D)012"
  Placement = pos=(32049.8,-500.383,0) rot=(0,0,-1;1.5708rad)
  shape: bbox 500 x 500 x 2e-07 mm, 0 faces, 0 solids (baked)
FEATURE [Part::Feature] Clone2D023  label="Clone of Circle001 (2D)012"
  Placement = pos=(32049.8,17975.6,0) rot=(0,0,-1;1.5708rad)
  shape: bbox 500 x 500 x 2e-07 mm, 0 faces, 0 solids (baked)
FEATURE [Part::Feature] Clone2D024  label="Clone of DWire180 (2D)001"
  Placement = pos=(1678.46,-18476,0) rot=(0,0,1;0rad)
  shape: bbox 299.5 x 500 x 2e-07 mm, 1 faces, 0 solids (baked)
FEATURE [Part::Part2DObjectPython] DWire181  # Draft 2D object (typed FeaturePython)
  ChamferSize = 0
  Closed = true
  End = (31799.8,17975.6,0)
  FilletRadius = 0
  Length = 1414.21
  MakeFace = true
  Placement = pos=(1678.46,-0.000215769,0) rot=(0,0,1;0rad)
  Points = (6) [(30371.4,18225.6,0),(30420.9,18176.1,0),(30220.4,17975.6,0),(30420.9,17775.1,0),(30371.4,17725.6,0),(30121.4,17975.6,0)]
  Start = (32049.8,18225.6,0)
FEATURE [Part::Part2DObjectPython] Line509  # Draft 2D object (typed FeaturePython)
  ChamferSize = 0
  Closed = false
  End = (47297.9,18240.8,0)
  FilletRadius = 0
  Length = 1241.2
  MakeFace = true
  Placement = pos=(41972.8,-0.388672,0) rot=(0,0,1;0rad)
  Points = (2) [(5325.09,17000,0),(5325.09,18241.2,0)]
  Start = (47297.9,16999.6,0)
FEATURE [Part::Feature] Clone038  label="Clone of Clone of Circle001 (2D)013"
  Placement = pos=(47047.9,-500.383,0) rot=(0,0,-1;1.5708rad)
  shape: bbox 500 x 500 x 2e-07 mm, 0 faces, 0 solids (baked)
FEATURE [Part::Feature] Clone2D025  label="Clone of Circle001 (2D)013"
  Placement = pos=(47047.9,17975.6,0) rot=(0,0,-1;1.5708rad)
  shape: bbox 500 x 500 x 2e-07 mm, 0 faces, 0 solids (baked)
FEATURE [Part::Feature] Clone039  label="Clone of Clone of Circle001 (2D)014"
  Placement = pos=(48688.5,-500.383,0) rot=(0,0,-1;1.5708rad)
  shape: bbox 500 x 500 x 2e-07 mm, 0 faces, 0 solids (baked)
FEATURE [Part::Feature] Clone2D026  label="Clone of DWire180 (2D)002"
  Placement = pos=(16676.5,-18476,0) rot=(0,0,1;0rad)
  shape: bbox 299.5 x 500 x 2e-07 mm, 1 faces, 0 solids (baked)
FEATURE [Part::Part2DObjectPython] DWire182  # Draft 2D object (typed FeaturePython)
  ChamferSize = 0
  Closed = true
  End = (46797.9,17975.6,0)
  FilletRadius = 0
  Length = 1414.21
  MakeFace = true
  Placement = pos=(16676.5,0,0) rot=(0,0,1;0rad)
  Points = (6) [(30371.4,18225.6,0),(30420.9,18176.1,0),(30220.4,17975.6,0),(30420.9,17775.1,0),(30371.4,17725.6,0),(30121.4,17975.6,0)]
  Start = (47047.9,18225.6,0)
FEATURE [Part::Feature] Clone2D027  label="Clone of Circle001 (2D)014"
  Placement = pos=(48688.5,17975.6,0) rot=(0,0,-1;1.5708rad)
  shape: bbox 500 x 500 x 2e-07 mm, 0 faces, 0 solids (baked)
FEATURE [Part::Feature] Clone2D028  label="Clone of DWire180 (2D)003"
  Placement = pos=(18317.1,-18476,0) rot=(0,0,1;0rad)
  shape: bbox 299.5 x 500 x 2e-07 mm, 1 faces, 0 solids (baked)
FEATURE [Part::Part2DObjectPython] DWire183  # Draft 2D object (typed FeaturePython)
  ChamferSize = 0
  Closed = true
  End = (48438.5,17975.6,0)
  FilletRadius = 0
  Length = 1414.21
  MakeFace = true
  Placement = pos=(18317.1,-0.000215769,0) rot=(0,0,1;0rad)
  Points = (6) [(30371.4,18225.6,0),(30420.9,18176.1,0),(30220.4,17975.6,0),(30420.9,17775.1,0),(30371.4,17725.6,0),(30121.4,17975.6,0)]
  Start = (48688.5,18225.6,0)
FEATURE [Part::Part2DObjectPython] Rectangle052  # Draft 2D object (typed FeaturePython)
  ChamferSize = 0
  FilletRadius = 100
  Height = 717.785
  Length = 775.673
  MakeFace = false
  Placement = pos=(58321.2,16311.8,0) rot=(0,0,-1;1.5708rad)
FEATURE [Part::Part2DObjectPython] Rectangle053  # Draft 2D object (typed FeaturePython)
  ChamferSize = 0
  FilletRadius = 100
  Height = 717.785
  Length = 775.673
  MakeFace = false
  Placement = pos=(56881.3,17338.4,0) rot=(0,0,-1;1.5708rad)
FEATURE [Part::Part2DObjectPython] Rectangle054  # Draft 2D object (typed FeaturePython)
  ChamferSize = 0
  FilletRadius = 100
  Height = 1000
  Length = 1000
  MakeFace = false
  Placement = pos=(68915.5,13251,-3.88e-10) rot=(0,0,-1;1.5708rad)
FEATURE [Part::Part2DObjectPython] Line511  # Draft 2D object (typed FeaturePython)
  ChamferSize = 0
  Closed = false
  End = (73870.8,12965.8,-0.0147835)
  FilletRadius = 0
  Length = 1136.68
  MakeFace = true
  Placement = pos=(1293.83,0,0) rot=(0,0,1;0rad)
  Points = (2) [(73713.6,12965.8,0),(72577,12965.8,-0.0147835)]
  Start = (75007.5,12965.8,0)
FEATURE [Part::Part2DObjectPython] Line512  # Draft 2D object (typed FeaturePython)
  ChamferSize = 0
  Closed = false
  End = (73870.8,9965.85,-0.0158951)
  FilletRadius = 0
  Length = 1136.68
  MakeFace = true
  Placement = pos=(1293.83,-3000,-0.0011116) rot=(0,0,1;0rad)
  Points = (2) [(73713.6,12965.8,0),(72577,12965.8,-0.0147835)]
  Start = (75007.5,9965.85,-0.0011116)
FEATURE [Part::Part2DObjectPython] Line513  # Draft 2D object (typed FeaturePython)
  ChamferSize = 0
  Closed = false
  End = (73870.8,15965.8,-0.0158951)
  FilletRadius = 0
  Length = 1136.68
  MakeFace = true
  Placement = pos=(1293.83,3000,-0.0011116) rot=(0,0,1;0rad)
  Points = (2) [(73713.6,12965.8,0),(72577,12965.8,-0.0147835)]
  Start = (75007.5,15965.8,-0.0011116)
FEATURE [Part::Feature] Clone040  label="Clone of Clone of Circle001 (2D)015"
  Placement = pos=(75257.5,9965.85,-0.0011116) rot=(0,0,-1;1.5708rad)
  shape: bbox 500 x 500 x 2e-07 mm, 0 faces, 0 solids (baked)
FEATURE [Part::Feature] Clone041  label="Clone of Clone of Circle001 (2D)016"
  Placement = pos=(75257.5,12965.8,3.6e-11) rot=(0,0,-1;1.5708rad)
  shape: bbox 500 x 500 x 2e-07 mm, 0 faces, 0 solids (baked)
FEATURE [Part::Feature] Clone042  label="Clone of Clone of Circle001 (2D)017"
  Placement = pos=(75257.5,15965.8,-0.0011116) rot=(0,0,-1;1.5708rad)
  shape: bbox 500 x 500 x 2e-07 mm, 0 faces, 0 solids (baked)
FEATURE [Part::Part2DObjectPython] Line514  # Draft 2D object (typed FeaturePython)
  ChamferSize = 0
  Closed = false
  End = (75257.5,10316.1,-0.0011116)
  FilletRadius = 0
  Length = 700.583
  MakeFace = true
  Points = (2) [(75257.5,9615.56,-0.0011116),(75257.5,10316.1,-0.0011116)]
  Start = (75257.5,9615.56,-0.0011116)
FEATURE [Part::Part2DObjectPython] Line515  # Draft 2D object (typed FeaturePython)
  ChamferSize = 0
  Closed = false
  End = (75007.5,9965.85,-0.0011116)
  FilletRadius = 0
  Length = 600.291
  MakeFace = true
  Points = (2) [(75607.8,9965.85,-0.0011116),(75007.5,9965.85,-0.0011116)]
  Start = (75607.8,9965.85,-0.0011116)
FEATURE [Part::Part2DObjectPython] Line516  # Draft 2D object (typed FeaturePython)
  ChamferSize = 0
  Closed = false
  End = (75007.5,12965.8,3.6e-11)
  FilletRadius = 0
  Length = 600.291
  MakeFace = true
  Placement = pos=(5e-08,3000,0.0011116) rot=(0,0,1;0rad)
  Points = (2) [(75607.8,9965.85,-0.0011116),(75007.5,9965.85,-0.0011116)]
  Start = (75607.8,12965.8,3.6e-11)
FEATURE [Part::Part2DObjectPython] Line517  # Draft 2D object (typed FeaturePython)
  ChamferSize = 0
  Closed = false
  End = (75257.5,13316.1,3.6e-11)
  FilletRadius = 0
  Length = 700.583
  MakeFace = true
  Placement = pos=(5e-08,3000,0.0011116) rot=(0,0,1;0rad)
  Points = (2) [(75257.5,9615.56,-0.0011116),(75257.5,10316.1,-0.0011116)]
  Start = (75257.5,12615.6,3.6e-11)
FEATURE [Part::Part2DObjectPython] Line518  # Draft 2D object (typed FeaturePython)
  ChamferSize = 0
  Closed = false
  End = (75007.5,15965.8,-0.0011116)
  FilletRadius = 0
  Length = 600.291
  MakeFace = true
  Placement = pos=(0,6000,3.76e-10) rot=(0,0,1;0rad)
  Points = (2) [(75607.8,9965.85,-0.0011116),(75007.5,9965.85,-0.0011116)]
  Start = (75607.8,15965.8,-0.0011116)
FEATURE [Part::Part2DObjectPython] Line519  # Draft 2D object (typed FeaturePython)
  ChamferSize = 0
  Closed = false
  End = (75257.5,16316.1,-0.0011116)
  FilletRadius = 0
  Length = 700.583
  MakeFace = true
  Placement = pos=(0,6000,3.76e-10) rot=(0,0,1;0rad)
  Points = (2) [(75257.5,9615.56,-0.0011116),(75257.5,10316.1,-0.0011116)]
  Start = (75257.5,15615.6,-0.0011116)
FEATURE [App::FeaturePython] Dimension029  # Draft dimension (typed FeaturePython)
  Dimline = (75976.8,12172,0)
  Direction = (0,0,0)
  Distance = 3000
  End = (75607.8,12965.8,3.6e-11)
  Normal = (0,0,1)
  Start = (75607.8,9965.85,-0.0011116)
FEATURE [Part::Part2DObjectPython] Rectangle055  # Draft 2D object (typed FeaturePython)
  ChamferSize = 0
  FilletRadius = 100
  Height = 717.785
  Length = 2000
  MakeFace = false
  Placement = pos=(64553.6,14095.3,0) rot=(0,0,-1;1.5708rad)
FEATURE [Part::Part2DObjectPython] Rectangle056  # Draft 2D object (typed FeaturePython)
  ChamferSize = 0
  FilletRadius = 100
  Height = 400
  Length = 500
  MakeFace = false
  Placement = pos=(62346.9,15184.5,0) rot=(0,0,-1;1.5708rad)
FEATURE [App::FeaturePython] Dimension030  # Draft dimension (typed FeaturePython)
  Dimline = (75976.8,12849.5,0.000251051)
  Direction = (0,0,0)
  Distance = 3000
  End = (75607.8,12965.8,3.6e-11)
  Normal = (0,0,1)
  Start = (75607.8,15965.8,-0.0011116)
FEATURE [Part::Part2DObjectPython] Rectangle057  # Draft 2D object (typed FeaturePython)
  ChamferSize = 0
  FilletRadius = 0
  Height = 150
  Length = 200
  MakeFace = true
  Placement = pos=(79530.2,10350.4,0) rot=(0,0,-1;1.5708rad)
FEATURE [Part::Part2DObjectPython] Line520  # Draft 2D object (typed FeaturePython)
  ChamferSize = 0
  Closed = false
  End = (79763.2,10350.4,0)
  FilletRadius = 0
  Length = 233.062
  MakeFace = true
  Points = (2) [(79530.2,10350.4,0),(79763.2,10350.4,0)]
  Start = (79530.2,10350.4,0)
FEATURE [Part::Part2DObjectPython] Line521  # Draft 2D object (typed FeaturePython)
  ChamferSize = 0
  Closed = false
  End = (79763.2,10360.4,0)
  FilletRadius = 0
  Length = 233.062
  MakeFace = true
  Points = (2) [(79530.2,10360.4,0),(79763.2,10360.4,0)]
  Start = (79530.2,10360.4,0)
FEATURE [Part::Part2DObjectPython] DWire184  # Draft 2D object (typed FeaturePython)
  ChamferSize = 0
  Closed = true
  End = (78759.2,9965.85,-0.0147835)
  FilletRadius = 0
  Length = 5900
  MakeFace = true
  Placement = pos=(6332.21,0,1.2071e-08) rot=(0,0,1;0rad)
  Points = (4) [(72427,12765.8,-0.0147835),(72577,12765.8,-0.0147835),(72577,9965.85,-0.0147835),(72427,9965.85,-0.0147835)]
  Start = (78759.2,12765.8,-0.0147835)
FEATURE [Part::Part2DObjectPython] Line522  # Draft 2D object (typed FeaturePython)
  ChamferSize = 0
  Closed = false
  End = (78271,9965.85,-0.0147835)
  FilletRadius = 0
  Length = 488.203
  MakeFace = true
  Points = (2) [(78759.2,9965.85,-0.0147835),(78271,9965.85,-0.0147835)]
  Start = (78759.2,9965.85,-0.0147835)
FEATURE [Part::Part2DObjectPython] Line523  # Draft 2D object (typed FeaturePython)
  ChamferSize = 0
  Closed = false
  End = (78271,10968.8,0)
  FilletRadius = 0
  Length = 488.203
  MakeFace = true
  Points = (2) [(78759.2,10968.8,0),(78271,10968.8,0)]
  Start = (78759.2,10968.8,0)
FEATURE [Part::Part2DObjectPython] Rectangle058  # Draft 2D object (typed FeaturePython)
  ChamferSize = 0
  FilletRadius = 0
  Height = 150
  Length = 200
  MakeFace = true
  Placement = pos=(78759.2,10165.8,-0.0147835) rot=(0,0,-1;1.5708rad)
FEATURE [Part::Part2DObjectPython] Line524  # Draft 2D object (typed FeaturePython)
  ChamferSize = 0
  Closed = false
  End = (79142.2,10165.8,-0.0147835)
  FilletRadius = 0
  Length = 233.062
  MakeFace = true
  Placement = pos=(-621.008,-184.531,-0.0147835) rot=(0,0,1;0rad)
  Points = (2) [(79530.2,10350.4,0),(79763.2,10350.4,0)]
  Start = (78909.2,10165.8,-0.0147835)
FEATURE [Part::Part2DObjectPython] Line525  # Draft 2D object (typed FeaturePython)
  ChamferSize = 0
  Closed = false
  End = (79142.2,10175.8,-0.0147835)
  FilletRadius = 0
  Length = 233.062
  MakeFace = true
  Placement = pos=(-621.008,-184.531,-0.0147835) rot=(0,0,1;0rad)
  Points = (2) [(79530.2,10360.4,0),(79763.2,10360.4,0)]
  Start = (78909.2,10175.8,-0.0147835)
FEATURE [Part::Part2DObjectPython] Rectangle059  # Draft 2D object (typed FeaturePython)
  ChamferSize = 0
  FilletRadius = 0
  Height = 150
  Length = 200
  MakeFace = true
  Placement = pos=(78759.2,10375.8,-0.0147835) rot=(0,0,-1;1.5708rad)
FEATURE [Part::Part2DObjectPython] Rectangle060  # Draft 2D object (typed FeaturePython)
  ChamferSize = 0
  FilletRadius = 0
  Height = 150
  Length = 200
  MakeFace = true
  Placement = pos=(78759.2,10585.8,-0.0147835) rot=(0,0,-1;1.5708rad)
FEATURE [Part::Part2DObjectPython] Rectangle061  # Draft 2D object (typed FeaturePython)
  ChamferSize = 0
  FilletRadius = 0
  Height = 150
  Length = 200
  MakeFace = true
  Placement = pos=(78759.2,11005.8,-0.0147835) rot=(0,0,-1;1.5708rad)
FEATURE [Part::Part2DObjectPython] Rectangle062  # Draft 2D object (typed FeaturePython)
  ChamferSize = 0
  FilletRadius = 0
  Height = 150
  Length = 200
  MakeFace = true
  Placement = pos=(78759.2,10795.8,-0.0147835) rot=(0,0,-1;1.5708rad)
FEATURE [Part::Part2DObjectPython] Line526  # Draft 2D object (typed FeaturePython)
  ChamferSize = 0
  Closed = false
  End = (77355.5,9965.85,-0.0147835)
  FilletRadius = 0
  Length = 488.203
  MakeFace = true
  Placement = pos=(-915.438,0,0) rot=(0,0,1;0rad)
  Points = (2) [(78759.2,9965.85,-0.0147835),(78271,9965.85,-0.0147835)]
  Start = (77843.7,9965.85,-0.0147835)
FEATURE [Part::Part2DObjectPython] Line527  # Draft 2D object (typed FeaturePython)
  ChamferSize = 0
  Closed = false
  End = (77355.5,10968.8,0)
  FilletRadius = 0
  Length = 488.203
  MakeFace = true
  Placement = pos=(-915.438,0,0) rot=(0,0,1;0rad)
  Points = (2) [(78759.2,10968.8,0),(78271,10968.8,0)]
  Start = (77843.7,10968.8,0)
FEATURE [Part::Part2DObjectPython] Rectangle063  # Draft 2D object (typed FeaturePython)
  ChamferSize = 0
  FilletRadius = 0
  Height = 150
  Length = 200
  MakeFace = true
  Placement = pos=(77843.7,10165.8,-0.0147835) rot=(0,0,-1;1.5708rad)
FEATURE [Part::Part2DObjectPython] Line528  # Draft 2D object (typed FeaturePython)
  ChamferSize = 0
  Closed = false
  End = (78226.8,10165.8,-0.0147835)
  FilletRadius = 0
  Length = 233.062
  MakeFace = true
  Placement = pos=(-1536.45,-184.531,-0.0147835) rot=(0,0,1;0rad)
  Points = (2) [(79530.2,10350.4,0),(79763.2,10350.4,0)]
  Start = (77993.7,10165.8,-0.0147835)
FEATURE [Part::Part2DObjectPython] Line529  # Draft 2D object (typed FeaturePython)
  ChamferSize = 0
  Closed = false
  End = (78226.8,10175.8,-0.0147835)
  FilletRadius = 0
  Length = 233.062
  MakeFace = true
  Placement = pos=(-1536.45,-184.531,-0.0147835) rot=(0,0,1;0rad)
  Points = (2) [(79530.2,10360.4,0),(79763.2,10360.4,0)]
  Start = (77993.7,10175.8,-0.0147835)
FEATURE [Part::Part2DObjectPython] Rectangle064  # Draft 2D object (typed FeaturePython)
  ChamferSize = 0
  FilletRadius = 0
  Height = 150
  Length = 200
  MakeFace = true
  Placement = pos=(77843.7,10365.8,-0.0147835) rot=(0,0,-1;1.5708rad)
FEATURE [Part::Part2DObjectPython] Rectangle065  # Draft 2D object (typed FeaturePython)
  ChamferSize = 0
  FilletRadius = 0
  Height = 150
  Length = 200
  MakeFace = true
  Placement = pos=(77843.7,10565.8,-0.0147835) rot=(0,0,-1;1.5708rad)
FEATURE [Part::Part2DObjectPython] Rectangle066  # Draft 2D object (typed FeaturePython)
  ChamferSize = 0
  FilletRadius = 0
  Height = 150
  Length = 200
  MakeFace = true
  Placement = pos=(77843.7,10965.8,-0.0147835) rot=(0,0,-1;1.5708rad)
FEATURE [Part::Part2DObjectPython] Rectangle067  # Draft 2D object (typed FeaturePython)
  ChamferSize = 0
  FilletRadius = 0
  Height = 150
  Length = 200
  MakeFace = true
  Placement = pos=(77843.7,10765.8,-0.0147835) rot=(0,0,-1;1.5708rad)
FEATURE [Part::Part2DObjectPython] Rectangle068  # Draft 2D object (typed FeaturePython)
  ChamferSize = 0
  FilletRadius = 100
  Height = 700
  Length = 1000
  MakeFace = false
  Placement = pos=(64873.4,10505.8,-0.0147835) rot=(0,0,-1;1.5708rad)
FEATURE [Part::Part2DObjectPython] Rectangle069  # Draft 2D object (typed FeaturePython)
  ChamferSize = 0
  FilletRadius = 100
  Height = 717.785
  Length = 775.673
  MakeFace = false
  Placement = pos=(58321.2,13272.1,9e-12) rot=(0,0,-1;1.5708rad)
FEATURE [Part::Part2DObjectPython] Rectangle070  # Draft 2D object (typed FeaturePython)
  ChamferSize = 0
  FilletRadius = 100
  Height = 500
  Length = 500
  MakeFace = false
  Placement = pos=(59231.2,12204.3,0) rot=(0,0,-1;1.5708rad)
FEATURE [Part::Part2DObjectPython] Rectangle071  # Draft 2D object (typed FeaturePython)
  ChamferSize = 0
  FilletRadius = 100
  Height = 717.785
  Length = 2000
  MakeFace = false
  Placement = pos=(72125.2,14476.8,0) rot=(0,0,-1;1.5708rad)
FEATURE [Part::Part2DObjectPython] DWire185  # Draft 2D object (typed FeaturePython)
  ChamferSize = 0
  Closed = true
  End = (63166.7,10166.4,-0.0141602)
  FilletRadius = 0
  Length = 968.112
  MakeFace = true
  Placement = pos=(80941.8,-38302.1,-0.0141602) rot=(0,0,1;1.5708rad)
  Points = (3) [(48468.4,18176.1,0),(48267.9,17975.6,0),(48468.4,17775.1,0)]
  Start = (62765.7,10166.4,-0.0141602)
FEATURE [Part::Part2DObjectPython] DWire186  # Draft 2D object (typed FeaturePython)
  ChamferSize = 0
  Closed = true
  End = (63166.7,13166.4,-0.0130486)
  FilletRadius = 0
  Length = 968.112
  MakeFace = true
  Placement = pos=(80941.8,-35302.1,-0.0130486) rot=(0,0,1;1.5708rad)
  Points = (3) [(48468.4,18176.1,0),(48267.9,17975.6,0),(48468.4,17775.1,0)]
  Start = (62765.7,13166.4,-0.0130486)
FEATURE [Part::Part2DObjectPython] DWire187  # Draft 2D object (typed FeaturePython)
  ChamferSize = 0
  Closed = true
  End = (63166.7,16166.4,-0.0141602)
  FilletRadius = 0
  Length = 968.112
  MakeFace = true
  Placement = pos=(80941.8,-32302.1,-0.0141602) rot=(0,0,1;1.5708rad)
  Points = (3) [(48468.4,18176.1,0),(48267.9,17975.6,0),(48468.4,17775.1,0)]
  Start = (62765.7,16166.4,-0.0141602)
FEATURE [Part::Part2DObjectPython] Line530  # Draft 2D object (typed FeaturePython)
  ChamferSize = 0
  Closed = false
  End = (63166.7,10166.4,-0.0141602)
  FilletRadius = 0
  Length = 488.203
  MakeFace = true
  Placement = pos=(-15104.3,200.503,0.000623305) rot=(0,0,1;0rad)
  Points = (2) [(78759.2,9965.85,-0.0147835),(78271,9965.85,-0.0147835)]
  Start = (63654.9,10166.4,-0.0141602)
FEATURE [Part::Part2DObjectPython] Line531  # Draft 2D object (typed FeaturePython)
  ChamferSize = 0
  Closed = false
  End = (63166.7,13166.4,-0.0130486)
  FilletRadius = 0
  Length = 488.203
  MakeFace = true
  Placement = pos=(-15104.3,3200.5,0.0017349) rot=(0,0,1;0rad)
  Points = (2) [(78759.2,9965.85,-0.0147835),(78271,9965.85,-0.0147835)]
  Start = (63654.9,13166.4,-0.0130486)
FEATURE [Part::Feature] Face016
  shape: bbox 5.96 x 35.03 x 2e-07 mm, 1 faces, 0 solids (baked)
FEATURE [Part::Feature] Face017
  shape: bbox 44.78 x 165.3 x 2e-07 mm, 1 faces, 0 solids (baked)
FEATURE [Part::Cut] Cut005
  Base = -> Face017
  Tool = -> Face016
FEATURE [Part::Part2DObjectPython] Line532  # Draft 2D object (typed FeaturePython)
  ChamferSize = 0
  Closed = false
  End = (81033.9,9965.85,-0.0147835)
  FilletRadius = 0
  Length = 488.203
  MakeFace = true
  Placement = pos=(2762.95,0,0) rot=(0,0,1;0rad)
  Points = (2) [(78759.2,9965.85,-0.0147835),(78271,9965.85,-0.0147835)]
  Start = (81522.1,9965.85,-0.0147835)
FEATURE [Part::Part2DObjectPython] Line533  # Draft 2D object (typed FeaturePython)
  ChamferSize = 0
  Closed = false
  End = (81033.9,10968.8,0)
  FilletRadius = 0
  Length = 488.203
  MakeFace = true
  Placement = pos=(2762.95,0,0) rot=(0,0,1;0rad)
  Points = (2) [(78759.2,10968.8,0),(78271,10968.8,0)]
  Start = (81522.1,10968.8,0)
FEATURE [Part::Part2DObjectPython] Rectangle072  # Draft 2D object (typed FeaturePython)
  ChamferSize = 0
  FilletRadius = 0
  Height = 150
  Length = 200
  MakeFace = true
  Placement = pos=(81522.1,10168.8,0) rot=(0,0,-1;1.5708rad)
FEATURE [Part::Part2DObjectPython] Line534  # Draft 2D object (typed FeaturePython)
  ChamferSize = 0
  Closed = false
  End = (81905.2,10165.8,-0.0147835)
  FilletRadius = 0
  Length = 233.062
  MakeFace = true
  Placement = pos=(2141.95,-184.531,-0.0147835) rot=(0,0,1;0rad)
  Points = (2) [(79530.2,10350.4,0),(79763.2,10350.4,0)]
  Start = (81672.1,10165.8,-0.0147835)
FEATURE [Part::Part2DObjectPython] Line535  # Draft 2D object (typed FeaturePython)
  ChamferSize = 0
  Closed = false
  End = (81905.2,10175.8,-0.0147835)
  FilletRadius = 0
  Length = 233.062
  MakeFace = true
  Placement = pos=(2141.95,-184.531,-0.0147835) rot=(0,0,1;0rad)
  Points = (2) [(79530.2,10360.4,0),(79763.2,10360.4,0)]
  Start = (81672.1,10175.8,-0.0147835)
FEATURE [Part::Part2DObjectPython] Rectangle073  # Draft 2D object (typed FeaturePython)
  ChamferSize = 0
  FilletRadius = 0
  Height = 150
  Length = 200
  MakeFace = true
  Placement = pos=(81522.1,10368.8,0) rot=(0,0,-1;1.5708rad)
FEATURE [Part::Part2DObjectPython] Rectangle074  # Draft 2D object (typed FeaturePython)
  ChamferSize = 0
  FilletRadius = 0
  Height = 150
  Length = 200
  MakeFace = true
  Placement = pos=(81522.1,10568.8,0) rot=(0,0,-1;1.5708rad)
FEATURE [Part::Part2DObjectPython] Rectangle075  # Draft 2D object (typed FeaturePython)
  ChamferSize = 0
  FilletRadius = 0
  Height = 150
  Length = 200
  MakeFace = true
  Placement = pos=(81522.1,10968.8,0) rot=(0,0,-1;1.5708rad)
FEATURE [Part::Part2DObjectPython] Rectangle076  # Draft 2D object (typed FeaturePython)
  ChamferSize = 0
  FilletRadius = 0
  Height = 150
  Length = 200
  MakeFace = true
  Placement = pos=(81522.1,10768.8,0) rot=(0,0,-1;1.5708rad)
FEATURE [Part::Part2DObjectPython] Line537  # Draft 2D object (typed FeaturePython)
  ChamferSize = 0
  Closed = false
  End = (82440.3,9965.85,-0.0147835)
  FilletRadius = 0
  Length = 488.203
  MakeFace = true
  Placement = pos=(4169.3,0,0) rot=(0,0,1;0rad)
  Points = (2) [(78759.2,9965.85,-0.0147835),(78271,9965.85,-0.0147835)]
  Start = (82928.5,9965.85,-0.0147835)
FEATURE [Part::Part2DObjectPython] Line538  # Draft 2D object (typed FeaturePython)
  ChamferSize = 0
  Closed = false
  End = (82440.3,10968.8,0)
  FilletRadius = 0
  Length = 488.203
  MakeFace = true
  Placement = pos=(4169.3,0,0) rot=(0,0,1;0rad)
  Points = (2) [(78759.2,10968.8,0),(78271,10968.8,0)]
  Start = (82928.5,10968.8,0)
FEATURE [Part::Part2DObjectPython] Rectangle077  # Draft 2D object (typed FeaturePython)
  ChamferSize = 0
  FilletRadius = 0
  Height = 150
  Length = 200
  MakeFace = true
  Placement = pos=(82928.5,10128.8,1.146e-09) rot=(0,0,-1;1.5708rad)
FEATURE [Part::Part2DObjectPython] Line539  # Draft 2D object (typed FeaturePython)
  ChamferSize = 0
  Closed = false
  End = (83311.5,10165.8,-0.0147835)
  FilletRadius = 0
  Length = 233.062
  MakeFace = true
  Placement = pos=(3548.3,-184.531,-0.0147835) rot=(0,0,1;0rad)
  Points = (2) [(79530.2,10350.4,0),(79763.2,10350.4,0)]
  Start = (83078.5,10165.8,-0.0147835)
FEATURE [Part::Part2DObjectPython] Line540  # Draft 2D object (typed FeaturePython)
  ChamferSize = 0
  Closed = false
  End = (83311.5,10175.8,-0.0147835)
  FilletRadius = 0
  Length = 233.062
  MakeFace = true
  Placement = pos=(3548.3,-184.531,-0.0147835) rot=(0,0,1;0rad)
  Points = (2) [(79530.2,10360.4,0),(79763.2,10360.4,0)]
  Start = (83078.5,10175.8,-0.0147835)
FEATURE [Part::Part2DObjectPython] Rectangle078  # Draft 2D object (typed FeaturePython)
  ChamferSize = 0
  FilletRadius = 0
  Height = 150
  Length = 200
  MakeFace = true
  Placement = pos=(82928.5,10338.8,8.59e-10) rot=(0,0,-1;1.5708rad)
FEATURE [Part::Part2DObjectPython] Rectangle079  # Draft 2D object (typed FeaturePython)
  ChamferSize = 0
  FilletRadius = 0
  Height = 150
  Length = 200
  MakeFace = true
  Placement = pos=(82928.5,10548.8,5.73e-10) rot=(0,0,-1;1.5708rad)
FEATURE [Part::Part2DObjectPython] Rectangle080  # Draft 2D object (typed FeaturePython)
  ChamferSize = 0
  FilletRadius = 0
  Height = 150
  Length = 200
  MakeFace = true
  Placement = pos=(82928.5,10968.8,0) rot=(0,0,-1;1.5708rad)
FEATURE [Part::Part2DObjectPython] Rectangle081  # Draft 2D object (typed FeaturePython)
  ChamferSize = 0
  FilletRadius = 0
  Height = 150
  Length = 200
  MakeFace = true
  Placement = pos=(82928.5,10758.8,2.86e-10) rot=(0,0,-1;1.5708rad)
FEATURE [App::FeaturePython] Dimension033  # Draft dimension (typed FeaturePython)
  Dimline = (83380.1,10173.3,0)
  Direction = (0,0,0)
  Distance = 10
  End = (83311.5,10165.8,-0.0147835)
  Normal = (0,0,1)
  Start = (83311.5,10175.8,-0.0147835)
FEATURE [App::FeaturePython] Dimension034  # Draft dimension (typed FeaturePython)
  Dimline = (83380.1,10170.7,0)
  Direction = (0,0,0)
  Distance = 10
  End = (83078.5,10375.8,-0.0147835)
  Normal = (0,0,1)
  Start = (83078.5,10385.8,-0.0147835)
FEATURE [App::FeaturePython] Dimension035  # Draft dimension (typed FeaturePython)
  Dimline = (83380.1,10380.7,-6.004e-09)
  Direction = (0,0,0)
  Distance = 10
  End = (83078.5,10585.8,-0.0147835)
  Normal = (0,0,1)
  Start = (83078.5,10595.8,-0.0147835)
FEATURE [App::FeaturePython] Dimension036  # Draft dimension (typed FeaturePython)
  Dimline = (83380.1,10585.8,-1.1893e-08)
  Direction = (0,0,0)
  Distance = 10
  End = (83078.5,10795.8,-0.0147835)
  Normal = (0,0,1)
  Start = (83078.5,10805.8,-0.0147835)
FEATURE [Part::Part2DObjectPython] Rectangle082  # Draft 2D object (typed FeaturePython)
  ChamferSize = 0
  FilletRadius = 0
  Height = 150
  Length = 200
  MakeFace = true
  Placement = pos=(82928.5,9918.83,1.433e-09) rot=(0,0,-1;1.5708rad)
FEATURE [Part::Part2DObjectPython] Line541  # Draft 2D object (typed FeaturePython)
  ChamferSize = 0
  Closed = false
  End = (86193.5,12765.8,-0.0147834)
  FilletRadius = 0
  Length = 13616.6
  MakeFace = true
  Points = (2) [(72577,12765.8,-0.0147835),(86193.5,12765.8,-0.0147834)]
  Start = (72577,12765.8,-0.0147835)
FEATURE [Part::Part2DObjectPython] Line542  # Draft 2D object (typed FeaturePython)
  ChamferSize = 0
  Closed = false
  End = (85365.7,9965.85,-0.0147835)
  FilletRadius = 0
  Length = 488.203
  MakeFace = true
  Placement = pos=(7094.75,0,0) rot=(0,0,1;0rad)
  Points = (2) [(78759.2,9965.85,-0.0147835),(78271,9965.85,-0.0147835)]
  Start = (85853.9,9965.85,-0.0147835)
FEATURE [Part::Part2DObjectPython] Line543  # Draft 2D object (typed FeaturePython)
  ChamferSize = 0
  Closed = false
  End = (85365.7,10968.8,0)
  FilletRadius = 0
  Length = 488.203
  MakeFace = true
  Placement = pos=(7094.75,0,0) rot=(0,0,1;0rad)
  Points = (2) [(78759.2,10968.8,0),(78271,10968.8,0)]
  Start = (85853.9,10968.8,0)
FEATURE [Part::Part2DObjectPython] Rectangle083  # Draft 2D object (typed FeaturePython)
  ChamferSize = 0
  FilletRadius = 0
  Height = 150
  Length = 200
  MakeFace = true
  Placement = pos=(85853.9,10165.8,-0.0147835) rot=(0,0,-1;1.5708rad)
FEATURE [Part::Part2DObjectPython] Line544  # Draft 2D object (typed FeaturePython)
  ChamferSize = 0
  Closed = false
  End = (86237,10165.8,-0.0147835)
  FilletRadius = 0
  Length = 233.062
  MakeFace = true
  Placement = pos=(6473.74,-184.531,-0.0147835) rot=(0,0,1;0rad)
  Points = (2) [(79530.2,10350.4,0),(79763.2,10350.4,0)]
  Start = (86003.9,10165.8,-0.0147835)
FEATURE [Part::Part2DObjectPython] Line545  # Draft 2D object (typed FeaturePython)
  ChamferSize = 0
  Closed = false
  End = (86237,10175.8,-0.0147835)
  FilletRadius = 0
  Length = 233.062
  MakeFace = true
  Placement = pos=(6473.74,-184.531,-0.0147835) rot=(0,0,1;0rad)
  Points = (2) [(79530.2,10360.4,0),(79763.2,10360.4,0)]
  Start = (86003.9,10175.8,-0.0147835)
FEATURE [Part::Part2DObjectPython] Rectangle084  # Draft 2D object (typed FeaturePython)
  ChamferSize = 0
  FilletRadius = 0
  Height = 150
  Length = 200
  MakeFace = true
  Placement = pos=(85853.9,10375.8,-0.0147835) rot=(0,0,-1;1.5708rad)
FEATURE [Part::Part2DObjectPython] Rectangle085  # Draft 2D object (typed FeaturePython)
  ChamferSize = 0
  FilletRadius = 0
  Height = 150
  Length = 200
  MakeFace = true
  Placement = pos=(85853.9,10585.8,-0.0147835) rot=(0,0,-1;1.5708rad)
FEATURE [Part::Part2DObjectPython] Rectangle086  # Draft 2D object (typed FeaturePython)
  ChamferSize = 0
  FilletRadius = 0
  Height = 150
  Length = 200
  MakeFace = true
  Placement = pos=(85853.9,11005.8,-0.0147835) rot=(0,0,-1;1.5708rad)
FEATURE [Part::Part2DObjectPython] Rectangle087  # Draft 2D object (typed FeaturePython)
  ChamferSize = 0
  FilletRadius = 0
  Height = 150
  Length = 200
  MakeFace = true
  Placement = pos=(85853.9,10795.8,-0.0147835) rot=(0,0,-1;1.5708rad)
FEATURE [Part::Part2DObjectPython] Line546  # Draft 2D object (typed FeaturePython)
  ChamferSize = 0
  Closed = false
  End = (84450.3,9965.85,-0.0147835)
  FilletRadius = 0
  Length = 488.203
  MakeFace = true
  Placement = pos=(6179.31,0,0) rot=(0,0,1;0rad)
  Points = (2) [(78759.2,9965.85,-0.0147835),(78271,9965.85,-0.0147835)]
  Start = (84938.5,9965.85,-0.0147835)
FEATURE [Part::Part2DObjectPython] Line547  # Draft 2D object (typed FeaturePython)
  ChamferSize = 0
  Closed = false
  End = (84450.3,10968.8,0)
  FilletRadius = 0
  Length = 488.203
  MakeFace = true
  Placement = pos=(6179.31,0,0) rot=(0,0,1;0rad)
  Points = (2) [(78759.2,10968.8,0),(78271,10968.8,0)]
  Start = (84938.5,10968.8,0)
FEATURE [Part::Part2DObjectPython] Rectangle088  # Draft 2D object (typed FeaturePython)
  ChamferSize = 0
  FilletRadius = 0
  Height = 150
  Length = 200
  MakeFace = true
  Placement = pos=(84938.5,10165.8,-0.0147835) rot=(0,0,-1;1.5708rad)
FEATURE [Part::Part2DObjectPython] Line548  # Draft 2D object (typed FeaturePython)
  ChamferSize = 0
  Closed = false
  End = (85321.6,10165.8,-0.0147835)
  FilletRadius = 0
  Length = 233.062
  MakeFace = true
  Placement = pos=(5558.3,-184.531,-0.0147835) rot=(0,0,1;0rad)
  Points = (2) [(79530.2,10350.4,0),(79763.2,10350.4,0)]
  Start = (85088.5,10165.8,-0.0147835)
FEATURE [Part::Part2DObjectPython] Line549  # Draft 2D object (typed FeaturePython)
  ChamferSize = 0
  Closed = false
  End = (85321.6,10175.8,-0.0147835)
  FilletRadius = 0
  Length = 233.062
  MakeFace = true
  Placement = pos=(5558.3,-184.531,-0.0147835) rot=(0,0,1;0rad)
  Points = (2) [(79530.2,10360.4,0),(79763.2,10360.4,0)]
  Start = (85088.5,10175.8,-0.0147835)
FEATURE [Part::Part2DObjectPython] Rectangle089  # Draft 2D object (typed FeaturePython)
  ChamferSize = 0
  FilletRadius = 0
  Height = 150
  Length = 200
  MakeFace = true
  Placement = pos=(84938.5,10365.8,-0.0147835) rot=(0,0,-1;1.5708rad)
FEATURE [Part::Part2DObjectPython] Rectangle090  # Draft 2D object (typed FeaturePython)
  ChamferSize = 0
  FilletRadius = 0
  Height = 150
  Length = 200
  MakeFace = true
  Placement = pos=(84938.5,10565.8,-0.0147835) rot=(0,0,-1;1.5708rad)
FEATURE [Part::Part2DObjectPython] Rectangle091  # Draft 2D object (typed FeaturePython)
  ChamferSize = 0
  FilletRadius = 0
  Height = 150
  Length = 200
  MakeFace = true
  Placement = pos=(84938.5,10965.8,-0.0147835) rot=(0,0,-1;1.5708rad)
FEATURE [Part::Part2DObjectPython] Rectangle092  # Draft 2D object (typed FeaturePython)
  ChamferSize = 0
  FilletRadius = 0
  Height = 150
  Length = 200
  MakeFace = true
  Placement = pos=(84938.5,10765.8,-0.0147835) rot=(0,0,-1;1.5708rad)
FEATURE [Part::Part2DObjectPython] Rectangle093  # Draft 2D object (typed FeaturePython)
  ChamferSize = 0
  FilletRadius = 0
  Height = 150
  Length = 200
  MakeFace = true
  Placement = pos=(84938.5,11165.8,-0.0147835) rot=(0,0,-1;1.5708rad)
FEATURE [Part::Part2DObjectPython] Rectangle094  # Draft 2D object (typed FeaturePython)
  ChamferSize = 0
  FilletRadius = 0
  Height = 150
  Length = 200
  MakeFace = true
  Placement = pos=(84938.5,11365.8,-0.0147835) rot=(0,0,-1;1.5708rad)
FEATURE [Part::Part2DObjectPython] Rectangle095  # Draft 2D object (typed FeaturePython)
  ChamferSize = 0
  FilletRadius = 0
  Height = 150
  Length = 200
  MakeFace = true
  Placement = pos=(84938.5,11565.8,-0.0147835) rot=(0,0,-1;1.5708rad)
FEATURE [Part::Part2DObjectPython] Rectangle096  # Draft 2D object (typed FeaturePython)
  ChamferSize = 0
  FilletRadius = 0
  Height = 150
  Length = 200
  MakeFace = true
  Placement = pos=(84938.5,11765.8,-0.0147835) rot=(0,0,-1;1.5708rad)
FEATURE [Part::Part2DObjectPython] Rectangle097  # Draft 2D object (typed FeaturePython)
  ChamferSize = 0
  FilletRadius = 0
  Height = 150
  Length = 200
  MakeFace = true
  Placement = pos=(84938.5,11965.8,-0.0147835) rot=(0,0,-1;1.5708rad)
FEATURE [Part::Part2DObjectPython] Rectangle098  # Draft 2D object (typed FeaturePython)
  ChamferSize = 0
  FilletRadius = 0
  Height = 150
  Length = 200
  MakeFace = true
  Placement = pos=(84938.5,12165.8,-0.0147835) rot=(0,0,-1;1.5708rad)
FEATURE [Part::Part2DObjectPython] Rectangle099  # Draft 2D object (typed FeaturePython)
  ChamferSize = 0
  FilletRadius = 0
  Height = 150
  Length = 200
  MakeFace = true
  Placement = pos=(84938.5,12365.8,-0.0147835) rot=(0,0,-1;1.5708rad)
FEATURE [Part::Part2DObjectPython] Rectangle100  # Draft 2D object (typed FeaturePython)
  ChamferSize = 0
  FilletRadius = 0
  Height = 150
  Length = 200
  MakeFace = true
  Placement = pos=(84938.5,12565.8,-0.0147835) rot=(0,0,-1;1.5708rad)
FEATURE [Part::Part2DObjectPython] Rectangle101  # Draft 2D object (typed FeaturePython)
  ChamferSize = 0
  FilletRadius = 0
  Height = 150
  Length = 200
  MakeFace = true
  Placement = pos=(84938.5,12765.8,-0.0147835) rot=(0,0,-1;1.5708rad)
FEATURE [Part::Part2DObjectPython] Rectangle103  # Draft 2D object (typed FeaturePython)
  ChamferSize = 0
  FilletRadius = 0
  Height = 150
  Length = 200
  MakeFace = true
  Placement = pos=(85853.9,11215.8,-0.0147835) rot=(0,0,-1;1.5708rad)
FEATURE [Part::Part2DObjectPython] Rectangle104  # Draft 2D object (typed FeaturePython)
  ChamferSize = 0
  FilletRadius = 0
  Height = 150
  Length = 200
  MakeFace = true
  Placement = pos=(85853.9,11425.8,-0.0147835) rot=(0,0,-1;1.5708rad)
FEATURE [Part::Part2DObjectPython] Rectangle105  # Draft 2D object (typed FeaturePython)
  ChamferSize = 0
  FilletRadius = 0
  Height = 150
  Length = 200
  MakeFace = true
  Placement = pos=(85853.9,11845.8,-0.0147835) rot=(0,0,-1;1.5708rad)
FEATURE [Part::Part2DObjectPython] Rectangle106  # Draft 2D object (typed FeaturePython)
  ChamferSize = 0
  FilletRadius = 0
  Height = 150
  Length = 200
  MakeFace = true
  Placement = pos=(85853.9,11635.8,-0.0147835) rot=(0,0,-1;1.5708rad)
FEATURE [Part::Part2DObjectPython] Rectangle107  # Draft 2D object (typed FeaturePython)
  ChamferSize = 0
  FilletRadius = 0
  Height = 150
  Length = 200
  MakeFace = true
  Placement = pos=(85853.9,12055.8,-0.0147835) rot=(0,0,-1;1.5708rad)
FEATURE [Part::Part2DObjectPython] Rectangle108  # Draft 2D object (typed FeaturePython)
  ChamferSize = 0
  FilletRadius = 0
  Height = 150
  Length = 200
  MakeFace = true
  Placement = pos=(85853.9,12265.8,-0.0147835) rot=(0,0,-1;1.5708rad)
FEATURE [Part::Part2DObjectPython] Rectangle109  # Draft 2D object (typed FeaturePython)
  ChamferSize = 0
  FilletRadius = 0
  Height = 150
  Length = 200
  MakeFace = true
  Placement = pos=(85853.9,12475.8,-0.0147835) rot=(0,0,-1;1.5708rad)
FEATURE [Part::Part2DObjectPython] Rectangle110  # Draft 2D object (typed FeaturePython)
  ChamferSize = 0
  FilletRadius = 0
  Height = 150
  Length = 200
  MakeFace = true
  Placement = pos=(85853.9,12685.8,-0.0147835) rot=(0,0,-1;1.5708rad)
FEATURE [App::FeaturePython] Dimension039  # Draft dimension (typed FeaturePython)
  Dimline = (86107.8,12667.8,0)
  Direction = (0,0,0)
  Distance = 280
  End = (86003.9,12765.8,-0.0147834)
  Normal = (0,0,1)
  Start = (86003.9,12485.8,-0.0147835)
FEATURE [Part::Part2DObjectPython] Rectangle111  # Draft 2D object (typed FeaturePython)
  ChamferSize = 0
  FilletRadius = 0
  Height = 150
  Length = 200
  MakeFace = true
  Placement = pos=(82928.5,9708.83,1.72e-09) rot=(0,0,-1;1.5708rad)
FEATURE [Part::Part2DObjectPython] Rectangle112  # Draft 2D object (typed FeaturePython)
  ChamferSize = 0
  FilletRadius = 0
  Height = 150
  Length = 200
  MakeFace = true
  Placement = pos=(82928.5,9498.83,2.007e-09) rot=(0,0,-1;1.5708rad)
FEATURE [Part::Part2DObjectPython] Rectangle113  # Draft 2D object (typed FeaturePython)
  ChamferSize = 0
  FilletRadius = 0
  Height = -245.803
  Length = 300
  MakeFace = true
  Placement = pos=(82820.9,9286.35,0) rot=(0,0,1;0rad)
FEATURE [Part::Part2DObjectPython] Rectangle114  # Draft 2D object (typed FeaturePython)
  ChamferSize = 0
  FilletRadius = 0
  Height = 150
  Length = 200
  MakeFace = true
  Placement = pos=(81522.1,9968.83,0) rot=(0,0,-1;1.5708rad)
FEATURE [Part::Part2DObjectPython] Rectangle115  # Draft 2D object (typed FeaturePython)
  ChamferSize = 0
  FilletRadius = 0
  Height = 150
  Length = 200
  MakeFace = true
  Placement = pos=(81522.1,9768.83,0) rot=(0,0,-1;1.5708rad)
FEATURE [Part::Part2DObjectPython] Rectangle116  # Draft 2D object (typed FeaturePython)
  ChamferSize = 0
  FilletRadius = 0
  Height = 150
  Length = 200
  MakeFace = true
  Placement = pos=(81522.1,9568.83,0) rot=(0,0,-1;1.5708rad)
FEATURE [Part::Part2DObjectPython] Line550  # Draft 2D object (typed FeaturePython)
  ChamferSize = 0
  Closed = false
  End = (86810.2,10965.4,-0.0147834)
  FilletRadius = 0
  Length = 727.68
  MakeFace = true
  Placement = pos=(13616.5,9308.98,-0.0147834) rot=(0,0,1;0rad)
  Points = (2) [(72466,1656.46,0.0147834),(73193.7,1656.46,-6.99961e-15)]
  Start = (86082.5,10965.4,0)
FEATURE [Part::Part2DObjectPython] Line551  # Draft 2D object (typed FeaturePython)
  ChamferSize = 0
  Closed = false
  End = (84525.9,12315.4,0)
  FilletRadius = 0
  Length = 3900.85
  MakeFace = true
  Placement = pos=(13616.5,10659,-0.0147834) rot=(0,0,1;0rad)
  Points = (2) [(74810.2,1656.46,0.0147834),(70909.3,1656.46,0.0147834)]
  Start = (88426.7,12315.4,0)
FEATURE [Part::Part2DObjectPython] Line552  # Draft 2D object (typed FeaturePython)
  ChamferSize = 0
  Closed = false
  End = (86193.5,12765.8,-0.0147834)
  FilletRadius = 0
  Length = 3668.38
  MakeFace = true
  Placement = pos=(13616.5,11109.4,-0.0147834) rot=(0,0,1;0rad)
  Points = (2) [(76245.4,1656.46,0.0147834),(72577,1656.46,-6.99961e-15)]
  Start = (89861.9,12765.8,0)
FEATURE [App::FeaturePython] Dimension040  # Draft dimension (typed FeaturePython)
  Dimline = (85581.6,12386.6,0)
  Direction = (0,0,0)
  Distance = 450.403
  End = (85449.6,12315.4,-0.00597787)
  Normal = (0,0,1)
  Start = (85449.6,12765.8,-0.0147834)
FEATURE [Part::Part2DObjectPython] Line553  # Draft 2D object (typed FeaturePython)
  ChamferSize = 0
  Closed = false
  End = (87391.5,9965.85,-0.0147835)
  FilletRadius = 0
  Length = 2451.68
  MakeFace = true
  Placement = pos=(9120.48,0,0) rot=(0,0,1;0rad)
  Points = (2) [(80722.7,9965.85,0),(78271,9965.85,-0.0147835)]
  Start = (89843.1,9965.85,0)
FEATURE [Part::Part2DObjectPython] Line554  # Draft 2D object (typed FeaturePython)
  ChamferSize = 0
  Closed = false
  End = (87391.5,10968.8,0)
  FilletRadius = 0
  Length = 488.203
  MakeFace = true
  Placement = pos=(9120.48,0,0) rot=(0,0,1;0rad)
  Points = (2) [(78759.2,10968.8,0),(78271,10968.8,0)]
  Start = (87879.7,10968.8,0)
FEATURE [Part::Part2DObjectPython] Rectangle117  # Draft 2D object (typed FeaturePython)
  ChamferSize = 0
  FilletRadius = 0
  Height = 150
  Length = 200
  MakeFace = true
  Placement = pos=(87879.7,10165.8,-0.0147835) rot=(0,0,-1;1.5708rad)
FEATURE [Part::Part2DObjectPython] Line555  # Draft 2D object (typed FeaturePython)
  ChamferSize = 0
  Closed = false
  End = (88262.7,10165.8,-0.0147835)
  FilletRadius = 0
  Length = 233.062
  MakeFace = true
  Placement = pos=(8499.48,-184.531,-0.0147835) rot=(0,0,1;0rad)
  Points = (2) [(79530.2,10350.4,0),(79763.2,10350.4,0)]
  Start = (88029.7,10165.8,-0.0147835)
FEATURE [Part::Part2DObjectPython] Line556  # Draft 2D object (typed FeaturePython)
  ChamferSize = 0
  Closed = false
  End = (88262.7,10175.8,-0.0147835)
  FilletRadius = 0
  Length = 233.062
  MakeFace = true
  Placement = pos=(8499.48,-184.531,-0.0147835) rot=(0,0,1;0rad)
  Points = (2) [(79530.2,10360.4,0),(79763.2,10360.4,0)]
  Start = (88029.7,10175.8,-0.0147835)
FEATURE [Part::Part2DObjectPython] Rectangle118  # Draft 2D object (typed FeaturePython)
  ChamferSize = 0
  FilletRadius = 0
  Height = 150
  Length = 200
  MakeFace = true
  Placement = pos=(87879.7,10365.8,-0.0147835) rot=(0,0,-1;1.5708rad)
FEATURE [Part::Part2DObjectPython] Rectangle119  # Draft 2D object (typed FeaturePython)
  ChamferSize = 0
  FilletRadius = 0
  Height = 150
  Length = 200
  MakeFace = true
  Placement = pos=(87879.7,10565.8,-0.0147835) rot=(0,0,-1;1.5708rad)
FEATURE [Part::Part2DObjectPython] Rectangle120  # Draft 2D object (typed FeaturePython)
  ChamferSize = 0
  FilletRadius = 0
  Height = 150
  Length = 200
  MakeFace = true
  Placement = pos=(87879.7,10965.8,-0.0147835) rot=(0,0,-1;1.5708rad)
FEATURE [Part::Part2DObjectPython] Rectangle121  # Draft 2D object (typed FeaturePython)
  ChamferSize = 0
  FilletRadius = 0
  Height = 150
  Length = 200
  MakeFace = true
  Placement = pos=(87879.7,10765.8,-0.0147835) rot=(0,0,-1;1.5708rad)
FEATURE [Part::Part2DObjectPython] Rectangle129  # Draft 2D object (typed FeaturePython)
  ChamferSize = 0
  FilletRadius = 0
  Height = 150
  Length = 200
  MakeFace = true
  Placement = pos=(87879.7,12515.4,0) rot=(0,0,-1;1.5708rad)
FEATURE [Part::Part2DObjectPython] Rectangle130  # Draft 2D object (typed FeaturePython)
  ChamferSize = 0
  FilletRadius = 0
  Height = 150
  Length = 200
  MakeFace = true
  Placement = pos=(87879.7,12765.8,-0.0147835) rot=(0,0,-1;1.5708rad)
FEATURE [Part::Part2DObjectPython] Rectangle131  # Draft 2D object (typed FeaturePython)
  ChamferSize = 0
  FilletRadius = 0
  Height = 150
  Length = 200
  MakeFace = true
  Placement = pos=(89385,12765.8,-0.0221752) rot=(0,0,-1;1.5708rad)
FEATURE [Part::Part2DObjectPython] Line557  # Draft 2D object (typed FeaturePython)
  ChamferSize = 0
  Closed = false
  End = (90047.7,11965.8,-0.0147835)
  FilletRadius = 0
  Length = 946.352
  MakeFace = true
  Points = (2) [(89101.4,11965.8,-0.0147835),(90047.7,11965.8,-0.0147835)]
  Start = (89101.4,11965.8,-0.0147835)
FEATURE [Part::Part2DObjectPython] Rectangle132  # Draft 2D object (typed FeaturePython)
  ChamferSize = 0
  FilletRadius = 0
  Height = 150
  Length = 200
  MakeFace = true
  Placement = pos=(89385,12565.8,-0.0221752) rot=(0,0,-1;1.5708rad)
FEATURE [Part::Part2DObjectPython] Rectangle133  # Draft 2D object (typed FeaturePython)
  ChamferSize = 0
  FilletRadius = 0
  Height = 150
  Length = 200
  MakeFace = true
  Placement = pos=(89385,12365.8,-0.0221752) rot=(0,0,-1;1.5708rad)
FEATURE [Part::Part2DObjectPython] Rectangle134  # Draft 2D object (typed FeaturePython)
  ChamferSize = 0
  FilletRadius = 0
  Height = 150
  Length = 200
  MakeFace = true
  Placement = pos=(89385,12165.8,-0.0221752) rot=(0,0,-1;1.5708rad)
FEATURE [App::FeaturePython] Dimension041  # Draft dimension (typed FeaturePython)
  Dimline = (85220.1,11846.8,-0.0147835)
  Direction = (0,0,0)
  Distance = 1200
  End = (85088.5,12165.8,-0.0147835)
  Normal = (-2e-12,0,1)
  Start = (85088.5,10965.8,-0.0147835)
FEATURE [Part::Part2DObjectPython] Line558  # Draft 2D object (typed FeaturePython)
  ChamferSize = 0
  Closed = false
  End = (89985.9,12165.8,-0.0147835)
  FilletRadius = 0
  Length = 4897.45
  MakeFace = true
  Points = (2) [(85088.5,12165.8,-0.0147835),(89985.9,12165.8,-0.0147835)]
  Start = (85088.5,12165.8,-0.0147835)
FEATURE [Part::Part2DObjectPython] DWire188  # Draft 2D object (typed FeaturePython)
  ChamferSize = 0
  Closed = true
  End = (65227.8,9965.85,-0.0147835)
  FilletRadius = 0
  Length = 1070.63
  MakeFace = true
  Points = (5) [(65095.4,9965.85,-0.0145023),(65095.4,9695.32,-0.0145023),(65360.2,9695.32,-0.0147835),(65360.2,9965.85,-0.0147835),(65227.8,9965.85,-0.0147835)]
  Start = (65095.4,9965.85,-0.0145023)
FEATURE [Part::Part2DObjectPython] Rectangle135  # Draft 2D object (typed FeaturePython)
  ChamferSize = 0
  FilletRadius = 0
  Height = 200
  Length = 200
  MakeFace = true
  Placement = pos=(79530.2,10150.4,0) rot=(0,0,-1;1.5708rad)
FEATURE [Part::Part2DObjectPython] DWire189  # Draft 2D object (typed FeaturePython)
  ChamferSize = 0
  Closed = true
  End = (72427,15165.8,-0.0147835)
  FilletRadius = 0
  Length = 1500
  MakeFace = true
  Points = (4) [(72427,15765.8,-0.0147835),(72577,15765.8,-0.0147835),(72577,15165.8,-0.0147835),(72427,15165.8,-0.0147835)]
  Start = (72427,15765.8,-0.0147835)
FEATURE [App::DocumentObjectGroup] Group032  label="fills"
  Group = -> [DWire159,DWire145,DWire146,DWire147,DWire148,DWire149,DWire150,DWire151,DWire152,DWire153,DWire154,DWire155,DWire156,DWire158,DWire189]
FEATURE [App::FeaturePython] Dimension042  # Draft dimension (typed FeaturePython)
  Dimline = (73228.2,13965.8,-7e-12)
  Direction = (0,0,0)
  Distance = 1000
  End = (72577,13965.8,-0.0147835)
  Normal = (-2e-12,0,1)
  Start = (72577,12965.8,-0.0147835)
FEATURE [App::FeaturePython] Dimension043  # Draft dimension (typed FeaturePython)
  Dimline = (73228.2,13965.8,-7e-12)
  Direction = (0,0,0)
  Distance = 1200
  End = (72577,15165.8,-0.0147835)
  Normal = (-2e-12,0,1)
  Start = (72577,13965.8,-0.0147835)
FEATURE [App::FeaturePython] Dimension044  # Draft dimension (typed FeaturePython)
  Dimline = (73228.2,15165.8,-7e-12)
  Direction = (0,0,0)
  Distance = 600
  End = (72577,15165.8,-0.0147835)
  Normal = (-2e-12,0,1)
  Start = (72577,15765.8,-0.0147835)
FEATURE [Part::Part2DObjectPython] DWire190  # Draft 2D object (typed FeaturePython)
  ChamferSize = 0
  Closed = true
  End = (73577,9965.85,-0.0147835)
  FilletRadius = 0
  Length = 2200
  MakeFace = true
  Points = (4) [(72577,9965.85,-0.0147835),(72577,9865.85,-0.0147835),(73577,9865.85,-0.0147835),(73577,9965.85,-0.0147835)]
  Start = (72577,9965.85,-0.0147835)
FEATURE [Part::Part2DObjectPython] DWire192  # Draft 2D object (typed FeaturePython)
  ChamferSize = 0
  Closed = true
  End = (102514,9965.85,-0.0147834)
  FilletRadius = 0
  Length = 2200
  MakeFace = true
  Placement = pos=(28936.7,0,4.0881e-08) rot=(0,0,1;0rad)
  Points = (4) [(72577,9965.85,-0.0147835),(72577,9865.85,-0.0147835),(73577,9865.85,-0.0147835),(73577,9965.85,-0.0147835)]
  Start = (101514,9965.85,-0.0147834)
FEATURE [Part::Part2DObjectPython] DWire193  # Draft 2D object (typed FeaturePython)
  ChamferSize = 0
  Closed = true
  End = (98520.7,12765.8,-0.0145023)
  FilletRadius = 0
  Length = 6360
  MakeFace = true
  Placement = pos=(28923.7,0,5.5244e-08) rot=(0,0,1;0rad)
  Points = (4) [(69597,12965.8,-0.0145023),(72577,12965.8,-0.0145023),(72577,12765.8,-0.0145023),(69597,12765.8,-0.0145023)]
  Start = (98520.7,12965.8,-0.0145023)
FEATURE [Part::Part2DObjectPython] DWire196  # Draft 2D object (typed FeaturePython)
  ChamferSize = 0
  Closed = true
  End = (87500.6,15765.8,-0.0147834)
  FilletRadius = 0
  Length = 28400
  MakeFace = true
  Placement = pos=(28923.7,0,5.5244e-08) rot=(0,0,1;0rad)
  Points = (4) [(58577,15965.8,-0.0147835),(72577,15965.8,-0.0147835),(72577,15765.8,-0.0147835),(58577,15765.8,-0.0147835)]
  Start = (87500.6,15965.8,-0.0147834)
FEATURE [Part::Part2DObjectPython] Rectangle136  # Draft 2D object (typed FeaturePython)
  ChamferSize = 0
  FilletRadius = 0
  Height = 150
  Length = 200
  MakeFace = true
  Placement = pos=(101351,13965.8,-0.0147834) rot=(0,0,-1;1.5708rad)
FEATURE [Part::Part2DObjectPython] Rectangle137  # Draft 2D object (typed FeaturePython)
  ChamferSize = 0
  FilletRadius = 0
  Height = 150
  Length = 200
  MakeFace = true
  Placement = pos=(101351,13765.8,-0.0147834) rot=(0,0,-1;1.5708rad)
FEATURE [Part::Part2DObjectPython] Rectangle138  # Draft 2D object (typed FeaturePython)
  ChamferSize = 0
  FilletRadius = 0
  Height = 150
  Length = 200
  MakeFace = true
  Placement = pos=(101351,13565.8,-0.0147834) rot=(0,0,-1;1.5708rad)
FEATURE [Part::Part2DObjectPython] Rectangle139  # Draft 2D object (typed FeaturePython)
  ChamferSize = 0
  FilletRadius = 0
  Height = 150
  Length = 200
  MakeFace = true
  Placement = pos=(101351,13365.8,-0.0147834) rot=(0,0,-1;1.5708rad)
FEATURE [Part::Part2DObjectPython] Rectangle140  # Draft 2D object (typed FeaturePython)
  ChamferSize = 0
  FilletRadius = 0
  Height = 150
  Length = 200
  MakeFace = true
  Placement = pos=(101351,13165.8,-0.0147834) rot=(0,0,-1;1.5708rad)
FEATURE [Part::Part2DObjectPython] Rectangle141  # Draft 2D object (typed FeaturePython)
  ChamferSize = 0
  FilletRadius = 0
  Height = 150
  Length = 200
  MakeFace = true
  Placement = pos=(101351,15765.8,-0.0147834) rot=(0,0,-1;1.5708rad)
FEATURE [Part::Part2DObjectPython] Rectangle142  # Draft 2D object (typed FeaturePython)
  ChamferSize = 0
  FilletRadius = 0
  Height = 150
  Length = 200
  MakeFace = true
  Placement = pos=(101351,15565.8,-0.0147834) rot=(0,0,-1;1.5708rad)
FEATURE [Part::Part2DObjectPython] Rectangle143  # Draft 2D object (typed FeaturePython)
  ChamferSize = 0
  FilletRadius = 0
  Height = 150
  Length = 200
  MakeFace = true
  Placement = pos=(101351,15365.8,-0.0147834) rot=(0,0,-1;1.5708rad)
FEATURE [Part::Part2DObjectPython] Rectangle144  # Draft 2D object (typed FeaturePython)
  ChamferSize = 0
  FilletRadius = 0
  Height = 150
  Length = 200
  MakeFace = true
  Placement = pos=(101351,10165.8,-0.0147834) rot=(0,0,-1;1.5708rad)
FEATURE [Part::Part2DObjectPython] Rectangle145  # Draft 2D object (typed FeaturePython)
  ChamferSize = 0
  FilletRadius = 0
  Height = 150
  Length = 200
  MakeFace = true
  Placement = pos=(101351,10365.8,-0.0147834) rot=(0,0,-1;1.5708rad)
FEATURE [Part::Part2DObjectPython] Rectangle146  # Draft 2D object (typed FeaturePython)
  ChamferSize = 0
  FilletRadius = 0
  Height = 150
  Length = 200
  MakeFace = true
  Placement = pos=(101351,10565.8,-0.0147834) rot=(0,0,-1;1.5708rad)
FEATURE [Part::Part2DObjectPython] Rectangle147  # Draft 2D object (typed FeaturePython)
  ChamferSize = 0
  FilletRadius = 0
  Height = 150
  Length = 200
  MakeFace = true
  Placement = pos=(101351,10765.8,-0.0147834) rot=(0,0,-1;1.5708rad)
FEATURE [Part::Part2DObjectPython] Rectangle148  # Draft 2D object (typed FeaturePython)
  ChamferSize = 0
  FilletRadius = 0
  Height = 150
  Length = 200
  MakeFace = true
  Placement = pos=(101351,10965.8,-0.0147834) rot=(0,0,-1;1.5708rad)
FEATURE [Part::Part2DObjectPython] Rectangle149  # Draft 2D object (typed FeaturePython)
  ChamferSize = 0
  FilletRadius = 0
  Height = 150
  Length = 200
  MakeFace = true
  Placement = pos=(101351,11165.8,-0.0147834) rot=(0,0,-1;1.5708rad)
FEATURE [Part::Part2DObjectPython] Rectangle150  # Draft 2D object (typed FeaturePython)
  ChamferSize = 0
  FilletRadius = 0
  Height = 150
  Length = 200
  MakeFace = true
  Placement = pos=(101351,11365.8,-0.0147834) rot=(0,0,-1;1.5708rad)
FEATURE [Part::Part2DObjectPython] Rectangle151  # Draft 2D object (typed FeaturePython)
  ChamferSize = 0
  FilletRadius = 0
  Height = 150
  Length = 200
  MakeFace = true
  Placement = pos=(101351,11565.8,-0.0147834) rot=(0,0,-1;1.5708rad)
FEATURE [Part::Part2DObjectPython] Rectangle152  # Draft 2D object (typed FeaturePython)
  ChamferSize = 0
  FilletRadius = 0
  Height = 150
  Length = 200
  MakeFace = true
  Placement = pos=(101351,11765.8,-0.0147834) rot=(0,0,-1;1.5708rad)
FEATURE [Part::Part2DObjectPython] Rectangle153  # Draft 2D object (typed FeaturePython)
  ChamferSize = 0
  FilletRadius = 0
  Height = 150
  Length = 200
  MakeFace = true
  Placement = pos=(101351,11965.8,-0.0147834) rot=(0,0,-1;1.5708rad)
FEATURE [Part::Part2DObjectPython] Rectangle154  # Draft 2D object (typed FeaturePython)
  ChamferSize = 0
  FilletRadius = 0
  Height = 150
  Length = 200
  MakeFace = true
  Placement = pos=(101351,12165.8,-0.0147834) rot=(0,0,-1;1.5708rad)
FEATURE [Part::Part2DObjectPython] Rectangle155  # Draft 2D object (typed FeaturePython)
  ChamferSize = 0
  FilletRadius = 0
  Height = 150
  Length = 200
  MakeFace = true
  Placement = pos=(101351,12365.8,-0.0147834) rot=(0,0,-1;1.5708rad)
FEATURE [Part::Part2DObjectPython] Rectangle156  # Draft 2D object (typed FeaturePython)
  ChamferSize = 0
  FilletRadius = 0
  Height = 150
  Length = 200
  MakeFace = true
  Placement = pos=(101351,12565.8,-0.0147834) rot=(0,0,-1;1.5708rad)
FEATURE [Part::Part2DObjectPython] Rectangle157  # Draft 2D object (typed FeaturePython)
  ChamferSize = 0
  FilletRadius = 0
  Height = 150
  Length = 200
  MakeFace = true
  Placement = pos=(101351,12765.8,-0.0147834) rot=(0,0,-1;1.5708rad)
FEATURE [Part::Part2DObjectPython] Rectangle158  # Draft 2D object (typed FeaturePython)
  ChamferSize = 0
  FilletRadius = 0
  Height = 200
  Length = 200
  MakeFace = true
  Placement = pos=(101301,9965.85,-0.0147834) rot=(0,0,-1;1.5708rad)
FEATURE [Part::Part2DObjectPython] Rectangle159  # Draft 2D object (typed FeaturePython)
  ChamferSize = 0
  FilletRadius = 0
  Height = 150
  Length = 200
  MakeFace = true
  Placement = pos=(101744,10365.5,-0.0147835) rot=(0,0,-1;1.5708rad)
FEATURE [Part::Part2DObjectPython] DWire197  # Draft 2D object (typed FeaturePython)
  ChamferSize = 0
  Closed = true
  End = (101288,9965.85,-0.0147834)
  FilletRadius = 0
  Length = 1594
  MakeFace = true
  Placement = pos=(27710.7,-0.000123435,8.7186e-08) rot=(0,0,1;0rad)
  Points = (4) [(72880,9965.85,-0.0147835),(72880,9865.85,-0.0147835),(73577,9865.85,-0.0147835),(73577,9965.85,-0.0147835)]
  Start = (100591,9965.85,-0.0147834)
FEATURE [Image::ImagePlane] ImagePlane
  XSize = 100
  YSize = 100
FEATURE [App::FeaturePython] Dimension045  # Draft dimension (typed FeaturePython)
  Dimline = (101658,12799.5,0)
  Direction = (0,0,0)
  Distance = 200
  End = (101501,12765.8,-0.0145023)
  Normal = (0,0,1)
  Start = (101501,12965.8,-0.0145023)
FEATURE [Part::Part2DObjectPython] Line566  # Draft 2D object (typed FeaturePython)
  ChamferSize = 0
  Closed = false
  End = (101501,9654.81,-0.0147834)
  FilletRadius = 0
  Length = 311.043
  MakeFace = true
  Points = (2) [(101501,9965.85,-0.0147834),(101501,9654.81,-0.0147834)]
  Start = (101501,9965.85,-0.0147834)
FEATURE [Part::Part2DObjectPython] Line567  # Draft 2D object (typed FeaturePython)
  ChamferSize = 0
  Closed = false
  End = (101514,9654.81,-0.00881434)
  FilletRadius = 0
  Length = 311.043
  MakeFace = true
  Points = (2) [(101514,9965.85,-0.0147834),(101514,9654.81,-0.00881434)]
  Start = (101514,9965.85,-0.0147834)
FEATURE [Part::Part2DObjectPython] BezCurve  # Draft 2D object (typed FeaturePython)
  Closed = false
  Degree = 5
  MakeFace = true
  Points = (6) [(101288,9965.85,-0.0147834),(101290,9960.83,0),(101295,9959.36,0),(101297,9962.54,0),(101300,9964.98,0),(101301,9965.85,-0.0147834)]
FEATURE [Part::Feature] BezCurve001
  Placement = pos=(0.0013317,-3.40808,6.5405e-05) rot=(0,0,1;0rad)
  shape: bbox 13 x 4.94 x 0.01478 mm, 0 faces, 0 solids (baked)
FEATURE [Part::Feature] BezCurve002
  Placement = pos=(0.001332,-6.01453,0.00011543) rot=(0,0,1;0rad)
  shape: bbox 13 x 4.94 x 0.01478 mm, 0 faces, 0 solids (baked)
FEATURE [Part::Feature] BezCurve003
  Placement = pos=(0.0026637,-13.99,0.000268492) rot=(0,0,1;0rad)
  shape: bbox 13 x 4.94 x 0.01478 mm, 0 faces, 0 solids (baked)
FEATURE [Part::Feature] BezCurve004
  Placement = pos=(0.0026634,-11.3835,0.000218467) rot=(0,0,1;0rad)
  shape: bbox 13 x 4.94 x 0.01478 mm, 0 faces, 0 solids (baked)
FEATURE [Part::Feature] BezCurve005
  Placement = pos=(0.0013317,-7.97546,0.000153062) rot=(0,0,1;0rad)
  shape: bbox 13 x 4.94 x 0.01478 mm, 0 faces, 0 solids (baked)
FEATURE [Part::Feature] BezCurve006
  Placement = pos=(0.0026634,-25.782,0.000494778) rot=(0,0,1;0rad)
  shape: bbox 13 x 4.94 x 0.01478 mm, 0 faces, 0 solids (baked)
FEATURE [Part::Feature] BezCurve007
  Placement = pos=(0.0013317,-17.8065,0.000341716) rot=(0,0,1;0rad)
  shape: bbox 13 x 4.94 x 0.01478 mm, 0 faces, 0 solids (baked)
FEATURE [Part::Feature] BezCurve008
  Placement = pos=(0.0026634,-21.2146,0.000407121) rot=(0,0,1;0rad)
  shape: bbox 13 x 4.94 x 0.01478 mm, 0 faces, 0 solids (baked)
FEATURE [Part::Feature] BezCurve009
  Placement = pos=(0.0026637,-23.821,0.000457146) rot=(0,0,1;0rad)
  shape: bbox 13 x 4.94 x 0.01478 mm, 0 faces, 0 solids (baked)
FEATURE [Part::Feature] BezCurve010
  Placement = pos=(0.0039954,-31.7965,0.000610208) rot=(0,0,1;0rad)
  shape: bbox 13 x 4.94 x 0.01478 mm, 0 faces, 0 solids (baked)
FEATURE [Part::Feature] BezCurve011
  Placement = pos=(0.0039951,-29.1901,0.000560183) rot=(0,0,1;0rad)
  shape: bbox 13 x 4.94 x 0.01478 mm, 0 faces, 0 solids (baked)
FEATURE [Part::Feature] BezCurve012
  Placement = pos=(0.0013317,-36.5741,0.000701882) rot=(0,0,1;0rad)
  shape: bbox 13 x 4.94 x 0.01478 mm, 0 faces, 0 solids (baked)
FEATURE [Part::Feature] BezCurve013
  Placement = pos=(0.0026634,-54.3806,0.0010436) rot=(0,0,1;0rad)
  shape: bbox 13 x 4.94 x 0.01478 mm, 0 faces, 0 solids (baked)
FEATURE [Part::Feature] BezCurve014
  Placement = pos=(0.0039954,-50.5641,0.000970374) rot=(0,0,1;0rad)
  shape: bbox 13 x 4.94 x 0.01478 mm, 0 faces, 0 solids (baked)
FEATURE [Part::Feature] BezCurve015
  Placement = pos=(0.0026634,-44.5496,0.000854944) rot=(0,0,1;0rad)
  shape: bbox 13 x 4.94 x 0.01478 mm, 0 faces, 0 solids (baked)
FEATURE [Part::Feature] BezCurve016
  Placement = pos=(0.0026634,-39.9822,0.000767287) rot=(0,0,1;0rad)
  shape: bbox 13 x 4.94 x 0.01478 mm, 0 faces, 0 solids (baked)
FEATURE [Part::Feature] BezCurve017
  Placement = pos=(0.0026637,-42.5886,0.000817312) rot=(0,0,1;0rad)
  shape: bbox 13 x 4.94 x 0.01478 mm, 0 faces, 0 solids (baked)
FEATURE [Part::Feature] BezCurve018
  Placement = pos=(0.0039951,-57.7887,0.001109) rot=(0,0,1;0rad)
  shape: bbox 13 x 4.94 x 0.01478 mm, 0 faces, 0 solids (baked)
FEATURE [Part::Feature] BezCurve019
  Placement = pos=(0.0039951,-62.3561,0.00119666) rot=(0,0,1;0rad)
  shape: bbox 13 x 4.94 x 0.01478 mm, 0 faces, 0 solids (baked)
FEATURE [Part::Feature] BezCurve020
  Placement = pos=(0.0039951,-47.9576,0.000920349) rot=(0,0,1;0rad)
  shape: bbox 13 x 4.94 x 0.01478 mm, 0 faces, 0 solids (baked)
FEATURE [Part::Feature] BezCurve021
  Placement = pos=(0.0039954,-60.3951,0.00115903) rot=(0,0,1;0rad)
  shape: bbox 13 x 4.94 x 0.01478 mm, 0 faces, 0 solids (baked)
FEATURE [Part::Feature] BezCurve022
  Placement = pos=(0.0053271,-68.3706,0.00131209) rot=(0,0,1;0rad)
  shape: bbox 13 x 4.94 x 0.01478 mm, 0 faces, 0 solids (baked)
FEATURE [Part::Feature] BezCurve023
  Placement = pos=(0.0053268,-65.7642,0.00126207) rot=(0,0,1;0rad)
  shape: bbox 13 x 4.94 x 0.01478 mm, 0 faces, 0 solids (baked)
FEATURE [Part::Feature] BezCurve025
  Placement = pos=(0.001332,-72.6327,0.00139387) rot=(0,0,1;0rad)
  shape: bbox 13 x 4.94 x 0.01478 mm, 0 faces, 0 solids (baked)
FEATURE [Part::Feature] BezCurve026
  Placement = pos=(0.0026637,-90.4392,0.00173558) rot=(0,0,1;0rad)
  shape: bbox 13 x 4.94 x 0.01478 mm, 0 faces, 0 solids (baked)
FEATURE [Part::Feature] BezCurve027
  Placement = pos=(0.0039957,-86.6227,0.00166236) rot=(0,0,1;0rad)
  shape: bbox 13 x 4.94 x 0.01478 mm, 0 faces, 0 solids (baked)
FEATURE [Part::Feature] BezCurve029
  Placement = pos=(0.0026637,-80.6082,0.00154693) rot=(0,0,1;0rad)
  shape: bbox 13 x 4.94 x 0.01478 mm, 0 faces, 0 solids (baked)
FEATURE [Part::Feature] BezCurve030
  Placement = pos=(0.0026637,-76.0408,0.00145927) rot=(0,0,1;0rad)
  shape: bbox 13 x 4.94 x 0.01478 mm, 0 faces, 0 solids (baked)
FEATURE [Part::Feature] BezCurve031
  Placement = pos=(0.002664,-78.6472,0.0015093) rot=(0,0,1;0rad)
  shape: bbox 13 x 4.94 x 0.01478 mm, 0 faces, 0 solids (baked)
FEATURE [Part::Feature] BezCurve033
  Placement = pos=(0.0039954,-93.8473,0.00180099) rot=(0,0,1;0rad)
  shape: bbox 13 x 4.94 x 0.01478 mm, 0 faces, 0 solids (baked)
FEATURE [Part::Feature] BezCurve035
  Placement = pos=(0.0039954,-84.0162,0.00161233) rot=(0,0,1;0rad)
  shape: bbox 13 x 4.94 x 0.01478 mm, 0 faces, 0 solids (baked)
FEATURE [Part::Part2DObjectPython] DWire199  # Draft 2D object (typed FeaturePython)
  ChamferSize = 0
  Closed = true
  End = (101301,9965.85,-0.0147834)
  FilletRadius = 0
  Length = 226
  MakeFace = true
  Points = (4) [(101288,9965.85,-0.0147834),(101288,9865.85,-0.0147834),(101301,9865.85,-0.0128644),(101301,9965.85,-0.0147834)]
  Start = (101288,9965.85,-0.0147834)
FEATURE [App::DocumentObjectGroup] Group033  label="13mm expansion joint"
  Group = -> [BezCurve,BezCurve001,BezCurve002,BezCurve003,BezCurve004,BezCurve005,BezCurve006,BezCurve007,BezCurve008,BezCurve009,BezCurve010,BezCurve011,BezCurve012,BezCurve013,BezCurve014,BezCurve015,BezCurve016,BezCurve017,BezCurve018,BezCurve019,BezCurve020,BezCurve021,BezCurve022,BezCurve023,BezCurve025,BezCurve026,BezCurve027,BezCurve029,BezCurve030,BezCurve031,BezCurve033,BezCurve035,DWire199]
FEATURE [Part::Part2DObjectPython] Rectangle161  # Draft 2D object (typed FeaturePython)
  ChamferSize = 0
  FilletRadius = 0
  Height = -391.441
  Length = -35.7096
  MakeFace = true
  Placement = pos=(101301,9865.85,-0.0128644) rot=(0,0,1;0rad)
FEATURE [Part::Part2DObjectPython] DWire200  # Draft 2D object (typed FeaturePython)
  ChamferSize = 0
  Closed = true
  End = (101265,9860.85,-0.0128644)
  FilletRadius = 0
  Length = 1548.58
  MakeFace = false
  Placement = pos=(27688,-105,0.00191913) rot=(0,0,1;0rad)
  Points = (4) [(72902.7,9965.85,-0.0167025),(72902.7,9865.85,-0.00191913),(73577,9865.85,-0.0147835),(73577,9965.85,-0.0147835)]
  Start = (100591,9860.85,-0.0147834)
FEATURE [Sketcher::SketchObject] Sketch066
  Placement = pos=(4595,6879.37,3092.06) rot=(0.57735,0.57735,0.57735;2.0944rad)
  sketch-geometry (8):
    g0: LineSegment StartX=0 StartY=0 StartZ=0 EndX=1000 EndY=0 EndZ=0
    g1: LineSegment StartX=1000 StartY=0 StartZ=0 EndX=1000 EndY=2200 EndZ=0
    g2: LineSegment StartX=1000 StartY=2200 StartZ=0 EndX=0 EndY=2200 EndZ=0
    g3: LineSegment StartX=0 StartY=2200 StartZ=0 EndX=0 EndY=0 EndZ=0
    g4: LineSegment StartX=50 StartY=0 StartZ=0 EndX=950 EndY=0 EndZ=0
    g5: LineSegment StartX=950 StartY=0 StartZ=0 EndX=950 EndY=2150 EndZ=0
    g6: LineSegment StartX=950 StartY=2150 StartZ=0 EndX=50 EndY=2150 EndZ=0
    g7: LineSegment StartX=50 StartY=2150 StartZ=0 EndX=50 EndY=0 EndZ=0
  constraints (23):
    c: Coincident(g0,g1)
    c: Coincident(g1,g2)
    c: Coincident(g2,g3)
    c: Coincident(g3,g0)
    c: Horizontal(g0)
    c: Horizontal(g2)
    c: Vertical(g1)
    c: Vertical(g3)
    c: Coincident(g4,g5)
    c: Coincident(g5,g6)
    c: Coincident(g6,g7)
    c: Coincident(g7,g4)
    c: Horizontal(g4)
    c: Horizontal(g6)
    c: Vertical(g5)
    c: Vertical(g7)
    c: DistanceY(g1) = 2200
    c: DistanceX(g0) = 1000
    c: DistanceY(g6,g2) = 50
    c: DistanceX(g2,g6) = 50
    c: DistanceX(g4,g0) = 50
    c: DistanceY(g0,g4) = 0
    c: Coincident(g0,g-1)
FEATURE [Part::FeaturePython] Window055  label="Window053"  # WARN: FeaturePython — macro-defined, semantics opaque (R4)
  Base = -> Sketch066
  Height = 2200
  HoleDepth = 0
  MoveWithHost = true
  Normal = (-1,0,0)
  Placement = pos=(0,-729.366,-92.0593) rot=(0,0,1;0rad)
  Preset = 6
  Role = 1
  Width = 1000
  WindowParts = OuterFrame | Frame | Wire0,Wire1 | 150.0 | 0.0 | Door | Solid panel | Wire1 | 50.0 | 50.0
FEATURE [Part::FeaturePython] Wall057  # WARN: FeaturePython — macro-defined, semantics opaque (R4)
  Align = 1
  Base = -> Line052
  Face = 0
  Height = 2800
  Length = 0
  MoveWithHost = false
  Normal = (0,0,0)
  Role = 0
  Subtractions = -> [Window055]
  Width = 150
FEATURE [Part::Part2DObjectPython] Line568  # Draft 2D object (typed FeaturePython)
  ChamferSize = 0
  Closed = false
  End = (4170.48,6050,3000)
  FilletRadius = 0
  Length = 274.521
  MakeFace = true
  Points = (2) [(4445,6050,3000),(4170.48,6050,3000)]
  Start = (4445,6050,3000)
  Support = -> Cut
FEATURE [Part::Part2DObjectPython] Line569  # Draft 2D object (typed FeaturePython)
  ChamferSize = 0
  Closed = false
  End = (4170.48,6150,3000)
  FilletRadius = 0
  Length = 624.724
  MakeFace = true
  Points = (2) [(4795.2,6150,3000),(4170.48,6150,3000)]
  Start = (4795.2,6150,3000)
FEATURE [Part::Part2DObjectPython] Line570  # Draft 2D object (typed FeaturePython)
  ChamferSize = 0
  Closed = false
  End = (4170.48,7150,3000)
  FilletRadius = 0
  Length = 624.724
  MakeFace = true
  Points = (2) [(4795.2,7150,3000),(4170.48,7150,3000)]
  Start = (4795.2,7150,3000)
FEATURE [Part::Part2DObjectPython] Line571  # Draft 2D object (typed FeaturePython)
  ChamferSize = 0
  Closed = false
  End = (4170.48,7250,3000)
  FilletRadius = 0
  Length = 624.724
  MakeFace = true
  Points = (2) [(4795.2,7250,3000),(4170.48,7250,3000)]
  Start = (4795.2,7250,3000)
FEATURE [Part::Part2DObjectPython] Line572  # Draft 2D object (typed FeaturePython)
  ChamferSize = 0
  Closed = false
  End = (145,7250,3000)
  FilletRadius = 0
  Length = 4300
  MakeFace = true
  Points = (2) [(4445,7250,3000),(145,7250,3000)]
  Start = (4445,7250,3000)
FEATURE [Part::Part2DObjectPython] Arc019  # Draft 2D object (typed FeaturePython)
  FirstAngle = 90
  LastAngle = 179.976
  MakeFace = true
  Placement = pos=(25798,12969.6,0) rot=(0,0,-1;1.57037rad)
  Radius = 900
FEATURE [Part::Part2DObjectPython] Line574  # Draft 2D object (typed FeaturePython)
  ChamferSize = 0
  Closed = false
  End = (25798.4,12969.6,0)
  FilletRadius = 0
  Length = 900
  MakeFace = true
  Placement = pos=(-6600,-8.9406e-05,0) rot=(0,0,1;0rad)
  Points = (2) [(32398,13869.6,0),(32398.4,12969.6,0)]
  Start = (25798,13869.6,0)
FEATURE [Sketcher::SketchObject] Sketch067
  Placement = pos=(1839,7230,3000) rot=(1,0,0;1.5708rad)
  sketch-geometry (8):
    g0: LineSegment StartX=0 StartY=0 StartZ=0 EndX=1000 EndY=0 EndZ=0
    g1: LineSegment StartX=1000 StartY=0 StartZ=0 EndX=1000 EndY=2200 EndZ=0
    g2: LineSegment StartX=1000 StartY=2200 StartZ=0 EndX=0 EndY=2200 EndZ=0
    g3: LineSegment StartX=0 StartY=2200 StartZ=0 EndX=0 EndY=0 EndZ=0
    g4: LineSegment StartX=50 StartY=0 StartZ=0 EndX=950 EndY=0 EndZ=0
    g5: LineSegment StartX=950 StartY=0 StartZ=0 EndX=950 EndY=2150 EndZ=0
    g6: LineSegment StartX=950 StartY=2150 StartZ=0 EndX=50 EndY=2150 EndZ=0
    g7: LineSegment StartX=50 StartY=2150 StartZ=0 EndX=50 EndY=0 EndZ=0
  constraints (23):
    c: Coincident(g0,g1)
    c: Coincident(g1,g2)
    c: Coincident(g2,g3)
    c: Coincident(g3,g0)
    c: Horizontal(g0)
    c: Horizontal(g2)
    c: Vertical(g1)
    c: Vertical(g3)
    c: Coincident(g4,g5)
    c: Coincident(g5,g6)
    c: Coincident(g6,g7)
    c: Coincident(g7,g4)
    c: Horizontal(g4)
    c: Horizontal(g6)
    c: Vertical(g5)
    c: Vertical(g7)
    c: DistanceY(g1) = 2200
    c: DistanceX(g0) = 1000
    c: DistanceY(g6,g2) = 50
    c: DistanceX(g2,g6) = 50
    c: DistanceX(g4,g0) = 50
    c: DistanceY(g0,g4) = 0
    c: Coincident(g0,g-1)
FEATURE [Part::FeaturePython] Window056  label="Window054"  # WARN: FeaturePython — macro-defined, semantics opaque (R4)
  Base = -> Sketch067
  Height = 2200
  HoleDepth = 0
  MoveWithHost = true
  Normal = (0,1,0)
  Placement = pos=(-1594,20,0) rot=(0,0,1;0rad)
  Preset = 6
  Role = 1
  Width = 1000
  WindowParts = OuterFrame | Frame | Wire0,Wire1 | 150.0 | 0.0 | Door | Solid panel | Wire1 | 50.0 | 50.0
FEATURE [Part::FeaturePython] Wall094  # WARN: FeaturePython — macro-defined, semantics opaque (R4)
  Align = 0
  Base = -> Line572
  Face = 0
  Height = 2800
  Length = 0
  MoveWithHost = false
  Normal = (0,0,0)
  Role = 0
  Subtractions = -> [Window056]
  Width = 150
FEATURE [App::DocumentObjectGroup] Group002  label="LEVEL 2 WALLS"
  Group = -> [Wall078,Wall058,Wall057,Wall055,Wall054,Wall053,Wall052,Wall051,Wall050,Wall049,Wall048,Wall047,Wall045,Wall042,Wall041,Wall038,Wall037,Wall035,Wall034,Wall033,Wall030,Wall029,Wall028,Wall027,Wall026,Wall025,Wall024,Wall023,Wall085,Wall094]
FEATURE [Part::Part2DObjectPython] Line575  # Draft 2D object (typed FeaturePython)
  ChamferSize = 0
  Closed = false
  End = (42437,7349.61,0)
  FilletRadius = 0
  Length = 900
  MakeFace = true
  Placement = pos=(10038.6,-5620,0) rot=(0,0,1;0rad)
  Points = (2) [(32398,13869.6,0),(32398.4,12969.6,0)]
  Start = (42436.6,8249.61,0)
FEATURE [Part::Part2DObjectPython] Arc020  # Draft 2D object (typed FeaturePython)
  FirstAngle = 90
  LastAngle = 179.976
  MakeFace = true
  Placement = pos=(42436.6,7349.61,0) rot=(0,0,-1;1.57037rad)
  Radius = 900
FEATURE [Part::Part2DObjectPython] Line576  # Draft 2D object (typed FeaturePython)
  ChamferSize = 0
  Closed = false
  End = (22414,7249.61,0)
  FilletRadius = 0
  Length = 20973
  MakeFace = true
  Points = (2) [(43387,7249.61,0),(22414,7249.61,0)]
  Start = (43387,7249.61,0)
FEATURE [Part::Part2DObjectPython] Line577  # Draft 2D object (typed FeaturePython)
  ChamferSize = 0
  Closed = false
  End = (55743,4649.61,0)
  FilletRadius = 0
  Length = 27144.6
  MakeFace = true
  Points = (2) [(28598.4,4649.61,0),(55743,4649.61,0)]
  Start = (28598.4,4649.61,0)
FEATURE [Part::Part2DObjectPython] Line578  # Draft 2D object (typed FeaturePython)
  ChamferSize = 0
  Closed = false
  End = (33636,6049.61,0)
  FilletRadius = 0
  Length = 4887.62
  MakeFace = true
  Points = (2) [(28748.4,6049.61,0),(33636,6049.61,0)]
  Start = (28748.4,6049.61,0)
FEATURE [Part::Part2DObjectPython] Line579  # Draft 2D object (typed FeaturePython)
  ChamferSize = 0
  Closed = false
  End = (31448.4,1999.61,0)
  FilletRadius = 0
  Length = 2850
  MakeFace = true
  Points = (2) [(28598.4,1999.61,0),(31448.4,1999.61,0)]
  Start = (28598.4,1999.61,0)
FEATURE [Part::Part2DObjectPython] Rectangle162  # Draft 2D object (typed FeaturePython)
  ChamferSize = 0
  FilletRadius = 0
  Height = -3600
  Length = 7750
  MakeFace = true
  Placement = pos=(45387,5749.61,0) rot=(0,0,1;0rad)
FEATURE [Part::Part2DObjectPython] Line580  # Draft 2D object (typed FeaturePython)
  ChamferSize = 0
  Closed = false
  End = (24098.4,5749.61,0)
  FilletRadius = 0
  Length = 21138.6
  MakeFace = true
  Points = (2) [(45237,5749.61,0),(24098.4,5749.61,0)]
  Start = (45237,5749.61,0)
FEATURE [Part::Part2DObjectPython] Line581  # Draft 2D object (typed FeaturePython)
  ChamferSize = 0
  Closed = false
  End = (23164,6049.61,0)
  FilletRadius = 0
  Length = 23573
  MakeFace = true
  Points = (2) [(46737,6049.61,0),(23164,6049.61,0)]
  Start = (46737,6049.61,0)
FEATURE [Part::Part2DObjectPython] Line582  # Draft 2D object (typed FeaturePython)
  ChamferSize = 0
  Closed = false
  End = (31298.4,6049.61,0)
  FilletRadius = 0
  Length = 2200
  MakeFace = true
  Points = (2) [(31298.4,8249.61,0),(31298.4,6049.61,0)]
  Start = (31298.4,8249.61,0)
FEATURE [Part::Part2DObjectPython] Line583  # Draft 2D object (typed FeaturePython)
  ChamferSize = 0
  Closed = false
  End = (29948.4,1997,0)
  FilletRadius = 0
  Length = 6252.61
  MakeFace = true
  Points = (2) [(29948.4,8249.61,0),(29948.4,1997,0)]
  Start = (29948.4,8249.61,0)
FEATURE [Part::Part2DObjectPython] Line584  # Draft 2D object (typed FeaturePython)
  ChamferSize = 0
  Closed = false
  End = (25648.4,4499.61,0)
  FilletRadius = 0
  Length = 2950
  MakeFace = true
  Points = (2) [(28598.4,4499.61,0),(25648.4,4499.61,0)]
  Start = (28598.4,4499.61,0)
FEATURE [Part::Part2DObjectPython] Line585  # Draft 2D object (typed FeaturePython)
  ChamferSize = 0
  Closed = false
  End = (25648.4,5123.31,0)
  FilletRadius = 0
  Length = 4300
  MakeFace = true
  Points = (2) [(29948.4,5123.31,0),(25648.4,5123.31,0)]
  Start = (29948.4,5123.31,0)
FEATURE [Part::Part2DObjectPython] Line586  # Draft 2D object (typed FeaturePython)
  ChamferSize = 0
  Closed = false
  End = (47162,5899.61,0)
  FilletRadius = 0
  Length = 3750
  MakeFace = true
  Points = (2) [(47162,2149.61,0),(47162,5899.61,0)]
  Start = (47162,2149.61,0)
FEATURE [Part::Part2DObjectPython] Line587  # Draft 2D object (typed FeaturePython)
  ChamferSize = 0
  Closed = false
  End = (38434,2149.61,1)
  FilletRadius = 0
  Length = 2085.62
  MakeFace = true
  Points = (2) [(36348.4,2149.61,1),(38434,2149.61,1)]
  Start = (36348.4,2149.61,1)
FEATURE [Part::Part2DObjectPython] Line589  # Draft 2D object (typed FeaturePython)
  ChamferSize = 0
  Closed = false
  End = (28748.4,6049.61,1)
  FilletRadius = 0
  Length = 2550
  MakeFace = true
  Points = (2) [(31298.4,6049.61,1),(28748.4,6049.61,1)]
  Start = (31298.4,6049.61,1)
FEATURE [Part::Part2DObjectPython] Line590  # Draft 2D object (typed FeaturePython)
  ChamferSize = 0
  Closed = false
  End = (29948.4,8249.61,1)
  FilletRadius = 0
  Length = 7711.61
  MakeFace = true
  Points = (2) [(29948.4,538,0),(29948.4,8249.61,1)]
  Start = (29948.4,538,0)
FEATURE [Part::Part2DObjectPython] Line591  # Draft 2D object (typed FeaturePython)
  ChamferSize = 0
  Closed = false
  End = (42437,7349.61,0)
  FilletRadius = 0
  Length = 900
  MakeFace = true
  Placement = pos=(10038.6,-5620,0) rot=(0,0,1;0rad)
  Points = (2) [(32398,13869.6,0),(32398.4,12969.6,0)]
  Start = (42436.6,8249.61,0)
FEATURE [Part::Part2DObjectPython] Arc021  # Draft 2D object (typed FeaturePython)
  FirstAngle = 90
  LastAngle = 179.976
  MakeFace = true
  Placement = pos=(42436.6,7349.61,0) rot=(0,0,-1;1.57037rad)
  Radius = 900
FEATURE [Part::Part2DObjectPython] Line593  # Draft 2D object (typed FeaturePython)
  ChamferSize = 0
  Closed = false
  End = (31110.9,6049.61,1)
  FilletRadius = 0
  Length = 3900
  MakeFace = true
  Points = (2) [(31110.9,2149.61,1),(31110.9,6049.61,1)]
  Start = (31110.9,2149.61,1)
FEATURE [Part::Part2DObjectPython] Rectangle163  # Draft 2D object (typed FeaturePython)
  ChamferSize = 0
  FilletRadius = 0
  Height = -4770
  Length = 1500
  MakeFace = true
  Placement = pos=(46587,13019.6,0) rot=(0,0,1;0rad)
FEATURE [Part::Part2DObjectPython] Rectangle164  # Draft 2D object (typed FeaturePython)
  ChamferSize = 0
  FilletRadius = 0
  Height = -4770
  Length = 1500
  MakeFace = true
  Placement = pos=(29948.4,13019.6,1) rot=(0,0,1;0rad)
FEATURE [Part::Part2DObjectPython] Line594  # Draft 2D object (typed FeaturePython)
  ChamferSize = 0
  Closed = false
  End = (26623.4,2149.61,0)
  FilletRadius = 0
  Length = 4350
  MakeFace = true
  Points = (2) [(26623.4,6499.61,1),(26623.4,2149.61,0)]
  Start = (26623.4,6499.61,1)
FEATURE [Part::Part2DObjectPython] Line595  # Draft 2D object (typed FeaturePython)
  ChamferSize = 0
  Closed = false
  End = (36348.4,10634.6,1)
  FilletRadius = 0
  Length = 4900
  MakeFace = true
  Points = (2) [(31448.4,10634.6,1),(36348.4,10634.6,1)]
  Start = (31448.4,10634.6,1)
FEATURE [Part::Part2DObjectPython] Line596  # Draft 2D object (typed FeaturePython)
  ChamferSize = 0
  Closed = false
  End = (25648.4,10634.6,1)
  FilletRadius = 0
  Length = 4300
  MakeFace = true
  Points = (2) [(29948.4,10634.6,1),(25648.4,10634.6,1)]
  Start = (29948.4,10634.6,1)
FEATURE [Part::Part2DObjectPython] Rectangle165  # Draft 2D object (typed FeaturePython)
  ChamferSize = 0
  FilletRadius = 0
  Height = 2830
  Length = 4900
  MakeFace = true
  Placement = pos=(31448.4,13019.6,1) rot=(0,0,1;0rad)
FEATURE [Part::Part2DObjectPython] Line599  # Draft 2D object (typed FeaturePython)
  ChamferSize = 0
  Closed = false
  End = (46587,2149.61,0)
  FilletRadius = 0
  Length = 3750
  MakeFace = true
  Points = (2) [(46587,5899.61,0),(46587,2149.61,0)]
  Start = (46587,5899.61,0)
FEATURE [Part::Part2DObjectPython] Line600  # Draft 2D object (typed FeaturePython)
  ChamferSize = 0
  Closed = false
  End = (33898.4,1999.61,1)
  FilletRadius = 0
  Length = 1950
  MakeFace = true
  Points = (2) [(33898.4,3949.61,1),(33898.4,1999.61,1)]
  Start = (33898.4,3949.61,1)
FEATURE [Part::Part2DObjectPython] Line601  # Draft 2D object (typed FeaturePython)
  ChamferSize = 0
  Closed = false
  End = (37933,19000,0)
  FilletRadius = 0
  Length = 20338
  MakeFace = true
  Placement = pos=(0,0,-3000) rot=(0,0,1;0rad)
  Points = (2) [(17595,19000,3000),(37933,19000,3000)]
  Start = (17595,19000,0)
FEATURE [Part::Part2DObjectPython] Line602  # Draft 2D object (typed FeaturePython)
  ChamferSize = 0
  Closed = false
  End = (25498,21100,0)
  FilletRadius = 0
  Length = 8080.39
  MakeFace = true
  Points = (2) [(25498.4,13019.6,1),(25498,21100,0)]
  Start = (25498.4,13019.6,1)
FEATURE [Part::Part2DObjectPython] Line603  # Draft 2D object (typed FeaturePython)
  ChamferSize = 0
  Closed = false
  End = (23498,21099.9,0)
  FilletRadius = 0
  Length = 26614.6
  MakeFace = true
  Points = (2) [(23499.3,-5514.72,0),(23498,21099.9,0)]
  Start = (23499.3,-5514.72,0)
FEATURE [Part::Part2DObjectPython] Line604  # Draft 2D object (typed FeaturePython)
  ChamferSize = 0
  Closed = false
  End = (36348.4,16149.6,1)
  FilletRadius = 0
  Length = 12850.4
  MakeFace = true
  Points = (2) [(23498,16150.2,0),(36348.4,16149.6,1)]
  Start = (23498,16150.2,0)
FEATURE [Part::Part2DObjectPython] Arc022  # Draft 2D object (typed FeaturePython)
  FirstAngle = -90
  LastAngle = 0.0241588
  MakeFace = true
  Placement = pos=(49387,9899.61,0) rot=(0,0,1;0rad)
  Radius = 900
FEATURE [Part::Part2DObjectPython] Line605  # Draft 2D object (typed FeaturePython)
  ChamferSize = 0
  Closed = false
  End = (50287,9899.61,0)
  FilletRadius = 0
  Length = 900
  MakeFace = true
  Points = (2) [(49387,9899.61,0),(50287,9899.61,0)]
  Start = (49387,9899.61,0)
FEATURE [Part::Part2DObjectPython] Line606  # Draft 2D object (typed FeaturePython)
  ChamferSize = 0
  Closed = false
  End = (29123.7,1281,1)
  FilletRadius = 0
  Length = 718.612
  MakeFace = true
  Points = (2) [(29123.7,1999.61,1),(29123.7,1281,1)]
  Start = (29123.7,1999.61,1)
FEATURE [Part::Part2DObjectPython] Line607  # Draft 2D object (typed FeaturePython)
  ChamferSize = 0
  Closed = false
  End = (30923.4,1281,1)
  FilletRadius = 0
  Length = 718.612
  MakeFace = true
  Points = (2) [(30923.4,1999.61,1),(30923.4,1281,1)]
  Start = (30923.4,1999.61,1)
FEATURE [Part::Part2DObjectPython] Line608  # Draft 2D object (typed FeaturePython)
  ChamferSize = 0
  Closed = false
  End = (29123.7,1281,1)
  FilletRadius = 0
  Length = 1799.69
  MakeFace = true
  Points = (2) [(30923.4,1281,1),(29123.7,1281,1)]
  Start = (30923.4,1281,1)
FEATURE [Part::Part2DObjectPython] Line609  # Draft 2D object (typed FeaturePython)
  ChamferSize = 0
  Closed = false
  End = (39159,1999.61,1)
  FilletRadius = 0
  Length = 3535.62
  MakeFace = true
  Points = (2) [(35623.4,1999.61,1),(39159,1999.61,1)]
  Start = (35623.4,1999.61,1)
FEATURE [Part::Part2DObjectPython] Line610  # Draft 2D object (typed FeaturePython)
  ChamferSize = 0
  Closed = false
  End = (39159,3999.61,-0.967751)
  FilletRadius = 0
  Length = 33289
  MakeFace = true
  Points = (2) [(5870,3999.61,0),(39159,3999.61,-0.967751)]
  Start = (5870,3999.61,0)
FEATURE [Sketcher::SketchObject] Sketch068
  Placement = pos=(5945,2150,0) rot=(0.57735,0.57735,0.57735;2.0944rad)
  sketch-geometry (16):
    g0: LineSegment StartX=0 StartY=0 StartZ=0 EndX=1000 EndY=0 EndZ=0
    g1: LineSegment StartX=1000 StartY=0 StartZ=0 EndX=1000 EndY=2200 EndZ=0
    g2: LineSegment StartX=1000 StartY=2200 StartZ=0 EndX=0 EndY=2200 EndZ=0
    g3: LineSegment StartX=0 StartY=2200 StartZ=0 EndX=0 EndY=0 EndZ=0
    g4: LineSegment StartX=50 StartY=0 StartZ=0 EndX=950 EndY=0 EndZ=0
    g5: LineSegment StartX=950 StartY=0 StartZ=0 EndX=950 EndY=2150 EndZ=0
    g6: LineSegment StartX=950 StartY=2150 StartZ=0 EndX=50 EndY=2150 EndZ=0
    g7: LineSegment StartX=50 StartY=2150 StartZ=0 EndX=50 EndY=0 EndZ=0
    g8: LineSegment StartX=55 StartY=5 StartZ=0 EndX=945 EndY=5 EndZ=0
    g9: LineSegment StartX=945 StartY=5 StartZ=0 EndX=945 EndY=2145 EndZ=0
    g10: LineSegment StartX=945 StartY=2145 StartZ=0 EndX=55 EndY=2145 EndZ=0
    g11: LineSegment StartX=55 StartY=2145 StartZ=0 EndX=55 EndY=5 EndZ=0
    g12: LineSegment StartX=85 StartY=55 StartZ=0 EndX=915 EndY=55 EndZ=0
    g13: LineSegment StartX=915 StartY=55 StartZ=0 EndX=915 EndY=2115 EndZ=0
    g14: LineSegment StartX=915 StartY=2115 StartZ=0 EndX=85 EndY=2115 EndZ=0
    g15: LineSegment StartX=85 StartY=2115 StartZ=0 EndX=85 EndY=55 EndZ=0
  constraints (47):
    c: Coincident(g0,g1)
    c: Coincident(g1,g2)
    c: Coincident(g2,g3)
    c: Coincident(g3,g0)
    c: Horizontal(g0)
    c: Horizontal(g2)
    c: Vertical(g1)
    c: Vertical(g3)
    c: Coincident(g4,g5)
    c: Coincident(g5,g6)
    c: Coincident(g6,g7)
    c: Coincident(g7,g4)
    c: Horizontal(g4)
    c: Horizontal(g6)
    c: Vertical(g5)
    c: Vertical(g7)
    c: DistanceY(g1) = 2200
    c: DistanceX(g0) = 1000
    c: DistanceY(g6,g2) = 50
    c: DistanceX(g2,g6) = 50
    c: DistanceX(g4,g0) = 50
    c: DistanceY(g0,g4) = 0
    c: Coincident(g0,g-1)
    c: Coincident(g8,g9)
    c: Coincident(g9,g10)
    c: Coincident(g10,g11)
    c: Coincident(g11,g8)
    c: Horizontal(g8)
    c: Horizontal(g10)
    c: Vertical(g9)
    c: Vertical(g11)
    c: Coincident(g12,g13)
    c: Coincident(g13,g14)
    c: Coincident(g14,g15)
    c: Coincident(g15,g12)
    c: Horizontal(g12)
    c: Horizontal(g14)
    c: Vertical(g13)
    c: Vertical(g15)
    c: DistanceX(g8,g12) = 30
    c: DistanceY(g8,g12) = 50
    c: DistanceX(g14,g10) = 30
    c: DistanceY(g14,g10) = 30
    c: DistanceX(g4,g8) = 5
    c: DistanceY(g4,g8) = 5
    c: DistanceX(g10,g6) = 5
    c: DistanceY(g10,g6) = 5
FEATURE [Part::FeaturePython] Window057  label="Window055"  # WARN: FeaturePython — macro-defined, semantics opaque (R4)
  Base = -> Sketch068
  Height = 2200
  HoleDepth = 0
  MoveWithHost = true
  Normal = (-1,0,0)
  Preset = 7
  Role = 1
  Width = 1000
  WindowParts = OuterFrame | Frame | Wire0,Wire1 | 150.0 | 0.0 | InnerFrame | Frame | Wire2,Wire3 | 20.0 | 50.0 | InnerGlass | Glass panel | Wire3 | 2.0 | 60.0
FEATURE [Part::FeaturePython] Wall074  # WARN: FeaturePython — macro-defined, semantics opaque (R4)
  Align = 2
  Base = -> Line078
  Face = 0
  Height = 2900
  Length = 0
  MoveWithHost = false
  Normal = (0,0,0)
  Role = 0
  Subtractions = -> [Window057]
  Width = 150
FEATURE [Part::Part2DObjectPython] Line611  # Draft 2D object (typed FeaturePython)
  ChamferSize = 0
  Closed = false
  End = (28748.4,3949.61,1)
  FilletRadius = 0
  Length = 2550
  MakeFace = true
  Points = (2) [(31298.4,3949.61,1),(28748.4,3949.61,1)]
  Start = (31298.4,3949.61,1)
FEATURE [Part::Part2DObjectPython] Arc023  # Draft 2D object (typed FeaturePython)
  FirstAngle = 90
  LastAngle = 179.975
  MakeFace = true
  Placement = pos=(31378.4,2204.22,0.5202) rot=(0,0,1;0rad)
  Radius = 890
FEATURE [Part::Part2DObjectPython] Line612  # Draft 2D object (typed FeaturePython)
  ChamferSize = 0
  Closed = false
  End = (31378.4,2204.61,1)
  FilletRadius = 0
  Length = 890
  MakeFace = true
  Placement = pos=(0.000976525,-100,0) rot=(0,0,1;0rad)
  Points = (2) [(30488.4,2304.61,0.5202),(31378.4,2304.61,1)]
  Start = (30488.4,2204.61,0.5202)
FEATURE [Part::Part2DObjectPython] Line614  # Draft 2D object (typed FeaturePython)
  ChamferSize = 0
  Closed = false
  End = (29558,1849.81,0.2399)
  FilletRadius = 0
  Length = 809.618
  MakeFace = true
  Placement = pos=(-1740,56.8057,0.2399) rot=(0,0,1;0rad)
  Points = (2) [(30488.4,1792.81,0.7601),(31298,1793,0)]
  Start = (28748.4,1849.61,1)
FEATURE [Part::Part2DObjectPython] Line615  # Draft 2D object (typed FeaturePython)
  ChamferSize = 0
  Closed = false
  End = (29558,2401,0)
  FilletRadius = 0
  Length = 551.194
  MakeFace = true
  Points = (2) [(29558,1849.81,0.2399),(29558,2401,0)]
  Start = (29558,1849.81,0.2399)
FEATURE [Part::Part2DObjectPython] Line616  # Draft 2D object (typed FeaturePython)
  ChamferSize = 0
  Closed = false
  End = (30488.4,1849.81,0.733382)
  FilletRadius = 0
  Length = 930.382
  MakeFace = true
  Points = (2) [(29558,1849.81,0.2399),(30488.4,1849.81,0.733382)]
  Start = (29558,1849.81,0.2399)
FEATURE [Part::Part2DObjectPython] Line617  # Draft 2D object (typed FeaturePython)
  ChamferSize = 0
  Closed = false
  End = (2041.98,2000,0)
  FilletRadius = 0
  Length = 1000
  MakeFace = true
  Points = (2) [(2041.98,2000,1000),(2041.98,2000,0)]
  Start = (2041.98,2000,1000)
FEATURE [Part::Part2DObjectPython] Line618  # Draft 2D object (typed FeaturePython)
  ChamferSize = 0
  Closed = false
  End = (4859.72,2000,0)
  FilletRadius = 0
  Length = 1000
  MakeFace = true
  Points = (2) [(4859.72,2000,1000),(4859.72,2000,0)]
  Start = (4859.72,2000,1000)
FEATURE [Part::Part2DObjectPython] Line619  # Draft 2D object (typed FeaturePython)
  ChamferSize = 0
  Closed = false
  End = (4859.72,2000,1000)
  FilletRadius = 0
  Length = 2817.74
  MakeFace = true
  Points = (2) [(2041.98,2000,1000),(4859.72,2000,1000)]
  Start = (2041.98,2000,1000)
FEATURE [Part::FeaturePython] Window058  label="Window056"  # WARN: FeaturePython — macro-defined, semantics opaque (R4)
  Base = -> Sketch019
  Height = 1000
  HoleDepth = 0
  MoveWithHost = true
  Normal = (0,1,0)
  Placement = pos=(3474.34,0,-22.897) rot=(0,0,1;0rad)
  Preset = 1
  Role = 0
  Width = 1200
  WindowParts = OuterFrame | Frame | Wire0,Wire1 | 100.0 | 0.0 | Glass | Glass panel | Wire1 | 10.0 | 50.0
FEATURE [Part::FeaturePython] Wall068  # WARN: FeaturePython — macro-defined, semantics opaque (R4)
  Align = 0
  Base = -> Line073
  Face = 0
  Height = 2900
  Length = 0
  MoveWithHost = false
  Normal = (0,0,0)
  Placement = pos=(0,-850,0) rot=(0,0,1;0rad)
  Role = 0
  Subtractions = -> [Window007,Window058]
  Width = 150
FEATURE [Part::Part2DObjectPython] Line620  # Draft 2D object (typed FeaturePython)
  ChamferSize = 0
  Closed = false
  End = (3245,3999.61,-100)
  FilletRadius = 0
  Length = 2550
  MakeFace = true
  Placement = pos=(0,0,-100) rot=(0,0,1;0rad)
  Points = (2) [(5795,3999.61,0),(3245,3999.61,0)]
  Start = (5795,3999.61,-100)
  Support = -> Wall074
FEATURE [Sketcher::SketchObject] Sketch072
  Placement = pos=(4173,4095,0) rot=(1,0,0;1.5708rad)
  sketch-geometry (8):
    g0: LineSegment StartX=0 StartY=0 StartZ=0 EndX=1500 EndY=0 EndZ=0
    g1: LineSegment StartX=1500 StartY=0 StartZ=0 EndX=1500 EndY=2200 EndZ=0
    g2: LineSegment StartX=1500 StartY=2200 StartZ=0 EndX=0 EndY=2200 EndZ=0
    g3: LineSegment StartX=0 StartY=2200 StartZ=0 EndX=0 EndY=0 EndZ=0
    g4: LineSegment StartX=50 StartY=0 StartZ=0 EndX=1450 EndY=0 EndZ=0
    g5: LineSegment StartX=1450 StartY=0 StartZ=0 EndX=1450 EndY=2150 EndZ=0
    g6: LineSegment StartX=1450 StartY=2150 StartZ=0 EndX=50 EndY=2150 EndZ=0
    g7: LineSegment StartX=50 StartY=2150 StartZ=0 EndX=50 EndY=0 EndZ=0
  constraints (23):
    c: Coincident(g0,g1)
    c: Coincident(g1,g2)
    c: Coincident(g2,g3)
    c: Coincident(g3,g0)
    c: Horizontal(g0)
    c: Horizontal(g2)
    c: Vertical(g1)
    c: Vertical(g3)
    c: Coincident(g4,g5)
    c: Coincident(g5,g6)
    c: Coincident(g6,g7)
    c: Coincident(g7,g4)
    c: Horizontal(g4)
    c: Horizontal(g6)
    c: Vertical(g5)
    c: Vertical(g7)
    c: DistanceY(g1) = 2200
    c: DistanceX(g0) = 1500
    c: DistanceY(g6,g2) = 50
    c: DistanceX(g2,g6) = 50
    c: DistanceX(g4,g0) = 50
    c: DistanceY(g0,g4) = 0
    c: Coincident(g0,g-1)
FEATURE [Part::FeaturePython] Window059  label="Window057"  # WARN: FeaturePython — macro-defined, semantics opaque (R4)
  Base = -> Sketch072
  Height = 2200
  HoleDepth = 0
  MoveWithHost = true
  Normal = (0,1,0)
  Placement = pos=(-403,-95.3894,0) rot=(0,0,1;0rad)
  Preset = 6
  Role = 1
  Width = 1500
  WindowParts = OuterFrame | Frame | Wire0,Wire1 | 150.0 | 0.0 | Door | Solid panel | Wire1 | 0.0 | 0.0
FEATURE [Part::FeaturePython] Wall095  # WARN: FeaturePython — macro-defined, semantics opaque (R4)
  Align = 0
  Base = -> Line620
  Face = 0
  Height = 2900
  Length = 0
  MoveWithHost = false
  Normal = (0,0,0)
  Role = 0
  Subtractions = -> [Window059]
  Width = 150
FEATURE [Part::Part2DObjectPython] Line621  # Draft 2D object (typed FeaturePython)
  ChamferSize = 0
  Closed = false
  End = (3245,5750,0)
  FilletRadius = 0
  Length = 2550
  MakeFace = true
  Points = (2) [(5795,5750,0),(3245,5750,0)]
  Start = (5795,5750,0)
FEATURE [Part::Part2DObjectPython] Line622  # Draft 2D object (typed FeaturePython)
  ChamferSize = 0
  Closed = false
  End = (4520,4149.61,0)
  FilletRadius = 0
  Length = 1600.39
  MakeFace = true
  Points = (2) [(4520,5750,0),(4520,4149.61,0)]
  Start = (4520,5750,0)
FEATURE [Part::Part2DObjectPython] Rectangle168  # Draft 2D object (typed FeaturePython)
  ChamferSize = 0
  FilletRadius = 0
  Height = 380.505
  Length = 1500
  MakeFace = true
  Placement = pos=(3770,4149.61,0) rot=(0,0,1;0rad)
FEATURE [Part::Part2DObjectPython] Line625  # Draft 2D object (typed FeaturePython)
  ChamferSize = 0
  Closed = false
  End = (37371.3,6299.61,0)
  FilletRadius = 0
  Length = 900
  MakeFace = true
  Placement = pos=(-13281.7,-3600,0) rot=(0,0,1;0rad)
  Points = (2) [(49753,9899.61,0),(50653,9899.61,0)]
  Start = (36471.3,6299.61,0)
FEATURE [Part::Part2DObjectPython] Arc024  # Draft 2D object (typed FeaturePython)
  FirstAngle = 0.00625634
  LastAngle = 90
  MakeFace = true
  Placement = pos=(36471.3,6299.51,0) rot=(0,0,1;0rad)
  Radius = 900
FEATURE [App::Annotation] Text029
  LabelText = FRONT VERANDA
  Position = (33329,3166.86,0)
FEATURE [App::DocumentObjectGroup] Group027  label="text level 1"
  Group = -> [Text007,Text008,Text009,Text010,Text011,Text012,Text013,Text014,Text015,Text029]
FEATURE [App::DocumentObjectGroup] Group019  label="Level 1 Floor"
  Group = -> [Group026,Group027,Group021]
FEATURE [App::FeaturePython] Dimension050  # Draft dimension (typed FeaturePython)
  Dimline = (9587.65,444.997,0)
  Direction = (0,0,0)
  Distance = 11000
  End = (10995,1850,0)
  Normal = (0,0,1)
  Start = (-5,1850,0)
FEATURE [App::FeaturePython] Dimension051  # Draft dimension (typed FeaturePython)
  Dimline = (4658.34,678.716,0)
  Direction = (0,0,0)
  Distance = 5950
  End = (5945,1850,0)
  Normal = (0,0,1)
  Start = (-5,1850,0)
FEATURE [App::FeaturePython] Dimension052  # Draft dimension (typed FeaturePython)
  Dimline = (5945,678.716,0)
  Direction = (0,0,0)
  Distance = 5050
  End = (10995,1850,0)
  Normal = (0,0,1)
  Start = (5945,1850,0)
FEATURE [App::FeaturePython] Dimension053  # Draft dimension (typed FeaturePython)
  Dimline = (170.702,876.782,0)
  Direction = (0,0,0)
  Distance = 150
  End = (145,1850,0)
  Normal = (0,0,1)
  Start = (-5,1850,0)
FEATURE [App::FeaturePython] Dimension054  # Draft dimension (typed FeaturePython)
  Dimline = (145,876.782,0)
  Direction = (0,0,0)
  Distance = 1212.26
  End = (1357.26,1850,0)
  Normal = (0,0,1)
  Start = (145,1850,0)
FEATURE [App::FeaturePython] Dimension055  # Draft dimension (typed FeaturePython)
  Dimline = (1357.26,876.782,0)
  Direction = (0,0,0)
  Distance = 1000
  End = (2357.26,2000,0)
  Normal = (0,0,1)
  Start = (1357.26,2000,0)
FEATURE [App::FeaturePython] Dimension057  # Draft dimension (typed FeaturePython)
  Dimline = (3095,876.782,0)
  Direction = (0,0,0)
  Distance = 150
  End = (3245,1850,0)
  Normal = (0,0,1)
  Start = (3095,1850,0)
FEATURE [App::FeaturePython] Dimension058  # Draft dimension (typed FeaturePython)
  Dimline = (3245,876.782,0)
  Direction = (0,0,0)
  Distance = 775
  End = (4020,1850,0)
  Normal = (0,0,1)
  Start = (3245,1850,0)
FEATURE [App::FeaturePython] Dimension059  # Draft dimension (typed FeaturePython)
  Dimline = (4020,876.782,0)
  Direction = (0,0,0)
  Distance = 1000
  End = (5020,2000,0)
  Normal = (0,0,1)
  Start = (4020,2000,0)
FEATURE [App::FeaturePython] Dimension061  # Draft dimension (typed FeaturePython)
  Dimline = (5795,876.782,0)
  Direction = (0,0,0)
  Distance = 150
  End = (5945,1850,0)
  Normal = (0,0,1)
  Start = (5795,1850,0)
FEATURE [App::FeaturePython] Dimension062  # Draft dimension (typed FeaturePython)
  Dimline = (5945,876.782,0)
  Direction = (0,0,0)
  Distance = 4900
  End = (10845,1850,0)
  Normal = (0,0,1)
  Start = (5945,1850,0)
FEATURE [App::FeaturePython] Dimension063  # Draft dimension (typed FeaturePython)
  Dimline = (10845,876.782,0)
  Direction = (0,0,0)
  Distance = 150
  End = (10995,1850,0)
  Normal = (0,0,1)
  Start = (10845,1850,0)
FEATURE [App::FeaturePython] Dimension066  # Draft dimension (typed FeaturePython)
  Dimline = (3095,876.782,0)
  Direction = (0,0,0)
  Distance = 737.741
  End = (3095,1850,0)
  Normal = (0,0,1)
  Start = (2357.26,1850,0)
FEATURE [App::FeaturePython] Dimension067  # Draft dimension (typed FeaturePython)
  Dimline = (5020,876.782,0)
  Direction = (0,0,0)
  Distance = 775
  End = (5795,1850,0)
  Normal = (0,0,1)
  Start = (5020,1850,0)
FEATURE [App::FeaturePython] Dimension068  # Draft dimension (typed FeaturePython)
  Dimline = (12253.1,2506.42,0)
  Direction = (0,0,0)
  Distance = 14300
  End = (10995,16150,0)
  Normal = (0,0,1)
  Start = (10995,1850,0)
FEATURE [App::FeaturePython] Dimension069  # Draft dimension (typed FeaturePython)
  Dimline = (12016.1,2966.42,0)
  Direction = (0,0,0)
  Distance = 2149.61
  End = (10995,3999.61,0)
  Normal = (0,0,1)
  Start = (10995,1850,0)
FEATURE [App::FeaturePython] Dimension070  # Draft dimension (typed FeaturePython)
  Dimline = (12016.1,3999.61,0)
  Direction = (0,0,0)
  Distance = 12150.4
  End = (10995,16150,0)
  Normal = (0,0,1)
  Start = (10995,3999.61,0)
FEATURE [App::FeaturePython] Dimension071  # Draft dimension (typed FeaturePython)
  Dimline = (11827.1,2150.42,0)
  Direction = (0,0,0)
  Distance = 300
  End = (10995,2150,0)
  Normal = (0,0,1)
  Start = (10995,1850,0)
FEATURE [App::FeaturePython] Dimension072  # Draft dimension (typed FeaturePython)
  Dimline = (11827.1,2150,0)
  Direction = (0,0,0)
  Distance = 1849.61
  End = (10995,3999.61,0)
  Normal = (0,0,1)
  Start = (10995,2150,0)
FEATURE [App::FeaturePython] Dimension073  # Draft dimension (typed FeaturePython)
  Dimline = (11827.1,3999.61,0)
  Direction = (0,0,0)
  Distance = 1750.39
  End = (10995,5750,0)
  Normal = (0,0,1)
  Start = (10995,3999.61,0)
FEATURE [App::FeaturePython] Dimension074  # Draft dimension (typed FeaturePython)
  Dimline = (11827.1,5750,0)
  Direction = (0,0,0)
  Distance = 300
  End = (10995,6050,0.0001461)
  Normal = (0,0,1)
  Start = (10995,5750,0)
FEATURE [App::FeaturePython] Dimension082  # Draft dimension (typed FeaturePython)
  Dimline = (11827.1,12720,0)
  Direction = (0,0,0)
  Distance = 300
  End = (10995,13020,0)
  Normal = (0,0,1)
  Start = (10995,12720,0)
FEATURE [App::FeaturePython] Dimension084  # Draft dimension (typed FeaturePython)
  Dimline = (11827.1,13020,0)
  Direction = (0,0,0)
  Distance = 358.805
  End = (10995,13378.8,0)
  Normal = (0,0,1)
  Start = (10995,13020,0)
FEATURE [App::FeaturePython] Dimension085  # Draft dimension (typed FeaturePython)
  Dimline = (11827.1,13378.8,0)
  Direction = (0,0,0)
  Distance = 500
  End = (10995,13878.8,0)
  Normal = (0,0,1)
  Start = (10995,13378.8,0)
FEATURE [App::FeaturePython] Dimension086  # Draft dimension (typed FeaturePython)
  Dimline = (11827.1,13878.8,0)
  Direction = (0,0,0)
  Distance = 1971.2
  End = (10995,15850,0)
  Normal = (0,0,1)
  Start = (10995,13878.8,0)
FEATURE [App::FeaturePython] Dimension087  # Draft dimension (typed FeaturePython)
  Dimline = (11827.1,15850,0)
  Direction = (0,0,0)
  Distance = 300
  End = (10995,16150,0)
  Normal = (0,0,1)
  Start = (10995,15850,0)
FEATURE [Part::Part2DObjectPython] DWire201  # Draft 2D object (typed FeaturePython)
  ChamferSize = 0
  Closed = true
  End = (5945,2000,0)
  FilletRadius = 0
  Length = 14099.2
  MakeFace = true
  Placement = pos=(-25503.4,0.388456,0) rot=(0,0,1;0rad)
  Points = (6) [(31448.4,3999.22,0),(36498.4,3999.22,0),(36498.4,2149.61,0),(36348.4,2149.61,0),(36348.4,1999.61,0),(31448.4,1999.61,0)]
  Start = (5945,3999.61,0)
FEATURE [Part::Extrusion] Extrusion044
  Base = -> DWire201
  Dir = (0,0,2800)
  Solid = true
FEATURE [Part::FeaturePython] Space  label="Veranda"  # WARN: FeaturePython — macro-defined, semantics opaque (R4)
  Area = 1.00755e+07
  Base = -> Extrusion044
  MoveWithHost = false
  Role = 0
FEATURE [Part::Part2DObjectPython] Rectangle169  # Draft 2D object (typed FeaturePython)
  ChamferSize = 0
  FilletRadius = 0
  Height = -1849.61
  Length = -2550
  MakeFace = true
  Placement = pos=(5795,3999.61,0) rot=(0,0,1;0rad)
FEATURE [Part::Part2DObjectPython] DWire202  # Draft 2D object (typed FeaturePython)
  ChamferSize = 0
  Closed = true
  End = (3245,4149.61,0)
  FilletRadius = 0
  Length = 16000.8
  MakeFace = true
  Placement = pos=(-25503.4,0.388761,0) rot=(0,0,1;0rad)
  Points = (6) [(28748.4,9599.61,0),(29948.4,9599.61,0),(29948.4,8249.61,0),(31298.4,8249.61,0),(31298.4,4149.22,0),(28748.4,4149.22,0)]
  Start = (3245,9600,0)
FEATURE [Part::Part2DObjectPython] DWire203  # Draft 2D object (typed FeaturePython)
  ChamferSize = 0
  Closed = true
  End = (3095,6650,0)
  FilletRadius = 0
  Length = 9100
  MakeFace = true
  Placement = pos=(-25503.4,0.388761,0) rot=(0,0,1;0rad)
  Points = (4) [(28598.4,8249.61,0),(25648.4,8249.61,0),(25648.4,6649.61,0),(28598.4,6649.61,0)]
  Start = (3095,8250,0)
FEATURE [Part::Part2DObjectPython] DWire204  # Draft 2D object (typed FeaturePython)
  ChamferSize = 0
  Closed = true
  End = (144.999,2150,0)
  FilletRadius = 0
  Length = 15799.9
  MakeFace = true
  Placement = pos=(-25503.4,0.388761,0) rot=(0,0,1;0rad)
  Points = (8) [(25648.4,6499.61,0),(28598.4,6499.61,0),(28598.4,4649.61,0),(27998.4,4649.61,0),(27998.4,4499.61,0),(28598.4,4499.61,0),(28598.4,2149.61,0),+1 more]
  Start = (144.999,6500,0)
FEATURE [Part::Part2DObjectPython] Rectangle170  # Draft 2D object (typed FeaturePython)
  ChamferSize = 0
  FilletRadius = 0
  Height = -1200
  Length = 2950
  MakeFace = true
  Placement = pos=(144.999,9600,0) rot=(0,0,1;0rad)
FEATURE [Part::Part2DObjectPython] Rectangle171  # Draft 2D object (typed FeaturePython)
  ChamferSize = 0
  FilletRadius = 0
  Height = -3120
  Length = 4300
  MakeFace = true
  Placement = pos=(144.999,12870,0) rot=(0,0,1;0rad)
FEATURE [Part::Part2DObjectPython] DWire205  # Draft 2D object (typed FeaturePython)
  ChamferSize = 0
  Closed = true
  End = (144.999,15850,0)
  FilletRadius = 0
  Length = 12160
  MakeFace = true
  Placement = pos=(-25503.4,0.388761,0) rot=(0,0,1;0rad)
  Points = (6) [(25648.4,15999.6,0),(28598.4,15999.6,0),(28598.4,13019.6,0),(25498.4,13019.6,0),(25498.4,15849.6,0),(25648.4,15849.6,0)]
  Start = (145,16000,0)
FEATURE [Part::Part2DObjectPython] Rectangle172  # Draft 2D object (typed FeaturePython)
  ChamferSize = 0
  FilletRadius = 0
  Height = -2830
  Length = 5550.34
  MakeFace = true
  Placement = pos=(3244.66,15850,0) rot=(0,0,1;0rad)
FEATURE [Part::Part2DObjectPython] Rectangle173  # Draft 2D object (typed FeaturePython)
  ChamferSize = 0
  FilletRadius = 0
  Height = -2830
  Length = 1900
  MakeFace = true
  Placement = pos=(8945,15850,0) rot=(0,0,1;0rad)
FEATURE [Part::Part2DObjectPython] Rectangle174  # Draft 2D object (typed FeaturePython)
  ChamferSize = 0
  FilletRadius = 0
  Height = 8720.39
  Length = -4900
  MakeFace = true
  Placement = pos=(10845,4149.61,0) rot=(0,0,1;0rad)
FEATURE [Part::Extrusion] Extrusion045
  Base = -> Rectangle169
  Dir = (0,0,2800)
  Solid = true
FEATURE [Part::Extrusion] Extrusion046
  Base = -> DWire204
  Dir = (0,0,2800)
  Solid = true
FEATURE [Part::Extrusion] Extrusion047
  Base = -> DWire203
  Dir = (0,0,2800)
  Solid = true
FEATURE [Part::Extrusion] Extrusion048
  Base = -> Rectangle170
  Dir = (0,0,2800)
  Solid = true
FEATURE [Part::Extrusion] Extrusion049
  Base = -> Rectangle171
  Dir = (0,0,2800)
  Solid = true
FEATURE [Part::Extrusion] Extrusion050
  Base = -> DWire205
  Dir = (0,0,2800)
  Solid = true
FEATURE [Part::Extrusion] Extrusion051
  Base = -> Rectangle172
  Dir = (0,0,2800)
  Solid = true
FEATURE [Part::Extrusion] Extrusion052
  Base = -> Rectangle173
  Dir = (0,0,2800)
  Solid = true
FEATURE [Part::Extrusion] Extrusion053
  Base = -> Rectangle174
  Dir = (0,0,2800)
  Solid = true
FEATURE [Part::FeaturePython] Space001  label="Living & Dinning "  # WARN: FeaturePython — macro-defined, semantics opaque (R4)
  Area = 4.27299e+07
  Base = -> Extrusion053
  MoveWithHost = false
  Role = 0
FEATURE [Part::FeaturePython] Space002  label="Foyer"  # WARN: FeaturePython — macro-defined, semantics opaque (R4)
  Area = 4.71651e+06
  Base = -> Extrusion045
  MoveWithHost = false
  Role = 0
FEATURE [Part::FeaturePython] Space003  label="Guest Bedroom"  # WARN: FeaturePython — macro-defined, semantics opaque (R4)
  Area = 1.27425e+07
  Base = -> Extrusion046
  MoveWithHost = false
  Role = 0
FEATURE [Part::FeaturePython] Space004  label="Guest bathroom"  # WARN: FeaturePython — macro-defined, semantics opaque (R4)
  Area = 4.72e+06
  Base = -> Extrusion047
  MoveWithHost = false
  Role = 0
FEATURE [Part::FeaturePython] Space005  label="Toilet"  # WARN: FeaturePython — macro-defined, semantics opaque (R4)
  Area = 3.54e+06
  Base = -> Extrusion048
  MoveWithHost = false
  Role = 0
FEATURE [Part::FeaturePython] Space006  label="Laundery"  # WARN: FeaturePython — macro-defined, semantics opaque (R4)
  Area = 1.3416e+07
  Base = -> Extrusion049
  MoveWithHost = false
  Role = 0
FEATURE [Part::FeaturePython] Space007  label="Rear Veranda"  # WARN: FeaturePython — macro-defined, semantics opaque (R4)
  Area = 9.2155e+06
  Base = -> Extrusion050
  MoveWithHost = false
  Role = 0
FEATURE [Part::FeaturePython] Space008  label="Kitchen"  # WARN: FeaturePython — macro-defined, semantics opaque (R4)
  Area = 1.57075e+07
  Base = -> Extrusion051
  MoveWithHost = false
  Role = 0
FEATURE [Part::FeaturePython] Space009  label="Storage"  # WARN: FeaturePython — macro-defined, semantics opaque (R4)
  Area = 5.377e+06
  Base = -> Extrusion052
  MoveWithHost = false
  Role = 0
FEATURE [Part::Extrusion] Extrusion054
  Base = -> DWire202
  Dir = (0,0,2800)
  Solid = true
FEATURE [Part::FeaturePython] Space010  label="Corridor"  # WARN: FeaturePython — macro-defined, semantics opaque (R4)
  Area = 1.2076e+07
  Base = -> Extrusion054
  MoveWithHost = false
  Role = 0
FEATURE [App::DocumentObjectGroup] Group037  label="Level 1 Spaces"
  Group = -> [Space,Space001,Space002,Space003,Space004,Space005,Space006,Space007,Space008,Space009,Space010]
FEATURE [App::FeaturePython] Dimension090  # Draft dimension (typed FeaturePython)
  Dimline = (-1026.05,13020,0)
  Direction = (0,0,0)
  Distance = 11170
  End = (-4.99902,1850,0)
  Normal = (0,0,1)
  Start = (-4.99902,13020,0)
FEATURE [App::FeaturePython] Dimension091  # Draft dimension (typed FeaturePython)
  Dimline = (-837.052,16150,0)
  Direction = (0,0,0)
  Distance = 300
  End = (-5,15850,0)
  Normal = (0,0,1)
  Start = (-5,16150,0)
FEATURE [App::FeaturePython] Dimension092  # Draft dimension (typed FeaturePython)
  Dimline = (-837.052,16150,0)
  Direction = (0,0,0)
  Distance = 2830
  End = (-5,13020,0)
  Normal = (0,0,1)
  Start = (-5,15850,0)
FEATURE [App::FeaturePython] Dimension093  # Draft dimension (typed FeaturePython)
  Dimline = (-837.052,13020,0)
  Direction = (0,0,0)
  Distance = 300
  End = (-5,12720,0)
  Normal = (0,0,1)
  Start = (-5,13020,0)
FEATURE [App::FeaturePython] Dimension094  # Draft dimension (typed FeaturePython)
  Dimline = (-837.052,12720,0)
  Direction = (0,0,0)
  Distance = 928.577
  End = (-5,11791.4,0)
  Normal = (0,0,1)
  Start = (-5,12720,0)
FEATURE [App::FeaturePython] Dimension095  # Draft dimension (typed FeaturePython)
  Dimline = (-837.052,11791.4,0)
  Direction = (0,0,0)
  Distance = 1000
  End = (-5,10791.4,0)
  Normal = (0,0,1)
  Start = (-5,11791.4,0)
FEATURE [App::FeaturePython] Dimension096  # Draft dimension (typed FeaturePython)
  Dimline = (-837.052,10791.4,0)
  Direction = (0,0,0)
  Distance = 1741.42
  End = (-5,9050,0)
  Normal = (0,0,1)
  Start = (-5,10791.4,0)
FEATURE [App::FeaturePython] Dimension097  # Draft dimension (typed FeaturePython)
  Dimline = (-837.052,9050,0)
  Direction = (0,0,0)
  Distance = 500
  End = (-5,8550,0)
  Normal = (0,0,1)
  Start = (-5,9050,0)
FEATURE [App::FeaturePython] Dimension098  # Draft dimension (typed FeaturePython)
  Dimline = (-837.052,8550,0)
  Direction = (0,0,0)
  Distance = 300
  End = (-5,8250,0)
  Normal = (0,0,1)
  Start = (-5,8550,0)
FEATURE [App::FeaturePython] Dimension099  # Draft dimension (typed FeaturePython)
  Dimline = (-837.052,8250,0)
  Direction = (0,0,0)
  Distance = 500
  End = (-5,7750,0)
  Normal = (0,0,1)
  Start = (-5,8250,0)
FEATURE [App::FeaturePython] Dimension100  # Draft dimension (typed FeaturePython)
  Dimline = (-837.052,7750,0)
  Direction = (0,0,0)
  Distance = 1700
  End = (-5,6050,0)
  Normal = (0,0,1)
  Start = (-5,7750,0)
FEATURE [App::FeaturePython] Dimension101  # Draft dimension (typed FeaturePython)
  Dimline = (-837.052,6050,0)
  Direction = (0,0,0)
  Distance = 300
  End = (-5,5750,0)
  Normal = (0,0,1)
  Start = (-5,6050,0)
FEATURE [App::FeaturePython] Dimension102  # Draft dimension (typed FeaturePython)
  Dimline = (-837.052,5750,0)
  Direction = (0,0,0)
  Distance = 500
  End = (-5,5250,0)
  Normal = (0,0,1)
  Start = (-5,5750,0)
FEATURE [App::FeaturePython] Dimension103  # Draft dimension (typed FeaturePython)
  Dimline = (-837.052,5250,0)
  Direction = (0,0,0)
  Distance = 3100
  End = (-5,2150,0)
  Normal = (0,0,1)
  Start = (-5,5250,0)
FEATURE [App::FeaturePython] Dimension104  # Draft dimension (typed FeaturePython)
  Dimline = (-837.052,2150,0)
  Direction = (0,0,0)
  Distance = 300
  End = (-5,1850,0)
  Normal = (0,0,1)
  Start = (-5,2150,0)
FEATURE [Part::Part2DObjectPython] Line626  # Draft 2D object (typed FeaturePython)
  ChamferSize = 0
  Closed = false
  End = (10995,17081,0)
  FilletRadius = 0
  Length = 931
  MakeFace = true
  Points = (2) [(10995,16150,0),(10995,17081,0)]
  Start = (10995,16150,0)
FEATURE [Part::Part2DObjectPython] Line627  # Draft 2D object (typed FeaturePython)
  ChamferSize = 0
  Closed = false
  End = (11827.1,17081,0)
  FilletRadius = 0
  Length = 931
  MakeFace = true
  Points = (2) [(11827.1,16150,5.7e-14),(11827.1,17081,5.7e-14)]
  Start = (11827.1,16150,0)
FEATURE [Part::Part2DObjectPython] Line628  # Draft 2D object (typed FeaturePython)
  ChamferSize = 0
  Closed = false
  End = (12016.1,17081,0)
  FilletRadius = 0
  Length = 931
  MakeFace = true
  Points = (2) [(12016.1,16150,0),(12016.1,17081,0)]
  Start = (12016.1,16150,0)
FEATURE [Part::Part2DObjectPython] Line629  # Draft 2D object (typed FeaturePython)
  ChamferSize = 0
  Closed = false
  End = (12253.1,17081,0)
  FilletRadius = 0
  Length = 931
  MakeFace = true
  Points = (2) [(12253.1,16150,0),(12253.1,17081,0)]
  Start = (12253.1,16150,0)
FEATURE [Part::Part2DObjectPython] Line630  # Draft 2D object (typed FeaturePython)
  ChamferSize = 0
  Closed = false
  End = (11827.1,16615.5,0)
  FilletRadius = 0
  Length = 832.051
  MakeFace = true
  Points = (2) [(10995,16615.5,0),(11827.1,16615.5,5.7e-14)]
  Start = (10995,16615.5,0)
FEATURE [App::FeaturePython] Dimension105  # Draft dimension (typed FeaturePython)
  Dimline = (-1263.05,16150,0)
  Direction = (0,0,0)
  Distance = 14300
  End = (-4.99902,16150,0)
  Normal = (0,0,1)
  Start = (-4.99902,1850,0)
FEATURE [Part::Part2DObjectPython] Line631  # Draft 2D object (typed FeaturePython)
  ChamferSize = 0
  Closed = false
  End = (-5,18153.4,0)
  FilletRadius = 0
  Length = 2003.39
  MakeFace = true
  Placement = pos=(-25503.4,0.388456,0) rot=(0,0,1;0rad)
  Points = (2) [(25498.4,16149.6,0),(25498.4,18153,0)]
  Start = (-5,16150,0)
FEATURE [Part::Part2DObjectPython] Line632  # Draft 2D object (typed FeaturePython)
  ChamferSize = 0
  Closed = false
  End = (-5,17151.7,0)
  FilletRadius = 0
  Length = 832.051
  MakeFace = true
  Placement = pos=(-11832.1,536.194,0) rot=(0,0,1;0rad)
  Points = (2) [(10995,16615.5,0),(11827.1,16615.5,5.7e-14)]
  Start = (-837.051,17151.7,0)
FEATURE [Part::Part2DObjectPython] Line633  # Draft 2D object (typed FeaturePython)
  ChamferSize = 0
  Closed = false
  End = (-837.051,18153.4,0)
  FilletRadius = 0
  Length = 2003.39
  MakeFace = true
  Placement = pos=(-25503.4,0.388456,0) rot=(0,0,1;0rad)
  Points = (2) [(24666.3,16149.6,-5.7e-14),(24666.3,18153,-5.7e-14)]
  Start = (-837.051,16150,0)
FEATURE [Part::Part2DObjectPython] Line634  # Draft 2D object (typed FeaturePython)
  ChamferSize = 0
  Closed = false
  End = (12016.1,16615.5,0)
  FilletRadius = 0
  Length = 189
  MakeFace = true
  Points = (2) [(11827.1,16615.5,5.7e-14),(12016.1,16615.5,0)]
  Start = (11827.1,16615.5,0)
FEATURE [Part::Part2DObjectPython] Line635  # Draft 2D object (typed FeaturePython)
  ChamferSize = 0
  Closed = false
  End = (12253.1,16615.5,0)
  FilletRadius = 0
  Length = 237
  MakeFace = true
  Points = (2) [(12016.1,16615.5,0),(12253.1,16615.5,0)]
  Start = (12016.1,16615.5,0)
FEATURE [Part::Part2DObjectPython] Line636  # Draft 2D object (typed FeaturePython)
  ChamferSize = 0
  Closed = false
  End = (-837.051,17151.7,0)
  FilletRadius = 0
  Length = 189
  MakeFace = true
  Placement = pos=(-12853.1,536.194,0) rot=(0,0,1;0rad)
  Points = (2) [(11827.1,16615.5,5.7e-14),(12016.1,16615.5,0)]
  Start = (-1026.05,17151.7,0)
FEATURE [Part::Part2DObjectPython] Line637  # Draft 2D object (typed FeaturePython)
  ChamferSize = 0
  Closed = false
  End = (-1026.05,18153.4,0)
  FilletRadius = 0
  Length = 2003.39
  MakeFace = true
  Placement = pos=(-25503.4,0.388456,0) rot=(0,0,1;0rad)
  Points = (2) [(24477.3,16149.6,0),(24477.3,18153,0)]
  Start = (-1026.05,16150,0)
FEATURE [Part::Part2DObjectPython] Line638  # Draft 2D object (typed FeaturePython)
  ChamferSize = 0
  Closed = false
  End = (-1026.05,17151.7,0)
  FilletRadius = 0
  Length = 237
  MakeFace = true
  Placement = pos=(-13279.1,536.194,0) rot=(0,0,1;0rad)
  Points = (2) [(12016.1,16615.5,0),(12253.1,16615.5,0)]
  Start = (-1263.05,17151.7,0)
FEATURE [Part::Part2DObjectPython] Line639  # Draft 2D object (typed FeaturePython)
  ChamferSize = 0
  Closed = false
  End = (-1263.05,18153.4,0)
  FilletRadius = 0
  Length = 2003.39
  MakeFace = true
  Placement = pos=(-25503.4,0.388456,0) rot=(0,0,1;0rad)
  Points = (2) [(24240.3,16149.6,0),(24240.3,18153,0)]
  Start = (-1263.05,16150,0)
FEATURE [App::FeaturePython] Dimension106  # Draft dimension (typed FeaturePython)
  Dimline = (-1026.05,13020,0)
  Direction = (0,0,0)
  Distance = 3130
  End = (-5,13020,0)
  Normal = (0,0,1)
  Start = (-4.99902,16150,0)
FEATURE [Part::Part2DObjectPython] Line640  # Draft 2D object (typed FeaturePython)
  ChamferSize = 0
  Closed = false
  End = (14250,1850,0)
  FilletRadius = 0
  Length = 3255
  MakeFace = true
  Points = (2) [(10995,1850,0),(14250,1850,0)]
  Start = (10995,1850,0)
FEATURE [Part::Part2DObjectPython] Line641  # Draft 2D object (typed FeaturePython)
  ChamferSize = 0
  Closed = false
  End = (14250,876.782,0)
  FilletRadius = 0
  Length = 3255
  MakeFace = true
  Points = (2) [(10995,876.782,0),(14250,876.782,0)]
  Start = (10995,876.782,0)
FEATURE [Part::Part2DObjectPython] Line642  # Draft 2D object (typed FeaturePython)
  ChamferSize = 0
  Closed = false
  End = (14250,678.716,0)
  FilletRadius = 0
  Length = 3255
  MakeFace = true
  Points = (2) [(10995,678.716,0),(14250,678.716,0)]
  Start = (10995,678.716,0)
FEATURE [Part::Part2DObjectPython] Line643  # Draft 2D object (typed FeaturePython)
  ChamferSize = 0
  Closed = false
  End = (14250,444.997,0)
  FilletRadius = 0
  Length = 3255
  MakeFace = true
  Points = (2) [(10995,444.997,0),(14250,444.997,0)]
  Start = (10995,444.997,0)
FEATURE [Part::Part2DObjectPython] Line644  # Draft 2D object (typed FeaturePython)
  ChamferSize = 0
  Closed = false
  End = (12633,876.782,0)
  FilletRadius = 0
  Length = 973.218
  MakeFace = true
  Points = (2) [(12633,1850,0),(12633,876.782,0)]
  Start = (12633,1850,0)
FEATURE [Part::Part2DObjectPython] Line645  # Draft 2D object (typed FeaturePython)
  ChamferSize = 0
  Closed = false
  End = (12633,678.716,0)
  FilletRadius = 0
  Length = 198.066
  MakeFace = true
  Points = (2) [(12633,876.782,0),(12633,678.716,0)]
  Start = (12633,876.782,0)
FEATURE [Part::Part2DObjectPython] Line646  # Draft 2D object (typed FeaturePython)
  ChamferSize = 0
  Closed = false
  End = (12633,444.997,0)
  FilletRadius = 0
  Length = 233.719
  MakeFace = true
  Points = (2) [(12633,678.716,0),(12633,444.997,0)]
  Start = (12633,678.716,0)
FEATURE [Part::Part2DObjectPython] Line647  # Draft 2D object (typed FeaturePython)
  ChamferSize = 0
  Closed = false
  End = (13790,16150,0)
  FilletRadius = 0
  Length = 2795
  MakeFace = true
  Points = (2) [(10995,16150,0),(13790,16150,0)]
  Start = (10995,16150,0)
FEATURE [Part::Part2DObjectPython] Line649  # Draft 2D object (typed FeaturePython)
  ChamferSize = 0
  Closed = false
  End = (12392.5,16150,0)
  FilletRadius = 0
  Length = 973.218
  MakeFace = true
  Placement = pos=(-240.5,15273.2,0) rot=(0,0,1;0rad)
  Points = (2) [(12633,1850,0),(12633,876.782,0)]
  Start = (12392.5,17123.2,0)
FEATURE [Part::Part2DObjectPython] Line650  # Draft 2D object (typed FeaturePython)
  ChamferSize = 0
  Closed = false
  End = (13790,17123.2,0)
  FilletRadius = 0
  Length = 2795
  MakeFace = true
  Points = (2) [(10995,17123.2,0),(13790,17123.2,0)]
  Start = (10995,17123.2,0)
FEATURE [Part::Part2DObjectPython] Line651  # Draft 2D object (typed FeaturePython)
  ChamferSize = 0
  Closed = false
  End = (12392.5,17123.2,0)
  FilletRadius = 0
  Length = 198.066
  MakeFace = true
  Placement = pos=(-240.5,16444.5,0) rot=(0,0,1;0rad)
  Points = (2) [(12633,876.782,0),(12633,678.716,0)]
  Start = (12392.5,17321.3,0)
FEATURE [Part::Part2DObjectPython] Line652  # Draft 2D object (typed FeaturePython)
  ChamferSize = 0
  Closed = false
  End = (13790,17321.3,0)
  FilletRadius = 0
  Length = 2795
  MakeFace = true
  Points = (2) [(10995,17321.3,0),(13790,17321.3,0)]
  Start = (10995,17321.3,0)
FEATURE [Part::Part2DObjectPython] Line653  # Draft 2D object (typed FeaturePython)
  ChamferSize = 0
  Closed = false
  End = (12392.5,17321.3,0)
  FilletRadius = 0
  Length = 233.719
  MakeFace = true
  Placement = pos=(-240.5,16876.3,0) rot=(0,0,1;0rad)
  Points = (2) [(12633,678.716,0),(12633,444.997,0)]
  Start = (12392.5,17555,0)
FEATURE [Part::Part2DObjectPython] Line654  # Draft 2D object (typed FeaturePython)
  ChamferSize = 0
  Closed = false
  End = (13790,17555,0)
  FilletRadius = 0
  Length = 2795
  MakeFace = true
  Points = (2) [(10995,17555,0),(13790,17555,0)]
  Start = (10995,17555,0)
FEATURE [Part::Part2DObjectPython] Line655  # Draft 2D object (typed FeaturePython)
  ChamferSize = 0
  Closed = false
  End = (25516,17123.2,0)
  FilletRadius = 0
  Length = 11726
  MakeFace = true
  Points = (2) [(13790,17123.2,0),(25516,17123.2,0)]
  Start = (13790,17123.2,0)
FEATURE [Part::Part2DObjectPython] Line656  # Draft 2D object (typed FeaturePython)
  ChamferSize = 0
  Closed = false
  End = (25534,17321.3,0)
  FilletRadius = 0
  Length = 11744
  MakeFace = true
  Points = (2) [(13790,17321.3,0),(25534,17321.3,0)]
  Start = (13790,17321.3,0)
FEATURE [Part::Part2DObjectPython] Line657  # Draft 2D object (typed FeaturePython)
  ChamferSize = 0
  Closed = false
  End = (25409,17555,0)
  FilletRadius = 0
  Length = 11619
  MakeFace = true
  Points = (2) [(13790,17555,0),(25409,17555,0)]
  Start = (13790,17555,0)
FEATURE [App::FeaturePython] Dimension107  # Draft dimension (typed FeaturePython)
  Dimline = (-94.3828,17555.4,0)
  Direction = (0,0,0)
  Distance = 11000
  End = (10995,16150,0)
  Normal = (0,0,1)
  Start = (-5.00098,16150,0)
FEATURE [App::FeaturePython] Dimension108  # Draft dimension (typed FeaturePython)
  Dimline = (-5.00098,17321.7,0)
  Direction = (0,0,0)
  Distance = 3100
  End = (3095,16150,0)
  Normal = (0,0,1)
  Start = (-5.00098,16150,0)
FEATURE [App::FeaturePython] Dimension109  # Draft dimension (typed FeaturePython)
  Dimline = (3095,17321.7,0)
  Direction = (0,0,0)
  Distance = 7900
  End = (10995,16150,0)
  Normal = (0,0,1)
  Start = (3095,16150,0)
FEATURE [App::FeaturePython] Dimension110  # Draft dimension (typed FeaturePython)
  Dimline = (12.6172,17123.6,0)
  Direction = (0,0,0)
  Distance = 150
  End = (144.999,16150,0)
  Normal = (0,0,1)
  Start = (-5.00098,16150,0)
FEATURE [App::FeaturePython] Dimension111  # Draft dimension (typed FeaturePython)
  Dimline = (144.999,17123.6,0)
  Direction = (0,0,0)
  Distance = 2950
  End = (3095,16150,0)
  Normal = (0,0,1)
  Start = (144.999,16150,0)
FEATURE [App::FeaturePython] Dimension112  # Draft dimension (typed FeaturePython)
  Dimline = (3095,17123.6,0)
  Direction = (0,0,0)
  Distance = 150
  End = (3245,16150,0)
  Normal = (0,0,1)
  Start = (3095,16150,0)
FEATURE [App::FeaturePython] Dimension113  # Draft dimension (typed FeaturePython)
  Dimline = (3245,17123.6,0)
  Direction = (0,0,0)
  Distance = 2550
  End = (5795,16150,0)
  Normal = (0,0,1)
  Start = (3245,16150,0)
FEATURE [App::FeaturePython] Dimension114  # Draft dimension (typed FeaturePython)
  Dimline = (5795,17123.6,0)
  Direction = (0,0,0)
  Distance = 150
  End = (5945,16150,0)
  Normal = (0,0,1)
  Start = (5795,16150,0)
FEATURE [App::FeaturePython] Dimension115  # Draft dimension (typed FeaturePython)
  Dimline = (5945,17123.6,0)
  Direction = (0,0,0)
  Distance = 1200
  End = (7145,16000,0)
  Normal = (0,0,1)
  Start = (5945,16000,0)
FEATURE [App::FeaturePython] Dimension116  # Draft dimension (typed FeaturePython)
  Dimline = (7145,17123.6,0)
  Direction = (0,0,0)
  Distance = 3700
  End = (10845,16000,0)
  Normal = (0,0,1)
  Start = (7145,16000,0)
FEATURE [App::FeaturePython] Dimension117  # Draft dimension (typed FeaturePython)
  Dimline = (10845,17123.6,0)
  Direction = (0,0,0)
  Distance = 150
  End = (10995,16150,0)
  Normal = (0,0,1)
  Start = (10845,16150,0)
FEATURE [App::FeaturePython] Dimension127  # Draft dimension (typed FeaturePython)
  Dimline = (909.617,4149.39,0)
  Direction = (0,0,0)
  Distance = 2350.39
  End = (751.617,4500.39,0)
  Normal = (0,0,1)
  Start = (751.128,2150,0)
FEATURE [App::FeaturePython] Dimension129  # Draft dimension (typed FeaturePython)
  Dimline = (909.69,4650,0)
  Direction = (0,0,0)
  Distance = 1850
  End = (2495.03,6500,0)
  Normal = (0,0,1)
  Start = (2495.03,4650,0)
FEATURE [App::FeaturePython] Dimension131  # Draft dimension (typed FeaturePython)
  Dimline = (909.69,6650,0)
  Direction = (0,0,0)
  Distance = 1600
  End = (2095,8250,0)
  Normal = (0,0,1)
  Start = (2095,6650,0)
FEATURE [App::FeaturePython] Dimension132  # Draft dimension (typed FeaturePython)
  Dimline = (909.69,8250,0)
  Direction = (0,0,0)
  Distance = 150
  End = (1620,8400,0)
  Normal = (0,0,1)
  Start = (1620,8250,0)
FEATURE [App::FeaturePython] Dimension133  # Draft dimension (typed FeaturePython)
  Dimline = (909.69,8400,0)
  Direction = (0,0,0)
  Distance = 1200
  End = (1620,9600,0)
  Normal = (0,0,1)
  Start = (1620,8400,0)
FEATURE [App::FeaturePython] Dimension134  # Draft dimension (typed FeaturePython)
  Dimline = (909.69,9600,0)
  Direction = (0,0,0)
  Distance = 150
  End = (144.999,9750,0)
  Normal = (0,0,1)
  Start = (144.999,9600,0)
FEATURE [App::FeaturePython] Dimension135  # Draft dimension (typed FeaturePython)
  Dimline = (909.69,9600,0)
  Direction = (0,0,0)
  Distance = 3120
  End = (144.999,12870,0)
  Normal = (0,0,1)
  Start = (144.999,9750,0)
FEATURE [App::FeaturePython] Dimension137  # Draft dimension (typed FeaturePython)
  Dimline = (9066.62,14406.4,0)
  Direction = (0,0,0)
  Distance = 150
  End = (8945,14020,0)
  Normal = (0,0,1)
  Start = (8795,14020,0)
FEATURE [App::FeaturePython] Dimension138  # Draft dimension (typed FeaturePython)
  Dimline = (8945,14406.4,0)
  Direction = (0,0,0)
  Distance = 1900
  End = (10845,14020,0)
  Normal = (0,0,1)
  Start = (8945,14020,0)
FEATURE [App::FeaturePython] Dimension140  # Draft dimension (typed FeaturePython)
  Dimline = (909.69,12870,0)
  Direction = (0,0,0)
  Distance = 150
  End = (294.999,13020,0)
  Normal = (0,0,1)
  Start = (294.999,12870,0)
FEATURE [App::FeaturePython] Dimension141  # Draft dimension (typed FeaturePython)
  Dimline = (909.69,6650,0)
  Direction = (0,0,0)
  Distance = 150
  End = (144.999,6650,0)
  Normal = (0,0,1)
  Start = (144.999,6500,0)
FEATURE [App::FeaturePython] Dimension142  # Draft dimension (typed FeaturePython)
  Dimline = (909.69,4650,0)
  Direction = (0,0,0)
  Distance = 150
  End = (2495.03,4650,0)
  Normal = (0,0,1)
  Start = (2495.03,4500,0)
FEATURE [App::FeaturePython] Dimension143  # Draft dimension (typed FeaturePython)
  Dimline = (3094.62,11923.4,0)
  Direction = (0,0,0)
  Distance = 2950
  End = (3095,9600,0)
  Normal = (0,0,1)
  Start = (144.999,9600,0)
FEATURE [App::FeaturePython] Dimension144  # Draft dimension (typed FeaturePython)
  Dimline = (3095,11923.4,0)
  Direction = (0,0,0)
  Distance = 150
  End = (3245,9600,0)
  Normal = (0,0,1)
  Start = (3095,9600,0)
FEATURE [App::FeaturePython] Dimension145  # Draft dimension (typed FeaturePython)
  Dimline = (3245,11923.4,0)
  Direction = (0,0,0)
  Distance = 1200
  End = (4445,9600,0)
  Normal = (0,0,1)
  Start = (3245,9600,0)
FEATURE [App::FeaturePython] Dimension146  # Draft dimension (typed FeaturePython)
  Dimline = (4445,11923.4,0)
  Direction = (0,0,0)
  Distance = 150
  End = (4595,9750,0)
  Normal = (0,0,1)
  Start = (4445,9750,0)
FEATURE [App::FeaturePython] Dimension147  # Draft dimension (typed FeaturePython)
  Dimline = (4445,11923.4,0)
  Direction = (0,0,0)
  Distance = 1200
  End = (5794.99,10989.9,0)
  Normal = (0,0,1)
  Start = (4595,10989.9,0)
FEATURE [App::FeaturePython] Dimension148  # Draft dimension (typed FeaturePython)
  Dimline = (5794.99,11923.4,0)
  Direction = (0,0,0)
  Distance = 150
  End = (5945,8550,0)
  Normal = (0,0,1)
  Start = (5795,8550,0)
FEATURE [App::FeaturePython] Dimension149  # Draft dimension (typed FeaturePython)
  Dimline = (5795,11923.4,0)
  Direction = (0,0,0)
  Distance = 4900
  End = (10845,8550,0)
  Normal = (0,0,1)
  Start = (5945,8550,0)
FEATURE [App::FeaturePython] Dimension150  # Draft dimension (typed FeaturePython)
  Dimline = (4745.62,3454.39,0)
  Direction = (0,0,0)
  Distance = 2550
  End = (5795,3999.61,0)
  Normal = (0,0,1)
  Start = (3245,3999.61,0)
FEATURE [Part::Part2DObjectPython] DWire206  # Draft 2D object (typed FeaturePython)
  ChamferSize = 0
  Closed = true
  End = (145,12150,3000)
  FilletRadius = 0
  Length = 16000
  MakeFace = true
  Placement = pos=(-42142,0.388761,3000) rot=(0,0,1;0rad)
  Points = (4) [(42287,15849.6,0),(46587,15849.6,0),(46587,12149.6,0),(42287,12149.6,0)]
  Start = (145,15850,3000)
FEATURE [Part::Part2DObjectPython] DWire207  # Draft 2D object (typed FeaturePython)
  ChamferSize = 0
  Closed = true
  End = (4595,13020,3000)
  FilletRadius = 0
  Length = 27400
  MakeFace = true
  Placement = pos=(-42142,0.388761,3000) rot=(0,0,1;0rad)
  Points = (8) [(46737,15849.6,0),(49287,15849.6,0),(49287,6049.61,0),(46737,6049.61,0),(46737,8249.61,0),(48087,8249.61,0),(48087,13019.6,0),(46737,13019.6,0)]
  Start = (4595,15850,3000)
FEATURE [Part::Part2DObjectPython] DWire208  # Draft 2D object (typed FeaturePython)
  ChamferSize = 0
  Closed = true
  End = (3170,12000,3000)
  FilletRadius = 0
  Length = 14300
  MakeFace = true
  Placement = pos=(-42142,0.388761,3000) rot=(0,0,1;0rad)
  Points = (8) [(46587,11999.6,0),(46587,9749.61,0),(42287,9749.61,0),(42287,11999.6,0),(45162,11999.6,0),(45162,11399.6,0),(45312,11399.6,0),(45312,11999.6,0)]
  Start = (4445,12000,3000)
FEATURE [Part::Part2DObjectPython] DWire209  # Draft 2D object (typed FeaturePython)
  ChamferSize = 0
  Closed = true
  End = (145,7400,3000)
  FilletRadius = 0
  Length = 13000
  MakeFace = true
  Placement = pos=(-42142,0.388761,3000) rot=(0,0,1;0rad)
  Points = (4) [(42287,9599.61,0),(46587,9599.61,0),(46587,7399.61,0),(42287,7399.61,0)]
  Start = (145,9600,3000)
FEATURE [Part::Part2DObjectPython] DWire210  # Draft 2D object (typed FeaturePython)
  ChamferSize = 0
  Closed = true
  End = (145,2150,3000)
  FilletRadius = 0
  Length = 21500
  MakeFace = true
  Placement = pos=(-42142,0.388761,3000) rot=(0,0,1;0rad)
  Points = (6) [(42287,7249.61,0),(46587,7249.61,0),(46587,5899.61,0),(47937,5899.61,0),(47937,2149.61,0),(42287,2149.61,0)]
  Start = (145,7250,3000)
FEATURE [Part::Part2DObjectPython] DWire211  # Draft 2D object (typed FeaturePython)
  ChamferSize = 0
  Closed = true
  End = (5945,2000,3000)
  FilletRadius = 0
  Length = 17900
  MakeFace = true
  Placement = pos=(-42142,0.388761,3000) rot=(0,0,1;0rad)
  Points = (8) [(48087,5899.61,0),(52987,5899.61,0),(52987,5749.61,0),(53137,5749.61,0),(53137,2149.61,0),(52987,2149.61,0),(52987,1999.61,0),(48087,1999.61,0)]
  Start = (5945,5900,3000)
FEATURE [Part::Part2DObjectPython] DWire212  # Draft 2D object (typed FeaturePython)
  ChamferSize = 0
  Closed = true
  End = (7295,8250,3000)
  FilletRadius = 0
  Length = 16300
  MakeFace = true
  Placement = pos=(-42142,0.388761,3000) rot=(0,0,1;0rad)
  Points = (8) [(49437,6049.61,0),(52987,6049.61,0),(52987,10049.6,0),(49437,10049.6,0),(49437,8399.61,0),(50037,8399.61,0),(50037,8249.61,0),(49437,8249.61,0)]
  Start = (7295,6050,3000)
FEATURE [Part::Part2DObjectPython] DWire213  # Draft 2D object (typed FeaturePython)
  ChamferSize = 0
  Closed = true
  End = (7295,10200,3000)
  FilletRadius = 0
  Length = 10100
  MakeFace = true
  Placement = pos=(-42142,0.388761,3000) rot=(0,0,1;0rad)
  Points = (4) [(49437,11699.6,0),(52987,11699.6,0),(52987,10199.6,0),(49437,10199.6,0)]
  Start = (7295,11700,3000)
FEATURE [Part::Part2DObjectPython] DWire214  # Draft 2D object (typed FeaturePython)
  ChamferSize = 0
  Closed = true
  End = (7295,13650,3000)
  FilletRadius = 0
  Length = 16300
  MakeFace = true
  Placement = pos=(-42142,0.388761,3000) rot=(0,0,1;0rad)
  Points = (8) [(49437,15849.6,0),(52987,15849.6,0),(52987,11849.6,0),(49437,11849.6,0),(49437,13499.6,0),(50037,13499.6,0),(50037,13649.6,0),(49437,13649.6,0)]
  Start = (7295,15850,3000)
FEATURE [Part::Extrusion] Extrusion055
  Base = -> DWire206
  Dir = (0,0,2800)
  Solid = true
FEATURE [Part::Extrusion] Extrusion056
  Base = -> DWire207
  Dir = (0,0,2800)
  Solid = true
FEATURE [Part::Extrusion] Extrusion057
  Base = -> DWire214
  Dir = (0,0,2800)
  Solid = true
FEATURE [Part::Extrusion] Extrusion058
  Base = -> DWire208
  Dir = (0,0,2800)
  Solid = true
FEATURE [Part::Extrusion] Extrusion059
  Base = -> DWire213
  Dir = (0,0,2800)
  Solid = true
FEATURE [Part::Extrusion] Extrusion060
  Base = -> DWire212
  Dir = (0,0,2800)
  Solid = true
FEATURE [Part::Extrusion] Extrusion061
  Base = -> DWire211
  Dir = (0,0,2800)
  Solid = true
FEATURE [Part::Extrusion] Extrusion062
  Base = -> DWire210
  Dir = (0,0,2800)
  Solid = true
FEATURE [Part::Extrusion] Extrusion063
  Base = -> DWire209
  Dir = (0,0,2800)
  Solid = true
FEATURE [Part::FeaturePython] Space011  label="Balcony"  # WARN: FeaturePython — macro-defined, semantics opaque (R4)
  Area = 1.965e+07
  Base = -> Extrusion061
  MoveWithHost = false
  Role = 0
FEATURE [Part::FeaturePython] Space012  label="Master Bedroom"  # WARN: FeaturePython — macro-defined, semantics opaque (R4)
  Area = 2.69925e+07
  Base = -> Extrusion062
  MoveWithHost = false
  Role = 0
FEATURE [Part::FeaturePython] Space013  label="Master Bathroom"  # WARN: FeaturePython — macro-defined, semantics opaque (R4)
  Area = 9.46e+06
  Base = -> Extrusion063
  MoveWithHost = false
  Role = 0
FEATURE [Part::FeaturePython] Space014  label="Study"  # WARN: FeaturePython — macro-defined, semantics opaque (R4)
  Area = 9.585e+06
  Base = -> Extrusion058
  MoveWithHost = false
  Role = 0
FEATURE [Part::FeaturePython] Space015  label="Small Living"  # WARN: FeaturePython — macro-defined, semantics opaque (R4)
  Area = 1.591e+07
  Base = -> Extrusion055
  MoveWithHost = false
  Role = 0
FEATURE [Part::FeaturePython] Space017  label="Bedroom 1"  # WARN: FeaturePython — macro-defined, semantics opaque (R4)
  Area = 1.411e+07
  Base = -> Extrusion060
  MoveWithHost = false
  Role = 0
FEATURE [Part::FeaturePython] Space018  label="Bedroom 2"  # WARN: FeaturePython — macro-defined, semantics opaque (R4)
  Area = 1.411e+07
  Base = -> Extrusion057
  MoveWithHost = false
  Role = 0
FEATURE [Part::FeaturePython] Space019  label="Bathroom"  # WARN: FeaturePython — macro-defined, semantics opaque (R4)
  Area = 5.325e+06
  Base = -> Extrusion059
  MoveWithHost = false
  Role = 0
FEATURE [Part::FeaturePython] Space020  label="Stair Corridor"  # WARN: FeaturePython — macro-defined, semantics opaque (R4)
  Area = 1.85505e+07
  Base = -> Extrusion056
  MoveWithHost = false
  Role = 0
FEATURE [App::DocumentObjectGroup] Group038  label="Level 2 Spaces"
  Group = -> [Space011,Space012,Space013,Space014,Space015,Space017,Space018,Space019,Space020]
FEATURE [App::DocumentObjectGroup] Group036  label="Spaces"
  Group = -> [Group037,Group038]
FEATURE [Part::Part2DObjectPython] Line658  # Draft 2D object (typed FeaturePython)
  ChamferSize = 0
  Closed = false
  End = (40878.9,18153,0)
  FilletRadius = 0
  Length = 2003.39
  MakeFace = true
  Placement = pos=(16638.6,-0.000305198,0) rot=(0,0,1;0rad)
  Points = (2) [(24240.3,16149.6,0),(24240.3,18153,0)]
  Start = (40878.9,16149.6,0)
FEATURE [Part::Part2DObjectPython] Line659  # Draft 2D object (typed FeaturePython)
  ChamferSize = 0
  Closed = false
  End = (41115.9,18153,0)
  FilletRadius = 0
  Length = 2003.39
  MakeFace = true
  Placement = pos=(16638.6,-0.000305198,0) rot=(0,0,1;0rad)
  Points = (2) [(24477.3,16149.6,0),(24477.3,18153,0)]
  Start = (41115.9,16149.6,0)
FEATURE [Part::Part2DObjectPython] Line660  # Draft 2D object (typed FeaturePython)
  ChamferSize = 0
  Closed = false
  End = (41304.9,18153,0)
  FilletRadius = 0
  Length = 2003.39
  MakeFace = true
  Placement = pos=(16638.6,-0.000305198,0) rot=(0,0,1;0rad)
  Points = (2) [(24666.3,16149.6,-5.7e-14),(24666.3,18153,-5.7e-14)]
  Start = (41304.9,16149.6,0)
FEATURE [Part::Part2DObjectPython] Line661  # Draft 2D object (typed FeaturePython)
  ChamferSize = 0
  Closed = false
  End = (53137,17080.6,0)
  FilletRadius = 0
  Length = 931
  MakeFace = true
  Placement = pos=(42142,-0.388761,0) rot=(0,0,1;0rad)
  Points = (2) [(10995,16150,0),(10995,17081,0)]
  Start = (53137,16149.6,0)
FEATURE [Part::Part2DObjectPython] Line662  # Draft 2D object (typed FeaturePython)
  ChamferSize = 0
  Closed = false
  End = (53969.1,17080.6,0)
  FilletRadius = 0
  Length = 931
  MakeFace = true
  Placement = pos=(42142,-0.388761,0) rot=(0,0,1;0rad)
  Points = (2) [(11827.1,16150,5.7e-14),(11827.1,17081,5.7e-14)]
  Start = (53969.1,16149.6,0)
FEATURE [Part::Part2DObjectPython] Line663  # Draft 2D object (typed FeaturePython)
  ChamferSize = 0
  Closed = false
  End = (54158.1,17080.6,0)
  FilletRadius = 0
  Length = 931
  MakeFace = true
  Placement = pos=(42142,-0.388761,0) rot=(0,0,1;0rad)
  Points = (2) [(12016.1,16150,0),(12016.1,17081,0)]
  Start = (54158.1,16149.6,0)
FEATURE [Part::Part2DObjectPython] Line664  # Draft 2D object (typed FeaturePython)
  ChamferSize = 0
  Closed = false
  End = (54395.1,17080.6,0)
  FilletRadius = 0
  Length = 931
  MakeFace = true
  Placement = pos=(42142,-0.388761,0) rot=(0,0,1;0rad)
  Points = (2) [(12253.1,16150,0),(12253.1,17081,0)]
  Start = (54395.1,16149.6,0)
FEATURE [Part::Part2DObjectPython] Line665  # Draft 2D object (typed FeaturePython)
  ChamferSize = 0
  Closed = false
  End = (42137,18153,0)
  FilletRadius = 0
  Length = 2003.39
  MakeFace = true
  Placement = pos=(16638.6,-0.000305198,0) rot=(0,0,1;0rad)
  Points = (2) [(25498.4,16149.6,0),(25498.4,18153,0)]
  Start = (42137,16149.6,0)
FEATURE [Part::Part2DObjectPython] Line666  # Draft 2D object (typed FeaturePython)
  ChamferSize = 0
  Closed = false
  End = (55568,876.782,0)
  FilletRadius = 0
  Length = 3255
  MakeFace = true
  Placement = pos=(41318,3e-12,0) rot=(0,0,1;0rad)
  Points = (2) [(10995,876.782,0),(14250,876.782,0)]
  Start = (52313,876.782,0)
FEATURE [Part::Part2DObjectPython] Line667  # Draft 2D object (typed FeaturePython)
  ChamferSize = 0
  Closed = false
  End = (55568,678.716,0)
  FilletRadius = 0
  Length = 3255
  MakeFace = true
  Placement = pos=(41318,3e-12,0) rot=(0,0,1;0rad)
  Points = (2) [(10995,678.716,0),(14250,678.716,0)]
  Start = (52313,678.716,0)
FEATURE [Part::Part2DObjectPython] Line668  # Draft 2D object (typed FeaturePython)
  ChamferSize = 0
  Closed = false
  End = (55568,444.997,0)
  FilletRadius = 0
  Length = 3255
  MakeFace = true
  Placement = pos=(41318,3e-12,0) rot=(0,0,1;0rad)
  Points = (2) [(10995,444.997,0),(14250,444.997,0)]
  Start = (52313,444.997,0)
FEATURE [Part::Part2DObjectPython] Line669  # Draft 2D object (typed FeaturePython)
  ChamferSize = 0
  Closed = false
  End = (61276,17555,0)
  FilletRadius = 0
  Length = 6880.95
  MakeFace = true
  Placement = pos=(35867,4e-12,0) rot=(0,0,1;0rad)
  Points = (2) [(18528.1,17555,0),(25409,17555,0)]
  Start = (54395.1,17555,0)
FEATURE [Part::Part2DObjectPython] Line670  # Draft 2D object (typed FeaturePython)
  ChamferSize = 0
  Closed = false
  End = (61401,17321.3,0)
  FilletRadius = 0
  Length = 7005.95
  MakeFace = true
  Placement = pos=(35867,4e-12,0) rot=(0,0,1;0rad)
  Points = (2) [(18528.1,17321.3,0),(25534,17321.3,0)]
  Start = (54395.1,17321.3,0)
FEATURE [Part::Part2DObjectPython] Line671  # Draft 2D object (typed FeaturePython)
  ChamferSize = 0
  Closed = false
  End = (61383,17123.2,0)
  FilletRadius = 0
  Length = 6987.95
  MakeFace = true
  Placement = pos=(35867,4e-12,0) rot=(0,0,1;0rad)
  Points = (2) [(18528.1,17123.2,0),(25516,17123.2,0)]
  Start = (54395.1,17123.2,0)
FEATURE [App::FeaturePython] Dimension152  # Draft dimension (typed FeaturePython)
  Dimline = (12253.1,16150,3000)
  Direction = (0,0,0)
  Distance = 14300
  End = (10995,1850,3000)
  Normal = (0,0,1)
  Start = (10995,16150,3000)
FEATURE [App::FeaturePython] Dimension153  # Draft dimension (typed FeaturePython)
  Dimline = (12016.1,16150,3000)
  Direction = (0,0,0)
  Distance = 10400
  End = (10995,5750,3000)
  Normal = (0,0,1)
  Start = (10995,16150,3000)
FEATURE [App::FeaturePython] Dimension154  # Draft dimension (typed FeaturePython)
  Dimline = (12016.1,5750,3000)
  Direction = (0,0,0)
  Distance = 3900
  End = (10995,1850,3000)
  Normal = (0,0,1)
  Start = (10995,5750,3000)
FEATURE [App::FeaturePython] Dimension155  # Draft dimension (typed FeaturePython)
  Dimline = (11827.1,16150,3000)
  Direction = (0,0,0)
  Distance = 300
  End = (10995,15850,3000)
  Normal = (0,0,1)
  Start = (10995,16150,3000)
FEATURE [App::FeaturePython] Dimension156  # Draft dimension (typed FeaturePython)
  Dimline = (11827.1,15850,3000)
  Direction = (0,0,0)
  Distance = 1471.2
  End = (10995,14378.8,3000)
  Normal = (0,0,1)
  Start = (10995,15850,3000)
FEATURE [App::FeaturePython] Dimension157  # Draft dimension (typed FeaturePython)
  Dimline = (11827.1,14378.8,3000)
  Direction = (0,0,0)
  Distance = 1000
  End = (10995,13378.8,3000)
  Normal = (0,0,1)
  Start = (10995,14378.8,3000)
FEATURE [App::FeaturePython] Dimension158  # Draft dimension (typed FeaturePython)
  Dimline = (11827.1,13378.8,3000)
  Direction = (0,0,0)
  Distance = 358.804
  End = (10995,13020,3000)
  Normal = (0,0,1)
  Start = (10995,13378.8,3000)
FEATURE [App::FeaturePython] Dimension159  # Draft dimension (typed FeaturePython)
  Dimline = (11827.1,13020,3000)
  Direction = (0,0,0)
  Distance = 300
  End = (10995,12720,3000)
  Normal = (0,0,1)
  Start = (10995,13020,3000)
FEATURE [App::FeaturePython] Dimension163  # Draft dimension (typed FeaturePython)
  Dimline = (11827.1,8550,3000)
  Direction = (0,0,0)
  Distance = 300
  End = (10995,8250,3000)
  Normal = (0,0,1)
  Start = (10995,8550,3000)
FEATURE [App::FeaturePython] Dimension164  # Draft dimension (typed FeaturePython)
  Dimline = (11827.1,8250,3000)
  Direction = (0,0,0)
  Distance = 1000
  End = (10995,7250,3000)
  Normal = (0,0,1)
  Start = (10995,8250,3000)
FEATURE [App::FeaturePython] Dimension165  # Draft dimension (typed FeaturePython)
  Dimline = (11827.1,7250,3000)
  Direction = (0,0,0)
  Distance = 1200
  End = (10995,6050,3000)
  Normal = (0,0,1)
  Start = (10995,7250,3000)
FEATURE [App::FeaturePython] Dimension166  # Draft dimension (typed FeaturePython)
  Dimline = (11827.1,6050,3000)
  Direction = (0,0,0)
  Distance = 300
  End = (10995,5750,3000)
  Normal = (0,0,1)
  Start = (10995,6050,3000)
FEATURE [App::FeaturePython] Dimension167  # Draft dimension (typed FeaturePython)
  Dimline = (11827.1,5750,3000)
  Direction = (0,0,0)
  Distance = 3600
  End = (10995,2150,3000)
  Normal = (0,0,1)
  Start = (10995,5750,3000)
FEATURE [App::FeaturePython] Dimension168  # Draft dimension (typed FeaturePython)
  Dimline = (11827.1,2150,3000)
  Direction = (0,0,0)
  Distance = 300
  End = (10995,1850,3000)
  Normal = (0,0,1)
  Start = (10995,2150,3000)
FEATURE [App::FeaturePython] Dimension169  # Draft dimension (typed FeaturePython)
  Dimline = (12253.1,17555.4,3000)
  Direction = (0,0,0)
  Distance = 11000
  End = (-4.99643,16150,3000)
  Normal = (0,0,1)
  Start = (10995,16150,3000)
FEATURE [App::FeaturePython] Dimension170  # Draft dimension (typed FeaturePython)
  Dimline = (12253.1,17321.7,3000)
  Direction = (0,0,0)
  Distance = 150
  End = (145.004,16150,3000)
  Normal = (0,0,1)
  Start = (-4.99643,16150,3000)
FEATURE [App::FeaturePython] Dimension171  # Draft dimension (typed FeaturePython)
  Dimline = (12253.1,17321.7,3000)
  Direction = (0,0,0)
  Distance = 2950
  End = (3095,16150,3000)
  Normal = (0,0,1)
  Start = (145.004,16150,3000)
FEATURE [App::FeaturePython] Dimension172  # Draft dimension (typed FeaturePython)
  Dimline = (12253.1,17321.7,3000)
  Direction = (0,0,0)
  Distance = 150
  End = (3245,16150,3000)
  Normal = (0,0,1)
  Start = (3095,16150,3000)
FEATURE [App::FeaturePython] Dimension173  # Draft dimension (typed FeaturePython)
  Dimline = (12253.1,17321.7,3000)
  Direction = (0,0,0)
  Distance = 1350
  End = (4595,16000,3000)
  Normal = (0,0,1)
  Start = (3245,16000,3000)
FEATURE [App::FeaturePython] Dimension174  # Draft dimension (typed FeaturePython)
  Dimline = (12253.1,17321.7,3000)
  Direction = (0,0,0)
  Distance = 1200
  End = (5795,16000,3000)
  Normal = (0,0,1)
  Start = (4595,16000,3000)
FEATURE [App::FeaturePython] Dimension175  # Draft dimension (typed FeaturePython)
  Dimline = (12253.1,17321.7,3000)
  Direction = (0,0,0)
  Distance = 150
  End = (5945,16150,3000)
  Normal = (0,0,1)
  Start = (5795,16150,3000)
FEATURE [App::FeaturePython] Dimension176  # Draft dimension (typed FeaturePython)
  Dimline = (12253.1,17321.7,3000)
  Direction = (0,0,0)
  Distance = 1200
  End = (7145,16000,3000)
  Normal = (0,0,1)
  Start = (5945,16000,3000)
FEATURE [App::FeaturePython] Dimension177  # Draft dimension (typed FeaturePython)
  Dimline = (12253.1,17321.7,3000)
  Direction = (0,0,0)
  Distance = 3700
  End = (10845,16000,3000)
  Normal = (0,0,1)
  Start = (7145,16000,3000)
FEATURE [App::FeaturePython] Dimension178  # Draft dimension (typed FeaturePython)
  Dimline = (12253.1,17321.7,3000)
  Direction = (0,0,0)
  Distance = 150
  End = (10995,16150,3000)
  Normal = (0,0,1)
  Start = (10845,16150,3000)
FEATURE [App::FeaturePython] Dimension179  # Draft dimension (typed FeaturePython)
  Dimline = (-1263.05,16150,3000)
  Direction = (0,0,0)
  Distance = 14300
  End = (-4.99643,1850,3000)
  Normal = (0,0,1)
  Start = (-4.99643,16150,3000)
FEATURE [App::FeaturePython] Dimension180  # Draft dimension (typed FeaturePython)
  Dimline = (-1026.05,16150,3000)
  Direction = (0,0,0)
  Distance = 300
  End = (-4.99643,15850,3000)
  Normal = (0,0,1)
  Start = (-4.99643,16150,3000)
FEATURE [App::FeaturePython] Dimension181  # Draft dimension (typed FeaturePython)
  Dimline = (-1026.05,15850,3000)
  Direction = (0,0,0)
  Distance = 2830
  End = (-4.99643,13020,3000)
  Normal = (0,0,1)
  Start = (-4.99643,15850,3000)
FEATURE [App::FeaturePython] Dimension182  # Draft dimension (typed FeaturePython)
  Dimline = (-1026.05,13020,3000)
  Direction = (0,0,0)
  Distance = 300
  End = (-4.99643,12720,3000)
  Normal = (0,0,1)
  Start = (-4.99643,13020,3000)
FEATURE [App::FeaturePython] Dimension183  # Draft dimension (typed FeaturePython)
  Dimline = (-1026.05,12720,3000)
  Direction = (0,0,0)
  Distance = 570
  End = (-4.99643,12150,3000)
  Normal = (0,0,1)
  Start = (-4.99643,12720,3000)
FEATURE [App::FeaturePython] Dimension184  # Draft dimension (typed FeaturePython)
  Dimline = (-1026.05,12150,3000)
  Direction = (0,0,0)
  Distance = 1358.58
  End = (-4.99643,10791.4,3000)
  Normal = (0,0,1)
  Start = (-4.99643,12150,3000)
FEATURE [App::FeaturePython] Dimension185  # Draft dimension (typed FeaturePython)
  Dimline = (-1026.05,10791.4,3000)
  Direction = (0,0,0)
  Distance = 500
  End = (-4.99643,10291.4,3000)
  Normal = (0,0,1)
  Start = (-4.99643,10791.4,3000)
FEATURE [App::FeaturePython] Dimension186  # Draft dimension (typed FeaturePython)
  Dimline = (-1026.05,10291.4,3000)
  Direction = (0,0,0)
  Distance = 1241.42
  End = (-4.99643,9050,3000)
  Normal = (0,0,1)
  Start = (-4.99643,10291.4,3000)
FEATURE [App::FeaturePython] Dimension187  # Draft dimension (typed FeaturePython)
  Dimline = (-1026.05,9050,3000)
  Direction = (0,0,0)
  Distance = 500
  End = (-4.99643,8550,3000)
  Normal = (0,0,1)
  Start = (-4.99643,9050,3000)
FEATURE [App::FeaturePython] Dimension188  # Draft dimension (typed FeaturePython)
  Dimline = (-1026.05,8550,3000)
  Direction = (0,0,0)
  Distance = 300
  End = (-4.99643,8250,3000)
  Normal = (0,0,1)
  Start = (-4.99643,8550,3000)
FEATURE [App::FeaturePython] Dimension189  # Draft dimension (typed FeaturePython)
  Dimline = (-1026.05,8250,3000)
  Direction = (0,0,0)
  Distance = 2200
  End = (-4.99643,6050,3000)
  Normal = (0,0,1)
  Start = (-4.99643,8250,3000)
FEATURE [App::FeaturePython] Dimension190  # Draft dimension (typed FeaturePython)
  Dimline = (-1026.05,6050,3000)
  Direction = (0,0,0)
  Distance = 300
  End = (-4.99643,5750,3000)
  Normal = (0,0,1)
  Start = (-4.99643,6050,3000)
FEATURE [App::FeaturePython] Dimension191  # Draft dimension (typed FeaturePython)
  Dimline = (-1026.05,5750,3000)
  Direction = (0,0,0)
  Distance = 500
  End = (-4.99643,5250,3000)
  Normal = (0,0,1)
  Start = (-4.99643,5750,3000)
FEATURE [App::FeaturePython] Dimension192  # Draft dimension (typed FeaturePython)
  Dimline = (-1026.05,5250,3000)
  Direction = (0,0,0)
  Distance = 3100
  End = (-4.99643,2150,3000)
  Normal = (0,0,1)
  Start = (-4.99643,5250,3000)
FEATURE [App::FeaturePython] Dimension193  # Draft dimension (typed FeaturePython)
  Dimline = (-1026.05,2150,3000)
  Direction = (0,0,0)
  Distance = 300
  End = (-4.99643,1850,3000)
  Normal = (0,0,1)
  Start = (-4.99643,2150,3000)
FEATURE [App::FeaturePython] Dimension194  # Draft dimension (typed FeaturePython)
  Dimline = (10171,445.385,3000)
  Direction = (0,0,0)
  Distance = 11000
  End = (10995,1850,3000)
  Normal = (0,0,1)
  Start = (-4.99643,1850,3000)
FEATURE [App::FeaturePython] Dimension195  # Draft dimension (typed FeaturePython)
  Dimline = (10171,679.104,3000)
  Direction = (0,0,0)
  Distance = 5950
  End = (5945,1850,3000)
  Normal = (0,0,1)
  Start = (-4.99643,1850,3000)
FEATURE [App::FeaturePython] Dimension196  # Draft dimension (typed FeaturePython)
  Dimline = (10171,679.104,3000)
  Direction = (0,0,0)
  Distance = 5050
  End = (10995,1850,3000)
  Normal = (0,0,1)
  Start = (5945,1850,3000)
FEATURE [App::FeaturePython] Dimension197  # Draft dimension (typed FeaturePython)
  Dimline = (10171,877.17,3000)
  Direction = (0,0,0)
  Distance = 150
  End = (145.004,1850,3000)
  Normal = (0,0,1)
  Start = (-4.99643,1850,3000)
FEATURE [App::FeaturePython] Dimension198  # Draft dimension (typed FeaturePython)
  Dimline = (10171,877.17,3000)
  Direction = (0,0,0)
  Distance = 896.979
  End = (1041.98,2000,3000)
  Normal = (0,0,1)
  Start = (145.004,2000,3000)
FEATURE [App::FeaturePython] Dimension199  # Draft dimension (typed FeaturePython)
  Dimline = (10171,877.17,3000)
  Direction = (0,0,0)
  Distance = 1000
  End = (2041.98,2000,3000)
  Normal = (0,0,1)
  Start = (1041.98,2000,3000)
FEATURE [App::FeaturePython] Dimension200  # Draft dimension (typed FeaturePython)
  Dimline = (10171,877.17,3000)
  Direction = (0,0,0)
  Distance = 1053.02
  End = (3095,2000,3000)
  Normal = (0,0,1)
  Start = (2041.98,2000,3000)
FEATURE [App::FeaturePython] Dimension201  # Draft dimension (typed FeaturePython)
  Dimline = (10171,877.17,3000)
  Direction = (0,0,0)
  Distance = 150
  End = (3245,1850,3000)
  Normal = (0,0,1)
  Start = (3095,1850,3000)
FEATURE [App::FeaturePython] Dimension202  # Draft dimension (typed FeaturePython)
  Dimline = (3245,877.17,3000)
  Direction = (0,0,0)
  Distance = 775
  End = (4020,2000,3000)
  Normal = (0,0,1)
  Start = (3245,2000,3000)
FEATURE [App::FeaturePython] Dimension203  # Draft dimension (typed FeaturePython)
  Dimline = (4020,877.17,3000)
  Direction = (0,0,0)
  Distance = 1000
  End = (5020,2000,3000)
  Normal = (0,0,1)
  Start = (4020,2000,3000)
FEATURE [App::FeaturePython] Dimension204  # Draft dimension (typed FeaturePython)
  Dimline = (5020,877.17,3000)
  Direction = (0,0,0)
  Distance = 775
  End = (5795,2000,3000)
  Normal = (0,0,1)
  Start = (5020,2000,3000)
FEATURE [App::FeaturePython] Dimension205  # Draft dimension (typed FeaturePython)
  Dimline = (5795,877.17,3000)
  Direction = (0,0,0)
  Distance = 150
  End = (5945,1850,3000)
  Normal = (0,0,1)
  Start = (5795,1850,3000)
FEATURE [App::FeaturePython] Dimension206  # Draft dimension (typed FeaturePython)
  Dimline = (5945,877.17,3000)
  Direction = (0,0,0)
  Distance = 4900
  End = (10845,1850,3000)
  Normal = (0,0,1)
  Start = (5945,1850,3000)
FEATURE [App::FeaturePython] Dimension207  # Draft dimension (typed FeaturePython)
  Dimline = (10845,877.17,3000)
  Direction = (0,0,0)
  Distance = 150
  End = (10995,1850,3000)
  Normal = (0,0,1)
  Start = (10845,1850,3000)
FEATURE [App::FeaturePython] Dimension208  # Draft dimension (typed FeaturePython)
  Dimline = (4219,15524.4,3000)
  Direction = (0,0,0)
  Distance = 500
  End = (4445,15850,3000)
  Normal = (0,0,1)
  Start = (4445,15350,3000)
FEATURE [App::FeaturePython] Dimension209  # Draft dimension (typed FeaturePython)
  Dimline = (7895,13906.4,3000)
  Direction = (0,0,0)
  Distance = 599.997
  End = (7895,13650,3000)
  Normal = (0,0,1)
  Start = (7295.01,13650,3000)
FEATURE [App::FeaturePython] Dimension210  # Draft dimension (typed FeaturePython)
  Dimline = (7854,8600.39,3000)
  Direction = (0,0,0)
  Distance = 600
  End = (7895,8400,3000)
  Normal = (0,0,1)
  Start = (7295,8400,3000)
FEATURE [App::FeaturePython] Dimension211  # Draft dimension (typed FeaturePython)
  Dimline = (2807,11696.4,3000)
  Direction = (0,0,0)
  Distance = 600
  End = (3020,12000,3000)
  Normal = (0,0,1)
  Start = (3020,11400,3000)
FEATURE [App::FeaturePython] Dimension212  # Draft dimension (typed FeaturePython)
  Dimline = (3772,15043.4,3000)
  Direction = (0,0,0)
  Distance = 4300
  End = (4445,15350,3000)
  Normal = (0,0,1)
  Start = (145.004,15350,3000)
FEATURE [App::FeaturePython] Dimension213  # Draft dimension (typed FeaturePython)
  Dimline = (4445,15043.4,3000)
  Direction = (0,0,0)
  Distance = 150
  End = (4595,15350,3000)
  Normal = (0,0,1)
  Start = (4445,15350,3000)
FEATURE [App::FeaturePython] Dimension214  # Draft dimension (typed FeaturePython)
  Dimline = (4595,15043.4,3000)
  Direction = (0,0,0)
  Distance = 2550
  End = (7145,15350,3000)
  Normal = (0,0,1)
  Start = (4595,15350,3000)
FEATURE [App::FeaturePython] Dimension215  # Draft dimension (typed FeaturePython)
  Dimline = (8116,13573.4,3000)
  Direction = (0,0,0)
  Distance = 150
  End = (7895,13650,3000)
  Normal = (0,0,1)
  Start = (7895,13500,3000)
FEATURE [App::FeaturePython] Dimension216  # Draft dimension (typed FeaturePython)
  Dimline = (8142,8341.39,3000)
  Direction = (0,0,0)
  Distance = 150
  End = (7895,8400,3000)
  Normal = (0,0,1)
  Start = (7895,8250,3000)
FEATURE [App::FeaturePython] Dimension217  # Draft dimension (typed FeaturePython)
  Dimline = (7145,15043.4,3000)
  Direction = (0,0,0)
  Distance = 150
  End = (7295,15043.4,3000)
  Normal = (0,0,1)
  Start = (7145,15043.4,3000)
FEATURE [App::FeaturePython] Dimension218  # Draft dimension (typed FeaturePython)
  Dimline = (7295,15043.4,3000)
  Direction = (0,0,0)
  Distance = 3550
  End = (10845,15043.4,3000)
  Normal = (0,0,1)
  Start = (7295,15043.4,3000)
FEATURE [App::FeaturePython] Dimension219  # Draft dimension (typed FeaturePython)
  Dimline = (8791,15350.4,3000)
  Direction = (0,0,0)
  Distance = 4000
  End = (9070,15850,3000)
  Normal = (0,0,1)
  Start = (9070,11850,3000)
FEATURE [App::FeaturePython] Dimension220  # Draft dimension (typed FeaturePython)
  Dimline = (8791,11850,3000)
  Direction = (0,0,0)
  Distance = 150
  End = (9070,11850,3000)
  Normal = (0,0,1)
  Start = (9070,11700,3000)
FEATURE [App::FeaturePython] Dimension221  # Draft dimension (typed FeaturePython)
  Dimline = (8791,11850,3000)
  Direction = (0,0,0)
  Distance = 1500
  End = (9070,11700,3000)
  Normal = (0,0,1)
  Start = (9070,10200,3000)
FEATURE [App::FeaturePython] Dimension222  # Draft dimension (typed FeaturePython)
  Dimline = (8791,10200,3000)
  Direction = (0,0,0)
  Distance = 150
  End = (9070,10200,3000)
  Normal = (0,0,1)
  Start = (9070,10050,3000)
FEATURE [App::FeaturePython] Dimension223  # Draft dimension (typed FeaturePython)
  Dimline = (8791,10200,3000)
  Direction = (0,0,0)
  Distance = 4000
  End = (8945,10050,3000)
  Normal = (0,0,1)
  Start = (8945,6050,3000)
FEATURE [App::FeaturePython] Dimension224  # Draft dimension (typed FeaturePython)
  Dimline = (8791,6050,3000)
  Direction = (0,0,0)
  Distance = 150
  End = (8945,6050,3000)
  Normal = (0,0,1)
  Start = (8945,5900,3000)
FEATURE [App::FeaturePython] Dimension225  # Draft dimension (typed FeaturePython)
  Dimline = (8791,5900,3000)
  Direction = (0,0,0)
  Distance = 3900
  End = (8395,5900,3000)
  Normal = (0,0,1)
  Start = (8395,2000,3000)
FEATURE [App::FeaturePython] Dimension226  # Draft dimension (typed FeaturePython)
  Dimline = (6562,7626.39,3000)
  Direction = (0,0,0)
  Distance = 2550
  End = (7145,7700,3000)
  Normal = (0,0,1)
  Start = (4595,7700,3000)
FEATURE [App::FeaturePython] Dimension227  # Draft dimension (typed FeaturePython)
  Dimline = (5795,13313.4,3000)
  Direction = (0,0,0)
  Distance = 1200
  End = (7145,8400,3000)
  Normal = (0,0,1)
  Start = (5945,8400,3000)
FEATURE [App::FeaturePython] Dimension230  # Draft dimension (typed FeaturePython)
  Dimline = (1487,15520.4,3000)
  Direction = (0,0,0)
  Distance = 3700
  End = (1745,15850,3000)
  Normal = (0,0,1)
  Start = (1745,12150,3000)
FEATURE [App::FeaturePython] Dimension231  # Draft dimension (typed FeaturePython)
  Dimline = (1487,12150,3000)
  Direction = (0,0,0)
  Distance = 150
  End = (1745,12150,3000)
  Normal = (0,0,1)
  Start = (1745,12000,3000)
FEATURE [App::FeaturePython] Dimension232  # Draft dimension (typed FeaturePython)
  Dimline = (1487,12150,3000)
  Direction = (0,0,0)
  Distance = 2250
  End = (2295,12000,3000)
  Normal = (0,0,1)
  Start = (2295,9750,3000)
FEATURE [App::FeaturePython] Dimension233  # Draft dimension (typed FeaturePython)
  Dimline = (1487,9750,3000)
  Direction = (0,0,0)
  Distance = 150
  End = (2295,9750,3000)
  Normal = (0,0,1)
  Start = (2295,9600,3000)
FEATURE [App::FeaturePython] Dimension234  # Draft dimension (typed FeaturePython)
  Dimline = (1487,9750,3000)
  Direction = (0,0,0)
  Distance = 2200
  End = (2845,9600,3000)
  Normal = (0,0,1)
  Start = (2845,7400,3000)
FEATURE [App::FeaturePython] Dimension235  # Draft dimension (typed FeaturePython)
  Dimline = (5322,8000.39,3000)
  Direction = (0,0,0)
  Distance = 2200
  End = (5195,8250,3000)
  Normal = (0,0,1)
  Start = (5195,6050,3000)
FEATURE [App::FeaturePython] Dimension236  # Draft dimension (typed FeaturePython)
  Dimline = (1487,7400,3000)
  Direction = (0,0,0)
  Distance = 150
  End = (2845,7400,3000)
  Normal = (0,0,1)
  Start = (2845,7250,3000)
FEATURE [App::FeaturePython] Dimension237  # Draft dimension (typed FeaturePython)
  Dimline = (1487,7400,3000)
  Direction = (0,0,0)
  Distance = 5100
  End = (2568.49,7250,3000)
  Normal = (0,0,1)
  Start = (2568.49,2150,3000)
FEATURE [App::FeaturePython] Dimension238  # Draft dimension (typed FeaturePython)
  Dimline = (5322,6050,3000)
  Direction = (0,0,0)
  Distance = 3750
  End = (5407.5,5900,3000)
  Normal = (0,0,1)
  Start = (5407.5,2150,3000)
FEATURE [App::FeaturePython] Dimension239  # Draft dimension (typed FeaturePython)
  Dimline = (5322,6050,3000)
  Direction = (0,0,0)
  Distance = 150
  End = (5795,6050,3000)
  Normal = (0,0,1)
  Start = (5795,5900,3000)
FEATURE [App::FeaturePython] Dimension240  # Draft dimension (typed FeaturePython)
  Dimline = (3747,6606.39,3000)
  Direction = (0,0,0)
  Distance = 1350
  End = (4445,7250,3000)
  Normal = (0,0,1)
  Start = (4445,5900,3000)
FEATURE [App::FeaturePython] Dimension241  # Draft dimension (typed FeaturePython)
  Dimline = (4970,5300,3000)
  Direction = (0,0,0)
  Distance = 1350
  End = (5795,5900,3000)
  Normal = (0,0,1)
  Start = (4445,5900,3000)
FEATURE [App::FeaturePython] Dimension242  # Draft dimension (typed FeaturePython)
  Dimline = (5667,4993.39,3000)
  Direction = (0,0,0)
  Distance = 5650
  End = (5795,3700,3000)
  Normal = (0,0,1)
  Start = (145.004,3700,3000)
FEATURE [App::FeaturePython] Dimension243  # Draft dimension (typed FeaturePython)
  Dimline = (4020,10503.4,3000)
  Direction = (0,0,0)
  Distance = 4300
  End = (4445,10291.4,3000)
  Normal = (0,0,1)
  Start = (145.004,10291.4,3000)
FEATURE [App::FeaturePython] Dimension244  # Draft dimension (typed FeaturePython)
  Dimline = (5664,13313.4,3000)
  Direction = (0,0,0)
  Distance = 1200
  End = (5795,13020,3000)
  Normal = (0,0,1)
  Start = (4595,13020,3000)
FEATURE [App::FeaturePython] Dimension245  # Draft dimension (typed FeaturePython)
  Dimline = (5795,13313.4,3000)
  Direction = (0,0,0)
  Distance = 150
  End = (5945,13020,3000)
  Normal = (0,0,1)
  Start = (5795,13020,3000)
FEATURE [App::FeaturePython] Dimension246  # Draft dimension (typed FeaturePython)
  Dimline = (4595,13313.4,3000)
  Direction = (0,0,0)
  Distance = 150
  End = (4595,13020,3000)
  Normal = (0,0,1)
  Start = (4445,13020,3000)
FEATURE [App::FeaturePython] Dimension247  # Draft dimension (typed FeaturePython)
  Dimline = (3095,11191.4,3000)
  Direction = (0,0,0)
  Distance = 150
  End = (3170,11400,3000)
  Normal = (0,0,1)
  Start = (3020,11400,3000)
FEATURE [App::FeaturePython] Dimension248  # Draft dimension (typed FeaturePython)
  Dimline = (5795,4993.39,3000)
  Direction = (0,0,0)
  Distance = 5050
  End = (10995,3950,3000)
  Normal = (0,0,1)
  Start = (5945,3950,3000)
FEATURE [App::FeaturePython] Dimension249  # Draft dimension (typed FeaturePython)
  Dimline = (8795,14406.4,0)
  Direction = (0,0,0)
  Distance = 5550.34
  End = (8795,14406.4,0)
  Normal = (0,0,1)
  Start = (3244.66,14406.4,0)
FEATURE [App::FeaturePython] Dimension250  # Draft dimension (typed FeaturePython)
  Dimline = (7512.62,14537.4,0)
  Direction = (0,0,0)
  Distance = 2830
  End = (6945,15850,0)
  Normal = (0,0,1)
  Start = (6945,13020,0)
FEATURE [App::FeaturePython] Dimension251  # Draft dimension (typed FeaturePython)
  Dimline = (7512.62,13020,0)
  Direction = (0,0,0)
  Distance = 150
  End = (6945,13020,0)
  Normal = (0,0,1)
  Start = (6945,12870,0)
FEATURE [App::FeaturePython] Dimension252  # Draft dimension (typed FeaturePython)
  Dimline = (7512.62,13020,0)
  Direction = (0,0,0)
  Distance = 8720.39
  End = (8395,12870,0)
  Normal = (0,0,1)
  Start = (8395,4149.61,0)
FEATURE [App::FeaturePython] Dimension253  # Draft dimension (typed FeaturePython)
  Dimline = (7512.62,4149.61,0)
  Direction = (0,0,0)
  Distance = 150
  End = (8395,4149.61,0)
  Normal = (0,0,1)
  Start = (8395,3999.61,0)
FEATURE [App::FeaturePython] Dimension254  # Draft dimension (typed FeaturePython)
  Dimline = (7512.62,4149.61,0)
  Direction = (0,0,0)
  Distance = 1999.61
  End = (8395,3999.61,0)
  Normal = (0,0,1)
  Start = (8395,2000,0)
FEATURE [App::FeaturePython] Dimension255  # Draft dimension (typed FeaturePython)
  Dimline = (3507.5,3999.61,0)
  Direction = (0,0,0)
  Distance = 1849.39
  End = (4019.62,3999.39,0)
  Normal = (0,0,1)
  Start = (4020,2150,0)
FEATURE [App::FeaturePython] Dimension256  # Draft dimension (typed FeaturePython)
  Dimline = (3507.5,4149.61,0)
  Direction = (0,0,0)
  Distance = 150
  End = (3770,4149.61,0)
  Normal = (0,0,1)
  Start = (3770,3999.61,0)
FEATURE [App::FeaturePython] Dimension257  # Draft dimension (typed FeaturePython)
  Dimline = (3507.5,4149.61,0)
  Direction = (0,0,0)
  Distance = 1900.39
  End = (5795,6050,0)
  Normal = (0,0,1)
  Start = (5795,4149.61,0)
FEATURE [App::FeaturePython] Dimension258  # Draft dimension (typed FeaturePython)
  Dimline = (3507.5,6050,0)
  Direction = (0,0,0)
  Distance = 2200
  End = (5795,8250,0)
  Normal = (0,0,1)
  Start = (5795,6050,0)
FEATURE [App::FeaturePython] Dimension259  # Draft dimension (typed FeaturePython)
  Dimline = (4205.62,9214.39,0)
  Direction = (0,0,0)
  Distance = 1200
  End = (4445,9450,0)
  Normal = (0,0,1)
  Start = (3245,9450,0)
FEATURE [App::FeaturePython] Dimension260  # Draft dimension (typed FeaturePython)
  Dimline = (2810.62,5014.39,0)
  Direction = (0,0,0)
  Distance = 599.965
  End = (3095,4650,0)
  Normal = (0,0,1)
  Start = (2495.03,4650,0)
FEATURE [App::FeaturePython] Dimension261  # Draft dimension (typed FeaturePython)
  Dimline = (2307.62,4504.39,0)
  Direction = (0,0,0)
  Distance = 150
  End = (2495.03,4650,0)
  Normal = (0,0,1)
  Start = (2495.03,4500,0)
FEATURE [App::FeaturePython] Dimension262  # Draft dimension (typed FeaturePython)
  Dimline = (3707.62,4303.39,0)
  Direction = (0,0,0)
  Distance = 575
  End = (3820,4149.61,0)
  Normal = (0,0,1)
  Start = (3245,4149.61,0)
FEATURE [App::FeaturePython] Dimension263  # Draft dimension (typed FeaturePython)
  Dimline = (3820,4303.39,0)
  Direction = (0,0,0)
  Distance = 1400
  End = (5220,4149.61,0)
  Normal = (0,0,1)
  Start = (3820,4149.61,0)
FEATURE [App::FeaturePython] Dimension264  # Draft dimension (typed FeaturePython)
  Dimline = (5220,4303.39,0)
  Direction = (0,0,0)
  Distance = 575
  End = (5795,4149.61,0)
  Normal = (0,0,1)
  Start = (5220,4149.61,0)
FEATURE [App::FeaturePython] Dimension265  # Draft dimension (typed FeaturePython)
  Dimline = (3507.5,8250,0)
  Direction = (0,0,0)
  Distance = 1350
  End = (4445,9600,0)
  Normal = (0,0,1)
  Start = (4445,8250,0)
FEATURE [App::DocumentObjectGroup] Group040  label="UNSORTED"
  Group = -> [Rectangle161,DWire200,Arc019,Line574,Arc022,Line605,Arc023,Line612,Line625,Arc024,Line532,Line533,Rectangle072,Line534,Line535,Rectangle073,Rectangle074,Rectangle075,Rectangle076,Line537,Line538,Rectangle077,Line539,Line540,Rectangle078,Rectangle079,Rectangle080,Rectangle081,Dimension033,Dimension034,Dimension035,Dimension036,Rectangle082,Line541,Line542,Line543,Rectangle083,Line544,Line545,+164 more]
FEATURE [Drawing::FeatureViewPython] ViewSpace  label="Veranda001"  # drawing view (typed FeaturePython)
  Direction = (0,0,0)
  FillStyle = 0
  FontSize = 1.5
  LineStyle = 2
  LineWidth = 0.35
  Rotation = 0
  Scale = 0.01
  Source = -> Space
  ViewResult = <g id="ViewSpace" transform="rotate(0.0,50.0,200.0) translate(50.0,200.0) scale(0.01,-0.01)"><text fill="#000000" font-size="150.0" style="text-anchor:end;text-align:right;font-family:Arial" transform="rotate(0.0,8573.1171875,3104.63598633) translate(8573.1171875,3104.63598633) scale(1,-1) " freecad:skip="1">\nVeranda</text>\n<text fill="#000000" font-size="75.0" style="text-anchor:end;text-align:right;font-family:Arial" transform="rotate(0.0,8573.1171875,2944.63598633) translate(8573.1171875,2944.63598633) scale(1,-1) " freecad:skip="1">\n10.08m²</text>\n</g>
  Visible = true
  X = 50
  Y = 200
FEATURE [Drawing::FeatureViewPython] ViewSpace002  label="Foyer001"  # drawing view (typed FeaturePython)
  Direction = (0,0,0)
  FillStyle = 0
  FontSize = 1.5
  LineStyle = 2
  LineWidth = 0.35
  Rotation = 0
  Scale = 0.01
  Source = -> Space002
  ViewResult = <g id="ViewSpace002" transform="rotate(0.0,50.0,200.0) translate(50.0,200.0) scale(0.01,-0.01)"><text fill="#000000" font-size="150.0" style="text-anchor:end;text-align:right;font-family:Arial" transform="rotate(0.0,4519.99902344,3234.80566406) translate(4519.99902344,3234.80566406) scale(1,-1) " freecad:skip="1">\nFoyer</text>\n<text fill="#000000" font-size="75.0" style="text-anchor:end;text-align:right;font-family:Arial" transform="rotate(0.0,4519.99902344,3074.80566406) translate(4519.99902344,3074.80566406) scale(1,-1) " freecad:skip="1">\n4.72m²</text>\n</g>
  Visible = true
  X = 50
  Y = 200
FEATURE [Drawing::FeatureViewPython] ViewSpace003  label="Guest bedroom"  # drawing view (typed FeaturePython)
  Direction = (0,0,0)
  FillStyle = 0
  FontSize = 1.5
  LineStyle = 2
  LineWidth = 0.35
  Rotation = 0
  Scale = 0.01
  Source = -> Space003
  ViewResult = <g id="ViewSpace003" transform="rotate(0.0,50.0,200.0) translate(50.0,200.0) scale(0.01,-0.01)"><text fill="#000000" font-size="150.0" style="text-anchor:end;text-align:right;font-family:Arial" transform="rotate(0.0,2059.51318359,3712.99902344) translate(2059.51318359,3712.99902344) scale(1,-1) " freecad:skip="1">\nGuest Bedroom</text>\n<text fill="#000000" font-size="75.0" style="text-anchor:end;text-align:right;font-family:Arial" transform="rotate(0.0,2059.51318359,3552.99902344) translate(2059.51318359,3552.99902344) scale(1,-1) " freecad:skip="1">\n12.74m²</text>\n</g>
  Visible = true
  X = 50
  Y = 200
FEATURE [Drawing::FeatureViewPython] ViewSpace004  label="buest bathroom"  # drawing view (typed FeaturePython)
  Direction = (0,0,0)
  FillStyle = 0
  FontSize = 1.5
  LineStyle = 2
  LineWidth = 0.35
  Rotation = 0
  Scale = 0.01
  Source = -> Space004
  ViewResult = <g id="ViewSpace004" transform="rotate(0.0,50.0,200.0) translate(50.0,200.0) scale(0.01,-0.01)"><text fill="#000000" font-size="150.0" style="text-anchor:end;text-align:right;font-family:Arial" transform="rotate(0.0,2032.56665039,7666.62695312) translate(2032.56665039,7666.62695312) scale(1,-1) " freecad:skip="1">\nGuest bathroom</text>\n<text fill="#000000" font-size="75.0" style="text-anchor:end;text-align:right;font-family:Arial" transform="rotate(0.0,2032.56665039,7506.62695312) translate(2032.56665039,7506.62695312) scale(1,-1) " freecad:skip="1">\n4.72m²</text>\n</g>
  Visible = true
  X = 50
  Y = 200
FEATURE [Drawing::FeatureViewPython] ViewSpace005  label="Toilet001"  # drawing view (typed FeaturePython)
  Direction = (0,0,0)
  FillStyle = 0
  FontSize = 1.5
  LineStyle = 2
  LineWidth = 0.35
  Rotation = 0
  Scale = 0.01
  Source = -> Space005
  ViewResult = <g id="ViewSpace005" transform="rotate(0.0,50.0,200.0) translate(50.0,200.0) scale(0.01,-0.01)"><text fill="#000000" font-size="150.0" style="text-anchor:end;text-align:right;font-family:Arial" transform="rotate(0.0,1619.99902344,9160.0) translate(1619.99902344,9160.0) scale(1,-1) " freecad:skip="1">\nToilet</text>\n<text fill="#000000" font-size="75.0" style="text-anchor:end;text-align:right;font-family:Arial" transform="rotate(0.0,1619.99902344,9000.0) translate(1619.99902344,9000.0) scale(1,-1) " freecad:skip="1">\n3.54m²</text>\n</g>
  Visible = true
  X = 50
  Y = 200
FEATURE [Drawing::FeatureViewPython] ViewSpace006  label="Laundery001"  # drawing view (typed FeaturePython)
  Direction = (0,0,0)
  FillStyle = 0
  FontSize = 1.5
  LineStyle = 2
  LineWidth = 0.35
  Rotation = 0
  Scale = 0.01
  Source = -> Space006
  ViewResult = <g id="ViewSpace006" transform="rotate(0.0,50.0,200.0) translate(50.0,200.0) scale(0.01,-0.01)"><text fill="#000000" font-size="150.0" style="text-anchor:end;text-align:right;font-family:Arial" transform="rotate(0.0,2294.99902344,11470.0) translate(2294.99902344,11470.0) scale(1,-1) " freecad:skip="1">\nLaundery</text>\n<text fill="#000000" font-size="75.0" style="text-anchor:end;text-align:right;font-family:Arial" transform="rotate(0.0,2294.99902344,11310.0) translate(2294.99902344,11310.0) scale(1,-1) " freecad:skip="1">\n13.42m²</text>\n</g>
  Visible = true
  X = 50
  Y = 200
FEATURE [Drawing::FeatureViewPython] ViewSpace007  label="Rear veranda"  # drawing view (typed FeaturePython)
  Direction = (0,0,0)
  FillStyle = 0
  FontSize = 1.5
  LineStyle = 2
  LineWidth = 0.35
  Rotation = 0
  Scale = 0.01
  Source = -> Space007
  ViewResult = <g id="ViewSpace007" transform="rotate(0.0,50.0,200.0) translate(50.0,200.0) scale(0.01,-0.01)"><text fill="#000000" font-size="150.0" style="text-anchor:end;text-align:right;font-family:Arial" transform="rotate(0.0,2120.0,14184.0) translate(2120.0,14184.0) scale(1,-1) " freecad:skip="1">\nRear Veranda</text>\n<text fill="#000000" font-size="75.0" style="text-anchor:end;text-align:right;font-family:Arial" transform="rotate(0.0,2120.0,14024.0) translate(2120.0,14024.0) scale(1,-1) " freecad:skip="1">\n9.22m²</text>\n</g>
  Visible = true
  X = 50
  Y = 200
FEATURE [Drawing::FeatureViewPython] ViewSpace008  label="Kitchen001"  # drawing view (typed FeaturePython)
  Direction = (0,0,0)
  FillStyle = 0
  FontSize = 1.5
  LineStyle = 2
  LineWidth = 0.35
  Rotation = 0
  Scale = 0.01
  Source = -> Space008
  ViewResult = <g id="ViewSpace008" transform="rotate(0.0,50.0,200.0) translate(50.0,200.0) scale(0.01,-0.01)"><text fill="#000000" font-size="150.0" style="text-anchor:end;text-align:right;font-family:Arial" transform="rotate(0.0,6289.0,14103.0) translate(6289.0,14103.0) scale(1,-1) " freecad:skip="1">\nKitchen</text>\n<text fill="#000000" font-size="75.0" style="text-anchor:end;text-align:right;font-family:Arial" transform="rotate(0.0,6289.0,13943.0) translate(6289.0,13943.0) scale(1,-1) " freecad:skip="1">\n15.71m²</text>\n</g>
  Visible = true
  X = 50
  Y = 200
FEATURE [Drawing::FeatureViewPython] ViewSpace009  label="Storage001"  # drawing view (typed FeaturePython)
  Direction = (0,0,0)
  FillStyle = 0
  FontSize = 1.5
  LineStyle = 2
  LineWidth = 0.35
  Rotation = 0
  Scale = 0.01
  Source = -> Space009
  ViewResult = <g id="ViewSpace009" transform="rotate(0.0,50.0,200.0) translate(50.0,200.0) scale(0.01,-0.01)"><text fill="#000000" font-size="150.0" style="text-anchor:end;text-align:right;font-family:Arial" transform="rotate(0.0,10212.0,14224.0) translate(10212.0,14224.0) scale(1,-1) " freecad:skip="1">\nStorage</text>\n<text fill="#000000" font-size="75.0" style="text-anchor:end;text-align:right;font-family:Arial" transform="rotate(0.0,10212.0,14064.0) translate(10212.0,14064.0) scale(1,-1) " freecad:skip="1">\n5.38m²</text>\n</g>
  Visible = true
  X = 50
  Y = 200
FEATURE [Drawing::FeatureViewPython] ViewSpace010  label="Corridor001"  # drawing view (typed FeaturePython)
  Direction = (0,0,0)
  FillStyle = 0
  FontSize = 1.5
  LineStyle = 2
  LineWidth = 0.35
  Rotation = 0
  Scale = 0.01
  Source = -> Space010
  ViewResult = <g id="ViewSpace010" transform="rotate(0.0,50.0,200.0) translate(50.0,200.0) scale(0.01,-0.01)"><text fill="#000000" font-size="150.0" style="text-anchor:end;text-align:right;font-family:Arial" transform="rotate(0.0,4924.0,6427.0) translate(4924.0,6427.0) scale(1,-1) " freecad:skip="1">\nCorridor</text>\n<text fill="#000000" font-size="75.0" style="text-anchor:end;text-align:right;font-family:Arial" transform="rotate(0.0,4924.0,6267.0) translate(4924.0,6267.0) scale(1,-1) " freecad:skip="1">\n12.08m²</text>\n</g>
  Visible = true
  X = 50
  Y = 200
FEATURE [App::DocumentObjectGroup] Group041  label="Space Annotation Level 1"
  Group = -> [ViewSpace,ViewSpace002,ViewSpace003,ViewSpace004,ViewSpace005,ViewSpace006,ViewSpace007,ViewSpace008,ViewSpace009,ViewSpace010]
FEATURE [Drawing::FeatureViewPython] ViewSpace011  label="Balcony001"  # drawing view (typed FeaturePython)
  Direction = (0,0,0)
  FillStyle = 0
  FontSize = 1.5
  LineStyle = 2
  LineWidth = 0.35
  Rotation = 0
  Scale = 0.01
  Source = -> Space011
  ViewResult = <g id="ViewSpace011" transform="rotate(0.0,220.0,200.0) translate(220.0,200.0) scale(0.01,-0.01)"><text fill="#000000" font-size="150.0" style="text-anchor:end;text-align:right;font-family:Arial" transform="rotate(0.0,9179.85351562,4114.45532227) translate(9179.85351562,4114.45532227) scale(1,-1) " freecad:skip="1">\nBalcony</text>\n<text fill="#000000" font-size="75.0" style="text-anchor:end;text-align:right;font-family:Arial" transform="rotate(0.0,9179.85351562,3954.45532227) translate(9179.85351562,3954.45532227) scale(1,-1) " freecad:skip="1">\n19.65m²</text>\n</g>
  Visible = true
  X = 220
  Y = 200
FEATURE [Drawing::FeatureViewPython] ViewSpace012  label="Master Bedroom001"  # drawing view (typed FeaturePython)
  Direction = (0,0,0)
  FillStyle = 0
  FontSize = 1.5
  LineStyle = 2
  LineWidth = 0.35
  Rotation = 0
  Scale = 0.01
  Source = -> Space012
  ViewResult = <g id="ViewSpace012" transform="rotate(0.0,220.0,200.0) translate(220.0,200.0) scale(0.01,-0.01)"><text fill="#000000" font-size="150.0" style="text-anchor:end;text-align:right;font-family:Arial" transform="rotate(0.0,2824.8347168,4733.40234375) translate(2824.8347168,4733.40234375) scale(1,-1) " freecad:skip="1">\nMaster Bedroom</text>\n<text fill="#000000" font-size="75.0" style="text-anchor:end;text-align:right;font-family:Arial" transform="rotate(0.0,2824.8347168,4573.40234375) translate(2824.8347168,4573.40234375) scale(1,-1) " freecad:skip="1">\n26.99m²</text>\n</g>
  Visible = true
  X = 220
  Y = 200
FEATURE [Drawing::FeatureViewPython] ViewSpace013  label="Master Bathroom001"  # drawing view (typed FeaturePython)
  Direction = (0,0,0)
  FillStyle = 0
  FontSize = 1.5
  LineStyle = 2
  LineWidth = 0.35
  Rotation = 0
  Scale = 0.01
  Source = -> Space013
  ViewResult = <g id="ViewSpace013" transform="rotate(0.0,220.0,200.0) translate(220.0,200.0) scale(0.01,-0.01)"><text fill="#000000" font-size="150.0" style="text-anchor:end;text-align:right;font-family:Arial" transform="rotate(0.0,2295.0,8660.0) translate(2295.0,8660.0) scale(1,-1) " freecad:skip="1">\nMaster Bathroom</text>\n<text fill="#000000" font-size="75.0" style="text-anchor:end;text-align:right;font-family:Arial" transform="rotate(0.0,2295.0,8500.0) translate(2295.0,8500.0) scale(1,-1) " freecad:skip="1">\n9.46m²</text>\n</g>
  Visible = true
  X = 220
  Y = 200
FEATURE [Drawing::FeatureViewPython] ViewSpace014  label="Study001"  # drawing view (typed FeaturePython)
  Direction = (0,0,0)
  FillStyle = 0
  FontSize = 1.5
  LineStyle = 2
  LineWidth = 0.35
  Rotation = 0
  Scale = 0.01
  Source = -> Space014
  ViewResult = <g id="ViewSpace014" transform="rotate(0.0,220.0,200.0) translate(220.0,200.0) scale(0.01,-0.01)"><text fill="#000000" font-size="150.0" style="text-anchor:end;text-align:right;font-family:Arial" transform="rotate(0.0,2287.48828125,11027.2539062) translate(2287.48828125,11027.2539062) scale(1,-1) " freecad:skip="1">\nStudy</text>\n<text fill="#000000" font-size="75.0" style="text-anchor:end;text-align:right;font-family:Arial" transform="rotate(0.0,2287.48828125,10867.2539062) translate(2287.48828125,10867.2539062) scale(1,-1) " freecad:skip="1">\n9.58m²</text>\n</g>
  Visible = true
  X = 220
  Y = 200
FEATURE [Drawing::FeatureViewPython] ViewSpace015  label="Small Living001"  # drawing view (typed FeaturePython)
  Direction = (0,0,0)
  FillStyle = 0
  FontSize = 1.5
  LineStyle = 2
  LineWidth = 0.35
  Rotation = 0
  Scale = 0.01
  Source = -> Space015
  ViewResult = <g id="ViewSpace015" transform="rotate(0.0,220.0,200.0) translate(220.0,200.0) scale(0.01,-0.01)"><text fill="#000000" font-size="150.0" style="text-anchor:end;text-align:right;font-family:Arial" transform="rotate(0.0,2295.0,14160.0) translate(2295.0,14160.0) scale(1,-1) " freecad:skip="1">\nSmall Living</text>\n<text fill="#000000" font-size="75.0" style="text-anchor:end;text-align:right;font-family:Arial" transform="rotate(0.0,2295.0,14000.0) translate(2295.0,14000.0) scale(1,-1) " freecad:skip="1">\n15.91m²</text>\n</g>
  Visible = true
  X = 220
  Y = 200
FEATURE [Drawing::FeatureViewPython] ViewSpace017  label="Bedroom 003"  # drawing view (typed FeaturePython)
  Direction = (0,0,0)
  FillStyle = 0
  FontSize = 1.5
  LineStyle = 2
  LineWidth = 0.35
  Rotation = 0
  Scale = 0.01
  Source = -> Space017
  ViewResult = <g id="ViewSpace017" transform="rotate(0.0,220.0,200.0) translate(220.0,200.0) scale(0.01,-0.01)"><text fill="#000000" font-size="150.0" style="text-anchor:end;text-align:right;font-family:Arial" transform="rotate(0.0,9079.40820312,8208.24609375) translate(9079.40820312,8208.24609375) scale(1,-1) " freecad:skip="1">\nBedroom 1</text>\n<text fill="#000000" font-size="75.0" style="text-anchor:end;text-align:right;font-family:Arial" transform="rotate(0.0,9079.40820312,8048.24609375) translate(9079.40820312,8048.24609375) scale(1,-1) " freecad:skip="1">\n14.11m²</text>\n</g>
  Visible = true
  X = 220
  Y = 200
FEATURE [Drawing::FeatureViewPython] ViewSpace018  label="Bedroom 004"  # drawing view (typed FeaturePython)
  Direction = (0,0,0)
  FillStyle = 0
  FontSize = 1.5
  LineStyle = 2
  LineWidth = 0.35
  Rotation = 0
  Scale = 0.01
  Source = -> Space018
  ViewResult = <g id="ViewSpace018" transform="rotate(0.0,220.0,200.0) translate(220.0,200.0) scale(0.01,-0.01)"><text fill="#000000" font-size="150.0" style="text-anchor:end;text-align:right;font-family:Arial" transform="rotate(0.0,9079.40917969,14011.7539062) translate(9079.40917969,14011.7539062) scale(1,-1) " freecad:skip="1">\nBedroom 2</text>\n<text fill="#000000" font-size="75.0" style="text-anchor:end;text-align:right;font-family:Arial" transform="rotate(0.0,9079.40917969,13851.7539062) translate(9079.40917969,13851.7539062) scale(1,-1) " freecad:skip="1">\n14.11m²</text>\n</g>
  Visible = true
  X = 220
  Y = 200
FEATURE [Drawing::FeatureViewPython] ViewSpace019  label="Bathroom001"  # drawing view (typed FeaturePython)
  Direction = (0,0,0)
  FillStyle = 0
  FontSize = 1.5
  LineStyle = 2
  LineWidth = 0.35
  Rotation = 0
  Scale = 0.01
  Source = -> Space019
  ViewResult = <g id="ViewSpace019" transform="rotate(0.0,220.0,200.0) translate(220.0,200.0) scale(0.01,-0.01)"><text fill="#000000" font-size="150.0" style="text-anchor:end;text-align:right;font-family:Arial" transform="rotate(0.0,9070.0,11110.0) translate(9070.0,11110.0) scale(1,-1) " freecad:skip="1">\nBathroom</text>\n<text fill="#000000" font-size="75.0" style="text-anchor:end;text-align:right;font-family:Arial" transform="rotate(0.0,9070.0,10950.0) translate(9070.0,10950.0) scale(1,-1) " freecad:skip="1">\n5.32m²</text>\n</g>
  Visible = true
  X = 220
  Y = 200
FEATURE [Drawing::FeatureViewPython] ViewSpace020  label="Stair Corridor001"  # drawing view (typed FeaturePython)
  Direction = (0,0,0)
  FillStyle = 0
  FontSize = 1.5
  LineStyle = 2
  LineWidth = 0.35
  Rotation = 0
  Scale = 0.01
  Source = -> Space020
  ViewResult = <g id="ViewSpace020" transform="rotate(0.0,220.0,200.0) translate(220.0,200.0) scale(0.01,-0.01)"><text fill="#000000" font-size="150.0" style="text-anchor:end;text-align:right;font-family:Arial" transform="rotate(0.0,6846.89160156,13382.7802734) translate(6846.89160156,13382.7802734) scale(1,-1) " freecad:skip="1">\nStair Corridor</text>\n<text fill="#000000" font-size="75.0" style="text-anchor:end;text-align:right;font-family:Arial" transform="rotate(0.0,6846.89160156,13222.7802734) translate(6846.89160156,13222.7802734) scale(1,-1) " freecad:skip="1">\n18.55m²</text>\n</g>
  Visible = true
  X = 220
  Y = 200
FEATURE [App::DocumentObjectGroup] Group042  label="Space Annotation Level 2"
  Group = -> [ViewSpace011,ViewSpace012,ViewSpace013,ViewSpace014,ViewSpace015,ViewSpace017,ViewSpace018,ViewSpace019,ViewSpace020]
FEATURE [Part::Part2DObjectPython] Arc025  # Draft 2D object (typed FeaturePython)
  FirstAngle = 90
  LastAngle = 179.975
  MakeFace = true
  Placement = pos=(5875,2205,0) rot=(0,0,1;0rad)
  Radius = 890
FEATURE [Part::Part2DObjectPython] Line672  # Draft 2D object (typed FeaturePython)
  ChamferSize = 0
  Closed = false
  FilletRadius = 0
  Length = 890
  MakeFace = true
  Placement = pos=(-25503.4,0.388761,0) rot=(0,0,1;0rad)
  Points = (2) [(31378.4,2204.61,0),(30488.4,2204.61,0)]
FEATURE [Part::Part2DObjectPython] Arc026  # Draft 2D object (typed FeaturePython)
  FirstAngle = 90
  LastAngle = 180
  MakeFace = true
  Placement = pos=(3145,4800,0) rot=(0,0,1;0rad)
  Radius = 900
FEATURE [Part::Part2DObjectPython] Line673  # Draft 2D object (typed FeaturePython)
  ChamferSize = 0
  Closed = false
  FilletRadius = 0
  Length = 900
  MakeFace = true
  Placement = pos=(-25503.4,0.388761,0) rot=(0,0,1;0rad)
  Points = (2) [(28648.4,4799.61,0),(27748.4,4799.61,0)]
FEATURE [Part::Part2DObjectPython] Arc027  # Draft 2D object (typed FeaturePython)
  FirstAngle = 90
  LastAngle = 179.974
  MakeFace = true
  Placement = pos=(10895,8600,0) rot=(0,0,1;0rad)
  Radius = 900
FEATURE [Part::Part2DObjectPython] Arc028  # Draft 2D object (typed FeaturePython)
  FirstAngle = 179.969
  LastAngle = 270
  MakeFace = true
  Placement = pos=(10895,10500,0) rot=(0,0,1;0rad)
  Radius = 900
FEATURE [Part::Part2DObjectPython] Line674  # Draft 2D object (typed FeaturePython)
  ChamferSize = 0
  Closed = false
  FilletRadius = 0
  Length = 900
  MakeFace = true
  Placement = pos=(-25503.4,2300.39,0) rot=(0,0,1;0rad)
  Points = (2) [(36398.4,8199.61,0),(35498.4,8199.61,0)]
FEATURE [Part::Part2DObjectPython] Line675  # Draft 2D object (typed FeaturePython)
  ChamferSize = 0
  Closed = false
  FilletRadius = 0
  Length = 895.383
  MakeFace = true
  Placement = pos=(-25503.4,2300.39,0) rot=(0,0,1;0rad)
  Points = (2) [(36398.4,6299.61,0),(35503,6299.61,0)]
FEATURE [Part::Part2DObjectPython] Arc029  # Draft 2D object (typed FeaturePython)
  FirstAngle = 90.0386
  LastAngle = 180
  MakeFace = true
  Placement = pos=(2945,6600,0) rot=(0,0,1;0rad)
  Radius = 800
FEATURE [Part::Part2DObjectPython] Line676  # Draft 2D object (typed FeaturePython)
  ChamferSize = 0
  Closed = false
  FilletRadius = 0
  Length = 800
  MakeFace = true
  Placement = pos=(-25503.4,0.388761,0) rot=(0,0,1;0rad)
  Points = (2) [(28448.4,6599.61,0),(28447.8,7399.61,0)]
FEATURE [Part::Part2DObjectPython] Arc030  # Draft 2D object (typed FeaturePython)
  FirstAngle = 179.966
  LastAngle = 270
  MakeFace = true
  Placement = pos=(3145,9450,0) rot=(0,0,1;0rad)
  Radius = 800
FEATURE [Part::Part2DObjectPython] Line677  # Draft 2D object (typed FeaturePython)
  ChamferSize = 0
  Closed = false
  FilletRadius = 0
  Length = 800
  MakeFace = true
  Placement = pos=(-25503.4,0.388761,0) rot=(0,0,1;0rad)
  Points = (2) [(28648.4,9449.61,0),(27848.4,9449.61,0)]
FEATURE [Part::Part2DObjectPython] Arc031  # Draft 2D object (typed FeaturePython)
  FirstAngle = 90.0341
  LastAngle = 180
  MakeFace = true
  Placement = pos=(4295,9700,0) rot=(0,0,1;0rad)
  Radius = 900
FEATURE [Part::Part2DObjectPython] Line678  # Draft 2D object (typed FeaturePython)
  ChamferSize = 0
  Closed = false
  FilletRadius = 0
  Length = 900
  MakeFace = true
  Placement = pos=(-25503.4,0.388761,0) rot=(0,0,1;0rad)
  Points = (2) [(29798.4,9699.61,0),(29798.4,10599.6,0)]
FEATURE [Part::Part2DObjectPython] Arc032  # Draft 2D object (typed FeaturePython)
  FirstAngle = 0
  LastAngle = 90
  MakeFace = true
  Placement = pos=(295,12970,0) rot=(0,0,1;0rad)
  Radius = 900
FEATURE [Part::Part2DObjectPython] Line679  # Draft 2D object (typed FeaturePython)
  ChamferSize = 0
  Closed = false
  FilletRadius = 0
  Length = 900
  MakeFace = true
  Placement = pos=(-25503.4,0.388761,0) rot=(0,0,1;0rad)
  Points = (2) [(25798.4,12969.6,0),(25798.4,13869.6,0)]
FEATURE [Part::Part2DObjectPython] Arc033  # Draft 2D object (typed FeaturePython)
  FirstAngle = 90.0216
  LastAngle = 179.972
  MakeFace = true
  Placement = pos=(3145,13170,0) rot=(0,0,1;0rad)
  Radius = 900
FEATURE [Part::Part2DObjectPython] Line680  # Draft 2D object (typed FeaturePython)
  ChamferSize = 0
  Closed = false
  FilletRadius = 0
  Length = 899.661
  MakeFace = true
  Placement = pos=(-25503.4,0.388761,0) rot=(0,0,1;0rad)
  Points = (2) [(28648,13169.6,0),(27748.4,13170.1,0)]
FEATURE [Part::Part2DObjectPython] Arc034  # Draft 2D object (typed FeaturePython)
  FirstAngle = 0.0343944
  LastAngle = 90
  MakeFace = true
  Placement = pos=(8895,13170,0) rot=(0,0,1;0rad)
  Radius = 800
FEATURE [Part::Part2DObjectPython] Line681  # Draft 2D object (typed FeaturePython)
  ChamferSize = 0
  Closed = false
  FilletRadius = 0
  Length = 800
  MakeFace = true
  Placement = pos=(-25503.4,0.388761,0) rot=(0,0,1;0rad)
  Points = (2) [(34398.4,13169.6,0),(35198.4,13170.1,0)]
FEATURE [Part::Part2DObjectPython] Arc035  # Draft 2D object (typed FeaturePython)
  FirstAngle = 0
  LastAngle = 90.0497
  MakeFace = true
  Placement = pos=(5995,12970,0) rot=(0,0,1;0rad)
  Radius = 900
FEATURE [Part::Part2DObjectPython] Line682  # Draft 2D object (typed FeaturePython)
  ChamferSize = 0
  Closed = false
  FilletRadius = 0
  Length = 900
  MakeFace = true
  Placement = pos=(-25503.4,0.388761,0) rot=(0,0,1;0rad)
  Points = (2) [(31498.4,13869.6,0),(31498.4,12969.6,0)]
FEATURE [Part::Part2DObjectPython] Arc036  # Draft 2D object (typed FeaturePython)
  FirstAngle = -90
  LastAngle = 0
  MakeFace = true
  Placement = pos=(6100,5950,3000) rot=(0,0,1;0rad)
  Radius = 890
FEATURE [Part::Part2DObjectPython] Line683  # Draft 2D object (typed FeaturePython)
  ChamferSize = 0
  Closed = false
  FilletRadius = 0
  Length = 890
  MakeFace = true
  Placement = pos=(-42142,0.38841,3000) rot=(0,0,1;0rad)
  Points = (2) [(48242,5949.61,0),(48242,5059.61,0)]
FEATURE [Part::Part2DObjectPython] Arc037  # Draft 2D object (typed FeaturePython)
  FirstAngle = 179.96
  LastAngle = 270
  MakeFace = true
  Placement = pos=(4495,7100,3000) rot=(0,0,1;0rad)
  Radius = 900
FEATURE [Part::Part2DObjectPython] Line684  # Draft 2D object (typed FeaturePython)
  ChamferSize = 0
  Closed = false
  FilletRadius = 0
  Length = 900
  MakeFace = true
  Placement = pos=(-42142,0.38841,3000) rot=(0,0,1;0rad)
  Points = (2) [(46637,7099.61,0),(45737,7099.61,0)]
FEATURE [Part::Part2DObjectPython] Arc038  # Draft 2D object (typed FeaturePython)
  FirstAngle = 0
  LastAngle = 90
  MakeFace = true
  Placement = pos=(295.004,7350,3000) rot=(0,0,1;0rad)
  Radius = 900
FEATURE [Part::Part2DObjectPython] Line685  # Draft 2D object (typed FeaturePython)
  ChamferSize = 0
  Closed = false
  FilletRadius = 0
  Length = 900
  MakeFace = true
  Placement = pos=(-42142,0.38841,3000) rot=(0,0,1;0rad)
  Points = (2) [(42437,8249.61,0),(42437,7349.61,0)]
FEATURE [Part::Part2DObjectPython] Arc039  # Draft 2D object (typed FeaturePython)
  FirstAngle = -90
  LastAngle = 0.036396
  MakeFace = true
  Placement = pos=(7245,9900,3000) rot=(0,0,1;0rad)
  Radius = 900
FEATURE [Part::Part2DObjectPython] Line686  # Draft 2D object (typed FeaturePython)
  ChamferSize = 0
  Closed = false
  FilletRadius = 0
  Length = 900
  MakeFace = true
  Placement = pos=(-42142,0.38841,3000) rot=(0,0,1;0rad)
  Points = (2) [(49387,9899.61,0),(50287,9899.61,0)]
FEATURE [Part::Part2DObjectPython] Arc040  # Draft 2D object (typed FeaturePython)
  FirstAngle = -180
  LastAngle = -90
  MakeFace = true
  Placement = pos=(4295,12050,3000) rot=(0,0,1;0rad)
  Radius = 900
FEATURE [Part::Part2DObjectPython] Line687  # Draft 2D object (typed FeaturePython)
  ChamferSize = 0
  Closed = false
  FilletRadius = 0
  Length = 900
  MakeFace = true
  Placement = pos=(-42142,0.38841,3000) rot=(0,0,1;0rad)
  Points = (2) [(46437,12049.6,0),(46437,11149.6,0)]
FEATURE [Part::Part2DObjectPython] Arc041  # Draft 2D object (typed FeaturePython)
  FirstAngle = 0.00913251
  LastAngle = 90
  MakeFace = true
  Placement = pos=(7245,10347.3,3000) rot=(0,0,1;0rad)
  Radius = 900
FEATURE [Part::Part2DObjectPython] Line688  # Draft 2D object (typed FeaturePython)
  ChamferSize = 0
  Closed = false
  FilletRadius = 0
  Length = 900
  MakeFace = true
  Placement = pos=(-42142,0.38841,3000) rot=(0,0,1;0rad)
  Points = (2) [(49387,10346.9,0),(50287,10347,0)]
FEATURE [Part::Part2DObjectPython] Arc042  # Draft 2D object (typed FeaturePython)
  FirstAngle = 0.0275554
  LastAngle = 90
  MakeFace = true
  Placement = pos=(7245,11994.9,3000) rot=(0,0,1;0rad)
  Radius = 900
FEATURE [Part::Part2DObjectPython] Line689  # Draft 2D object (typed FeaturePython)
  ChamferSize = 0
  Closed = false
  FilletRadius = 0
  Length = 899.986
  MakeFace = true
  Placement = pos=(-42142,-4.66432,3000) rot=(0,0,1;0rad)
  Points = (2) [(50287,11999.6,0),(49387,11999.6,0)]
FEATURE [App::DocumentObjectGroup] Group043  label="Level 1 door swings"
  Group = -> [Arc025,Line672,Arc026,Line673,Arc027,Arc028,Line674,Line675,Arc029,Line676,Arc030,Line677,Arc031,Line678,Arc032,Line679,Arc033,Line680,Arc034,Line681,Arc035,Line682]
FEATURE [App::DocumentObjectGroup] Group044  label="Level 2 door swings"
  Group = -> [Arc036,Line683,Arc037,Line684,Arc038,Line685,Arc039,Line686,Arc040,Line687,Arc041,Line688,Arc042,Line689]
FEATURE [App::DocumentObjectGroup] Group045  label="Door Swings"
  Group = -> [Group043,Group044]
FEATURE [Drawing::FeatureViewPython] ViewGroup043  label="Door Swings Level 1"  # drawing view (typed FeaturePython)
  Direction = (0,0,0)
  FillStyle = 0
  FontSize = 12
  LineStyle = 0
  LineWidth = 0.05
  Rotation = 0
  Scale = 0.01
  Source = -> Group043
  ViewResult = <g id="ViewGroup043" transform="rotate(0.0,50.0,200.0) translate(50.0,200.0) scale(0.01,-0.01)"></g>
  Visible = true
  X = 50
  Y = 200
FEATURE [Drawing::FeatureViewPython] ViewGroup044  label="Door Swings Level 2"  # drawing view (typed FeaturePython)
  Direction = (0,0,0)
  FillStyle = 0
  FontSize = 12
  LineStyle = 0
  LineWidth = 0.05
  Rotation = 0
  Scale = 0.01
  Source = -> Group044
  ViewResult = <g id="ViewGroup044" transform="rotate(0.0,220.0,200.0) translate(220.0,200.0) scale(0.01,-0.01)"></g>
  Visible = true
  X = 220
  Y = 200
FEATURE [App::DocumentObjectGroup] Group046  label="Door Swings001"
  Group = -> [ViewGroup044,ViewGroup043]
FEATURE [Part::Part2DObjectPython] Line692  # Draft 2D object (typed FeaturePython)
  ChamferSize = 0
  Closed = false
  End = (34298.4,14119.6,0)
  FilletRadius = 0
  Length = 5550.34
  MakeFace = true
  Points = (2) [(28748,14119.6,0),(34298.4,14119.6,0)]
  Start = (28748,14119.6,0)
FEATURE [Part::Part2DObjectPython] Line693  # Draft 2D object (typed FeaturePython)
  ChamferSize = 0
  Closed = false
  End = (28748,16842,0)
  FilletRadius = 0
  Length = 2722.39
  MakeFace = true
  Points = (2) [(28748,14119.6,0),(28748,16842,0)]
  Start = (28748,14119.6,0)
FEATURE [Part::Part2DObjectPython] Line694  # Draft 2D object (typed FeaturePython)
  ChamferSize = 0
  Closed = false
  End = (29348,16842,0)
  FilletRadius = 0
  Length = 2722.39
  MakeFace = true
  Points = (2) [(29348,14119.6,0),(29348,16842,0)]
  Start = (29348,14119.6,0)
FEATURE [Part::Part2DObjectPython] Line695  # Draft 2D object (typed FeaturePython)
  ChamferSize = 0
  Closed = false
  End = (33698.3,16842,0)
  FilletRadius = 0
  Length = 2722.39
  MakeFace = true
  Placement = pos=(4950.34,0,0) rot=(0,0,1;0rad)
  Points = (2) [(28748,14119.6,0),(28748,16842,0)]
  Start = (33698.4,14119.6,0)
FEATURE [Part::Part2DObjectPython] Line696  # Draft 2D object (typed FeaturePython)
  ChamferSize = 0
  Closed = false
  End = (34298.3,16842,0)
  FilletRadius = 0
  Length = 2722.39
  MakeFace = true
  Placement = pos=(4950.34,0,0) rot=(0,0,1;0rad)
  Points = (2) [(29348,14119.6,0),(29348,16842,0)]
  Start = (34298.4,14119.6,0)
FEATURE [Part::Part2DObjectPython] Line697  # Draft 2D object (typed FeaturePython)
  ChamferSize = 0
  Closed = false
  End = (27943,15850,0)
  FilletRadius = 0
  Length = 3355.38
  MakeFace = true
  Points = (2) [(31298.4,15849.6,0),(27943,15850,0)]
  Start = (31298.4,15849.6,0)
FEATURE [Part::Part2DObjectPython] Rectangle175  # Draft 2D object (typed FeaturePython)
  ChamferSize = 0
  FilletRadius = 30
  Height = 500
  Length = 800
  MakeFace = true
  Placement = pos=(31731.6,14504.2,0) rot=(0,0,1;0rad)
FEATURE [Part::Part2DObjectPython] Rectangle179  # Draft 2D object (typed FeaturePython)
  ChamferSize = 0
  FilletRadius = 30
  Height = 350
  Length = 350
  MakeFace = true
  Placement = pos=(32141.6,14544.2,0) rot=(0,0,1;0rad)
FEATURE [Part::Part2DObjectPython] Rectangle180  # Draft 2D object (typed FeaturePython)
  ChamferSize = 0
  FilletRadius = 30
  Height = 350
  Length = 350
  MakeFace = true
  Placement = pos=(31771.6,14544.2,0) rot=(0,0,1;0rad)
FEATURE [Part::Part2DObjectPython] Rectangle181  # Draft 2D object (typed FeaturePython)
  ChamferSize = 0
  FilletRadius = 30
  Height = 350
  Length = 350
  MakeFace = true
  Placement = pos=(32883.5,14352.9,0) rot=(0,0,1;0rad)
FEATURE [Part::Cut] Cut006
  Base = -> Rectangle175
  Tool = -> Rectangle180
FEATURE [Part::Cut] Cut007
  Base = -> Cut006
  Tool = -> Rectangle179
FEATURE [Part::Feature] Face018
  Placement = pos=(-1654.04,195.809,0) rot=(0,0,1;0rad)
  shape: bbox 290 x 2e-07 x 200 mm, 1 faces, 0 solids (baked)
FEATURE [Part::Feature] Face019
  Placement = pos=(-1654.04,195.809,0) rot=(0,0,1;0rad)
  shape: bbox 30 x 30 x 200 mm, 1 faces, 0 solids (baked)
FEATURE [Part::Feature] Face020
  Placement = pos=(-1654.04,195.809,0) rot=(0,0,1;0rad)
  shape: bbox 2e-07 x 290 x 200 mm, 1 faces, 0 solids (baked)
FEATURE [Part::Feature] Face021
  Placement = pos=(-1654.04,195.809,0) rot=(0,0,1;0rad)
  shape: bbox 30 x 30 x 200 mm, 1 faces, 0 solids (baked)
FEATURE [Part::Feature] Face022
  Placement = pos=(-1654.04,195.809,0) rot=(0,0,1;0rad)
  shape: bbox 290 x 2e-07 x 200 mm, 1 faces, 0 solids (baked)
FEATURE [Part::Feature] Face023
  Placement = pos=(-1654.04,195.809,0) rot=(0,0,1;0rad)
  shape: bbox 30 x 30 x 200 mm, 1 faces, 0 solids (baked)
FEATURE [Part::Feature] Face024
  Placement = pos=(-1654.04,195.809,0) rot=(0,0,1;0rad)
  shape: bbox 2e-07 x 290 x 200 mm, 1 faces, 0 solids (baked)
FEATURE [Part::Feature] Face025
  Placement = pos=(-1654.04,195.809,0) rot=(0,0,1;0rad)
  shape: bbox 30 x 30 x 200 mm, 1 faces, 0 solids (baked)
FEATURE [Part::Feature] Face027
  Placement = pos=(31229.5,14548.7,-200) rot=(0,0,1;0rad)
  shape: bbox 350 x 350 x 2e-07 mm, 1 faces, 0 solids (baked)
FEATURE [Part::MultiFuse] Fusion
  Shapes = -> [Face018,Face022,Face023,Face019,Face020,Face024,Face021,Face025,Face027]
FEATURE [Part::Feature] Fusion001
  Placement = pos=(542.107,-4.5127,0) rot=(0,0,1;0rad)
  shape: bbox 350 x 350 x 200 mm, 9 faces, 0 solids (baked)
FEATURE [Part::Feature] Fusion002
  Placement = pos=(912.107,-4.5127,0) rot=(0,0,1;0rad)
  shape: bbox 350 x 350 x 200 mm, 9 faces, 0 solids (baked)
FEATURE [Part::MultiFuse] Fusion003  label="Kitchen Sink"
  Placement = pos=(-25586.6,815.8,900) rot=(0,0,1;0rad)
  Shapes = -> [Cut007,Fusion001,Fusion002]
FEATURE [Part::Extrusion] Extrusion064
  Base = -> Rectangle181
  Dir = (0,0,-200)
  Solid = true
FEATURE [Part::Feature] Extrusion065
  Placement = pos=(-1740.64,224.054,0) rot=(0,0,1;0rad)
  shape: bbox 350 x 350 x 200 mm, 10 faces (baked)
FEATURE [Part::Feature] Face028
  Placement = pos=(-1634.62,26.7998,0) rot=(0,0,1;0rad)
  shape: bbox 800 x 500 x 2e-07 mm, 1 faces, 0 solids (baked)
FEATURE [Part::Feature] Face029
  Placement = pos=(-1634.62,26.7998,0) rot=(0,0,1;0rad)
  shape: bbox 2e-07 x 290 x 200 mm, 1 faces, 0 solids (baked)
FEATURE [Part::Feature] Face030
  Placement = pos=(-1634.62,26.7998,0) rot=(0,0,1;0rad)
  shape: bbox 30 x 30 x 200 mm, 1 faces, 0 solids (baked)
FEATURE [Part::Feature] Face031
  Placement = pos=(-1634.62,26.7998,0) rot=(0,0,1;0rad)
  shape: bbox 30 x 30 x 200 mm, 1 faces, 0 solids (baked)
FEATURE [Part::Feature] Face032
  Placement = pos=(-1634.62,26.7998,0) rot=(0,0,1;0rad)
  shape: bbox 290 x 2e-07 x 200 mm, 1 faces, 0 solids (baked)
FEATURE [Part::Feature] Face033
  Placement = pos=(-1634.62,26.7998,0) rot=(0,0,1;0rad)
  shape: bbox 290 x 2e-07 x 200 mm, 1 faces, 0 solids (baked)
FEATURE [Part::Feature] Face034
  Placement = pos=(-1634.62,26.7998,0) rot=(0,0,1;0rad)
  shape: bbox 30 x 30 x 200 mm, 1 faces, 0 solids (baked)
FEATURE [Part::Feature] Face035
  Placement = pos=(-1634.62,26.7998,0) rot=(0,0,1;0rad)
  shape: bbox 30 x 30 x 200 mm, 1 faces, 0 solids (baked)
FEATURE [Part::Feature] Face036
  Placement = pos=(-1634.62,26.7998,0) rot=(0,0,1;0rad)
  shape: bbox 2e-07 x 290 x 200 mm, 1 faces, 0 solids (baked)
FEATURE [Part::Feature] Face037
  Placement = pos=(-1634.62,26.7998,0) rot=(0,0,1;0rad)
  shape: bbox 30 x 30 x 200 mm, 1 faces, 0 solids (baked)
FEATURE [Part::Feature] Face038
  Placement = pos=(-1634.62,26.7998,0) rot=(0,0,1;0rad)
  shape: bbox 290 x 2e-07 x 200 mm, 1 faces, 0 solids (baked)
FEATURE [Part::Feature] Face039
  Placement = pos=(-1634.62,26.7998,0) rot=(0,0,1;0rad)
  shape: bbox 2e-07 x 290 x 200 mm, 1 faces, 0 solids (baked)
FEATURE [Part::Feature] Face040
  Placement = pos=(-1634.62,26.7998,0) rot=(0,0,1;0rad)
  shape: bbox 30 x 30 x 200 mm, 1 faces, 0 solids (baked)
FEATURE [Part::Feature] Face041
  Placement = pos=(-1634.62,26.7998,0) rot=(0,0,1;0rad)
  shape: bbox 30 x 30 x 200 mm, 1 faces, 0 solids (baked)
FEATURE [Part::Feature] Face042
  Placement = pos=(-1634.62,26.7998,0) rot=(0,0,1;0rad)
  shape: bbox 2e-07 x 290 x 200 mm, 1 faces, 0 solids (baked)
FEATURE [Part::Feature] Face043
  Placement = pos=(-1634.62,26.7998,0) rot=(0,0,1;0rad)
  shape: bbox 290 x 2e-07 x 200 mm, 1 faces, 0 solids (baked)
FEATURE [Part::Feature] Face044
  Placement = pos=(-1634.62,26.7998,0) rot=(0,0,1;0rad)
  shape: bbox 30 x 30 x 200 mm, 1 faces, 0 solids (baked)
FEATURE [Part::Feature] Face045
  Placement = pos=(-722.51,22.2871,0) rot=(0,0,1;0rad)
  shape: bbox 350 x 350 x 2e-07 mm, 1 faces, 0 solids (baked)
FEATURE [Part::Feature] Face046
  Placement = pos=(-1092.51,22.2871,0) rot=(0,0,1;0rad)
  shape: bbox 350 x 350 x 2e-07 mm, 1 faces, 0 solids (baked)
FEATURE [Part::MultiFuse] Fusion004
  Shapes = -> [Face029,Face030,Face033,Face031,Face032,Face034,Face036,Face035,Face045]
FEATURE [Part::MultiFuse] Fusion005
  Shapes = -> [Face037,Face038,Face039,Face042,Face040,Face041,Face044,Face043,Face046]
FEATURE [Part::Extrusion] Extrude
  Base = -> Face028
  Dir = (0,0,1)
  Solid = true
FEATURE [Part::Part2DObjectPython] Rectangle182  # Draft 2D object (typed FeaturePython)
  ChamferSize = 0
  FilletRadius = 0
  Height = 600
  Length = 5550.34
  MakeFace = true
  Placement = pos=(28748.4,15249.6,0) rot=(0,0,1;0rad)
FEATURE [Part::Part2DObjectPython] Rectangle183  # Draft 2D object (typed FeaturePython)
  ChamferSize = 0
  FilletRadius = 0
  Height = 520
  Length = 5550.34
  MakeFace = true
  Placement = pos=(28748.4,15329.6,0) rot=(0,0,1;0rad)
FEATURE [Part::Part2DObjectPython] Line712  # Draft 2D object (typed FeaturePython)
  ChamferSize = 0
  Closed = false
  End = (33778.3,16842,0)
  FilletRadius = 0
  Length = 80
  MakeFace = true
  Points = (2) [(33698.3,16842,0),(33778.3,16842,0)]
  Start = (33698.3,16842,0)
  Support = -> Rectangle183
FEATURE [Part::Part2DObjectPython] DWire215  # Draft 2D object (typed FeaturePython)
  ChamferSize = 0
  Closed = true
  End = (28748.4,15849.6,0)
  FilletRadius = 0
  Length = 16980.4
  MakeFace = true
  Points = (8) [(28748,14119.6,0),(29268,14119.6,0),(29268,15329.6,0),(33778.4,15329.7,0),(33778.4,14119.6,0),(34298.4,14119.6,0),(34298.4,15849.6,0),+1 more]
  Start = (28748,14119.6,0)
FEATURE [Part::Extrusion] Extrusion066  label="Cabinet concrete base"
  Base = -> DWire215
  Dir = (0,0,90)
  Placement = pos=(-25503.4,0.388761,0) rot=(0,0,1;0rad)
  Solid = true
FEATURE [Part::Part2DObjectPython] DWire216  # Draft 2D object (typed FeaturePython)
  ChamferSize = 0
  Closed = true
  End = (28748.4,15849.6,850)
  FilletRadius = 0
  Length = 16820.4
  MakeFace = true
  Placement = pos=(0,0,850) rot=(0,0,1;0rad)
  Points = (8) [(28748,14119.6,0),(29348,14119.6,0),(29348,15249.6,0),(33698.4,15249.7,0),(33698.4,14119.6,0),(34298.4,14119.6,0),(34298.4,15849.6,0),+1 more]
  Start = (28748,14119.6,850)
FEATURE [Part::Part2DObjectPython] Rectangle185  # Draft 2D object (typed FeaturePython)
  ChamferSize = 0
  FilletRadius = 30
  Height = 400
  Length = 760
  MakeFace = true
  Placement = pos=(31668.4,15339.6,850) rot=(0,0,1;0rad)
FEATURE [Part::Cut] Cut008
  Base = -> DWire216
  Tool = -> Rectangle185
FEATURE [Part::FeaturePython] Panel041  label="Kitchen Counter Top U-shape"  # WARN: FeaturePython — macro-defined, semantics opaque (R4)
  Base = -> Cut008
  Length = 0
  MoveWithHost = false
  Placement = pos=(-25503.4,0.388761,0) rot=(0,0,1;0rad)
  Role = 0
  Sheets = 1
  Thickness = 50
  Width = 0
FEATURE [Part::Feature] Cut009
  Placement = pos=(-83.2344,815.411,900) rot=(0,0,1;0rad)
  shape: bbox 800 x 500 x 2e-07 mm, 1 faces, 0 solids (baked)
FEATURE [Part::Extrusion] Extrusion067
  Base = -> Cut009
  Dir = (0,0,5)
  Placement = pos=(-25503.4,0.388761,0) rot=(0,0,1;0rad)
  Solid = true
FEATURE [Part::Part2DObjectPython] Rectangle188  # Draft 2D object (typed FeaturePython)
  ChamferSize = 0
  FilletRadius = 0
  Height = 740
  Length = 2329.99
  MakeFace = true
  Placement = pos=(31448.4,15849.6,850) rot=(-1,0,0;1.5708rad)
FEATURE [Part::FeaturePython] Panel042  label="Panel041"  # WARN: FeaturePython — macro-defined, semantics opaque (R4)
  Base = -> Rectangle188
  Length = 0
  MoveWithHost = false
  Placement = pos=(-25503.4,-19.6112,0) rot=(0,0,1;0rad)
  Role = 0
  Sheets = 1
  Thickness = 20
  Width = 0
FEATURE [Part::Part2DObjectPython] Rectangle191  # Draft 2D object (typed FeaturePython)
  ChamferSize = 0
  FilletRadius = 0
  Height = -740
  Length = -499.965
  MakeFace = true
  Placement = pos=(31448.4,15329.6,850) rot=(0.57735,-0.57735,-0.57735;2.0944rad)
FEATURE [Part::FeaturePython] Panel044  label="Panel043"  # WARN: FeaturePython — macro-defined, semantics opaque (R4)
  Base = -> Rectangle191
  Length = 0
  MoveWithHost = false
  Placement = pos=(-25493.4,0.388761,0) rot=(0,0,1;0rad)
  Role = 0
  Sheets = 1
  Thickness = 20
  Width = 0
FEATURE [Part::Part2DObjectPython] Rectangle192  # Draft 2D object (typed FeaturePython)
  ChamferSize = 0
  FilletRadius = 0
  Height = -740
  Length = -499.965
  MakeFace = true
  Placement = pos=(32648.4,15329.6,850) rot=(0.57735,-0.57735,-0.57735;2.0944rad)
FEATURE [Part::FeaturePython] Panel045  label="Panel044"  # WARN: FeaturePython — macro-defined, semantics opaque (R4)
  Base = -> Rectangle192
  Length = 0
  MoveWithHost = false
  Placement = pos=(-25493.4,0.388761,0) rot=(0,0,1;0rad)
  Role = 0
  Sheets = 1
  Thickness = 20
  Width = 0
FEATURE [Part::Part2DObjectPython] Rectangle197  # Draft 2D object (typed FeaturePython)
  ChamferSize = 0
  FilletRadius = 0
  Height = -20
  Length = 740
  MakeFace = true
  Placement = pos=(32038.4,15329.7,110) rot=(0.57735,-0.57735,0.57735;2.0944rad)
FEATURE [Part::FeaturePython] Panel049  label="Panel048"  # WARN: FeaturePython — macro-defined, semantics opaque (R4)
  Base = -> Rectangle197
  Length = 0
  MoveWithHost = false
  Placement = pos=(-25503.4,10.3888,0) rot=(0,0,1;0rad)
  Role = 0
  Sheets = 1
  Thickness = 10
  Width = 0
FEATURE [Part::Part2DObjectPython] DWire217  # Draft 2D object (typed FeaturePython)
  ChamferSize = 0
  Closed = true
  End = (31898.4,15729.6,905)
  FilletRadius = 0
  Length = 720
  MakeFace = true
  Points = (4) [(31898.4,15789.6,905),(32198.4,15789.6,905),(32198.4,15729.6,905),(31898.4,15729.6,905)]
  Start = (31898.4,15789.6,905)
FEATURE [Part::FeaturePython] Panel050  label="Panel049"  # WARN: FeaturePython — macro-defined, semantics opaque (R4)
  Base = -> DWire217
  Length = 0
  MoveWithHost = false
  Placement = pos=(-25503.4,0.388761,0) rot=(0,0,1;0rad)
  Role = 0
  Sheets = 1
  Thickness = 10
  Width = 0
FEATURE [Part::Feature] Wire  label="Tap Wire"
  shape: bbox 2e-07 x 200 x 150 mm, 0 faces, 0 solids (baked)
FEATURE [Part::Part2DObjectPython] Line726  # Draft 2D object (typed FeaturePython)
  ChamferSize = 0
  Closed = false
  End = (29268,15329.6,90)
  FilletRadius = 0
  Length = 810.657
  MakeFace = true
  Points = (2) [(28457.4,15329.6,90),(29268,15329.6,90)]
  Start = (28457.4,15329.6,90)
FEATURE [Part::Part2DObjectPython] Line727  # Draft 2D object (typed FeaturePython)
  ChamferSize = 0
  Closed = false
  End = (29268,14119.6,90)
  FilletRadius = 0
  Length = 810.657
  MakeFace = true
  Placement = pos=(0,-1209.99,0) rot=(0,0,1;0rad)
  Points = (2) [(28457.4,15329.6,90),(29268,15329.6,90)]
  Start = (28457.4,14119.6,90)
FEATURE [Part::Part2DObjectPython] Line729  # Draft 2D object (typed FeaturePython)
  ChamferSize = 0
  Closed = false
  End = (29268,15019.6,90)
  FilletRadius = 0
  Length = 810.657
  MakeFace = true
  Placement = pos=(0,450,0) rot=(0,0,1;0rad)
  Points = (2) [(28457.4,14569.6,90),(29268,14569.6,90)]
  Start = (28457.4,15019.6,90)
FEATURE [Part::Part2DObjectPython] Line730  # Draft 2D object (typed FeaturePython)
  ChamferSize = 0
  Closed = false
  End = (31448.4,16393,90)
  FilletRadius = 0
  Length = 1063.33
  MakeFace = true
  Points = (2) [(31448.4,15329.6,90),(31448.4,16393,90)]
  Start = (31448.4,15329.6,90)
FEATURE [Part::Part2DObjectPython] Line731  # Draft 2D object (typed FeaturePython)
  ChamferSize = 0
  Closed = false
  End = (30848.4,16393,90)
  FilletRadius = 0
  Length = 1063.33
  MakeFace = true
  Placement = pos=(-150,0,0) rot=(0,0,1;0rad)
  Points = (2) [(30998.4,15329.6,90),(30998.4,16393,90)]
  Start = (30848.4,15329.6,90)
FEATURE [Part::Part2DObjectPython] Line733  # Draft 2D object (typed FeaturePython)
  ChamferSize = 0
  Closed = false
  End = (30248.4,16393,90)
  FilletRadius = 0
  Length = 1063.33
  MakeFace = true
  Placement = pos=(-750,0,0) rot=(0,0,1;0rad)
  Points = (2) [(30998.4,15329.6,90),(30998.4,16393,90)]
  Start = (30248.4,15329.6,90)
FEATURE [Part::Part2DObjectPython] Line734  # Draft 2D object (typed FeaturePython)
  ChamferSize = 0
  Closed = false
  End = (29648.4,16393,90)
  FilletRadius = 0
  Length = 1063.33
  MakeFace = true
  Placement = pos=(-1350,0,0) rot=(0,0,1;0rad)
  Points = (2) [(30998.4,15329.6,90),(30998.4,16393,90)]
  Start = (29648.4,15329.6,90)
FEATURE [Part::Part2DObjectPython] Line735  # Draft 2D object (typed FeaturePython)
  ChamferSize = 0
  Closed = false
  End = (29198.4,16393,90)
  FilletRadius = 0
  Length = 1063.33
  MakeFace = true
  Placement = pos=(-1800,0,0) rot=(0,0,1;0rad)
  Points = (2) [(30998.4,15329.6,90),(30998.4,16393,90)]
  Start = (29198.4,15329.6,90)
FEATURE [Part::Part2DObjectPython] Line736  # Draft 2D object (typed FeaturePython)
  ChamferSize = 0
  Closed = false
  End = (33998.4,16393,90)
  FilletRadius = 0
  Length = 1063.33
  MakeFace = true
  Placement = pos=(2550,0.0194385,0) rot=(0,0,1;0rad)
  Points = (2) [(31448.4,15329.6,90),(31448.4,16393,90)]
  Start = (33998.4,15329.7,90)
FEATURE [Part::Part2DObjectPython] Line737  # Draft 2D object (typed FeaturePython)
  ChamferSize = 0
  Closed = false
  End = (33548.4,16393,90)
  FilletRadius = 0
  Length = 1063.33
  MakeFace = true
  Placement = pos=(2550,0.0194385,0) rot=(0,0,1;0rad)
  Points = (2) [(30998.4,15329.6,90),(30998.4,16393,90)]
  Start = (33548.4,15329.7,90)
FEATURE [Part::Part2DObjectPython] Line738  # Draft 2D object (typed FeaturePython)
  ChamferSize = 0
  Closed = false
  End = (33098.4,16393,90)
  FilletRadius = 0
  Length = 1063.33
  MakeFace = true
  Placement = pos=(2100,0.0194385,0) rot=(0,0,1;0rad)
  Points = (2) [(30998.4,15329.6,90),(30998.4,16393,90)]
  Start = (33098.4,15329.7,90)
FEATURE [Part::Part2DObjectPython] Line739  # Draft 2D object (typed FeaturePython)
  ChamferSize = 0
  Closed = false
  End = (32648.4,16393,90)
  FilletRadius = 0
  Length = 1063.33
  MakeFace = true
  Placement = pos=(1650,0.0194385,0) rot=(0,0,1;0rad)
  Points = (2) [(30998.4,15329.6,90),(30998.4,16393,90)]
  Start = (32648.4,15329.7,90)
FEATURE [Part::Part2DObjectPython] Line740  # Draft 2D object (typed FeaturePython)
  ChamferSize = 0
  Closed = false
  End = (34298.4,14119.6,90)
  FilletRadius = 0
  Length = 810.657
  MakeFace = true
  Placement = pos=(5030.34,-1210,0) rot=(0,0,1;0rad)
  Points = (2) [(28457.4,15329.6,90),(29268,15329.6,90)]
  Start = (33487.7,14119.6,90)
FEATURE [Part::Part2DObjectPython] Line741  # Draft 2D object (typed FeaturePython)
  ChamferSize = 0
  Closed = false
  End = (34298.4,14569.6,90)
  FilletRadius = 0
  Length = 810.657
  MakeFace = true
  Placement = pos=(5030.34,-0.0071275,0) rot=(0,0,1;0rad)
  Points = (2) [(28457.4,14569.6,90),(29268,14569.6,90)]
  Start = (33487.7,14569.6,90)
FEATURE [Part::Part2DObjectPython] Line742  # Draft 2D object (typed FeaturePython)
  ChamferSize = 0
  Closed = false
  End = (34298.4,15019.6,90)
  FilletRadius = 0
  Length = 810.657
  MakeFace = true
  Placement = pos=(5030.34,449.993,0) rot=(0,0,1;0rad)
  Points = (2) [(28457.4,14569.6,90),(29268,14569.6,90)]
  Start = (33487.7,15019.6,90)
FEATURE [Part::Part2DObjectPython] Rectangle206  # Draft 2D object (typed FeaturePython)
  ChamferSize = 0
  FilletRadius = 0
  Height = -740
  Length = -499.965
  MakeFace = true
  Placement = pos=(29268,14119.6,850) rot=(1,4.9e-05,4.9e-05;1.5708rad)
FEATURE [Part::Part2DObjectPython] Line743  # Draft 2D object (typed FeaturePython)
  ChamferSize = 0
  Closed = false
  End = (28768.1,14119.6,90)
  FilletRadius = 0
  Length = 20
  MakeFace = true
  Points = (2) [(28768.1,14119.6,110),(28768.1,14119.6,90)]
  Start = (28768.1,14119.6,110)
  Support = -> Extrusion066
FEATURE [Part::Part2DObjectPython] Line745  # Draft 2D object (typed FeaturePython)
  ChamferSize = 0
  Closed = false
  End = (29268,14719.6,90)
  FilletRadius = 0
  Length = 760
  MakeFace = true
  Placement = pos=(-0.00114353,150.001,0) rot=(0,0,1;0rad)
  Points = (2) [(29268,14569.6,850),(29268,14569.6,90)]
  Start = (29268,14719.6,850)
FEATURE [Part::Part2DObjectPython] Line747  # Draft 2D object (typed FeaturePython)
  ChamferSize = 0
  Closed = false
  End = (32048.4,15329.7,90)
  FilletRadius = 0
  Length = 20
  MakeFace = true
  Points = (2) [(32048.4,15329.7,110),(32048.4,15329.7,90)]
  Start = (32048.4,15329.7,110)
FEATURE [Part::Part2DObjectPython] Line748  # Draft 2D object (typed FeaturePython)
  ChamferSize = 0
  Closed = false
  End = (33548.4,15329.7,90)
  FilletRadius = 0
  Length = 20
  MakeFace = true
  Points = (2) [(33548.4,15329.7,110),(33548.4,15329.7,90)]
  Start = (33548.4,15329.7,110)
FEATURE [Part::Part2DObjectPython] Line749  # Draft 2D object (typed FeaturePython)
  ChamferSize = 0
  Closed = false
  End = (32048.4,15309.7,1431)
  FilletRadius = 0
  Length = 1341
  MakeFace = true
  Points = (2) [(32048.4,15309.7,90),(32048.4,15309.7,1431)]
  Start = (32048.4,15309.7,90)
FEATURE [Part::Part2DObjectPython] Line750  # Draft 2D object (typed FeaturePython)
  ChamferSize = 0
  Closed = false
  End = (31448.4,15309.7,1431)
  FilletRadius = 0
  Length = 1341
  MakeFace = true
  Points = (2) [(31448.4,15309.7,90),(31448.4,15309.7,1431)]
  Start = (31448.4,15309.7,90)
FEATURE [Part::Part2DObjectPython] Line751  # Draft 2D object (typed FeaturePython)
  ChamferSize = 0
  Closed = false
  End = (33248.4,15309.7,1431)
  FilletRadius = 0
  Length = 1341
  MakeFace = true
  Placement = pos=(1200,2.68e-05,0) rot=(0,0,1;0rad)
  Points = (2) [(32048.4,15309.7,90),(32048.4,15309.7,1431)]
  Start = (33248.4,15309.7,90)
FEATURE [Part::Part2DObjectPython] Line752  # Draft 2D object (typed FeaturePython)
  ChamferSize = 0
  Closed = false
  End = (30848.4,15309.7,1431)
  FilletRadius = 0
  Length = 1341
  MakeFace = true
  Placement = pos=(-600,-2.68e-05,0) rot=(0,0,1;0rad)
  Points = (2) [(31448.4,15309.7,90),(31448.4,15309.7,1431)]
  Start = (30848.4,15309.7,90)
FEATURE [Part::Part2DObjectPython] Line753  # Draft 2D object (typed FeaturePython)
  ChamferSize = 0
  Closed = false
  End = (30248.4,15309.7,1431)
  FilletRadius = 0
  Length = 1341
  MakeFace = true
  Placement = pos=(-1200,-2.68e-05,0) rot=(0,0,1;0rad)
  Points = (2) [(31448.4,15309.7,90),(31448.4,15309.7,1431)]
  Start = (30248.4,15309.7,90)
FEATURE [Part::Part2DObjectPython] Line754  # Draft 2D object (typed FeaturePython)
  ChamferSize = 0
  Closed = false
  End = (29648.4,15309.7,1431)
  FilletRadius = 0
  Length = 1341
  MakeFace = true
  Placement = pos=(-1800,-2.68e-05,0) rot=(0,0,1;0rad)
  Points = (2) [(31448.4,15309.7,90),(31448.4,15309.7,1431)]
  Start = (29648.4,15309.7,90)
FEATURE [Part::Part2DObjectPython] Line755  # Draft 2D object (typed FeaturePython)
  ChamferSize = 0
  Closed = false
  End = (32648.4,15309.7,1431)
  FilletRadius = 0
  Length = 1341
  MakeFace = true
  Placement = pos=(1200,2.68e-05,0) rot=(0,0,1;0rad)
  Points = (2) [(31448.4,15309.7,90),(31448.4,15309.7,1431)]
  Start = (32648.4,15309.7,90)
FEATURE [Part::Part2DObjectPython] Line756  # Draft 2D object (typed FeaturePython)
  ChamferSize = 0
  Closed = false
  End = (29288,14119.6,1431)
  FilletRadius = 0
  Length = 1341
  MakeFace = true
  Points = (2) [(29288,14119.6,90),(29288,14119.6,1431)]
  Start = (29288,14119.6,90)
FEATURE [Part::Part2DObjectPython] Line757  # Draft 2D object (typed FeaturePython)
  ChamferSize = 0
  Closed = false
  End = (29288,14719.6,1431)
  FilletRadius = 0
  Length = 1341
  MakeFace = true
  Points = (2) [(29288,14719.6,90),(29288,14719.6,1431)]
  Start = (29288,14719.6,90)
FEATURE [Part::Part2DObjectPython] DWire221  # Draft 2D object (typed FeaturePython)
  ChamferSize = 0
  Closed = true
  End = (28748.4,15849.6,90)
  FilletRadius = 0
  Length = 16980.4
  MakeFace = true
  Placement = pos=(0,-0.000229913,90) rot=(0,0,1;0rad)
  Points = (8) [(28748,14119.6,0),(29268,14119.6,0),(29268,15329.6,0),(33778.4,15329.7,0),(33778.4,14119.6,0),(34298.4,14119.6,0),(34298.4,15849.6,0),+1 more]
  Start = (28748,14119.6,90)
FEATURE [Part::FeaturePython] Panel076  label="Panel075"  # WARN: FeaturePython — macro-defined, semantics opaque (R4)
  Base = -> DWire221
  Length = 0
  MoveWithHost = false
  Placement = pos=(-25503.4,0.388761,0) rot=(0,0,1;0rad)
  Role = 0
  Sheets = 1
  Thickness = 20
  Width = 0
FEATURE [Part::FeaturePython] Panel078  label="Panel077"  # WARN: FeaturePython — macro-defined, semantics opaque (R4)
  Base = -> Rectangle206
  Length = 0
  MoveWithHost = false
  Placement = pos=(-25503.4,20.3888,0) rot=(0,0,1;0rad)
  Role = 0
  Sheets = 1
  Thickness = 20
  Width = 0
FEATURE [Part::FeaturePython] Panel088  label="Panel087"  # WARN: FeaturePython — macro-defined, semantics opaque (R4)
  Base = -> Rectangle206
  Length = 0
  MoveWithHost = false
  Placement = pos=(-25503.4,610.391,0) rot=(0,0,1;0rad)
  Role = 0
  Sheets = 1
  Thickness = 20
  Width = 0
FEATURE [Part::Part2DObjectPython] Rectangle224  # Draft 2D object (typed FeaturePython)
  ChamferSize = 0
  FilletRadius = 0
  Height = -600
  Length = 760
  MakeFace = true
  Placement = pos=(29648.4,15329.6,850) rot=(0.57735,-0.57735,0.57735;2.0944rad)
FEATURE [Part::FeaturePython] Panel090  label="Panel089"  # WARN: FeaturePython — macro-defined, semantics opaque (R4)
  Base = -> Rectangle224
  Length = 0
  MoveWithHost = false
  Placement = pos=(-25503.4,0.388761,-760) rot=(0,0,1;0rad)
  Role = 0
  Sheets = 1
  Thickness = 20
  Width = 0
FEATURE [Part::FeaturePython] Panel091  label="Panel090"  # WARN: FeaturePython — macro-defined, semantics opaque (R4)
  Base = -> Rectangle224
  Length = 0
  MoveWithHost = false
  Placement = pos=(-24903.4,0.388761,-760) rot=(0,0,1;0rad)
  Role = 0
  Sheets = 1
  Thickness = 20
  Width = 0
FEATURE [Part::FeaturePython] Panel092  label="Panel091"  # WARN: FeaturePython — macro-defined, semantics opaque (R4)
  Base = -> Rectangle224
  Length = 0
  MoveWithHost = false
  Placement = pos=(-24303.4,0.388761,-760) rot=(0,0,1;0rad)
  Role = 0
  Sheets = 1
  Thickness = 20
  Width = 0
FEATURE [Part::FeaturePython] Panel093  label="Panel092"  # WARN: FeaturePython — macro-defined, semantics opaque (R4)
  Base = -> Rectangle224
  Length = 0
  MoveWithHost = false
  Placement = pos=(-22503.4,0.388761,-760) rot=(0,0,1;0rad)
  Role = 0
  Sheets = 1
  Thickness = 20
  Width = 0
FEATURE [Part::FeaturePython] Panel094  label="Panel093"  # WARN: FeaturePython — macro-defined, semantics opaque (R4)
  Base = -> Rectangle224
  Length = 0
  MoveWithHost = false
  Placement = pos=(-23103.4,0.388761,-760) rot=(0,0,1;0rad)
  Role = 0
  Sheets = 1
  Thickness = 20
  Width = 0
FEATURE [Part::FeaturePython] Panel095  label="Panel094"  # WARN: FeaturePython — macro-defined, semantics opaque (R4)
  Base = -> Rectangle224
  Length = 0
  MoveWithHost = false
  Placement = pos=(-23703.4,0.388761,-760) rot=(0,0,1;0rad)
  Role = 0
  Sheets = 1
  Thickness = 20
  Width = 0
FEATURE [Part::Part2DObjectPython] Rectangle225  # Draft 2D object (typed FeaturePython)
  ChamferSize = 0
  FilletRadius = 0
  Height = -600.002
  Length = 760
  MakeFace = true
  Placement = pos=(29268,14119.6,90) rot=(0.707107,3.4e-05,0.707107;3.14166rad)
FEATURE [Part::FeaturePython] Panel099  label="Panel098"  # WARN: FeaturePython — macro-defined, semantics opaque (R4)
  Base = -> Rectangle225
  Length = 0
  MoveWithHost = false
  Placement = pos=(-25503.4,0.388761,0) rot=(0,0,1;0rad)
  Role = 0
  Sheets = 1
  Thickness = 20
  Width = 0
FEATURE [Part::Part2DObjectPython] Rectangle226  # Draft 2D object (typed FeaturePython)
  ChamferSize = 0
  FilletRadius = 0
  Height = -609.99
  Length = 760
  MakeFace = true
  Placement = pos=(29268,14719.6,90) rot=(0.707107,3.4e-05,0.707107;3.14166rad)
FEATURE [Part::FeaturePython] Panel101  label="Panel100"  # WARN: FeaturePython — macro-defined, semantics opaque (R4)
  Base = -> Rectangle226
  Length = 0
  MoveWithHost = false
  Placement = pos=(-25503.4,0.388761,0) rot=(0,0,1;0rad)
  Role = 0
  Sheets = 1
  Thickness = 20
  Width = 0
FEATURE [Part::Part2DObjectPython] Rectangle227  # Draft 2D object (typed FeaturePython)
  ChamferSize = 0
  FilletRadius = 0
  Height = 360.401
  Length = -760
  MakeFace = true
  Placement = pos=(29648.4,15329.6,850) rot=(0.57735,-0.57735,0.57735;2.0944rad)
FEATURE [Part::FeaturePython] Panel104  label="Panel103"  # WARN: FeaturePython — macro-defined, semantics opaque (R4)
  Base = -> Rectangle227
  Length = 0
  MoveWithHost = false
  Placement = pos=(-25503.4,0.388761,0) rot=(0,0,1;0rad)
  Role = 0
  Sheets = 1
  Thickness = 20
  Width = 0
FEATURE [Part::FeaturePython] Panel106  label="Panel105"  # WARN: FeaturePython — macro-defined, semantics opaque (R4)
  Base = -> Rectangle191
  Length = 0
  MoveWithHost = false
  Placement = pos=(-26093.4,0.388761,0) rot=(0,0,1;0rad)
  Role = 0
  Sheets = 1
  Thickness = 20
  Width = 0
FEATURE [Part::FeaturePython] Panel107  label="Panel106"  # WARN: FeaturePython — macro-defined, semantics opaque (R4)
  Base = -> Rectangle191
  Length = 0
  MoveWithHost = false
  Placement = pos=(-26693.4,0.388761,0) rot=(0,0,1;0rad)
  Role = 0
  Sheets = 1
  Thickness = 20
  Width = 0
FEATURE [Part::FeaturePython] Panel108  label="Panel107"  # WARN: FeaturePython — macro-defined, semantics opaque (R4)
  Base = -> Rectangle191
  Length = 0
  MoveWithHost = false
  Placement = pos=(-27293.4,0.388715,0) rot=(0,0,1;0rad)
  Role = 0
  Sheets = 1
  Thickness = 20
  Width = 0
FEATURE [Part::FeaturePython] Panel109  label="Panel108"  # WARN: FeaturePython — macro-defined, semantics opaque (R4)
  Base = -> Rectangle192
  Length = 0
  MoveWithHost = false
  Placement = pos=(-24893.4,0.388808,0) rot=(0,0,1;0rad)
  Role = 0
  Sheets = 1
  Thickness = 20
  Width = 0
FEATURE [Part::FeaturePython] Panel110  label="Panel109"  # WARN: FeaturePython — macro-defined, semantics opaque (R4)
  Base = -> Rectangle206
  Length = 0
  MoveWithHost = false
  Placement = pos=(-25503.4,1210.38,0) rot=(0,0,1;0rad)
  Role = 0
  Sheets = 1
  Thickness = 20
  Width = 0
FEATURE [Part::Part2DObjectPython] Rectangle229  # Draft 2D object (typed FeaturePython)
  ChamferSize = 0
  FilletRadius = 0
  Height = -740
  Length = -1730
  MakeFace = true
  Placement = pos=(34298.4,15849.6,850) rot=(0.57735,0.57735,0.57735;2.0944rad)
FEATURE [Part::FeaturePython] Panel111  label="Panel110"  # WARN: FeaturePython — macro-defined, semantics opaque (R4)
  Base = -> Rectangle229
  Length = 0
  MoveWithHost = false
  Placement = pos=(-25523.4,0.388761,0) rot=(0,0,1;0rad)
  Role = 0
  Sheets = 1
  Thickness = 20
  Width = 0
FEATURE [Part::Part2DObjectPython] Rectangle230  # Draft 2D object (typed FeaturePython)
  ChamferSize = 0
  FilletRadius = 0
  Height = -740
  Length = -1730
  MakeFace = true
  Placement = pos=(28748,14119.6,850) rot=(-0.577275,0.577388,0.577388;4.18868rad)
FEATURE [Part::FeaturePython] Panel112  label="Panel111"  # WARN: FeaturePython — macro-defined, semantics opaque (R4)
  Base = -> Rectangle230
  Length = 0
  MoveWithHost = false
  Placement = pos=(-25483.4,0.384846,0) rot=(0,0,1;0rad)
  Role = 0
  Sheets = 1
  Thickness = 20
  Width = 0
FEATURE [Part::Part2DObjectPython] Rectangle231  # Draft 2D object (typed FeaturePython)
  ChamferSize = 0
  FilletRadius = 0
  Height = -740
  Length = -2680
  MakeFace = true
  Placement = pos=(28768.4,15849.6,850) rot=(0,0.707107,0.707107;3.14159rad)
  Support = -> Panel076
FEATURE [Part::FeaturePython] Panel113  label="Panel112"  # WARN: FeaturePython — macro-defined, semantics opaque (R4)
  Base = -> Rectangle231
  Length = 0
  MoveWithHost = false
  Placement = pos=(-25503.4,-19.6109,0) rot=(0,0,1;0rad)
  Role = 0
  Sheets = 1
  Thickness = 20
  Width = 0
FEATURE [Part::Part2DObjectPython] Line759  # Draft 2D object (typed FeaturePython)
  ChamferSize = 0
  Closed = true
  End = (28748.4,15849.6,900)
  FilletRadius = 0
  Length = 500
  MakeFace = true
  Points = (2) [(28748.4,15849.6,900),(28748.4,15849.6,900)]
  Start = (28748.4,15849.6,900)
FEATURE [Part::Feature] Box005  label="Cube005"
  Placement = pos=(33248.4,15549.6,1500) rot=(0,0,1;0rad)
  shape: bbox 600 x 300 x 720 mm, 6 faces (baked)
FEATURE [Part::Part2DObjectPython] Line762  # Draft 2D object (typed FeaturePython)
  ChamferSize = 0
  Closed = true
  End = (34298.4,15849.6,900)
  FilletRadius = 0
  Length = 500
  MakeFace = true
  Placement = pos=(5550,0,0) rot=(0,0,1;0rad)
  Points = (2) [(28748.4,15849.6,900),(28748.4,15849.6,900)]
  Start = (34298.4,15849.6,900)
FEATURE [Part::Part2DObjectPython] Line763  # Draft 2D object (typed FeaturePython)
  ChamferSize = 0
  Closed = false
  End = (28748.4,15849.6,1500)
  FilletRadius = 0
  Length = 5550
  MakeFace = true
  Points = (2) [(34298.4,15849.6,1500),(28748.4,15849.6,1500)]
  Start = (34298.4,15849.6,1500)
FEATURE [Part::Part2DObjectPython] Line764  # Draft 2D object (typed FeaturePython)
  ChamferSize = 0
  Closed = true
  End = (34298.4,14119.6,900)
  FilletRadius = 0
  Length = 500
  MakeFace = true
  Placement = pos=(5550,-1730,0) rot=(0,0,1;0rad)
  Points = (2) [(28748.4,15849.6,900),(28748.4,15849.6,900)]
  Start = (34298.4,14119.6,900)
FEATURE [Part::Part2DObjectPython] Line765  # Draft 2D object (typed FeaturePython)
  ChamferSize = 0
  Closed = false
  End = (34298.4,15849.6,1500)
  FilletRadius = 0
  Length = 1730
  MakeFace = true
  Points = (2) [(34298.4,14119.6,1500),(34298.4,15849.6,1500)]
  Start = (34298.4,14119.6,1500)
FEATURE [Part::Feature] Solid
  Placement = pos=(-25503.4,0.388761,0) rot=(0,0,1;0rad)
  shape: bbox 500 x 20.05 x 2110 mm, 6 faces (baked)
FEATURE [Part::Feature] Solid001
  Placement = pos=(-25503.4,590.39,0) rot=(0,0,1;0rad)
  shape: bbox 500 x 20.05 x 2110 mm, 6 faces (baked)
FEATURE [Part::Feature] Solid002
  Placement = pos=(-25503.4,1190.38,0) rot=(0,0,1;0rad)
  shape: bbox 500 x 20.05 x 2110 mm, 6 faces (baked)
FEATURE [Part::Part2DObjectPython] Rectangle233  # Draft 2D object (typed FeaturePython)
  ChamferSize = 0
  FilletRadius = 0
  Height = -1730
  Length = -2110
  MakeFace = true
  Placement = pos=(34278.4,14119.6,2220) rot=(0.707107,3.4e-05,0.707107;3.14166rad)
FEATURE [Part::FeaturePython] Panel115  label="Panel114"  # WARN: FeaturePython — macro-defined, semantics opaque (R4)
  Base = -> Rectangle233
  Length = 0
  MoveWithHost = false
  Placement = pos=(-25503.4,0.388761,0) rot=(0,0,1;0rad)
  Role = 0
  Sheets = 1
  Thickness = 20
  Width = 0
FEATURE [Part::Part2DObjectPython] Rectangle234  # Draft 2D object (typed FeaturePython)
  ChamferSize = 0
  FilletRadius = 0
  Height = 1410
  Length = -599.953
  MakeFace = true
  Placement = pos=(33778.4,14119.6,90) rot=(0.577388,-0.577332,-0.577332;2.09434rad)
FEATURE [Part::FeaturePython] Panel116  label="Panel115"  # WARN: FeaturePython — macro-defined, semantics opaque (R4)
  Base = -> Rectangle234
  Length = 0
  MoveWithHost = false
  Placement = pos=(-25503.4,0.388761,0) rot=(0,0,1;0rad)
  Role = 0
  Sheets = 1
  Thickness = 20
  Width = 0
FEATURE [Part::Part2DObjectPython] Rectangle235  # Draft 2D object (typed FeaturePython)
  ChamferSize = 0
  FilletRadius = 0
  Height = 720
  Length = 600.001
  MakeFace = true
  Placement = pos=(33778.3,14719.6,1500) rot=(0.577388,-0.577332,-0.577332;2.09434rad)
  Support = -> Panel116
FEATURE [Part::FeaturePython] Panel117  label="Panel116"  # WARN: FeaturePython — macro-defined, semantics opaque (R4)
  Base = -> Rectangle235
  Length = 0
  MoveWithHost = false
  Placement = pos=(-25503.4,0.388761,0) rot=(0,0,1;0rad)
  Role = 0
  Sheets = 1
  Thickness = 20
  Width = 0
FEATURE [Part::Feature] Solid003
  Placement = pos=(-25503.4,1710.39,0) rot=(0,0,1;0rad)
  shape: bbox 500 x 20.05 x 2110 mm, 6 faces (baked)
FEATURE [Sketcher::SketchObject] Sketch073
  Placement = pos=(33758.4,15809.9,1049.63) rot=(0.577388,-0.577332,-0.577332;2.09434rad)
  sketch-geometry (8):
    g0: LineSegment StartX=0 StartY=0 StartZ=0 EndX=450 EndY=0 EndZ=0
    g1: LineSegment StartX=450 StartY=0 StartZ=0 EndX=450 EndY=1200 EndZ=0
    g2: LineSegment StartX=450 StartY=1200 StartZ=0 EndX=0 EndY=1200 EndZ=0
    g3: LineSegment StartX=0 StartY=1200 StartZ=0 EndX=0 EndY=0 EndZ=0
    g4: LineSegment StartX=10 StartY=0 StartZ=0 EndX=440 EndY=0 EndZ=0
    g5: LineSegment StartX=440 StartY=0 StartZ=0 EndX=440 EndY=1190 EndZ=0
    g6: LineSegment StartX=440 StartY=1190 StartZ=0 EndX=10 EndY=1190 EndZ=0
    g7: LineSegment StartX=10 StartY=1190 StartZ=0 EndX=10 EndY=0 EndZ=0
  constraints (23):
    c: Coincident(g0,g1)
    c: Coincident(g1,g2)
    c: Coincident(g2,g3)
    c: Coincident(g3,g0)
    c: Horizontal(g0)
    c: Horizontal(g2)
    c: Vertical(g1)
    c: Vertical(g3)
    c: Coincident(g4,g5)
    c: Coincident(g5,g6)
    c: Coincident(g6,g7)
    c: Coincident(g7,g4)
    c: Horizontal(g4)
    c: Horizontal(g6)
    c: Vertical(g5)
    c: Vertical(g7)
    c: DistanceY(g1) = 1200
    c: DistanceX(g0) = 450
    c: DistanceY(g6,g2) = 10
    c: DistanceX(g2,g6) = 10
    c: DistanceX(g4,g0) = 10
    c: DistanceY(g0,g4) = 0
    c: Coincident(g0,g-1)
FEATURE [Part::FeaturePython] Window061  label="Window059"  # WARN: FeaturePython — macro-defined, semantics opaque (R4)
  Base = -> Sketch073
  Height = 1200
  HoleDepth = 0
  MoveWithHost = true
  Normal = (1,9.71743e-05,0)
  Placement = pos=(-25503.4,-4.90278,-149.632) rot=(0,0,1;0rad)
  Preset = 6
  Role = 1
  Width = 450
  WindowParts = OuterFrame | Frame | Wire0,Wire1 | 40.0 | 0.0 | Door | Solid panel | Wire1 | 0.0 | 0.0
FEATURE [Part::Part2DObjectPython] Rectangle238  # Draft 2D object (typed FeaturePython)
  ChamferSize = 0
  FilletRadius = 0
  Height = 720
  Length = -609.998
  MakeFace = true
  Placement = pos=(33778.3,14719.6,1500) rot=(0.577388,-0.577332,-0.577332;2.09434rad)
FEATURE [Part::FeaturePython] Panel121  label="Panel120"  # WARN: FeaturePython — macro-defined, semantics opaque (R4)
  Base = -> Rectangle238
  Length = 0
  MoveWithHost = false
  Placement = pos=(-25503.4,0.388761,0) rot=(0,0,1;0rad)
  Role = 0
  Sheets = 1
  Thickness = 20
  Width = 0
FEATURE [Part::Feature] Solid004
  Placement = pos=(-24402,1457.26,900) rot=(0,0,1;0rad)
  shape: bbox 109.3 x 38.36 x 1190 mm, 6 faces (baked)
FEATURE [Part::Feature] Solid005
  Placement = pos=(-24402,1457.26,900) rot=(0,0,1;0rad)
  shape: bbox 109.3 x 38.36 x 1190 mm, 6 faces (baked)
FEATURE [Part::Feature] Solid006
  Placement = pos=(-24299.6,1280.62,900) rot=(0,0,1;0rad)
  shape: bbox 20 x 107.5 x 1190 mm, 6 faces (baked)
FEATURE [Part::Feature] Solid007
  Placement = pos=(-24299.6,1173.12,900) rot=(0,0,1;0rad)
  shape: bbox 20 x 107.5 x 1190 mm, 6 faces (baked)
FEATURE [Part::Part2DObjectPython] Line768  # Draft 2D object (typed FeaturePython)
  ChamferSize = 0
  Closed = false
  End = (33758.3,14719.6,900)
  FilletRadius = 0
  Length = 609.997
  MakeFace = true
  Points = (2) [(33758.3,15329.6,900),(33758.3,14719.6,900)]
  Start = (33758.3,15329.6,900)
FEATURE [Part::Part2DObjectPython] Line769  # Draft 2D object (typed FeaturePython)
  ChamferSize = 0
  Closed = false
  End = (33778.3,14719.6,900)
  FilletRadius = 0
  Length = 609.997
  MakeFace = true
  Placement = pos=(20,0.00194349,0) rot=(0,0,1;0rad)
  Points = (2) [(33758.3,15329.6,900),(33758.3,14719.6,900)]
  Start = (33778.3,15329.6,900)
FEATURE [Part::Part2DObjectPython] Rectangle240  # Draft 2D object (typed FeaturePython)
  ChamferSize = 0
  FilletRadius = 0
  Height = -600
  Length = -609.99
  MakeFace = true
  Placement = pos=(33778.3,14719.6,1500) rot=(0.577388,-0.577332,-0.577332;2.09434rad)
  Support = -> Solid001
FEATURE [Part::FeaturePython] Panel123  label="Panel122"  # WARN: FeaturePython — macro-defined, semantics opaque (R4)
  Base = -> Rectangle240
  Length = 0
  MoveWithHost = false
  Placement = pos=(-25503.4,0.388761,0) rot=(0,0,1;0rad)
  Role = 0
  Sheets = 1
  Thickness = 20
  Width = 0
FEATURE [Part::Part2DObjectPython] Rectangle241  # Draft 2D object (typed FeaturePython)
  ChamferSize = 0
  FilletRadius = 0
  Height = -530.039
  Length = 760
  MakeFace = true
  Placement = pos=(33248.4,15329.6,90) rot=(0.57735,-0.57735,0.57735;2.0944rad)
  Support = -> Panel109
FEATURE [Part::FeaturePython] Panel124  label="Panel123"  # WARN: FeaturePython — macro-defined, semantics opaque (R4)
  Base = -> Rectangle241
  Length = 0
  MoveWithHost = false
  Placement = pos=(-25503.4,0.388761,0) rot=(0,0,1;0rad)
  Role = 0
  Sheets = 1
  Thickness = 20
  Width = 0
FEATURE [Part::Part2DObjectPython] Rectangle242  # Draft 2D object (typed FeaturePython)
  ChamferSize = 0
  FilletRadius = 0
  Height = 760
  Length = 590.081
  MakeFace = true
  Placement = pos=(33778.4,15309.6,90) rot=(0.577357,-0.577347,-0.577347;2.09439rad)
  Support = -> Panel076
FEATURE [Part::FeaturePython] Panel125  label="Panel124"  # WARN: FeaturePython — macro-defined, semantics opaque (R4)
  Base = -> Rectangle242
  Length = 0
  MoveWithHost = false
  Placement = pos=(-25503.4,0.388761,0) rot=(0,0,1;0rad)
  Role = 0
  Sheets = 1
  Thickness = 20
  Width = 0
FEATURE [Part::Part2DObjectPython] DWire222  # Draft 2D object (typed FeaturePython)
  ChamferSize = 0
  Closed = true
  End = (31964.5,15309.6,500)
  FilletRadius = 0
  Length = 440
  MakeFace = true
  Points = (4) [(31964.5,15309.6,700),(31984.5,15309.6,700),(31984.5,15309.6,500),(31964.5,15309.6,500)]
  Start = (31964.5,15309.6,700)
FEATURE [Part::Feature] Solid008
  Placement = pos=(-25499.5,0.388761,0) rot=(0,0,1;0rad)
  shape: bbox 20 x 20 x 200 mm, 6 faces (baked)
FEATURE [Part::Feature] Extrusion072
  Placement = pos=(-25359.5,0.388761,0) rot=(0,0,1;0rad)
  shape: bbox 20 x 20 x 200 mm, 6 faces (baked)
FEATURE [Part::Feature] Solid011
  Placement = pos=(-26699.5,0.388761,0) rot=(0,0,1;0rad)
  shape: bbox 20 x 20 x 200 mm, 6 faces (baked)
FEATURE [Part::Feature] Extrusion076
  Placement = pos=(-26559.5,0.388761,0) rot=(0,0,1;0rad)
  shape: bbox 20 x 20 x 200 mm, 6 faces (baked)
FEATURE [Part::Feature] Solid012
  Placement = pos=(-27899.5,0.388761,0) rot=(0,0,1;0rad)
  shape: bbox 20 x 20 x 200 mm, 6 faces (baked)
FEATURE [Part::Feature] Extrusion077
  Placement = pos=(-27759.5,0.388761,0) rot=(0,0,1;0rad)
  shape: bbox 20 x 20 x 200 mm, 6 faces (baked)
FEATURE [Part::Feature] Solid013
  Placement = pos=(-24299.5,0.388761,0) rot=(0,0,1;0rad)
  shape: bbox 20 x 20 x 200 mm, 6 faces (baked)
FEATURE [Part::Feature] Extrusion078
  Placement = pos=(-24159.5,0.388761,0) rot=(0,0,1;0rad)
  shape: bbox 20 x 20 x 200 mm, 6 faces (baked)
FEATURE [Part::Feature] Solid014
  Placement = pos=(-7054.65,46764.4,0) rot=(0,0,-1;1.5708rad)
  shape: bbox 20 x 20 x 200 mm, 6 faces (baked)
FEATURE [Part::Feature] Extrusion084
  Placement = pos=(-7054.65,46624.4,0) rot=(0,0,-1;1.5708rad)
  shape: bbox 20 x 20 x 200 mm, 6 faces (baked)
FEATURE [Part::Feature] Solid016
  Placement = pos=(-11505,46764.4,0) rot=(0,0,-1;1.5708rad)
  shape: bbox 20 x 20 x 200 mm, 6 faces (baked)
FEATURE [Part::Feature] Extrusion090
  Placement = pos=(-11505,46624.4,0) rot=(0,0,-1;1.5708rad)
  shape: bbox 20 x 20 x 200 mm, 6 faces (baked)
FEATURE [Part::Feature] Solid017
  Placement = pos=(-25503.4,0.388761,-50) rot=(0,0,1;0rad)
  shape: bbox 2700 x 1730 x 50 mm, 8 faces (baked)
FEATURE [Part::Feature] Solid018
  Placement = pos=(-25503.4,0.388479,720) rot=(0,0,1;0rad)
  shape: bbox 2700 x 1730 x 50 mm, 8 faces (baked)
FEATURE [Part::Feature] Solid019
  Placement = pos=(-25503.4,20.3888,0) rot=(0,0,1;0rad)
  shape: bbox 600 x 20 x 720 mm, 6 faces (baked)
FEATURE [Part::Feature] Solid021
  Placement = pos=(-25523.4,0.388761,0) rot=(0,0,1;0rad)
  shape: bbox 20 x 260 x 720 mm, 6 faces (baked)
FEATURE [Part::Feature] Solid022
  Placement = pos=(-26113.4,0.388761,0) rot=(0,0,1;0rad)
  shape: bbox 20 x 260 x 720 mm, 6 faces (baked)
FEATURE [Part::Feature] Solid023
  Placement = pos=(-26713.4,0.388761,0) rot=(0,0,1;0rad)
  shape: bbox 20 x 260 x 720 mm, 6 faces (baked)
FEATURE [Part::Feature] Solid024
  Placement = pos=(-27313.4,0.388761,0) rot=(0,0,1;0rad)
  shape: bbox 20 x 260 x 720 mm, 6 faces (baked)
FEATURE [Part::Feature] Solid025
  Placement = pos=(-26103.4,20.3888,0) rot=(0,0,1;0rad)
  shape: bbox 600 x 20 x 720 mm, 6 faces (baked)
FEATURE [Part::Feature] Solid026
  Placement = pos=(-26703.4,20.3888,4.4e-10) rot=(0,0,1;0rad)
  shape: bbox 600 x 20 x 720 mm, 6 faces (baked)
FEATURE [Part::Feature] Solid027
  Placement = pos=(-27303.4,20.3888,4.4e-10) rot=(0,0,1;0rad)
  shape: bbox 600 x 20 x 720 mm, 6 faces (baked)
FEATURE [Part::Feature] Solid028
  Placement = pos=(-25503.4,0.388761,-370) rot=(0,0,1;0rad)
  shape: bbox 570 x 260 x 20 mm, 6 faces (baked)
FEATURE [Part::Feature] Solid029
  Placement = pos=(-25503.4,0.388761,-370) rot=(0,0,1;0rad)
  shape: bbox 580 x 260 x 20 mm, 6 faces (baked)
FEATURE [Part::Feature] Solid030
  Placement = pos=(-26103.4,0.388761,-370) rot=(0,0,1;0rad)
  shape: bbox 580 x 260 x 20 mm, 6 faces (baked)
FEATURE [Part::Feature] Solid031
  Placement = pos=(-27903.4,0.388761,4.36e-10) rot=(0,0,1;0rad)
  shape: bbox 20 x 260 x 720 mm, 6 faces (baked)
FEATURE [Part::Feature] Solid032
  Placement = pos=(-25503.4,0.388761,-370) rot=(0,0,1;0rad)
  shape: bbox 570 x 260 x 20 mm, 6 faces (baked)
FEATURE [Part::Feature] Solid033
  Placement = pos=(-25523.4,0.388761,0) rot=(0,0,1;0rad)
  shape: bbox 20 x 600 x 720 mm, 6 faces (baked)
FEATURE [Part::Feature] Solid035
  Placement = pos=(-25523.4,600.389,0) rot=(0,0,1;0rad)
  shape: bbox 20 x 600 x 720 mm, 6 faces (baked)
FEATURE [Part::Feature] Solid036
  Placement = pos=(-25503.4,20.3885,0) rot=(0,0,1;0rad)
  shape: bbox 260 x 20 x 720 mm, 6 faces (baked)
FEATURE [Part::Feature] Solid037
  Placement = pos=(-25503.4,610.388,0) rot=(0,0,1;0rad)
  shape: bbox 260 x 20 x 720 mm, 6 faces (baked)
FEATURE [Part::Feature] Solid038
  Placement = pos=(-25503.4,1200.39,0) rot=(0,0,1;0rad)
  shape: bbox 260 x 20 x 720 mm, 6 faces (baked)
FEATURE [Part::Feature] Solid039
  Placement = pos=(-25503.4,0.388761,-370) rot=(0,0,1;0rad)
  shape: bbox 280 x 510 x 20 mm, 6 faces (baked)
FEATURE [Part::Feature] Solid040
  Placement = pos=(-25503.4,0.388761,-370) rot=(0,0,1;0rad)
  shape: bbox 260 x 570 x 20 mm, 6 faces (baked)
FEATURE [Part::Feature] Solid041
  Placement = pos=(-25503.4,0.388761,-370) rot=(0,0,1;0rad)
  shape: bbox 260 x 570 x 20 mm, 6 faces (baked)
FEATURE [Part::Feature] Extrusion091
  Placement = pos=(-11744.6,46624.4,1160) rot=(0,0,-1;1.5708rad)
  shape: bbox 20 x 20 x 200 mm, 6 faces (baked)
FEATURE [Part::Feature] Solid042
  Placement = pos=(-11744.6,46764.4,1160) rot=(0,0,-1;1.5708rad)
  shape: bbox 20 x 20 x 200 mm, 6 faces (baked)
FEATURE [Part::Feature] Solid043
  Placement = pos=(-27899.5,240.354,1160) rot=(0,0,1;0rad)
  shape: bbox 20 x 20 x 200 mm, 6 faces (baked)
FEATURE [Part::Feature] Extrusion092
  Placement = pos=(-27759.5,240.354,1160) rot=(0,0,1;0rad)
  shape: bbox 20 x 20 x 200 mm, 6 faces (baked)
FEATURE [Part::Feature] Solid044
  Placement = pos=(-26699.5,240.354,1160) rot=(0,0,1;0rad)
  shape: bbox 20 x 20 x 200 mm, 6 faces (baked)
FEATURE [Part::Feature] Extrusion093
  Placement = pos=(-26559.5,240.354,1160) rot=(0,0,1;0rad)
  shape: bbox 20 x 20 x 200 mm, 6 faces (baked)
FEATURE [Part::Feature] Solid045
  Placement = pos=(-25483.4,0.388761,0) rot=(0,0,1;0rad)
  shape: bbox 20 x 1730 x 720 mm, 6 faces (baked)
FEATURE [Part::Feature] Solid046
  Placement = pos=(-25503.4,-19.6112,0) rot=(0,0,1;0rad)
  shape: bbox 2680 x 20 x 720 mm, 6 faces (baked)
FEATURE [Part::Feature] Solid047
  Placement = pos=(-25503.4,0.388761,0) rot=(0,0,1;0rad)
  shape: bbox 540.2 x 1730 x 50 mm, 6 faces (baked)
FEATURE [App::DocumentObjectGroup] Group050  label="Wall Cabinet"
  Group = -> [Solid017,Solid019,Solid022,Solid024,Solid026,Solid028,Solid030,Solid032,Solid035,Solid037,Solid039,Solid041,Solid042,Extrusion092,Extrusion093,Solid046,Solid018,Solid021,Solid023,Solid025,Solid027,Solid029,Solid031,Solid033,Solid036,Solid038,Solid040,Extrusion091,Solid043,Solid044,Solid045]
FEATURE [Part::Feature] Box004  label="Cube004"
  Placement = pos=(32648.4,15549.6,1500) rot=(0,0,1;0rad)
  shape: bbox 600 x 300 x 720 mm, 6 faces (baked)
FEATURE [App::DocumentObjectGroup] Group047  label="Trash objects"
  Group = -> [Extrusion064,Fusion,Fusion005,Fusion004,Extrude,Extrusion065,Wire,Box005,Box004]
FEATURE [Part::Feature] Solid048
  Placement = pos=(-24303.4,0.388761,-760) rot=(0,0,1;0rad)
  shape: bbox 600 x 20 x 760 mm, 6 faces (baked)
FEATURE [Part::Feature] Solid049
  Placement = pos=(-25503.4,0.388761,0) rot=(0,0,1;0rad)
  shape: bbox 40.05 x 500 x 1320 mm, 10 faces (baked)
FEATURE [App::DocumentObjectGroup] Group051  label="Tall Cabinets"
  Group = -> [Solid,Solid001,Solid002,Panel115,Panel116,Panel117,Solid003,Panel121,Solid004,Solid005,Solid006,Solid007,Panel123,Panel125,Solid047,Window061,Solid049]
FEATURE [Part::Feature] wc
  Placement = pos=(552.769,8969.39,0) rot=(0,0,1;1.5708rad)
  shape: bbox 707.9 x 455.8 x 820 mm, 42 faces, 2 solids (baked)
FEATURE [Part::Feature] wc001
  Placement = pos=(1596.62,7842.23,0) rot=(0,0,1;0rad)
  shape: bbox 455.8 x 707.9 x 820 mm, 42 faces, 2 solids (baked)
FEATURE [Part::Feature] wc002
  Placement = pos=(2058,9192.19,3000) rot=(0,0,1;0rad)
  shape: bbox 455.8 x 707.9 x 820 mm, 42 faces, 2 solids (baked)
FEATURE [Part::Feature] wc003
  Placement = pos=(9070,11292.2,3000) rot=(0,0,1;0rad)
  shape: bbox 455.8 x 707.9 x 820 mm, 42 faces, 2 solids (baked)
FEATURE [Part::Feature] Part__Feature  label="Lavabo01"
  Placement = pos=(1796.02,9413.06,0) rot=(0.000105,0.707107,0.707107;3.14138rad)
  shape: bbox 550.5 x 453.2 x 939.1 mm, 221 faces (baked)
FEATURE [Part::Feature] Part__Feature001  label="Lavabo002"
  Placement = pos=(2616.63,8063.11,-1.45343e-05) rot=(0.000105,0.707107,0.707107;3.14138rad)
  shape: bbox 550.5 x 453.2 x 939.1 mm, 221 faces (baked)
FEATURE [Part::Feature] Part__Feature002  label="Lavabo003"
  Placement = pos=(8112.1,11513.1,3000) rot=(0.000105,0.707107,0.707107;3.14138rad)
  shape: bbox 550.5 x 453.2 x 939.1 mm, 221 faces (baked)
FEATURE [Part::Feature] Solid056  label="Shower Base"
  Placement = pos=(-42142,0.388761,3000) rot=(0,0,1;0rad)
  shape: bbox 1000 x 1500 x 110 mm, 20 faces (baked)
FEATURE [Part::Feature] Solid057  label="Shower Base001"
  Placement = pos=(-42142,0.388761,3000) rot=(0,0,1;0rad)
  shape: bbox 1600 x 2200 x 110 mm, 20 faces (baked)
FEATURE [Part::Feature] Solid058  label="Shower Base002"
  Placement = pos=(-25503.4,0.388456,0) rot=(0,0,1;0rad)
  shape: bbox 1000 x 1600 x 110 mm, 20 faces (baked)
FEATURE [Part::Feature] Part__Feature003  label="Lavabo004"
  Placement = pos=(1076.1,9413.06,3000) rot=(0.000105,0.707107,0.707107;3.14138rad)
  shape: bbox 550.5 x 453.2 x 939.1 mm, 221 faces (baked)
FEATURE [App::DocumentObjectGroup] Group052  label="Sanitation"
  Group = -> [wc,wc001,wc002,wc003,Part__Feature,Part__Feature001,Part__Feature002,Solid056,Solid057,Solid058,Part__Feature003]
FEATURE [Part::Part2DObjectPython] Line770  # Draft 2D object (typed FeaturePython)
  ChamferSize = 0
  Closed = false
  End = (50037,15849.6,0)
  FilletRadius = 0
  Length = 2200
  MakeFace = true
  Points = (2) [(50037,13649.6,0),(50037,15849.6,0)]
  Start = (50037,13649.6,0)
FEATURE [Part::Part2DObjectPython] Line771  # Draft 2D object (typed FeaturePython)
  ChamferSize = 0
  Closed = false
  End = (50820,14749.6,0)
  FilletRadius = 0
  Length = 783
  MakeFace = true
  Points = (2) [(50037,14749.6,0),(50820,14749.6,0)]
  Start = (50037,14749.6,0)
FEATURE [Part::Part2DObjectPython] Line772  # Draft 2D object (typed FeaturePython)
  ChamferSize = 0
  Closed = false
  End = (50820,15849.6,0)
  FilletRadius = 0
  Length = 1100
  MakeFace = true
  Points = (2) [(50820,14749.6,0),(50820,15849.6,0)]
  Start = (50820,14749.6,0)
FEATURE [Part::Part2DObjectPython] Line773  # Draft 2D object (typed FeaturePython)
  ChamferSize = 0
  Closed = false
  End = (50037,15299.6,0)
  FilletRadius = 0
  Length = 783
  MakeFace = true
  Points = (2) [(50820,15299.6,0),(50037,15299.6,0)]
  Start = (50820,15299.6,0)
FEATURE [Part::Part2DObjectPython] Line774  # Draft 2D object (typed FeaturePython)
  ChamferSize = 0
  Closed = false
  End = (50820,14199.6,0)
  FilletRadius = 0
  Length = 783
  MakeFace = true
  Placement = pos=(0,-550,0) rot=(0,0,1;0rad)
  Points = (2) [(50037,14749.6,0),(50820,14749.6,0)]
  Start = (50037,14199.6,0)
FEATURE [Part::Part2DObjectPython] Line775  # Draft 2D object (typed FeaturePython)
  ChamferSize = 0
  Closed = false
  End = (50566,13924.6,0)
  FilletRadius = 0
  Length = 529
  MakeFace = true
  Points = (2) [(50037,13924.6,0),(50566,13924.6,0)]
  Start = (50037,13924.6,0)
FEATURE [Part::Part2DObjectPython] Line776  # Draft 2D object (typed FeaturePython)
  ChamferSize = 0
  Closed = false
  End = (50208,13649.6,0)
  FilletRadius = 0
  Length = 171
  MakeFace = true
  Points = (2) [(50037,13649.6,0),(50208,13649.6,0)]
  Start = (50037,13649.6,0)
FEATURE [Part::Part2DObjectPython] Line777  # Draft 2D object (typed FeaturePython)
  ChamferSize = 0
  Closed = false
  End = (50208,13924.6,0)
  FilletRadius = 0
  Length = 275
  MakeFace = true
  Points = (2) [(50208,13649.6,0),(50208,13924.6,0)]
  Start = (50208,13649.6,0)
FEATURE [Part::Part2DObjectPython] Line779  # Draft 2D object (typed FeaturePython)
  ChamferSize = 0
  Closed = false
  End = (50037,14066.8,0)
  FilletRadius = 0
  Length = 360.624
  MakeFace = true
  Points = (2) [(50397.6,14066.8,0),(50037,14066.8,0)]
  Start = (50397.6,14066.8,0)
FEATURE [Part::Part2DObjectPython] Rectangle248  # Draft 2D object (typed FeaturePython)
  ChamferSize = 0
  FilletRadius = 0
  Height = 2800
  Length = 550
  MakeFace = true
  Placement = pos=(50037,14199.6,0) rot=(0.57735,-0.57735,-0.57735;2.0944rad)
FEATURE [Part::FeaturePython] Panel130  label="Panel129"  # WARN: FeaturePython — macro-defined, semantics opaque (R4)
  Base = -> Rectangle248
  Length = 0
  MoveWithHost = false
  Placement = pos=(-42142,0.388761,3000) rot=(0,0,1;0rad)
  Role = 0
  Sheets = 1
  Thickness = 30
  Width = 0
FEATURE [Part::FeaturePython] Panel131  label="Panel130"  # WARN: FeaturePython — macro-defined, semantics opaque (R4)
  Base = -> Rectangle248
  Length = 0
  MoveWithHost = false
  Placement = pos=(-42142,550.389,3000) rot=(0,0,1;0rad)
  Role = 0
  Sheets = 1
  Thickness = 30
  Width = 0
FEATURE [Part::FeaturePython] Panel132  label="Panel131"  # WARN: FeaturePython — macro-defined, semantics opaque (R4)
  Base = -> Rectangle248
  Length = 0
  MoveWithHost = false
  Placement = pos=(-42142,1100.39,3000) rot=(0,0,1;0rad)
  Role = 0
  Sheets = 1
  Thickness = 30
  Width = 0
FEATURE [Part::FeaturePython] Panel133  label="Panel132"  # WARN: FeaturePython — macro-defined, semantics opaque (R4)
  Base = -> Rectangle248
  Length = 0
  MoveWithHost = false
  Placement = pos=(-42142,1650.39,3000) rot=(0,0,1;0rad)
  Role = 0
  Sheets = 1
  Thickness = 30
  Width = 0
FEATURE [Part::Part2DObjectPython] Rectangle250  # Draft 2D object (typed FeaturePython)
  ChamferSize = 0
  FilletRadius = 0
  Height = 2800
  Length = 550
  MakeFace = true
  Placement = pos=(50037,14199.6,0) rot=(0.57735,-0.57735,-0.57735;2.0944rad)
FEATURE [Part::FeaturePython] Panel134  label="Panel200"  # WARN: FeaturePython — macro-defined, semantics opaque (R4)
  Base = -> Rectangle250
  Length = 0
  MoveWithHost = false
  Placement = pos=(-37138.2,39379.8,3000) rot=(0,0,-1;0.785399rad)
  Role = 0
  Sheets = 1
  Thickness = 30
  Width = 0
FEATURE [Part::FeaturePython] Panel135  label="Panel134"  # WARN: FeaturePython — macro-defined, semantics opaque (R4)
  Base = -> Rectangle250
  Length = 0
  MoveWithHost = false
  Placement = pos=(-17445.9,-30951.9,3000) rot=(0,0,1;0.785398rad)
  Role = 0
  Sheets = 1
  Thickness = 30
  Width = 0
FEATURE [Part::FeaturePython] Panel136  label="Panel135"  # WARN: FeaturePython — macro-defined, semantics opaque (R4)
  Base = -> Rectangle250
  Length = 0
  MoveWithHost = false
  Placement = pos=(-37138.2,40759.5,3000) rot=(0,0,-1;0.785398rad)
  Role = 0
  Sheets = 1
  Thickness = 30
  Width = 0
FEATURE [Part::FeaturePython] Panel137  label="Panel136"  # WARN: FeaturePython — macro-defined, semantics opaque (R4)
  Base = -> Rectangle250
  Length = 0
  MoveWithHost = false
  Placement = pos=(-17445.9,-29572.1,3000) rot=(0,0,1;0.785398rad)
  Role = 0
  Sheets = 1
  Thickness = 30
  Width = 0
FEATURE [Part::Part2DObjectPython] Rectangle253  # Draft 2D object (typed FeaturePython)
  ChamferSize = 0
  FilletRadius = 0
  Height = 2200
  Length = -570
  MakeFace = true
  Placement = pos=(50007,13649.6,0) rot=(0,0,1;0rad)
FEATURE [Part::FeaturePython] Panel138  label="bed 2 closet conc base"  # WARN: FeaturePython — macro-defined, semantics opaque (R4)
  Base = -> Rectangle253
  Length = 0
  MoveWithHost = false
  Placement = pos=(-42142,0.388761,3000) rot=(0,0,1;0rad)
  Role = 0
  Sheets = 1
  Thickness = 40
  Width = 0
FEATURE [App::DocumentObjectGroup] Group056  label="Bedroom 2 Closet"
  Group = -> [Panel130,Panel131,Panel132,Panel133,Panel138]
FEATURE [Part::Part2DObjectPython] Rectangle254  # Draft 2D object (typed FeaturePython)
  ChamferSize = 0
  FilletRadius = 0
  Height = 2200
  Length = -570
  MakeFace = true
  Placement = pos=(50007,13649.6,0) rot=(0,0,1;0rad)
FEATURE [Part::FeaturePython] Panel139  label="bed 2 closet conc base001"  # WARN: FeaturePython — macro-defined, semantics opaque (R4)
  Base = -> Rectangle254
  Length = 0
  MoveWithHost = false
  Placement = pos=(-42142,0.388761,3000) rot=(0,0,1;0rad)
  Role = 0
  Sheets = 1
  Thickness = 40
  Width = 0
FEATURE [Part::Part2DObjectPython] Rectangle255  # Draft 2D object (typed FeaturePython)
  ChamferSize = 0
  FilletRadius = 0
  Height = -570
  Length = -2760
  MakeFace = true
  Placement = pos=(49437,15849.6,40) rot=(0.57735,-0.57735,-0.57735;4.18879rad)
  Support = -> Panel133
FEATURE [Part::FeaturePython] Panel140  label="Panel139"  # WARN: FeaturePython — macro-defined, semantics opaque (R4)
  Base = -> Rectangle255
  Length = 0
  MoveWithHost = false
  Placement = pos=(-42142,-1664.61,3000) rot=(0,0,1;0rad)
  Role = 0
  Sheets = 1
  Thickness = 30
  Width = 0
FEATURE [Part::FeaturePython] Panel141  label="Panel140"  # WARN: FeaturePython — macro-defined, semantics opaque (R4)
  Base = -> Rectangle255
  Length = 0
  MoveWithHost = false
  Placement = pos=(-42142,-564.611,3000) rot=(0,0,1;0rad)
  Role = 0
  Sheets = 1
  Thickness = 30
  Width = 0
FEATURE [Part::Part2DObjectPython] Rectangle256  # Draft 2D object (typed FeaturePython)
  ChamferSize = 0
  FilletRadius = 0
  Height = 570
  Length = -535
  MakeFace = true
  Placement = pos=(50007,14184.6,1000) rot=(0,0,1;1.5708rad)
FEATURE [Part::FeaturePython] Panel142  label="Panel141"  # WARN: FeaturePython — macro-defined, semantics opaque (R4)
  Base = -> Rectangle256
  Length = 0
  MoveWithHost = false
  Placement = pos=(-42142,0.388761,3000) rot=(0,0,1;0rad)
  Role = 0
  Sheets = 1
  Thickness = 30
  Width = 0
FEATURE [Part::FeaturePython] Clone043  label="Clone of Panel141"  # Draft clone (typed FeaturePython)
  Objects = -> [Panel142]
  Placement = pos=(-42142,1665.39,3000) rot=(0,0,1;0rad)
  Scale = (1,1,1)
FEATURE [Part::FeaturePython] Clone044  label="Clone of Panel142"  # Draft clone (typed FeaturePython)
  Objects = -> [Panel142]
  Placement = pos=(-42142,0.377523,3990) rot=(0,0,1;0rad)
  Scale = (1,1,1)
FEATURE [Part::Feature] Clone045  label="Clone of Panel143"
  Placement = pos=(-42142,1665.39,3990) rot=(0,0,1;0rad)
  shape: bbox 570 x 535 x 30 mm, 6 faces (baked)
FEATURE [Part::Part2DObjectPython] Rectangle257  # Draft 2D object (typed FeaturePython)
  ChamferSize = 0
  FilletRadius = 0
  Height = 570
  Length = -1070
  MakeFace = true
  Placement = pos=(50007,15284.6,1500) rot=(0,0,1;1.5708rad)
FEATURE [Part::FeaturePython] Panel143  label="Panel142"  # WARN: FeaturePython — macro-defined, semantics opaque (R4)
  Base = -> Rectangle257
  Length = 0
  MoveWithHost = false
  Placement = pos=(-42142,0.388761,3000) rot=(0,0,1;0rad)
  Role = 0
  Sheets = 1
  Thickness = 30
  Width = 0
FEATURE [Part::FeaturePython] Panel144  label="Panel143"  # WARN: FeaturePython — macro-defined, semantics opaque (R4)
  Base = -> Rectangle257
  Length = 0
  MoveWithHost = false
  Placement = pos=(-42142,0.388761,3490) rot=(0,0,1;0rad)
  Role = 0
  Sheets = 1
  Thickness = 30
  Width = 0
FEATURE [Part::Feature] Clone046  label="Clone of Panel144"
  Placement = pos=(-42142,0.377523,3500) rot=(0,0,1;0rad)
  shape: bbox 570 x 535 x 30 mm, 6 faces (baked)
FEATURE [Part::Feature] Clone047  label="Clone of Panel145"
  Placement = pos=(-42142,1665.39,3500) rot=(0,0,1;0rad)
  shape: bbox 570 x 535 x 30 mm, 6 faces (baked)
FEATURE [App::DocumentObjectGroup] Group061  label="Bedroom 2 Closet001"
  Group = -> [Panel136,Panel135,Panel137,Panel134,Panel139,Panel140,Panel141,Panel142,Clone043,Clone044,Clone045,Panel143,Panel144,Clone046,Clone047]
FEATURE [Part::Part2DObjectPython] Rectangle258  # Draft 2D object (typed FeaturePython)
  ChamferSize = 0
  FilletRadius = 0
  Height = 2800
  Length = 550
  MakeFace = true
  Placement = pos=(50037,14199.6,0) rot=(0.57735,-0.57735,-0.57735;2.0944rad)
FEATURE [Part::Part2DObjectPython] Rectangle259  # Draft 2D object (typed FeaturePython)
  ChamferSize = 0
  FilletRadius = 0
  Height = 2800
  Length = 550
  MakeFace = true
  Placement = pos=(50037,14199.6,0) rot=(0.57735,-0.57735,-0.57735;2.0944rad)
FEATURE [Part::FeaturePython] Panel146  label="Panel201"  # WARN: FeaturePython — macro-defined, semantics opaque (R4)
  Base = -> Rectangle259
  Length = 0
  MoveWithHost = false
  Placement = pos=(-37138.2,31779.8,3000) rot=(0,0,-1;0.785399rad)
  Role = 0
  Sheets = 1
  Thickness = 30
  Width = 0
FEATURE [Part::FeaturePython] Panel147  label="Panel146"  # WARN: FeaturePython — macro-defined, semantics opaque (R4)
  Base = -> Rectangle259
  Length = 0
  MoveWithHost = false
  Placement = pos=(-17445.9,-38551.9,3000) rot=(0,0,1;0.785398rad)
  Role = 0
  Sheets = 1
  Thickness = 30
  Width = 0
FEATURE [Part::FeaturePython] Panel148  label="Panel147"  # WARN: FeaturePython — macro-defined, semantics opaque (R4)
  Base = -> Rectangle259
  Length = 0
  MoveWithHost = false
  Placement = pos=(-37138.2,33159.5,3000) rot=(0,0,-1;0.785398rad)
  Role = 0
  Sheets = 1
  Thickness = 30
  Width = 0
FEATURE [Part::FeaturePython] Panel149  label="Panel148"  # WARN: FeaturePython — macro-defined, semantics opaque (R4)
  Base = -> Rectangle259
  Length = 0
  MoveWithHost = false
  Placement = pos=(-17445.9,-37172.1,3000) rot=(0,0,1;0.785398rad)
  Role = 0
  Sheets = 1
  Thickness = 30
  Width = 0
FEATURE [Part::Part2DObjectPython] Rectangle260  # Draft 2D object (typed FeaturePython)
  ChamferSize = 0
  FilletRadius = 0
  Height = 2200
  Length = -570
  MakeFace = true
  Placement = pos=(50007,13649.6,0) rot=(0,0,1;0rad)
FEATURE [Part::FeaturePython] Panel150  label="bed 2 closet conc base002"  # WARN: FeaturePython — macro-defined, semantics opaque (R4)
  Base = -> Rectangle260
  Length = 0
  MoveWithHost = false
  Placement = pos=(-42142,-7599.61,3000) rot=(0,0,1;0rad)
  Role = 0
  Sheets = 1
  Thickness = 40
  Width = 0
FEATURE [Part::Part2DObjectPython] Rectangle261  # Draft 2D object (typed FeaturePython)
  ChamferSize = 0
  FilletRadius = 0
  Height = -570
  Length = -2760
  MakeFace = true
  Placement = pos=(49437,15849.6,40) rot=(0.57735,-0.57735,-0.57735;4.18879rad)
FEATURE [Part::FeaturePython] Panel151  label="Panel150"  # WARN: FeaturePython — macro-defined, semantics opaque (R4)
  Base = -> Rectangle261
  Length = 0
  MoveWithHost = false
  Placement = pos=(-42142,-9264.61,3000) rot=(0,0,1;0rad)
  Role = 0
  Sheets = 1
  Thickness = 30
  Width = 0
FEATURE [Part::FeaturePython] Panel152  label="Panel151"  # WARN: FeaturePython — macro-defined, semantics opaque (R4)
  Base = -> Rectangle261
  Length = 0
  MoveWithHost = false
  Placement = pos=(-42142,-8164.61,3000) rot=(0,0,1;0rad)
  Role = 0
  Sheets = 1
  Thickness = 30
  Width = 0
FEATURE [Part::Part2DObjectPython] Rectangle262  # Draft 2D object (typed FeaturePython)
  ChamferSize = 0
  FilletRadius = 0
  Height = 570
  Length = -535
  MakeFace = true
  Placement = pos=(50007,14184.6,1000) rot=(0,0,1;1.5708rad)
FEATURE [Part::FeaturePython] Panel153  label="Panel152"  # WARN: FeaturePython — macro-defined, semantics opaque (R4)
  Base = -> Rectangle262
  Length = 0
  MoveWithHost = false
  Placement = pos=(-42142,-7599.61,3000) rot=(0,0,1;0rad)
  Role = 0
  Sheets = 1
  Thickness = 30
  Width = 0
FEATURE [Part::FeaturePython] Clone048  label="Clone of Panel146"  # Draft clone (typed FeaturePython)
  Objects = -> [Panel153]
  Placement = pos=(-42142,-5934.61,3000) rot=(0,0,1;0rad)
  Scale = (1,1,1)
FEATURE [Part::FeaturePython] Clone049  label="Clone of Panel147"  # Draft clone (typed FeaturePython)
  Objects = -> [Panel153]
  Placement = pos=(-42142,-7599.62,3990) rot=(0,0,1;0rad)
  Scale = (1,1,1)
FEATURE [Part::Feature] Clone050  label="Clone of Panel148"
  Placement = pos=(-42142,-5934.61,3990) rot=(0,0,1;0rad)
  shape: bbox 570 x 535 x 30 mm, 6 faces (baked)
FEATURE [Part::Part2DObjectPython] Rectangle263  # Draft 2D object (typed FeaturePython)
  ChamferSize = 0
  FilletRadius = 0
  Height = 570
  Length = -1070
  MakeFace = true
  Placement = pos=(50007,15284.6,1500) rot=(0,0,1;1.5708rad)
FEATURE [Part::FeaturePython] Panel154  label="Panel153"  # WARN: FeaturePython — macro-defined, semantics opaque (R4)
  Base = -> Rectangle263
  Length = 0
  MoveWithHost = false
  Placement = pos=(-42142,-7599.61,3000) rot=(0,0,1;0rad)
  Role = 0
  Sheets = 1
  Thickness = 30
  Width = 0
FEATURE [Part::FeaturePython] Panel155  label="Panel154"  # WARN: FeaturePython — macro-defined, semantics opaque (R4)
  Base = -> Rectangle263
  Length = 0
  MoveWithHost = false
  Placement = pos=(-42142,-7599.61,3490) rot=(0,0,1;0rad)
  Role = 0
  Sheets = 1
  Thickness = 30
  Width = 0
FEATURE [Part::Feature] Clone051  label="Clone of Panel149"
  Placement = pos=(-42142,-7599.62,3500) rot=(0,0,1;0rad)
  shape: bbox 570 x 535 x 30 mm, 6 faces (baked)
FEATURE [Part::Feature] Clone052  label="Clone of Panel150"
  Placement = pos=(-42142,-5934.61,3500) rot=(0,0,1;0rad)
  shape: bbox 570 x 535 x 30 mm, 6 faces (baked)
FEATURE [App::DocumentObjectGroup] Group062  label="Bedroom 1 Closet001"
  Group = -> [Clone051,Clone050,Clone052,Panel147,Panel146,Panel148,Panel149,Panel154,Panel152,Panel150,Panel153,Clone048,Clone049,Panel155,Panel151]
FEATURE [Part::Part2DObjectPython] Rectangle264  # Draft 2D object (typed FeaturePython)
  ChamferSize = 0
  FilletRadius = 0
  Height = 2800
  Length = 550
  MakeFace = true
  Placement = pos=(50037,14199.6,0) rot=(0.57735,-0.57735,-0.57735;2.0944rad)
FEATURE [Part::FeaturePython] Panel156  label="Panel202"  # WARN: FeaturePython — macro-defined, semantics opaque (R4)
  Base = -> Rectangle264
  Length = 0
  MoveWithHost = false
  Placement = pos=(-42142,-7599.61,3000) rot=(0,0,1;0rad)
  Role = 0
  Sheets = 1
  Thickness = 30
  Width = 0
FEATURE [Part::FeaturePython] Panel157  label="Panel203"  # WARN: FeaturePython — macro-defined, semantics opaque (R4)
  Base = -> Rectangle264
  Length = 0
  MoveWithHost = false
  Placement = pos=(-42142,-7049.61,3000) rot=(0,0,1;0rad)
  Role = 0
  Sheets = 1
  Thickness = 30
  Width = 0
FEATURE [Part::FeaturePython] Panel158  label="Panel204"  # WARN: FeaturePython — macro-defined, semantics opaque (R4)
  Base = -> Rectangle264
  Length = 0
  MoveWithHost = false
  Placement = pos=(-42142,-6499.61,3000) rot=(0,0,1;0rad)
  Role = 0
  Sheets = 1
  Thickness = 30
  Width = 0
FEATURE [Part::FeaturePython] Panel159  label="Panel158"  # WARN: FeaturePython — macro-defined, semantics opaque (R4)
  Base = -> Rectangle264
  Length = 0
  MoveWithHost = false
  Placement = pos=(-42142,-5949.61,3000) rot=(0,0,1;0rad)
  Role = 0
  Sheets = 1
  Thickness = 30
  Width = 0
FEATURE [Part::Part2DObjectPython] Rectangle265  # Draft 2D object (typed FeaturePython)
  ChamferSize = 0
  FilletRadius = 0
  Height = 2200
  Length = -570
  MakeFace = true
  Placement = pos=(50007,13649.6,0) rot=(0,0,1;0rad)
FEATURE [Part::FeaturePython] Panel160  label="bed 2 closet conc base003"  # WARN: FeaturePython — macro-defined, semantics opaque (R4)
  Base = -> Rectangle265
  Length = 0
  MoveWithHost = false
  Placement = pos=(-42142,-7599.61,3000) rot=(0,0,1;0rad)
  Role = 0
  Sheets = 1
  Thickness = 40
  Width = 0
FEATURE [App::DocumentObjectGroup] Group057  label="Bedroom 1 Closet"
  Group = -> [Panel156,Panel158,Panel160,Panel159,Panel157]
FEATURE [Part::Part2DObjectPython] Rectangle267  # Draft 2D object (typed FeaturePython)
  ChamferSize = 0
  FilletRadius = 0
  Height = -150
  Length = -150
  MakeFace = true
  Placement = pos=(47487,4099.61,7e-12) rot=(0,0,1;0rad)
FEATURE [Part::FeaturePython] Structure040  # WARN: FeaturePython — macro-defined, semantics opaque (R4)
  Base = -> Rectangle267
  Height = 2800
  Length = 0
  MoveWithHost = false
  Nodes = (2) [(47412,4024.61,7.27596e-12),(47412,4024.61,2800)]
  Normal = (0,0,0)
  Placement = pos=(-42142,0.388761,3000) rot=(0,0,1;0rad)
  Role = 0
  Width = 100
FEATURE [Part::Part2DObjectPython] Rectangle269  # Draft 2D object (typed FeaturePython)
  ChamferSize = 0
  FilletRadius = 0
  Height = 450
  Length = -2800
  MakeFace = true
  Placement = pos=(47337,2149.61,2800) rot=(0,-1,0;1.5708rad)
FEATURE [Part::FeaturePython] Panel161  label="Panel205"  # WARN: FeaturePython — macro-defined, semantics opaque (R4)
  Base = -> Rectangle269
  Length = 0
  MoveWithHost = false
  Placement = pos=(-42112,0.388761,3000) rot=(0,0,1;0rad)
  Role = 0
  Sheets = 1
  Thickness = 30
  Width = 0
FEATURE [Part::FeaturePython] Panel162  label="Panel206"  # WARN: FeaturePython — macro-defined, semantics opaque (R4)
  Base = -> Rectangle269
  Length = 0
  MoveWithHost = false
  Placement = pos=(-42112,450.389,3000) rot=(0,0,1;0rad)
  Role = 0
  Sheets = 1
  Thickness = 30
  Width = 0
FEATURE [Part::FeaturePython] Panel163  label="Panel207"  # WARN: FeaturePython — macro-defined, semantics opaque (R4)
  Base = -> Rectangle269
  Length = 0
  MoveWithHost = false
  Placement = pos=(-42112,1350.39,3000) rot=(0,0,1;0rad)
  Role = 0
  Sheets = 1
  Thickness = 30
  Width = 0
FEATURE [Part::FeaturePython] Panel164  label="Panel208"  # WARN: FeaturePython — macro-defined, semantics opaque (R4)
  Base = -> Rectangle269
  Length = 0
  MoveWithHost = false
  Placement = pos=(-42112,900.389,3000) rot=(0,0,1;0rad)
  Role = 0
  Sheets = 1
  Thickness = 30
  Width = 0
FEATURE [Part::FeaturePython] Panel165  label="Panel209"  # WARN: FeaturePython — macro-defined, semantics opaque (R4)
  Base = -> Rectangle269
  Length = 0
  MoveWithHost = false
  Placement = pos=(-42112,1950.39,3000) rot=(0,0,1;0rad)
  Role = 0
  Sheets = 1
  Thickness = 30
  Width = 0
FEATURE [Part::FeaturePython] Panel166  label="Panel210"  # WARN: FeaturePython — macro-defined, semantics opaque (R4)
  Base = -> Rectangle269
  Length = 0
  MoveWithHost = false
  Placement = pos=(-42112,2400.39,3000) rot=(0,0,1;0rad)
  Role = 0
  Sheets = 1
  Thickness = 30
  Width = 0
FEATURE [Part::FeaturePython] Panel167  label="Panel211"  # WARN: FeaturePython — macro-defined, semantics opaque (R4)
  Base = -> Rectangle269
  Length = 0
  MoveWithHost = false
  Placement = pos=(-42112,2850.39,3000) rot=(0,0,1;0rad)
  Role = 0
  Sheets = 1
  Thickness = 30
  Width = 0
FEATURE [Part::FeaturePython] Panel168  label="Panel212"  # WARN: FeaturePython — macro-defined, semantics opaque (R4)
  Base = -> Rectangle269
  Length = 0
  MoveWithHost = false
  Placement = pos=(-42112,3300.39,3000) rot=(0,0,1;0rad)
  Role = 0
  Sheets = 1
  Thickness = 30
  Width = 0
FEATURE [Part::Part2DObjectPython] DWire223  # Draft 2D object (typed FeaturePython)
  ChamferSize = 0
  Closed = true
  End = (47937,5899.61,0)
  FilletRadius = 0
  Length = 8880
  MakeFace = true
  Points = (8) [(47367,5899.61,4.54747e-13),(47367,4099.61,7.27596e-12),(47487,4099.61,7.27596e-12),(47487,3949.61,7.27596e-12),(47367,3949.61,4.54747e-13),+3 more]
  Start = (47367,5899.61,0)
FEATURE [Part::FeaturePython] Panel169  label="masterbedroom closet base"  # WARN: FeaturePython — macro-defined, semantics opaque (R4)
  Base = -> DWire223
  Length = 0
  MoveWithHost = false
  Placement = pos=(-42142,0.388761,3000) rot=(0,0,1;0rad)
  Role = 0
  Sheets = 1
  Thickness = 40
  Width = 0
FEATURE [Part::Part2DObjectPython] Rectangle270  # Draft 2D object (typed FeaturePython)
  ChamferSize = 0
  FilletRadius = 0
  Height = 2760
  Length = -450
  MakeFace = true
  Placement = pos=(47937,3949.61,40) rot=(1,0,0;1.5708rad)
FEATURE [Part::FeaturePython] Panel170  label="Panel divider"  # WARN: FeaturePython — macro-defined, semantics opaque (R4)
  Base = -> Rectangle270
  Length = 0
  MoveWithHost = false
  Placement = pos=(-42142,105.389,3000) rot=(0,0,1;0rad)
  Role = 0
  Sheets = 1
  Thickness = 60
  Width = 0
FEATURE [App::DocumentObjectGroup] Group058  label="Masterbedroom Closet"
  Group = -> [Structure040,Panel161,Panel162,Panel163,Panel164,Panel165,Panel166,Panel167,Panel168,Panel169,Panel170]
FEATURE [Part::Part2DObjectPython] Rectangle271  # Draft 2D object (typed FeaturePython)
  ChamferSize = 0
  FilletRadius = 0
  Height = -150
  Length = -150
  MakeFace = true
  Placement = pos=(47487,4099.61,7e-12) rot=(0,0,1;0rad)
FEATURE [Part::FeaturePython] Structure041  # WARN: FeaturePython — macro-defined, semantics opaque (R4)
  Base = -> Rectangle271
  Height = 2800
  Length = 0
  MoveWithHost = false
  Nodes = (2) [(47412,4024.61,7.27596e-12),(47412,4024.61,2800)]
  Normal = (0,0,0)
  Placement = pos=(-42142,0.388761,3000) rot=(0,0,1;0rad)
  Role = 0
  Width = 100
FEATURE [Part::Part2DObjectPython] Rectangle272  # Draft 2D object (typed FeaturePython)
  ChamferSize = 0
  FilletRadius = 0
  Height = 450
  Length = -2800
  MakeFace = true
  Placement = pos=(47337,2149.61,2800) rot=(0,-1,0;1.5708rad)
FEATURE [Part::FeaturePython] Panel171  label="Panel213"  # WARN: FeaturePython — macro-defined, semantics opaque (R4)
  Base = -> Rectangle272
  Length = 0
  MoveWithHost = false
  Placement = pos=(-26736.1,-32821.1,3000) rot=(0,0,1;0.785398rad)
  Role = 0
  Sheets = 1
  Thickness = 30
  Width = 0
FEATURE [Part::FeaturePython] Panel172  label="Panel214"  # WARN: FeaturePython — macro-defined, semantics opaque (R4)
  Base = -> Rectangle272
  Length = 0
  MoveWithHost = false
  Placement = pos=(-30094.3,34441.7,3000) rot=(0,0,-1;0.785398rad)
  Role = 0
  Sheets = 1
  Thickness = 30
  Width = 0
FEATURE [Part::FeaturePython] Panel173  label="Panel215"  # WARN: FeaturePython — macro-defined, semantics opaque (R4)
  Base = -> Rectangle272
  Length = 0
  MoveWithHost = false
  Placement = pos=(-30094.3,35562.9,3000) rot=(0,0,-1;0.785398rad)
  Role = 0
  Sheets = 1
  Thickness = 30
  Width = 0
FEATURE [Part::FeaturePython] Panel174  label="Panel216"  # WARN: FeaturePython — macro-defined, semantics opaque (R4)
  Base = -> Rectangle272
  Length = 0
  MoveWithHost = false
  Placement = pos=(-26736.1,-31699.9,3000) rot=(0,0,1;0.785398rad)
  Role = 0
  Sheets = 1
  Thickness = 30
  Width = 0
FEATURE [Part::FeaturePython] Panel175  label="Panel217"  # WARN: FeaturePython — macro-defined, semantics opaque (R4)
  Base = -> Rectangle272
  Length = 0
  MoveWithHost = false
  Placement = pos=(-26736.1,-30871.1,3000) rot=(0,0,1;0.785398rad)
  Role = 0
  Sheets = 1
  Thickness = 30
  Width = 0
FEATURE [Part::FeaturePython] Panel176  label="Panel218"  # WARN: FeaturePython — macro-defined, semantics opaque (R4)
  Base = -> Rectangle272
  Length = 0
  MoveWithHost = false
  Placement = pos=(-30094.3,36391.7,3000) rot=(0,0,-1;0.785398rad)
  Role = 0
  Sheets = 1
  Thickness = 30
  Width = 0
FEATURE [Part::FeaturePython] Panel177  label="Panel219"  # WARN: FeaturePython — macro-defined, semantics opaque (R4)
  Base = -> Rectangle272
  Length = 0
  MoveWithHost = false
  Placement = pos=(-26736.1,-29749.9,3000) rot=(0,0,1;0.785398rad)
  Role = 0
  Sheets = 1
  Thickness = 30
  Width = 0
FEATURE [Part::FeaturePython] Panel178  label="Panel220"  # WARN: FeaturePython — macro-defined, semantics opaque (R4)
  Base = -> Rectangle272
  Length = 0
  MoveWithHost = false
  Placement = pos=(-30094.3,37512.9,3000) rot=(0,0,-1;0.785398rad)
  Role = 0
  Sheets = 1
  Thickness = 30
  Width = 0
FEATURE [Part::Part2DObjectPython] DWire224  # Draft 2D object (typed FeaturePython)
  ChamferSize = 0
  Closed = true
  End = (47937,5899.61,0)
  FilletRadius = 0
  Length = 8880
  MakeFace = true
  Points = (8) [(47367,5899.61,4.54747e-13),(47367,4099.61,7.27596e-12),(47487,4099.61,7.27596e-12),(47487,3949.61,7.27596e-12),(47367,3949.61,4.54747e-13),+3 more]
  Start = (47367,5899.61,0)
FEATURE [Part::FeaturePython] Panel179  label="masterbedroom closet base001"  # WARN: FeaturePython — macro-defined, semantics opaque (R4)
  Base = -> DWire224
  Length = 0
  MoveWithHost = false
  Placement = pos=(-42142,0.388761,3000) rot=(0,0,1;0rad)
  Role = 0
  Sheets = 1
  Thickness = 40
  Width = 0
FEATURE [Part::Part2DObjectPython] Rectangle273  # Draft 2D object (typed FeaturePython)
  ChamferSize = 0
  FilletRadius = 0
  Height = 2760
  Length = -450
  MakeFace = true
  Placement = pos=(47937,3949.61,40) rot=(1,0,0;1.5708rad)
FEATURE [Part::FeaturePython] Panel180  label="Panel divider001"  # WARN: FeaturePython — macro-defined, semantics opaque (R4)
  Base = -> Rectangle273
  Length = 0
  MoveWithHost = false
  Placement = pos=(-42142,105.389,3000) rot=(0,0,1;0rad)
  Role = 0
  Sheets = 1
  Thickness = 60
  Width = 0
FEATURE [App::DocumentObjectGroup] Group063  label="Masterbedroom Closet001"
  Group = -> [Panel174,Structure041,Panel171,Panel172,Panel176,Panel177,Panel179,Panel180,Panel175,Panel178,Panel173]
FEATURE [Part::Part2DObjectPython] Line780  # Draft 2D object (typed FeaturePython)
  ChamferSize = 0
  Closed = false
  End = (27998.4,2149.61,0)
  FilletRadius = 0
  Length = 2350
  MakeFace = true
  Points = (2) [(27998.4,4499.61,0),(27998.4,2149.61,0)]
  Start = (27998.4,4499.61,0)
FEATURE [Part::Part2DObjectPython] Rectangle284  # Draft 2D object (typed FeaturePython)
  ChamferSize = 0
  FilletRadius = 0
  Height = -150
  Length = -150
  MakeFace = true
  Placement = pos=(28148.4,3399.61,0) rot=(0,0,1;0rad)
FEATURE [Part::FeaturePython] Structure042  # WARN: FeaturePython — macro-defined, semantics opaque (R4)
  Base = -> Rectangle284
  Height = 2800
  Length = 0
  MoveWithHost = false
  Nodes = (2) [(47412,4024.61,7.27596e-12),(47412,4024.61,2800)]
  Normal = (0,0,0)
  Placement = pos=(-25503.4,0.388456,0) rot=(0,0,1;0rad)
  Role = 0
  Width = 100
FEATURE [Part::Part2DObjectPython] Line781  # Draft 2D object (typed FeaturePython)
  ChamferSize = 0
  Closed = false
  End = (28598.4,3324.61,0)
  FilletRadius = 0
  Length = 599.966
  MakeFace = true
  Points = (2) [(27998.4,3324.61,0),(28598.4,3324.61,0)]
  Start = (27998.4,3324.61,0)
FEATURE [Part::Part2DObjectPython] Rectangle295  # Draft 2D object (typed FeaturePython)
  ChamferSize = 0
  FilletRadius = 0
  Height = -2800
  Length = 1100
  MakeFace = true
  Placement = pos=(27998.4,3249.61,2800) rot=(0.57735,-0.57735,-0.57735;2.0944rad)
FEATURE [Part::Part2DObjectPython] Line782  # Draft 2D object (typed FeaturePython)
  ChamferSize = 0
  Closed = false
  End = (27998.4,2699.61,0)
  FilletRadius = 0
  Length = 2800
  MakeFace = true
  Points = (2) [(27998.4,2699.61,2800),(27998.4,2699.61,0)]
  Start = (27998.4,2699.61,2800)
  Support = -> Rectangle295
FEATURE [Part::Part2DObjectPython] Line783  # Draft 2D object (typed FeaturePython)
  ChamferSize = 0
  Closed = false
  End = (27998.4,2149.61,1400)
  FilletRadius = 0
  Length = 550
  MakeFace = true
  Points = (2) [(27998.4,2699.61,1400),(27998.4,2149.61,1400)]
  Start = (27998.4,2699.61,1400)
FEATURE [Part::Part2DObjectPython] Line784  # Draft 2D object (typed FeaturePython)
  ChamferSize = 0
  Closed = false
  End = (27998.4,2424.61,0)
  FilletRadius = 0
  Length = 1400
  MakeFace = true
  Points = (2) [(27998.4,2424.61,1400),(27998.4,2424.61,0)]
  Start = (27998.4,2424.61,1400)
FEATURE [Part::Part2DObjectPython] Line785  # Draft 2D object (typed FeaturePython)
  ChamferSize = 0
  Closed = false
  End = (27998.4,2974.61,0)
  FilletRadius = 0
  Length = 1400
  MakeFace = true
  Placement = pos=(0.000691675,550,0) rot=(0,0,1;0rad)
  Points = (2) [(27998.4,2424.61,1400),(27998.4,2424.61,0)]
  Start = (27998.4,2974.61,1400)
FEATURE [Part::Part2DObjectPython] Line786  # Draft 2D object (typed FeaturePython)
  ChamferSize = 0
  Closed = false
  End = (27998.4,2699.61,1400)
  FilletRadius = 0
  Length = 550
  MakeFace = true
  Placement = pos=(0.000691675,550,0) rot=(0,0,1;0rad)
  Points = (2) [(27998.4,2699.61,1400),(27998.4,2149.61,1400)]
  Start = (27998.4,3249.61,1400)
FEATURE [Part::Part2DObjectPython] Rectangle296  # Draft 2D object (typed FeaturePython)
  ChamferSize = 0
  FilletRadius = 0
  Height = 275
  Length = 2800
  MakeFace = true
  Placement = pos=(27998.4,3249.61,2800) rot=(0.707107,0,-0.707107;3.14159rad)
FEATURE [Part::FeaturePython] Panel181  label="Panel221"  # WARN: FeaturePython — macro-defined, semantics opaque (R4)
  Base = -> Rectangle296
  Length = 0
  MoveWithHost = false
  Placement = pos=(-25473.4,0.388456,0) rot=(0,0,1;0rad)
  Role = 0
  Sheets = 1
  Thickness = 30
  Width = 0
FEATURE [Part::FeaturePython] Panel182  label="Panel222"  # WARN: FeaturePython — macro-defined, semantics opaque (R4)
  Base = -> Rectangle296
  Length = 0
  MoveWithHost = false
  Placement = pos=(-25473.4,-274.611,0) rot=(0,0,1;0rad)
  Role = 0
  Sheets = 1
  Thickness = 30
  Width = 0
FEATURE [Part::FeaturePython] Panel183  label="Panel223"  # WARN: FeaturePython — macro-defined, semantics opaque (R4)
  Base = -> Rectangle296
  Length = 0
  MoveWithHost = false
  Placement = pos=(-25473.4,-549.611,0) rot=(0,0,1;0rad)
  Role = 0
  Sheets = 1
  Thickness = 30
  Width = 0
FEATURE [Part::FeaturePython] Panel184  label="Panel224"  # WARN: FeaturePython — macro-defined, semantics opaque (R4)
  Base = -> Rectangle296
  Length = 0
  MoveWithHost = false
  Placement = pos=(-25473.4,-824.611,0) rot=(0,0,1;0rad)
  Role = 0
  Sheets = 1
  Thickness = 30
  Width = 0
FEATURE [Part::FeaturePython] Panel185  label="Panel225"  # WARN: FeaturePython — macro-defined, semantics opaque (R4)
  Base = -> Rectangle296
  Length = 0
  MoveWithHost = false
  Placement = pos=(-25473.4,1250.39,0) rot=(0,0,1;0rad)
  Role = 0
  Sheets = 1
  Thickness = 30
  Width = 0
FEATURE [Part::FeaturePython] Panel186  label="Panel226"  # WARN: FeaturePython — macro-defined, semantics opaque (R4)
  Base = -> Rectangle296
  Length = 0
  MoveWithHost = false
  Placement = pos=(-25473.4,975.388,0) rot=(0,0,1;0rad)
  Role = 0
  Sheets = 1
  Thickness = 30
  Width = 0
FEATURE [Part::FeaturePython] Panel187  label="Panel227"  # WARN: FeaturePython — macro-defined, semantics opaque (R4)
  Base = -> Rectangle296
  Length = 0
  MoveWithHost = false
  Placement = pos=(-25473.4,700.388,0) rot=(0,0,1;0rad)
  Role = 0
  Sheets = 1
  Thickness = 30
  Width = 0
FEATURE [Part::FeaturePython] Panel188  label="Panel228"  # WARN: FeaturePython — macro-defined, semantics opaque (R4)
  Base = -> Rectangle296
  Length = 0
  MoveWithHost = false
  Placement = pos=(-25473.4,425.388,0) rot=(0,0,1;0rad)
  Role = 0
  Sheets = 1
  Thickness = 30
  Width = 0
FEATURE [Part::Part2DObjectPython] Rectangle306  # Draft 2D object (typed FeaturePython)
  ChamferSize = 0
  FilletRadius = 0
  Height = -150
  Length = -150
  MakeFace = true
  Placement = pos=(28148.4,3399.61,0) rot=(0,0,1;0rad)
FEATURE [Part::FeaturePython] Structure043  # WARN: FeaturePython — macro-defined, semantics opaque (R4)
  Base = -> Rectangle306
  Height = 2800
  Length = 0
  MoveWithHost = false
  Nodes = (2) [(47412,4024.61,7.27596e-12),(47412,4024.61,2800)]
  Normal = (0,0,0)
  Placement = pos=(-25503.4,0.388456,0) rot=(0,0,1;0rad)
  Role = 0
  Width = 100
FEATURE [Part::Part2DObjectPython] Rectangle307  # Draft 2D object (typed FeaturePython)
  ChamferSize = 0
  FilletRadius = 0
  Height = 275
  Length = 2800
  MakeFace = true
  Placement = pos=(27998.4,3249.61,2800) rot=(0.707107,0,-0.707107;3.14159rad)
FEATURE [Part::FeaturePython] Panel189  label="Panel229"  # WARN: FeaturePython — macro-defined, semantics opaque (R4)
  Base = -> Rectangle307
  Length = 0
  MoveWithHost = false
  Placement = pos=(-19579.4,20728.8,0) rot=(0,0,-1;0.785398rad)
  Role = 0
  Sheets = 1
  Thickness = 30
  Width = 0
FEATURE [Part::FeaturePython] Panel190  label="Panel230"  # WARN: FeaturePython — macro-defined, semantics opaque (R4)
  Base = -> Rectangle307
  Length = 0
  MoveWithHost = false
  Placement = pos=(-15178.3,-19061.4,0) rot=(0,0,1;0.785398rad)
  Role = 0
  Sheets = 1
  Thickness = 30
  Width = 0
FEATURE [Part::FeaturePython] Panel191  label="Panel231"  # WARN: FeaturePython — macro-defined, semantics opaque (R4)
  Base = -> Rectangle307
  Length = 0
  MoveWithHost = false
  Placement = pos=(-19579.4,20060.2,0) rot=(0,0,-1;0.785398rad)
  Role = 0
  Sheets = 1
  Thickness = 30
  Width = 0
FEATURE [Part::FeaturePython] Panel192  label="Panel232"  # WARN: FeaturePython — macro-defined, semantics opaque (R4)
  Base = -> Rectangle307
  Length = 0
  MoveWithHost = false
  Placement = pos=(-15178.3,-19730,0) rot=(0,0,1;0.785398rad)
  Role = 0
  Sheets = 1
  Thickness = 30
  Width = 0
FEATURE [Part::FeaturePython] Panel193  label="Panel233"  # WARN: FeaturePython — macro-defined, semantics opaque (R4)
  Base = -> Rectangle307
  Length = 0
  MoveWithHost = false
  Placement = pos=(-19561.2,22001.9,0) rot=(0,0,-1;0.786442rad)
  Role = 0
  Sheets = 1
  Thickness = 30
  Width = 0
FEATURE [Part::FeaturePython] Panel194  label="Panel234"  # WARN: FeaturePython — macro-defined, semantics opaque (R4)
  Base = -> Rectangle307
  Length = 0
  MoveWithHost = false
  Placement = pos=(-15178.5,-17811.2,0) rot=(0,0,1;0.785398rad)
  Role = 0
  Sheets = 1
  Thickness = 30
  Width = 0
FEATURE [Part::FeaturePython] Panel195  label="Panel235"  # WARN: FeaturePython — macro-defined, semantics opaque (R4)
  Base = -> Rectangle307
  Length = 0
  MoveWithHost = false
  Placement = pos=(-19579.4,21310.2,0) rot=(0,0,-1;0.785398rad)
  Role = 0
  Sheets = 1
  Thickness = 30
  Width = 0
FEATURE [Part::FeaturePython] Panel196  label="Panel236"  # WARN: FeaturePython — macro-defined, semantics opaque (R4)
  Base = -> Rectangle307
  Length = 0
  MoveWithHost = false
  Placement = pos=(-15178.2,-18480,0) rot=(0,0,1;0.785399rad)
  Role = 0
  Sheets = 1
  Thickness = 30
  Width = 0
FEATURE [Part::Part2DObjectPython] DWire225  # Draft 2D object (typed FeaturePython)
  ChamferSize = 0
  Closed = true
  End = (28598.4,2149.61,0)
  FilletRadius = 0
  Length = 6079.93
  MakeFace = true
  Points = (8) [(28028.4,2149.61,9.09495e-13),(28028.4,3249.61,9.09495e-13),(28148.4,3249.61,0),(28148.4,3399.61,0),(28028.4,3399.61,9.09495e-13),(28028.4,4499.61,0),+2 more]
  Start = (28028.4,2149.61,1e-12)
FEATURE [Part::FeaturePython] Panel197  label="Panel237"  # WARN: FeaturePython — macro-defined, semantics opaque (R4)
  Base = -> DWire225
  Length = 0
  MoveWithHost = false
  Placement = pos=(-25503.4,0.388456,0) rot=(0,0,1;0rad)
  Role = 0
  Sheets = 1
  Thickness = 40
  Width = 0
FEATURE [App::DocumentObjectGroup] Group059  label="Guestbedroom Closet"
  Group = -> [Panel181,Panel182,Panel183,Panel184,Panel185,Panel186,Panel187,Panel188,Structure042,Panel197]
FEATURE [App::DocumentObjectGroup] Group055  label="Closed - Elevation View"
  Group = -> [Group056,Group057,Group058,Group059]
FEATURE [Part::Part2DObjectPython] DWire226  # Draft 2D object (typed FeaturePython)
  ChamferSize = 0
  Closed = true
  End = (28598.4,2149.61,0)
  FilletRadius = 0
  Length = 6079.93
  MakeFace = true
  Points = (8) [(28028.4,2149.61,9.09495e-13),(28028.4,3249.61,9.09495e-13),(28148.4,3249.61,0),(28148.4,3399.61,0),(28028.4,3399.61,9.09495e-13),(28028.4,4499.61,0),+2 more]
  Start = (28028.4,2149.61,1e-12)
FEATURE [Part::FeaturePython] Panel198  label="Panel238"  # WARN: FeaturePython — macro-defined, semantics opaque (R4)
  Base = -> DWire226
  Length = 0
  MoveWithHost = false
  Placement = pos=(-25503.4,0.388456,0) rot=(0,0,1;0rad)
  Role = 0
  Sheets = 1
  Thickness = 40
  Width = 0
FEATURE [App::DocumentObjectGroup] Group060  label="Guestbedroom Closet001"
  Group = -> [Panel193,Panel195,Panel190,Panel196,Panel191,Panel189,Panel194,Panel192,Structure043,Panel198]
FEATURE [App::DocumentObjectGroup] Group054  label="Open - Plan View"
  Group = -> [Group063,Group062,Group061,Group060]
FEATURE [App::DocumentObjectGroup] Group053  label="Closet"
  Group = -> [Group054,Group055]
FEATURE [Part::Part2DObjectPython] Rectangle311  # Draft 2D object (typed FeaturePython)
  ChamferSize = 0
  FilletRadius = 0
  Height = 900
  Length = 1950
  MakeFace = true
  Placement = pos=(37618,10442,760) rot=(0,0,1;0rad)
FEATURE [Part::Feature] Solid060  label="table legs001"
  Placement = pos=(-30023,-278.569,0) rot=(0,0,1;0rad)
  shape: bbox 100 x 100 x 760 mm, 6 faces (baked)
FEATURE [Part::Feature] Solid061  label="table legs002"
  Placement = pos=(-30023,521.431,0) rot=(0,0,1;0rad)
  shape: bbox 100 x 100 x 760 mm, 6 faces (baked)
FEATURE [Part::Feature] Solid062  label="table legs003"
  Placement = pos=(-31873,-278.569,0) rot=(0,0,1;0rad)
  shape: bbox 100 x 100 x 760 mm, 6 faces (baked)
FEATURE [Part::Feature] Solid063  label="table legs004"
  Placement = pos=(-31873,521.431,0) rot=(0,0,1;0rad)
  shape: bbox 100 x 100 x 760 mm, 6 faces (baked)
FEATURE [Part::FeaturePython] Panel199  label="Panel239"  # WARN: FeaturePython — macro-defined, semantics opaque (R4)
  Base = -> Rectangle311
  Length = 0
  MoveWithHost = false
  Placement = pos=(-29698,729.431,0) rot=(0,0,1;0rad)
  Role = 0
  Sheets = 1
  Thickness = 50
  Width = 0
FEATURE [Part::Feature] Solid067
  Placement = pos=(-29773,729.431,660) rot=(0,0,1;0rad)
  shape: bbox 50 x 700 x 100 mm, 6 faces (baked)
FEATURE [Part::Feature] Solid068
  Placement = pos=(-31623,729.431,660) rot=(0,0,1;0rad)
  shape: bbox 50 x 700 x 100 mm, 6 faces (baked)
FEATURE [Part::Feature] Solid073
  Placement = pos=(-29698,654.431,660) rot=(0,0,1;0rad)
  shape: bbox 1750 x 50 x 100 mm, 6 faces (baked)
FEATURE [Part::Feature] Solid074
  Placement = pos=(-29698,-145.569,660) rot=(0,0,1;0rad)
  shape: bbox 1750 x 50 x 100 mm, 6 faces (baked)
FEATURE [App::DocumentObjectGroup] Group068  label="1.95m x 0.9m Table"
  Group = -> [Solid062,Solid074,Panel199,Solid060,Solid067,Solid063,Solid073,Solid061,Solid068]
FEATURE [App::DocumentObjectGroup] Group066  label="Dinning Table"
  Group = -> [Group068]
FEATURE [App::DocumentObjectGroup] Group065  label="Table"
  Group = -> [Group066]
FEATURE [Part::Part2DObjectPython] Rectangle313  # Draft 2D object (typed FeaturePython)
  ChamferSize = 0
  FilletRadius = 0
  Height = -150
  Length = 0
  MakeFace = true
  Placement = pos=(36498.4,6249.61,0) rot=(0.57735,0.57735,0.57735;4.18879rad)
FEATURE [Part::Feature] Generic___Chair
  Placement = pos=(8895,12274.6,3e-12) rot=(0,0,1;0rad)
  shape: bbox 355.6 x 406.4 x 736.6 mm, 58 faces, 9 solids (baked)
FEATURE [Part::Feature] Face053
  shape: bbox 20 x 20 x 2e-07 mm, 1 faces, 0 solids (baked)
FEATURE [Part::Feature] Face054
  shape: bbox 20 x 64.94 x 64.94 mm, 1 faces, 0 solids (baked)
FEATURE [Part::Feature] Face055
  shape: bbox 20 x 100 x 20 mm, 1 faces, 0 solids (baked)
FEATURE [Part::Feature] Face056
  shape: bbox 20 x 64.94 x 64.94 mm, 1 faces, 0 solids (baked)
FEATURE [Part::Feature] Face057
  shape: bbox 20 x 20 x 100 mm, 1 faces, 0 solids (baked)
FEATURE [Part::Feature] Face058
  shape: bbox 20 x 20 x 2e-07 mm, 1 faces, 0 solids (baked)
FEATURE [Part::MultiFuse] Fusion006
  Shapes = -> [Face053,Face055,Face058,Face056,Face057,Face054]
FEATURE [App::DocumentObjectGroup] Group069  label="Sink"
  Group = -> [Fusion006,Extrusion067,Panel050,Fusion003]
FEATURE [App::DocumentObjectGroup] Group049  label="Base Cabinet"
  Group = -> [Panel042,Panel044,Panel045,Panel049,Panel041,Extrusion066,Panel076,Panel078,Panel088,Panel090,Panel091,Panel092,Panel093,Panel094,Panel095,Panel099,Panel101,Panel104,Panel106,Panel107,Panel108,Panel109,Panel110,Panel111,Panel112,Panel113,Panel124,Extrusion090,Solid016,Extrusion084,Solid014,Extrusion078,Solid013,Extrusion077,Solid012,Extrusion076,Solid011,Extrusion072,Solid008,Solid048,Group069]
FEATURE [App::DocumentObjectGroup] Group048  label="Kitchen Cabinets"
  Group = -> [Group049,Group050,Group051]
FEATURE [Part::Part2DObjectPython] Rectangle314  # Draft 2D object (typed FeaturePython)
  ChamferSize = 0
  FilletRadius = 0
  Height = 700
  Length = 1750
  MakeFace = true
  Placement = pos=(33523.4,11271,0) rot=(0,0,1;0rad)
FEATURE [Part::Part2DObjectPython] Rectangle315  # Draft 2D object (typed FeaturePython)
  ChamferSize = 0
  FilletRadius = 0
  Height = 406.4
  Length = 355.6
  MakeFace = true
  Placement = pos=(34220.6,12071,0) rot=(0,0,1;0rad)
FEATURE [Part::Part2DObjectPython] Line788  # Draft 2D object (typed FeaturePython)
  ChamferSize = 0
  Closed = false
  End = (33523.4,12071,0)
  FilletRadius = 0
  Length = 1750
  MakeFace = true
  Placement = pos=(-4194.62,729.043,0) rot=(0,0,1;0rad)
  Points = (2) [(39468,11342,-1.13687e-13),(37718,11342,-1.13687e-13)]
  Start = (35273.4,12071,0)
FEATURE [Part::Part2DObjectPython] Line789  # Draft 2D object (typed FeaturePython)
  ChamferSize = 0
  Closed = false
  End = (35273.4,12274.2,0)
  FilletRadius = 0
  Length = 697.2
  MakeFace = true
  Placement = pos=(-4194.62,729.043,0) rot=(0,0,1;0rad)
  Points = (2) [(38770.8,11545.2,-1.13687e-13),(39468,11545.2,-1.13687e-13)]
  Start = (34576.2,12274.2,0)
FEATURE [Part::Part2DObjectPython] Line790  # Draft 2D object (typed FeaturePython)
  ChamferSize = 0
  Closed = false
  End = (34924.8,12071,0)
  FilletRadius = 0
  Length = 203.2
  MakeFace = true
  Placement = pos=(-4194.62,729.043,0) rot=(0,0,1;0rad)
  Points = (2) [(39119.4,11545.2,-1.13687e-13),(39119.4,11342,-1.13687e-13)]
  Start = (34924.8,12274.2,0)
FEATURE [Part::Part2DObjectPython] Rectangle318  # Draft 2D object (typed FeaturePython)
  ChamferSize = 0
  FilletRadius = 0
  Height = 406.4
  Length = 355.6
  MakeFace = true
  Placement = pos=(34747,12071,0) rot=(0,0,1;0rad)
FEATURE [Part::Part2DObjectPython] Rectangle319  # Draft 2D object (typed FeaturePython)
  ChamferSize = 0
  FilletRadius = 0
  Height = 406.4
  Length = 355.6
  MakeFace = true
  Placement = pos=(33694.2,12071,3e-12) rot=(0,0,1;0rad)
FEATURE [Part::Feature] Generic___Chair001
  Placement = pos=(10073.1,11621.3,0) rot=(0,0,-1;1.5708rad)
  shape: bbox 406.4 x 355.6 x 736.6 mm, 58 faces, 9 solids (baked)
FEATURE [Part::Feature] Generic___Chair002
  Placement = pos=(8368.6,12274.6,3e-12) rot=(0,0,1;0rad)
  shape: bbox 355.6 x 406.4 x 736.6 mm, 58 faces, 9 solids (baked)
FEATURE [Part::Part2DObjectPython] Line791  # Draft 2D object (typed FeaturePython)
  ChamferSize = 0
  Closed = false
  End = (35373.4,11271,0)
  FilletRadius = 0
  Length = 700
  MakeFace = true
  Placement = pos=(-4194.62,729.043,0) rot=(0,0,1;0rad)
  Points = (2) [(39568,11242,-1.13687e-13),(39568,10542,-1.13687e-13)]
  Start = (35373.4,11971,0)
FEATURE [Part::Part2DObjectPython] Rectangle320  # Draft 2D object (typed FeaturePython)
  ChamferSize = 0
  FilletRadius = 0
  Height = 406.4
  Length = 355.6
  MakeFace = true
  Placement = pos=(35373.5,11798.8,0) rot=(0,0,-1;1.57123rad)
FEATURE [Part::Feature] Generic___Chair003
  Placement = pos=(9421.4,12274.6,0) rot=(0,0,1;0rad)
  shape: bbox 355.6 x 406.4 x 736.6 mm, 58 faces, 9 solids (baked)
FEATURE [Part::Part2DObjectPython] Line792  # Draft 2D object (typed FeaturePython)
  ChamferSize = 0
  Closed = false
  End = (35273.4,11171,0)
  FilletRadius = 0
  Length = 1750
  MakeFace = true
  Placement = pos=(-4194.62,729.043,0) rot=(0,0,1;0rad)
  Points = (2) [(37718,10442,-1.13687e-13),(39468,10442,-1.13687e-13)]
  Start = (33523.4,11171,0)
FEATURE [Part::Part2DObjectPython] Rectangle321  # Draft 2D object (typed FeaturePython)
  ChamferSize = 0
  FilletRadius = 0
  Height = 406.4
  Length = 355.6
  MakeFace = true
  Placement = pos=(33694.2,10764.6,0) rot=(0,0,1;0rad)
FEATURE [Part::Part2DObjectPython] Rectangle322  # Draft 2D object (typed FeaturePython)
  ChamferSize = 0
  FilletRadius = 0
  Height = 406.4
  Length = 355.6
  MakeFace = true
  Placement = pos=(34220.6,10764.6,-3e-12) rot=(0,0,1;0rad)
FEATURE [Part::Part2DObjectPython] Rectangle323  # Draft 2D object (typed FeaturePython)
  ChamferSize = 0
  FilletRadius = 0
  Height = 406.4
  Length = 355.6
  MakeFace = true
  Placement = pos=(34747,10764.6,-3e-12) rot=(0,0,1;0rad)
FEATURE [Part::Feature] Generic___Chair004
  Placement = pos=(8368.6,10968.2,-5e-12) rot=(0,0,1;3.14159rad)
  shape: bbox 355.6 x 406.4 x 736.6 mm, 58 faces, 9 solids (baked)
FEATURE [Part::Feature] Generic___Chair005
  Placement = pos=(8895,10968.2,-2e-12) rot=(0,0,1;3.14159rad)
  shape: bbox 355.6 x 406.4 x 736.6 mm, 58 faces, 9 solids (baked)
FEATURE [Part::Feature] Generic___Chair006
  Placement = pos=(9421.4,10968.2,-2e-12) rot=(0,0,1;3.14159rad)
  shape: bbox 355.6 x 406.4 x 736.6 mm, 58 faces, 9 solids (baked)
FEATURE [Part::Part2DObjectPython] Line793  # Draft 2D object (typed FeaturePython)
  ChamferSize = 0
  Closed = false
  End = (33423.4,11271,0)
  FilletRadius = 0
  Length = 700
  MakeFace = true
  Placement = pos=(-4194.62,729.043,0) rot=(0,0,1;0rad)
  Points = (2) [(37618,11242,-1.13687e-13),(37618,10542,-1.13687e-13)]
  Start = (33423.4,11971,0)
FEATURE [Part::Part2DObjectPython] Rectangle324  # Draft 2D object (typed FeaturePython)
  ChamferSize = 0
  FilletRadius = 0
  Height = 406.4
  Length = 355.6
  MakeFace = true
  Placement = pos=(33017.1,11799,0) rot=(0,0,-1;1.57123rad)
FEATURE [Part::Feature] Generic___Chair007
  Placement = pos=(7716.72,11621.6,1e-12) rot=(0,0,1;1.5708rad)
  shape: bbox 406.4 x 355.6 x 736.6 mm, 58 faces, 9 solids (baked)
FEATURE [App::DocumentObjectGroup] Group070  label="Chairs"
  Group = -> [Generic___Chair,Generic___Chair001,Generic___Chair002,Generic___Chair003,Generic___Chair004,Generic___Chair005,Generic___Chair006,Generic___Chair007]
FEATURE [App::DocumentObjectGroup] Group064  label="Furniture"
  Group = -> [Group065,Group070]
FEATURE [Part::Part2DObjectPython] Line794  # Draft 2D object (typed FeaturePython)
  ChamferSize = 0
  Closed = false
  End = (34398.4,12869.6,0)
  FilletRadius = 0
  Length = 2497.97
  MakeFace = true
  Placement = pos=(-4927.82,3139.23,0) rot=(0,0,1;0rad)
  Points = (2) [(39326.2,7232.41,0),(39326.2,9730.38,0)]
  Start = (34398.4,10371.6,0)
FEATURE [Part::Part2DObjectPython] Line795  # Draft 2D object (typed FeaturePython)
  ChamferSize = 0
  Closed = false
  End = (36348.4,11620.6,0)
  FilletRadius = 0
  Length = 3900
  MakeFace = true
  Placement = pos=(-4927.82,3139.23,0) rot=(0,0,1;0rad)
  Points = (2) [(37376.2,8481.39,0),(41276.2,8481.39,0)]
  Start = (32448.4,11620.6,0)
FEATURE [Part::Part2DObjectPython] Line796  # Draft 2D object (typed FeaturePython)
  ChamferSize = 0
  Closed = false
  End = (34398.4,10764.6,-3e-12)
  FilletRadius = 0
  Length = 1712.8
  MakeFace = true
  Placement = pos=(-4194.62,729.043,0) rot=(0,0,1;0rad)
  Points = (2) [(38593,11748.4,-1.13687e-13),(38593,10035.6,-2.91417e-12)]
  Start = (34398.4,12477.4,0)
  Support = -> Rectangle315
FEATURE [Part::Part2DObjectPython] Line797  # Draft 2D object (typed FeaturePython)
  ChamferSize = 0
  Closed = false
  End = (35779.8,11620,0)
  FilletRadius = 0
  Length = 2762.8
  MakeFace = true
  Placement = pos=(-4194.62,729.043,0) rot=(0,0,1;0rad)
  Points = (2) [(37211.6,10892.2,-1.13687e-13),(39974.4,10891,-1.13687e-13)]
  Start = (33017,11621.2,0)
FEATURE [Part::FeaturePython] Window062  label="Window060"  # WARN: FeaturePython — macro-defined, semantics opaque (R4)
  Base = -> Sketch062
  Height = 2100
  HoleDepth = 0
  MoveWithHost = true
  Normal = (-1,0,0)
  Placement = pos=(0,2440.47,-185.542) rot=(0,0,1;0rad)
  Preset = 6
  Role = 1
  Width = 1000
  WindowParts = OuterFrame | Frame | Wire0,Wire1 | 150.0 | 0.0 | Door | Solid panel | Wire1 | 50.0 | 50.0
FEATURE [Part::FeaturePython] Window063  label="Window061"  # WARN: FeaturePython — macro-defined, semantics opaque (R4)
  Base = -> Sketch062
  Height = 2200
  HoleDepth = 0
  MoveWithHost = true
  Normal = (-1,0,0)
  Placement = pos=(0,3440.47,-185.542) rot=(0,0,1;0rad)
  Preset = 6
  Role = 1
  Width = 1000
  WindowParts = OuterFrame | Frame | Wire0,Wire1 | 150.0 | 0.0 | Door | Solid panel | Wire1 | 50.0 | 50.0
FEATURE [Part::FeaturePython] Wall076  # WARN: FeaturePython — macro-defined, semantics opaque (R4)
  Align = 2
  Base = -> Line081
  Face = 0
  Height = 2900
  Length = 0
  MoveWithHost = false
  Normal = (0,0,0)
  Role = 0
  Subtractions = -> [Window035,Window062,Window063]
  Width = 150
FEATURE [App::DocumentObjectGroup] Group001  label="LEVEL 1 WALLS"
  Group = -> [Wall004,Wall009,Wall011,Wall013,Wall015,Wall064,Wall065,Wall066,Wall063,Wall067,Wall059,Wall068,Wall069,Wall060,Wall061,Wall062,Wall072,Wall073,Wall074,Wall,Wall075,Wall076,Wall077,Wall080,Wall084,Wall095]
FEATURE [App::DocumentObjectGroup] Group003  label="WALLS"
  Group = -> [Group002,Group001]
FEATURE [Part::Part2DObjectPython] Line177  # Draft 2D object (typed FeaturePython)
  ChamferSize = 0
  Closed = false
  End = (6080,19646.6,999.6)
  FilletRadius = 0
  Length = 8942.3
  MakeFace = true
  Placement = pos=(-4915,0.305262,1000) rot=(0,0,1;0rad)
  Points = (2) [(10995,10704,-0.0820662),(10995,19646.3,-0.400582)]
  Start = (6080,10704.3,999.918)
  Support = -> Wall076
FEATURE [Part::Part2DObjectPython] Line798  # Draft 2D object (typed FeaturePython)
  ChamferSize = 0
  Closed = false
  End = (10995,10550,2197.67)
  FilletRadius = 0
  Length = 197.674
  MakeFace = true
  Points = (2) [(10995,10550,2000),(10995,10550,2197.67)]
  Start = (10995,10550,2000)
  Support = -> Wall076
FEATURE [Part::Part2DObjectPython] Line799  # Draft 2D object (typed FeaturePython)
  ChamferSize = 0
  Closed = false
  End = (36398.4,8599.61,0)
  FilletRadius = 0
  Length = 900
  MakeFace = true
  Placement = pos=(0,2300,0) rot=(0,0,1;0rad)
  Points = (2) [(35498.4,6299.61,0),(36398.4,6299.61,0)]
  Start = (35498.4,8599.61,0)
FEATURE [Part::Part2DObjectPython] Arc043  # Draft 2D object (typed FeaturePython)
  FirstAngle = 90
  LastAngle = 179.974
  MakeFace = true
  Placement = pos=(36398.4,8599.61,0) rot=(0,0,1;0rad)
  Radius = 900
FEATURE [Part::Part2DObjectPython] Arc044  # Draft 2D object (typed FeaturePython)
  FirstAngle = 179.969
  LastAngle = 270
  MakeFace = true
  Placement = pos=(36398.4,10499.6,0) rot=(0,0,1;0rad)
  Radius = 900
FEATURE [Part::Part2DObjectPython] Line800  # Draft 2D object (typed FeaturePython)
  ChamferSize = 0
  Closed = false
  End = (35498.4,10499.6,0)
  FilletRadius = 0
  Length = 900
  MakeFace = true
  Placement = pos=(0,2300,0) rot=(0,0,1;0rad)
  Points = (2) [(36398.4,8199.61,0),(35498.4,8199.61,0)]
  Start = (36398.4,10499.6,0)
FEATURE [Part::Part2DObjectPython] Rectangle325  # Draft 2D object (typed FeaturePython)
  ChamferSize = 0
  FilletRadius = 0
  Height = -2830
  Length = 5550
  MakeFace = true
  Placement = pos=(3245,15850,0) rot=(0,0,1;0rad)
FEATURE [Part::Part2DObjectPython] Rectangle326  # Draft 2D object (typed FeaturePython)
  ChamferSize = 0
  FilletRadius = 0
  Height = -2830
  Length = -1900
  MakeFace = true
  Placement = pos=(10845,15850,0) rot=(0,0,1;0rad)
FEATURE [Part::Part2DObjectPython] Rectangle327  # Draft 2D object (typed FeaturePython)
  ChamferSize = 0
  FilletRadius = 0
  Height = -3120
  Length = -4300
  MakeFace = true
  Placement = pos=(4445,12870,0) rot=(0,0,1;0rad)
FEATURE [Part::Part2DObjectPython] Rectangle328  # Draft 2D object (typed FeaturePython)
  ChamferSize = 0
  FilletRadius = 0
  Height = -1200
  Length = 2950
  MakeFace = true
  Placement = pos=(145,9600,0) rot=(0,0,1;0rad)
FEATURE [Part::Part2DObjectPython] Rectangle329  # Draft 2D object (typed FeaturePython)
  ChamferSize = 0
  FilletRadius = 0
  Height = -1600
  Length = 2950
  MakeFace = true
  Placement = pos=(145,8250,0) rot=(0,0,1;0rad)
FEATURE [Part::Part2DObjectPython] DWire228  # Draft 2D object (typed FeaturePython)
  ChamferSize = 0
  Closed = true
  End = (145,2150,0)
  FilletRadius = 0
  Length = 15799.9
  MakeFace = true
  Placement = pos=(-25503.4,0.388761,0) rot=(0,0,1;0rad)
  Points = (8) [(25648.4,6499.61,0),(28598.4,6499.61,0),(28598.4,4649.61,0),(27998.4,4649.61,0),(27998.4,4499.61,0),(28598.4,4499.61,0),(28598.4,2149.61,0),+1 more]
  Start = (145,6500,0)
FEATURE [Part::Feature] Face059
  Placement = pos=(-25503.4,0.388761,0) rot=(0,0,1;0rad)
  shape: bbox 7600 x 8720 x 2e-07 mm, 1 faces, 0 solids (baked)
FEATURE [Part::Part2DObjectPython] Rectangle330  # Draft 2D object (typed FeaturePython)
  ChamferSize = 0
  FilletRadius = 0
  Height = -1849.61
  Length = -2550
  MakeFace = true
  Placement = pos=(5795,3999.61,0) rot=(0,0,1;0rad)
FEATURE [Part::Part2DObjectPython] DWire229  # Draft 2D object (typed FeaturePython)
  ChamferSize = 0
  Closed = true
  End = (5945,2000,0)
  FilletRadius = 0
  Length = 14099.2
  MakeFace = true
  Placement = pos=(-25503.4,0.388761,0) rot=(0,0,1;0rad)
  Points = (6) [(31448.4,3999.22,0),(36498.4,3999.22,0),(36498.4,2149.61,0),(36348.4,2149.61,0),(36348.4,1999.61,0),(31448.4,1999.61,0)]
  Start = (5945,3999.61,0)
FEATURE [Part::Part2DObjectPython] DWire230  # Draft 2D object (typed FeaturePython)
  ChamferSize = 0
  Closed = true
  End = (3095,13020,0)
  FilletRadius = 0
  Length = 12160
  MakeFace = true
  Placement = pos=(-25503.4,0.388761,0) rot=(0,0,1;0rad)
  Points = (6) [(28598.4,15999.6,0),(25648.4,15999.6,0),(25648.4,15849.6,0),(25498.4,15849.6,0),(25498.4,13019.6,0),(28598.4,13019.6,0)]
  Start = (3095,16000,0)
FEATURE [Part::FeaturePython] Structure044  # WARN: FeaturePython — macro-defined, semantics opaque (R4)
  Base = -> DWire230
  Height = 100
  Length = 0
  MoveWithHost = false
  Nodes = (2) [(1548.6,14506.5,0),(1548.6,14506.5,100)]
  Normal = (0,0,0)
  Placement = pos=(0,0,-100) rot=(0,0,1;0rad)
  Role = 2
  Width = 100
FEATURE [Part::FeaturePython] Structure045  # WARN: FeaturePython — macro-defined, semantics opaque (R4)
  Base = -> Rectangle325
  Height = 100
  Length = 0
  MoveWithHost = false
  Nodes = (2) [(6020,14435,0),(6020,14435,100)]
  Normal = (0,0,0)
  Placement = pos=(0,0,-100) rot=(0,0,1;0rad)
  Role = 2
  Width = 100
FEATURE [Part::FeaturePython] Structure046  # WARN: FeaturePython — macro-defined, semantics opaque (R4)
  Base = -> Rectangle327
  Height = 100
  Length = 0
  MoveWithHost = false
  Nodes = (2) [(2295,11310,0),(2295,11310,100)]
  Normal = (0,0,0)
  Placement = pos=(0,0,-100) rot=(0,0,1;0rad)
  Role = 2
  Width = 100
FEATURE [Part::FeaturePython] Structure047  # WARN: FeaturePython — macro-defined, semantics opaque (R4)
  Base = -> Rectangle328
  Height = 100
  Length = 0
  MoveWithHost = false
  Nodes = (2) [(1620,9000,0),(1620,9000,100)]
  Normal = (0,0,0)
  Placement = pos=(0,0,-100) rot=(0,0,1;0rad)
  Role = 2
  Width = 100
FEATURE [Part::FeaturePython] Structure048  # WARN: FeaturePython — macro-defined, semantics opaque (R4)
  Base = -> Rectangle329
  Height = 100
  Length = 0
  MoveWithHost = false
  Nodes = (2) [(1620,7450,0),(1620,7450,100)]
  Normal = (0,0,0)
  Placement = pos=(0,0,-100) rot=(0,0,1;0rad)
  Role = 2
  Width = 100
FEATURE [Part::FeaturePython] Structure049  # WARN: FeaturePython — macro-defined, semantics opaque (R4)
  Base = -> DWire228
  Height = 100
  Length = 0
  MoveWithHost = false
  Nodes = (2) [(1611.7,4323.23,0),(1611.7,4323.23,100)]
  Normal = (0,0,0)
  Placement = pos=(0,0,-100) rot=(0,0,1;0rad)
  Role = 2
  Width = 100
FEATURE [Part::FeaturePython] Structure050  # WARN: FeaturePython — macro-defined, semantics opaque (R4)
  Base = -> Face059
  Height = 100
  Length = 0
  MoveWithHost = false
  Normal = (0,0,0)
  Placement = pos=(0,0,-100) rot=(0,0,1;0rad)
  Role = 2
  Width = 100
FEATURE [Part::FeaturePython] Structure051  # WARN: FeaturePython — macro-defined, semantics opaque (R4)
  Base = -> Rectangle330
  Height = 100
  Length = 0
  MoveWithHost = false
  Nodes = (2) [(4520,3074.81,0),(4520,3074.81,100)]
  Normal = (0,0,0)
  Placement = pos=(0,0,-100) rot=(0,0,1;0rad)
  Role = 2
  Width = 100
FEATURE [Part::FeaturePython] Structure052  # WARN: FeaturePython — macro-defined, semantics opaque (R4)
  Base = -> DWire229
  Height = 100
  Length = 0
  MoveWithHost = false
  Nodes = (2) [(8464.53,3001.87,0),(8464.53,3001.87,100)]
  Normal = (0,0,0)
  Placement = pos=(0,0,-100) rot=(0,0,1;0rad)
  Role = 2
  Width = 100
FEATURE [Part::FeaturePython] Structure053  # WARN: FeaturePython — macro-defined, semantics opaque (R4)
  Base = -> Rectangle326
  Height = 100
  Length = 0
  MoveWithHost = false
  Nodes = (2) [(9895,14435,0),(9895,14435,100)]
  Normal = (0,0,0)
  Placement = pos=(0,0,-100) rot=(0,0,1;0rad)
  Role = 2
  Width = 100
FEATURE [Part::Part2DObjectPython] DWire231  label="Ext Foundation Sketch"  # Draft 2D object (typed FeaturePython)
  ChamferSize = 0
  Closed = true
  End = (10920,15925.4,-700)
  FilletRadius = 0
  Length = 49400.4
  MakeFace = false
  Placement = pos=(-25503.4,0.388456,-700) rot=(0,0,1;0rad)
  Points = (8) [(28673,15924.6,0),(28673,12944.6,0),(25573.4,12944.6,0),(25573.4,2074.61,0),(31373.4,2074.61,0),(31373.4,4074.22,0),(36423.4,4074.22,0),+1 more]
  Start = (3169.66,15925,-700)
FEATURE [Part::Part2DObjectPython] Line818  # Draft 2D object (typed FeaturePython)
  ChamferSize = 0
  Closed = false
  End = (10920,12945,-700)
  FilletRadius = 0
  Length = 7750.34
  MakeFace = true
  Placement = pos=(-25503.4,0.388456,-700) rot=(0,0,1;0rad)
  Points = (2) [(28673,12944.6,0),(36423.4,12944.6,0)]
  Start = (3169.66,12945,-700)
FEATURE [Part::Part2DObjectPython] Line819  # Draft 2D object (typed FeaturePython)
  ChamferSize = 0
  Closed = false
  End = (8869.89,15925.3,-700)
  FilletRadius = 0
  Length = 2980.22
  MakeFace = true
  Placement = pos=(-25503.4,0.388456,-700) rot=(0,0,1;0rad)
  Points = (2) [(34373.4,12944.7,0),(34373.3,15924.9,0)]
  Start = (8870.06,12945.1,-700)
FEATURE [Part::Part2DObjectPython] Line820  # Draft 2D object (typed FeaturePython)
  ChamferSize = 0
  Closed = false
  End = (4520,8550,-700)
  FilletRadius = 0
  Length = 4395
  MakeFace = true
  Placement = pos=(-25503.4,0.388456,-700) rot=(0,0,1;0rad)
  Points = (2) [(30023.4,12944.6,0),(30023.4,8549.61,0)]
  Start = (4520,12945,-700)
FEATURE [Part::Part2DObjectPython] Line821  # Draft 2D object (typed FeaturePython)
  ChamferSize = 0
  Closed = false
  End = (70.001,9675,-700)
  FilletRadius = 0
  Length = 4450
  MakeFace = true
  Placement = pos=(-25503.4,0.388456,-700) rot=(0,0,1;0rad)
  Points = (2) [(30023.4,9674.61,0),(25573.4,9674.61,0)]
  Start = (4520,9675,-700)
FEATURE [Part::Part2DObjectPython] Line823  # Draft 2D object (typed FeaturePython)
  ChamferSize = 0
  Closed = false
  End = (70.001,8325,-700)
  FilletRadius = 0
  Length = 3100
  MakeFace = true
  Placement = pos=(-25503.4,0.388456,-700) rot=(0,0,1;0rad)
  Points = (2) [(28673.4,8324.61,0),(25573.4,8324.61,0)]
  Start = (3170,8325,-700)
FEATURE [Part::Part2DObjectPython] Line824  # Draft 2D object (typed FeaturePython)
  ChamferSize = 0
  Closed = false
  End = (3170,9675,-700)
  FilletRadius = 0
  Length = 7600
  MakeFace = true
  Placement = pos=(-25503.4,0.388456,-700) rot=(0,0,1;0rad)
  Points = (2) [(28673.4,2074.61,0),(28673.4,9674.61,0)]
  Start = (3170,2075,-700)
FEATURE [Part::Part2DObjectPython] Line825  # Draft 2D object (typed FeaturePython)
  ChamferSize = 0
  Closed = false
  End = (70.001,6575,-700)
  FilletRadius = 0
  Length = 3100
  MakeFace = true
  Placement = pos=(-25503.4,0.388456,-700) rot=(0,0,1;0rad)
  Points = (2) [(28673.4,6574.61,0),(25573.4,6574.61,0)]
  Start = (3170,6575,-700)
FEATURE [Part::Part2DObjectPython] Line826  # Draft 2D object (typed FeaturePython)
  ChamferSize = 0
  Closed = false
  End = (5870,5750,-700)
  FilletRadius = 0
  Length = 1675.39
  MakeFace = true
  Placement = pos=(-25503.4,0.388456,-700) rot=(0,0,1;0rad)
  Points = (2) [(31373.4,4074.22,0),(31373.4,5749.61,0)]
  Start = (5870,4074.61,-700)
FEATURE [Part::Part2DObjectPython] Line827  # Draft 2D object (typed FeaturePython)
  ChamferSize = 0
  Closed = false
  End = (3170,4074.61,-700)
  FilletRadius = 0
  Length = 2700
  MakeFace = true
  Placement = pos=(-25503.4,0.388456,-700) rot=(0,0,1;0rad)
  Points = (2) [(31373.4,4074.22,0),(28673.4,4074.22,0)]
  Start = (5870,4074.61,-700)
FEATURE [Part::Part2DObjectPython] Line828  # Draft 2D object (typed FeaturePython)
  ChamferSize = 0
  Closed = false
  End = (3170,4575,-700)
  FilletRadius = 0
  Length = 674.965
  MakeFace = true
  Placement = pos=(-25503.4,0.388456,-700) rot=(0,0,1;0rad)
  Points = (2) [(27998.4,4574.61,0),(28673.4,4574.61,0)]
  Start = (2495.04,4575,-700)
FEATURE [Part::FeaturePython] Wall097  # WARN: FeaturePython — macro-defined, semantics opaque (R4)
  Align = 2
  Base = -> Line818
  Face = 0
  Height = 600
  Length = 0
  MoveWithHost = false
  Normal = (0,0,0)
  Role = 0
  Width = 200
FEATURE [Part::FeaturePython] Wall099  # WARN: FeaturePython — macro-defined, semantics opaque (R4)
  Align = 2
  Base = -> Line820
  Face = 0
  Height = 600
  Length = 0
  MoveWithHost = false
  Normal = (0,0,0)
  Role = 0
  Width = 200
FEATURE [Part::FeaturePython] Wall098  # WARN: FeaturePython — macro-defined, semantics opaque (R4)
  Additions = -> [Wall097,Wall099]
  Align = 2
  Base = -> Line819
  Face = 0
  Height = 600
  Length = 0
  MoveWithHost = false
  Normal = (0,0,0)
  Role = 0
  Width = 200
FEATURE [Part::FeaturePython] Wall100  # WARN: FeaturePython — macro-defined, semantics opaque (R4)
  Align = 2
  Base = -> Line821
  Face = 0
  Height = 600
  Length = 0
  MoveWithHost = false
  Normal = (0,0,0)
  Role = 0
  Width = 200
FEATURE [Part::FeaturePython] Wall101  # WARN: FeaturePython — macro-defined, semantics opaque (R4)
  Align = 2
  Base = -> Line823
  Face = 0
  Height = 600
  Length = 0
  MoveWithHost = false
  Normal = (0,0,0)
  Role = 0
  Width = 200
FEATURE [Part::FeaturePython] Wall103  # WARN: FeaturePython — macro-defined, semantics opaque (R4)
  Align = 2
  Base = -> Line825
  Face = 0
  Height = 600
  Length = 0
  MoveWithHost = false
  Normal = (0,0,0)
  Role = 0
  Width = 200
FEATURE [Part::FeaturePython] Wall104  # WARN: FeaturePython — macro-defined, semantics opaque (R4)
  Align = 2
  Base = -> Line826
  Face = 0
  Height = 600
  Length = 0
  MoveWithHost = false
  Normal = (0,0,0)
  Role = 0
  Width = 200
FEATURE [Part::FeaturePython] Wall105  # WARN: FeaturePython — macro-defined, semantics opaque (R4)
  Align = 2
  Base = -> Line827
  Face = 0
  Height = 600
  Length = 0
  MoveWithHost = false
  Normal = (0,0,0)
  Role = 0
  Width = 200
FEATURE [Part::FeaturePython] Wall106  # WARN: FeaturePython — macro-defined, semantics opaque (R4)
  Align = 2
  Base = -> Line828
  Face = 0
  Height = 600
  Length = 0
  MoveWithHost = false
  Normal = (0,0,0)
  Role = 0
  Width = 200
FEATURE [Part::FeaturePython] Wall102  # WARN: FeaturePython — macro-defined, semantics opaque (R4)
  Additions = -> [Wall106,Wall103,Wall101,Wall100,Wall098,Wall105]
  Align = 2
  Base = -> Line824
  Face = 0
  Height = 600
  Length = 0
  MoveWithHost = false
  Normal = (0,0,0)
  Role = 0
  Width = 200
FEATURE [Part::FeaturePython] Wall096  # WARN: FeaturePython — macro-defined, semantics opaque (R4)
  Additions = -> [Wall102,Wall104]
  Align = 2
  Base = -> DWire231
  Face = 0
  Height = 600
  Length = 0
  MoveWithHost = false
  Normal = (0,0,0)
  Role = 0
  Width = 200
FEATURE [Part::Part2DObjectPython] DWire232  label="Ext Foundation Sketch001"  # Draft 2D object (typed FeaturePython)
  ChamferSize = 0
  Closed = true
  End = (10920,15925.4,-960)
  FilletRadius = 0
  Length = 49400.4
  MakeFace = false
  Placement = pos=(-25503.4,0.388729,-960) rot=(0,0,1;0rad)
  Points = (8) [(28673,15924.6,0),(28673,12944.6,0),(25573.4,12944.6,0),(25573.4,2074.61,0),(31373.4,2074.61,0),(31373.4,4074.22,0),(36423.4,4074.22,0),+1 more]
  Start = (3169.66,15925,-960)
FEATURE [Part::Part2DObjectPython] Line829  # Draft 2D object (typed FeaturePython)
  ChamferSize = 0
  Closed = false
  End = (10920,12945,-960)
  FilletRadius = 0
  Length = 7750.34
  MakeFace = true
  Placement = pos=(-25503.4,0.388729,-960) rot=(0,0,1;0rad)
  Points = (2) [(28673,12944.6,0),(36423.4,12944.6,0)]
  Start = (3169.66,12945,-960)
FEATURE [Part::Part2DObjectPython] Line830  # Draft 2D object (typed FeaturePython)
  ChamferSize = 0
  Closed = false
  End = (8869.89,15925.3,-960)
  FilletRadius = 0
  Length = 2980.22
  MakeFace = true
  Placement = pos=(-25503.4,0.388729,-960) rot=(0,0,1;0rad)
  Points = (2) [(34373.4,12944.7,0),(34373.3,15924.9,0)]
  Start = (8870.06,12945.1,-960)
FEATURE [Part::Part2DObjectPython] Line831  # Draft 2D object (typed FeaturePython)
  ChamferSize = 0
  Closed = false
  End = (4520,8550,-960)
  FilletRadius = 0
  Length = 4395
  MakeFace = true
  Placement = pos=(-25503.4,0.388729,-960) rot=(0,0,1;0rad)
  Points = (2) [(30023.4,12944.6,0),(30023.4,8549.61,0)]
  Start = (4520,12945,-960)
FEATURE [Part::Part2DObjectPython] Line832  # Draft 2D object (typed FeaturePython)
  ChamferSize = 0
  Closed = false
  End = (70,9675,-960)
  FilletRadius = 0
  Length = 4450
  MakeFace = true
  Placement = pos=(-25503.4,0.388729,-960) rot=(0,0,1;0rad)
  Points = (2) [(30023.4,9674.61,0),(25573.4,9674.61,0)]
  Start = (4520,9675,-960)
FEATURE [Part::Part2DObjectPython] Line833  # Draft 2D object (typed FeaturePython)
  ChamferSize = 0
  Closed = false
  End = (70,8325,-960)
  FilletRadius = 0
  Length = 3100
  MakeFace = true
  Placement = pos=(-25503.4,0.388729,-960) rot=(0,0,1;0rad)
  Points = (2) [(28673.4,8324.61,0),(25573.4,8324.61,0)]
  Start = (3170,8325,-960)
FEATURE [Part::Part2DObjectPython] Line834  # Draft 2D object (typed FeaturePython)
  ChamferSize = 0
  Closed = false
  End = (3170,9675,-960)
  FilletRadius = 0
  Length = 7600
  MakeFace = true
  Placement = pos=(-25503.4,0.388729,-960) rot=(0,0,1;0rad)
  Points = (2) [(28673.4,2074.61,0),(28673.4,9674.61,0)]
  Start = (3170,2075,-960)
FEATURE [Part::Part2DObjectPython] Line835  # Draft 2D object (typed FeaturePython)
  ChamferSize = 0
  Closed = false
  End = (70,6575,-960)
  FilletRadius = 0
  Length = 3100
  MakeFace = true
  Placement = pos=(-25503.4,0.388729,-960) rot=(0,0,1;0rad)
  Points = (2) [(28673.4,6574.61,0),(25573.4,6574.61,0)]
  Start = (3170,6575,-960)
FEATURE [Part::Part2DObjectPython] Line836  # Draft 2D object (typed FeaturePython)
  ChamferSize = 0
  Closed = false
  End = (5870,5750,-960)
  FilletRadius = 0
  Length = 1675.39
  MakeFace = true
  Placement = pos=(-25503.4,0.388729,-960) rot=(0,0,1;0rad)
  Points = (2) [(31373.4,4074.22,0),(31373.4,5749.61,0)]
  Start = (5870,4074.61,-960)
FEATURE [Part::Part2DObjectPython] Line837  # Draft 2D object (typed FeaturePython)
  ChamferSize = 0
  Closed = false
  End = (3170,4074.61,-960)
  FilletRadius = 0
  Length = 2700
  MakeFace = true
  Placement = pos=(-25503.4,0.388729,-960) rot=(0,0,1;0rad)
  Points = (2) [(31373.4,4074.22,0),(28673.4,4074.22,0)]
  Start = (5870,4074.61,-960)
FEATURE [Part::Part2DObjectPython] Line838  # Draft 2D object (typed FeaturePython)
  ChamferSize = 0
  Closed = false
  End = (3170,4575,-960)
  FilletRadius = 0
  Length = 674.965
  MakeFace = true
  Placement = pos=(-25503.4,0.388729,-960) rot=(0,0,1;0rad)
  Points = (2) [(27998.4,4574.61,0),(28673.4,4574.61,0)]
  Start = (2495.03,4575,-960)
FEATURE [Part::FeaturePython] Wall108  # WARN: FeaturePython — macro-defined, semantics opaque (R4)
  Align = 2
  Base = -> Line829
  Face = 0
  Height = 260
  Length = 0
  MoveWithHost = false
  Normal = (0,0,0)
  Role = 0
  Width = 520
FEATURE [Part::FeaturePython] Wall110  # WARN: FeaturePython — macro-defined, semantics opaque (R4)
  Align = 2
  Base = -> Line831
  Face = 0
  Height = 260
  Length = 0
  MoveWithHost = false
  Normal = (0,0,0)
  Role = 0
  Width = 520
FEATURE [Part::FeaturePython] Wall109  # WARN: FeaturePython — macro-defined, semantics opaque (R4)
  Additions = -> [Wall108,Wall110]
  Align = 2
  Base = -> Line830
  Face = 0
  Height = 260
  Length = 0
  MoveWithHost = false
  Normal = (0,0,0)
  Role = 0
  Width = 520
FEATURE [Part::FeaturePython] Wall111  # WARN: FeaturePython — macro-defined, semantics opaque (R4)
  Align = 2
  Base = -> Line832
  Face = 0
  Height = 260
  Length = 0
  MoveWithHost = false
  Normal = (0,0,0)
  Role = 0
  Width = 520
FEATURE [Part::FeaturePython] Wall112  # WARN: FeaturePython — macro-defined, semantics opaque (R4)
  Align = 2
  Base = -> Line833
  Face = 0
  Height = 260
  Length = 0
  MoveWithHost = false
  Normal = (0,0,0)
  Role = 0
  Width = 520
FEATURE [Part::FeaturePython] Wall114  # WARN: FeaturePython — macro-defined, semantics opaque (R4)
  Align = 2
  Base = -> Line835
  Face = 0
  Height = 260
  Length = 0
  MoveWithHost = false
  Normal = (0,0,0)
  Role = 0
  Width = 520
FEATURE [Part::FeaturePython] Wall115  # WARN: FeaturePython — macro-defined, semantics opaque (R4)
  Align = 2
  Base = -> Line836
  Face = 0
  Height = 260
  Length = 0
  MoveWithHost = false
  Normal = (0,0,0)
  Role = 0
  Width = 520
FEATURE [Part::FeaturePython] Wall116  # WARN: FeaturePython — macro-defined, semantics opaque (R4)
  Align = 2
  Base = -> Line837
  Face = 0
  Height = 260
  Length = 0
  MoveWithHost = false
  Normal = (0,0,0)
  Role = 0
  Width = 520
FEATURE [Part::FeaturePython] Wall117  # WARN: FeaturePython — macro-defined, semantics opaque (R4)
  Align = 2
  Base = -> Line838
  Face = 0
  Height = 260
  Length = 0
  MoveWithHost = false
  Normal = (0,0,0)
  Role = 0
  Width = 520
FEATURE [Part::FeaturePython] Wall113  # WARN: FeaturePython — macro-defined, semantics opaque (R4)
  Additions = -> [Wall117,Wall114,Wall112,Wall111,Wall109,Wall116]
  Align = 2
  Base = -> Line834
  Face = 0
  Height = 260
  Length = 0
  MoveWithHost = false
  Normal = (0,0,0)
  Role = 0
  Width = 520
FEATURE [App::DocumentObjectGroup] Group073  label="Foundation Wall"
  Group = -> [Wall096]
FEATURE [App::DocumentObjectGroup] Group074  label="Ground Slab Level 1"
  Group = -> [Structure044,Structure045,Structure046,Structure047,Structure048,Structure049,Structure050,Structure051,Structure052,Structure053]
FEATURE [Part::Part2DObjectPython] Rectangle333  # Draft 2D object (typed FeaturePython)
  ChamferSize = 0
  FilletRadius = 0
  Height = -684
  Length = -520
  MakeFace = true
  Placement = pos=(330,2335,-700) rot=(0,0,1;0rad)
FEATURE [Part::Part2DObjectPython] Rectangle334  # Draft 2D object (typed FeaturePython)
  ChamferSize = 0
  FilletRadius = 0
  Height = -684
  Length = -520
  MakeFace = true
  Placement = pos=(3430,2335,-700) rot=(0,0,1;0rad)
FEATURE [Part::Part2DObjectPython] Rectangle335  # Draft 2D object (typed FeaturePython)
  ChamferSize = 0
  FilletRadius = 0
  Height = -684
  Length = -520
  MakeFace = true
  Placement = pos=(6130,2335,-700) rot=(0,0,1;0rad)
FEATURE [Part::Part2DObjectPython] Rectangle336  # Draft 2D object (typed FeaturePython)
  ChamferSize = 0
  FilletRadius = 0
  Height = -684
  Length = -520
  MakeFace = true
  Placement = pos=(11180,2335,-700) rot=(0,0,1;0rad)
FEATURE [Part::Part2DObjectPython] Rectangle337  # Draft 2D object (typed FeaturePython)
  ChamferSize = 0
  FilletRadius = 0
  Height = -684
  Length = -520
  MakeFace = true
  Placement = pos=(11180,16349.4,-700) rot=(0,0,1;0rad)
FEATURE [Part::Part2DObjectPython] Rectangle338  # Draft 2D object (typed FeaturePython)
  ChamferSize = 0
  FilletRadius = 0
  Height = -684
  Length = -520
  MakeFace = true
  Placement = pos=(6130,16349.4,-700) rot=(0,0,1;0rad)
FEATURE [Part::Part2DObjectPython] Rectangle339  # Draft 2D object (typed FeaturePython)
  ChamferSize = 0
  FilletRadius = 0
  Height = -684
  Length = -520
  MakeFace = true
  Placement = pos=(3430,16349.4,-700) rot=(0,0,1;0rad)
FEATURE [Part::Part2DObjectPython] Rectangle340  # Draft 2D object (typed FeaturePython)
  ChamferSize = 0
  FilletRadius = 0
  Height = -684
  Length = -520
  MakeFace = true
  Placement = pos=(330,16349.4,-700) rot=(0,0,1;0rad)
FEATURE [Part::Part2DObjectPython] Rectangle342  # Draft 2D object (typed FeaturePython)
  ChamferSize = 0
  FilletRadius = 0
  Height = -684
  Length = -520
  MakeFace = true
  Placement = pos=(6130,13205,-700) rot=(0,0,1;0rad)
FEATURE [Part::Part2DObjectPython] Rectangle347  # Draft 2D object (typed FeaturePython)
  ChamferSize = 0
  FilletRadius = 0
  Height = -684
  Length = -520
  MakeFace = true
  Placement = pos=(4780,8742,-700) rot=(0,0,1;0rad)
FEATURE [Part::Part2DObjectPython] Rectangle348  # Draft 2D object (typed FeaturePython)
  ChamferSize = 0
  FilletRadius = 0
  Height = -684
  Length = -520
  MakeFace = true
  Placement = pos=(6130,8742,-700) rot=(0,0,1;0rad)
FEATURE [Part::Part2DObjectPython] Rectangle350  # Draft 2D object (typed FeaturePython)
  ChamferSize = 0
  FilletRadius = 0
  Height = -684
  Length = -520
  MakeFace = true
  Placement = pos=(6130,6242,-700) rot=(0,0,1;0rad)
FEATURE [App::DocumentObjectGroup] Group076
FEATURE [Part::FeaturePython] Structure054  # WARN: FeaturePython — macro-defined, semantics opaque (R4)
  Base = -> Rectangle336
  Height = 260
  Length = 0
  MoveWithHost = false
  Nodes = (2) [(10920,1993,-700),(10920,1993,-440)]
  Normal = (0,0,0)
  Placement = pos=(0,0,-260) rot=(0,0,1;0rad)
  Role = 0
  Width = 100
FEATURE [Part::FeaturePython] Structure056  # WARN: FeaturePython — macro-defined, semantics opaque (R4)
  Base = -> Rectangle350
  Height = 260
  Length = 0
  MoveWithHost = false
  Nodes = (2) [(5870,5900,-700),(5870,5900,-440)]
  Normal = (0,0,0)
  Placement = pos=(0,0,-260) rot=(0,0,1;0rad)
  Role = 0
  Width = 100
FEATURE [Part::FeaturePython] Structure057  # WARN: FeaturePython — macro-defined, semantics opaque (R4)
  Base = -> Rectangle348
  Height = 260
  Length = 0
  MoveWithHost = false
  Nodes = (2) [(5870,8400,-700),(5870,8400,-440)]
  Normal = (0,0,0)
  Placement = pos=(0,0,-260) rot=(0,0,1;0rad)
  Role = 0
  Width = 100
FEATURE [Part::FeaturePython] Structure058  # WARN: FeaturePython — macro-defined, semantics opaque (R4)
  Base = -> Rectangle347
  Height = 260
  Length = 0
  MoveWithHost = false
  Nodes = (2) [(4520,8400,-700),(4520,8400,-440)]
  Normal = (0,0,0)
  Placement = pos=(0,0,-260) rot=(0,0,1;0rad)
  Role = 0
  Width = 100
FEATURE [Part::FeaturePython] Structure059  # WARN: FeaturePython — macro-defined, semantics opaque (R4)
  Base = -> Rectangle338
  Height = 260
  Length = 0
  MoveWithHost = false
  Nodes = (2) [(5870,16007.4,-700),(5870,16007.4,-440)]
  Normal = (0,0,0)
  Placement = pos=(0,0,-260) rot=(0,0,1;0rad)
  Role = 0
  Width = 100
FEATURE [Part::FeaturePython] Structure060  # WARN: FeaturePython — macro-defined, semantics opaque (R4)
  Base = -> Rectangle339
  Height = 260
  Length = 0
  MoveWithHost = false
  Nodes = (2) [(3170,16007.4,-700),(3170,16007.4,-440)]
  Normal = (0,0,0)
  Placement = pos=(0,0,-260) rot=(0,0,1;0rad)
  Role = 0
  Width = 100
FEATURE [Part::FeaturePython] Structure061  # WARN: FeaturePython — macro-defined, semantics opaque (R4)
  Base = -> Rectangle337
  Height = 260
  Length = 0
  MoveWithHost = false
  Nodes = (2) [(10920,16007.4,-700),(10920,16007.4,-440)]
  Normal = (0,0,0)
  Placement = pos=(0,0,-260) rot=(0,0,1;0rad)
  Role = 0
  Width = 100
FEATURE [Part::FeaturePython] Structure062  # WARN: FeaturePython — macro-defined, semantics opaque (R4)
  Base = -> Rectangle340
  Height = 260
  Length = 0
  MoveWithHost = false
  Nodes = (2) [(69.9996,16007.4,-700),(69.9996,16007.4,-440)]
  Normal = (0,0,0)
  Placement = pos=(0,0,-260) rot=(0,0,1;0rad)
  Role = 0
  Width = 100
FEATURE [Part::FeaturePython] Structure063  # WARN: FeaturePython — macro-defined, semantics opaque (R4)
  Base = -> Rectangle334
  Height = 260
  Length = 0
  MoveWithHost = false
  Nodes = (2) [(3170,1993,-700),(3170,1993,-440)]
  Normal = (0,0,0)
  Placement = pos=(0,0,-260) rot=(0,0,1;0rad)
  Role = 0
  Width = 100
FEATURE [Part::FeaturePython] Structure064  # WARN: FeaturePython — macro-defined, semantics opaque (R4)
  Base = -> Rectangle342
  Height = 260
  Length = 0
  MoveWithHost = false
  Nodes = (2) [(5870,12863,-700),(5870,12863,-440)]
  Normal = (0,0,0)
  Placement = pos=(0,0,-260) rot=(0,0,1;0rad)
  Role = 0
  Width = 100
FEATURE [Part::FeaturePython] Structure065  # WARN: FeaturePython — macro-defined, semantics opaque (R4)
  Base = -> Rectangle333
  Height = 260
  Length = 0
  MoveWithHost = false
  Nodes = (2) [(70,1993,-700),(70,1993,-440)]
  Normal = (0,0,0)
  Placement = pos=(0,0,-260) rot=(0,0,1;0rad)
  Role = 0
  Width = 100
FEATURE [Part::FeaturePython] Structure066  # WARN: FeaturePython — macro-defined, semantics opaque (R4)
  Base = -> Rectangle335
  Height = 260
  Length = 0
  MoveWithHost = false
  Nodes = (2) [(5870,1993,-700),(5870,1993,-440)]
  Normal = (0,0,0)
  Placement = pos=(0,0,-260) rot=(0,0,1;0rad)
  Role = 0
  Width = 100
FEATURE [Part::FeaturePython] Wall118  label="Continuous Footer"  # WARN: FeaturePython — macro-defined, semantics opaque (R4)
  Additions = -> [Wall113,Wall115,Structure056,Structure066,Structure063,Structure065,Structure058,Structure064,Structure060,Structure059,Structure061]
  Align = 2
  Base = -> DWire232
  Face = 0
  Height = 260
  Length = 0
  MoveWithHost = false
  Normal = (0,0,0)
  Role = 0
  Width = 520
FEATURE [App::DocumentObjectGroup] Group075  label="Foundation Footer"
  Group = -> [Wall118,Structure054,Structure057,Structure062]
FEATURE [App::FeaturePython] Section009  label="Foundation Plan"  # WARN: FeaturePython — macro-defined, semantics opaque (R4)
  Objects = -> [Group073,Group074,Group075,Group]
  OnlySolids = true
  Placement = pos=(5836.66,8193.78,-300) rot=(0,0,1;0rad)
FEATURE [Part::Part2DObjectPython] Shape2DView019  label="Foundation cut"  # Draft 2D object (typed FeaturePython)
  Base = -> Section009
  HiddenLines = false
  Placement = pos=(25503.4,-17097,300) rot=(0,0,1;0rad)
  Projection = (0,0,1)
  ProjectionMode = 2
  SegmentLength = 0.05
  Tessellation = false
FEATURE [Part::Part2DObjectPython] Shape2DView020  label="Foundation Footer projection"  # Draft 2D object (typed FeaturePython)
  Base = -> Section009
  HiddenLines = false
  Placement = pos=(25503.4,-17097,0) rot=(0,0,1;0rad)
  Projection = (0,0,1)
  ProjectionMode = 0
  SegmentLength = 0.05
  Tessellation = false
FEATURE [Drawing::FeatureViewPython] View009  label="View of Section009"  # drawing view (typed FeaturePython)
  FontSize = 12
  LineWidth = 0.1
  RenderingMode = 1
  Rotation = 0
  Scale = 0.01
  ShowCut = true
  ShowFill = false
  Source = -> Section009
  ViewResult = <blob: 26655 chars omitted>
  Visible = true
  X = 50
  Y = 200
FEATURE [App::FeaturePython] Dimension267  # Draft dimension (typed FeaturePython)
  Dimline = (11827.1,6050,0.0001461)
  Direction = (0,0,0)
  Distance = 2200
  End = (11384.4,8250,0.0001461)
  Normal = (0,0,1)
  Start = (11384.4,6050,0.0001461)
FEATURE [App::FeaturePython] Dimension268  # Draft dimension (typed FeaturePython)
  Dimline = (11827.1,8250,0.0001461)
  Direction = (0,0,0)
  Distance = 300
  End = (11384.4,8550,0.0001461)
  Normal = (0,0,1)
  Start = (11384.4,8250,0.0001461)
FEATURE [App::FeaturePython] Dimension269  # Draft dimension (typed FeaturePython)
  Dimline = (11827.1,8550,0.0001461)
  Direction = (0,0,0)
  Distance = 2000
  End = (11384.4,10550,0.0001461)
  Normal = (0,0,1)
  Start = (11384.4,8550,0.0001461)
FEATURE [App::FeaturePython] Dimension270  # Draft dimension (typed FeaturePython)
  Dimline = (11827.1,10550,0.0001461)
  Direction = (0,0,0)
  Distance = 650
  End = (11384.4,11200,0.0001461)
  Normal = (0,0,1)
  Start = (11384.4,10550,0.0001461)
FEATURE [App::FeaturePython] Dimension271  # Draft dimension (typed FeaturePython)
  Dimline = (11827.1,11200,0.0001461)
  Direction = (0,0,0)
  Distance = 1000
  End = (11384.4,12200,0.0001461)
  Normal = (0,0,1)
  Start = (11384.4,11200,0.0001461)
FEATURE [App::FeaturePython] Dimension272  # Draft dimension (typed FeaturePython)
  Dimline = (11827.1,12200,0.0001461)
  Direction = (0,0,0)
  Distance = 520
  End = (11384.4,12720,0.0001461)
  Normal = (0,0,1)
  Start = (11384.4,12200,0.0001461)
FEATURE [App::FeaturePython] Dimension273  # Draft dimension (typed FeaturePython)
  Dimline = (11827.1,12720,0.0001461)
  Direction = (0,0,0)
  Distance = 300
  End = (11384.4,13020,0.0001461)
  Normal = (0,0,1)
  Start = (11384.4,12720,0.0001461)
FEATURE [App::FeaturePython] Dimension274  # Draft dimension (typed FeaturePython)
  Dimline = (11827.1,13020,0.0001461)
  Direction = (0,0,0)
  Distance = 358.805
  End = (11384.4,13378.8,0.0001461)
  Normal = (0,0,1)
  Start = (11384.4,13020,0.0001461)
FEATURE [App::FeaturePython] Dimension275  # Draft dimension (typed FeaturePython)
  Dimline = (11827.1,13378.8,0.0001461)
  Direction = (0,0,0)
  Distance = 500
  End = (11384.4,13878.8,0.0001461)
  Normal = (0,0,1)
  Start = (11384.4,13378.8,0.0001461)
FEATURE [App::DocumentObjectGroup] Group035  label="Level 1 Plan Annotation"
  Group = -> [Dimension050,Dimension051,Dimension052,Dimension053,Dimension054,Dimension055,Dimension057,Dimension058,Dimension059,Dimension061,Dimension062,Dimension063,Dimension066,Dimension067,Dimension068,Dimension069,Dimension070,Dimension071,Dimension072,Dimension073,Dimension074,Dimension082,Dimension084,Dimension085,Dimension086,Dimension087,Dimension090,Dimension091,Dimension092,Dimension093,+70 more]
FEATURE [Drawing::FeatureViewPython] ViewGroup035001  label="Level 1 Dimensions"  # drawing view (typed FeaturePython)
  Direction = (0,0,0)
  FillStyle = 0
  FontSize = 1.5
  LineStyle = 0
  LineWidth = 0.03
  Rotation = 0
  Scale = 0.01
  Source = -> Group035
  ViewResult = <g id="ViewGroup035001" transform="rotate(0.0,50.0,200.0) translate(50.0,200.0) scale(0.01,-0.01)"></g>
  Visible = true
  X = 50
  Y = 200
FEATURE [App::FeaturePython] Dimension278  # Draft dimension (typed FeaturePython)
  Dimline = (11827.1,11700.4,3000)
  Direction = (0,0,0)
  Distance = 1020
  End = (11520.1,11700,3000)
  Normal = (0,0,1)
  Start = (11520.1,12720,3000)
FEATURE [App::FeaturePython] Dimension279  # Draft dimension (typed FeaturePython)
  Dimline = (11827.1,11700,3000)
  Direction = (0,0,0)
  Distance = 500
  End = (11520.1,11200,3000)
  Normal = (0,0,1)
  Start = (11520.1,11700,3000)
FEATURE [App::FeaturePython] Dimension280  # Draft dimension (typed FeaturePython)
  Dimline = (11827.1,11200,3000)
  Direction = (0,0,0)
  Distance = 2650
  End = (11520.1,8550,3000)
  Normal = (0,0,1)
  Start = (11520.1,11200,3000)
FEATURE [App::DocumentObjectGroup] Group039  label="Level 2 Plan Annotation"
  Group = -> [Dimension152,Dimension153,Dimension154,Dimension155,Dimension156,Dimension157,Dimension158,Dimension159,Dimension163,Dimension164,Dimension165,Dimension166,Dimension167,Dimension168,Dimension169,Dimension170,Dimension171,Dimension172,Dimension173,Dimension174,Dimension175,Dimension176,Dimension177,Dimension178,Dimension179,Dimension180,Dimension181,Dimension182,Dimension183,Dimension184,+65 more]
FEATURE [Drawing::FeatureViewPython] ViewGroup039  label="Level 2 Dimensions"  # drawing view (typed FeaturePython)
  Direction = (0,0,0)
  FillStyle = 0
  FontSize = 1.5
  LineStyle = 0
  LineWidth = 0.03
  Rotation = 0
  Scale = 0.01
  Source = -> Group039
  ViewResult = <g id="ViewGroup039" transform="rotate(0.0,220.0,200.0) translate(220.0,200.0) scale(0.01,-0.01)"></g>
  Visible = true
  X = 220
  Y = 200
FEATURE [App::FeaturePython] Dimension  # Draft dimension (typed FeaturePython)
  Dimline = (11180,17249.4,-300)
  Direction = (0,0,0)
  Distance = 11370
  End = (11180,16349.4,-300)
  Normal = (0,0,1)
  Start = (-190,16349.4,-300)
FEATURE [App::FeaturePython] Dimension281  # Draft dimension (typed FeaturePython)
  Dimline = (11180,16949.4,-300)
  Direction = (0,0,0)
  Distance = 3100
  End = (2910,16349.4,-300)
  Normal = (0,0,1)
  Start = (-190,16349.4,-300)
FEATURE [App::FeaturePython] Dimension282  # Draft dimension (typed FeaturePython)
  Dimline = (11180,16949.4,-300)
  Direction = (0,0,0)
  Distance = 8270
  End = (11180,16349.4,-300)
  Normal = (0,0,1)
  Start = (2910,16349.4,-300)
FEATURE [App::FeaturePython] Dimension283  # Draft dimension (typed FeaturePython)
  Dimline = (-190,16649.4,-300)
  Direction = (0,0,0)
  Distance = 520
  End = (330,16349.4,-300)
  Normal = (0,0,1)
  Start = (-190,16349.4,-300)
FEATURE [App::FeaturePython] Dimension284  # Draft dimension (typed FeaturePython)
  Dimline = (330,16649.4,-300)
  Direction = (0,0,0)
  Distance = 2580
  End = (2910,16349.4,-300)
  Normal = (0,0,1)
  Start = (330,16349.4,-300)
FEATURE [App::FeaturePython] Dimension285  # Draft dimension (typed FeaturePython)
  Dimline = (2910,16649.4,-300)
  Direction = (0,0,0)
  Distance = 520
  End = (3430,16349.4,-300)
  Normal = (0,0,1)
  Start = (2910,16349.4,-300)
FEATURE [App::FeaturePython] Dimension286  # Draft dimension (typed FeaturePython)
  Dimline = (3430,16649.4,-300)
  Direction = (0,0,0)
  Distance = 2180
  End = (5610,16349.4,-300)
  Normal = (0,0,1)
  Start = (3430,16349.4,-300)
FEATURE [App::FeaturePython] Dimension287  # Draft dimension (typed FeaturePython)
  Dimline = (5610,16649.4,-300)
  Direction = (0,0,0)
  Distance = 520
  End = (6130,16349.4,-300)
  Normal = (0,0,1)
  Start = (5610,16349.4,-300)
FEATURE [App::FeaturePython] Dimension288  # Draft dimension (typed FeaturePython)
  Dimline = (6130,16649.4,-300)
  Direction = (0,0,0)
  Distance = 4530
  End = (10660,16349.4,-300)
  Normal = (0,0,1)
  Start = (6130,16349.4,-300)
FEATURE [App::FeaturePython] Dimension289  # Draft dimension (typed FeaturePython)
  Dimline = (10660,16649.4,-300)
  Direction = (0,0,0)
  Distance = 520
  End = (11180,16349.4,-300)
  Normal = (0,0,1)
  Start = (10660,16349.4,-300)
FEATURE [App::FeaturePython] Dimension290  # Draft dimension (typed FeaturePython)
  Dimline = (-1090,16349.4,-300)
  Direction = (0,0,0)
  Distance = 14698.4
  End = (-190,16349.4,-300)
  Normal = (0,0,1)
  Start = (-190,1651,-300)
FEATURE [App::FeaturePython] Dimension291  # Draft dimension (typed FeaturePython)
  Dimline = (-790,16349.4,-300)
  Direction = (0,0,0)
  Distance = 11554
  End = (-190,13205,-300)
  Normal = (0,0,1)
  Start = (-190,1651,-300)
FEATURE [App::FeaturePython] Dimension292  # Draft dimension (typed FeaturePython)
  Dimline = (-790,16349.4,-300)
  Direction = (0,0,0)
  Distance = 3144.42
  End = (-190,16349.4,-300)
  Normal = (0,0,1)
  Start = (-190,13205,-300)
FEATURE [App::FeaturePython] Dimension293  # Draft dimension (typed FeaturePython)
  Dimline = (-490,1651,-300)
  Direction = (0,0,0)
  Distance = 164
  End = (330,1815,-300)
  Normal = (0,0,1)
  Start = (330,1651,-300)
FEATURE [App::FeaturePython] Dimension294  # Draft dimension (typed FeaturePython)
  Dimline = (-490,1815,-300)
  Direction = (0,0,0)
  Distance = 520
  End = (330,2335,-300)
  Normal = (0,0,1)
  Start = (330,1815,-300)
FEATURE [App::FeaturePython] Dimension295  # Draft dimension (typed FeaturePython)
  Dimline = (-490,2335,-300)
  Direction = (0,0,0)
  Distance = 3980
  End = (330,6315,-300)
  Normal = (0,0,1)
  Start = (330,2335,-300)
FEATURE [App::FeaturePython] Dimension296  # Draft dimension (typed FeaturePython)
  Dimline = (-490,6315,-300)
  Direction = (0,0,0)
  Distance = 520
  End = (330,6835,-300)
  Normal = (0,0,1)
  Start = (330,6315,-300)
FEATURE [App::FeaturePython] Dimension297  # Draft dimension (typed FeaturePython)
  Dimline = (-490,6835,-300)
  Direction = (0,0,0)
  Distance = 1230
  End = (330,8065,-300)
  Normal = (0,0,1)
  Start = (330,6835,-300)
FEATURE [App::FeaturePython] Dimension298  # Draft dimension (typed FeaturePython)
  Dimline = (-490,8065,-300)
  Direction = (0,0,0)
  Distance = 520
  End = (330,8585,-300)
  Normal = (0,0,1)
  Start = (330,8065,-300)
FEATURE [App::FeaturePython] Dimension299  # Draft dimension (typed FeaturePython)
  Dimline = (-490,8585,-300)
  Direction = (0,0,0)
  Distance = 830
  End = (330,9415,-300)
  Normal = (0,0,1)
  Start = (330,8585,-300)
FEATURE [App::FeaturePython] Dimension300  # Draft dimension (typed FeaturePython)
  Dimline = (-490,9415,-300)
  Direction = (0,0,0)
  Distance = 520
  End = (330,9935,-300)
  Normal = (0,0,1)
  Start = (330,9415,-300)
FEATURE [App::FeaturePython] Dimension301  # Draft dimension (typed FeaturePython)
  Dimline = (-490,9935,-300)
  Direction = (0,0,0)
  Distance = 2750
  End = (330,12685,-300)
  Normal = (0,0,1)
  Start = (330,9935,-300)
FEATURE [App::FeaturePython] Dimension302  # Draft dimension (typed FeaturePython)
  Dimline = (-490,12685,-300)
  Direction = (0,0,0)
  Distance = 520
  End = (330,13205,-300)
  Normal = (0,0,1)
  Start = (330,12685,-300)
FEATURE [App::FeaturePython] Dimension303  # Draft dimension (typed FeaturePython)
  Dimline = (-490,13205,-300)
  Direction = (0,0,0)
  Distance = 2460.42
  End = (-190,15665.4,-300)
  Normal = (0,0,1)
  Start = (-190,13205,-300)
FEATURE [App::FeaturePython] Dimension304  # Draft dimension (typed FeaturePython)
  Dimline = (-490,15665.4,-300)
  Direction = (0,0,0)
  Distance = 684
  End = (-190,16349.4,-300)
  Normal = (0,0,1)
  Start = (-190,15665.4,-300)
FEATURE [App::FeaturePython] Dimension305  # Draft dimension (typed FeaturePython)
  Dimline = (12080,1651,-300)
  Direction = (0,0,0)
  Distance = 14698.4
  End = (11180,1651,-300)
  Normal = (0,0,1)
  Start = (11180,16349.4,-300)
FEATURE [App::FeaturePython] Dimension306  # Draft dimension (typed FeaturePython)
  Dimline = (11780,1651,-300)
  Direction = (0,0,0)
  Distance = 12534.8
  End = (11180,3814.61,-300)
  Normal = (0,0,1)
  Start = (11180,16349.4,-300)
FEATURE [App::FeaturePython] Dimension307  # Draft dimension (typed FeaturePython)
  Dimline = (11780,1651,-300)
  Direction = (0,0,0)
  Distance = 2163.61
  End = (11180,1651,-300)
  Normal = (0,0,1)
  Start = (11180,3814.61,-300)
FEATURE [App::FeaturePython] Dimension308  # Draft dimension (typed FeaturePython)
  Dimline = (11479.6,16330,-300)
  Direction = (0,0,0)
  Distance = 163.971
  End = (11180,16185.5,-300)
  Normal = (0,0,1)
  Start = (11180,16349.4,-300)
FEATURE [App::FeaturePython] Dimension309  # Draft dimension (typed FeaturePython)
  Dimline = (11479.6,16185.5,-300)
  Direction = (0,0,0)
  Distance = 520
  End = (10660,15665.4,-300)
  Normal = (0,0,1)
  Start = (10660,16185.4,-300)
FEATURE [App::FeaturePython] Dimension310  # Draft dimension (typed FeaturePython)
  Dimline = (11479.6,15665.4,-300)
  Direction = (0,0,0)
  Distance = 2460.42
  End = (10660,13205,-300)
  Normal = (0,0,1)
  Start = (10660,15665.4,-300)
FEATURE [App::FeaturePython] Dimension311  # Draft dimension (typed FeaturePython)
  Dimline = (11479.6,13205,-300)
  Direction = (0,0,0)
  Distance = 520
  End = (10660,12685,-300)
  Normal = (0,0,1)
  Start = (10660,13205,-300)
FEATURE [App::FeaturePython] Dimension312  # Draft dimension (typed FeaturePython)
  Dimline = (11479.6,12685,-300)
  Direction = (0,0,0)
  Distance = 8350.39
  End = (10660,4334.61,-300)
  Normal = (0,0,1)
  Start = (10660,12685,-300)
FEATURE [App::FeaturePython] Dimension313  # Draft dimension (typed FeaturePython)
  Dimline = (11479.6,4334.61,-300)
  Direction = (0,0,0)
  Distance = 520
  End = (10660,3814.61,-300)
  Normal = (0,0,1)
  Start = (10660,4334.61,-300)
FEATURE [App::FeaturePython] Dimension314  # Draft dimension (typed FeaturePython)
  Dimline = (11479.6,3814.61,-300)
  Direction = (0,0,0)
  Distance = 1479.61
  End = (11180,2335,-300)
  Normal = (0,0,1)
  Start = (11180,3814.61,-300)
FEATURE [App::FeaturePython] Dimension315  # Draft dimension (typed FeaturePython)
  Dimline = (11479.6,2335,-300)
  Direction = (0,0,0)
  Distance = 684
  End = (11180,1651,-300)
  Normal = (0,0,1)
  Start = (11180,2335,-300)
FEATURE [App::FeaturePython] Dimension316  # Draft dimension (typed FeaturePython)
  Dimline = (11180,751,-300)
  Direction = (0,0,0)
  Distance = 11370
  End = (11180,1651,-300)
  Normal = (0,0,1)
  Start = (-190,1651,-300)
FEATURE [App::FeaturePython] Dimension317  # Draft dimension (typed FeaturePython)
  Dimline = (-190,1051,-300)
  Direction = (0,0,0)
  Distance = 6320
  End = (6130,1651,-300)
  Normal = (0,0,1)
  Start = (-190,1651,-300)
FEATURE [App::FeaturePython] Dimension318  # Draft dimension (typed FeaturePython)
  Dimline = (6130,1051,-300)
  Direction = (0,0,0)
  Distance = 5050
  End = (11180,1651,-300)
  Normal = (0,0,1)
  Start = (6130,1651,-300)
FEATURE [App::FeaturePython] Dimension319  # Draft dimension (typed FeaturePython)
  Dimline = (-190,1351,-300)
  Direction = (0,0,0)
  Distance = 520
  End = (330,1651,-300)
  Normal = (0,0,1)
  Start = (-190,1651,-300)
FEATURE [App::FeaturePython] Dimension320  # Draft dimension (typed FeaturePython)
  Dimline = (330,1351,-300)
  Direction = (0,0,0)
  Distance = 2580
  End = (2910,1651,-300)
  Normal = (0,0,1)
  Start = (330,1651,-300)
FEATURE [App::FeaturePython] Dimension321  # Draft dimension (typed FeaturePython)
  Dimline = (2910,1351,-300)
  Direction = (0,0,0)
  Distance = 520
  End = (3430,1651,-300)
  Normal = (0,0,1)
  Start = (2910,1651,-300)
FEATURE [App::FeaturePython] Dimension322  # Draft dimension (typed FeaturePython)
  Dimline = (3430,1351,-300)
  Direction = (0,0,0)
  Distance = 2180
  End = (5610,1651,-300)
  Normal = (0,0,1)
  Start = (3430,1651,-300)
FEATURE [App::FeaturePython] Dimension323  # Draft dimension (typed FeaturePython)
  Dimline = (5610,1351,-300)
  Direction = (0,0,0)
  Distance = 520
  End = (6130,1651,-300)
  Normal = (0,0,1)
  Start = (5610,1651,-300)
FEATURE [App::FeaturePython] Dimension324  # Draft dimension (typed FeaturePython)
  Dimline = (6130,1351,-300)
  Direction = (0,0,0)
  Distance = 4530
  End = (10660,1651,-300)
  Normal = (0,0,1)
  Start = (6130,1651,-300)
FEATURE [App::FeaturePython] Dimension325  # Draft dimension (typed FeaturePython)
  Dimline = (10660,1351,-300)
  Direction = (0,0,0)
  Distance = 520
  End = (11180,1651,-300)
  Normal = (0,0,1)
  Start = (10660,1651,-300)
FEATURE [App::FeaturePython] Dimension326  # Draft dimension (typed FeaturePython)
  Dimline = (9129.98,14435.2,-300)
  Direction = (0,0,0)
  Distance = 520
  End = (9129.98,14435.2,-300)
  Normal = (0,0,1)
  Start = (8609.98,14435.2,-300)
FEATURE [App::FeaturePython] Dimension327  # Draft dimension (typed FeaturePython)
  Dimline = (8609.98,14435.2,-300)
  Direction = (0,0,0)
  Distance = 1530.02
  End = (10660,14435.2,-300)
  Normal = (0,0,1)
  Start = (9129.98,14435.2,-300)
FEATURE [App::FeaturePython] Dimension328  # Draft dimension (typed FeaturePython)
  Dimline = (10660,14435.2,-300)
  Direction = (0,0,0)
  Distance = 520
  End = (11180,14435.2,-300)
  Normal = (0,0,1)
  Start = (10660,14435.2,-300)
FEATURE [App::FeaturePython] Dimension329  # Draft dimension (typed FeaturePython)
  Dimline = (8969.96,14735.2,-300)
  Direction = (0,0,0)
  Distance = 200
  End = (8969.98,14435.2,-300)
  Normal = (0,0,1)
  Start = (8769.98,14435.2,-300)
FEATURE [App::FeaturePython] Dimension333  # Draft dimension (typed FeaturePython)
  Dimline = (9129.96,14735.2,-300)
  Direction = (0,0,0)
  Distance = 200
  End = (11020,14435.2,-300)
  Normal = (0,0,1)
  Start = (10820,14435.2,-300)
FEATURE [App::FeaturePython] Dimension334  # Draft dimension (typed FeaturePython)
  Dimline = (8769.96,15035.1,-300)
  Direction = (0,0,0)
  Distance = 160.001
  End = (8769.91,15665.3,-300)
  Normal = (0,0,1)
  Start = (8609.91,15665.3,-300)
FEATURE [App::FeaturePython] Dimension335  # Draft dimension (typed FeaturePython)
  Dimline = (8769.96,15035.1,-300)
  Direction = (0,0,0)
  Distance = 159.999
  End = (9129.94,15035.2,-300)
  Normal = (0,0,1)
  Start = (8969.94,15035.1,-300)
FEATURE [App::FeaturePython] Dimension336  # Draft dimension (typed FeaturePython)
  Dimline = (9069.96,15035.1,-300)
  Direction = (0,0,0)
  Distance = 160.001
  End = (10820,15665.4,-300)
  Normal = (0,0,1)
  Start = (10660,15665.4,-300)
FEATURE [App::FeaturePython] Dimension337  # Draft dimension (typed FeaturePython)
  Dimline = (10820,15035.1,-300)
  Direction = (0,0,0)
  Distance = 159.999
  End = (11180,16025.4,-300)
  Normal = (0,0,1)
  Start = (11020,16025.4,-300)
FEATURE [App::FeaturePython] Dimension338  # Draft dimension (typed FeaturePython)
  Dimline = (3429.66,14735.1,-300)
  Direction = (0,0,0)
  Distance = 200
  End = (3269.66,14735.1,-300)
  Normal = (0,0,1)
  Start = (3069.66,14735.1,-300)
FEATURE [App::FeaturePython] Dimension340  # Draft dimension (typed FeaturePython)
  Dimline = (3069.66,15035.1,-300)
  Direction = (0,0,0)
  Distance = 159.999
  End = (3429.64,15035.2,-300)
  Normal = (0,0,0)
  Start = (3269.65,15035.1,-300)
FEATURE [App::FeaturePython] Dimension341  # Draft dimension (typed FeaturePython)
  Dimline = (3269.65,15035.2,-300)
  Direction = (0,0,0)
  Distance = 160.001
  End = (3069.66,15035.2,-300)
  Normal = (0,0,1)
  Start = (2909.66,15035.2,-300)
FEATURE [Part::Part2DObjectPython] Rectangle376  # Draft 2D object (typed FeaturePython)
  ChamferSize = 0
  FilletRadius = 0
  Height = 2399.72
  Length = 6380
  MakeFace = true
  Placement = pos=(72926,-10123.7,0) rot=(0,0,1;0rad)
FEATURE [Part::Part2DObjectPython] Rectangle377  # Draft 2D object (typed FeaturePython)
  ChamferSize = 0
  FilletRadius = 0
  Height = 300
  Length = -300
  MakeFace = true
  Placement = pos=(73627,-3463.72,0) rot=(0,0,1;0rad)
FEATURE [Part::Part2DObjectPython] Rectangle378  # Draft 2D object (typed FeaturePython)
  ChamferSize = 0
  FilletRadius = 0
  Height = 300
  Length = -300
  MakeFace = true
  Placement = pos=(73027,-3463.72,0) rot=(0,0,1;0rad)
FEATURE [Part::Part2DObjectPython] Rectangle379  # Draft 2D object (typed FeaturePython)
  ChamferSize = 0
  FilletRadius = 0
  Height = 300
  Length = -300
  MakeFace = true
  Placement = pos=(73327,-3463.72,0) rot=(0,0,1;0rad)
FEATURE [App::FeaturePython] Dimension342  # Draft dimension (typed FeaturePython)
  Dimline = (6130,3074.81,-300)
  Direction = (0,0,0)
  Distance = 200
  End = (5970,3074.81,-300)
  Normal = (0,0,1)
  Start = (5770,3074.81,-300)
FEATURE [App::FeaturePython] Dimension343  # Draft dimension (typed FeaturePython)
  Dimline = (5970,3374.81,-300)
  Direction = (0,0,0)
  Distance = 160.001
  End = (5770,3374.81,-300)
  Normal = (0,0,1)
  Start = (5610,3374.81,-300)
FEATURE [App::FeaturePython] Dimension344  # Draft dimension (typed FeaturePython)
  Dimline = (5770,3374.81,-300)
  Direction = (0,0,0)
  Distance = 159.999
  End = (6130,3374.81,-300)
  Normal = (0,0,1)
  Start = (5970,3374.81,-300)
FEATURE [App::FeaturePython] Dimension345  # Draft dimension (typed FeaturePython)
  Dimline = (3370,3074.81,-300)
  Direction = (0,0,0)
  Distance = 200
  End = (3270,3074.81,-300)
  Normal = (0,0,1)
  Start = (3070,3074.81,-300)
FEATURE [App::FeaturePython] Dimension346  # Draft dimension (typed FeaturePython)
  Dimline = (3070,3374.81,-300)
  Direction = (0,0,0)
  Distance = 159.999
  End = (3430,3374.81,-300)
  Normal = (0,0,1)
  Start = (3270,3374.81,-300)
FEATURE [App::FeaturePython] Dimension347  # Draft dimension (typed FeaturePython)
  Dimline = (3270,3374.81,-300)
  Direction = (0,0,0)
  Distance = 160.001
  End = (3070,3374.81,-300)
  Normal = (0,0,1)
  Start = (2910,3374.81,-300)
FEATURE [App::FeaturePython] Dimension349  # Draft dimension (typed FeaturePython)
  Dimline = (6730,8742,-300)
  Direction = (0,0,0)
  Distance = 684
  End = (6130,8058,-300)
  Normal = (0,0,1)
  Start = (6130,8742,-300)
FEATURE [App::FeaturePython] Dimension350  # Draft dimension (typed FeaturePython)
  Dimline = (6730,8058,-300)
  Direction = (0,0,0)
  Distance = 1816
  End = (6130,6242,-300)
  Normal = (0,0,1)
  Start = (6130,8058,-300)
FEATURE [App::FeaturePython] Dimension351  # Draft dimension (typed FeaturePython)
  Dimline = (6730,6242,-300)
  Direction = (0,0,0)
  Distance = 1907.39
  End = (6130,4334.61,-300)
  Normal = (0,0,1)
  Start = (6130,6242,-300)
FEATURE [App::FeaturePython] Dimension352  # Draft dimension (typed FeaturePython)
  Dimline = (6730,8742,-300)
  Direction = (0,0,0)
  Distance = 3943
  End = (6130,8742,-300)
  Normal = (0,0,1)
  Start = (6130,12685,-300)
FEATURE [App::FeaturePython] Dimension353  # Draft dimension (typed FeaturePython)
  Dimline = (6730,4334.61,-300)
  Direction = (0,0,0)
  Distance = 520
  End = (6130,3814.61,-300)
  Normal = (0,0,1)
  Start = (6130,4334.61,-300)
FEATURE [App::FeaturePython] Dimension354  # Draft dimension (typed FeaturePython)
  Dimline = (6430,9042,-300)
  Direction = (0,0,0)
  Distance = 164
  End = (6130,12521,-300)
  Normal = (0,0,1)
  Start = (6130,12685,-300)
FEATURE [App::FeaturePython] Dimension355  # Draft dimension (typed FeaturePython)
  Dimline = (6430,9042,-300)
  Direction = (0,0,0)
  Distance = 3779
  End = (6130,8742,-300)
  Normal = (0,0,1)
  Start = (6130,12521,-300)
FEATURE [App::FeaturePython] Dimension356  # Draft dimension (typed FeaturePython)
  Dimline = (6430,8742,-300)
  Direction = (0,0,0)
  Distance = 192
  End = (5870,8550,-300)
  Normal = (0,0,1)
  Start = (5870,8742,-300)
FEATURE [App::FeaturePython] Dimension357  # Draft dimension (typed FeaturePython)
  Dimline = (6430,8550,-300)
  Direction = (0,0,0)
  Distance = 300
  End = (5945,8250,-300)
  Normal = (0,0,1)
  Start = (5945,8550,-300)
FEATURE [App::FeaturePython] Dimension358  # Draft dimension (typed FeaturePython)
  Dimline = (6430,8250,-300)
  Direction = (0,0,0)
  Distance = 192
  End = (5945,8058,-300)
  Normal = (0,0,1)
  Start = (5945,8250,-300)
FEATURE [App::FeaturePython] Dimension359  # Draft dimension (typed FeaturePython)
  Dimline = (6430,8058,-300)
  Direction = (0,0,0)
  Distance = 1816
  End = (6130,6242,-300)
  Normal = (0,0,1)
  Start = (6130,8058,-300)
FEATURE [App::FeaturePython] Dimension360  # Draft dimension (typed FeaturePython)
  Dimline = (6430,6242,-300)
  Direction = (0,0,0)
  Distance = 192
  End = (5870,6050,-300)
  Normal = (0,0,1)
  Start = (5870,6242,-300)
FEATURE [App::FeaturePython] Dimension361  # Draft dimension (typed FeaturePython)
  Dimline = (6430,6050,-300)
  Direction = (0,0,0)
  Distance = 300
  End = (5945,5750,-300)
  Normal = (0,0,1)
  Start = (5945,6050,-300)
FEATURE [App::FeaturePython] Dimension362  # Draft dimension (typed FeaturePython)
  Dimline = (6430,5750,-300)
  Direction = (0,0,0)
  Distance = 1415.39
  End = (6130,4334.61,-300)
  Normal = (0,0,1)
  Start = (6130,5750,-300)
FEATURE [App::FeaturePython] Dimension363  # Draft dimension (typed FeaturePython)
  Dimline = (7030,3874.61,-300)
  Direction = (0,0,0)
  Distance = 200
  End = (7030,3974.61,-300)
  Normal = (0,0,1)
  Start = (7030,4174.61,-300)
FEATURE [App::FeaturePython] Dimension364  # Draft dimension (typed FeaturePython)
  Dimline = (7330,4174.61,-300)
  Direction = (0,0,0)
  Distance = 160
  End = (7330,3814.61,-300)
  Normal = (0,0,1)
  Start = (7330,3974.61,-300)
FEATURE [App::FeaturePython] Dimension365  # Draft dimension (typed FeaturePython)
  Dimline = (7330,3814.61,-300)
  Direction = (0,0,0)
  Distance = 160
  End = (7330,4174.61,-300)
  Normal = (0,0,1)
  Start = (7330,4334.61,-300)
FEATURE [App::FeaturePython] Dimension366  # Draft dimension (typed FeaturePython)
  Dimline = (1595.03,4315,-300)
  Direction = (0,0,0)
  Distance = 520
  End = (2495.04,4315,-300)
  Normal = (0,0,1)
  Start = (2495.04,4835,-300)
FEATURE [App::FeaturePython] Dimension367  # Draft dimension (typed FeaturePython)
  Dimline = (1895.03,4315,-300)
  Direction = (0,0,0)
  Distance = 200
  End = (2495.04,4475,-300)
  Normal = (0,0,1)
  Start = (2495.03,4675,-300)
FEATURE [App::FeaturePython] Dimension368  # Draft dimension (typed FeaturePython)
  Dimline = (2195.03,4615,-300)
  Direction = (0,0,0)
  Distance = 160
  End = (2495.04,4675,-300)
  Normal = (0,0,1)
  Start = (2495.03,4835,-300)
FEATURE [App::FeaturePython] Dimension369  # Draft dimension (typed FeaturePython)
  Dimline = (2195.03,4315,-300)
  Direction = (0,0,0)
  Distance = 160
  End = (2495.03,4315,-300)
  Normal = (0,0,1)
  Start = (2495.04,4475,-300)
FEATURE [App::FeaturePython] Dimension370  # Draft dimension (typed FeaturePython)
  Dimline = (1595.03,4835,-300)
  Direction = (0,0,0)
  Distance = 520
  End = (1620,6315,-300)
  Normal = (0,0,1)
  Start = (1620,6835,-300)
FEATURE [App::FeaturePython] Dimension371  # Draft dimension (typed FeaturePython)
  Dimline = (1895.03,4675,-300)
  Direction = (0,0,0)
  Distance = 200
  End = (3070,6475,-300)
  Normal = (0,0,1)
  Start = (3070,6675,-300)
FEATURE [App::FeaturePython] Dimension372  # Draft dimension (typed FeaturePython)
  Dimline = (2195.03,4835,-300)
  Direction = (0,0,0)
  Distance = 160
  End = (2910,6315,-300)
  Normal = (0,0,1)
  Start = (2909.66,6475,-300)
FEATURE [App::FeaturePython] Dimension373  # Draft dimension (typed FeaturePython)
  Dimline = (2191.9,6313.48,-300)
  Direction = (0,0,0)
  Distance = 160
  End = (2910,6675,-300)
  Normal = (0,0,1)
  Start = (2910,6835,-300)
FEATURE [App::FeaturePython] Dimension374  # Draft dimension (typed FeaturePython)
  Dimline = (1620,6835,-300)
  Direction = (0,0,0)
  Distance = 520
  End = (2295,9415,-300)
  Normal = (0,0,1)
  Start = (2295,9935,-300)
FEATURE [App::FeaturePython] Dimension375  # Draft dimension (typed FeaturePython)
  Dimline = (1895.03,6675,-300)
  Direction = (0,0,0)
  Distance = 200
  End = (2495.04,9575,-300)
  Normal = (0,0,1)
  Start = (2495.04,9775,-300)
FEATURE [App::FeaturePython] Dimension376  # Draft dimension (typed FeaturePython)
  Dimline = (2191.9,6675,-300)
  Direction = (0,0,0)
  Distance = 160
  End = (3845,9415,-300)
  Normal = (0,0,1)
  Start = (3845,9575,-300)
FEATURE [App::FeaturePython] Dimension377  # Draft dimension (typed FeaturePython)
  Dimline = (2191.9,9415,-300)
  Direction = (0,0,0)
  Distance = 160
  End = (4260,9775,-300)
  Normal = (0,0,1)
  Start = (4260,9935,-300)
FEATURE [App::FeaturePython] Dimension378  # Draft dimension (typed FeaturePython)
  Dimline = (1620,9415,-300)
  Direction = (0,0,0)
  Distance = 520
  End = (1359.83,12685,-300)
  Normal = (0,0,1)
  Start = (1359.83,13205,-300)
FEATURE [App::FeaturePython] Dimension379  # Draft dimension (typed FeaturePython)
  Dimline = (1895.03,9775,-300)
  Direction = (0,0,0)
  Distance = 200
  End = (3069.66,12845,-300)
  Normal = (0,0,1)
  Start = (3069.66,13045,-300)
FEATURE [App::FeaturePython] Dimension380  # Draft dimension (typed FeaturePython)
  Dimline = (2191.9,9775,-300)
  Direction = (0,0,0)
  Distance = 160
  End = (2909.66,13045,-300)
  Normal = (0,0,1)
  Start = (2909.66,13205,-300)
FEATURE [App::FeaturePython] Dimension381  # Draft dimension (typed FeaturePython)
  Dimline = (2191.9,9935,-300)
  Direction = (0,0,0)
  Distance = 160
  End = (2295,12685,-300)
  Normal = (0,0,1)
  Start = (2295,12845,-300)
FEATURE [App::FeaturePython] Dimension382  # Draft dimension (typed FeaturePython)
  Dimline = (1595.03,6315,-300)
  Direction = (0,0,0)
  Distance = 520
  End = (1620,8065,-300)
  Normal = (0,0,1)
  Start = (1620,8585,-300)
FEATURE [App::FeaturePython] Dimension383  # Draft dimension (typed FeaturePython)
  Dimline = (1895.03,9575,-300)
  Direction = (0,0,0)
  Distance = 200
  End = (1620,8225,-300)
  Normal = (0,0,1)
  Start = (1620,8425,-300)
FEATURE [App::FeaturePython] Dimension384  # Draft dimension (typed FeaturePython)
  Dimline = (2191.9,9415,-300)
  Direction = (0,0,0)
  Distance = 160.001
  End = (2909.66,8425,-300)
  Normal = (0,0,1)
  Start = (2910,8585,-300)
FEATURE [App::FeaturePython] Dimension385  # Draft dimension (typed FeaturePython)
  Dimline = (2191.9,9415,-300)
  Direction = (0,0,0)
  Distance = 160
  End = (1620,8065,-300)
  Normal = (0,0,1)
  Start = (1620,8225,-300)
FEATURE [App::FeaturePython] Dimension386  # Draft dimension (typed FeaturePython)
  Dimline = (2495.03,5135,-300)
  Direction = (0,0,0)
  Distance = 414.964
  End = (2910,4835,-300)
  Normal = (0,0,1)
  Start = (2495.04,4835,-300)
FEATURE [App::FeaturePython] Dimension387  # Draft dimension (typed FeaturePython)
  Dimline = (2495.03,5435,-300)
  Direction = (0,0,0)
  Distance = 574.965
  End = (3070,4675,-300)
  Normal = (0,0,1)
  Start = (2495.04,4675,-300)
FEATURE [App::FeaturePython] Dimension388  # Draft dimension (typed FeaturePython)
  Dimline = (4520,2175,-300)
  Direction = (0,0,0)
  Distance = 1479.61
  End = (4520,2335,-300)
  Normal = (0,0,1)
  Start = (4520,3814.61,-300)
FEATURE [App::FeaturePython] Dimension389  # Draft dimension (typed FeaturePython)
  Dimline = (1595.03,4315,-300)
  Direction = (0,0,0)
  Distance = 520
  End = (1620,1815,-300)
  Normal = (0,0,1)
  Start = (1620,2335,-300)
FEATURE [App::FeaturePython] Dimension390  # Draft dimension (typed FeaturePython)
  Dimline = (1895.03,4475,-300)
  Direction = (0,0,0)
  Distance = 200
  End = (1620,1975,-300)
  Normal = (0,0,1)
  Start = (1620,2175,-300)
FEATURE [App::FeaturePython] Dimension391  # Draft dimension (typed FeaturePython)
  Dimline = (2195.03,4315,-300)
  Direction = (0,0,0)
  Distance = 160
  End = (2910,2175,-300)
  Normal = (0,0,1)
  Start = (2910,2335,-300)
FEATURE [App::FeaturePython] Dimension392  # Draft dimension (typed FeaturePython)
  Dimline = (2195.03,2335,-300)
  Direction = (0,0,0)
  Distance = 160
  End = (2909.66,1815,-300)
  Normal = (0,0,1)
  Start = (2909.66,1975,-300)
FEATURE [App::FeaturePython] Dimension393  # Draft dimension (typed FeaturePython)
  Dimline = (330,7770,-300)
  Direction = (0,0,0)
  Distance = 520
  End = (330,7770,-300)
  Normal = (0,0,1)
  Start = (-190,7770,-300)
FEATURE [App::FeaturePython] Dimension394  # Draft dimension (typed FeaturePython)
  Dimline = (-340,7470,-300)
  Direction = (0,0,0)
  Distance = 200
  End = (170.001,6675,-300)
  Normal = (0,0,1)
  Start = (-29.999,6675,-300)
FEATURE [App::FeaturePython] Dimension395  # Draft dimension (typed FeaturePython)
  Dimline = (-340,7170,-300)
  Direction = (0,0,0)
  Distance = 160.001
  End = (-29.999,13205,-300)
  Normal = (0,0,1)
  Start = (-190,13205,-300)
FEATURE [App::FeaturePython] Dimension396  # Draft dimension (typed FeaturePython)
  Dimline = (-190,7170,-300)
  Direction = (0,0,0)
  Distance = 159.999
  End = (330,6475,-300)
  Normal = (0,0,1)
  Start = (170.001,6475,-300)
FEATURE [App::FeaturePython] Dimension397  # Draft dimension (typed FeaturePython)
  Dimline = (4620,11310,-300)
  Direction = (0,0,0)
  Distance = 520
  End = (4780,11310,-300)
  Normal = (0,0,1)
  Start = (4260,11310,-300)
FEATURE [App::FeaturePython] Dimension398  # Draft dimension (typed FeaturePython)
  Dimline = (4620,11010,-300)
  Direction = (0,0,0)
  Distance = 200
  End = (4620,9775,-300)
  Normal = (0,0,1)
  Start = (4420,9775,-300)
FEATURE [App::FeaturePython] Dimension399  # Draft dimension (typed FeaturePython)
  Dimline = (4720,10710,-300)
  Direction = (0,0,0)
  Distance = 160.001
  End = (4420,9935,-300)
  Normal = (0,0,1)
  Start = (4260,9935,-300)
FEATURE [App::FeaturePython] Dimension400  # Draft dimension (typed FeaturePython)
  Dimline = (4720,10710,-300)
  Direction = (0,0,0)
  Distance = 159.999
  End = (4780,8550,-300)
  Normal = (0,0,1)
  Start = (4620,8550,-300)
FEATURE [App::FeaturePython] Dimension401  # Draft dimension (typed FeaturePython)
  Dimline = (330,7770,-300)
  Direction = (0,0,0)
  Distance = 830
  End = (28933.4,-7682,0)
  LinkedGeometry = -> [Shape2DView020]
  Normal = (0,0,1)
  Start = (29763.4,-7682,0)
  Support = -> Shape2DView020
FEATURE [App::FeaturePython] Dimension402  # Draft dimension (typed FeaturePython)
  Dimline = (4260,7770,-300)
  Direction = (0,0,0)
  Distance = 520
  End = (4780,8058,-300)
  Normal = (0,0,1)
  Start = (4260,8058,-300)
FEATURE [App::FeaturePython] Dimension403  # Draft dimension (typed FeaturePython)
  Dimline = (4825.62,7770,-300)
  Direction = (0,0,0)
  Distance = 830
  End = (5610,8058,-300)
  Normal = (0,0,1)
  Start = (4780,8058,-300)
FEATURE [App::FeaturePython] Dimension405  # Draft dimension (typed FeaturePython)
  Dimline = (3960,9415,-300)
  Direction = (0,0,0)
  Distance = 1357
  End = (3959.62,8058,-300)
  Normal = (0,0,1)
  Start = (3960,9415,-300)
FEATURE [App::FeaturePython] Dimension406  # Draft dimension (typed FeaturePython)
  Dimline = (5610,7770,-300)
  Direction = (0,0,0)
  Distance = 520
  End = (6130,8058,-300)
  Normal = (0,0,1)
  Start = (5610,8058,-300)
FEATURE [App::FeaturePython] Dimension407  # Draft dimension (typed FeaturePython)
  Dimline = (3660,9415,-300)
  Direction = (0,0,0)
  Distance = 1517
  End = (4535,8058,-300)
  Normal = (0,0,1)
  Start = (4535,9575,-300)
FEATURE [App::FeaturePython] Dimension408  # Draft dimension (typed FeaturePython)
  Dimline = (4420,11310,-300)
  Direction = (0,0,0)
  Distance = 3930
  End = (4260,11310,-300)
  Normal = (0,0,1)
  Start = (330,11310,-300)
FEATURE [App::FeaturePython] Dimension409  # Draft dimension (typed FeaturePython)
  Dimline = (5770,5750,-300)
  Direction = (0,0,0)
  Distance = 2580
  End = (2910,6315,-300)
  Normal = (0,0,1)
  Start = (330,6315,-300)
FEATURE [App::FeaturePython] Dimension410  # Draft dimension (typed FeaturePython)
  Dimline = (4260,11310,-300)
  Direction = (0,0,0)
  Distance = 5880
  End = (10660,10713.5,-300)
  Normal = (0,0,1)
  Start = (4780,10713.5,-300)
FEATURE [App::FeaturePython] Dimension411  # Draft dimension (typed FeaturePython)
  Dimline = (2387.62,3975,-300)
  Direction = (0,0,0)
  Distance = 2165.03
  End = (2495.03,4325,-300)
  Normal = (0,0,1)
  Start = (330,4325,-300)
FEATURE [App::FeaturePython] Dimension412  # Draft dimension (typed FeaturePython)
  Dimline = (6730,12685,-300)
  Direction = (0,0,0)
  Distance = 2460.16
  End = (6019.78,13205,-300)
  Normal = (0,0,1)
  Start = (6019.78,15665.2,-300)
FEATURE [App::DocumentObjectGroup] Group077  label="Foundation Plan Annotation"
  Group = -> [Dimension,Dimension281,Dimension282,Dimension283,Dimension284,Dimension285,Dimension286,Dimension287,Dimension288,Dimension289,Dimension290,Dimension291,Dimension292,Dimension293,Dimension294,Dimension295,Dimension296,Dimension297,Dimension298,Dimension299,Dimension300,Dimension301,Dimension302,Dimension303,Dimension304,Dimension305,Dimension306,Dimension307,Dimension308,Dimension309,Dimension310,+96 more]
FEATURE [Part::Part2DObjectPython] Rectangle380  # Draft 2D object (typed FeaturePython)
  ChamferSize = 0
  FilletRadius = 0
  Height = 2416
  Length = -735
  MakeFace = true
  Placement = pos=(15232,1588,-300) rot=(0,0,1;0rad)
FEATURE [Part::Part2DObjectPython] Shape2DView023  label="S2DV foundation plan"  # Draft 2D object (typed FeaturePython)
  Base = -> Section009
  HiddenLines = false
  Placement = pos=(0,0,-300) rot=(0,0,1;0rad)
  Projection = (0,0,1)
  ProjectionMode = 0
  SegmentLength = 0.05
  Tessellation = false
FEATURE [Part::Part2DObjectPython] DWire  # Draft 2D object (typed FeaturePython)
  ChamferSize = 0
  Closed = true
  End = (6774.56,36965.6,-960)
  FilletRadius = 0
  Length = 36698.8
  MakeFace = true
  Points = (4) [(6774.56,24595,-960),(6774.56,26680.4,6000),(6774.56,36780.4,6000),(6774.56,36965.6,-960)]
  Start = (6774.56,24595,-960)
FEATURE [Part::Part2DObjectPython] Rectangle381  # Draft 2D object (typed FeaturePython)
  ChamferSize = 0
  FilletRadius = 0
  Height = 300
  Length = 300
  MakeFace = true
  Placement = pos=(6774.56,36930.4,6000) rot=(0.57735,0.57735,0.57735;2.0944rad)
FEATURE [Part::Part2DObjectPython] Rectangle382  # Draft 2D object (typed FeaturePython)
  ChamferSize = 0
  FilletRadius = 0
  Height = 300
  Length = 300
  MakeFace = true
  Placement = pos=(6774.56,37230.4,6000) rot=(0.57735,0.57735,0.57735;2.0944rad)
FEATURE [Part::Part2DObjectPython] Rectangle383  # Draft 2D object (typed FeaturePython)
  ChamferSize = 0
  FilletRadius = 0
  Height = 300
  Length = 300
  MakeFace = true
  Placement = pos=(6774.56,37530.4,6000) rot=(0.57735,0.57735,0.57735;2.0944rad)
FEATURE [App::FeaturePython] Dimension413  # Draft dimension (typed FeaturePython)
  Dimline = (6774.56,17050,6000)
  Direction = (0,0,0)
  Distance = 6960
  End = (6774.56,16150,-960)
  Normal = (1,0,-8.418e-09)
  Start = (6774.56,16150,6000)
FEATURE [App::FeaturePython] Dimension414  # Draft dimension (typed FeaturePython)
  Dimline = (6774.56,16750,5700)
  Direction = (0,0,0)
  Distance = 2995
  End = (6774.56,16000,3005)
  Normal = (1,0,-8.418e-09)
  Start = (6774.56,16000,6000)
FEATURE [App::FeaturePython] Dimension415  # Draft dimension (typed FeaturePython)
  Dimline = (6774.56,16750,3005)
  Direction = (0,0,0)
  Distance = 3005
  End = (6774.56,16000,0)
  Normal = (1,0,-8.418e-09)
  Start = (6774.56,16000,3005)
FEATURE [App::FeaturePython] Dimension416  # Draft dimension (typed FeaturePython)
  Dimline = (6774.56,16750,0)
  Direction = (0,0,0)
  Distance = 700
  End = (6774.56,16000,-700)
  Normal = (1,0,-8.418e-09)
  Start = (6774.56,16000,0)
FEATURE [App::FeaturePython] Dimension417  # Draft dimension (typed FeaturePython)
  Dimline = (6774.56,16750,-700)
  Direction = (0,0,0)
  Distance = 260
  End = (6774.56,16025.2,-960)
  Normal = (1,0,-8.418e-09)
  Start = (6774.56,16025.2,-700)
FEATURE [App::FeaturePython] Dimension418  # Draft dimension (typed FeaturePython)
  Dimline = (6774.56,16450,6000)
  Direction = (0,0,0)
  Distance = 200
  End = (6774.56,16000,5800)
  Normal = (1,0,-8.418e-09)
  Start = (6774.56,16000,6000)
FEATURE [App::FeaturePython] Dimension419  # Draft dimension (typed FeaturePython)
  Dimline = (6774.56,16450,5800)
  Direction = (0,0,0)
  Distance = 600
  End = (6774.56,16000,5200)
  Normal = (1,0,-8.418e-09)
  Start = (6774.56,16000,5800)
FEATURE [App::FeaturePython] Dimension420  # Draft dimension (typed FeaturePython)
  Dimline = (6774.56,16450,5200)
  Direction = (0,0,0)
  Distance = 1200
  End = (6774.56,16000,4000)
  Normal = (1,0,-8.418e-09)
  Start = (6774.56,16000,5200)
FEATURE [App::FeaturePython] Dimension421  # Draft dimension (typed FeaturePython)
  Dimline = (6774.56,16450,4000)
  Direction = (0,0,0)
  Distance = 1000
  End = (6774.56,16000,3000)
  Normal = (1,0,-8.418e-09)
  Start = (6774.56,16000,4000)
FEATURE [App::FeaturePython] Dimension422  # Draft dimension (typed FeaturePython)
  Dimline = (6774.56,16450,3000)
  Direction = (0,0,0)
  Distance = 200
  End = (6774.56,16000,2800)
  Normal = (1,0,-8.418e-09)
  Start = (6774.56,16000,3000)
FEATURE [App::FeaturePython] Dimension423  # Draft dimension (typed FeaturePython)
  Dimline = (6774.56,16450,2800)
  Direction = (0,0,0)
  Distance = 600.403
  End = (6774.56,16000,2199.6)
  Normal = (1,0,-8.418e-09)
  Start = (6774.56,16000,2800)
FEATURE [App::FeaturePython] Dimension424  # Draft dimension (typed FeaturePython)
  Dimline = (6774.56,16450,2199.6)
  Direction = (0,0,0)
  Distance = 1200
  End = (6774.56,16000,999.597)
  Normal = (1,0,-8.418e-09)
  Start = (6774.56,16000,2199.6)
FEATURE [App::FeaturePython] Dimension425  # Draft dimension (typed FeaturePython)
  Dimline = (6774.56,16450,999.597)
  Direction = (0,0,0)
  Distance = 1099.6
  End = (6774.56,16000,-100)
  Normal = (1,0,-8.418e-09)
  Start = (6774.56,16000,999.597)
FEATURE [App::FeaturePython] Dimension426  # Draft dimension (typed FeaturePython)
  Dimline = (6774.56,16450,-100)
  Direction = (0,0,0)
  Distance = 600
  End = (6774.56,16025.2,-700)
  Normal = (1,0,-8.418e-09)
  Start = (6774.56,16025.2,-100)
FEATURE [App::FeaturePython] Dimension427  # Draft dimension (typed FeaturePython)
  Dimline = (6774.56,16450,-700)
  Direction = (0,0,0)
  Distance = 260
  End = (6774.56,16185.2,-960)
  Normal = (1,0,-8.418e-09)
  Start = (6774.56,16185.2,-700)
FEATURE [Part::Part2DObjectPython] Rectangle384  # Draft 2D object (typed FeaturePython)
  ChamferSize = 0
  FilletRadius = 0
  Height = 300
  Length = 300
  MakeFace = true
  Placement = pos=(6774.56,21730.4,6000) rot=(0.57735,0.57735,0.57735;2.0944rad)
FEATURE [Part::Part2DObjectPython] Rectangle385  # Draft 2D object (typed FeaturePython)
  ChamferSize = 0
  FilletRadius = 0
  Height = 300
  Length = 300
  MakeFace = true
  Placement = pos=(6774.56,22030.4,6000) rot=(0.57735,0.57735,0.57735;2.0944rad)
FEATURE [Part::Part2DObjectPython] Rectangle386  # Draft 2D object (typed FeaturePython)
  ChamferSize = 0
  FilletRadius = 0
  Height = 300
  Length = 300
  MakeFace = true
  Placement = pos=(6774.56,22330.4,6000) rot=(0.57735,0.57735,0.57735;2.0944rad)
FEATURE [App::FeaturePython] Dimension428  # Draft dimension (typed FeaturePython)
  Dimline = (6774.56,950,6000)
  Direction = (0,0,0)
  Distance = 6960
  End = (6774.56,1651,6000)
  Normal = (1,0,-8.418e-09)
  Start = (6774.56,1651,-960)
FEATURE [App::FeaturePython] Dimension429  # Draft dimension (typed FeaturePython)
  Dimline = (6774.56,1250,6000)
  Direction = (0,0,0)
  Distance = 959.785
  End = (6774.56,1650.95,-0.21484)
  Normal = (1,0,-8.418e-09)
  Start = (6774.56,1651,-960)
FEATURE [App::FeaturePython] Dimension430  # Draft dimension (typed FeaturePython)
  Dimline = (6774.56,1250.29,-0.234504)
  Direction = (0,0,0)
  Distance = 3000
  End = (6774.56,2000,3000)
  Normal = (1,0,-8.418e-09)
  Start = (6774.56,2000,0)
FEATURE [App::FeaturePython] Dimension431  # Draft dimension (typed FeaturePython)
  Dimline = (6774.56,1250,6000)
  Direction = (0,0,0)
  Distance = 3000
  End = (6774.56,2000,6000)
  Normal = (1,0,-8.418e-09)
  Start = (6774.56,2000,3000)
FEATURE [App::FeaturePython] Dimension432  # Draft dimension (typed FeaturePython)
  Dimline = (6774.56,1550,6000)
  Direction = (0,0,0)
  Distance = 260
  End = (6774.56,1651,-700)
  Normal = (1,0,-8.418e-09)
  Start = (6774.56,1651,-960)
FEATURE [App::FeaturePython] Dimension433  # Draft dimension (typed FeaturePython)
  Dimline = (6774.56,1550,-700)
  Direction = (0,0,0)
  Distance = 599.785
  End = (6774.56,1650.95,-100.215)
  Normal = (1,0,-8.418e-09)
  Start = (6774.56,1651,-700)
FEATURE [App::FeaturePython] Dimension434  # Draft dimension (typed FeaturePython)
  Dimline = (6774.56,1549.95,-100.223)
  Direction = (0,0,0)
  Distance = 100
  End = (6774.56,2000,0)
  Normal = (1,0,-8.418e-09)
  Start = (6774.56,2000,-100)
FEATURE [App::FeaturePython] Dimension435  # Draft dimension (typed FeaturePython)
  Dimline = (6774.56,1549.95,0)
  Direction = (0,0,0)
  Distance = 2800
  End = (6774.56,2000,2800)
  Normal = (1,0,-8.418e-09)
  Start = (6774.56,2000,-1e-12)
FEATURE [App::FeaturePython] Dimension436  # Draft dimension (typed FeaturePython)
  Dimline = (6774.56,1549.95,2800)
  Direction = (0,0,0)
  Distance = 200
  End = (6774.56,2000,3000)
  Normal = (1,0,-8.418e-09)
  Start = (6774.56,2000,2800)
FEATURE [App::FeaturePython] Dimension437  # Draft dimension (typed FeaturePython)
  Dimline = (6774.56,1549.95,3000)
  Direction = (0,0,0)
  Distance = 2310
  End = (6774.56,2000,5310)
  Normal = (1,0,-8.418e-09)
  Start = (6774.56,2000,3000)
FEATURE [App::FeaturePython] Dimension438  # Draft dimension (typed FeaturePython)
  Dimline = (6774.56,1549.95,5972.79)
  Direction = (0,0,0)
  Distance = 490
  End = (6774.56,2000,5800)
  Normal = (1,0,-8.418e-09)
  Start = (6774.56,2000,5310)
FEATURE [App::FeaturePython] Dimension439  # Draft dimension (typed FeaturePython)
  Dimline = (6774.56,1550,6000)
  Direction = (0,0,0)
  Distance = 200
  End = (6774.56,2000,6000)
  Normal = (1,0,-8.418e-09)
  Start = (6774.56,2000,5800)
FEATURE [App::FeaturePython] Dimension440  # Draft dimension (typed FeaturePython)
  Dimline = (6774.56,3814.61,-1260)
  Direction = (0,0,0)
  Distance = 520
  End = (6774.56,4334.61,-960)
  Normal = (1,0,-8.418e-09)
  Start = (6774.56,3814.61,-960)
FEATURE [App::FeaturePython] Dimension441  # Draft dimension (typed FeaturePython)
  Dimline = (6774.56,4334.61,-1260)
  Direction = (0,0,0)
  Distance = 520
  End = (6774.56,13205,-960)
  Normal = (1,0,-8.418e-09)
  Start = (6774.56,12685,-960)
FEATURE [App::FeaturePython] Dimension442  # Draft dimension (typed FeaturePython)
  Dimline = (6774.56,13205,-1260)
  Direction = (0,0,0)
  Distance = 520.188
  End = (6774.56,16185.2,-960)
  Normal = (1,0,-8.418e-09)
  Start = (6774.56,15665,-960)
FEATURE [App::FeaturePython] Dimension443  # Draft dimension (typed FeaturePython)
  Dimline = (6774.56,3974.61,-400)
  Direction = (0,0,0)
  Distance = 200
  End = (6774.56,4174.61,-400)
  Normal = (1,0,-8.418e-09)
  Start = (6774.56,3974.61,-400)
FEATURE [App::FeaturePython] Dimension444  # Draft dimension (typed FeaturePython)
  Dimline = (6774.56,12845,-400)
  Direction = (0,0,0)
  Distance = 200
  End = (6774.56,13045,-400)
  Normal = (1,0,-8.418e-09)
  Start = (6774.56,12845,-400)
FEATURE [App::FeaturePython] Dimension445  # Draft dimension (typed FeaturePython)
  Dimline = (6774.56,15825.2,-400)
  Direction = (0,0,0)
  Distance = 200
  End = (6774.56,16025.2,-400)
  Normal = (1,0,-8.418e-09)
  Start = (6774.56,15825.2,-400)
FEATURE [App::FeaturePython] Dimension446  # Draft dimension (typed FeaturePython)
  Dimline = (6774.56,6350,2500)
  Direction = (0,0,0)
  Distance = 490
  End = (6774.56,6050,2310)
  Normal = (1,0,-8.418e-09)
  Start = (6774.56,6050,2800)
FEATURE [App::FeaturePython] Dimension447  # Draft dimension (typed FeaturePython)
  Dimline = (6774.56,7950,2500)
  Direction = (0,0,0)
  Distance = 490
  End = (6774.56,8250,2310)
  Normal = (1,0,-8.418e-09)
  Start = (6774.56,8250,2800)
FEATURE [App::FeaturePython] Dimension448  # Draft dimension (typed FeaturePython)
  Dimline = (6774.56,4449.61,2500)
  Direction = (0,0,0)
  Distance = 600
  End = (6774.56,4149.61,2200)
  Normal = (1,0,-8.418e-09)
  Start = (6774.56,4149.61,2800)
FEATURE [App::FeaturePython] Dimension449  # Draft dimension (typed FeaturePython)
  Dimline = (6774.56,4449.61,2200)
  Direction = (0,0,0)
  Distance = 1200
  End = (6774.56,4149.61,1000)
  Normal = (1,0,-8.418e-09)
  Start = (6774.56,4149.61,2200)
FEATURE [App::FeaturePython] Dimension450  # Draft dimension (typed FeaturePython)
  Dimline = (6774.56,4449.61,1000)
  Direction = (0,0,0)
  Distance = 1000
  End = (6774.56,4149.61,0)
  Normal = (1,0,-8.418e-09)
  Start = (6774.56,4149.61,1000)
FEATURE [App::FeaturePython] Dimension451  # Draft dimension (typed FeaturePython)
  Dimline = (6774.56,4449.61,0)
  Direction = (0,0,0)
  Distance = 100
  End = (6774.56,4149.61,-100)
  Normal = (1,0,-8.418e-09)
  Start = (6774.56,4149.61,0)
FEATURE [App::FeaturePython] Dimension452  # Draft dimension (typed FeaturePython)
  Dimline = (6774.56,6200,2010)
  Direction = (0,0,0)
  Distance = 150
  End = (6774.56,6050,2310)
  Normal = (1,0,-8.418e-09)
  Start = (6774.56,5900,2310)
FEATURE [App::FeaturePython] Dimension453  # Draft dimension (typed FeaturePython)
  Dimline = (6774.56,6050,2010)
  Direction = (0,0,0)
  Distance = 150
  End = (6774.56,8400,2310)
  Normal = (1,0,-8.418e-09)
  Start = (6774.56,8250,2310)
FEATURE [Part::Part2DObjectPython] Rectangle388  # Draft 2D object (typed FeaturePython)
  ChamferSize = 0
  FilletRadius = 0
  Height = 300
  Length = 300
  MakeFace = true
  Placement = pos=(6774.56,33350.4,2500) rot=(0.57735,0.57735,0.57735;2.0944rad)
FEATURE [App::FeaturePython] Dimension454  # Draft dimension (typed FeaturePython)
  Dimline = (6774.56,12570,2500)
  Direction = (0,0,0)
  Distance = 600
  End = (6774.56,12870,2800)
  Normal = (1,0,-8.418e-09)
  Start = (6774.56,12870,2200)
FEATURE [App::FeaturePython] Dimension455  # Draft dimension (typed FeaturePython)
  Dimline = (6774.56,12570,2200)
  Direction = (0,0,0)
  Distance = 2200
  End = (6774.56,12870,2200)
  Normal = (1,0,-8.418e-09)
  Start = (6774.56,12870,0)
FEATURE [App::FeaturePython] Dimension456  # Draft dimension (typed FeaturePython)
  Dimline = (6774.56,13320,2500)
  Direction = (0,0,0)
  Distance = 2200
  End = (6774.56,13120,0)
  Normal = (1,0,-8.418e-09)
  Start = (6774.56,13120,2200)
FEATURE [Part::Part2DObjectPython] Rectangle389  # Draft 2D object (typed FeaturePython)
  ChamferSize = 0
  FilletRadius = 0
  Height = 150
  Length = 150
  MakeFace = true
  Placement = pos=(6774.56,34750.4,2200) rot=(0.57735,0.57735,0.57735;2.0944rad)
FEATURE [App::FeaturePython] Dimension457  # Draft dimension (typed FeaturePython)
  Dimline = (6774.56,13820,2500)
  Direction = (0,0,0)
  Distance = 1000
  End = (6774.56,14120,2200)
  Normal = (1,0,-8.418e-09)
  Start = (6774.56,13120,2200)
FEATURE [App::FeaturePython] Dimension458  # Draft dimension (typed FeaturePython)
  Dimline = (6774.56,14120,2500)
  Direction = (0,0,0)
  Distance = 1730
  End = (6774.56,15850,2199.6)
  Normal = (1,0,-8.418e-09)
  Start = (6774.56,14120,2200)
FEATURE [App::FeaturePython] Dimension459  # Draft dimension (typed FeaturePython)
  Dimline = (6774.56,13970,2200)
  Direction = (0,0,0)
  Distance = 90
  End = (6774.56,14270,90)
  Normal = (1,0,-8.418e-09)
  Start = (6774.56,14270,-4e-12)
FEATURE [App::FeaturePython] Dimension460  # Draft dimension (typed FeaturePython)
  Dimline = (6774.56,13970,90)
  Direction = (0,0,0)
  Distance = 809.785
  End = (6774.56,14270,899.785)
  Normal = (1,0,-8.418e-09)
  Start = (6774.56,14270,90)
FEATURE [App::FeaturePython] Dimension462  # Draft dimension (typed FeaturePython)
  Dimline = (6774.56,13969.9,1439.76)
  Direction = (0,0,0)
  Distance = 820
  End = (6774.56,14270,2270)
  Normal = (1,0,-8.418e-09)
  Start = (6774.56,14270,1450)
FEATURE [App::FeaturePython] Dimension463  # Draft dimension (typed FeaturePython)
  Dimline = (6774.56,13969.9,1450)
  Direction = (0,0,0)
  Distance = 550
  End = (6774.56,14270,1450)
  Normal = (1,0,-8.418e-09)
  Start = (6774.56,14270,900)
FEATURE [Part::Part2DObjectPython] Rectangle390  # Draft 2D object (typed FeaturePython)
  ChamferSize = 0
  FilletRadius = 0
  Height = 150
  Length = 150
  MakeFace = true
  Placement = pos=(6774.56,34900.4,900) rot=(0.57735,0.57735,0.57735;2.0944rad)
FEATURE [App::FeaturePython] Dimension464  # Draft dimension (typed FeaturePython)
  Dimline = (6774.56,14270,1050)
  Direction = (0,0,0)
  Distance = 600.002
  End = (6774.56,14720,850)
  Normal = (1,0,-8.418e-09)
  Start = (6774.56,14120,850)
FEATURE [App::FeaturePython] Dimension465  # Draft dimension (typed FeaturePython)
  Dimline = (6774.56,14720,1050)
  Direction = (0,0,0)
  Distance = 619.988
  End = (6774.56,15340,850)
  Normal = (1,0,-8.418e-09)
  Start = (6774.56,14720,850)
FEATURE [Part::Part2DObjectPython] Rectangle391  # Draft 2D object (typed FeaturePython)
  ChamferSize = 0
  FilletRadius = 0
  Height = 150
  Length = 150
  MakeFace = true
  Placement = pos=(6774.56,34900.4,1300) rot=(0.57735,0.57735,0.57735;2.0944rad)
FEATURE [App::FeaturePython] Dimension466  # Draft dimension (typed FeaturePython)
  Dimline = (6774.56,14270,1300)
  Direction = (0,0,0)
  Distance = 600.002
  End = (6774.56,14720,1500)
  Normal = (1,0,-8.418e-09)
  Start = (6774.56,14120,1500)
FEATURE [App::FeaturePython] Dimension467  # Draft dimension (typed FeaturePython)
  Dimline = (6774.56,14720,1300)
  Direction = (0,0,0)
  Distance = 600
  End = (6774.56,15320,1500)
  Normal = (1,0,-8.418e-09)
  Start = (6774.56,14720,1500)
FEATURE [App::FeaturePython] Dimension468  # Draft dimension (typed FeaturePython)
  Dimline = (6774.56,15320,1300)
  Direction = (0,0,0)
  Distance = 229.99
  End = (6774.56,15550,1500)
  Normal = (1,0,-8.418e-09)
  Start = (6774.56,15320,1500)
FEATURE [App::FeaturePython] Dimension469  # Draft dimension (typed FeaturePython)
  Dimline = (6774.56,15550,1300)
  Direction = (0,0,0)
  Distance = 300
  End = (6774.56,15850,1450)
  Normal = (1,0,-8.418e-09)
  Start = (6774.56,15550,1450)
FEATURE [App::FeaturePython] Dimension470  # Draft dimension (typed FeaturePython)
  Dimline = (6774.56,3150,2500)
  Direction = (0,0,0)
  Distance = 1000
  End = (6774.56,3150,2200)
  Normal = (1,0,-8.418e-09)
  Start = (6774.56,2150,2200)
FEATURE [App::FeaturePython] Dimension471  # Draft dimension (typed FeaturePython)
  Dimline = (6774.56,3450,2200)
  Direction = (0,0,0)
  Distance = 2200
  End = (6774.56,3150,0)
  Normal = (1,0,-8.418e-09)
  Start = (6774.56,3150,2200)
FEATURE [Part::Part2DObjectPython] Rectangle392  # Draft 2D object (typed FeaturePython)
  ChamferSize = 0
  FilletRadius = 0
  Height = 300
  Length = 300
  MakeFace = true
  Placement = pos=(6774.56,29330.4,3000) rot=(0.57735,0.57735,0.57735;2.0944rad)
FEATURE [App::FeaturePython] Dimension472  # Draft dimension (typed FeaturePython)
  Dimline = (6774.56,8850,3300)
  Direction = (0,0,0)
  Distance = 1000
  End = (6774.56,8550,3000)
  Normal = (1,0,-8.418e-09)
  Start = (6774.56,8550,4000)
FEATURE [Part::Part2DObjectPython] Rectangle393  # Draft 2D object (typed FeaturePython)
  ChamferSize = 0
  FilletRadius = 0
  Height = 300
  Length = 300
  MakeFace = true
  Placement = pos=(6774.56,27930.4,5200) rot=(0.57735,0.57735,0.57735;2.0944rad)
FEATURE [Part::Part2DObjectPython] Rectangle394  # Draft 2D object (typed FeaturePython)
  ChamferSize = 0
  FilletRadius = 0
  Height = 300
  Length = 300
  MakeFace = true
  Placement = pos=(6774.56,26380.4,5500) rot=(0.57735,0.57735,0.57735;2.0944rad)
FEATURE [App::FeaturePython] Dimension473  # Draft dimension (typed FeaturePython)
  Dimline = (6774.56,5600,5500)
  Direction = (0,0,0)
  Distance = 600
  End = (6774.56,5900,5800)
  Normal = (1,0,-8.418e-09)
  Start = (6774.56,5900,5200)
FEATURE [App::FeaturePython] Dimension474  # Draft dimension (typed FeaturePython)
  Dimline = (6774.56,5600,5200)
  Direction = (0,0,0)
  Distance = 2200
  End = (6774.56,5900,5200)
  Normal = (1,0,-8.418e-09)
  Start = (6774.56,5900,3000)
FEATURE [App::FeaturePython] Dimension475  # Draft dimension (typed FeaturePython)
  Dimline = (6774.56,7150,5500)
  Direction = (0,0,0)
  Distance = 1000
  End = (6774.56,7150,5200)
  Normal = (1,0,-8.418e-09)
  Start = (6774.56,6150,5200)
FEATURE [App::FeaturePython] Dimension476  # Draft dimension (typed FeaturePython)
  Dimline = (6774.56,7450,5200)
  Direction = (0,0,0)
  Distance = 2200
  End = (6774.56,7150,3000)
  Normal = (1,0,-8.418e-09)
  Start = (6774.56,7150,5200)
FEATURE [App::FeaturePython] Dimension477  # Draft dimension (typed FeaturePython)
  Dimline = (6774.56,9577.64,900)
  Direction = (0,0,0)
  Distance = 180
  End = (6774.56,10107.2,1260)
  Normal = (1,0,-8.418e-09)
  Start = (6774.56,10107.2,1080)
FEATURE [App::FeaturePython] Dimension478  # Draft dimension (typed FeaturePython)
  Dimline = (6774.56,10372,1440)
  Direction = (0,0,0)
  Distance = 264.797
  End = (6774.56,10107.2,1080)
  Normal = (1,0,-8.418e-09)
  Start = (6774.56,9842.43,1080)
FEATURE [App::DocumentObjectGroup] Group079  label="Section - Longitudinal-Anno"
  Group = -> [Dimension413,Dimension414,Dimension415,Dimension416,Dimension417,Dimension418,Dimension419,Dimension420,Dimension421,Dimension422,Dimension423,Dimension424,Dimension425,Dimension426,Dimension427,Dimension428,Dimension429,Dimension430,Dimension431,Dimension432,Dimension433,Dimension434,Dimension435,Dimension436,Dimension437,Dimension438,Dimension439,Dimension440,Dimension441,Dimension442,+35 more]
FEATURE [Part::Part2DObjectPython] DWire233  # Draft 2D object (typed FeaturePython)
  ChamferSize = 0
  Closed = true
  End = (4800,47838,4000)
  FilletRadius = 0
  Length = 10340
  MakeFace = true
  Points = (4) [(4800,52008,4000),(4800,52008,3000),(4800,47838,3000),(4800,47838,4000)]
  Start = (4800,52008,4000)
FEATURE [Part::Part2DObjectPython] Rectangle395  # Draft 2D object (typed FeaturePython)
  ChamferSize = 0
  FilletRadius = 0
  Height = 300
  Length = 300
  MakeFace = true
  Placement = pos=(4800,41138,6300) rot=(0.57735,-0.57735,0.57735;4.18879rad)
FEATURE [Part::Part2DObjectPython] Rectangle396  # Draft 2D object (typed FeaturePython)
  ChamferSize = 0
  FilletRadius = 0
  Height = 300
  Length = 300
  MakeFace = true
  Placement = pos=(4800,40838,6300) rot=(0.57735,-0.57735,0.57735;4.18879rad)
FEATURE [Part::Part2DObjectPython] Rectangle397  # Draft 2D object (typed FeaturePython)
  ChamferSize = 0
  FilletRadius = 0
  Height = 300
  Length = 300
  MakeFace = true
  Placement = pos=(4800,40538,6300) rot=(0.57735,-0.57735,0.57735;4.18879rad)
FEATURE [Part::Part2DObjectPython] Rectangle398  # Draft 2D object (typed FeaturePython)
  ChamferSize = 0
  FilletRadius = 0
  Height = 150
  Length = 150
  MakeFace = true
  Placement = pos=(4800,42588,2350) rot=(0.57735,-0.57735,0.57735;4.18879rad)
FEATURE [App::DocumentObjectGroup] Construction
  Group = -> [Line043,Line048,Line049,Line050,Line057,Line058,Line061,Line065,Line066,Line069,Line070,Line084,Line085,Line086,Line087,Line088,Line089,Line090,Line091,Line092,Line093,Line094,Line095,Line097,Line098,Line099,Line100,Line101,Line102,Line105,Line106,Line107,Line108,Line109,Line110,Line111,Line112,Line113,Line114,Line115,Line116,Line117,Line118,Line119,Line120,Line121,Line122,Line123,Line124,Line125,+349 more]
FEATURE [App::DocumentObjectGroupPython] Building  # scripted group (container) (typed FeaturePython)
  Group = -> [Group,Construction,Stairs,Group003,Cut,Cut001,Group004,Group005,Group006,_d_vehicles,Extrusion022,Extrusion035,Extrusion038,Group014]
  Height = 0
FEATURE [App::FeaturePython] Section  label="Section level 1"  # WARN: FeaturePython — macro-defined, semantics opaque (R4)
  Objects = -> [Building,Clone033,Wall095,Space,Space001,Space009,Space002,Space006,Space010,Space004,Space008,Space005,Space007,Space003,Solid058,wc001,Part__Feature001,wc,Part__Feature,Group048,Group054,Group064,Group074]
  OnlySolids = true
  Placement = pos=(6000,9000,1500) rot=(0,0,1;0rad)
FEATURE [App::FeaturePython] Section001  label="Section level 2"  # WARN: FeaturePython — macro-defined, semantics opaque (R4)
  Objects = -> [Building,Window040,Window041,Window042,Clone033,Wall094,wc002,wc003,Part__Feature002,Solid056,Solid057,Part__Feature003,Group054]
  OnlySolids = true
  Placement = pos=(6000,9000,4600) rot=(0,0,1;0rad)
FEATURE [Part::Part2DObjectPython] Shape2DView001  label="Level 2 - Cut view"  # Draft 2D object (typed FeaturePython)
  Base = -> Section001
  HiddenLines = false
  Placement = pos=(42142,-0.388761,-4600) rot=(0,0,1;0rad)
  Projection = (0,0,1)
  ProjectionMode = 2
  SegmentLength = 0.05
  Tessellation = false
FEATURE [App::FeaturePython] Section002  label="Front Elevation"  # WARN: FeaturePython — macro-defined, semantics opaque (R4)
  Objects = -> [Building,Group075,Group073,Group074,Extrusion022]
  OnlySolids = true
  Placement = pos=(5990.59,-1537.83,4270.37) rot=(1,0,0;1.5708rad)
FEATURE [Part::Part2DObjectPython] Shape2DView002  # Draft 2D object (typed FeaturePython)
  Base = -> Section002
  HiddenLines = false
  Placement = pos=(-23885,5945,0) rot=(0,0,-1;1.5708rad)
  Projection = (0,0,1)
  ProjectionMode = 0
  SegmentLength = 0.05
  Tessellation = false
FEATURE [App::FeaturePython] Section003  label="Section - Longitudinal"  # WARN: FeaturePython — macro-defined, semantics opaque (R4)
  Objects = -> [Building,Group048,Group075,Group074,Group073]
  OnlySolids = true
  Placement = pos=(6774.56,9033.4,3010) rot=(0,1,0;1.5708rad)
FEATURE [Part::Part2DObjectPython] Shape2DView004  # Draft 2D object (typed FeaturePython)
  Base = -> Section003
  HiddenLines = false
  Placement = pos=(56577,656.865,-6774.56) rot=(0.57735,0.57735,0.57735;4.18879rad)
  Projection = (0,0,1)
  ProjectionMode = 2
  SegmentLength = 0.05
  Tessellation = false
FEATURE [Part::Part2DObjectPython] Shape2DView005  # Draft 2D object (typed FeaturePython)
  Base = -> Section003
  HiddenLines = false
  Placement = pos=(56577,656.865,0) rot=(0,0,1;1.5708rad)
  Projection = (0,0,1)
  ProjectionMode = 0
  SegmentLength = 0.05
  Tessellation = false
FEATURE [App::FeaturePython] Section004  label="Section Longitudinal 2"  # WARN: FeaturePython — macro-defined, semantics opaque (R4)
  Objects = -> [Building,Window040,Window041,Window042,Panel018,Panel002,Panel,Panel001,Panel003,Panel008,Panel009,Panel011,Panel010,Panel012,Panel013,Panel014,Panel016,Panel017,Panel015,Panel021,Panel024,Panel022,Panel020,Panel025,Panel023,Panel027,Panel029,Panel031,Panel033,Panel030,Group048,Group075,Group074,Group073]
  OnlySolids = true
  Placement = pos=(5186,10033.4,3010) rot=(0,1,0;1.5708rad)
FEATURE [Part::Part2DObjectPython] Shape2DView009  label="Level 1 - projection"  # Draft 2D object (typed FeaturePython)
  Base = -> Section
  HiddenLines = false
  Placement = pos=(25503.4,-0.388761,0) rot=(0,0,1;0rad)
  Projection = (0,0,1)
  ProjectionMode = 0
  SegmentLength = 0.05
  Tessellation = false
FEATURE [App::FeaturePython] Section005  label="East Elevation"  # WARN: FeaturePython — macro-defined, semantics opaque (R4)
  Objects = -> [Building,Group075,Group073,Group074]
  OnlySolids = true
  Placement = pos=(13970,8831.79,3759.22) rot=(0,1,0;1.5708rad)
FEATURE [Part::Part2DObjectPython] Shape2DView010  label="East Elevation001"  # Draft 2D object (typed FeaturePython)
  Base = -> Section005
  HiddenLines = false
  Placement = pos=(-26300,-3580,0) rot=(0,0,1;0rad)
  Projection = (0,0,1)
  ProjectionMode = 0
  SegmentLength = 0.05
  Tessellation = false
FEATURE [App::FeaturePython] Section006  label="Rear Elevation"  # WARN: FeaturePython — macro-defined, semantics opaque (R4)
  Objects = -> [Building,Group075,Group073,Group074]
  OnlySolids = true
  Placement = pos=(5193,17509,4145) rot=(-1,0,0;1.5708rad)
FEATURE [Part::Part2DObjectPython] Shape2DView011  label="Rear Elevation001"  # Draft 2D object (typed FeaturePython)
  Base = -> Section006
  HiddenLines = false
  Placement = pos=(-11940,-14702,0) rot=(0,0,1;1.5708rad)
  Projection = (0,0,1)
  ProjectionMode = 0
  SegmentLength = 0.05
  Tessellation = false
FEATURE [App::FeaturePython] Section007  label="West Elevation"  # WARN: FeaturePython — macro-defined, semantics opaque (R4)
  Objects = -> [Building,Group075,Group073,Group074]
  OnlySolids = true
  Placement = pos=(-1695.76,9000,3733) rot=(0,-1,0;1.5708rad)
FEATURE [Part::Part2DObjectPython] Shape2DView012  label="West Elevation001"  # Draft 2D object (typed FeaturePython)
  Base = -> Section007
  HiddenLines = false
  Placement = pos=(-8295,-26645,0) rot=(0,0,1;0rad)
  Projection = (0,0,1)
  ProjectionMode = 0
  SegmentLength = 0.05
  Tessellation = false
FEATURE [Part::Part2DObjectPython] Shape2DView013  # Draft 2D object (typed FeaturePython)
  Base = -> Section004
  HiddenLines = false
  Placement = pos=(56577,9965.85,-0.0147835) rot=(0,0,1;0rad)
  Projection = (0,0,1)
  ProjectionMode = 0
  SegmentLength = 0.05
  Tessellation = false
FEATURE [Part::Part2DObjectPython] Shape2DView014  # Draft 2D object (typed FeaturePython)
  Base = -> Section004
  HiddenLines = false
  Placement = pos=(56577,9965.85,-5186.01) rot=(-0.57735,-0.57735,-0.57735;2.0944rad)
  Projection = (0,0,1)
  ProjectionMode = 2
  SegmentLength = 0.05
  Tessellation = false
FEATURE [App::FeaturePython] Dimension024  # Draft dimension (typed FeaturePython)
  Dimline = (73228.2,12765.8,-3e-12)
  Direction = (0,0,0)
  Distance = 6400
  End = (64977,12965.8,-0.0148431)
  LinkedGeometry = -> [Shape2DView014]
  Normal = (0,0,1)
  Start = (58577,12965.8,-0.0148431)
  Support = -> Shape2DView014
FEATURE [App::FeaturePython] Dimension027  # Draft dimension (typed FeaturePython)
  Dimline = (73228.2,15765.8,-1.5e-11)
  Direction = (0,0,0)
  Distance = 40
  End = (61442,15965.8,-0.0148431)
  LinkedGeometry = -> [Shape2DView014]
  Normal = (0,0,1)
  Start = (61442,16005.8,-0.0148431)
  Support = -> Shape2DView014
FEATURE [App::DocumentObjectGroup] Group031
  Group = -> [Dimension024,Dimension027,Text026,Text027,Text028]
FEATURE [App::DocumentObjectGroup] Group018  label="Section Longitude"
  Group = -> [Group031,Group032]
FEATURE [App::DocumentObjectGroup] Group016  label="2D Documentation"
  Group = -> [Group017,Group018,Group019,Group023,Group028]
FEATURE [Part::Part2DObjectPython] Shape2DView  label="Level 1 - Cut view"  # Draft 2D object (typed FeaturePython)
  Base = -> Section
  HiddenLines = false
  Placement = pos=(25503.4,-0.388456,-1500) rot=(0,0,1;0rad)
  Projection = (0,0,1)
  ProjectionMode = 2
  SegmentLength = 0.05
  Tessellation = false
FEATURE [Drawing::FeatureViewPython] View003  label="View of Section Plan level 1"  # drawing view (typed FeaturePython)
  FontSize = 12
  LineWidth = 0.05
  RenderingMode = 1
  Rotation = 0
  Scale = 0.01
  ShowCut = false
  Source = -> Section
  ViewResult = <blob: 6659 chars omitted>
  Visible = false
  X = 50
  Y = 200
FEATURE [Drawing::FeatureViewPython] View004  label="View of Section Plan level 2"  # drawing view (typed FeaturePython)
  FontSize = 12
  LineWidth = 0.05
  RenderingMode = 1
  Rotation = 0
  Scale = 0.01
  ShowCut = false
  Source = -> Section001
  ViewResult = <g id="View004" transform="rotate(0.0,220.0,200.0) translate(220.0,200.0) scale(0.01,0.01)">\n<g   stroke="rgb(0, 0, 0)"\n   stroke-width="5.0px"\n   stroke-linecap="butt"\n   stroke-linejoin="miter"\n   fill="none"\n   transform="scale(1,-1)"\n  >\n<path id= "1" d=" M 10995 16000 L -5 16000 " />\n<path id= "2" d=" M 10995 2000 L 10995 16000 " />\n<path id= "3" d=" M -5 16000 L -5 2000 " />\n<path id= "4" d=" M -5 2000 L 10995 2000 " />\n<path id= "5" d=" M 5795 13020 L 5795 8400 " />\n<path id= "6" d=" M 5795 8400 L 4595 8400 " />\n<path id= "7" d=" M 4595 8400 L 4595 13020 " />\n<path id= "8" d=" M 4595 13020 L 5795 13020 " />\n<path id= "9" d=" M 5945 2055 L 10845 2055 " />\n<path id= "10" d=" M 5945 2095 L 10845 2095 " />\n<path id= "11" d=" M 5945 2055 L 5945 2095 " />\n<path id= "12" d=" M 10845 2055 L 10845 2095 " />\n<path id= "13" d=" M 5945 2095 L 10845 2095 " />\n<path id= "14" d=" M 10900 2150 L 10900 5750 " />\n<path id= "15" d=" M 10940 2150 L 10940 5750 " />\n<path id= "16" d=" M 10900 2150 L 10900 5750 " />\n<path id= "17" d=" M 10940 2150 L 10900 2150 " />\n<path id= "18" d=" M 10940 5750 L 10900 5750 " />\n</g>\n</g>
  Visible = false
  X = 220
  Y = 200
FEATURE [Part::Part2DObjectPython] Shape2DView015  label="Level 2 - Projection"  # Draft 2D object (typed FeaturePython)
  Base = -> Section001
  HiddenLines = false
  Placement = pos=(42142,-0.388761,0) rot=(0,0,1;0rad)
  Projection = (0,0,1)
  ProjectionMode = 0
  SegmentLength = 0.05
  Tessellation = false
FEATURE [App::DocumentObjectGroup] Group007  label="plans"
  Group = -> [Shape2DView009,Shape2DView,Shape2DView001,Shape2DView015,Group009]
FEATURE [Drawing::FeatureViewPython] View005  label="View of Section001"  # drawing view (typed FeaturePython)
  FontSize = 12
  LineWidth = 0.05
  RenderingMode = 1
  Rotation = 0
  Scale = 0.01
  ShowCut = false
  ShowFill = false
  Source = -> Section001
  ViewResult = <g id="View005" transform="rotate(0.0,220.0,200.0) translate(220.0,200.0) scale(0.01,0.01)">\n<g   stroke="rgb(0, 0, 0)"\n   stroke-width="5.0px"\n   stroke-linecap="butt"\n   stroke-linejoin="miter"\n   fill="none"\n   transform="scale(1,-1)"\n  >\n<path id= "1" d=" M 10995 16000 L -5 16000 " />\n<path id= "2" d=" M 10995 2000 L 10995 16000 " />\n<path id= "3" d=" M -5 16000 L -5 2000 " />\n<path id= "4" d=" M -5 2000 L 10995 2000 " />\n<path id= "5" d=" M 5795 13020 L 5795 8400 " />\n<path id= "6" d=" M 5795 8400 L 4595 8400 " />\n<path id= "7" d=" M 4595 8400 L 4595 13020 " />\n<path id= "8" d=" M 4595 13020 L 5795 13020 " />\n<path id= "9" d=" M 5945 2055 L 10845 2055 " />\n<path id= "10" d=" M 5945 2095 L 10845 2095 " />\n<path id= "11" d=" M 5945 2055 L 5945 2095 " />\n<path id= "12" d=" M 10845 2055 L 10845 2095 " />\n<path id= "13" d=" M 5945 2095 L 10845 2095 " />\n<path id= "14" d=" M 10900 2150 L 10900 5750 " />\n<path id= "15" d=" M 10940 2150 L 10940 5750 " />\n<path id= "16" d=" M 10900 2150 L 10900 5750 " />\n<path id= "17" d=" M 10940 2150 L 10900 2150 " />\n<path id= "18" d=" M 10940 5750 L 10900 5750 " />\n</g>\n</g>
  Visible = false
  X = 220
  Y = 200
FEATURE [Drawing::FeatureViewPython] View  label="View of Section"  # drawing view (typed FeaturePython)
  FontSize = 12
  LineWidth = 0.05
  RenderingMode = 1
  Rotation = 0
  Scale = 0.01
  ShowCut = false
  ShowFill = false
  Source = -> Section
  ViewResult = <blob: 6656 chars omitted>
  Visible = false
  X = 50
  Y = 200
FEATURE [Drawing::FeatureViewPython] View006  label="View of Section002"  # drawing view (typed FeaturePython)
  FontSize = 12
  LineWidth = 0.05
  RenderingMode = 1
  Rotation = 0
  Scale = 0.01
  ShowCut = false
  ShowFill = false
  Source = -> Section001
  ViewResult = <g id="View006" transform="rotate(0.0,220.0,200.0) translate(220.0,200.0) scale(0.01,0.01)">\n<g   stroke="rgb(0, 0, 0)"\n   stroke-width="5.0px"\n   stroke-linecap="butt"\n   stroke-linejoin="miter"\n   fill="none"\n   transform="scale(1,-1)"\n  >\n<path id= "1" d=" M 10995 16000 L -5 16000 " />\n<path id= "2" d=" M 10995 2000 L 10995 16000 " />\n<path id= "3" d=" M -5 16000 L -5 2000 " />\n<path id= "4" d=" M -5 2000 L 10995 2000 " />\n<path id= "5" d=" M 5795 13020 L 5795 8400 " />\n<path id= "6" d=" M 5795 8400 L 4595 8400 " />\n<path id= "7" d=" M 4595 8400 L 4595 13020 " />\n<path id= "8" d=" M 4595 13020 L 5795 13020 " />\n<path id= "9" d=" M 5945 2055 L 10845 2055 " />\n<path id= "10" d=" M 5945 2095 L 10845 2095 " />\n<path id= "11" d=" M 5945 2055 L 5945 2095 " />\n<path id= "12" d=" M 10845 2055 L 10845 2095 " />\n<path id= "13" d=" M 5945 2095 L 10845 2095 " />\n<path id= "14" d=" M 10900 2150 L 10900 5750 " />\n<path id= "15" d=" M 10940 2150 L 10940 5750 " />\n<path id= "16" d=" M 10900 2150 L 10900 5750 " />\n<path id= "17" d=" M 10940 2150 L 10900 2150 " />\n<path id= "18" d=" M 10940 5750 L 10900 5750 " />\n</g>\n</g>
  Visible = false
  X = 220
  Y = 200
FEATURE [App::FeaturePython] Section008  label="Longitudinal section 3"  # WARN: FeaturePython — macro-defined, semantics opaque (R4)
  Objects = -> [Building,Group064,Group048,Group069,Group058,Group075,Group074,Group073]
  OnlySolids = true
  Placement = pos=(4800,8000,4000) rot=(0,-1,0;1.5708rad)
FEATURE [Part::Part2DObjectPython] Shape2DView016  # Draft 2D object (typed FeaturePython)
  Base = -> Section008
  HiddenLines = false
  Placement = pos=(74577,-9163.72,4800) rot=(0.57735,-0.57735,-0.57735;4.18879rad)
  Projection = (0,0,1)
  ProjectionMode = 2
  SegmentLength = 0.05
  Tessellation = false
FEATURE [Part::Part2DObjectPython] Shape2DView018  # Draft 2D object (typed FeaturePython)
  Base = -> Section008
  HiddenLines = false
  Placement = pos=(74577,-9163.72,0) rot=(0,0,-1;1.5708rad)
  Projection = (0,0,1)
  ProjectionMode = 0
  SegmentLength = 0.05
  Tessellation = false
FEATURE [App::DocumentObjectGroup] Group008  label="Elevations"
  Group = -> [Shape2DView002,Shape2DView004,Shape2DView005,Shape2DView010,Shape2DView011,Shape2DView012,Shape2DView013,Shape2DView014,Shape2DView016,Shape2DView018,Shape2DView019,Shape2DView020]
FEATURE [App::DocumentObjectGroup] Group071  label="Sections Cuts & Elevations"
  Group = -> [Section008,Section005,Section006,Section007,Section,Section001,Section002,Section003,Section004,Section009]
FEATURE [Drawing::FeatureViewPython] View007  label="View of Section008"  # drawing view (typed FeaturePython)
  FontSize = 12
  LineWidth = 0.05
  RenderingMode = 1
  Rotation = 90
  Scale = 0.01
  ShowCut = false
  ShowFill = false
  Source = -> Section008
  ViewResult = <blob: 162694 chars omitted>
  Visible = true
  X = 200
  Y = 280
FEATURE [App::FeaturePython] Section010  label="Roof"  # WARN: FeaturePython — macro-defined, semantics opaque (R4)
  Objects = -> [Building]
  OnlySolids = true
  Placement = pos=(4486.26,8952.82,8265.16) rot=(0,0,1;0rad)
FEATURE [Part::Part2DObjectPython] Shape2DView021  # Draft 2D object (typed FeaturePython)
  Base = -> Section010
  HiddenLines = false
  Placement = pos=(41308,-16910,0) rot=(0,0,1;0rad)
  Projection = (0,0,1)
  ProjectionMode = 0
  SegmentLength = 0.05
  Tessellation = false
FEATURE [Part::Part2DObjectPython] Shape2DView022  # Draft 2D object (typed FeaturePython)
  Base = -> Section010
  HiddenLines = false
  Placement = pos=(41308,-16910,0) rot=(0,0,1;0rad)
  Projection = (0,0,1)
  ProjectionMode = 0
  SegmentLength = 0.05
  Tessellation = false
FEATURE [Drawing::FeatureViewPython] View011  label="View of Section011"  # drawing view (typed FeaturePython)
  FontSize = 12
  LineWidth = 0.1
  RenderingMode = 1
  Rotation = 0
  Scale = 0.01
  ShowCut = false
  ShowFill = false
  Source = -> Section010
  ViewResult = <blob: 226966 chars omitted>
  Visible = true
  X = 220
  Y = 200
FEATURE [Part::Part2DObjectPython] Shape2DView024  # Draft 2D object (typed FeaturePython)
  Base = -> Section003
  HiddenLines = false
  Placement = pos=(0,20780.4,0) rot=(0,0,1;0rad)
  Projection = (0,0,1)
  ProjectionMode = 2
  SegmentLength = 0.05
  Tessellation = false
FEATURE [Part::Part2DObjectPython] Shape2DView025  # Draft 2D object (typed FeaturePython)
  Base = -> Section003
  HiddenLines = false
  Placement = pos=(6774.56,20780.4,0) rot=(0.707107,0,0.707107;3.14159rad)
  Projection = (0,0,1)
  ProjectionMode = 0
  SegmentLength = 0.05
  Tessellation = false
FEATURE [Part::Part2DObjectPython] Shape2DView026  # Draft 2D object (typed FeaturePython)
  Base = -> Section003
  HiddenLines = false
  Projection = (0,0,1)
  ProjectionMode = 2
  SegmentLength = 0.05
  Tessellation = false
FEATURE [App::DocumentObjectGroup] Group078  label="Shape2dviews for dimensions extraction"
  Group = -> [Shape2DView023,Shape2DView026,Shape2DView024,Shape2DView025]
FEATURE [Part::Part2DObjectPython] Shape2DView027  # Draft 2D object (typed FeaturePython)
  Base = -> Section008
  HiddenLines = false
  Placement = pos=(0,39288,0) rot=(0,0,1;0rad)
  Projection = (0,0,1)
  ProjectionMode = 2
  SegmentLength = 0.05
  Tessellation = false
FEATURE [Part::Part2DObjectPython] Shape2DView028  # Draft 2D object (typed FeaturePython)
  Base = -> Section008
  HiddenLines = false
  Placement = pos=(4800,39288,0) rot=(0.707107,0,-0.707107;3.14159rad)
  Projection = (0,0,1)
  ProjectionMode = 0
  SegmentLength = 0.05
  Tessellation = false
FEATURE [App::FeaturePython] Dimension479  # Draft dimension (typed FeaturePython)
  Dimline = (4800,949.954,6000)
  Direction = (0,0,0)
  Distance = 6960
  End = (4800,1849.95,-960)
  Normal = (-1,0,0)
  Start = (4800,1849.95,6000)
FEATURE [App::FeaturePython] Dimension480  # Draft dimension (typed FeaturePython)
  Dimline = (4800,1249.95,6000)
  Direction = (0,0,0)
  Distance = 3000
  End = (4800,1999.95,3000)
  Normal = (-1,0,0)
  Start = (4800,1999.95,6000)
FEATURE [App::FeaturePython] Dimension481  # Draft dimension (typed FeaturePython)
  Dimline = (4800,1249.95,3000)
  Direction = (0,0,0)
  Distance = 3000
  End = (4800,1999.95,0)
  Normal = (-1,0,0)
  Start = (4800,1999.95,3000)
FEATURE [App::FeaturePython] Dimension482  # Draft dimension (typed FeaturePython)
  Dimline = (4800,1249.95,0)
  Direction = (0,0,0)
  Distance = 960
  End = (4800,2149.95,-960)
  Normal = (-1,0,0)
  Start = (4800,2149.95,0)
FEATURE [App::FeaturePython] Dimension483  # Draft dimension (typed FeaturePython)
  Dimline = (4800,1549.95,6000)
  Direction = (0,0,0)
  Distance = 200
  End = (4800,1999.95,5800)
  Normal = (-1,0,0)
  Start = (4800,1999.95,6000)
FEATURE [App::FeaturePython] Dimension484  # Draft dimension (typed FeaturePython)
  Dimline = (4800,1549.95,5800)
  Direction = (0,0,0)
  Distance = 600.632
  End = (4800,1999.95,5199.37)
  Normal = (-1,0,0)
  Start = (4800,1999.95,5800)
FEATURE [App::FeaturePython] Dimension485  # Draft dimension (typed FeaturePython)
  Dimline = (4800,1549.95,5199.37)
  Direction = (0,0,0)
  Distance = 1200.63
  End = (4800,1999.95,3999.37)
  Normal = (-1,0,0)
  Start = (4800,1999.95,5200)
FEATURE [App::FeaturePython] Dimension486  # Draft dimension (typed FeaturePython)
  Dimline = (4800,1549.95,3999.37)
  Direction = (0,0,0)
  Distance = 999.368
  End = (4800,1999.95,3000)
  Normal = (-1,0,0)
  Start = (4800,1999.95,3999.37)
FEATURE [App::FeaturePython] Dimension487  # Draft dimension (typed FeaturePython)
  Dimline = (4800,1549.95,3000)
  Direction = (0,0,0)
  Distance = 200
  End = (4800,1999.95,2800)
  Normal = (-1,0,0)
  Start = (4800,1999.95,3000)
FEATURE [App::FeaturePython] Dimension488  # Draft dimension (typed FeaturePython)
  Dimline = (4800,1549.95,2800)
  Direction = (0,0,0)
  Distance = 600
  End = (4800,1999.95,2200)
  Normal = (-1,0,0)
  Start = (4800,1999.95,2800)
FEATURE [App::FeaturePython] Dimension489  # Draft dimension (typed FeaturePython)
  Dimline = (4800,1549.95,2200)
  Direction = (0,0,0)
  Distance = 1200
  End = (4800,1999.95,1000)
  Normal = (-1,0,0)
  Start = (4800,1999.95,2200)
FEATURE [App::FeaturePython] Dimension490  # Draft dimension (typed FeaturePython)
  Dimline = (4800,1549.95,1000)
  Direction = (0,0,0)
  Distance = 1100
  End = (4800,1999.95,-100)
  Normal = (-1,0,0)
  Start = (4800,1999.95,1000)
FEATURE [App::FeaturePython] Dimension491  # Draft dimension (typed FeaturePython)
  Dimline = (4800,1549.95,-100)
  Direction = (0,0,0)
  Distance = 600
  End = (4800,1974.95,-700)
  Normal = (-1,0,0)
  Start = (4800,1974.95,-100)
FEATURE [App::FeaturePython] Dimension492  # Draft dimension (typed FeaturePython)
  Dimline = (4800,1549.95,-700)
  Direction = (0,0,0)
  Distance = 260
  End = (4800,1814.95,-960)
  Normal = (-1,0,0)
  Start = (4800,1814.95,-700)
FEATURE [Part::Part2DObjectPython] Rectangle400  # Draft 2D object (typed FeaturePython)
  ChamferSize = 0
  FilletRadius = 0
  Height = 300
  Length = 300
  MakeFace = true
  Placement = pos=(4800,56038,-660) rot=(0.57735,-0.57735,0.57735;4.18879rad)
FEATURE [Part::Part2DObjectPython] Rectangle401  # Draft 2D object (typed FeaturePython)
  ChamferSize = 0
  FilletRadius = 0
  Height = 300
  Length = 300
  MakeFace = true
  Placement = pos=(4800,56338,-660) rot=(0.57735,-0.57735,0.57735;4.18879rad)
FEATURE [Part::Part2DObjectPython] Rectangle402  # Draft 2D object (typed FeaturePython)
  ChamferSize = 0
  FilletRadius = 0
  Height = 300
  Length = 300
  MakeFace = true
  Placement = pos=(4800,56338,6300) rot=(0.57735,-0.57735,0.57735;4.18879rad)
FEATURE [Part::Part2DObjectPython] Rectangle403  # Draft 2D object (typed FeaturePython)
  ChamferSize = 0
  FilletRadius = 0
  Height = 300
  Length = 300
  MakeFace = true
  Placement = pos=(4800,56038,6300) rot=(0.57735,-0.57735,0.57735;4.18879rad)
FEATURE [Part::Part2DObjectPython] Rectangle404  # Draft 2D object (typed FeaturePython)
  ChamferSize = 0
  FilletRadius = 0
  Height = 300
  Length = 300
  MakeFace = true
  Placement = pos=(4800,55738,6300) rot=(0.57735,-0.57735,0.57735;4.18879rad)
FEATURE [App::FeaturePython] Dimension493  # Draft dimension (typed FeaturePython)
  Dimline = (4800,17050,6000)
  Direction = (0,0,0)
  Distance = 6960
  End = (4800,16150,6000)
  Normal = (-1,0,0)
  Start = (4800,16150,-960)
FEATURE [App::FeaturePython] Dimension494  # Draft dimension (typed FeaturePython)
  Dimline = (4800,16750,-660)
  Direction = (0,0,0)
  Distance = 860
  End = (4800,16000,-100)
  Normal = (-1,0,0)
  Start = (4800,16000,-960)
FEATURE [App::FeaturePython] Dimension495  # Draft dimension (typed FeaturePython)
  Dimline = (4800,16750,-100)
  Direction = (0,0,0)
  Distance = 3000
  End = (4800,15850,3000)
  Normal = (-1,0,0)
  Start = (4800,15850,3e-12)
FEATURE [App::FeaturePython] Dimension496  # Draft dimension (typed FeaturePython)
  Dimline = (4800,16750,3e-12)
  Direction = (0,0,0)
  Distance = 100
  End = (4800,15850,0)
  Normal = (-1,0,0)
  Start = (4800,15850,-100)
FEATURE [App::FeaturePython] Dimension497  # Draft dimension (typed FeaturePython)
  Dimline = (4800,16750,6000)
  Direction = (0,0,0)
  Distance = 3000
  End = (4800,16000,6000)
  Normal = (-1,0,0)
  Start = (4800,16000,3000)
FEATURE [App::FeaturePython] Dimension499  # Draft dimension (typed FeaturePython)
  Dimline = (4800,16450,-660)
  Direction = (0,0,0)
  Distance = 600
  End = (4800,16025,-100)
  Normal = (-1,0,0)
  Start = (4800,16025,-700)
FEATURE [App::FeaturePython] Dimension500  # Draft dimension (typed FeaturePython)
  Dimline = (4800,16450,-100)
  Direction = (0,0,0)
  Distance = 200
  End = (4800,16000,3000)
  Normal = (-1,0,0)
  Start = (4800,16000,2800)
FEATURE [App::FeaturePython] Dimension501  # Draft dimension (typed FeaturePython)
  Dimline = (4800,16450,3000)
  Direction = (0,0,0)
  Distance = 1000
  End = (4800,16000,4000)
  Normal = (-1,0,0)
  Start = (4800,16000,3000)
FEATURE [App::FeaturePython] Dimension502  # Draft dimension (typed FeaturePython)
  Dimline = (4800,16450,4000)
  Direction = (0,0,0)
  Distance = 1200
  End = (4800,16000,5200)
  Normal = (-1,0,0)
  Start = (4800,16000,4000)
FEATURE [App::FeaturePython] Dimension503  # Draft dimension (typed FeaturePython)
  Dimline = (4800,16450,5200)
  Direction = (0,0,0)
  Distance = 600
  End = (4800,16000,5800)
  Normal = (-1,0,0)
  Start = (4800,16000,5200)
FEATURE [App::FeaturePython] Dimension504  # Draft dimension (typed FeaturePython)
  Dimline = (4800,16450,5800)
  Direction = (0,0,0)
  Distance = 200
  End = (4800,16000,6000)
  Normal = (-1,0,0)
  Start = (4800,16000,5800)
FEATURE [App::FeaturePython] Dimension505  # Draft dimension (typed FeaturePython)
  Dimline = (4800,3149.95,2350)
  Direction = (0,0,0)
  Distance = 1000
  End = (4800,2149.95,2200)
  Normal = (-1,0,0)
  Start = (4800,3149.95,2200)
FEATURE [App::FeaturePython] Dimension506  # Draft dimension (typed FeaturePython)
  Dimline = (4800,3299.95,2220)
  Direction = (0,0,0)
  Distance = 2195
  End = (4800,3149.95,2200)
  Normal = (-1,0,0)
  Start = (4800,3149.95,5)
FEATURE [Part::Part2DObjectPython] Rectangle405  # Draft 2D object (typed FeaturePython)
  ChamferSize = 0
  FilletRadius = 0
  Height = 150
  Length = 150
  MakeFace = true
  Placement = pos=(4800,47538,2460) rot=(0.57735,-0.57735,0.57735;4.18879rad)
FEATURE [App::FeaturePython] Dimension507  # Draft dimension (typed FeaturePython)
  Dimline = (4800,4299.57,2200)
  Direction = (0,0,0)
  Distance = 2200
  End = (4800,4149.57,2200)
  Normal = (-1,0,0)
  Start = (4800,4149.57,0)
FEATURE [App::FeaturePython] Dimension508  # Draft dimension (typed FeaturePython)
  Dimline = (4800,4299.57,2350)
  Direction = (0,0,0)
  Distance = 600
  End = (4800,4149.57,2800)
  Normal = (-1,0,0)
  Start = (4800,4149.57,2200)
FEATURE [App::FeaturePython] Dimension509  # Draft dimension (typed FeaturePython)
  Dimline = (4800,8099.95,2460)
  Direction = (0,0,0)
  Distance = 490
  End = (4800,8249.95,2310)
  Normal = (-1,0,0)
  Start = (4800,8249.95,2800)
FEATURE [Part::Part2DObjectPython] Rectangle406  # Draft 2D object (typed FeaturePython)
  ChamferSize = 0
  FilletRadius = 0
  Height = 150
  Length = 150
  MakeFace = true
  Placement = pos=(4800,47538,4000) rot=(0.57735,-0.57735,0.57735;4.18879rad)
FEATURE [App::FeaturePython] Dimension510  # Draft dimension (typed FeaturePython)
  Dimline = (4800,8099.95,3925)
  Direction = (0,0,0)
  Distance = 1000
  End = (4800,8249.95,3000)
  Normal = (-1,0,0)
  Start = (4800,8249.95,4000)
FEATURE [Part::Part2DObjectPython] Rectangle407  # Draft 2D object (typed FeaturePython)
  ChamferSize = 0
  FilletRadius = 0
  Height = 150
  Length = 150
  MakeFace = true
  Placement = pos=(4800,47538,4150) rot=(0.57735,-0.57735,0.57735;4.18879rad)
FEATURE [App::FeaturePython] Dimension511  # Draft dimension (typed FeaturePython)
  Dimline = (4800,8249.95,4150)
  Direction = (0,0,0)
  Distance = 150
  End = (4800,8249.95,4000)
  Normal = (-1,0,0)
  Start = (4800,8399.95,4000)
FEATURE [Part::Part2DObjectPython] Rectangle408  # Draft 2D object (typed FeaturePython)
  ChamferSize = 0
  FilletRadius = 0
  Height = 150
  Length = 150
  MakeFace = true
  Placement = pos=(4800,47538,2310) rot=(0.57735,-0.57735,0.57735;4.18879rad)
FEATURE [App::FeaturePython] Dimension512  # Draft dimension (typed FeaturePython)
  Dimline = (4800,8249.95,2160)
  Direction = (0,0,0)
  Distance = 150
  End = (4800,8249.95,2310)
  Normal = (-1,0,0)
  Start = (4800,8399.95,2310)
FEATURE [App::FeaturePython] Dimension513  # Draft dimension (typed FeaturePython)
  Dimline = (4800,8099.95,3000)
  Direction = (0,0,0)
  Distance = 200
  End = (4800,8249.95,2800)
  Normal = (-1,0,0)
  Start = (4800,8249.95,3000)
FEATURE [Part::Part2DObjectPython] Rectangle409  # Draft 2D object (typed FeaturePython)
  ChamferSize = 0
  FilletRadius = 0
  Height = 150
  Length = 150
  MakeFace = true
  Placement = pos=(4800,47806.4,330) rot=(0.57735,-0.57735,0.57735;4.18879rad)
FEATURE [App::FeaturePython] Dimension514  # Draft dimension (typed FeaturePython)
  Dimline = (4800,8368.4,180)
  Direction = (0,0,0)
  Distance = 180
  End = (4800,8518.4,0)
  Normal = (-1,0,0)
  Start = (4800,8518.4,180)
FEATURE [Part::Part2DObjectPython] Rectangle410  # Draft 2D object (typed FeaturePython)
  ChamferSize = 0
  FilletRadius = 0
  Height = 150
  Length = 150
  MakeFace = true
  Placement = pos=(4800,47806.4,480) rot=(0.57735,-0.57735,0.57735;4.18879rad)
FEATURE [App::FeaturePython] Dimension515  # Draft dimension (typed FeaturePython)
  Dimline = (4800,8518.4,480)
  Direction = (0,0,0)
  Distance = 264.797
  End = (4800,8518.4,180)
  Normal = (-1,0,0)
  Start = (4800,8783.2,180)
FEATURE [Part::Part2DObjectPython] Rectangle411  # Draft 2D object (typed FeaturePython)
  ChamferSize = 0
  FilletRadius = 0
  Height = 150
  Length = 150
  MakeFace = true
  Placement = pos=(4800,49988,2350) rot=(0.57735,-0.57735,0.57735;4.18879rad)
FEATURE [App::FeaturePython] Dimension517  # Draft dimension (typed FeaturePython)
  Dimline = (4800,10700,2200)
  Direction = (0,0,0)
  Distance = 2200
  End = (4800,10550,2200)
  Normal = (-1,0,0)
  Start = (4800,10550,0)
FEATURE [Part::Part2DObjectPython] Rectangle412  # Draft 2D object (typed FeaturePython)
  ChamferSize = 0
  FilletRadius = 0
  Height = 150
  Length = 150
  MakeFace = true
  Placement = pos=(4800,49988,2500) rot=(0.57735,-0.57735,0.57735;4.18879rad)
FEATURE [App::FeaturePython] Dimension518  # Draft dimension (typed FeaturePython)
  Dimline = (4800,10550,2500)
  Direction = (0,0,0)
  Distance = 2000
  End = (4800,8549.95,2200)
  Normal = (-1,0,0)
  Start = (4800,10550,2200)
FEATURE [App::FeaturePython] Dimension519  # Draft dimension (typed FeaturePython)
  Dimline = (4800,10550,2350)
  Direction = (0,0,0)
  Distance = 1003
  End = (4800,9546.95,2200)
  Normal = (-1,0,0)
  Start = (4800,10550,2200)
FEATURE [App::FeaturePython] Dimension520  # Draft dimension (typed FeaturePython)
  Dimline = (4800,9546.95,2350)
  Direction = (0,0,0)
  Distance = 1000
  End = (4800,8549.95,2200)
  Normal = (-1,0,0)
  Start = (4800,9549.95,2200)
FEATURE [Part::Part2DObjectPython] Rectangle413  # Draft 2D object (typed FeaturePython)
  ChamferSize = 0
  FilletRadius = 0
  Height = 150
  Length = 150
  MakeFace = true
  Placement = pos=(4800,51638,2345.35) rot=(0.57735,-0.57735,0.57735;4.18879rad)
FEATURE [App::FeaturePython] Dimension521  # Draft dimension (typed FeaturePython)
  Dimline = (4800,11200,2347.67)
  Direction = (0,0,0)
  Distance = 1000
  End = (4800,11200,2197.67)
  Normal = (-1,0,0)
  Start = (4800,12200,2197.67)
FEATURE [App::FeaturePython] Dimension522  # Draft dimension (typed FeaturePython)
  Dimline = (4800,12350,2195.35)
  Direction = (0,0,0)
  Distance = 1197.67
  End = (4800,12200,2195.35)
  Normal = (-1,0,0)
  Start = (4800,12200,997.674)
FEATURE [Part::Part2DObjectPython] Rectangle414  # Draft 2D object (typed FeaturePython)
  ChamferSize = 0
  FilletRadius = 0
  Height = 150
  Length = 150
  MakeFace = true
  Placement = pos=(4800,53558,2420) rot=(0.57735,-0.57735,0.57735;4.18879rad)
FEATURE [App::FeaturePython] Dimension523  # Draft dimension (typed FeaturePython)
  Dimline = (4800,13687,1917)
  Direction = (0,0,0)
  Distance = 2200
  End = (4800,14020,2200)
  Normal = (-1,0,0)
  Start = (4800,14020,0)
FEATURE [App::FeaturePython] Dimension524  # Draft dimension (typed FeaturePython)
  Dimline = (4800,13870,2350)
  Direction = (0,0,0)
  Distance = 900
  End = (4800,13120,2200)
  Normal = (-1,0,0)
  Start = (4800,14020,2200)
FEATURE [Part::Part2DObjectPython] Rectangle415  # Draft 2D object (typed FeaturePython)
  ChamferSize = 0
  FilletRadius = 0
  Height = 150
  Length = 150
  MakeFace = true
  Placement = pos=(4800,54538,1050) rot=(0.57735,-0.57735,0.57735;4.18879rad)
FEATURE [App::FeaturePython] Dimension525  # Draft dimension (typed FeaturePython)
  Dimline = (4800,15550,2420)
  Direction = (0,0,0)
  Distance = 300
  End = (4800,15550,2270)
  Normal = (-1,0,0)
  Start = (4800,15850,2270)
FEATURE [App::FeaturePython] Dimension526  # Draft dimension (typed FeaturePython)
  Dimline = (4800,15400,2420)
  Direction = (0,0,0)
  Distance = 1430.05
  End = (4800,14119.9,2270)
  Normal = (-1,0,0)
  Start = (4800,15550,2270)
FEATURE [App::FeaturePython] Dimension529  # Draft dimension (typed FeaturePython)
  Dimline = (4800,15100,1050)
  Direction = (0,0,0)
  Distance = 820
  End = (4800,15550,1450)
  Normal = (-1,0,0)
  Start = (4800,15550,2270)
FEATURE [App::FeaturePython] Dimension530  # Draft dimension (typed FeaturePython)
  Dimline = (4800,15100,1450)
  Direction = (0,0,0)
  Distance = 550
  End = (4800,15550,900)
  Normal = (-1,0,0)
  Start = (4800,15550,1450)
FEATURE [App::FeaturePython] Dimension531  # Draft dimension (typed FeaturePython)
  Dimline = (4800,15100,900)
  Direction = (0,0,0)
  Distance = 810
  End = (4800,15250,89.9998)
  Normal = (-1,0,0)
  Start = (4800,15250,900)
FEATURE [App::FeaturePython] Dimension532  # Draft dimension (typed FeaturePython)
  Dimline = (4800,15100,90.002)
  Direction = (0,0,0)
  Distance = 89.9998
  End = (4800,15250,0)
  Normal = (-1,0,0)
  Start = (4800,15250,89.9998)
FEATURE [App::FeaturePython] Dimension533  # Draft dimension (typed FeaturePython)
  Dimline = (4800,15100,90.002)
  Direction = (0,0,0)
  Distance = 100
  End = (4800,15330,-100)
  Normal = (-1,0,0)
  Start = (4800,15330,0)
FEATURE [App::FeaturePython] Dimension534  # Draft dimension (typed FeaturePython)
  Dimline = (4800,15100,1050)
  Direction = (0,0,0)
  Distance = 609.998
  End = (4800,14719.9,1500)
  Normal = (-1,0,0)
  Start = (4800,15329.9,1500)
FEATURE [App::FeaturePython] Dimension535  # Draft dimension (typed FeaturePython)
  Dimline = (4800,14719.9,1050)
  Direction = (0,0,0)
  Distance = 599.999
  End = (4800,14119.9,1500)
  Normal = (-1,0,0)
  Start = (4800,14719.9,1500)
FEATURE [Part::Part2DObjectPython] Rectangle416  # Draft 2D object (typed FeaturePython)
  ChamferSize = 0
  FilletRadius = 0
  Height = 150
  Length = 150
  MakeFace = true
  Placement = pos=(4800,48238,5350) rot=(0.57735,-0.57735,0.57735;4.18879rad)
FEATURE [App::FeaturePython] Dimension536  # Draft dimension (typed FeaturePython)
  Dimline = (4800,8949.95,5350)
  Direction = (0,0,0)
  Distance = 1000
  End = (4800,8949.95,5200)
  Normal = (-1,0,0)
  Start = (4800,9949.95,5200)
FEATURE [App::FeaturePython] Dimension537  # Draft dimension (typed FeaturePython)
  Dimline = (4800,9949.95,5350)
  Direction = (0,0,0)
  Distance = 1000
  End = (4800,10297.2,5200)
  Normal = (-1,0,0)
  Start = (4800,11297.2,5200)
FEATURE [App::FeaturePython] Dimension538  # Draft dimension (typed FeaturePython)
  Dimline = (4800,8799.95,5200)
  Direction = (0,0,0)
  Distance = 1000
  End = (4800,9841.95,3000)
  Normal = (-1,0,0)
  Start = (4800,9842.39,4000)
FEATURE [App::FeaturePython] Dimension539  # Draft dimension (typed FeaturePython)
  Dimline = (4800,11541,3259)
  Direction = (0,0,0)
  Distance = 2830
  End = (4800,13020,3000)
  Normal = (-1,0,0)
  Start = (4800,15850,3000)
FEATURE [App::FeaturePython] Dimension540  # Draft dimension (typed FeaturePython)
  Dimline = (4800,15825,-400)
  Direction = (0,0,0)
  Distance = 200
  End = (4800,15825,-700)
  Normal = (-1,0,0)
  Start = (4800,16025,-700)
FEATURE [App::FeaturePython] Dimension541  # Draft dimension (typed FeaturePython)
  Dimline = (4800,15825,-400)
  Direction = (0,0,0)
  Distance = 200
  End = (4800,12845,-700)
  Normal = (-1,0,0)
  Start = (4800,13045,-700)
FEATURE [App::FeaturePython] Dimension542  # Draft dimension (typed FeaturePython)
  Dimline = (4800,15472,-1181)
  Direction = (0,0,0)
  Distance = 520
  End = (4800,15665,-960)
  Normal = (-1,0,0)
  Start = (4800,16185,-960)
FEATURE [App::FeaturePython] Dimension543  # Draft dimension (typed FeaturePython)
  Dimline = (4800,15665,-1181)
  Direction = (0,0,0)
  Distance = 520
  End = (4800,12685,-960)
  Normal = (-1,0,0)
  Start = (4800,13205,-960)
FEATURE [App::FeaturePython] Dimension544  # Draft dimension (typed FeaturePython)
  Dimline = (4800,4174.56,-400)
  Direction = (0,0,0)
  Distance = 200
  End = (4800,3974.56,-400)
  Normal = (-1,0,0)
  Start = (4800,4174.56,-400)
FEATURE [App::FeaturePython] Dimension545  # Draft dimension (typed FeaturePython)
  Dimline = (4800,2174.95,-400)
  Direction = (0,0,0)
  Distance = 200
  End = (4800,1974.95,-361.595)
  Normal = (-1,0,0)
  Start = (4800,2174.95,-361.595)
FEATURE [App::FeaturePython] Dimension546  # Draft dimension (typed FeaturePython)
  Dimline = (4800,12685,-1181)
  Direction = (0,0,0)
  Distance = 520
  End = (4800,3814.57,-960)
  Normal = (-1,0,0)
  Start = (4800,4334.57,-960)
FEATURE [App::FeaturePython] Dimension547  # Draft dimension (typed FeaturePython)
  Dimline = (4800,3814.57,-1181)
  Direction = (0,0,0)
  Distance = 520
  End = (4800,1814.95,-960)
  Normal = (-1,0,0)
  Start = (4800,2334.95,-960)
FEATURE [App::DocumentObjectGroup] Group080  label="Longitudinal section 3-Anno"
  Group = -> [Dimension479,Dimension480,Dimension481,Dimension482,Dimension483,Dimension484,Dimension485,Dimension486,Dimension487,Dimension488,Dimension489,Dimension490,Dimension491,Dimension492,Dimension493,Dimension494,Dimension495,Dimension496,Dimension497,Dimension499,Dimension500,Dimension501,Dimension502,Dimension503,Dimension504,Dimension505,Dimension506,Dimension507,Dimension508,Dimension509,+35 more]
FEATURE [App::DocumentObjectGroup] Group034  label="Annotation"
  Group = -> [Group035,Group039,Group045,Group077,Group079,Group080]
FEATURE [Part::Part2DObjectPython] Shape2DView029  # Draft 2D object (typed FeaturePython)
  Base = -> Section008
  HiddenLines = false
  Projection = (0,0,1)
  ProjectionMode = 2
  SegmentLength = 0.05
  Tessellation = false
FEATURE [Drawing::FeatureViewPython] ViewGroup080  # drawing view (typed FeaturePython)
  Direction = (-1,0,0)
  FillStyle = 0
  FontSize = 1.5
  LineStyle = 0
  LineWidth = 0.03
  Rotation = 90
  Scale = 0.01
  Source = -> Group080
  ViewResult = <blob: 59357 chars omitted>
  Visible = true
  X = 200
  Y = 280
FEATURE [Drawing::FeatureViewPython] View012  label="View of Section012"  # drawing view (typed FeaturePython)
  FontSize = 12
  LineWidth = 0.05
  RenderingMode = 1
  Rotation = 90
  Scale = 0.01
  ShowCut = false
  ShowFill = false
  Source = -> Section002
  ViewResult = <blob: 76058 chars omitted>
  Visible = true
  X = 220
  Y = 280
FEATURE [Drawing::FeaturePage] Page001  label="A0 Sheet"
  Group = -> [ViewGroup035001,ViewGroup039,View003,View004,Group041,Group042,Group046,View005,View,View006,View007,View009,View011,ViewGroup080,View012]
